# Revit family: Triple_CAVP_with_Mixing_Box
name_source: partatom
category: Mechanical Equipment
units: mm (PartAtom-declared; Revit-internal decimal feet)

## family parameters
Always vertical = Yes
Cut with Voids When Loaded = No
Part Type = Normal
Room Calculation Point = No
Round Connector Dimension = Use Diameter
Shared = No
Work Plane-Based = No

## types (227) — shared parameters
0 = 0"
1" = 1"
1.5 = 1 1/2"
10.1875 = 10 3/16"
135 = 135.00°
2" = 2"
2' = 24"
3" = 3"
4" = 4"
60 = 60.00°
8.1875 = 8 3/16"
85 = 85.00°
F-H = 2"
Manufacturer = Loren Cook Company
Model = Triple_CAVP_with_Mixing_Box
ONE EIGTH = 1/8"
Q = 1"
Q/2 = 1/2"
URL = www.lorencook.com

## per-type parameters (varying)
- Triple_120_CAVP-9L_CLASS_1_With_Mixing_Box: ((M - (2 * (D - L - K - J))) / 2) + (TRANSITION / 2)=9 7/32"; (B/2)+1.5"=9 9/16"; (B/2)-.125"=7 15/16"; (D-J-K-L)*2=2 1/16"; (E/2)-((B/2)+1.5")=3 25/32"; (E/2)-((MB_P/2)+.125")=-9/32"; (E/2)-(E/52*15)=5 21/32"; (F-((F-H)/2))/2=8 3/4"; (M - (2 * (D - L - K - J)))/2=4 11/16"; (MB_P/2)+.125"=13 5/8"; (MB_P/2-.125")+((F / 2) - 2")=-22 1/8"; (MB_P/2-.125")-((F / 2) - 2")=-4 5/8"; (MB_Q/2)+.125"=13 5/8"; (NOZZLE_HEIGHT - (NOZZLE_HEIGHT / 8 * 2)) / 2=10 1/2"; (NOZZLE_WB_OD - NOZZLE_TOP_OD) / 4=2 3/8"; -((MB_Q / 2) + 1/8")=-13 5/8"; -(F-((F-H)/2))/2=-8 3/4"; -MB_HEIGHT=-32"; -MB_P=-27"; -MB_P-.25=-27 1/4"; A=71"; A/2=35 1/2"; B=16 1/8"; B/2=8 1/16"; B/4=4 1/32"; C=43"; C/2=21 1/2"; CLASS=1"; D=32 13/16"; D-L-K-J=1 1/32"; D-M=21 3/8"; DUAL_Q=81 3/8"; DUAL_Q+.25"=81 5/8"; E=26 11/16"; E-(NOZZLE_RAD/3*2)=9 1/16"; E-N-N-H=-56 13/32"; E/2=13 11/32"; E/2-H/2=3 19/32"; E/52*15=7 11/16"; E/52*30=15 13/32"; F=21 1/2"; F/2=10 3/4"; H=19 1/2"; H/2=9 3/4"; HEIGHT=33 21/32"; J=6 1/2"; J+K+L=31 25/32"; K=11 7/8"; L=13 13/32"; M=11 7/16"; M-(2*(D-L-K-J))=9 3/8"; MB_A=89 11/16"; MB_F=9 1/8"; MB_F-3"=6 1/8"; MB_HEIGHT=32"; MB_HEIGHT/2=16"; MB_N=14 3/16"; MB_N-(D-J-K-L)=13 5/32"; MB_P=27"; MB_P+.25"=27 1/4"; MB_P+MB_P+.5=54 1/2"; MB_P-4.5"=22 1/2"; MB_Q=27"; N=60"; N+(H/2)=69 3/4"; NOZZLE_BOTTOM_ID=12 13/16"; NOZZLE_BOTTOM_RAD=6 13/32"; NOZZLE_BOTTOM_RAD-3*2=13/32"; NOZZLE_HEIGHT=28"; NOZZLE_HEIGHT/7*2=7"; NOZZLE_SIZE=9"; NOZZLE_TOP_OD=13 1/2"; NOZZLE_TOP_RAD=6 3/4"; NOZZLE_WB/4=4 19/32"; NOZZLE_WB_OD=23"; NOZZLE_WB_RAD=11 1/2"; NOZZLE_WB_RAD-2"=9 1/2"; P=60"; R=22"; R*1.1=24 3/16"; R+((B/2)+1.5")=31 9/16"; R-((B/2)+1.5")=12 7/16"; RO/2=11 1/4"; RO2/2=65 5/8"; TRANSITION=9 1/16"; TRANSITION/2=4 17/32"; TRIP_Q=135 3/4"; TRIP_Q-4.5"=131 1/4"; Type Comments=Triple Vari-Plume Laboratory Exhaust Centrifugal Airfoil Class 1 Arr 10 With Mixing Box
- Triple_120_CAVP-9H_CLASS_1_With_Mixing_Box: ((M - (2 * (D - L - K - J))) / 2) + (TRANSITION / 2)=9 7/32"; (B/2)+1.5"=9 9/16"; (B/2)-.125"=7 15/16"; (D-J-K-L)*2=2 1/16"; (E/2)-((B/2)+1.5")=3 25/32"; (E/2)-((MB_P/2)+.125")=-9/32"; (E/2)-(E/52*15)=5 21/32"; (F-((F-H)/2))/2=8 3/4"; (M - (2 * (D - L - K - J)))/2=4 11/16"; (MB_P/2)+.125"=13 5/8"; (MB_P/2-.125")+((F / 2) - 2")=-22 1/8"; (MB_P/2-.125")-((F / 2) - 2")=-4 5/8"; (MB_Q/2)+.125"=13 5/8"; (NOZZLE_HEIGHT - (NOZZLE_HEIGHT / 8 * 2)) / 2=10 1/2"; (NOZZLE_WB_OD - NOZZLE_TOP_OD) / 4=2 3/8"; -((MB_Q / 2) + 1/8")=-13 5/8"; -(F-((F-H)/2))/2=-8 3/4"; -MB_HEIGHT=-32"; -MB_P=-27"; -MB_P-.25=-27 1/4"; A=71"; A/2=35 1/2"; B=16 1/8"; B/2=8 1/16"; B/4=4 1/32"; C=43"; C/2=21 1/2"; CLASS=1"; D=32 13/16"; D-L-K-J=1 1/32"; D-M=21 3/8"; DUAL_Q=81 3/8"; DUAL_Q+.25"=81 5/8"; E=26 11/16"; E-(NOZZLE_RAD/3*2)=9 1/16"; E-N-N-H=-56 13/32"; E/2=13 11/32"; E/2-H/2=3 19/32"; E/52*15=7 11/16"; E/52*30=15 13/32"; F=21 1/2"; F/2=10 3/4"; H=19 1/2"; H/2=9 3/4"; HEIGHT=33 21/32"; J=6 1/2"; J+K+L=31 25/32"; K=11 7/8"; L=13 13/32"; M=11 7/16"; M-(2*(D-L-K-J))=9 3/8"; MB_A=89 11/16"; MB_F=9 1/8"; MB_F-3"=6 1/8"; MB_HEIGHT=32"; MB_HEIGHT/2=16"; MB_N=14 3/16"; MB_N-(D-J-K-L)=13 5/32"; MB_P=27"; MB_P+.25"=27 1/4"; MB_P+MB_P+.5=54 1/2"; MB_P-4.5"=22 1/2"; MB_Q=27"; N=60"; N+(H/2)=69 3/4"; NOZZLE_BOTTOM_ID=12 13/16"; NOZZLE_BOTTOM_RAD=6 13/32"; NOZZLE_BOTTOM_RAD-3*2=13/32"; NOZZLE_HEIGHT=28"; NOZZLE_HEIGHT/7*2=7"; NOZZLE_SIZE=9"; NOZZLE_TOP_OD=13 1/2"; NOZZLE_TOP_RAD=6 3/4"; NOZZLE_WB/4=4 19/32"; NOZZLE_WB_OD=23"; NOZZLE_WB_RAD=11 1/2"; NOZZLE_WB_RAD-2"=9 1/2"; P=60"; R=22"; R*1.1=24 3/16"; R+((B/2)+1.5")=31 9/16"; R-((B/2)+1.5")=12 7/16"; RO/2=11 1/4"; RO2/2=65 5/8"; TRANSITION=9 1/16"; TRANSITION/2=4 17/32"; TRIP_Q=135 3/4"; TRIP_Q-4.5"=131 1/4"; Type Comments=Triple Vari-Plume Laboratory Exhaust Centrifugal Airfoil Class 1 Arr 10 With Mixing Box
- Triple_120_CAVP-9L_CLASS_2_With_Mixing_Box: ((M - (2 * (D - L - K - J))) / 2) + (TRANSITION / 2)=8 15/32"; (B/2)+1.5"=9 9/16"; (B/2)-.125"=7 15/16"; (D-J-K-L)*2=3 9/16"; (E/2)-((B/2)+1.5")=3 25/32"; (E/2)-((MB_P/2)+.125")=-9/32"; (E/2)-(E/52*15)=5 21/32"; (F-((F-H)/2))/2=8 3/4"; (M - (2 * (D - L - K - J)))/2=3 15/16"; (MB_P/2)+.125"=13 5/8"; (MB_P/2-.125")+((F / 2) - 2")=-22 1/8"; (MB_P/2-.125")-((F / 2) - 2")=-4 5/8"; (MB_Q/2)+.125"=13 5/8"; (NOZZLE_HEIGHT - (NOZZLE_HEIGHT / 8 * 2)) / 2=10 1/2"; (NOZZLE_WB_OD - NOZZLE_TOP_OD) / 4=2 3/8"; -((MB_Q / 2) + 1/8")=-13 5/8"; -(F-((F-H)/2))/2=-8 3/4"; -MB_HEIGHT=-32"; -MB_P=-27"; -MB_P-.25=-27 1/4"; A=71"; A/2=35 1/2"; B=16 1/8"; B/2=8 1/16"; B/4=4 1/32"; C=43"; C/2=21 1/2"; CLASS=2"; D=36 13/16"; D-L-K-J=1 25/32"; D-M=25 3/8"; DUAL_Q=81 3/8"; DUAL_Q+.25"=81 5/8"; E=26 11/16"; E-(NOZZLE_RAD/3*2)=9 1/16"; E-N-N-H=-56 13/32"; E/2=13 11/32"; E/2-H/2=3 19/32"; E/52*15=7 11/16"; E/52*30=15 13/32"; F=21 1/2"; F/2=10 3/4"; H=19 1/2"; H/2=9 3/4"; HEIGHT=33 21/32"; J=6 1/4"; J+K+L=35 1/32"; K=15 3/8"; L=13 13/32"; M=11 7/16"; M-(2*(D-L-K-J))=7 7/8"; MB_A=86 7/16"; MB_F=9 1/8"; MB_F-3"=6 1/8"; MB_HEIGHT=32"; MB_HEIGHT/2=16"; MB_N=14 3/16"; MB_N-(D-J-K-L)=12 13/32"; MB_P=27"; MB_P+.25"=27 1/4"; MB_P+MB_P+.5=54 1/2"; MB_P-4.5"=22 1/2"; MB_Q=27"; N=60"; N+(H/2)=69 3/4"; NOZZLE_BOTTOM_ID=12 13/16"; NOZZLE_BOTTOM_RAD=6 13/32"; NOZZLE_BOTTOM_RAD-3*2=13/32"; NOZZLE_HEIGHT=28"; NOZZLE_HEIGHT/7*2=7"; NOZZLE_SIZE=9"; NOZZLE_TOP_OD=13 1/2"; NOZZLE_TOP_RAD=6 3/4"; NOZZLE_WB/4=4 19/32"; NOZZLE_WB_OD=23"; NOZZLE_WB_RAD=11 1/2"; NOZZLE_WB_RAD-2"=9 1/2"; P=60"; R=22"; R*1.1=24 3/16"; R+((B/2)+1.5")=31 9/16"; R-((B/2)+1.5")=12 7/16"; RO/2=11 1/4"; RO2/2=65 5/8"; TRANSITION=9 1/16"; TRANSITION/2=4 17/32"; TRIP_Q=135 3/4"; TRIP_Q-4.5"=131 1/4"; Type Comments=Triple Vari-Plume Laboratory Exhaust Centrifugal Airfoil Class 2 Arr 10 With Mixing Box
- Triple_120_CAVP-9H_CLASS_2_With_Mixing_Box: ((M - (2 * (D - L - K - J))) / 2) + (TRANSITION / 2)=8 15/32"; (B/2)+1.5"=9 9/16"; (B/2)-.125"=7 15/16"; (D-J-K-L)*2=3 9/16"; (E/2)-((B/2)+1.5")=3 25/32"; (E/2)-((MB_P/2)+.125")=-9/32"; (E/2)-(E/52*15)=5 21/32"; (F-((F-H)/2))/2=8 3/4"; (M - (2 * (D - L - K - J)))/2=3 15/16"; (MB_P/2)+.125"=13 5/8"; (MB_P/2-.125")+((F / 2) - 2")=-22 1/8"; (MB_P/2-.125")-((F / 2) - 2")=-4 5/8"; (MB_Q/2)+.125"=13 5/8"; (NOZZLE_HEIGHT - (NOZZLE_HEIGHT / 8 * 2)) / 2=10 1/2"; (NOZZLE_WB_OD - NOZZLE_TOP_OD) / 4=2 3/8"; -((MB_Q / 2) + 1/8")=-13 5/8"; -(F-((F-H)/2))/2=-8 3/4"; -MB_HEIGHT=-32"; -MB_P=-27"; -MB_P-.25=-27 1/4"; A=71"; A/2=35 1/2"; B=16 1/8"; B/2=8 1/16"; B/4=4 1/32"; C=43"; C/2=21 1/2"; CLASS=2"; D=36 13/16"; D-L-K-J=1 25/32"; D-M=25 3/8"; DUAL_Q=81 3/8"; DUAL_Q+.25"=81 5/8"; E=26 11/16"; E-(NOZZLE_RAD/3*2)=9 1/16"; E-N-N-H=-56 13/32"; E/2=13 11/32"; E/2-H/2=3 19/32"; E/52*15=7 11/16"; E/52*30=15 13/32"; F=21 1/2"; F/2=10 3/4"; H=19 1/2"; H/2=9 3/4"; HEIGHT=33 21/32"; J=6 1/4"; J+K+L=35 1/32"; K=15 3/8"; L=13 13/32"; M=11 7/16"; M-(2*(D-L-K-J))=7 7/8"; MB_A=86 7/16"; MB_F=9 1/8"; MB_F-3"=6 1/8"; MB_HEIGHT=32"; MB_HEIGHT/2=16"; MB_N=14 3/16"; MB_N-(D-J-K-L)=12 13/32"; MB_P=27"; MB_P+.25"=27 1/4"; MB_P+MB_P+.5=54 1/2"; MB_P-4.5"=22 1/2"; MB_Q=27"; N=60"; N+(H/2)=69 3/4"; NOZZLE_BOTTOM_ID=12 13/16"; NOZZLE_BOTTOM_RAD=6 13/32"; NOZZLE_BOTTOM_RAD-3*2=13/32"; NOZZLE_HEIGHT=28"; NOZZLE_HEIGHT/7*2=7"; NOZZLE_SIZE=9"; NOZZLE_TOP_OD=13 1/2"; NOZZLE_TOP_RAD=6 3/4"; NOZZLE_WB/4=4 19/32"; NOZZLE_WB_OD=23"; NOZZLE_WB_RAD=11 1/2"; NOZZLE_WB_RAD-2"=9 1/2"; P=60"; R=22"; R*1.1=24 3/16"; R+((B/2)+1.5")=31 9/16"; R-((B/2)+1.5")=12 7/16"; RO/2=11 1/4"; RO2/2=65 5/8"; TRANSITION=9 1/16"; TRANSITION/2=4 17/32"; TRIP_Q=135 3/4"; TRIP_Q-4.5"=131 1/4"; Type Comments=Triple Vari-Plume Laboratory Exhaust Centrifugal Airfoil Class 2 Arr 10 With Mixing Box
- Triple_135_CAVP-9L_CLASS_1_With_Mixing_Box: ((M - (2 * (D - L - K - J))) / 2) + (TRANSITION / 2)=9 25/32"; (B/2)+1.5"=10 5/16"; (B/2)-.125"=8 11/16"; (D-J-K-L)*2=2 1/16"; (E/2)-((B/2)+1.5")=4 19/32"; (E/2)-((MB_P/2)+.125")=9/32"; (E/2)-(E/52*15)=6 5/16"; (F-((F-H)/2))/2=8 3/4"; (M - (2 * (D - L - K - J)))/2=5 1/4"; (MB_P/2)+.125"=14 5/8"; (MB_P/2-.125")+((F / 2) - 2")=-23 1/8"; (MB_P/2-.125")-((F / 2) - 2")=-5 5/8"; (MB_Q/2)+.125"=14 5/8"; (NOZZLE_HEIGHT - (NOZZLE_HEIGHT / 8 * 2)) / 2=10 1/2"; (NOZZLE_WB_OD - NOZZLE_TOP_OD) / 4=2 3/8"; -((MB_Q / 2) + 1/8")=-14 5/8"; -(F-((F-H)/2))/2=-8 3/4"; -MB_HEIGHT=-33 1/2"; -MB_P=-29"; -MB_P-.25=-29 1/4"; A=73 11/16"; A/2=36 27/32"; B=17 5/8"; B/2=8 13/16"; B/4=4 13/32"; C=45 11/16"; C/2=22 27/32"; CLASS=1"; D=34 5/16"; D-L-K-J=1 1/32"; D-M=21 3/4"; DUAL_Q=87 3/8"; DUAL_Q+.25"=87 5/8"; E=29 13/16"; E-(NOZZLE_RAD/3*2)=10 5/8"; E-N-N-H=-54 27/32"; E/2=14 29/32"; E/2-H/2=5 5/32"; E/52*15=8 19/32"; E/52*30=17 3/16"; F=21 1/2"; F/2=10 3/4"; H=19 1/2"; H/2=9 3/4"; HEIGHT=35 1/32"; J=6 1/2"; J+K+L=33 9/32"; K=12 1/4"; L=14 17/32"; M=12 9/16"; M-(2*(D-L-K-J))=10 1/2"; MB_A=90 13/16"; MB_F=8 3/8"; MB_F-3"=5 3/8"; MB_HEIGHT=33 1/2"; MB_HEIGHT/2=16 3/4"; MB_N=14 3/16"; MB_N-(D-J-K-L)=13 5/32"; MB_P=29"; MB_P+.25"=29 1/4"; MB_P+MB_P+.5=58 1/2"; MB_P-4.5"=24 1/2"; MB_Q=29"; N=60"; N+(H/2)=69 3/4"; NOZZLE_BOTTOM_ID=12 13/16"; NOZZLE_BOTTOM_RAD=6 13/32"; NOZZLE_BOTTOM_RAD-3*2=13/32"; NOZZLE_HEIGHT=28"; NOZZLE_HEIGHT/7*2=7"; NOZZLE_SIZE=9"; NOZZLE_TOP_OD=13 1/2"; NOZZLE_TOP_RAD=6 3/4"; NOZZLE_WB/4=4 19/32"; NOZZLE_WB_OD=23"; NOZZLE_WB_RAD=11 1/2"; NOZZLE_WB_RAD-2"=9 1/2"; P=60"; R=22"; R*1.1=24 3/16"; R+((B/2)+1.5")=32 5/16"; R-((B/2)+1.5")=11 11/16"; RO/2=12 1/4"; RO2/2=70 5/8"; TRANSITION=9 1/16"; TRANSITION/2=4 17/32"; TRIP_Q=145 3/4"; TRIP_Q-4.5"=141 1/4"; Type Comments=Triple Vari-Plume Laboratory Exhaust Centrifugal Airfoil Class 1 Arr 10 With Mixing Box
- Triple_135_CAVP-9H_CLASS_1_With_Mixing_Box: ((M - (2 * (D - L - K - J))) / 2) + (TRANSITION / 2)=9 25/32"; (B/2)+1.5"=10 5/16"; (B/2)-.125"=8 11/16"; (D-J-K-L)*2=2 1/16"; (E/2)-((B/2)+1.5")=4 19/32"; (E/2)-((MB_P/2)+.125")=9/32"; (E/2)-(E/52*15)=6 5/16"; (F-((F-H)/2))/2=8 3/4"; (M - (2 * (D - L - K - J)))/2=5 1/4"; (MB_P/2)+.125"=14 5/8"; (MB_P/2-.125")+((F / 2) - 2")=-23 1/8"; (MB_P/2-.125")-((F / 2) - 2")=-5 5/8"; (MB_Q/2)+.125"=14 5/8"; (NOZZLE_HEIGHT - (NOZZLE_HEIGHT / 8 * 2)) / 2=10 1/2"; (NOZZLE_WB_OD - NOZZLE_TOP_OD) / 4=2 3/8"; -((MB_Q / 2) + 1/8")=-14 5/8"; -(F-((F-H)/2))/2=-8 3/4"; -MB_HEIGHT=-33 1/2"; -MB_P=-29"; -MB_P-.25=-29 1/4"; A=73 11/16"; A/2=36 27/32"; B=17 5/8"; B/2=8 13/16"; B/4=4 13/32"; C=45 11/16"; C/2=22 27/32"; CLASS=1"; D=34 5/16"; D-L-K-J=1 1/32"; D-M=21 3/4"; DUAL_Q=87 3/8"; DUAL_Q+.25"=87 5/8"; E=29 13/16"; E-(NOZZLE_RAD/3*2)=10 5/8"; E-N-N-H=-54 27/32"; E/2=14 29/32"; E/2-H/2=5 5/32"; E/52*15=8 19/32"; E/52*30=17 3/16"; F=21 1/2"; F/2=10 3/4"; H=19 1/2"; H/2=9 3/4"; HEIGHT=35 1/32"; J=6 1/2"; J+K+L=33 9/32"; K=12 1/4"; L=14 17/32"; M=12 9/16"; M-(2*(D-L-K-J))=10 1/2"; MB_A=90 13/16"; MB_F=8 3/8"; MB_F-3"=5 3/8"; MB_HEIGHT=33 1/2"; MB_HEIGHT/2=16 3/4"; MB_N=14 3/16"; MB_N-(D-J-K-L)=13 5/32"; MB_P=29"; MB_P+.25"=29 1/4"; MB_P+MB_P+.5=58 1/2"; MB_P-4.5"=24 1/2"; MB_Q=29"; N=60"; N+(H/2)=69 3/4"; NOZZLE_BOTTOM_ID=12 13/16"; NOZZLE_BOTTOM_RAD=6 13/32"; NOZZLE_BOTTOM_RAD-3*2=13/32"; NOZZLE_HEIGHT=28"; NOZZLE_HEIGHT/7*2=7"; NOZZLE_SIZE=9"; NOZZLE_TOP_OD=13 1/2"; NOZZLE_TOP_RAD=6 3/4"; NOZZLE_WB/4=4 19/32"; NOZZLE_WB_OD=23"; NOZZLE_WB_RAD=11 1/2"; NOZZLE_WB_RAD-2"=9 1/2"; P=60"; R=22"; R*1.1=24 3/16"; R+((B/2)+1.5")=32 5/16"; R-((B/2)+1.5")=11 11/16"; RO/2=12 1/4"; RO2/2=70 5/8"; TRANSITION=9 1/16"; TRANSITION/2=4 17/32"; TRIP_Q=145 3/4"; TRIP_Q-4.5"=141 1/4"; Type Comments=Triple Vari-Plume Laboratory Exhaust Centrifugal Airfoil Class 1 Arr 10 With Mixing Box
- Triple_135_CAVP-9L_CLASS_2_With_Mixing_Box: ((M - (2 * (D - L - K - J))) / 2) + (TRANSITION / 2)=9 25/32"; (B/2)+1.5"=10 5/16"; (B/2)-.125"=8 11/16"; (D-J-K-L)*2=2 1/16"; (E/2)-((B/2)+1.5")=4 19/32"; (E/2)-((MB_P/2)+.125")=9/32"; (E/2)-(E/52*15)=6 5/16"; (F-((F-H)/2))/2=8 3/4"; (M - (2 * (D - L - K - J)))/2=5 1/4"; (MB_P/2)+.125"=14 5/8"; (MB_P/2-.125")+((F / 2) - 2")=-23 1/8"; (MB_P/2-.125")-((F / 2) - 2")=-5 5/8"; (MB_Q/2)+.125"=14 5/8"; (NOZZLE_HEIGHT - (NOZZLE_HEIGHT / 8 * 2)) / 2=10 1/2"; (NOZZLE_WB_OD - NOZZLE_TOP_OD) / 4=2 3/8"; -((MB_Q / 2) + 1/8")=-14 5/8"; -(F-((F-H)/2))/2=-8 3/4"; -MB_HEIGHT=-33 1/2"; -MB_P=-29"; -MB_P-.25=-29 1/4"; A=73 11/16"; A/2=36 27/32"; B=17 5/8"; B/2=8 13/16"; B/4=4 13/32"; C=45 11/16"; C/2=22 27/32"; CLASS=2"; D=37 3/16"; D-L-K-J=1 1/32"; D-M=24 5/8"; DUAL_Q=87 3/8"; DUAL_Q+.25"=87 5/8"; E=29 13/16"; E-(NOZZLE_RAD/3*2)=10 5/8"; E-N-N-H=-54 27/32"; E/2=14 29/32"; E/2-H/2=5 5/32"; E/52*15=8 19/32"; E/52*30=17 3/16"; F=21 1/2"; F/2=10 3/4"; H=19 1/2"; H/2=9 3/4"; HEIGHT=35 1/32"; J=6 1/4"; J+K+L=36 5/32"; K=15 3/8"; L=14 17/32"; M=12 9/16"; M-(2*(D-L-K-J))=10 1/2"; MB_A=93 11/16"; MB_F=8 3/8"; MB_F-3"=5 3/8"; MB_HEIGHT=33 1/2"; MB_HEIGHT/2=16 3/4"; MB_N=14 3/16"; MB_N-(D-J-K-L)=13 5/32"; MB_P=29"; MB_P+.25"=29 1/4"; MB_P+MB_P+.5=58 1/2"; MB_P-4.5"=24 1/2"; MB_Q=29"; N=60"; N+(H/2)=69 3/4"; NOZZLE_BOTTOM_ID=12 13/16"; NOZZLE_BOTTOM_RAD=6 13/32"; NOZZLE_BOTTOM_RAD-3*2=13/32"; NOZZLE_HEIGHT=28"; NOZZLE_HEIGHT/7*2=7"; NOZZLE_SIZE=9"; NOZZLE_TOP_OD=13 1/2"; NOZZLE_TOP_RAD=6 3/4"; NOZZLE_WB/4=4 19/32"; NOZZLE_WB_OD=23"; NOZZLE_WB_RAD=11 1/2"; NOZZLE_WB_RAD-2"=9 1/2"; P=60"; R=22"; R*1.1=24 3/16"; R+((B/2)+1.5")=32 5/16"; R-((B/2)+1.5")=11 11/16"; RO/2=12 1/4"; RO2/2=70 5/8"; TRANSITION=9 1/16"; TRANSITION/2=4 17/32"; TRIP_Q=145 3/4"; TRIP_Q-4.5"=141 1/4"; Type Comments=Triple Vari-Plume Laboratory Exhaust Centrifugal Airfoil Class 2 Arr 10 With Mixing Box
- Triple_135_CAVP-9H_CLASS_2_With_Mixing_Box: ((M - (2 * (D - L - K - J))) / 2) + (TRANSITION / 2)=9 25/32"; (B/2)+1.5"=10 5/16"; (B/2)-.125"=8 11/16"; (D-J-K-L)*2=2 1/16"; (E/2)-((B/2)+1.5")=4 19/32"; (E/2)-((MB_P/2)+.125")=9/32"; (E/2)-(E/52*15)=6 5/16"; (F-((F-H)/2))/2=8 3/4"; (M - (2 * (D - L - K - J)))/2=5 1/4"; (MB_P/2)+.125"=14 5/8"; (MB_P/2-.125")+((F / 2) - 2")=-23 1/8"; (MB_P/2-.125")-((F / 2) - 2")=-5 5/8"; (MB_Q/2)+.125"=14 5/8"; (NOZZLE_HEIGHT - (NOZZLE_HEIGHT / 8 * 2)) / 2=10 1/2"; (NOZZLE_WB_OD - NOZZLE_TOP_OD) / 4=2 3/8"; -((MB_Q / 2) + 1/8")=-14 5/8"; -(F-((F-H)/2))/2=-8 3/4"; -MB_HEIGHT=-33 1/2"; -MB_P=-29"; -MB_P-.25=-29 1/4"; A=73 11/16"; A/2=36 27/32"; B=17 5/8"; B/2=8 13/16"; B/4=4 13/32"; C=45 11/16"; C/2=22 27/32"; CLASS=2"; D=37 3/16"; D-L-K-J=1 1/32"; D-M=24 5/8"; DUAL_Q=87 3/8"; DUAL_Q+.25"=87 5/8"; E=29 13/16"; E-(NOZZLE_RAD/3*2)=10 5/8"; E-N-N-H=-54 27/32"; E/2=14 29/32"; E/2-H/2=5 5/32"; E/52*15=8 19/32"; E/52*30=17 3/16"; F=21 1/2"; F/2=10 3/4"; H=19 1/2"; H/2=9 3/4"; HEIGHT=35 1/32"; J=6 1/4"; J+K+L=36 5/32"; K=15 3/8"; L=14 17/32"; M=12 9/16"; M-(2*(D-L-K-J))=10 1/2"; MB_A=93 11/16"; MB_F=8 3/8"; MB_F-3"=5 3/8"; MB_HEIGHT=33 1/2"; MB_HEIGHT/2=16 3/4"; MB_N=14 3/16"; MB_N-(D-J-K-L)=13 5/32"; MB_P=29"; MB_P+.25"=29 1/4"; MB_P+MB_P+.5=58 1/2"; MB_P-4.5"=24 1/2"; MB_Q=29"; N=60"; N+(H/2)=69 3/4"; NOZZLE_BOTTOM_ID=12 13/16"; NOZZLE_BOTTOM_RAD=6 13/32"; NOZZLE_BOTTOM_RAD-3*2=13/32"; NOZZLE_HEIGHT=28"; NOZZLE_HEIGHT/7*2=7"; NOZZLE_SIZE=9"; NOZZLE_TOP_OD=13 1/2"; NOZZLE_TOP_RAD=6 3/4"; NOZZLE_WB/4=4 19/32"; NOZZLE_WB_OD=23"; NOZZLE_WB_RAD=11 1/2"; NOZZLE_WB_RAD-2"=9 1/2"; P=60"; R=22"; R*1.1=24 3/16"; R+((B/2)+1.5")=32 5/16"; R-((B/2)+1.5")=11 11/16"; RO/2=12 1/4"; RO2/2=70 5/8"; TRANSITION=9 1/16"; TRANSITION/2=4 17/32"; TRIP_Q=145 3/4"; TRIP_Q-4.5"=141 1/4"; Type Comments=Triple Vari-Plume Laboratory Exhaust Centrifugal Airfoil Class 2 Arr 10 With Mixing Box
- Triple_150_CAVP-9L_CLASS_1_With_Mixing_Box: ((M - (2 * (D - L - K - J))) / 2) + (TRANSITION / 2)=10 11/32"; (B/2)+1.5"=11 1/16"; (B/2)-.125"=9 7/16"; (D-J-K-L)*2=2 1/16"; (E/2)-((B/2)+1.5")=5 3/8"; (E/2)-((MB_P/2)+.125")=1 5/16"; (E/2)-(E/52*15)=6 31/32"; (F-((F-H)/2))/2=8 3/4"; (M - (2 * (D - L - K - J)))/2=5 13/16"; (MB_P/2)+.125"=15 1/8"; (MB_P/2-.125")+((F / 2) - 2")=-23 5/8"; (MB_P/2-.125")-((F / 2) - 2")=-6 1/8"; (MB_Q/2)+.125"=15 1/8"; (NOZZLE_HEIGHT - (NOZZLE_HEIGHT / 8 * 2)) / 2=10 1/2"; (NOZZLE_WB_OD - NOZZLE_TOP_OD) / 4=2 3/8"; -((MB_Q / 2) + 1/8")=-15 1/8"; -(F-((F-H)/2))/2=-8 3/4"; -MB_HEIGHT=-35"; -MB_P=-30"; -MB_P-.25=-30 1/4"; A=78"; A/2=39"; B=19 1/8"; B/2=9 9/16"; B/4=4 25/32"; C=46 3/4"; C/2=23 3/8"; CLASS=1"; D=35 7/16"; D-L-K-J=1 1/32"; D-M=21 3/4"; DUAL_Q=90 3/8"; DUAL_Q+.25"=90 5/8"; E=32 7/8"; E-(NOZZLE_RAD/3*2)=12 5/32"; E-N-N-H=-53 5/16"; E/2=16 7/16"; E/2-H/2=6 11/16"; E/52*15=9 15/32"; E/52*30=18 31/32"; F=21 1/2"; F/2=10 3/4"; H=19 1/2"; H/2=9 3/4"; HEIGHT=36 11/32"; J=6 1/2"; J+K+L=34 13/32"; K=12 1/4"; L=15 21/32"; M=13 11/16"; M-(2*(D-L-K-J))=11 5/8"; MB_A=94 3/16"; MB_F=7 5/8"; MB_F-3"=4 5/8"; MB_HEIGHT=35"; MB_HEIGHT/2=17 1/2"; MB_N=14 3/16"; MB_N-(D-J-K-L)=13 5/32"; MB_P=30"; MB_P+.25"=30 1/4"; MB_P+MB_P+.5=60 1/2"; MB_P-4.5"=25 1/2"; MB_Q=30"; N=60"; N+(H/2)=69 3/4"; NOZZLE_BOTTOM_ID=12 13/16"; NOZZLE_BOTTOM_RAD=6 13/32"; NOZZLE_BOTTOM_RAD-3*2=13/32"; NOZZLE_HEIGHT=28"; NOZZLE_HEIGHT/7*2=7"; NOZZLE_SIZE=9"; NOZZLE_TOP_OD=13 1/2"; NOZZLE_TOP_RAD=6 3/4"; NOZZLE_WB/4=4 19/32"; NOZZLE_WB_OD=23"; NOZZLE_WB_RAD=11 1/2"; NOZZLE_WB_RAD-2"=9 1/2"; P=60"; R=22"; R*1.1=24 3/16"; R+((B/2)+1.5")=33 1/16"; R-((B/2)+1.5")=10 15/16"; RO/2=12 3/4"; RO2/2=73 1/8"; TRANSITION=9 1/16"; TRANSITION/2=4 17/32"; TRIP_Q=150 3/4"; TRIP_Q-4.5"=146 1/4"; Type Comments=Triple Vari-Plume Laboratory Exhaust Centrifugal Airfoil Class 1 Arr 10 With Mixing Box
- Triple_150_CAVP-9H_CLASS_1_With_Mixing_Box: ((M - (2 * (D - L - K - J))) / 2) + (TRANSITION / 2)=10 11/32"; (B/2)+1.5"=11 1/16"; (B/2)-.125"=9 7/16"; (D-J-K-L)*2=2 1/16"; (E/2)-((B/2)+1.5")=5 3/8"; (E/2)-((MB_P/2)+.125")=1 5/16"; (E/2)-(E/52*15)=6 31/32"; (F-((F-H)/2))/2=8 3/4"; (M - (2 * (D - L - K - J)))/2=5 13/16"; (MB_P/2)+.125"=15 1/8"; (MB_P/2-.125")+((F / 2) - 2")=-23 5/8"; (MB_P/2-.125")-((F / 2) - 2")=-6 1/8"; (MB_Q/2)+.125"=15 1/8"; (NOZZLE_HEIGHT - (NOZZLE_HEIGHT / 8 * 2)) / 2=10 1/2"; (NOZZLE_WB_OD - NOZZLE_TOP_OD) / 4=2 3/8"; -((MB_Q / 2) + 1/8")=-15 1/8"; -(F-((F-H)/2))/2=-8 3/4"; -MB_HEIGHT=-35"; -MB_P=-30"; -MB_P-.25=-30 1/4"; A=78"; A/2=39"; B=19 1/8"; B/2=9 9/16"; B/4=4 25/32"; C=46 3/4"; C/2=23 3/8"; CLASS=1"; D=35 7/16"; D-L-K-J=1 1/32"; D-M=21 3/4"; DUAL_Q=90 3/8"; DUAL_Q+.25"=90 5/8"; E=32 7/8"; E-(NOZZLE_RAD/3*2)=12 5/32"; E-N-N-H=-53 5/16"; E/2=16 7/16"; E/2-H/2=6 11/16"; E/52*15=9 15/32"; E/52*30=18 31/32"; F=21 1/2"; F/2=10 3/4"; H=19 1/2"; H/2=9 3/4"; HEIGHT=36 11/32"; J=6 1/2"; J+K+L=34 13/32"; K=12 1/4"; L=15 21/32"; M=13 11/16"; M-(2*(D-L-K-J))=11 5/8"; MB_A=94 3/16"; MB_F=7 5/8"; MB_F-3"=4 5/8"; MB_HEIGHT=35"; MB_HEIGHT/2=17 1/2"; MB_N=14 3/16"; MB_N-(D-J-K-L)=13 5/32"; MB_P=30"; MB_P+.25"=30 1/4"; MB_P+MB_P+.5=60 1/2"; MB_P-4.5"=25 1/2"; MB_Q=30"; N=60"; N+(H/2)=69 3/4"; NOZZLE_BOTTOM_ID=12 13/16"; NOZZLE_BOTTOM_RAD=6 13/32"; NOZZLE_BOTTOM_RAD-3*2=13/32"; NOZZLE_HEIGHT=28"; NOZZLE_HEIGHT/7*2=7"; NOZZLE_SIZE=9"; NOZZLE_TOP_OD=13 1/2"; NOZZLE_TOP_RAD=6 3/4"; NOZZLE_WB/4=4 19/32"; NOZZLE_WB_OD=23"; NOZZLE_WB_RAD=11 1/2"; NOZZLE_WB_RAD-2"=9 1/2"; P=60"; R=22"; R*1.1=24 3/16"; R+((B/2)+1.5")=33 1/16"; R-((B/2)+1.5")=10 15/16"; RO/2=12 3/4"; RO2/2=73 1/8"; TRANSITION=9 1/16"; TRANSITION/2=4 17/32"; TRIP_Q=150 3/4"; TRIP_Q-4.5"=146 1/4"; Type Comments=Triple Vari-Plume Laboratory Exhaust Centrifugal Airfoil Class 1 Arr 10 With Mixing Box
- Triple_150_CAVP-9L_CLASS_2_With_Mixing_Box: ((M - (2 * (D - L - K - J))) / 2) + (TRANSITION / 2)=10 11/32"; (B/2)+1.5"=11 1/16"; (B/2)-.125"=9 7/16"; (D-J-K-L)*2=2 1/16"; (E/2)-((B/2)+1.5")=5 3/8"; (E/2)-((MB_P/2)+.125")=1 5/16"; (E/2)-(E/52*15)=6 31/32"; (F-((F-H)/2))/2=8 3/4"; (M - (2 * (D - L - K - J)))/2=5 13/16"; (MB_P/2)+.125"=15 1/8"; (MB_P/2-.125")+((F / 2) - 2")=-23 5/8"; (MB_P/2-.125")-((F / 2) - 2")=-6 1/8"; (MB_Q/2)+.125"=15 1/8"; (NOZZLE_HEIGHT - (NOZZLE_HEIGHT / 8 * 2)) / 2=10 1/2"; (NOZZLE_WB_OD - NOZZLE_TOP_OD) / 4=2 3/8"; -((MB_Q / 2) + 1/8")=-15 1/8"; -(F-((F-H)/2))/2=-8 3/4"; -MB_HEIGHT=-35"; -MB_P=-30"; -MB_P-.25=-30 1/4"; A=78"; A/2=39"; B=19 1/8"; B/2=9 9/16"; B/4=4 25/32"; C=46 3/4"; C/2=23 3/8"; CLASS=2"; D=38 5/16"; D-L-K-J=1 1/32"; D-M=24 5/8"; DUAL_Q=90 3/8"; DUAL_Q+.25"=90 5/8"; E=32 7/8"; E-(NOZZLE_RAD/3*2)=12 5/32"; E-N-N-H=-53 5/16"; E/2=16 7/16"; E/2-H/2=6 11/16"; E/52*15=9 15/32"; E/52*30=18 31/32"; F=21 1/2"; F/2=10 3/4"; H=19 1/2"; H/2=9 3/4"; HEIGHT=36 11/32"; J=6 1/4"; J+K+L=37 9/32"; K=15 3/8"; L=15 21/32"; M=13 11/16"; M-(2*(D-L-K-J))=11 5/8"; MB_A=97 1/16"; MB_F=7 5/8"; MB_F-3"=4 5/8"; MB_HEIGHT=35"; MB_HEIGHT/2=17 1/2"; MB_N=14 3/16"; MB_N-(D-J-K-L)=13 5/32"; MB_P=30"; MB_P+.25"=30 1/4"; MB_P+MB_P+.5=60 1/2"; MB_P-4.5"=25 1/2"; MB_Q=30"; N=60"; N+(H/2)=69 3/4"; NOZZLE_BOTTOM_ID=12 13/16"; NOZZLE_BOTTOM_RAD=6 13/32"; NOZZLE_BOTTOM_RAD-3*2=13/32"; NOZZLE_HEIGHT=28"; NOZZLE_HEIGHT/7*2=7"; NOZZLE_SIZE=9"; NOZZLE_TOP_OD=13 1/2"; NOZZLE_TOP_RAD=6 3/4"; NOZZLE_WB/4=4 19/32"; NOZZLE_WB_OD=23"; NOZZLE_WB_RAD=11 1/2"; NOZZLE_WB_RAD-2"=9 1/2"; P=60"; R=22"; R*1.1=24 3/16"; R+((B/2)+1.5")=33 1/16"; R-((B/2)+1.5")=10 15/16"; RO/2=12 3/4"; RO2/2=73 1/8"; TRANSITION=9 1/16"; TRANSITION/2=4 17/32"; TRIP_Q=150 3/4"; TRIP_Q-4.5"=146 1/4"; Type Comments=Triple Vari-Plume Laboratory Exhaust Centrifugal Airfoil Class 2 Arr 10 With Mixing Box
- Triple_150_CAVP-9H_CLASS_2_With_Mixing_Box: ((M - (2 * (D - L - K - J))) / 2) + (TRANSITION / 2)=10 11/32"; (B/2)+1.5"=11 1/16"; (B/2)-.125"=9 7/16"; (D-J-K-L)*2=2 1/16"; (E/2)-((B/2)+1.5")=5 3/8"; (E/2)-((MB_P/2)+.125")=1 5/16"; (E/2)-(E/52*15)=6 31/32"; (F-((F-H)/2))/2=8 3/4"; (M - (2 * (D - L - K - J)))/2=5 13/16"; (MB_P/2)+.125"=15 1/8"; (MB_P/2-.125")+((F / 2) - 2")=-23 5/8"; (MB_P/2-.125")-((F / 2) - 2")=-6 1/8"; (MB_Q/2)+.125"=15 1/8"; (NOZZLE_HEIGHT - (NOZZLE_HEIGHT / 8 * 2)) / 2=10 1/2"; (NOZZLE_WB_OD - NOZZLE_TOP_OD) / 4=2 3/8"; -((MB_Q / 2) + 1/8")=-15 1/8"; -(F-((F-H)/2))/2=-8 3/4"; -MB_HEIGHT=-35"; -MB_P=-30"; -MB_P-.25=-30 1/4"; A=78"; A/2=39"; B=19 1/8"; B/2=9 9/16"; B/4=4 25/32"; C=46 3/4"; C/2=23 3/8"; CLASS=2"; D=38 5/16"; D-L-K-J=1 1/32"; D-M=24 5/8"; DUAL_Q=90 3/8"; DUAL_Q+.25"=90 5/8"; E=32 7/8"; E-(NOZZLE_RAD/3*2)=12 5/32"; E-N-N-H=-53 5/16"; E/2=16 7/16"; E/2-H/2=6 11/16"; E/52*15=9 15/32"; E/52*30=18 31/32"; F=21 1/2"; F/2=10 3/4"; H=19 1/2"; H/2=9 3/4"; HEIGHT=36 11/32"; J=6 1/4"; J+K+L=37 9/32"; K=15 3/8"; L=15 21/32"; M=13 11/16"; M-(2*(D-L-K-J))=11 5/8"; MB_A=97 1/16"; MB_F=7 5/8"; MB_F-3"=4 5/8"; MB_HEIGHT=35"; MB_HEIGHT/2=17 1/2"; MB_N=14 3/16"; MB_N-(D-J-K-L)=13 5/32"; MB_P=30"; MB_P+.25"=30 1/4"; MB_P+MB_P+.5=60 1/2"; MB_P-4.5"=25 1/2"; MB_Q=30"; N=60"; N+(H/2)=69 3/4"; NOZZLE_BOTTOM_ID=12 13/16"; NOZZLE_BOTTOM_RAD=6 13/32"; NOZZLE_BOTTOM_RAD-3*2=13/32"; NOZZLE_HEIGHT=28"; NOZZLE_HEIGHT/7*2=7"; NOZZLE_SIZE=9"; NOZZLE_TOP_OD=13 1/2"; NOZZLE_TOP_RAD=6 3/4"; NOZZLE_WB/4=4 19/32"; NOZZLE_WB_OD=23"; NOZZLE_WB_RAD=11 1/2"; NOZZLE_WB_RAD-2"=9 1/2"; P=60"; R=22"; R*1.1=24 3/16"; R+((B/2)+1.5")=33 1/16"; R-((B/2)+1.5")=10 15/16"; RO/2=12 3/4"; RO2/2=73 1/8"; TRANSITION=9 1/16"; TRANSITION/2=4 17/32"; TRIP_Q=150 3/4"; TRIP_Q-4.5"=146 1/4"; Type Comments=Triple Vari-Plume Laboratory Exhaust Centrifugal Airfoil Class 2 Arr 10 With Mixing Box
- Triple_150_CAVP-12H_CLASS_2_With_Mixing_Box: ((M - (2 * (D - L - K - J))) / 2) + (TRANSITION / 2)=11 27/32"; (B/2)+1.5"=11 1/16"; (B/2)-.125"=9 7/16"; (D-J-K-L)*2=2 1/16"; (E/2)-((B/2)+1.5")=5 3/8"; (E/2)-((MB_P/2)+.125")=1 5/16"; (E/2)-(E/52*15)=6 31/32"; (F-((F-H)/2))/2=8 3/4"; (M - (2 * (D - L - K - J)))/2=5 13/16"; (MB_P/2)+.125"=15 1/8"; (MB_P/2-.125")+((F / 2) - 2")=-23 5/8"; (MB_P/2-.125")-((F / 2) - 2")=-6 1/8"; (MB_Q/2)+.125"=15 1/8"; (NOZZLE_HEIGHT - (NOZZLE_HEIGHT / 8 * 2)) / 2=12"; (NOZZLE_WB_OD - NOZZLE_TOP_OD) / 4=2 1/8"; -((MB_Q / 2) + 1/8")=-15 1/8"; -(F-((F-H)/2))/2=-8 3/4"; -MB_HEIGHT=-35"; -MB_P=-30"; -MB_P-.25=-30 1/4"; A=78"; A/2=39"; B=19 1/8"; B/2=9 9/16"; B/4=4 25/32"; C=46 3/4"; C/2=23 3/8"; CLASS=2"; D=38 5/16"; D-L-K-J=1 1/32"; D-M=24 5/8"; DUAL_Q=90 3/8"; DUAL_Q+.25"=90 5/8"; E=32 7/8"; E-(NOZZLE_RAD/3*2)=10 3/4"; E-N-N-H=-53 5/16"; E/2=16 7/16"; E/2-H/2=6 11/16"; E/52*15=9 15/32"; E/52*30=18 31/32"; F=21 1/2"; F/2=10 3/4"; H=19 1/2"; H/2=9 3/4"; HEIGHT=36 11/32"; J=6 1/4"; J+K+L=37 9/32"; K=15 3/8"; L=15 21/32"; M=13 11/16"; M-(2*(D-L-K-J))=11 5/8"; MB_A=97 1/16"; MB_F=7 5/8"; MB_F-3"=4 5/8"; MB_HEIGHT=35"; MB_HEIGHT/2=17 1/2"; MB_N=14 3/16"; MB_N-(D-J-K-L)=13 5/32"; MB_P=30"; MB_P+.25"=30 1/4"; MB_P+MB_P+.5=60 1/2"; MB_P-4.5"=25 1/2"; MB_Q=30"; N=60"; N+(H/2)=69 3/4"; NOZZLE_BOTTOM_ID=17 1/16"; NOZZLE_BOTTOM_RAD=8 17/32"; NOZZLE_BOTTOM_RAD-3*2=2 17/32"; NOZZLE_HEIGHT=32"; NOZZLE_HEIGHT/7*2=8"; NOZZLE_SIZE=12"; NOZZLE_TOP_OD=19 1/2"; NOZZLE_TOP_RAD=9 3/4"; NOZZLE_WB/4=5 19/32"; NOZZLE_WB_OD=28"; NOZZLE_WB_RAD=14"; NOZZLE_WB_RAD-2"=12"; P=60"; R=22"; R*1.1=24 3/16"; R+((B/2)+1.5")=33 1/16"; R-((B/2)+1.5")=10 15/16"; RO/2=12 3/4"; RO2/2=73 1/8"; TRANSITION=12 1/16"; TRANSITION/2=6 1/32"; TRIP_Q=150 3/4"; TRIP_Q-4.5"=146 1/4"; Type Comments=Triple Vari-Plume Laboratory Exhaust Centrifugal Airfoil Class 2 Arr 10 With Mixing Box
- Triple_150_CAVP-12L_CLASS_2_With_Mixing_Box: ((M - (2 * (D - L - K - J))) / 2) + (TRANSITION / 2)=11 27/32"; (B/2)+1.5"=11 1/16"; (B/2)-.125"=9 7/16"; (D-J-K-L)*2=2 1/16"; (E/2)-((B/2)+1.5")=5 3/8"; (E/2)-((MB_P/2)+.125")=1 5/16"; (E/2)-(E/52*15)=6 31/32"; (F-((F-H)/2))/2=8 3/4"; (M - (2 * (D - L - K - J)))/2=5 13/16"; (MB_P/2)+.125"=15 1/8"; (MB_P/2-.125")+((F / 2) - 2")=-23 5/8"; (MB_P/2-.125")-((F / 2) - 2")=-6 1/8"; (MB_Q/2)+.125"=15 1/8"; (NOZZLE_HEIGHT - (NOZZLE_HEIGHT / 8 * 2)) / 2=12"; (NOZZLE_WB_OD - NOZZLE_TOP_OD) / 4=2 1/8"; -((MB_Q / 2) + 1/8")=-15 1/8"; -(F-((F-H)/2))/2=-8 3/4"; -MB_HEIGHT=-35"; -MB_P=-30"; -MB_P-.25=-30 1/4"; A=78"; A/2=39"; B=19 1/8"; B/2=9 9/16"; B/4=4 25/32"; C=46 3/4"; C/2=23 3/8"; CLASS=2"; D=38 5/16"; D-L-K-J=1 1/32"; D-M=24 5/8"; DUAL_Q=90 3/8"; DUAL_Q+.25"=90 5/8"; E=32 7/8"; E-(NOZZLE_RAD/3*2)=10 3/4"; E-N-N-H=-53 5/16"; E/2=16 7/16"; E/2-H/2=6 11/16"; E/52*15=9 15/32"; E/52*30=18 31/32"; F=21 1/2"; F/2=10 3/4"; H=19 1/2"; H/2=9 3/4"; HEIGHT=36 11/32"; J=6 1/4"; J+K+L=37 9/32"; K=15 3/8"; L=15 21/32"; M=13 11/16"; M-(2*(D-L-K-J))=11 5/8"; MB_A=97 1/16"; MB_F=7 5/8"; MB_F-3"=4 5/8"; MB_HEIGHT=35"; MB_HEIGHT/2=17 1/2"; MB_N=14 3/16"; MB_N-(D-J-K-L)=13 5/32"; MB_P=30"; MB_P+.25"=30 1/4"; MB_P+MB_P+.5=60 1/2"; MB_P-4.5"=25 1/2"; MB_Q=30"; N=60"; N+(H/2)=69 3/4"; NOZZLE_BOTTOM_ID=17 1/16"; NOZZLE_BOTTOM_RAD=8 17/32"; NOZZLE_BOTTOM_RAD-3*2=2 17/32"; NOZZLE_HEIGHT=32"; NOZZLE_HEIGHT/7*2=8"; NOZZLE_SIZE=12"; NOZZLE_TOP_OD=19 1/2"; NOZZLE_TOP_RAD=9 3/4"; NOZZLE_WB/4=5 19/32"; NOZZLE_WB_OD=28"; NOZZLE_WB_RAD=14"; NOZZLE_WB_RAD-2"=12"; P=60"; R=22"; R*1.1=24 3/16"; R+((B/2)+1.5")=33 1/16"; R-((B/2)+1.5")=10 15/16"; RO/2=12 3/4"; RO2/2=73 1/8"; TRANSITION=12 1/16"; TRANSITION/2=6 1/32"; TRIP_Q=150 3/4"; TRIP_Q-4.5"=146 1/4"; Type Comments=Triple Vari-Plume Laboratory Exhaust Centrifugal Airfoil Class 2 Arr 10 With Mixing Box
- Triple_150_CAVP-12H_CLASS_1_With_Mixing_Box: ((M - (2 * (D - L - K - J))) / 2) + (TRANSITION / 2)=11 27/32"; (B/2)+1.5"=11 1/16"; (B/2)-.125"=9 7/16"; (D-J-K-L)*2=2 1/16"; (E/2)-((B/2)+1.5")=5 3/8"; (E/2)-((MB_P/2)+.125")=1 5/16"; (E/2)-(E/52*15)=6 31/32"; (F-((F-H)/2))/2=8 3/4"; (M - (2 * (D - L - K - J)))/2=5 13/16"; (MB_P/2)+.125"=15 1/8"; (MB_P/2-.125")+((F / 2) - 2")=-23 5/8"; (MB_P/2-.125")-((F / 2) - 2")=-6 1/8"; (MB_Q/2)+.125"=15 1/8"; (NOZZLE_HEIGHT - (NOZZLE_HEIGHT / 8 * 2)) / 2=12"; (NOZZLE_WB_OD - NOZZLE_TOP_OD) / 4=2 1/8"; -((MB_Q / 2) + 1/8")=-15 1/8"; -(F-((F-H)/2))/2=-8 3/4"; -MB_HEIGHT=-35"; -MB_P=-30"; -MB_P-.25=-30 1/4"; A=78"; A/2=39"; B=19 1/8"; B/2=9 9/16"; B/4=4 25/32"; C=46 3/4"; C/2=23 3/8"; CLASS=1"; D=35 7/16"; D-L-K-J=1 1/32"; D-M=21 3/4"; DUAL_Q=90 3/8"; DUAL_Q+.25"=90 5/8"; E=32 7/8"; E-(NOZZLE_RAD/3*2)=10 3/4"; E-N-N-H=-53 5/16"; E/2=16 7/16"; E/2-H/2=6 11/16"; E/52*15=9 15/32"; E/52*30=18 31/32"; F=21 1/2"; F/2=10 3/4"; H=19 1/2"; H/2=9 3/4"; HEIGHT=36 11/32"; J=6 1/2"; J+K+L=34 13/32"; K=12 1/4"; L=15 21/32"; M=13 11/16"; M-(2*(D-L-K-J))=11 5/8"; MB_A=94 3/16"; MB_F=7 5/8"; MB_F-3"=4 5/8"; MB_HEIGHT=35"; MB_HEIGHT/2=17 1/2"; MB_N=14 3/16"; MB_N-(D-J-K-L)=13 5/32"; MB_P=30"; MB_P+.25"=30 1/4"; MB_P+MB_P+.5=60 1/2"; MB_P-4.5"=25 1/2"; MB_Q=30"; N=60"; N+(H/2)=69 3/4"; NOZZLE_BOTTOM_ID=17 1/16"; NOZZLE_BOTTOM_RAD=8 17/32"; NOZZLE_BOTTOM_RAD-3*2=2 17/32"; NOZZLE_HEIGHT=32"; NOZZLE_HEIGHT/7*2=8"; NOZZLE_SIZE=12"; NOZZLE_TOP_OD=19 1/2"; NOZZLE_TOP_RAD=9 3/4"; NOZZLE_WB/4=5 19/32"; NOZZLE_WB_OD=28"; NOZZLE_WB_RAD=14"; NOZZLE_WB_RAD-2"=12"; P=60"; R=22"; R*1.1=24 3/16"; R+((B/2)+1.5")=33 1/16"; R-((B/2)+1.5")=10 15/16"; RO/2=12 3/4"; RO2/2=73 1/8"; TRANSITION=12 1/16"; TRANSITION/2=6 1/32"; TRIP_Q=150 3/4"; TRIP_Q-4.5"=146 1/4"; Type Comments=Triple Vari-Plume Laboratory Exhaust Centrifugal Airfoil Class 1 Arr 10 With Mixing Box
- Triple_150_CAVP-12L_CLASS_1_With_Mixing_Box: ((M - (2 * (D - L - K - J))) / 2) + (TRANSITION / 2)=11 27/32"; (B/2)+1.5"=11 1/16"; (B/2)-.125"=9 7/16"; (D-J-K-L)*2=2 1/16"; (E/2)-((B/2)+1.5")=5 3/8"; (E/2)-((MB_P/2)+.125")=1 5/16"; (E/2)-(E/52*15)=6 31/32"; (F-((F-H)/2))/2=8 3/4"; (M - (2 * (D - L - K - J)))/2=5 13/16"; (MB_P/2)+.125"=15 1/8"; (MB_P/2-.125")+((F / 2) - 2")=-23 5/8"; (MB_P/2-.125")-((F / 2) - 2")=-6 1/8"; (MB_Q/2)+.125"=15 1/8"; (NOZZLE_HEIGHT - (NOZZLE_HEIGHT / 8 * 2)) / 2=12"; (NOZZLE_WB_OD - NOZZLE_TOP_OD) / 4=2 1/8"; -((MB_Q / 2) + 1/8")=-15 1/8"; -(F-((F-H)/2))/2=-8 3/4"; -MB_HEIGHT=-35"; -MB_P=-30"; -MB_P-.25=-30 1/4"; A=78"; A/2=39"; B=19 1/8"; B/2=9 9/16"; B/4=4 25/32"; C=46 3/4"; C/2=23 3/8"; CLASS=1"; D=35 7/16"; D-L-K-J=1 1/32"; D-M=21 3/4"; DUAL_Q=90 3/8"; DUAL_Q+.25"=90 5/8"; E=32 7/8"; E-(NOZZLE_RAD/3*2)=10 3/4"; E-N-N-H=-53 5/16"; E/2=16 7/16"; E/2-H/2=6 11/16"; E/52*15=9 15/32"; E/52*30=18 31/32"; F=21 1/2"; F/2=10 3/4"; H=19 1/2"; H/2=9 3/4"; HEIGHT=36 11/32"; J=6 1/2"; J+K+L=34 13/32"; K=12 1/4"; L=15 21/32"; M=13 11/16"; M-(2*(D-L-K-J))=11 5/8"; MB_A=94 3/16"; MB_F=7 5/8"; MB_F-3"=4 5/8"; MB_HEIGHT=35"; MB_HEIGHT/2=17 1/2"; MB_N=14 3/16"; MB_N-(D-J-K-L)=13 5/32"; MB_P=30"; MB_P+.25"=30 1/4"; MB_P+MB_P+.5=60 1/2"; MB_P-4.5"=25 1/2"; MB_Q=30"; N=60"; N+(H/2)=69 3/4"; NOZZLE_BOTTOM_ID=17 1/16"; NOZZLE_BOTTOM_RAD=8 17/32"; NOZZLE_BOTTOM_RAD-3*2=2 17/32"; NOZZLE_HEIGHT=32"; NOZZLE_HEIGHT/7*2=8"; NOZZLE_SIZE=12"; NOZZLE_TOP_OD=19 1/2"; NOZZLE_TOP_RAD=9 3/4"; NOZZLE_WB/4=5 19/32"; NOZZLE_WB_OD=28"; NOZZLE_WB_RAD=14"; NOZZLE_WB_RAD-2"=12"; P=60"; R=22"; R*1.1=24 3/16"; R+((B/2)+1.5")=33 1/16"; R-((B/2)+1.5")=10 15/16"; RO/2=12 3/4"; RO2/2=73 1/8"; TRANSITION=12 1/16"; TRANSITION/2=6 1/32"; TRIP_Q=150 3/4"; TRIP_Q-4.5"=146 1/4"; Type Comments=Triple Vari-Plume Laboratory Exhaust Centrifugal Airfoil Class 1 Arr 10 With Mixing Box
- Triple_165_CAVP-9L_CLASS_1_With_Mixing_Box: ((M - (2 * (D - L - K - J))) / 2) + (TRANSITION / 2)=10 15/16"; (B/2)+1.5"=12 3/32"; (B/2)-.125"=10 15/32"; (D-J-K-L)*2=2 1/16"; (E/2)-((B/2)+1.5")=5 29/32"; (E/2)-((MB_P/2)+.125")=1 7/8"; (E/2)-(E/52*15)=7 5/8"; (F-((F-H)/2))/2=11 1/16"; (M - (2 * (D - L - K - J)))/2=6 13/32"; (MB_P/2)+.125"=16 1/8"; (MB_P/2-.125")+((F / 2) - 2")=-26 15/16"; (MB_P/2-.125")-((F / 2) - 2")=-4 13/16"; (MB_Q/2)+.125"=16 1/8"; (NOZZLE_HEIGHT - (NOZZLE_HEIGHT / 8 * 2)) / 2=10 1/2"; (NOZZLE_WB_OD - NOZZLE_TOP_OD) / 4=2 3/8"; -((MB_Q / 2) + 1/8")=-16 1/8"; -(F-((F-H)/2))/2=-11 1/16"; -MB_HEIGHT=-37"; -MB_P=-32"; -MB_P-.25=-32 1/4"; A=82 1/16"; A/2=41 1/32"; B=21 3/16"; B/2=10 19/32"; B/4=5 5/16"; C=50 13/16"; C/2=25 13/32"; CLASS=1"; D=37 5/8"; D-L-K-J=1 1/32"; D-M=22 3/4"; DUAL_Q=96 3/8"; DUAL_Q+.25"=96 5/8"; E=36"; E-(NOZZLE_RAD/3*2)=13 23/32"; E-N-N-H=-54 1/16"; E/2=18"; E/2-H/2=5 15/16"; E/52*15=10 3/8"; E/52*30=20 25/32"; F=26 1/8"; F/2=13 1/16"; H=24 1/8"; H/2=12 1/16"; HEIGHT=39 31/32"; J=7 1/2"; J+K+L=36 19/32"; K=12 1/4"; L=16 27/32"; M=14 7/8"; M-(2*(D-L-K-J))=12 13/16"; MB_A=99"; MB_F=8 7/8"; MB_F-3"=5 7/8"; MB_HEIGHT=37"; MB_HEIGHT/2=18 1/2"; MB_N=14 3/16"; MB_N-(D-J-K-L)=13 5/32"; MB_P=32"; MB_P+.25"=32 1/4"; MB_P+MB_P+.5=64 1/2"; MB_P-4.5"=27 1/2"; MB_Q=32"; N=60"; N+(H/2)=72 1/16"; NOZZLE_BOTTOM_ID=12 13/16"; NOZZLE_BOTTOM_RAD=6 13/32"; NOZZLE_BOTTOM_RAD-3*2=13/32"; NOZZLE_HEIGHT=28"; NOZZLE_HEIGHT/7*2=7"; NOZZLE_SIZE=9"; NOZZLE_TOP_OD=13 1/2"; NOZZLE_TOP_RAD=6 3/4"; NOZZLE_WB/4=4 19/32"; NOZZLE_WB_OD=23"; NOZZLE_WB_RAD=11 1/2"; NOZZLE_WB_RAD-2"=9 1/2"; P=60"; R=24 1/4"; R*1.1=26 11/16"; R+((B/2)+1.5")=36 11/32"; R-((B/2)+1.5")=12 5/32"; RO/2=13 3/4"; RO2/2=78 1/8"; TRANSITION=9 1/16"; TRANSITION/2=4 17/32"; TRIP_Q=160 3/4"; TRIP_Q-4.5"=156 1/4"; Type Comments=Triple Vari-Plume Laboratory Exhaust Centrifugal Airfoil Class 1 Arr 10 With Mixing Box
- Triple_165_CAVP-9H_CLASS_1_With_Mixing_Box: ((M - (2 * (D - L - K - J))) / 2) + (TRANSITION / 2)=10 15/16"; (B/2)+1.5"=12 3/32"; (B/2)-.125"=10 15/32"; (D-J-K-L)*2=2 1/16"; (E/2)-((B/2)+1.5")=5 29/32"; (E/2)-((MB_P/2)+.125")=1 7/8"; (E/2)-(E/52*15)=7 5/8"; (F-((F-H)/2))/2=11 1/16"; (M - (2 * (D - L - K - J)))/2=6 13/32"; (MB_P/2)+.125"=16 1/8"; (MB_P/2-.125")+((F / 2) - 2")=-26 15/16"; (MB_P/2-.125")-((F / 2) - 2")=-4 13/16"; (MB_Q/2)+.125"=16 1/8"; (NOZZLE_HEIGHT - (NOZZLE_HEIGHT / 8 * 2)) / 2=10 1/2"; (NOZZLE_WB_OD - NOZZLE_TOP_OD) / 4=2 3/8"; -((MB_Q / 2) + 1/8")=-16 1/8"; -(F-((F-H)/2))/2=-11 1/16"; -MB_HEIGHT=-37"; -MB_P=-32"; -MB_P-.25=-32 1/4"; A=82 1/16"; A/2=41 1/32"; B=21 3/16"; B/2=10 19/32"; B/4=5 5/16"; C=50 13/16"; C/2=25 13/32"; CLASS=1"; D=37 5/8"; D-L-K-J=1 1/32"; D-M=22 3/4"; DUAL_Q=96 3/8"; DUAL_Q+.25"=96 5/8"; E=36"; E-(NOZZLE_RAD/3*2)=13 23/32"; E-N-N-H=-54 1/16"; E/2=18"; E/2-H/2=5 15/16"; E/52*15=10 3/8"; E/52*30=20 25/32"; F=26 1/8"; F/2=13 1/16"; H=24 1/8"; H/2=12 1/16"; HEIGHT=39 31/32"; J=7 1/2"; J+K+L=36 19/32"; K=12 1/4"; L=16 27/32"; M=14 7/8"; M-(2*(D-L-K-J))=12 13/16"; MB_A=99"; MB_F=8 7/8"; MB_F-3"=5 7/8"; MB_HEIGHT=37"; MB_HEIGHT/2=18 1/2"; MB_N=14 3/16"; MB_N-(D-J-K-L)=13 5/32"; MB_P=32"; MB_P+.25"=32 1/4"; MB_P+MB_P+.5=64 1/2"; MB_P-4.5"=27 1/2"; MB_Q=32"; N=60"; N+(H/2)=72 1/16"; NOZZLE_BOTTOM_ID=12 13/16"; NOZZLE_BOTTOM_RAD=6 13/32"; NOZZLE_BOTTOM_RAD-3*2=13/32"; NOZZLE_HEIGHT=28"; NOZZLE_HEIGHT/7*2=7"; NOZZLE_SIZE=9"; NOZZLE_TOP_OD=13 1/2"; NOZZLE_TOP_RAD=6 3/4"; NOZZLE_WB/4=4 19/32"; NOZZLE_WB_OD=23"; NOZZLE_WB_RAD=11 1/2"; NOZZLE_WB_RAD-2"=9 1/2"; P=60"; R=24 1/4"; R*1.1=26 11/16"; R+((B/2)+1.5")=36 11/32"; R-((B/2)+1.5")=12 5/32"; RO/2=13 3/4"; RO2/2=78 1/8"; TRANSITION=9 1/16"; TRANSITION/2=4 17/32"; TRIP_Q=160 3/4"; TRIP_Q-4.5"=156 1/4"; Type Comments=Triple Vari-Plume Laboratory Exhaust Centrifugal Airfoil Class 1 Arr 10 With Mixing Box
- Triple_165_CAVP-12L_CLASS_1_With_Mixing_Box: ((M - (2 * (D - L - K - J))) / 2) + (TRANSITION / 2)=12 7/16"; (B/2)+1.5"=12 3/32"; (B/2)-.125"=10 15/32"; (D-J-K-L)*2=2 1/16"; (E/2)-((B/2)+1.5")=5 29/32"; (E/2)-((MB_P/2)+.125")=1 7/8"; (E/2)-(E/52*15)=7 5/8"; (F-((F-H)/2))/2=11 1/16"; (M - (2 * (D - L - K - J)))/2=6 13/32"; (MB_P/2)+.125"=16 1/8"; (MB_P/2-.125")+((F / 2) - 2")=-26 15/16"; (MB_P/2-.125")-((F / 2) - 2")=-4 13/16"; (MB_Q/2)+.125"=16 1/8"; (NOZZLE_HEIGHT - (NOZZLE_HEIGHT / 8 * 2)) / 2=12"; (NOZZLE_WB_OD - NOZZLE_TOP_OD) / 4=2 1/8"; -((MB_Q / 2) + 1/8")=-16 1/8"; -(F-((F-H)/2))/2=-11 1/16"; -MB_HEIGHT=-37"; -MB_P=-32"; -MB_P-.25=-32 1/4"; A=82 1/16"; A/2=41 1/32"; B=21 3/16"; B/2=10 19/32"; B/4=5 5/16"; C=50 13/16"; C/2=25 13/32"; CLASS=1"; D=37 5/8"; D-L-K-J=1 1/32"; D-M=22 3/4"; DUAL_Q=96 3/8"; DUAL_Q+.25"=96 5/8"; E=36"; E-(NOZZLE_RAD/3*2)=12 5/16"; E-N-N-H=-54 1/16"; E/2=18"; E/2-H/2=5 15/16"; E/52*15=10 3/8"; E/52*30=20 25/32"; F=26 1/8"; F/2=13 1/16"; H=24 1/8"; H/2=12 1/16"; HEIGHT=39 31/32"; J=7 1/2"; J+K+L=36 19/32"; K=12 1/4"; L=16 27/32"; M=14 7/8"; M-(2*(D-L-K-J))=12 13/16"; MB_A=99"; MB_F=8 7/8"; MB_F-3"=5 7/8"; MB_HEIGHT=37"; MB_HEIGHT/2=18 1/2"; MB_N=14 3/16"; MB_N-(D-J-K-L)=13 5/32"; MB_P=32"; MB_P+.25"=32 1/4"; MB_P+MB_P+.5=64 1/2"; MB_P-4.5"=27 1/2"; MB_Q=32"; N=60"; N+(H/2)=72 1/16"; NOZZLE_BOTTOM_ID=17 1/16"; NOZZLE_BOTTOM_RAD=8 17/32"; NOZZLE_BOTTOM_RAD-3*2=2 17/32"; NOZZLE_HEIGHT=32"; NOZZLE_HEIGHT/7*2=8"; NOZZLE_SIZE=12"; NOZZLE_TOP_OD=19 1/2"; NOZZLE_TOP_RAD=9 3/4"; NOZZLE_WB/4=5 19/32"; NOZZLE_WB_OD=28"; NOZZLE_WB_RAD=14"; NOZZLE_WB_RAD-2"=12"; P=60"; R=24 1/4"; R*1.1=26 11/16"; R+((B/2)+1.5")=36 11/32"; R-((B/2)+1.5")=12 5/32"; RO/2=13 3/4"; RO2/2=78 1/8"; TRANSITION=12 1/16"; TRANSITION/2=6 1/32"; TRIP_Q=160 3/4"; TRIP_Q-4.5"=156 1/4"; Type Comments=Triple Vari-Plume Laboratory Exhaust Centrifugal Airfoil Class 1 Arr 10 With Mixing Box
- Triple_165_CAVP-12H_CLASS_1_With_Mixing_Box: ((M - (2 * (D - L - K - J))) / 2) + (TRANSITION / 2)=12 7/16"; (B/2)+1.5"=12 3/32"; (B/2)-.125"=10 15/32"; (D-J-K-L)*2=2 1/16"; (E/2)-((B/2)+1.5")=5 29/32"; (E/2)-((MB_P/2)+.125")=1 7/8"; (E/2)-(E/52*15)=7 5/8"; (F-((F-H)/2))/2=11 1/16"; (M - (2 * (D - L - K - J)))/2=6 13/32"; (MB_P/2)+.125"=16 1/8"; (MB_P/2-.125")+((F / 2) - 2")=-26 15/16"; (MB_P/2-.125")-((F / 2) - 2")=-4 13/16"; (MB_Q/2)+.125"=16 1/8"; (NOZZLE_HEIGHT - (NOZZLE_HEIGHT / 8 * 2)) / 2=12"; (NOZZLE_WB_OD - NOZZLE_TOP_OD) / 4=2 1/8"; -((MB_Q / 2) + 1/8")=-16 1/8"; -(F-((F-H)/2))/2=-11 1/16"; -MB_HEIGHT=-37"; -MB_P=-32"; -MB_P-.25=-32 1/4"; A=82 1/16"; A/2=41 1/32"; B=21 3/16"; B/2=10 19/32"; B/4=5 5/16"; C=50 13/16"; C/2=25 13/32"; CLASS=1"; D=37 5/8"; D-L-K-J=1 1/32"; D-M=22 3/4"; DUAL_Q=96 3/8"; DUAL_Q+.25"=96 5/8"; E=36"; E-(NOZZLE_RAD/3*2)=12 5/16"; E-N-N-H=-54 1/16"; E/2=18"; E/2-H/2=5 15/16"; E/52*15=10 3/8"; E/52*30=20 25/32"; F=26 1/8"; F/2=13 1/16"; H=24 1/8"; H/2=12 1/16"; HEIGHT=39 31/32"; J=7 1/2"; J+K+L=36 19/32"; K=12 1/4"; L=16 27/32"; M=14 7/8"; M-(2*(D-L-K-J))=12 13/16"; MB_A=99"; MB_F=8 7/8"; MB_F-3"=5 7/8"; MB_HEIGHT=37"; MB_HEIGHT/2=18 1/2"; MB_N=14 3/16"; MB_N-(D-J-K-L)=13 5/32"; MB_P=32"; MB_P+.25"=32 1/4"; MB_P+MB_P+.5=64 1/2"; MB_P-4.5"=27 1/2"; MB_Q=32"; N=60"; N+(H/2)=72 1/16"; NOZZLE_BOTTOM_ID=17 1/16"; NOZZLE_BOTTOM_RAD=8 17/32"; NOZZLE_BOTTOM_RAD-3*2=2 17/32"; NOZZLE_HEIGHT=32"; NOZZLE_HEIGHT/7*2=8"; NOZZLE_SIZE=12"; NOZZLE_TOP_OD=19 1/2"; NOZZLE_TOP_RAD=9 3/4"; NOZZLE_WB/4=5 19/32"; NOZZLE_WB_OD=28"; NOZZLE_WB_RAD=14"; NOZZLE_WB_RAD-2"=12"; P=60"; R=24 1/4"; R*1.1=26 11/16"; R+((B/2)+1.5")=36 11/32"; R-((B/2)+1.5")=12 5/32"; RO/2=13 3/4"; RO2/2=78 1/8"; TRANSITION=12 1/16"; TRANSITION/2=6 1/32"; TRIP_Q=160 3/4"; TRIP_Q-4.5"=156 1/4"; Type Comments=Triple Vari-Plume Laboratory Exhaust Centrifugal Airfoil Class 1 Arr 10 With Mixing Box
- Triple_165_CAVP-9L_CLASS_2_With_Mixing_Box: ((M - (2 * (D - L - K - J))) / 2) + (TRANSITION / 2)=10 15/16"; (B/2)+1.5"=12 3/32"; (B/2)-.125"=10 15/32"; (D-J-K-L)*2=2 1/16"; (E/2)-((B/2)+1.5")=5 29/32"; (E/2)-((MB_P/2)+.125")=1 7/8"; (E/2)-(E/52*15)=7 5/8"; (F-((F-H)/2))/2=11 1/16"; (M - (2 * (D - L - K - J)))/2=6 13/32"; (MB_P/2)+.125"=16 1/8"; (MB_P/2-.125")+((F / 2) - 2")=-26 15/16"; (MB_P/2-.125")-((F / 2) - 2")=-4 13/16"; (MB_Q/2)+.125"=16 1/8"; (NOZZLE_HEIGHT - (NOZZLE_HEIGHT / 8 * 2)) / 2=10 1/2"; (NOZZLE_WB_OD - NOZZLE_TOP_OD) / 4=2 3/8"; -((MB_Q / 2) + 1/8")=-16 1/8"; -(F-((F-H)/2))/2=-11 1/16"; -MB_HEIGHT=-37"; -MB_P=-32"; -MB_P-.25=-32 1/4"; A=82 1/16"; A/2=41 1/32"; B=21 3/16"; B/2=10 19/32"; B/4=5 5/16"; C=50 13/16"; C/2=25 13/32"; CLASS=2"; D=44 1/2"; D-L-K-J=1 1/32"; D-M=29 5/8"; DUAL_Q=96 3/8"; DUAL_Q+.25"=96 5/8"; E=36"; E-(NOZZLE_RAD/3*2)=13 23/32"; E-N-N-H=-54 1/16"; E/2=18"; E/2-H/2=5 15/16"; E/52*15=10 3/8"; E/52*30=20 25/32"; F=26 1/8"; F/2=13 1/16"; H=24 1/8"; H/2=12 1/16"; HEIGHT=39 31/32"; J=7 1/4"; J+K+L=43 15/32"; K=19 3/8"; L=16 27/32"; M=14 7/8"; M-(2*(D-L-K-J))=12 13/16"; MB_A=105 7/8"; MB_F=8 7/8"; MB_F-3"=5 7/8"; MB_HEIGHT=37"; MB_HEIGHT/2=18 1/2"; MB_N=14 3/16"; MB_N-(D-J-K-L)=13 5/32"; MB_P=32"; MB_P+.25"=32 1/4"; MB_P+MB_P+.5=64 1/2"; MB_P-4.5"=27 1/2"; MB_Q=32"; N=60"; N+(H/2)=72 1/16"; NOZZLE_BOTTOM_ID=12 13/16"; NOZZLE_BOTTOM_RAD=6 13/32"; NOZZLE_BOTTOM_RAD-3*2=13/32"; NOZZLE_HEIGHT=28"; NOZZLE_HEIGHT/7*2=7"; NOZZLE_SIZE=9"; NOZZLE_TOP_OD=13 1/2"; NOZZLE_TOP_RAD=6 3/4"; NOZZLE_WB/4=4 19/32"; NOZZLE_WB_OD=23"; NOZZLE_WB_RAD=11 1/2"; NOZZLE_WB_RAD-2"=9 1/2"; P=60"; R=24 1/4"; R*1.1=26 11/16"; R+((B/2)+1.5")=36 11/32"; R-((B/2)+1.5")=12 5/32"; RO/2=13 3/4"; RO2/2=78 1/8"; TRANSITION=9 1/16"; TRANSITION/2=4 17/32"; TRIP_Q=160 3/4"; TRIP_Q-4.5"=156 1/4"; Type Comments=Triple Vari-Plume Laboratory Exhaust Centrifugal Airfoil Class 2 Arr 10 With Mixing Box
- Triple_165_CAVP-9H_CLASS_2_With_Mixing_Box: ((M - (2 * (D - L - K - J))) / 2) + (TRANSITION / 2)=10 15/16"; (B/2)+1.5"=12 3/32"; (B/2)-.125"=10 15/32"; (D-J-K-L)*2=2 1/16"; (E/2)-((B/2)+1.5")=5 29/32"; (E/2)-((MB_P/2)+.125")=1 7/8"; (E/2)-(E/52*15)=7 5/8"; (F-((F-H)/2))/2=11 1/16"; (M - (2 * (D - L - K - J)))/2=6 13/32"; (MB_P/2)+.125"=16 1/8"; (MB_P/2-.125")+((F / 2) - 2")=-26 15/16"; (MB_P/2-.125")-((F / 2) - 2")=-4 13/16"; (MB_Q/2)+.125"=16 1/8"; (NOZZLE_HEIGHT - (NOZZLE_HEIGHT / 8 * 2)) / 2=10 1/2"; (NOZZLE_WB_OD - NOZZLE_TOP_OD) / 4=2 3/8"; -((MB_Q / 2) + 1/8")=-16 1/8"; -(F-((F-H)/2))/2=-11 1/16"; -MB_HEIGHT=-37"; -MB_P=-32"; -MB_P-.25=-32 1/4"; A=82 1/16"; A/2=41 1/32"; B=21 3/16"; B/2=10 19/32"; B/4=5 5/16"; C=50 13/16"; C/2=25 13/32"; CLASS=2"; D=44 1/2"; D-L-K-J=1 1/32"; D-M=29 5/8"; DUAL_Q=96 3/8"; DUAL_Q+.25"=96 5/8"; E=36"; E-(NOZZLE_RAD/3*2)=13 23/32"; E-N-N-H=-54 1/16"; E/2=18"; E/2-H/2=5 15/16"; E/52*15=10 3/8"; E/52*30=20 25/32"; F=26 1/8"; F/2=13 1/16"; H=24 1/8"; H/2=12 1/16"; HEIGHT=39 31/32"; J=7 1/4"; J+K+L=43 15/32"; K=19 3/8"; L=16 27/32"; M=14 7/8"; M-(2*(D-L-K-J))=12 13/16"; MB_A=105 7/8"; MB_F=8 7/8"; MB_F-3"=5 7/8"; MB_HEIGHT=37"; MB_HEIGHT/2=18 1/2"; MB_N=14 3/16"; MB_N-(D-J-K-L)=13 5/32"; MB_P=32"; MB_P+.25"=32 1/4"; MB_P+MB_P+.5=64 1/2"; MB_P-4.5"=27 1/2"; MB_Q=32"; N=60"; N+(H/2)=72 1/16"; NOZZLE_BOTTOM_ID=12 13/16"; NOZZLE_BOTTOM_RAD=6 13/32"; NOZZLE_BOTTOM_RAD-3*2=13/32"; NOZZLE_HEIGHT=28"; NOZZLE_HEIGHT/7*2=7"; NOZZLE_SIZE=9"; NOZZLE_TOP_OD=13 1/2"; NOZZLE_TOP_RAD=6 3/4"; NOZZLE_WB/4=4 19/32"; NOZZLE_WB_OD=23"; NOZZLE_WB_RAD=11 1/2"; NOZZLE_WB_RAD-2"=9 1/2"; P=60"; R=24 1/4"; R*1.1=26 11/16"; R+((B/2)+1.5")=36 11/32"; R-((B/2)+1.5")=12 5/32"; RO/2=13 3/4"; RO2/2=78 1/8"; TRANSITION=9 1/16"; TRANSITION/2=4 17/32"; TRIP_Q=160 3/4"; TRIP_Q-4.5"=156 1/4"; Type Comments=Triple Vari-Plume Laboratory Exhaust Centrifugal Airfoil Class 2 Arr 10 With Mixing Box
- Triple_165_CAVP-12L_CLASS_2_With_Mixing_Box: ((M - (2 * (D - L - K - J))) / 2) + (TRANSITION / 2)=12 7/16"; (B/2)+1.5"=12 3/32"; (B/2)-.125"=10 15/32"; (D-J-K-L)*2=2 1/16"; (E/2)-((B/2)+1.5")=5 29/32"; (E/2)-((MB_P/2)+.125")=1 7/8"; (E/2)-(E/52*15)=7 5/8"; (F-((F-H)/2))/2=11 1/16"; (M - (2 * (D - L - K - J)))/2=6 13/32"; (MB_P/2)+.125"=16 1/8"; (MB_P/2-.125")+((F / 2) - 2")=-26 15/16"; (MB_P/2-.125")-((F / 2) - 2")=-4 13/16"; (MB_Q/2)+.125"=16 1/8"; (NOZZLE_HEIGHT - (NOZZLE_HEIGHT / 8 * 2)) / 2=12"; (NOZZLE_WB_OD - NOZZLE_TOP_OD) / 4=2 1/8"; -((MB_Q / 2) + 1/8")=-16 1/8"; -(F-((F-H)/2))/2=-11 1/16"; -MB_HEIGHT=-37"; -MB_P=-32"; -MB_P-.25=-32 1/4"; A=82 1/16"; A/2=41 1/32"; B=21 3/16"; B/2=10 19/32"; B/4=5 5/16"; C=50 13/16"; C/2=25 13/32"; CLASS=2"; D=44 1/2"; D-L-K-J=1 1/32"; D-M=29 5/8"; DUAL_Q=96 3/8"; DUAL_Q+.25"=96 5/8"; E=36"; E-(NOZZLE_RAD/3*2)=12 5/16"; E-N-N-H=-54 1/16"; E/2=18"; E/2-H/2=5 15/16"; E/52*15=10 3/8"; E/52*30=20 25/32"; F=26 1/8"; F/2=13 1/16"; H=24 1/8"; H/2=12 1/16"; HEIGHT=39 31/32"; J=7 1/4"; J+K+L=43 15/32"; K=19 3/8"; L=16 27/32"; M=14 7/8"; M-(2*(D-L-K-J))=12 13/16"; MB_A=105 7/8"; MB_F=8 7/8"; MB_F-3"=5 7/8"; MB_HEIGHT=37"; MB_HEIGHT/2=18 1/2"; MB_N=14 3/16"; MB_N-(D-J-K-L)=13 5/32"; MB_P=32"; MB_P+.25"=32 1/4"; MB_P+MB_P+.5=64 1/2"; MB_P-4.5"=27 1/2"; MB_Q=32"; N=60"; N+(H/2)=72 1/16"; NOZZLE_BOTTOM_ID=17 1/16"; NOZZLE_BOTTOM_RAD=8 17/32"; NOZZLE_BOTTOM_RAD-3*2=2 17/32"; NOZZLE_HEIGHT=32"; NOZZLE_HEIGHT/7*2=8"; NOZZLE_SIZE=12"; NOZZLE_TOP_OD=19 1/2"; NOZZLE_TOP_RAD=9 3/4"; NOZZLE_WB/4=5 19/32"; NOZZLE_WB_OD=28"; NOZZLE_WB_RAD=14"; NOZZLE_WB_RAD-2"=12"; P=60"; R=24 1/4"; R*1.1=26 11/16"; R+((B/2)+1.5")=36 11/32"; R-((B/2)+1.5")=12 5/32"; RO/2=13 3/4"; RO2/2=78 1/8"; TRANSITION=12 1/16"; TRANSITION/2=6 1/32"; TRIP_Q=160 3/4"; TRIP_Q-4.5"=156 1/4"; Type Comments=Triple Vari-Plume Laboratory Exhaust Centrifugal Airfoil Class 2 Arr 10 With Mixing Box
- Triple_165_CAVP-12H_CLASS_2_With_Mixing_Box: ((M - (2 * (D - L - K - J))) / 2) + (TRANSITION / 2)=12 7/16"; (B/2)+1.5"=12 3/32"; (B/2)-.125"=10 15/32"; (D-J-K-L)*2=2 1/16"; (E/2)-((B/2)+1.5")=5 29/32"; (E/2)-((MB_P/2)+.125")=1 7/8"; (E/2)-(E/52*15)=7 5/8"; (F-((F-H)/2))/2=11 1/16"; (M - (2 * (D - L - K - J)))/2=6 13/32"; (MB_P/2)+.125"=16 1/8"; (MB_P/2-.125")+((F / 2) - 2")=-26 15/16"; (MB_P/2-.125")-((F / 2) - 2")=-4 13/16"; (MB_Q/2)+.125"=16 1/8"; (NOZZLE_HEIGHT - (NOZZLE_HEIGHT / 8 * 2)) / 2=12"; (NOZZLE_WB_OD - NOZZLE_TOP_OD) / 4=2 1/8"; -((MB_Q / 2) + 1/8")=-16 1/8"; -(F-((F-H)/2))/2=-11 1/16"; -MB_HEIGHT=-37"; -MB_P=-32"; -MB_P-.25=-32 1/4"; A=82 1/16"; A/2=41 1/32"; B=21 3/16"; B/2=10 19/32"; B/4=5 5/16"; C=50 13/16"; C/2=25 13/32"; CLASS=2"; D=44 1/2"; D-L-K-J=1 1/32"; D-M=29 5/8"; DUAL_Q=96 3/8"; DUAL_Q+.25"=96 5/8"; E=36"; E-(NOZZLE_RAD/3*2)=12 5/16"; E-N-N-H=-54 1/16"; E/2=18"; E/2-H/2=5 15/16"; E/52*15=10 3/8"; E/52*30=20 25/32"; F=26 1/8"; F/2=13 1/16"; H=24 1/8"; H/2=12 1/16"; HEIGHT=39 31/32"; J=7 1/4"; J+K+L=43 15/32"; K=19 3/8"; L=16 27/32"; M=14 7/8"; M-(2*(D-L-K-J))=12 13/16"; MB_A=105 7/8"; MB_F=8 7/8"; MB_F-3"=5 7/8"; MB_HEIGHT=37"; MB_HEIGHT/2=18 1/2"; MB_N=14 3/16"; MB_N-(D-J-K-L)=13 5/32"; MB_P=32"; MB_P+.25"=32 1/4"; MB_P+MB_P+.5=64 1/2"; MB_P-4.5"=27 1/2"; MB_Q=32"; N=60"; N+(H/2)=72 1/16"; NOZZLE_BOTTOM_ID=17 1/16"; NOZZLE_BOTTOM_RAD=8 17/32"; NOZZLE_BOTTOM_RAD-3*2=2 17/32"; NOZZLE_HEIGHT=32"; NOZZLE_HEIGHT/7*2=8"; NOZZLE_SIZE=12"; NOZZLE_TOP_OD=19 1/2"; NOZZLE_TOP_RAD=9 3/4"; NOZZLE_WB/4=5 19/32"; NOZZLE_WB_OD=28"; NOZZLE_WB_RAD=14"; NOZZLE_WB_RAD-2"=12"; P=60"; R=24 1/4"; R*1.1=26 11/16"; R+((B/2)+1.5")=36 11/32"; R-((B/2)+1.5")=12 5/32"; RO/2=13 3/4"; RO2/2=78 1/8"; TRANSITION=12 1/16"; TRANSITION/2=6 1/32"; TRIP_Q=160 3/4"; TRIP_Q-4.5"=156 1/4"; Type Comments=Triple Vari-Plume Laboratory Exhaust Centrifugal Airfoil Class 2 Arr 10 With Mixing Box
- Triple_180_CAVP-9H_CLASS_1_With_Mixing_Box: ((M - (2 * (D - L - K - J))) / 2) + (TRANSITION / 2)=11 1/2"; (B/2)+1.5"=12 27/32"; (B/2)-.125"=11 7/32"; (D-J-K-L)*2=2 1/16"; (E/2)-((B/2)+1.5")=6 11/16"; (E/2)-((MB_P/2)+.125")=2 13/32"; (E/2)-(E/52*15)=8 1/4"; (F-((F-H)/2))/2=11 1/16"; (M - (2 * (D - L - K - J)))/2=6 31/32"; (MB_P/2)+.125"=17 1/8"; (MB_P/2-.125")+((F / 2) - 2")=-27 15/16"; (MB_P/2-.125")-((F / 2) - 2")=-5 13/16"; (MB_Q/2)+.125"=17 1/8"; (NOZZLE_HEIGHT - (NOZZLE_HEIGHT / 8 * 2)) / 2=10 1/2"; (NOZZLE_WB_OD - NOZZLE_TOP_OD) / 4=2 3/8"; -((MB_Q / 2) + 1/8")=-17 1/8"; -(F-((F-H)/2))/2=-11 1/16"; -MB_HEIGHT=-38 1/2"; -MB_P=-34"; -MB_P-.25=-34 1/4"; A=84 1/16"; A/2=42 1/32"; B=22 11/16"; B/2=11 11/32"; B/4=5 11/16"; C=52 13/16"; C/2=26 13/32"; CLASS=1"; D=42 1/8"; D-L-K-J=1 1/32"; D-M=26 1/8"; DUAL_Q=102 3/8"; DUAL_Q+.25"=102 5/8"; E=39 1/16"; E-(NOZZLE_RAD/3*2)=15 1/4"; E-N-N-H=-52 17/32"; E/2=19 17/32"; E/2-H/2=7 15/32"; E/52*15=11 9/32"; E/52*30=22 17/32"; F=26 1/8"; F/2=13 1/16"; H=24 1/8"; H/2=12 1/16"; HEIGHT=41 5/16"; J=8"; J+K+L=41 3/32"; K=15 1/8"; L=17 31/32"; M=16"; M-(2*(D-L-K-J))=13 15/16"; MB_A=106 5/8"; MB_F=8 1/8"; MB_F-3"=5 1/8"; MB_HEIGHT=38 1/2"; MB_HEIGHT/2=19 1/4"; MB_N=14 3/16"; MB_N-(D-J-K-L)=13 5/32"; MB_P=34"; MB_P+.25"=34 1/4"; MB_P+MB_P+.5=68 1/2"; MB_P-4.5"=29 1/2"; MB_Q=34"; N=60"; N+(H/2)=72 1/16"; NOZZLE_BOTTOM_ID=12 13/16"; NOZZLE_BOTTOM_RAD=6 13/32"; NOZZLE_BOTTOM_RAD-3*2=13/32"; NOZZLE_HEIGHT=28"; NOZZLE_HEIGHT/7*2=7"; NOZZLE_SIZE=9"; NOZZLE_TOP_OD=13 1/2"; NOZZLE_TOP_RAD=6 3/4"; NOZZLE_WB/4=4 19/32"; NOZZLE_WB_OD=23"; NOZZLE_WB_RAD=11 1/2"; NOZZLE_WB_RAD-2"=9 1/2"; P=60"; R=24 1/4"; R*1.1=26 11/16"; R+((B/2)+1.5")=37 3/32"; R-((B/2)+1.5")=11 13/32"; RO/2=14 3/4"; RO2/2=83 1/8"; TRANSITION=9 1/16"; TRANSITION/2=4 17/32"; TRIP_Q=170 3/4"; TRIP_Q-4.5"=166 1/4"; Type Comments=Triple Vari-Plume Laboratory Exhaust Centrifugal Airfoil Class 1 Arr 10 With Mixing Box
- Triple_180_CAVP-9L_CLASS_1_With_Mixing_Box: ((M - (2 * (D - L - K - J))) / 2) + (TRANSITION / 2)=11 1/2"; (B/2)+1.5"=12 27/32"; (B/2)-.125"=11 7/32"; (D-J-K-L)*2=2 1/16"; (E/2)-((B/2)+1.5")=6 11/16"; (E/2)-((MB_P/2)+.125")=2 13/32"; (E/2)-(E/52*15)=8 1/4"; (F-((F-H)/2))/2=11 1/16"; (M - (2 * (D - L - K - J)))/2=6 31/32"; (MB_P/2)+.125"=17 1/8"; (MB_P/2-.125")+((F / 2) - 2")=-27 15/16"; (MB_P/2-.125")-((F / 2) - 2")=-5 13/16"; (MB_Q/2)+.125"=17 1/8"; (NOZZLE_HEIGHT - (NOZZLE_HEIGHT / 8 * 2)) / 2=10 1/2"; (NOZZLE_WB_OD - NOZZLE_TOP_OD) / 4=2 3/8"; -((MB_Q / 2) + 1/8")=-17 1/8"; -(F-((F-H)/2))/2=-11 1/16"; -MB_HEIGHT=-38 1/2"; -MB_P=-34"; -MB_P-.25=-34 1/4"; A=84 1/16"; A/2=42 1/32"; B=22 11/16"; B/2=11 11/32"; B/4=5 11/16"; C=52 13/16"; C/2=26 13/32"; CLASS=1"; D=42 1/8"; D-L-K-J=1 1/32"; D-M=26 1/8"; DUAL_Q=102 3/8"; DUAL_Q+.25"=102 5/8"; E=39 1/16"; E-(NOZZLE_RAD/3*2)=15 1/4"; E-N-N-H=-52 17/32"; E/2=19 17/32"; E/2-H/2=7 15/32"; E/52*15=11 9/32"; E/52*30=22 17/32"; F=26 1/8"; F/2=13 1/16"; H=24 1/8"; H/2=12 1/16"; HEIGHT=41 5/16"; J=8"; J+K+L=41 3/32"; K=15 1/8"; L=17 31/32"; M=16"; M-(2*(D-L-K-J))=13 15/16"; MB_A=106 5/8"; MB_F=8 1/8"; MB_F-3"=5 1/8"; MB_HEIGHT=38 1/2"; MB_HEIGHT/2=19 1/4"; MB_N=14 3/16"; MB_N-(D-J-K-L)=13 5/32"; MB_P=34"; MB_P+.25"=34 1/4"; MB_P+MB_P+.5=68 1/2"; MB_P-4.5"=29 1/2"; MB_Q=34"; N=60"; N+(H/2)=72 1/16"; NOZZLE_BOTTOM_ID=12 13/16"; NOZZLE_BOTTOM_RAD=6 13/32"; NOZZLE_BOTTOM_RAD-3*2=13/32"; NOZZLE_HEIGHT=28"; NOZZLE_HEIGHT/7*2=7"; NOZZLE_SIZE=9"; NOZZLE_TOP_OD=13 1/2"; NOZZLE_TOP_RAD=6 3/4"; NOZZLE_WB/4=4 19/32"; NOZZLE_WB_OD=23"; NOZZLE_WB_RAD=11 1/2"; NOZZLE_WB_RAD-2"=9 1/2"; P=60"; R=24 1/4"; R*1.1=26 11/16"; R+((B/2)+1.5")=37 3/32"; R-((B/2)+1.5")=11 13/32"; RO/2=14 3/4"; RO2/2=83 1/8"; TRANSITION=9 1/16"; TRANSITION/2=4 17/32"; TRIP_Q=170 3/4"; TRIP_Q-4.5"=166 1/4"; Type Comments=Triple Vari-Plume Laboratory Exhaust Centrifugal Airfoil Class 1 Arr 10 With Mixing Box
- Triple_180_CAVP-12H_CLASS_1_With_Mixing_Box: ((M - (2 * (D - L - K - J))) / 2) + (TRANSITION / 2)=13"; (B/2)+1.5"=12 27/32"; (B/2)-.125"=11 7/32"; (D-J-K-L)*2=2 1/16"; (E/2)-((B/2)+1.5")=6 11/16"; (E/2)-((MB_P/2)+.125")=2 13/32"; (E/2)-(E/52*15)=8 1/4"; (F-((F-H)/2))/2=11 1/16"; (M - (2 * (D - L - K - J)))/2=6 31/32"; (MB_P/2)+.125"=17 1/8"; (MB_P/2-.125")+((F / 2) - 2")=-27 15/16"; (MB_P/2-.125")-((F / 2) - 2")=-5 13/16"; (MB_Q/2)+.125"=17 1/8"; (NOZZLE_HEIGHT - (NOZZLE_HEIGHT / 8 * 2)) / 2=12"; (NOZZLE_WB_OD - NOZZLE_TOP_OD) / 4=2 1/8"; -((MB_Q / 2) + 1/8")=-17 1/8"; -(F-((F-H)/2))/2=-11 1/16"; -MB_HEIGHT=-38 1/2"; -MB_P=-34"; -MB_P-.25=-34 1/4"; A=84 1/16"; A/2=42 1/32"; B=22 11/16"; B/2=11 11/32"; B/4=5 11/16"; C=52 13/16"; C/2=26 13/32"; CLASS=1"; D=42 1/8"; D-L-K-J=1 1/32"; D-M=26 1/8"; DUAL_Q=102 3/8"; DUAL_Q+.25"=102 5/8"; E=39 1/16"; E-(NOZZLE_RAD/3*2)=13 27/32"; E-N-N-H=-52 17/32"; E/2=19 17/32"; E/2-H/2=7 15/32"; E/52*15=11 9/32"; E/52*30=22 17/32"; F=26 1/8"; F/2=13 1/16"; H=24 1/8"; H/2=12 1/16"; HEIGHT=41 5/16"; J=8"; J+K+L=41 3/32"; K=15 1/8"; L=17 31/32"; M=16"; M-(2*(D-L-K-J))=13 15/16"; MB_A=106 5/8"; MB_F=8 1/8"; MB_F-3"=5 1/8"; MB_HEIGHT=38 1/2"; MB_HEIGHT/2=19 1/4"; MB_N=14 3/16"; MB_N-(D-J-K-L)=13 5/32"; MB_P=34"; MB_P+.25"=34 1/4"; MB_P+MB_P+.5=68 1/2"; MB_P-4.5"=29 1/2"; MB_Q=34"; N=60"; N+(H/2)=72 1/16"; NOZZLE_BOTTOM_ID=17 1/16"; NOZZLE_BOTTOM_RAD=8 17/32"; NOZZLE_BOTTOM_RAD-3*2=2 17/32"; NOZZLE_HEIGHT=32"; NOZZLE_HEIGHT/7*2=8"; NOZZLE_SIZE=12"; NOZZLE_TOP_OD=19 1/2"; NOZZLE_TOP_RAD=9 3/4"; NOZZLE_WB/4=5 19/32"; NOZZLE_WB_OD=28"; NOZZLE_WB_RAD=14"; NOZZLE_WB_RAD-2"=12"; P=60"; R=24 1/4"; R*1.1=26 11/16"; R+((B/2)+1.5")=37 3/32"; R-((B/2)+1.5")=11 13/32"; RO/2=14 3/4"; RO2/2=83 1/8"; TRANSITION=12 1/16"; TRANSITION/2=6 1/32"; TRIP_Q=170 3/4"; TRIP_Q-4.5"=166 1/4"; Type Comments=Triple Vari-Plume Laboratory Exhaust Centrifugal Airfoil Class 1 Arr 10 With Mixing Box
- Triple_180_CAVP-12L_CLASS_1_With_Mixing_Box: ((M - (2 * (D - L - K - J))) / 2) + (TRANSITION / 2)=13"; (B/2)+1.5"=12 27/32"; (B/2)-.125"=11 7/32"; (D-J-K-L)*2=2 1/16"; (E/2)-((B/2)+1.5")=6 11/16"; (E/2)-((MB_P/2)+.125")=2 13/32"; (E/2)-(E/52*15)=8 1/4"; (F-((F-H)/2))/2=11 1/16"; (M - (2 * (D - L - K - J)))/2=6 31/32"; (MB_P/2)+.125"=17 1/8"; (MB_P/2-.125")+((F / 2) - 2")=-27 15/16"; (MB_P/2-.125")-((F / 2) - 2")=-5 13/16"; (MB_Q/2)+.125"=17 1/8"; (NOZZLE_HEIGHT - (NOZZLE_HEIGHT / 8 * 2)) / 2=12"; (NOZZLE_WB_OD - NOZZLE_TOP_OD) / 4=2 1/8"; -((MB_Q / 2) + 1/8")=-17 1/8"; -(F-((F-H)/2))/2=-11 1/16"; -MB_HEIGHT=-38 1/2"; -MB_P=-34"; -MB_P-.25=-34 1/4"; A=84 1/16"; A/2=42 1/32"; B=22 11/16"; B/2=11 11/32"; B/4=5 11/16"; C=52 13/16"; C/2=26 13/32"; CLASS=1"; D=42 1/8"; D-L-K-J=1 1/32"; D-M=26 1/8"; DUAL_Q=102 3/8"; DUAL_Q+.25"=102 5/8"; E=39 1/16"; E-(NOZZLE_RAD/3*2)=13 27/32"; E-N-N-H=-52 17/32"; E/2=19 17/32"; E/2-H/2=7 15/32"; E/52*15=11 9/32"; E/52*30=22 17/32"; F=26 1/8"; F/2=13 1/16"; H=24 1/8"; H/2=12 1/16"; HEIGHT=41 5/16"; J=8"; J+K+L=41 3/32"; K=15 1/8"; L=17 31/32"; M=16"; M-(2*(D-L-K-J))=13 15/16"; MB_A=106 5/8"; MB_F=8 1/8"; MB_F-3"=5 1/8"; MB_HEIGHT=38 1/2"; MB_HEIGHT/2=19 1/4"; MB_N=14 3/16"; MB_N-(D-J-K-L)=13 5/32"; MB_P=34"; MB_P+.25"=34 1/4"; MB_P+MB_P+.5=68 1/2"; MB_P-4.5"=29 1/2"; MB_Q=34"; N=60"; N+(H/2)=72 1/16"; NOZZLE_BOTTOM_ID=17 1/16"; NOZZLE_BOTTOM_RAD=8 17/32"; NOZZLE_BOTTOM_RAD-3*2=2 17/32"; NOZZLE_HEIGHT=32"; NOZZLE_HEIGHT/7*2=8"; NOZZLE_SIZE=12"; NOZZLE_TOP_OD=19 1/2"; NOZZLE_TOP_RAD=9 3/4"; NOZZLE_WB/4=5 19/32"; NOZZLE_WB_OD=28"; NOZZLE_WB_RAD=14"; NOZZLE_WB_RAD-2"=12"; P=60"; R=24 1/4"; R*1.1=26 11/16"; R+((B/2)+1.5")=37 3/32"; R-((B/2)+1.5")=11 13/32"; RO/2=14 3/4"; RO2/2=83 1/8"; TRANSITION=12 1/16"; TRANSITION/2=6 1/32"; TRIP_Q=170 3/4"; TRIP_Q-4.5"=166 1/4"; Type Comments=Triple Vari-Plume Laboratory Exhaust Centrifugal Airfoil Class 1 Arr 10 With Mixing Box
- Triple_180_CAVP-9H_CLASS_2_With_Mixing_Box: ((M - (2 * (D - L - K - J))) / 2) + (TRANSITION / 2)=11 1/2"; (B/2)+1.5"=12 27/32"; (B/2)-.125"=11 7/32"; (D-J-K-L)*2=2 1/16"; (E/2)-((B/2)+1.5")=6 11/16"; (E/2)-((MB_P/2)+.125")=2 13/32"; (E/2)-(E/52*15)=8 1/4"; (F-((F-H)/2))/2=11 1/16"; (M - (2 * (D - L - K - J)))/2=6 31/32"; (MB_P/2)+.125"=17 1/8"; (MB_P/2-.125")+((F / 2) - 2")=-27 15/16"; (MB_P/2-.125")-((F / 2) - 2")=-5 13/16"; (MB_Q/2)+.125"=17 1/8"; (NOZZLE_HEIGHT - (NOZZLE_HEIGHT / 8 * 2)) / 2=10 1/2"; (NOZZLE_WB_OD - NOZZLE_TOP_OD) / 4=2 3/8"; -((MB_Q / 2) + 1/8")=-17 1/8"; -(F-((F-H)/2))/2=-11 1/16"; -MB_HEIGHT=-38 1/2"; -MB_P=-34"; -MB_P-.25=-34 1/4"; A=84 1/16"; A/2=42 1/32"; B=22 11/16"; B/2=11 11/32"; B/4=5 11/16"; C=52 13/16"; C/2=26 13/32"; CLASS=2"; D=46 1/8"; D-L-K-J=1 1/32"; D-M=30 1/8"; DUAL_Q=102 3/8"; DUAL_Q+.25"=102 5/8"; E=39 1/16"; E-(NOZZLE_RAD/3*2)=15 1/4"; E-N-N-H=-52 17/32"; E/2=19 17/32"; E/2-H/2=7 15/32"; E/52*15=11 9/32"; E/52*30=22 17/32"; F=26 1/8"; F/2=13 1/16"; H=24 1/8"; H/2=12 1/16"; HEIGHT=41 5/16"; J=7 3/4"; J+K+L=45 3/32"; K=19 3/8"; L=17 31/32"; M=16"; M-(2*(D-L-K-J))=13 15/16"; MB_A=110 5/8"; MB_F=8 1/8"; MB_F-3"=5 1/8"; MB_HEIGHT=38 1/2"; MB_HEIGHT/2=19 1/4"; MB_N=14 3/16"; MB_N-(D-J-K-L)=13 5/32"; MB_P=34"; MB_P+.25"=34 1/4"; MB_P+MB_P+.5=68 1/2"; MB_P-4.5"=29 1/2"; MB_Q=34"; N=60"; N+(H/2)=72 1/16"; NOZZLE_BOTTOM_ID=12 13/16"; NOZZLE_BOTTOM_RAD=6 13/32"; NOZZLE_BOTTOM_RAD-3*2=13/32"; NOZZLE_HEIGHT=28"; NOZZLE_HEIGHT/7*2=7"; NOZZLE_SIZE=9"; NOZZLE_TOP_OD=13 1/2"; NOZZLE_TOP_RAD=6 3/4"; NOZZLE_WB/4=4 19/32"; NOZZLE_WB_OD=23"; NOZZLE_WB_RAD=11 1/2"; NOZZLE_WB_RAD-2"=9 1/2"; P=60"; R=24 1/4"; R*1.1=26 11/16"; R+((B/2)+1.5")=37 3/32"; R-((B/2)+1.5")=11 13/32"; RO/2=14 3/4"; RO2/2=83 1/8"; TRANSITION=9 1/16"; TRANSITION/2=4 17/32"; TRIP_Q=170 3/4"; TRIP_Q-4.5"=166 1/4"; Type Comments=Triple Vari-Plume Laboratory Exhaust Centrifugal Airfoil Class 2 Arr 10 With Mixing Box
- Triple_180_CAVP-9L_CLASS_2_With_Mixing_Box: ((M - (2 * (D - L - K - J))) / 2) + (TRANSITION / 2)=11 1/2"; (B/2)+1.5"=12 27/32"; (B/2)-.125"=11 7/32"; (D-J-K-L)*2=2 1/16"; (E/2)-((B/2)+1.5")=6 11/16"; (E/2)-((MB_P/2)+.125")=2 13/32"; (E/2)-(E/52*15)=8 1/4"; (F-((F-H)/2))/2=11 1/16"; (M - (2 * (D - L - K - J)))/2=6 31/32"; (MB_P/2)+.125"=17 1/8"; (MB_P/2-.125")+((F / 2) - 2")=-27 15/16"; (MB_P/2-.125")-((F / 2) - 2")=-5 13/16"; (MB_Q/2)+.125"=17 1/8"; (NOZZLE_HEIGHT - (NOZZLE_HEIGHT / 8 * 2)) / 2=10 1/2"; (NOZZLE_WB_OD - NOZZLE_TOP_OD) / 4=2 3/8"; -((MB_Q / 2) + 1/8")=-17 1/8"; -(F-((F-H)/2))/2=-11 1/16"; -MB_HEIGHT=-38 1/2"; -MB_P=-34"; -MB_P-.25=-34 1/4"; A=84 1/16"; A/2=42 1/32"; B=22 11/16"; B/2=11 11/32"; B/4=5 11/16"; C=52 13/16"; C/2=26 13/32"; CLASS=2"; D=46 1/8"; D-L-K-J=1 1/32"; D-M=30 1/8"; DUAL_Q=102 3/8"; DUAL_Q+.25"=102 5/8"; E=39 1/16"; E-(NOZZLE_RAD/3*2)=15 1/4"; E-N-N-H=-52 17/32"; E/2=19 17/32"; E/2-H/2=7 15/32"; E/52*15=11 9/32"; E/52*30=22 17/32"; F=26 1/8"; F/2=13 1/16"; H=24 1/8"; H/2=12 1/16"; HEIGHT=41 5/16"; J=7 3/4"; J+K+L=45 3/32"; K=19 3/8"; L=17 31/32"; M=16"; M-(2*(D-L-K-J))=13 15/16"; MB_A=110 5/8"; MB_F=8 1/8"; MB_F-3"=5 1/8"; MB_HEIGHT=38 1/2"; MB_HEIGHT/2=19 1/4"; MB_N=14 3/16"; MB_N-(D-J-K-L)=13 5/32"; MB_P=34"; MB_P+.25"=34 1/4"; MB_P+MB_P+.5=68 1/2"; MB_P-4.5"=29 1/2"; MB_Q=34"; N=60"; N+(H/2)=72 1/16"; NOZZLE_BOTTOM_ID=12 13/16"; NOZZLE_BOTTOM_RAD=6 13/32"; NOZZLE_BOTTOM_RAD-3*2=13/32"; NOZZLE_HEIGHT=28"; NOZZLE_HEIGHT/7*2=7"; NOZZLE_SIZE=9"; NOZZLE_TOP_OD=13 1/2"; NOZZLE_TOP_RAD=6 3/4"; NOZZLE_WB/4=4 19/32"; NOZZLE_WB_OD=23"; NOZZLE_WB_RAD=11 1/2"; NOZZLE_WB_RAD-2"=9 1/2"; P=60"; R=24 1/4"; R*1.1=26 11/16"; R+((B/2)+1.5")=37 3/32"; R-((B/2)+1.5")=11 13/32"; RO/2=14 3/4"; RO2/2=83 1/8"; TRANSITION=9 1/16"; TRANSITION/2=4 17/32"; TRIP_Q=170 3/4"; TRIP_Q-4.5"=166 1/4"; Type Comments=Triple Vari-Plume Laboratory Exhaust Centrifugal Airfoil Class 2 Arr 10 With Mixing Box
- Triple_180_CAVP-12H_CLASS_2_With_Mixing_Box: ((M - (2 * (D - L - K - J))) / 2) + (TRANSITION / 2)=13"; (B/2)+1.5"=12 27/32"; (B/2)-.125"=11 7/32"; (D-J-K-L)*2=2 1/16"; (E/2)-((B/2)+1.5")=6 11/16"; (E/2)-((MB_P/2)+.125")=2 13/32"; (E/2)-(E/52*15)=8 1/4"; (F-((F-H)/2))/2=11 1/16"; (M - (2 * (D - L - K - J)))/2=6 31/32"; (MB_P/2)+.125"=17 1/8"; (MB_P/2-.125")+((F / 2) - 2")=-27 15/16"; (MB_P/2-.125")-((F / 2) - 2")=-5 13/16"; (MB_Q/2)+.125"=17 1/8"; (NOZZLE_HEIGHT - (NOZZLE_HEIGHT / 8 * 2)) / 2=12"; (NOZZLE_WB_OD - NOZZLE_TOP_OD) / 4=2 1/8"; -((MB_Q / 2) + 1/8")=-17 1/8"; -(F-((F-H)/2))/2=-11 1/16"; -MB_HEIGHT=-38 1/2"; -MB_P=-34"; -MB_P-.25=-34 1/4"; A=84 1/16"; A/2=42 1/32"; B=22 11/16"; B/2=11 11/32"; B/4=5 11/16"; C=52 13/16"; C/2=26 13/32"; CLASS=2"; D=46 1/8"; D-L-K-J=1 1/32"; D-M=30 1/8"; DUAL_Q=102 3/8"; DUAL_Q+.25"=102 5/8"; E=39 1/16"; E-(NOZZLE_RAD/3*2)=13 27/32"; E-N-N-H=-52 17/32"; E/2=19 17/32"; E/2-H/2=7 15/32"; E/52*15=11 9/32"; E/52*30=22 17/32"; F=26 1/8"; F/2=13 1/16"; H=24 1/8"; H/2=12 1/16"; HEIGHT=41 5/16"; J=7 3/4"; J+K+L=45 3/32"; K=19 3/8"; L=17 31/32"; M=16"; M-(2*(D-L-K-J))=13 15/16"; MB_A=110 5/8"; MB_F=8 1/8"; MB_F-3"=5 1/8"; MB_HEIGHT=38 1/2"; MB_HEIGHT/2=19 1/4"; MB_N=14 3/16"; MB_N-(D-J-K-L)=13 5/32"; MB_P=34"; MB_P+.25"=34 1/4"; MB_P+MB_P+.5=68 1/2"; MB_P-4.5"=29 1/2"; MB_Q=34"; N=60"; N+(H/2)=72 1/16"; NOZZLE_BOTTOM_ID=17 1/16"; NOZZLE_BOTTOM_RAD=8 17/32"; NOZZLE_BOTTOM_RAD-3*2=2 17/32"; NOZZLE_HEIGHT=32"; NOZZLE_HEIGHT/7*2=8"; NOZZLE_SIZE=12"; NOZZLE_TOP_OD=19 1/2"; NOZZLE_TOP_RAD=9 3/4"; NOZZLE_WB/4=5 19/32"; NOZZLE_WB_OD=28"; NOZZLE_WB_RAD=14"; NOZZLE_WB_RAD-2"=12"; P=60"; R=24 1/4"; R*1.1=26 11/16"; R+((B/2)+1.5")=37 3/32"; R-((B/2)+1.5")=11 13/32"; RO/2=14 3/4"; RO2/2=83 1/8"; TRANSITION=12 1/16"; TRANSITION/2=6 1/32"; TRIP_Q=170 3/4"; TRIP_Q-4.5"=166 1/4"; Type Comments=Triple Vari-Plume Laboratory Exhaust Centrifugal Airfoil Class 2 Arr 10 With Mixing Box
- Triple_180_CAVP-12L_CLASS_2_With_Mixing_Box: ((M - (2 * (D - L - K - J))) / 2) + (TRANSITION / 2)=13"; (B/2)+1.5"=12 27/32"; (B/2)-.125"=11 7/32"; (D-J-K-L)*2=2 1/16"; (E/2)-((B/2)+1.5")=6 11/16"; (E/2)-((MB_P/2)+.125")=2 13/32"; (E/2)-(E/52*15)=8 1/4"; (F-((F-H)/2))/2=11 1/16"; (M - (2 * (D - L - K - J)))/2=6 31/32"; (MB_P/2)+.125"=17 1/8"; (MB_P/2-.125")+((F / 2) - 2")=-27 15/16"; (MB_P/2-.125")-((F / 2) - 2")=-5 13/16"; (MB_Q/2)+.125"=17 1/8"; (NOZZLE_HEIGHT - (NOZZLE_HEIGHT / 8 * 2)) / 2=12"; (NOZZLE_WB_OD - NOZZLE_TOP_OD) / 4=2 1/8"; -((MB_Q / 2) + 1/8")=-17 1/8"; -(F-((F-H)/2))/2=-11 1/16"; -MB_HEIGHT=-38 1/2"; -MB_P=-34"; -MB_P-.25=-34 1/4"; A=84 1/16"; A/2=42 1/32"; B=22 11/16"; B/2=11 11/32"; B/4=5 11/16"; C=52 13/16"; C/2=26 13/32"; CLASS=2"; D=46 1/8"; D-L-K-J=1 1/32"; D-M=30 1/8"; DUAL_Q=102 3/8"; DUAL_Q+.25"=102 5/8"; E=39 1/16"; E-(NOZZLE_RAD/3*2)=13 27/32"; E-N-N-H=-52 17/32"; E/2=19 17/32"; E/2-H/2=7 15/32"; E/52*15=11 9/32"; E/52*30=22 17/32"; F=26 1/8"; F/2=13 1/16"; H=24 1/8"; H/2=12 1/16"; HEIGHT=41 5/16"; J=7 3/4"; J+K+L=45 3/32"; K=19 3/8"; L=17 31/32"; M=16"; M-(2*(D-L-K-J))=13 15/16"; MB_A=110 5/8"; MB_F=8 1/8"; MB_F-3"=5 1/8"; MB_HEIGHT=38 1/2"; MB_HEIGHT/2=19 1/4"; MB_N=14 3/16"; MB_N-(D-J-K-L)=13 5/32"; MB_P=34"; MB_P+.25"=34 1/4"; MB_P+MB_P+.5=68 1/2"; MB_P-4.5"=29 1/2"; MB_Q=34"; N=60"; N+(H/2)=72 1/16"; NOZZLE_BOTTOM_ID=17 1/16"; NOZZLE_BOTTOM_RAD=8 17/32"; NOZZLE_BOTTOM_RAD-3*2=2 17/32"; NOZZLE_HEIGHT=32"; NOZZLE_HEIGHT/7*2=8"; NOZZLE_SIZE=12"; NOZZLE_TOP_OD=19 1/2"; NOZZLE_TOP_RAD=9 3/4"; NOZZLE_WB/4=5 19/32"; NOZZLE_WB_OD=28"; NOZZLE_WB_RAD=14"; NOZZLE_WB_RAD-2"=12"; P=60"; R=24 1/4"; R*1.1=26 11/16"; R+((B/2)+1.5")=37 3/32"; R-((B/2)+1.5")=11 13/32"; RO/2=14 3/4"; RO2/2=83 1/8"; TRANSITION=12 1/16"; TRANSITION/2=6 1/32"; TRIP_Q=170 3/4"; TRIP_Q-4.5"=166 1/4"; Type Comments=Triple Vari-Plume Laboratory Exhaust Centrifugal Airfoil Class 2 Arr 10 With Mixing Box
- Triple_195_CAVP-9L_CLASS_1_With_Mixing_Box: ((M - (2 * (D - L - K - J))) / 2) + (TRANSITION / 2)=12 1/8"; (B/2)+1.5"=13 19/32"; (B/2)-.125"=11 31/32"; (D-J-K-L)*2=2"; (E/2)-((B/2)+1.5")=7 1/2"; (E/2)-((MB_P/2)+.125")=3 15/32"; (E/2)-(E/52*15)=8 15/16"; (F-((F-H)/2))/2=11 3/4"; (M - (2 * (D - L - K - J)))/2=7 19/32"; (MB_P/2)+.125"=17 5/8"; (MB_P/2-.125")+((F / 2) - 2")=-29 1/8"; (MB_P/2-.125")-((F / 2) - 2")=-5 5/8"; (MB_Q/2)+.125"=17 5/8"; (NOZZLE_HEIGHT - (NOZZLE_HEIGHT / 8 * 2)) / 2=10 1/2"; (NOZZLE_WB_OD - NOZZLE_TOP_OD) / 4=2 3/8"; -((MB_Q / 2) + 1/8")=-17 5/8"; -(F-((F-H)/2))/2=-11 3/4"; -MB_HEIGHT=-40"; -MB_P=-35"; -MB_P-.25=-35 1/4"; A=96 3/4"; A/2=48 3/8"; B=24 3/16"; B/2=12 3/32"; B/4=6 1/16"; C=54 1/4"; C/2=27 1/8"; CLASS=1"; D=43 5/16"; D-L-K-J=1"; D-M=26 1/8"; DUAL_Q=105 3/8"; DUAL_Q+.25"=105 5/8"; E=42 3/16"; E-(NOZZLE_RAD/3*2)=16 13/16"; E-N-N-H=2"; E/2=21 3/32"; E/2-H/2=8 11/32"; E/52*15=12 5/32"; E/52*30=24 11/32"; F=27 1/2"; F/2=13 3/4"; H=25 1/2"; H/2=12 3/4"; HEIGHT=42 11/16"; J=8"; J+K+L=42 5/16"; K=15 1/8"; L=19 3/16"; M=17 3/16"; M-(2*(D-L-K-J))=15 3/16"; MB_A=110"; MB_F=7 3/8"; MB_F-3"=4 3/8"; MB_HEIGHT=40"; MB_HEIGHT/2=20"; MB_N=14 3/16"; MB_N-(D-J-K-L)=13 3/16"; MB_P=35"; MB_P+.25"=35 1/4"; MB_P+MB_P+.5=70 1/2"; MB_P-4.5"=30 1/2"; MB_Q=35"; N=6 11/32"; N+(H/2)=19 3/32"; NOZZLE_BOTTOM_ID=12 13/16"; NOZZLE_BOTTOM_RAD=6 13/32"; NOZZLE_BOTTOM_RAD-3*2=13/32"; NOZZLE_HEIGHT=28"; NOZZLE_HEIGHT/7*2=7"; NOZZLE_SIZE=9"; NOZZLE_TOP_OD=13 1/2"; NOZZLE_TOP_RAD=6 3/4"; NOZZLE_WB/4=4 19/32"; NOZZLE_WB_OD=23"; NOZZLE_WB_RAD=11 1/2"; NOZZLE_WB_RAD-2"=9 1/2"; P=60"; R=24 1/4"; R*1.1=26 11/16"; R+((B/2)+1.5")=37 27/32"; R-((B/2)+1.5")=10 21/32"; RO/2=15 1/4"; RO2/2=85 5/8"; TRANSITION=9 1/16"; TRANSITION/2=4 17/32"; TRIP_Q=175 3/4"; TRIP_Q-4.5"=171 1/4"; Type Comments=Triple Vari-Plume Laboratory Exhaust Centrifugal Airfoil Class 1 Arr 10 With Mixing Box
- Triple_195_CAVP-9H_CLASS_1_With_Mixing_Box: ((M - (2 * (D - L - K - J))) / 2) + (TRANSITION / 2)=12 1/8"; (B/2)+1.5"=13 19/32"; (B/2)-.125"=11 31/32"; (D-J-K-L)*2=2"; (E/2)-((B/2)+1.5")=7 1/2"; (E/2)-((MB_P/2)+.125")=3 15/32"; (E/2)-(E/52*15)=8 15/16"; (F-((F-H)/2))/2=11 3/4"; (M - (2 * (D - L - K - J)))/2=7 19/32"; (MB_P/2)+.125"=17 5/8"; (MB_P/2-.125")+((F / 2) - 2")=-29 1/8"; (MB_P/2-.125")-((F / 2) - 2")=-5 5/8"; (MB_Q/2)+.125"=17 5/8"; (NOZZLE_HEIGHT - (NOZZLE_HEIGHT / 8 * 2)) / 2=10 1/2"; (NOZZLE_WB_OD - NOZZLE_TOP_OD) / 4=2 3/8"; -((MB_Q / 2) + 1/8")=-17 5/8"; -(F-((F-H)/2))/2=-11 3/4"; -MB_HEIGHT=-40"; -MB_P=-35"; -MB_P-.25=-35 1/4"; A=96 3/4"; A/2=48 3/8"; B=24 3/16"; B/2=12 3/32"; B/4=6 1/16"; C=54 1/4"; C/2=27 1/8"; CLASS=1"; D=43 5/16"; D-L-K-J=1"; D-M=26 1/8"; DUAL_Q=105 3/8"; DUAL_Q+.25"=105 5/8"; E=42 3/16"; E-(NOZZLE_RAD/3*2)=16 13/16"; E-N-N-H=2"; E/2=21 3/32"; E/2-H/2=8 11/32"; E/52*15=12 5/32"; E/52*30=24 11/32"; F=27 1/2"; F/2=13 3/4"; H=25 1/2"; H/2=12 3/4"; HEIGHT=42 11/16"; J=8"; J+K+L=42 5/16"; K=15 1/8"; L=19 3/16"; M=17 3/16"; M-(2*(D-L-K-J))=15 3/16"; MB_A=110"; MB_F=7 3/8"; MB_F-3"=4 3/8"; MB_HEIGHT=40"; MB_HEIGHT/2=20"; MB_N=14 3/16"; MB_N-(D-J-K-L)=13 3/16"; MB_P=35"; MB_P+.25"=35 1/4"; MB_P+MB_P+.5=70 1/2"; MB_P-4.5"=30 1/2"; MB_Q=35"; N=6 11/32"; N+(H/2)=19 3/32"; NOZZLE_BOTTOM_ID=12 13/16"; NOZZLE_BOTTOM_RAD=6 13/32"; NOZZLE_BOTTOM_RAD-3*2=13/32"; NOZZLE_HEIGHT=28"; NOZZLE_HEIGHT/7*2=7"; NOZZLE_SIZE=9"; NOZZLE_TOP_OD=13 1/2"; NOZZLE_TOP_RAD=6 3/4"; NOZZLE_WB/4=4 19/32"; NOZZLE_WB_OD=23"; NOZZLE_WB_RAD=11 1/2"; NOZZLE_WB_RAD-2"=9 1/2"; P=60"; R=24 1/4"; R*1.1=26 11/16"; R+((B/2)+1.5")=37 27/32"; R-((B/2)+1.5")=10 21/32"; RO/2=15 1/4"; RO2/2=85 5/8"; TRANSITION=9 1/16"; TRANSITION/2=4 17/32"; TRIP_Q=175 3/4"; TRIP_Q-4.5"=171 1/4"; Type Comments=Triple Vari-Plume Laboratory Exhaust Centrifugal Airfoil Class 1 Arr 10 With Mixing Box
- Triple_195_CAVP-12L_CLASS_1_With_Mixing_Box: ((M - (2 * (D - L - K - J))) / 2) + (TRANSITION / 2)=13 5/8"; (B/2)+1.5"=13 19/32"; (B/2)-.125"=11 31/32"; (D-J-K-L)*2=2"; (E/2)-((B/2)+1.5")=7 1/2"; (E/2)-((MB_P/2)+.125")=3 15/32"; (E/2)-(E/52*15)=8 15/16"; (F-((F-H)/2))/2=11 3/4"; (M - (2 * (D - L - K - J)))/2=7 19/32"; (MB_P/2)+.125"=17 5/8"; (MB_P/2-.125")+((F / 2) - 2")=-29 1/8"; (MB_P/2-.125")-((F / 2) - 2")=-5 5/8"; (MB_Q/2)+.125"=17 5/8"; (NOZZLE_HEIGHT - (NOZZLE_HEIGHT / 8 * 2)) / 2=12"; (NOZZLE_WB_OD - NOZZLE_TOP_OD) / 4=2 1/8"; -((MB_Q / 2) + 1/8")=-17 5/8"; -(F-((F-H)/2))/2=-11 3/4"; -MB_HEIGHT=-40"; -MB_P=-35"; -MB_P-.25=-35 1/4"; A=96 3/4"; A/2=48 3/8"; B=24 3/16"; B/2=12 3/32"; B/4=6 1/16"; C=54 1/4"; C/2=27 1/8"; CLASS=1"; D=43 5/16"; D-L-K-J=1"; D-M=26 1/8"; DUAL_Q=105 3/8"; DUAL_Q+.25"=105 5/8"; E=42 3/16"; E-(NOZZLE_RAD/3*2)=15 13/32"; E-N-N-H=2"; E/2=21 3/32"; E/2-H/2=8 11/32"; E/52*15=12 5/32"; E/52*30=24 11/32"; F=27 1/2"; F/2=13 3/4"; H=25 1/2"; H/2=12 3/4"; HEIGHT=42 11/16"; J=8"; J+K+L=42 5/16"; K=15 1/8"; L=19 3/16"; M=17 3/16"; M-(2*(D-L-K-J))=15 3/16"; MB_A=110"; MB_F=7 3/8"; MB_F-3"=4 3/8"; MB_HEIGHT=40"; MB_HEIGHT/2=20"; MB_N=14 3/16"; MB_N-(D-J-K-L)=13 3/16"; MB_P=35"; MB_P+.25"=35 1/4"; MB_P+MB_P+.5=70 1/2"; MB_P-4.5"=30 1/2"; MB_Q=35"; N=6 11/32"; N+(H/2)=19 3/32"; NOZZLE_BOTTOM_ID=17 1/16"; NOZZLE_BOTTOM_RAD=8 17/32"; NOZZLE_BOTTOM_RAD-3*2=2 17/32"; NOZZLE_HEIGHT=32"; NOZZLE_HEIGHT/7*2=8"; NOZZLE_SIZE=12"; NOZZLE_TOP_OD=19 1/2"; NOZZLE_TOP_RAD=9 3/4"; NOZZLE_WB/4=5 19/32"; NOZZLE_WB_OD=28"; NOZZLE_WB_RAD=14"; NOZZLE_WB_RAD-2"=12"; P=60"; R=24 1/4"; R*1.1=26 11/16"; R+((B/2)+1.5")=37 27/32"; R-((B/2)+1.5")=10 21/32"; RO/2=15 1/4"; RO2/2=85 5/8"; TRANSITION=12 1/16"; TRANSITION/2=6 1/32"; TRIP_Q=175 3/4"; TRIP_Q-4.5"=171 1/4"; Type Comments=Triple Vari-Plume Laboratory Exhaust Centrifugal Airfoil Class 1 Arr 10 With Mixing Box
- Triple_195_CAVP-12H_CLASS_1_With_Mixing_Box: ((M - (2 * (D - L - K - J))) / 2) + (TRANSITION / 2)=13 5/8"; (B/2)+1.5"=13 19/32"; (B/2)-.125"=11 31/32"; (D-J-K-L)*2=2"; (E/2)-((B/2)+1.5")=7 1/2"; (E/2)-((MB_P/2)+.125")=3 15/32"; (E/2)-(E/52*15)=8 15/16"; (F-((F-H)/2))/2=11 3/4"; (M - (2 * (D - L - K - J)))/2=7 19/32"; (MB_P/2)+.125"=17 5/8"; (MB_P/2-.125")+((F / 2) - 2")=-29 1/8"; (MB_P/2-.125")-((F / 2) - 2")=-5 5/8"; (MB_Q/2)+.125"=17 5/8"; (NOZZLE_HEIGHT - (NOZZLE_HEIGHT / 8 * 2)) / 2=12"; (NOZZLE_WB_OD - NOZZLE_TOP_OD) / 4=2 1/8"; -((MB_Q / 2) + 1/8")=-17 5/8"; -(F-((F-H)/2))/2=-11 3/4"; -MB_HEIGHT=-40"; -MB_P=-35"; -MB_P-.25=-35 1/4"; A=96 3/4"; A/2=48 3/8"; B=24 3/16"; B/2=12 3/32"; B/4=6 1/16"; C=54 1/4"; C/2=27 1/8"; CLASS=1"; D=43 5/16"; D-L-K-J=1"; D-M=26 1/8"; DUAL_Q=105 3/8"; DUAL_Q+.25"=105 5/8"; E=42 3/16"; E-(NOZZLE_RAD/3*2)=15 13/32"; E-N-N-H=2"; E/2=21 3/32"; E/2-H/2=8 11/32"; E/52*15=12 5/32"; E/52*30=24 11/32"; F=27 1/2"; F/2=13 3/4"; H=25 1/2"; H/2=12 3/4"; HEIGHT=42 11/16"; J=8"; J+K+L=42 5/16"; K=15 1/8"; L=19 3/16"; M=17 3/16"; M-(2*(D-L-K-J))=15 3/16"; MB_A=110"; MB_F=7 3/8"; MB_F-3"=4 3/8"; MB_HEIGHT=40"; MB_HEIGHT/2=20"; MB_N=14 3/16"; MB_N-(D-J-K-L)=13 3/16"; MB_P=35"; MB_P+.25"=35 1/4"; MB_P+MB_P+.5=70 1/2"; MB_P-4.5"=30 1/2"; MB_Q=35"; N=6 11/32"; N+(H/2)=19 3/32"; NOZZLE_BOTTOM_ID=17 1/16"; NOZZLE_BOTTOM_RAD=8 17/32"; NOZZLE_BOTTOM_RAD-3*2=2 17/32"; NOZZLE_HEIGHT=32"; NOZZLE_HEIGHT/7*2=8"; NOZZLE_SIZE=12"; NOZZLE_TOP_OD=19 1/2"; NOZZLE_TOP_RAD=9 3/4"; NOZZLE_WB/4=5 19/32"; NOZZLE_WB_OD=28"; NOZZLE_WB_RAD=14"; NOZZLE_WB_RAD-2"=12"; P=60"; R=24 1/4"; R*1.1=26 11/16"; R+((B/2)+1.5")=37 27/32"; R-((B/2)+1.5")=10 21/32"; RO/2=15 1/4"; RO2/2=85 5/8"; TRANSITION=12 1/16"; TRANSITION/2=6 1/32"; TRIP_Q=175 3/4"; TRIP_Q-4.5"=171 1/4"; Type Comments=Triple Vari-Plume Laboratory Exhaust Centrifugal Airfoil Class 1 Arr 10 With Mixing Box
- Triple_195_CAVP-15L_CLASS_1_With_Mixing_Box: ((M - (2 * (D - L - K - J))) / 2) + (TRANSITION / 2)=15 5/32"; (B/2)+1.5"=13 19/32"; (B/2)-.125"=11 31/32"; (D-J-K-L)*2=2"; (E/2)-((B/2)+1.5")=7 1/2"; (E/2)-((MB_P/2)+.125")=3 15/32"; (E/2)-(E/52*15)=8 15/16"; (F-((F-H)/2))/2=11 3/4"; (M - (2 * (D - L - K - J)))/2=7 19/32"; (MB_P/2)+.125"=17 5/8"; (MB_P/2-.125")+((F / 2) - 2")=-29 1/8"; (MB_P/2-.125")-((F / 2) - 2")=-5 5/8"; (MB_Q/2)+.125"=17 5/8"; (NOZZLE_HEIGHT - (NOZZLE_HEIGHT / 8 * 2)) / 2=16 1/8"; (NOZZLE_WB_OD - NOZZLE_TOP_OD) / 4=3 1/4"; -((MB_Q / 2) + 1/8")=-17 5/8"; -(F-((F-H)/2))/2=-11 3/4"; -MB_HEIGHT=-40"; -MB_P=-35"; -MB_P-.25=-35 1/4"; A=96 3/4"; A/2=48 3/8"; B=24 3/16"; B/2=12 3/32"; B/4=6 1/16"; C=54 1/4"; C/2=27 1/8"; CLASS=1"; D=43 5/16"; D-L-K-J=1"; D-M=26 1/8"; DUAL_Q=105 3/8"; DUAL_Q+.25"=105 5/8"; E=42 3/16"; E-(NOZZLE_RAD/3*2)=13 31/32"; E-N-N-H=2"; E/2=21 3/32"; E/2-H/2=8 11/32"; E/52*15=12 5/32"; E/52*30=24 11/32"; F=27 1/2"; F/2=13 3/4"; H=25 1/2"; H/2=12 3/4"; HEIGHT=42 11/16"; J=8"; J+K+L=42 5/16"; K=15 1/8"; L=19 3/16"; M=17 3/16"; M-(2*(D-L-K-J))=15 3/16"; MB_A=110"; MB_F=7 3/8"; MB_F-3"=4 3/8"; MB_HEIGHT=40"; MB_HEIGHT/2=20"; MB_N=14 3/16"; MB_N-(D-J-K-L)=13 3/16"; MB_P=35"; MB_P+.25"=35 1/4"; MB_P+MB_P+.5=70 1/2"; MB_P-4.5"=30 1/2"; MB_Q=35"; N=6 11/32"; N+(H/2)=19 3/32"; NOZZLE_BOTTOM_ID=21 3/8"; NOZZLE_BOTTOM_RAD=10 11/16"; NOZZLE_BOTTOM_RAD-3*2=4 11/16"; NOZZLE_HEIGHT=43"; NOZZLE_HEIGHT/7*2=10 3/4"; NOZZLE_SIZE=15"; NOZZLE_TOP_OD=23"; NOZZLE_TOP_RAD=11 1/2"; NOZZLE_WB/4=7 3/16"; NOZZLE_WB_OD=36"; NOZZLE_WB_RAD=18"; NOZZLE_WB_RAD-2"=16"; P=60"; R=24 1/4"; R*1.1=26 11/16"; R+((B/2)+1.5")=37 27/32"; R-((B/2)+1.5")=10 21/32"; RO/2=15 1/4"; RO2/2=85 5/8"; TRANSITION=15 1/8"; TRANSITION/2=7 9/16"; TRIP_Q=175 3/4"; TRIP_Q-4.5"=171 1/4"; Type Comments=Triple Vari-Plume Laboratory Exhaust Centrifugal Airfoil Class 1 Arr 10 With Mixing Box
- Triple_195_CAVP-15H_CLASS_1_With_Mixing_Box: ((M - (2 * (D - L - K - J))) / 2) + (TRANSITION / 2)=15 5/32"; (B/2)+1.5"=13 19/32"; (B/2)-.125"=11 31/32"; (D-J-K-L)*2=2"; (E/2)-((B/2)+1.5")=7 1/2"; (E/2)-((MB_P/2)+.125")=3 15/32"; (E/2)-(E/52*15)=8 15/16"; (F-((F-H)/2))/2=11 3/4"; (M - (2 * (D - L - K - J)))/2=7 19/32"; (MB_P/2)+.125"=17 5/8"; (MB_P/2-.125")+((F / 2) - 2")=-29 1/8"; (MB_P/2-.125")-((F / 2) - 2")=-5 5/8"; (MB_Q/2)+.125"=17 5/8"; (NOZZLE_HEIGHT - (NOZZLE_HEIGHT / 8 * 2)) / 2=16 1/8"; (NOZZLE_WB_OD - NOZZLE_TOP_OD) / 4=3 1/4"; -((MB_Q / 2) + 1/8")=-17 5/8"; -(F-((F-H)/2))/2=-11 3/4"; -MB_HEIGHT=-40"; -MB_P=-35"; -MB_P-.25=-35 1/4"; A=96 3/4"; A/2=48 3/8"; B=24 3/16"; B/2=12 3/32"; B/4=6 1/16"; C=54 1/4"; C/2=27 1/8"; CLASS=1"; D=43 5/16"; D-L-K-J=1"; D-M=26 1/8"; DUAL_Q=105 3/8"; DUAL_Q+.25"=105 5/8"; E=42 3/16"; E-(NOZZLE_RAD/3*2)=13 31/32"; E-N-N-H=2"; E/2=21 3/32"; E/2-H/2=8 11/32"; E/52*15=12 5/32"; E/52*30=24 11/32"; F=27 1/2"; F/2=13 3/4"; H=25 1/2"; H/2=12 3/4"; HEIGHT=42 11/16"; J=8"; J+K+L=42 5/16"; K=15 1/8"; L=19 3/16"; M=17 3/16"; M-(2*(D-L-K-J))=15 3/16"; MB_A=110"; MB_F=7 3/8"; MB_F-3"=4 3/8"; MB_HEIGHT=40"; MB_HEIGHT/2=20"; MB_N=14 3/16"; MB_N-(D-J-K-L)=13 3/16"; MB_P=35"; MB_P+.25"=35 1/4"; MB_P+MB_P+.5=70 1/2"; MB_P-4.5"=30 1/2"; MB_Q=35"; N=6 11/32"; N+(H/2)=19 3/32"; NOZZLE_BOTTOM_ID=21 3/8"; NOZZLE_BOTTOM_RAD=10 11/16"; NOZZLE_BOTTOM_RAD-3*2=4 11/16"; NOZZLE_HEIGHT=43"; NOZZLE_HEIGHT/7*2=10 3/4"; NOZZLE_SIZE=15"; NOZZLE_TOP_OD=23"; NOZZLE_TOP_RAD=11 1/2"; NOZZLE_WB/4=7 3/16"; NOZZLE_WB_OD=36"; NOZZLE_WB_RAD=18"; NOZZLE_WB_RAD-2"=16"; P=60"; R=24 1/4"; R*1.1=26 11/16"; R+((B/2)+1.5")=37 27/32"; R-((B/2)+1.5")=10 21/32"; RO/2=15 1/4"; RO2/2=85 5/8"; TRANSITION=15 1/8"; TRANSITION/2=7 9/16"; TRIP_Q=175 3/4"; TRIP_Q-4.5"=171 1/4"; Type Comments=Triple Vari-Plume Laboratory Exhaust Centrifugal Airfoil Class 1 Arr 10 With Mixing Box
- Triple_195_CAVP-9L_CLASS_2_With_Mixing_Box: ((M - (2 * (D - L - K - J))) / 2) + (TRANSITION / 2)=12 1/8"; (B/2)+1.5"=13 19/32"; (B/2)-.125"=11 31/32"; (D-J-K-L)*2=2"; (E/2)-((B/2)+1.5")=7 1/2"; (E/2)-((MB_P/2)+.125")=3 15/32"; (E/2)-(E/52*15)=8 15/16"; (F-((F-H)/2))/2=11 3/4"; (M - (2 * (D - L - K - J)))/2=7 19/32"; (MB_P/2)+.125"=17 5/8"; (MB_P/2-.125")+((F / 2) - 2")=-29 1/8"; (MB_P/2-.125")-((F / 2) - 2")=-5 5/8"; (MB_Q/2)+.125"=17 5/8"; (NOZZLE_HEIGHT - (NOZZLE_HEIGHT / 8 * 2)) / 2=10 1/2"; (NOZZLE_WB_OD - NOZZLE_TOP_OD) / 4=2 3/8"; -((MB_Q / 2) + 1/8")=-17 5/8"; -(F-((F-H)/2))/2=-11 3/4"; -MB_HEIGHT=-40"; -MB_P=-35"; -MB_P-.25=-35 1/4"; A=96 3/4"; A/2=48 3/8"; B=24 3/16"; B/2=12 3/32"; B/4=6 1/16"; C=54 1/4"; C/2=27 1/8"; CLASS=2"; D=47 5/16"; D-L-K-J=1"; D-M=30 1/8"; DUAL_Q=105 3/8"; DUAL_Q+.25"=105 5/8"; E=42 3/16"; E-(NOZZLE_RAD/3*2)=16 13/16"; E-N-N-H=1 27/32"; E/2=21 3/32"; E/2-H/2=8 11/32"; E/52*15=12 5/32"; E/52*30=24 11/32"; F=27 1/2"; F/2=13 3/4"; H=25 1/2"; H/2=12 3/4"; HEIGHT=42 11/16"; J=7 3/4"; J+K+L=46 5/16"; K=19 3/8"; L=19 3/16"; M=17 3/16"; M-(2*(D-L-K-J))=15 3/16"; MB_A=114"; MB_F=7 3/8"; MB_F-3"=4 3/8"; MB_HEIGHT=40"; MB_HEIGHT/2=20"; MB_N=14 3/16"; MB_N-(D-J-K-L)=13 3/16"; MB_P=35"; MB_P+.25"=35 1/4"; MB_P+MB_P+.5=70 1/2"; MB_P-4.5"=30 1/2"; MB_Q=35"; N=6 1/2"; N+(H/2)=19 1/4"; NOZZLE_BOTTOM_ID=12 13/16"; NOZZLE_BOTTOM_RAD=6 13/32"; NOZZLE_BOTTOM_RAD-3*2=13/32"; NOZZLE_HEIGHT=28"; NOZZLE_HEIGHT/7*2=7"; NOZZLE_SIZE=9"; NOZZLE_TOP_OD=13 1/2"; NOZZLE_TOP_RAD=6 3/4"; NOZZLE_WB/4=4 19/32"; NOZZLE_WB_OD=23"; NOZZLE_WB_RAD=11 1/2"; NOZZLE_WB_RAD-2"=9 1/2"; P=60"; R=24 1/4"; R*1.1=26 11/16"; R+((B/2)+1.5")=37 27/32"; R-((B/2)+1.5")=10 21/32"; RO/2=15 1/4"; RO2/2=85 5/8"; TRANSITION=9 1/16"; TRANSITION/2=4 17/32"; TRIP_Q=175 3/4"; TRIP_Q-4.5"=171 1/4"; Type Comments=Triple Vari-Plume Laboratory Exhaust Centrifugal Airfoil Class 2 Arr 10 With Mixing Box
- Triple_195_CAVP-9H_CLASS_2_With_Mixing_Box: ((M - (2 * (D - L - K - J))) / 2) + (TRANSITION / 2)=12 1/8"; (B/2)+1.5"=13 19/32"; (B/2)-.125"=11 31/32"; (D-J-K-L)*2=2"; (E/2)-((B/2)+1.5")=7 1/2"; (E/2)-((MB_P/2)+.125")=3 15/32"; (E/2)-(E/52*15)=8 15/16"; (F-((F-H)/2))/2=11 3/4"; (M - (2 * (D - L - K - J)))/2=7 19/32"; (MB_P/2)+.125"=17 5/8"; (MB_P/2-.125")+((F / 2) - 2")=-29 1/8"; (MB_P/2-.125")-((F / 2) - 2")=-5 5/8"; (MB_Q/2)+.125"=17 5/8"; (NOZZLE_HEIGHT - (NOZZLE_HEIGHT / 8 * 2)) / 2=10 1/2"; (NOZZLE_WB_OD - NOZZLE_TOP_OD) / 4=2 3/8"; -((MB_Q / 2) + 1/8")=-17 5/8"; -(F-((F-H)/2))/2=-11 3/4"; -MB_HEIGHT=-40"; -MB_P=-35"; -MB_P-.25=-35 1/4"; A=96 3/4"; A/2=48 3/8"; B=24 3/16"; B/2=12 3/32"; B/4=6 1/16"; C=54 1/4"; C/2=27 1/8"; CLASS=2"; D=47 5/16"; D-L-K-J=1"; D-M=30 1/8"; DUAL_Q=105 3/8"; DUAL_Q+.25"=105 5/8"; E=42 3/16"; E-(NOZZLE_RAD/3*2)=16 13/16"; E-N-N-H=1 27/32"; E/2=21 3/32"; E/2-H/2=8 11/32"; E/52*15=12 5/32"; E/52*30=24 11/32"; F=27 1/2"; F/2=13 3/4"; H=25 1/2"; H/2=12 3/4"; HEIGHT=42 11/16"; J=7 3/4"; J+K+L=46 5/16"; K=19 3/8"; L=19 3/16"; M=17 3/16"; M-(2*(D-L-K-J))=15 3/16"; MB_A=114"; MB_F=7 3/8"; MB_F-3"=4 3/8"; MB_HEIGHT=40"; MB_HEIGHT/2=20"; MB_N=14 3/16"; MB_N-(D-J-K-L)=13 3/16"; MB_P=35"; MB_P+.25"=35 1/4"; MB_P+MB_P+.5=70 1/2"; MB_P-4.5"=30 1/2"; MB_Q=35"; N=6 1/2"; N+(H/2)=19 1/4"; NOZZLE_BOTTOM_ID=12 13/16"; NOZZLE_BOTTOM_RAD=6 13/32"; NOZZLE_BOTTOM_RAD-3*2=13/32"; NOZZLE_HEIGHT=28"; NOZZLE_HEIGHT/7*2=7"; NOZZLE_SIZE=9"; NOZZLE_TOP_OD=13 1/2"; NOZZLE_TOP_RAD=6 3/4"; NOZZLE_WB/4=4 19/32"; NOZZLE_WB_OD=23"; NOZZLE_WB_RAD=11 1/2"; NOZZLE_WB_RAD-2"=9 1/2"; P=60"; R=24 1/4"; R*1.1=26 11/16"; R+((B/2)+1.5")=37 27/32"; R-((B/2)+1.5")=10 21/32"; RO/2=15 1/4"; RO2/2=85 5/8"; TRANSITION=9 1/16"; TRANSITION/2=4 17/32"; TRIP_Q=175 3/4"; TRIP_Q-4.5"=171 1/4"; Type Comments=Triple Vari-Plume Laboratory Exhaust Centrifugal Airfoil Class 2 Arr 10 With Mixing Box
- Triple_195_CAVP-12L_CLASS_2_With_Mixing_Box: ((M - (2 * (D - L - K - J))) / 2) + (TRANSITION / 2)=13 5/8"; (B/2)+1.5"=13 19/32"; (B/2)-.125"=11 31/32"; (D-J-K-L)*2=2"; (E/2)-((B/2)+1.5")=7 1/2"; (E/2)-((MB_P/2)+.125")=3 15/32"; (E/2)-(E/52*15)=8 15/16"; (F-((F-H)/2))/2=11 3/4"; (M - (2 * (D - L - K - J)))/2=7 19/32"; (MB_P/2)+.125"=17 5/8"; (MB_P/2-.125")+((F / 2) - 2")=-29 1/8"; (MB_P/2-.125")-((F / 2) - 2")=-5 5/8"; (MB_Q/2)+.125"=17 5/8"; (NOZZLE_HEIGHT - (NOZZLE_HEIGHT / 8 * 2)) / 2=12"; (NOZZLE_WB_OD - NOZZLE_TOP_OD) / 4=2 1/8"; -((MB_Q / 2) + 1/8")=-17 5/8"; -(F-((F-H)/2))/2=-11 3/4"; -MB_HEIGHT=-40"; -MB_P=-35"; -MB_P-.25=-35 1/4"; A=96 3/4"; A/2=48 3/8"; B=24 3/16"; B/2=12 3/32"; B/4=6 1/16"; C=54 1/4"; C/2=27 1/8"; CLASS=2"; D=47 5/16"; D-L-K-J=1"; D-M=30 1/8"; DUAL_Q=105 3/8"; DUAL_Q+.25"=105 5/8"; E=42 3/16"; E-(NOZZLE_RAD/3*2)=15 13/32"; E-N-N-H=1 27/32"; E/2=21 3/32"; E/2-H/2=8 11/32"; E/52*15=12 5/32"; E/52*30=24 11/32"; F=27 1/2"; F/2=13 3/4"; H=25 1/2"; H/2=12 3/4"; HEIGHT=42 11/16"; J=7 3/4"; J+K+L=46 5/16"; K=19 3/8"; L=19 3/16"; M=17 3/16"; M-(2*(D-L-K-J))=15 3/16"; MB_A=114"; MB_F=7 3/8"; MB_F-3"=4 3/8"; MB_HEIGHT=40"; MB_HEIGHT/2=20"; MB_N=14 3/16"; MB_N-(D-J-K-L)=13 3/16"; MB_P=35"; MB_P+.25"=35 1/4"; MB_P+MB_P+.5=70 1/2"; MB_P-4.5"=30 1/2"; MB_Q=35"; N=6 1/2"; N+(H/2)=19 1/4"; NOZZLE_BOTTOM_ID=17 1/16"; NOZZLE_BOTTOM_RAD=8 17/32"; NOZZLE_BOTTOM_RAD-3*2=2 17/32"; NOZZLE_HEIGHT=32"; NOZZLE_HEIGHT/7*2=8"; NOZZLE_SIZE=12"; NOZZLE_TOP_OD=19 1/2"; NOZZLE_TOP_RAD=9 3/4"; NOZZLE_WB/4=5 19/32"; NOZZLE_WB_OD=28"; NOZZLE_WB_RAD=14"; NOZZLE_WB_RAD-2"=12"; P=60"; R=24 1/4"; R*1.1=26 11/16"; R+((B/2)+1.5")=37 27/32"; R-((B/2)+1.5")=10 21/32"; RO/2=15 1/4"; RO2/2=85 5/8"; TRANSITION=12 1/16"; TRANSITION/2=6 1/32"; TRIP_Q=175 3/4"; TRIP_Q-4.5"=171 1/4"; Type Comments=Triple Vari-Plume Laboratory Exhaust Centrifugal Airfoil Class 2 Arr 10 With Mixing Box
- Triple_195_CAVP-12H_CLASS_2_With_Mixing_Box: ((M - (2 * (D - L - K - J))) / 2) + (TRANSITION / 2)=13 5/8"; (B/2)+1.5"=13 19/32"; (B/2)-.125"=11 31/32"; (D-J-K-L)*2=2"; (E/2)-((B/2)+1.5")=7 1/2"; (E/2)-((MB_P/2)+.125")=3 15/32"; (E/2)-(E/52*15)=8 15/16"; (F-((F-H)/2))/2=11 3/4"; (M - (2 * (D - L - K - J)))/2=7 19/32"; (MB_P/2)+.125"=17 5/8"; (MB_P/2-.125")+((F / 2) - 2")=-29 1/8"; (MB_P/2-.125")-((F / 2) - 2")=-5 5/8"; (MB_Q/2)+.125"=17 5/8"; (NOZZLE_HEIGHT - (NOZZLE_HEIGHT / 8 * 2)) / 2=12"; (NOZZLE_WB_OD - NOZZLE_TOP_OD) / 4=2 1/8"; -((MB_Q / 2) + 1/8")=-17 5/8"; -(F-((F-H)/2))/2=-11 3/4"; -MB_HEIGHT=-40"; -MB_P=-35"; -MB_P-.25=-35 1/4"; A=96 3/4"; A/2=48 3/8"; B=24 3/16"; B/2=12 3/32"; B/4=6 1/16"; C=54 1/4"; C/2=27 1/8"; CLASS=2"; D=47 5/16"; D-L-K-J=1"; D-M=30 1/8"; DUAL_Q=105 3/8"; DUAL_Q+.25"=105 5/8"; E=42 3/16"; E-(NOZZLE_RAD/3*2)=15 13/32"; E-N-N-H=1 27/32"; E/2=21 3/32"; E/2-H/2=8 11/32"; E/52*15=12 5/32"; E/52*30=24 11/32"; F=27 1/2"; F/2=13 3/4"; H=25 1/2"; H/2=12 3/4"; HEIGHT=42 11/16"; J=7 3/4"; J+K+L=46 5/16"; K=19 3/8"; L=19 3/16"; M=17 3/16"; M-(2*(D-L-K-J))=15 3/16"; MB_A=114"; MB_F=7 3/8"; MB_F-3"=4 3/8"; MB_HEIGHT=40"; MB_HEIGHT/2=20"; MB_N=14 3/16"; MB_N-(D-J-K-L)=13 3/16"; MB_P=35"; MB_P+.25"=35 1/4"; MB_P+MB_P+.5=70 1/2"; MB_P-4.5"=30 1/2"; MB_Q=35"; N=6 1/2"; N+(H/2)=19 1/4"; NOZZLE_BOTTOM_ID=17 1/16"; NOZZLE_BOTTOM_RAD=8 17/32"; NOZZLE_BOTTOM_RAD-3*2=2 17/32"; NOZZLE_HEIGHT=32"; NOZZLE_HEIGHT/7*2=8"; NOZZLE_SIZE=12"; NOZZLE_TOP_OD=19 1/2"; NOZZLE_TOP_RAD=9 3/4"; NOZZLE_WB/4=5 19/32"; NOZZLE_WB_OD=28"; NOZZLE_WB_RAD=14"; NOZZLE_WB_RAD-2"=12"; P=60"; R=24 1/4"; R*1.1=26 11/16"; R+((B/2)+1.5")=37 27/32"; R-((B/2)+1.5")=10 21/32"; RO/2=15 1/4"; RO2/2=85 5/8"; TRANSITION=12 1/16"; TRANSITION/2=6 1/32"; TRIP_Q=175 3/4"; TRIP_Q-4.5"=171 1/4"; Type Comments=Triple Vari-Plume Laboratory Exhaust Centrifugal Airfoil Class 2 Arr 10 With Mixing Box
- Triple_195_CAVP-15L_CLASS_2_With_Mixing_Box: ((M - (2 * (D - L - K - J))) / 2) + (TRANSITION / 2)=15 5/32"; (B/2)+1.5"=13 19/32"; (B/2)-.125"=11 31/32"; (D-J-K-L)*2=2"; (E/2)-((B/2)+1.5")=7 1/2"; (E/2)-((MB_P/2)+.125")=3 15/32"; (E/2)-(E/52*15)=8 15/16"; (F-((F-H)/2))/2=11 3/4"; (M - (2 * (D - L - K - J)))/2=7 19/32"; (MB_P/2)+.125"=17 5/8"; (MB_P/2-.125")+((F / 2) - 2")=-29 1/8"; (MB_P/2-.125")-((F / 2) - 2")=-5 5/8"; (MB_Q/2)+.125"=17 5/8"; (NOZZLE_HEIGHT - (NOZZLE_HEIGHT / 8 * 2)) / 2=16 1/8"; (NOZZLE_WB_OD - NOZZLE_TOP_OD) / 4=3 1/4"; -((MB_Q / 2) + 1/8")=-17 5/8"; -(F-((F-H)/2))/2=-11 3/4"; -MB_HEIGHT=-40"; -MB_P=-35"; -MB_P-.25=-35 1/4"; A=96 3/4"; A/2=48 3/8"; B=24 3/16"; B/2=12 3/32"; B/4=6 1/16"; C=54 1/4"; C/2=27 1/8"; CLASS=2"; D=47 5/16"; D-L-K-J=1"; D-M=30 1/8"; DUAL_Q=105 3/8"; DUAL_Q+.25"=105 5/8"; E=42 3/16"; E-(NOZZLE_RAD/3*2)=13 31/32"; E-N-N-H=1 27/32"; E/2=21 3/32"; E/2-H/2=8 11/32"; E/52*15=12 5/32"; E/52*30=24 11/32"; F=27 1/2"; F/2=13 3/4"; H=25 1/2"; H/2=12 3/4"; HEIGHT=42 11/16"; J=7 3/4"; J+K+L=46 5/16"; K=19 3/8"; L=19 3/16"; M=17 3/16"; M-(2*(D-L-K-J))=15 3/16"; MB_A=114"; MB_F=7 3/8"; MB_F-3"=4 3/8"; MB_HEIGHT=40"; MB_HEIGHT/2=20"; MB_N=14 3/16"; MB_N-(D-J-K-L)=13 3/16"; MB_P=35"; MB_P+.25"=35 1/4"; MB_P+MB_P+.5=70 1/2"; MB_P-4.5"=30 1/2"; MB_Q=35"; N=6 1/2"; N+(H/2)=19 1/4"; NOZZLE_BOTTOM_ID=21 3/8"; NOZZLE_BOTTOM_RAD=10 11/16"; NOZZLE_BOTTOM_RAD-3*2=4 11/16"; NOZZLE_HEIGHT=43"; NOZZLE_HEIGHT/7*2=10 3/4"; NOZZLE_SIZE=15"; NOZZLE_TOP_OD=23"; NOZZLE_TOP_RAD=11 1/2"; NOZZLE_WB/4=7 3/16"; NOZZLE_WB_OD=36"; NOZZLE_WB_RAD=18"; NOZZLE_WB_RAD-2"=16"; P=60"; R=24 1/4"; R*1.1=26 11/16"; R+((B/2)+1.5")=37 27/32"; R-((B/2)+1.5")=10 21/32"; RO/2=15 1/4"; RO2/2=85 5/8"; TRANSITION=15 1/8"; TRANSITION/2=7 9/16"; TRIP_Q=175 3/4"; TRIP_Q-4.5"=171 1/4"; Type Comments=Triple Vari-Plume Laboratory Exhaust Centrifugal Airfoil Class 2 Arr 10 With Mixing Box
- Triple_195_CAVP-15H_CLASS_2_With_Mixing_Box: ((M - (2 * (D - L - K - J))) / 2) + (TRANSITION / 2)=15 5/32"; (B/2)+1.5"=13 19/32"; (B/2)-.125"=11 31/32"; (D-J-K-L)*2=2"; (E/2)-((B/2)+1.5")=7 1/2"; (E/2)-((MB_P/2)+.125")=3 15/32"; (E/2)-(E/52*15)=8 15/16"; (F-((F-H)/2))/2=11 3/4"; (M - (2 * (D - L - K - J)))/2=7 19/32"; (MB_P/2)+.125"=17 5/8"; (MB_P/2-.125")+((F / 2) - 2")=-29 1/8"; (MB_P/2-.125")-((F / 2) - 2")=-5 5/8"; (MB_Q/2)+.125"=17 5/8"; (NOZZLE_HEIGHT - (NOZZLE_HEIGHT / 8 * 2)) / 2=16 1/8"; (NOZZLE_WB_OD - NOZZLE_TOP_OD) / 4=3 1/4"; -((MB_Q / 2) + 1/8")=-17 5/8"; -(F-((F-H)/2))/2=-11 3/4"; -MB_HEIGHT=-40"; -MB_P=-35"; -MB_P-.25=-35 1/4"; A=96 3/4"; A/2=48 3/8"; B=24 3/16"; B/2=12 3/32"; B/4=6 1/16"; C=54 1/4"; C/2=27 1/8"; CLASS=2"; D=47 5/16"; D-L-K-J=1"; D-M=30 1/8"; DUAL_Q=105 3/8"; DUAL_Q+.25"=105 5/8"; E=42 3/16"; E-(NOZZLE_RAD/3*2)=13 31/32"; E-N-N-H=1 27/32"; E/2=21 3/32"; E/2-H/2=8 11/32"; E/52*15=12 5/32"; E/52*30=24 11/32"; F=27 1/2"; F/2=13 3/4"; H=25 1/2"; H/2=12 3/4"; HEIGHT=42 11/16"; J=7 3/4"; J+K+L=46 5/16"; K=19 3/8"; L=19 3/16"; M=17 3/16"; M-(2*(D-L-K-J))=15 3/16"; MB_A=114"; MB_F=7 3/8"; MB_F-3"=4 3/8"; MB_HEIGHT=40"; MB_HEIGHT/2=20"; MB_N=14 3/16"; MB_N-(D-J-K-L)=13 3/16"; MB_P=35"; MB_P+.25"=35 1/4"; MB_P+MB_P+.5=70 1/2"; MB_P-4.5"=30 1/2"; MB_Q=35"; N=6 1/2"; N+(H/2)=19 1/4"; NOZZLE_BOTTOM_ID=21 3/8"; NOZZLE_BOTTOM_RAD=10 11/16"; NOZZLE_BOTTOM_RAD-3*2=4 11/16"; NOZZLE_HEIGHT=43"; NOZZLE_HEIGHT/7*2=10 3/4"; NOZZLE_SIZE=15"; NOZZLE_TOP_OD=23"; NOZZLE_TOP_RAD=11 1/2"; NOZZLE_WB/4=7 3/16"; NOZZLE_WB_OD=36"; NOZZLE_WB_RAD=18"; NOZZLE_WB_RAD-2"=16"; P=60"; R=24 1/4"; R*1.1=26 11/16"; R+((B/2)+1.5")=37 27/32"; R-((B/2)+1.5")=10 21/32"; RO/2=15 1/4"; RO2/2=85 5/8"; TRANSITION=15 1/8"; TRANSITION/2=7 9/16"; TRIP_Q=175 3/4"; TRIP_Q-4.5"=171 1/4"; Type Comments=Triple Vari-Plume Laboratory Exhaust Centrifugal Airfoil Class 2 Arr 10 With Mixing Box
- Triple_210_CAVP-12H_CLASS_1_With_Mixing_Box: ((M - (2 * (D - L - K - J))) / 2) + (TRANSITION / 2)=14 3/16"; (B/2)+1.5"=14 15/32"; (B/2)-.125"=12 27/32"; (D-J-K-L)*2=2"; (E/2)-((B/2)+1.5")=8 5/32"; (E/2)-((MB_P/2)+.125")=4"; (E/2)-(E/52*15)=9 9/16"; (F-((F-H)/2))/2=12 1/16"; (M - (2 * (D - L - K - J)))/2=8 5/32"; (MB_P/2)+.125"=18 5/8"; (MB_P/2-.125")+((F / 2) - 2")=-30 7/16"; (MB_P/2-.125")-((F / 2) - 2")=-6 5/16"; (MB_Q/2)+.125"=18 5/8"; (NOZZLE_HEIGHT - (NOZZLE_HEIGHT / 8 * 2)) / 2=12"; (NOZZLE_WB_OD - NOZZLE_TOP_OD) / 4=2 1/8"; -((MB_Q / 2) + 1/8")=-18 5/8"; -(F-((F-H)/2))/2=-12 1/16"; -MB_HEIGHT=-41 3/4"; -MB_P=-37"; -MB_P-.25=-37 1/4"; A=99 1/4"; A/2=49 5/8"; B=25 15/16"; B/2=12 31/32"; B/4=6 1/2"; C=56 3/4"; C/2=28 3/8"; CLASS=1"; D=44 15/16"; D-L-K-J=1"; D-M=26 5/8"; DUAL_Q=111 3/8"; DUAL_Q+.25"=111 5/8"; E=45 1/4"; E-(NOZZLE_RAD/3*2)=16 15/16"; E-N-N-H=2"; E/2=22 5/8"; E/2-H/2=9 9/16"; E/52*15=13 1/16"; E/52*30=26 3/32"; F=28 1/8"; F/2=14 1/16"; H=26 1/8"; H/2=13 1/16"; HEIGHT=44"; J=8 1/2"; J+K+L=43 15/16"; K=15 1/8"; L=20 5/16"; M=18 5/16"; M-(2*(D-L-K-J))=16 5/16"; MB_A=114 1/2"; MB_F=6 1/2"; MB_F-3"=3 1/2"; MB_HEIGHT=41 3/4"; MB_HEIGHT/2=20 7/8"; MB_N=14 3/16"; MB_N-(D-J-K-L)=13 3/16"; MB_P=37"; MB_P+.25"=37 1/4"; MB_P+MB_P+.5=74 1/2"; MB_P-4.5"=32 1/2"; MB_Q=37"; N=7 9/16"; N+(H/2)=20 5/8"; NOZZLE_BOTTOM_ID=17 1/16"; NOZZLE_BOTTOM_RAD=8 17/32"; NOZZLE_BOTTOM_RAD-3*2=2 17/32"; NOZZLE_HEIGHT=32"; NOZZLE_HEIGHT/7*2=8"; NOZZLE_SIZE=12"; NOZZLE_TOP_OD=19 1/2"; NOZZLE_TOP_RAD=9 3/4"; NOZZLE_WB/4=5 19/32"; NOZZLE_WB_OD=28"; NOZZLE_WB_RAD=14"; NOZZLE_WB_RAD-2"=12"; P=60"; R=24 1/4"; R*1.1=26 11/16"; R+((B/2)+1.5")=38 23/32"; R-((B/2)+1.5")=9 25/32"; RO/2=16 1/4"; RO2/2=90 5/8"; TRANSITION=12 1/16"; TRANSITION/2=6 1/32"; TRIP_Q=185 3/4"; TRIP_Q-4.5"=181 1/4"; Type Comments=Triple Vari-Plume Laboratory Exhaust Centrifugal Airfoil Class 1 Arr 10 With Mixing Box
- Triple_210_CAVP-12L_CLASS_1_With_Mixing_Box: ((M - (2 * (D - L - K - J))) / 2) + (TRANSITION / 2)=14 3/16"; (B/2)+1.5"=14 15/32"; (B/2)-.125"=12 27/32"; (D-J-K-L)*2=2"; (E/2)-((B/2)+1.5")=8 5/32"; (E/2)-((MB_P/2)+.125")=4"; (E/2)-(E/52*15)=9 9/16"; (F-((F-H)/2))/2=12 1/16"; (M - (2 * (D - L - K - J)))/2=8 5/32"; (MB_P/2)+.125"=18 5/8"; (MB_P/2-.125")+((F / 2) - 2")=-30 7/16"; (MB_P/2-.125")-((F / 2) - 2")=-6 5/16"; (MB_Q/2)+.125"=18 5/8"; (NOZZLE_HEIGHT - (NOZZLE_HEIGHT / 8 * 2)) / 2=12"; (NOZZLE_WB_OD - NOZZLE_TOP_OD) / 4=2 1/8"; -((MB_Q / 2) + 1/8")=-18 5/8"; -(F-((F-H)/2))/2=-12 1/16"; -MB_HEIGHT=-41 3/4"; -MB_P=-37"; -MB_P-.25=-37 1/4"; A=99 1/4"; A/2=49 5/8"; B=25 15/16"; B/2=12 31/32"; B/4=6 1/2"; C=56 3/4"; C/2=28 3/8"; CLASS=1"; D=44 15/16"; D-L-K-J=1"; D-M=26 5/8"; DUAL_Q=111 3/8"; DUAL_Q+.25"=111 5/8"; E=45 1/4"; E-(NOZZLE_RAD/3*2)=16 15/16"; E-N-N-H=2"; E/2=22 5/8"; E/2-H/2=9 9/16"; E/52*15=13 1/16"; E/52*30=26 3/32"; F=28 1/8"; F/2=14 1/16"; H=26 1/8"; H/2=13 1/16"; HEIGHT=44"; J=8 1/2"; J+K+L=43 15/16"; K=15 1/8"; L=20 5/16"; M=18 5/16"; M-(2*(D-L-K-J))=16 5/16"; MB_A=114 1/2"; MB_F=6 1/2"; MB_F-3"=3 1/2"; MB_HEIGHT=41 3/4"; MB_HEIGHT/2=20 7/8"; MB_N=14 3/16"; MB_N-(D-J-K-L)=13 3/16"; MB_P=37"; MB_P+.25"=37 1/4"; MB_P+MB_P+.5=74 1/2"; MB_P-4.5"=32 1/2"; MB_Q=37"; N=7 9/16"; N+(H/2)=20 5/8"; NOZZLE_BOTTOM_ID=17 1/16"; NOZZLE_BOTTOM_RAD=8 17/32"; NOZZLE_BOTTOM_RAD-3*2=2 17/32"; NOZZLE_HEIGHT=32"; NOZZLE_HEIGHT/7*2=8"; NOZZLE_SIZE=12"; NOZZLE_TOP_OD=19 1/2"; NOZZLE_TOP_RAD=9 3/4"; NOZZLE_WB/4=5 19/32"; NOZZLE_WB_OD=28"; NOZZLE_WB_RAD=14"; NOZZLE_WB_RAD-2"=12"; P=60"; R=24 1/4"; R*1.1=26 11/16"; R+((B/2)+1.5")=38 23/32"; R-((B/2)+1.5")=9 25/32"; RO/2=16 1/4"; RO2/2=90 5/8"; TRANSITION=12 1/16"; TRANSITION/2=6 1/32"; TRIP_Q=185 3/4"; TRIP_Q-4.5"=181 1/4"; Type Comments=Triple Vari-Plume Laboratory Exhaust Centrifugal Airfoil Class 1 Arr 10 With Mixing Box
- Triple_210_CAVP-15H_CLASS_1_With_Mixing_Box: ((M - (2 * (D - L - K - J))) / 2) + (TRANSITION / 2)=15 23/32"; (B/2)+1.5"=14 15/32"; (B/2)-.125"=12 27/32"; (D-J-K-L)*2=2"; (E/2)-((B/2)+1.5")=8 5/32"; (E/2)-((MB_P/2)+.125")=4"; (E/2)-(E/52*15)=9 9/16"; (F-((F-H)/2))/2=12 1/16"; (M - (2 * (D - L - K - J)))/2=8 5/32"; (MB_P/2)+.125"=18 5/8"; (MB_P/2-.125")+((F / 2) - 2")=-30 7/16"; (MB_P/2-.125")-((F / 2) - 2")=-6 5/16"; (MB_Q/2)+.125"=18 5/8"; (NOZZLE_HEIGHT - (NOZZLE_HEIGHT / 8 * 2)) / 2=16 1/8"; (NOZZLE_WB_OD - NOZZLE_TOP_OD) / 4=3 1/4"; -((MB_Q / 2) + 1/8")=-18 5/8"; -(F-((F-H)/2))/2=-12 1/16"; -MB_HEIGHT=-41 3/4"; -MB_P=-37"; -MB_P-.25=-37 1/4"; A=99 1/4"; A/2=49 5/8"; B=25 15/16"; B/2=12 31/32"; B/4=6 1/2"; C=56 3/4"; C/2=28 3/8"; CLASS=1"; D=44 15/16"; D-L-K-J=1"; D-M=26 5/8"; DUAL_Q=111 3/8"; DUAL_Q+.25"=111 5/8"; E=45 1/4"; E-(NOZZLE_RAD/3*2)=15 1/2"; E-N-N-H=2"; E/2=22 5/8"; E/2-H/2=9 9/16"; E/52*15=13 1/16"; E/52*30=26 3/32"; F=28 1/8"; F/2=14 1/16"; H=26 1/8"; H/2=13 1/16"; HEIGHT=44"; J=8 1/2"; J+K+L=43 15/16"; K=15 1/8"; L=20 5/16"; M=18 5/16"; M-(2*(D-L-K-J))=16 5/16"; MB_A=114 1/2"; MB_F=6 1/2"; MB_F-3"=3 1/2"; MB_HEIGHT=41 3/4"; MB_HEIGHT/2=20 7/8"; MB_N=14 3/16"; MB_N-(D-J-K-L)=13 3/16"; MB_P=37"; MB_P+.25"=37 1/4"; MB_P+MB_P+.5=74 1/2"; MB_P-4.5"=32 1/2"; MB_Q=37"; N=7 9/16"; N+(H/2)=20 5/8"; NOZZLE_BOTTOM_ID=21 3/8"; NOZZLE_BOTTOM_RAD=10 11/16"; NOZZLE_BOTTOM_RAD-3*2=4 11/16"; NOZZLE_HEIGHT=43"; NOZZLE_HEIGHT/7*2=10 3/4"; NOZZLE_SIZE=15"; NOZZLE_TOP_OD=23"; NOZZLE_TOP_RAD=11 1/2"; NOZZLE_WB/4=7 3/16"; NOZZLE_WB_OD=36"; NOZZLE_WB_RAD=18"; NOZZLE_WB_RAD-2"=16"; P=60"; R=24 1/4"; R*1.1=26 11/16"; R+((B/2)+1.5")=38 23/32"; R-((B/2)+1.5")=9 25/32"; RO/2=16 1/4"; RO2/2=90 5/8"; TRANSITION=15 1/8"; TRANSITION/2=7 9/16"; TRIP_Q=185 3/4"; TRIP_Q-4.5"=181 1/4"; Type Comments=Triple Vari-Plume Laboratory Exhaust Centrifugal Airfoil Class 1 Arr 10 With Mixing Box
- Triple_210_CAVP-15L_CLASS_1_With_Mixing_Box: ((M - (2 * (D - L - K - J))) / 2) + (TRANSITION / 2)=15 23/32"; (B/2)+1.5"=14 15/32"; (B/2)-.125"=12 27/32"; (D-J-K-L)*2=2"; (E/2)-((B/2)+1.5")=8 5/32"; (E/2)-((MB_P/2)+.125")=4"; (E/2)-(E/52*15)=9 9/16"; (F-((F-H)/2))/2=12 1/16"; (M - (2 * (D - L - K - J)))/2=8 5/32"; (MB_P/2)+.125"=18 5/8"; (MB_P/2-.125")+((F / 2) - 2")=-30 7/16"; (MB_P/2-.125")-((F / 2) - 2")=-6 5/16"; (MB_Q/2)+.125"=18 5/8"; (NOZZLE_HEIGHT - (NOZZLE_HEIGHT / 8 * 2)) / 2=16 1/8"; (NOZZLE_WB_OD - NOZZLE_TOP_OD) / 4=3 1/4"; -((MB_Q / 2) + 1/8")=-18 5/8"; -(F-((F-H)/2))/2=-12 1/16"; -MB_HEIGHT=-41 3/4"; -MB_P=-37"; -MB_P-.25=-37 1/4"; A=99 1/4"; A/2=49 5/8"; B=25 15/16"; B/2=12 31/32"; B/4=6 1/2"; C=56 3/4"; C/2=28 3/8"; CLASS=1"; D=44 15/16"; D-L-K-J=1"; D-M=26 5/8"; DUAL_Q=111 3/8"; DUAL_Q+.25"=111 5/8"; E=45 1/4"; E-(NOZZLE_RAD/3*2)=15 1/2"; E-N-N-H=2"; E/2=22 5/8"; E/2-H/2=9 9/16"; E/52*15=13 1/16"; E/52*30=26 3/32"; F=28 1/8"; F/2=14 1/16"; H=26 1/8"; H/2=13 1/16"; HEIGHT=44"; J=8 1/2"; J+K+L=43 15/16"; K=15 1/8"; L=20 5/16"; M=18 5/16"; M-(2*(D-L-K-J))=16 5/16"; MB_A=114 1/2"; MB_F=6 1/2"; MB_F-3"=3 1/2"; MB_HEIGHT=41 3/4"; MB_HEIGHT/2=20 7/8"; MB_N=14 3/16"; MB_N-(D-J-K-L)=13 3/16"; MB_P=37"; MB_P+.25"=37 1/4"; MB_P+MB_P+.5=74 1/2"; MB_P-4.5"=32 1/2"; MB_Q=37"; N=7 9/16"; N+(H/2)=20 5/8"; NOZZLE_BOTTOM_ID=21 3/8"; NOZZLE_BOTTOM_RAD=10 11/16"; NOZZLE_BOTTOM_RAD-3*2=4 11/16"; NOZZLE_HEIGHT=43"; NOZZLE_HEIGHT/7*2=10 3/4"; NOZZLE_SIZE=15"; NOZZLE_TOP_OD=23"; NOZZLE_TOP_RAD=11 1/2"; NOZZLE_WB/4=7 3/16"; NOZZLE_WB_OD=36"; NOZZLE_WB_RAD=18"; NOZZLE_WB_RAD-2"=16"; P=60"; R=24 1/4"; R*1.1=26 11/16"; R+((B/2)+1.5")=38 23/32"; R-((B/2)+1.5")=9 25/32"; RO/2=16 1/4"; RO2/2=90 5/8"; TRANSITION=15 1/8"; TRANSITION/2=7 9/16"; TRIP_Q=185 3/4"; TRIP_Q-4.5"=181 1/4"; Type Comments=Triple Vari-Plume Laboratory Exhaust Centrifugal Airfoil Class 1 Arr 10 With Mixing Box
- Triple_210_CAVP-15L_CLASS_2_With_Mixing_Box: ((M - (2 * (D - L - K - J))) / 2) + (TRANSITION / 2)=15 23/32"; (B/2)+1.5"=14 15/32"; (B/2)-.125"=12 27/32"; (D-J-K-L)*2=2"; (E/2)-((B/2)+1.5")=8 5/32"; (E/2)-((MB_P/2)+.125")=4"; (E/2)-(E/52*15)=9 9/16"; (F-((F-H)/2))/2=12 1/16"; (M - (2 * (D - L - K - J)))/2=8 5/32"; (MB_P/2)+.125"=18 5/8"; (MB_P/2-.125")+((F / 2) - 2")=-30 7/16"; (MB_P/2-.125")-((F / 2) - 2")=-6 5/16"; (MB_Q/2)+.125"=18 5/8"; (NOZZLE_HEIGHT - (NOZZLE_HEIGHT / 8 * 2)) / 2=16 1/8"; (NOZZLE_WB_OD - NOZZLE_TOP_OD) / 4=3 1/4"; -((MB_Q / 2) + 1/8")=-18 5/8"; -(F-((F-H)/2))/2=-12 1/16"; -MB_HEIGHT=-41 3/4"; -MB_P=-37"; -MB_P-.25=-37 1/4"; A=99 1/4"; A/2=49 5/8"; B=25 15/16"; B/2=12 31/32"; B/4=6 1/2"; C=56 3/4"; C/2=28 3/8"; CLASS=2"; D=44 15/16"; D-L-K-J=1"; D-M=26 5/8"; DUAL_Q=111 3/8"; DUAL_Q+.25"=111 5/8"; E=45 1/4"; E-(NOZZLE_RAD/3*2)=15 1/2"; E-N-N-H=2"; E/2=22 5/8"; E/2-H/2=9 9/16"; E/52*15=13 1/16"; E/52*30=26 3/32"; F=28 1/8"; F/2=14 1/16"; H=26 1/8"; H/2=13 1/16"; HEIGHT=44"; J=8 1/2"; J+K+L=43 15/16"; K=15 1/8"; L=20 5/16"; M=18 5/16"; M-(2*(D-L-K-J))=16 5/16"; MB_A=118 1/2"; MB_F=6 1/2"; MB_F-3"=3 1/2"; MB_HEIGHT=41 3/4"; MB_HEIGHT/2=20 7/8"; MB_N=14 3/16"; MB_N-(D-J-K-L)=13 3/16"; MB_P=37"; MB_P+.25"=37 1/4"; MB_P+MB_P+.5=74 1/2"; MB_P-4.5"=32 1/2"; MB_Q=37"; N=7 9/16"; N+(H/2)=20 5/8"; NOZZLE_BOTTOM_ID=21 3/8"; NOZZLE_BOTTOM_RAD=10 11/16"; NOZZLE_BOTTOM_RAD-3*2=4 11/16"; NOZZLE_HEIGHT=43"; NOZZLE_HEIGHT/7*2=10 3/4"; NOZZLE_SIZE=15"; NOZZLE_TOP_OD=23"; NOZZLE_TOP_RAD=11 1/2"; NOZZLE_WB/4=7 3/16"; NOZZLE_WB_OD=36"; NOZZLE_WB_RAD=18"; NOZZLE_WB_RAD-2"=16"; P=60"; R=24 1/4"; R*1.1=26 11/16"; R+((B/2)+1.5")=38 23/32"; R-((B/2)+1.5")=9 25/32"; RO/2=16 1/4"; RO2/2=90 5/8"; TRANSITION=15 1/8"; TRANSITION/2=7 9/16"; TRIP_Q=185 3/4"; TRIP_Q-4.5"=181 1/4"; Type Comments=Triple Vari-Plume Laboratory Exhaust Centrifugal Airfoil Class 2 Arr 10 With Mixing Box
- Triple_210_CAVP-15H_CLASS_2_With_Mixing_Box: ((M - (2 * (D - L - K - J))) / 2) + (TRANSITION / 2)=15 23/32"; (B/2)+1.5"=14 15/32"; (B/2)-.125"=12 27/32"; (D-J-K-L)*2=2"; (E/2)-((B/2)+1.5")=8 5/32"; (E/2)-((MB_P/2)+.125")=4"; (E/2)-(E/52*15)=9 9/16"; (F-((F-H)/2))/2=12 1/16"; (M - (2 * (D - L - K - J)))/2=8 5/32"; (MB_P/2)+.125"=18 5/8"; (MB_P/2-.125")+((F / 2) - 2")=-30 7/16"; (MB_P/2-.125")-((F / 2) - 2")=-6 5/16"; (MB_Q/2)+.125"=18 5/8"; (NOZZLE_HEIGHT - (NOZZLE_HEIGHT / 8 * 2)) / 2=16 1/8"; (NOZZLE_WB_OD - NOZZLE_TOP_OD) / 4=3 1/4"; -((MB_Q / 2) + 1/8")=-18 5/8"; -(F-((F-H)/2))/2=-12 1/16"; -MB_HEIGHT=-41 3/4"; -MB_P=-37"; -MB_P-.25=-37 1/4"; A=99 1/4"; A/2=49 5/8"; B=25 15/16"; B/2=12 31/32"; B/4=6 1/2"; C=56 3/4"; C/2=28 3/8"; CLASS=2"; D=44 15/16"; D-L-K-J=1"; D-M=26 5/8"; DUAL_Q=111 3/8"; DUAL_Q+.25"=111 5/8"; E=45 1/4"; E-(NOZZLE_RAD/3*2)=15 1/2"; E-N-N-H=2"; E/2=22 5/8"; E/2-H/2=9 9/16"; E/52*15=13 1/16"; E/52*30=26 3/32"; F=28 1/8"; F/2=14 1/16"; H=26 1/8"; H/2=13 1/16"; HEIGHT=44"; J=8 1/2"; J+K+L=43 15/16"; K=15 1/8"; L=20 5/16"; M=18 5/16"; M-(2*(D-L-K-J))=16 5/16"; MB_A=118 1/2"; MB_F=6 1/2"; MB_F-3"=3 1/2"; MB_HEIGHT=41 3/4"; MB_HEIGHT/2=20 7/8"; MB_N=14 3/16"; MB_N-(D-J-K-L)=13 3/16"; MB_P=37"; MB_P+.25"=37 1/4"; MB_P+MB_P+.5=74 1/2"; MB_P-4.5"=32 1/2"; MB_Q=37"; N=7 9/16"; N+(H/2)=20 5/8"; NOZZLE_BOTTOM_ID=21 3/8"; NOZZLE_BOTTOM_RAD=10 11/16"; NOZZLE_BOTTOM_RAD-3*2=4 11/16"; NOZZLE_HEIGHT=43"; NOZZLE_HEIGHT/7*2=10 3/4"; NOZZLE_SIZE=15"; NOZZLE_TOP_OD=23"; NOZZLE_TOP_RAD=11 1/2"; NOZZLE_WB/4=7 3/16"; NOZZLE_WB_OD=36"; NOZZLE_WB_RAD=18"; NOZZLE_WB_RAD-2"=16"; P=60"; R=24 1/4"; R*1.1=26 11/16"; R+((B/2)+1.5")=38 23/32"; R-((B/2)+1.5")=9 25/32"; RO/2=16 1/4"; RO2/2=90 5/8"; TRANSITION=15 1/8"; TRANSITION/2=7 9/16"; TRIP_Q=185 3/4"; TRIP_Q-4.5"=181 1/4"; Type Comments=Triple Vari-Plume Laboratory Exhaust Centrifugal Airfoil Class 2 Arr 10 With Mixing Box
- Triple_210_CAVP-12L_CLASS_2_With_Mixing_Box: ((M - (2 * (D - L - K - J))) / 2) + (TRANSITION / 2)=14 3/16"; (B/2)+1.5"=14 15/32"; (B/2)-.125"=12 27/32"; (D-J-K-L)*2=2"; (E/2)-((B/2)+1.5")=8 5/32"; (E/2)-((MB_P/2)+.125")=4"; (E/2)-(E/52*15)=9 9/16"; (F-((F-H)/2))/2=12 1/16"; (M - (2 * (D - L - K - J)))/2=8 5/32"; (MB_P/2)+.125"=18 5/8"; (MB_P/2-.125")+((F / 2) - 2")=-30 7/16"; (MB_P/2-.125")-((F / 2) - 2")=-6 5/16"; (MB_Q/2)+.125"=18 5/8"; (NOZZLE_HEIGHT - (NOZZLE_HEIGHT / 8 * 2)) / 2=12"; (NOZZLE_WB_OD - NOZZLE_TOP_OD) / 4=2 1/8"; -((MB_Q / 2) + 1/8")=-18 5/8"; -(F-((F-H)/2))/2=-12 1/16"; -MB_HEIGHT=-41 3/4"; -MB_P=-37"; -MB_P-.25=-37 1/4"; A=99 1/4"; A/2=49 5/8"; B=25 15/16"; B/2=12 31/32"; B/4=6 1/2"; C=56 3/4"; C/2=28 3/8"; CLASS=2"; D=44 15/16"; D-L-K-J=1"; D-M=26 5/8"; DUAL_Q=111 3/8"; DUAL_Q+.25"=111 5/8"; E=45 1/4"; E-(NOZZLE_RAD/3*2)=16 15/16"; E-N-N-H=2"; E/2=22 5/8"; E/2-H/2=9 9/16"; E/52*15=13 1/16"; E/52*30=26 3/32"; F=28 1/8"; F/2=14 1/16"; H=26 1/8"; H/2=13 1/16"; HEIGHT=44"; J=8 1/2"; J+K+L=43 15/16"; K=15 1/8"; L=20 5/16"; M=18 5/16"; M-(2*(D-L-K-J))=16 5/16"; MB_A=118 1/2"; MB_F=6 1/2"; MB_F-3"=3 1/2"; MB_HEIGHT=41 3/4"; MB_HEIGHT/2=20 7/8"; MB_N=14 3/16"; MB_N-(D-J-K-L)=13 3/16"; MB_P=37"; MB_P+.25"=37 1/4"; MB_P+MB_P+.5=74 1/2"; MB_P-4.5"=32 1/2"; MB_Q=37"; N=7 9/16"; N+(H/2)=20 5/8"; NOZZLE_BOTTOM_ID=17 1/16"; NOZZLE_BOTTOM_RAD=8 17/32"; NOZZLE_BOTTOM_RAD-3*2=2 17/32"; NOZZLE_HEIGHT=32"; NOZZLE_HEIGHT/7*2=8"; NOZZLE_SIZE=12"; NOZZLE_TOP_OD=19 1/2"; NOZZLE_TOP_RAD=9 3/4"; NOZZLE_WB/4=5 19/32"; NOZZLE_WB_OD=28"; NOZZLE_WB_RAD=14"; NOZZLE_WB_RAD-2"=12"; P=60"; R=24 1/4"; R*1.1=26 11/16"; R+((B/2)+1.5")=38 23/32"; R-((B/2)+1.5")=9 25/32"; RO/2=16 1/4"; RO2/2=90 5/8"; TRANSITION=12 1/16"; TRANSITION/2=6 1/32"; TRIP_Q=185 3/4"; TRIP_Q-4.5"=181 1/4"; Type Comments=Triple Vari-Plume Laboratory Exhaust Centrifugal Airfoil Class 2 Arr 10 With Mixing Box
- Triple_210_CAVP-12H_CLASS_2_With_Mixing_Box: ((M - (2 * (D - L - K - J))) / 2) + (TRANSITION / 2)=14 3/16"; (B/2)+1.5"=14 15/32"; (B/2)-.125"=12 27/32"; (D-J-K-L)*2=2"; (E/2)-((B/2)+1.5")=8 5/32"; (E/2)-((MB_P/2)+.125")=4"; (E/2)-(E/52*15)=9 9/16"; (F-((F-H)/2))/2=12 1/16"; (M - (2 * (D - L - K - J)))/2=8 5/32"; (MB_P/2)+.125"=18 5/8"; (MB_P/2-.125")+((F / 2) - 2")=-30 7/16"; (MB_P/2-.125")-((F / 2) - 2")=-6 5/16"; (MB_Q/2)+.125"=18 5/8"; (NOZZLE_HEIGHT - (NOZZLE_HEIGHT / 8 * 2)) / 2=12"; (NOZZLE_WB_OD - NOZZLE_TOP_OD) / 4=2 1/8"; -((MB_Q / 2) + 1/8")=-18 5/8"; -(F-((F-H)/2))/2=-12 1/16"; -MB_HEIGHT=-41 3/4"; -MB_P=-37"; -MB_P-.25=-37 1/4"; A=99 1/4"; A/2=49 5/8"; B=25 15/16"; B/2=12 31/32"; B/4=6 1/2"; C=56 3/4"; C/2=28 3/8"; CLASS=2"; D=44 15/16"; D-L-K-J=1"; D-M=26 5/8"; DUAL_Q=111 3/8"; DUAL_Q+.25"=111 5/8"; E=45 1/4"; E-(NOZZLE_RAD/3*2)=16 15/16"; E-N-N-H=2"; E/2=22 5/8"; E/2-H/2=9 9/16"; E/52*15=13 1/16"; E/52*30=26 3/32"; F=28 1/8"; F/2=14 1/16"; H=26 1/8"; H/2=13 1/16"; HEIGHT=44"; J=8 1/2"; J+K+L=43 15/16"; K=15 1/8"; L=20 5/16"; M=18 5/16"; M-(2*(D-L-K-J))=16 5/16"; MB_A=118 1/2"; MB_F=6 1/2"; MB_F-3"=3 1/2"; MB_HEIGHT=41 3/4"; MB_HEIGHT/2=20 7/8"; MB_N=14 3/16"; MB_N-(D-J-K-L)=13 3/16"; MB_P=37"; MB_P+.25"=37 1/4"; MB_P+MB_P+.5=74 1/2"; MB_P-4.5"=32 1/2"; MB_Q=37"; N=7 9/16"; N+(H/2)=20 5/8"; NOZZLE_BOTTOM_ID=17 1/16"; NOZZLE_BOTTOM_RAD=8 17/32"; NOZZLE_BOTTOM_RAD-3*2=2 17/32"; NOZZLE_HEIGHT=32"; NOZZLE_HEIGHT/7*2=8"; NOZZLE_SIZE=12"; NOZZLE_TOP_OD=19 1/2"; NOZZLE_TOP_RAD=9 3/4"; NOZZLE_WB/4=5 19/32"; NOZZLE_WB_OD=28"; NOZZLE_WB_RAD=14"; NOZZLE_WB_RAD-2"=12"; P=60"; R=24 1/4"; R*1.1=26 11/16"; R+((B/2)+1.5")=38 23/32"; R-((B/2)+1.5")=9 25/32"; RO/2=16 1/4"; RO2/2=90 5/8"; TRANSITION=12 1/16"; TRANSITION/2=6 1/32"; TRIP_Q=185 3/4"; TRIP_Q-4.5"=181 1/4"; Type Comments=Triple Vari-Plume Laboratory Exhaust Centrifugal Airfoil Class 2 Arr 10 With Mixing Box
- Triple_225_CAVP-12H_CLASS_1_With_Mixing_Box: ((M - (2 * (D - L - K - J))) / 2) + (TRANSITION / 2)=14 3/4"; (B/2)+1.5"=15 7/32"; (B/2)-.125"=13 19/32"; (D-J-K-L)*2=2"; (E/2)-((B/2)+1.5")=8 15/16"; (E/2)-((MB_P/2)+.125")=5 1/32"; (E/2)-(E/52*15)=10 7/32"; (F-((F-H)/2))/2=12 13/16"; (M - (2 * (D - L - K - J)))/2=8 23/32"; (MB_P/2)+.125"=19 1/8"; (MB_P/2-.125")+((F / 2) - 2")=-31 11/16"; (MB_P/2-.125")-((F / 2) - 2")=-6 1/16"; (MB_Q/2)+.125"=19 1/8"; (NOZZLE_HEIGHT - (NOZZLE_HEIGHT / 8 * 2)) / 2=12"; (NOZZLE_WB_OD - NOZZLE_TOP_OD) / 4=2 1/8"; -((MB_Q / 2) + 1/8")=-19 1/8"; -(F-((F-H)/2))/2=-12 13/16"; -MB_HEIGHT=-43 1/4"; -MB_P=-38"; -MB_P-.25=-38 1/4"; A=106 11/16"; A/2=53 11/32"; B=27 7/16"; B/2=13 23/32"; B/4=6 7/8"; C=59 3/16"; C/2=29 19/32"; CLASS=1"; D=46 1/16"; D-L-K-J=1"; D-M=26 5/8"; DUAL_Q=114 3/8"; DUAL_Q+.25"=114 5/8"; E=48 5/16"; E-(NOZZLE_RAD/3*2)=18 15/32"; E-N-N-H=2"; E/2=24 5/32"; E/2-H/2=10 11/32"; E/52*15=13 15/16"; E/52*30=27 7/8"; F=29 5/8"; F/2=14 13/16"; H=27 5/8"; H/2=13 13/16"; HEIGHT=45 11/32"; J=8 1/2"; J+K+L=45 1/16"; K=15 1/8"; L=21 7/16"; M=19 7/16"; M-(2*(D-L-K-J))=17 7/16"; MB_A=117 5/8"; MB_F=5 3/4"; MB_F-3"=2 3/4"; MB_HEIGHT=43 1/4"; MB_HEIGHT/2=21 5/8"; MB_N=14 3/16"; MB_N-(D-J-K-L)=13 3/16"; MB_P=38"; MB_P+.25"=38 1/4"; MB_P+MB_P+.5=76 1/2"; MB_P-4.5"=33 1/2"; MB_Q=38"; N=8 11/32"; N+(H/2)=22 5/32"; NOZZLE_BOTTOM_ID=17 1/16"; NOZZLE_BOTTOM_RAD=8 17/32"; NOZZLE_BOTTOM_RAD-3*2=2 17/32"; NOZZLE_HEIGHT=32"; NOZZLE_HEIGHT/7*2=8"; NOZZLE_SIZE=12"; NOZZLE_TOP_OD=19 1/2"; NOZZLE_TOP_RAD=9 3/4"; NOZZLE_WB/4=5 19/32"; NOZZLE_WB_OD=28"; NOZZLE_WB_RAD=14"; NOZZLE_WB_RAD-2"=12"; P=60"; R=24 1/4"; R*1.1=26 11/16"; R+((B/2)+1.5")=39 15/32"; R-((B/2)+1.5")=9 1/32"; RO/2=16 3/4"; RO2/2=93 1/8"; TRANSITION=12 1/16"; TRANSITION/2=6 1/32"; TRIP_Q=190 3/4"; TRIP_Q-4.5"=186 1/4"; Type Comments=Triple Vari-Plume Laboratory Exhaust Centrifugal Airfoil Class 1 Arr 10 With Mixing Box
- Triple_225_CAVP-12L_CLASS_1_With_Mixing_Box: ((M - (2 * (D - L - K - J))) / 2) + (TRANSITION / 2)=14 3/4"; (B/2)+1.5"=15 7/32"; (B/2)-.125"=13 19/32"; (D-J-K-L)*2=2"; (E/2)-((B/2)+1.5")=8 15/16"; (E/2)-((MB_P/2)+.125")=5 1/32"; (E/2)-(E/52*15)=10 7/32"; (F-((F-H)/2))/2=12 13/16"; (M - (2 * (D - L - K - J)))/2=8 23/32"; (MB_P/2)+.125"=19 1/8"; (MB_P/2-.125")+((F / 2) - 2")=-31 11/16"; (MB_P/2-.125")-((F / 2) - 2")=-6 1/16"; (MB_Q/2)+.125"=19 1/8"; (NOZZLE_HEIGHT - (NOZZLE_HEIGHT / 8 * 2)) / 2=12"; (NOZZLE_WB_OD - NOZZLE_TOP_OD) / 4=2 1/8"; -((MB_Q / 2) + 1/8")=-19 1/8"; -(F-((F-H)/2))/2=-12 13/16"; -MB_HEIGHT=-43 1/4"; -MB_P=-38"; -MB_P-.25=-38 1/4"; A=106 11/16"; A/2=53 11/32"; B=27 7/16"; B/2=13 23/32"; B/4=6 7/8"; C=59 3/16"; C/2=29 19/32"; CLASS=1"; D=46 1/16"; D-L-K-J=1"; D-M=26 5/8"; DUAL_Q=114 3/8"; DUAL_Q+.25"=114 5/8"; E=48 5/16"; E-(NOZZLE_RAD/3*2)=18 15/32"; E-N-N-H=2"; E/2=24 5/32"; E/2-H/2=10 11/32"; E/52*15=13 15/16"; E/52*30=27 7/8"; F=29 5/8"; F/2=14 13/16"; H=27 5/8"; H/2=13 13/16"; HEIGHT=45 11/32"; J=8 1/2"; J+K+L=45 1/16"; K=15 1/8"; L=21 7/16"; M=19 7/16"; M-(2*(D-L-K-J))=17 7/16"; MB_A=117 5/8"; MB_F=5 3/4"; MB_F-3"=2 3/4"; MB_HEIGHT=43 1/4"; MB_HEIGHT/2=21 5/8"; MB_N=14 3/16"; MB_N-(D-J-K-L)=13 3/16"; MB_P=38"; MB_P+.25"=38 1/4"; MB_P+MB_P+.5=76 1/2"; MB_P-4.5"=33 1/2"; MB_Q=38"; N=8 11/32"; N+(H/2)=22 5/32"; NOZZLE_BOTTOM_ID=17 1/16"; NOZZLE_BOTTOM_RAD=8 17/32"; NOZZLE_BOTTOM_RAD-3*2=2 17/32"; NOZZLE_HEIGHT=32"; NOZZLE_HEIGHT/7*2=8"; NOZZLE_SIZE=12"; NOZZLE_TOP_OD=19 1/2"; NOZZLE_TOP_RAD=9 3/4"; NOZZLE_WB/4=5 19/32"; NOZZLE_WB_OD=28"; NOZZLE_WB_RAD=14"; NOZZLE_WB_RAD-2"=12"; P=60"; R=24 1/4"; R*1.1=26 11/16"; R+((B/2)+1.5")=39 15/32"; R-((B/2)+1.5")=9 1/32"; RO/2=16 3/4"; RO2/2=93 1/8"; TRANSITION=12 1/16"; TRANSITION/2=6 1/32"; TRIP_Q=190 3/4"; TRIP_Q-4.5"=186 1/4"; Type Comments=Triple Vari-Plume Laboratory Exhaust Centrifugal Airfoil Class 1 Arr 10 With Mixing Box
- Triple_225_CAVP-15L_CLASS_1_With_Mixing_Box: ((M - (2 * (D - L - K - J))) / 2) + (TRANSITION / 2)=16 9/32"; (B/2)+1.5"=15 7/32"; (B/2)-.125"=13 19/32"; (D-J-K-L)*2=2"; (E/2)-((B/2)+1.5")=8 15/16"; (E/2)-((MB_P/2)+.125")=5 1/32"; (E/2)-(E/52*15)=10 7/32"; (F-((F-H)/2))/2=12 13/16"; (M - (2 * (D - L - K - J)))/2=8 23/32"; (MB_P/2)+.125"=19 1/8"; (MB_P/2-.125")+((F / 2) - 2")=-31 11/16"; (MB_P/2-.125")-((F / 2) - 2")=-6 1/16"; (MB_Q/2)+.125"=19 1/8"; (NOZZLE_HEIGHT - (NOZZLE_HEIGHT / 8 * 2)) / 2=16 1/8"; (NOZZLE_WB_OD - NOZZLE_TOP_OD) / 4=3 1/4"; -((MB_Q / 2) + 1/8")=-19 1/8"; -(F-((F-H)/2))/2=-12 13/16"; -MB_HEIGHT=-43 1/4"; -MB_P=-38"; -MB_P-.25=-38 1/4"; A=106 11/16"; A/2=53 11/32"; B=27 7/16"; B/2=13 23/32"; B/4=6 7/8"; C=59 3/16"; C/2=29 19/32"; CLASS=1"; D=46 1/16"; D-L-K-J=1"; D-M=26 5/8"; DUAL_Q=114 3/8"; DUAL_Q+.25"=114 5/8"; E=48 5/16"; E-(NOZZLE_RAD/3*2)=17 1/32"; E-N-N-H=2"; E/2=24 5/32"; E/2-H/2=10 11/32"; E/52*15=13 15/16"; E/52*30=27 7/8"; F=29 5/8"; F/2=14 13/16"; H=27 5/8"; H/2=13 13/16"; HEIGHT=45 11/32"; J=8 1/2"; J+K+L=45 1/16"; K=15 1/8"; L=21 7/16"; M=19 7/16"; M-(2*(D-L-K-J))=17 7/16"; MB_A=117 5/8"; MB_F=5 3/4"; MB_F-3"=2 3/4"; MB_HEIGHT=43 1/4"; MB_HEIGHT/2=21 5/8"; MB_N=14 3/16"; MB_N-(D-J-K-L)=13 3/16"; MB_P=38"; MB_P+.25"=38 1/4"; MB_P+MB_P+.5=76 1/2"; MB_P-4.5"=33 1/2"; MB_Q=38"; N=8 11/32"; N+(H/2)=22 5/32"; NOZZLE_BOTTOM_ID=21 3/8"; NOZZLE_BOTTOM_RAD=10 11/16"; NOZZLE_BOTTOM_RAD-3*2=4 11/16"; NOZZLE_HEIGHT=43"; NOZZLE_HEIGHT/7*2=10 3/4"; NOZZLE_SIZE=15"; NOZZLE_TOP_OD=23"; NOZZLE_TOP_RAD=11 1/2"; NOZZLE_WB/4=7 3/16"; NOZZLE_WB_OD=36"; NOZZLE_WB_RAD=18"; NOZZLE_WB_RAD-2"=16"; P=60"; R=24 1/4"; R*1.1=26 11/16"; R+((B/2)+1.5")=39 15/32"; R-((B/2)+1.5")=9 1/32"; RO/2=16 3/4"; RO2/2=93 1/8"; TRANSITION=15 1/8"; TRANSITION/2=7 9/16"; TRIP_Q=190 3/4"; TRIP_Q-4.5"=186 1/4"; Type Comments=Triple Vari-Plume Laboratory Exhaust Centrifugal Airfoil Class 1 Arr 10 With Mixing Box
- Triple_225_CAVP-18H_CLASS_1_With_Mixing_Box: ((M - (2 * (D - L - K - J))) / 2) + (TRANSITION / 2)=17 25/32"; (B/2)+1.5"=15 7/32"; (B/2)-.125"=13 19/32"; (D-J-K-L)*2=2"; (E/2)-((B/2)+1.5")=8 15/16"; (E/2)-((MB_P/2)+.125")=5 1/32"; (E/2)-(E/52*15)=10 7/32"; (F-((F-H)/2))/2=12 13/16"; (M - (2 * (D - L - K - J)))/2=8 23/32"; (MB_P/2)+.125"=19 1/8"; (MB_P/2-.125")+((F / 2) - 2")=-31 11/16"; (MB_P/2-.125")-((F / 2) - 2")=-6 1/16"; (MB_Q/2)+.125"=19 1/8"; (NOZZLE_HEIGHT - (NOZZLE_HEIGHT / 8 * 2)) / 2=18"; (NOZZLE_WB_OD - NOZZLE_TOP_OD) / 4=3 7/8"; -((MB_Q / 2) + 1/8")=-19 1/8"; -(F-((F-H)/2))/2=-12 13/16"; -MB_HEIGHT=-43 1/4"; -MB_P=-38"; -MB_P-.25=-38 1/4"; A=106 11/16"; A/2=53 11/32"; B=27 7/16"; B/2=13 23/32"; B/4=6 7/8"; C=59 3/16"; C/2=29 19/32"; CLASS=1"; D=46 1/16"; D-L-K-J=1"; D-M=26 5/8"; DUAL_Q=114 3/8"; DUAL_Q+.25"=114 5/8"; E=48 5/16"; E-(NOZZLE_RAD/3*2)=15 5/8"; E-N-N-H=2"; E/2=24 5/32"; E/2-H/2=10 11/32"; E/52*15=13 15/16"; E/52*30=27 7/8"; F=29 5/8"; F/2=14 13/16"; H=27 5/8"; H/2=13 13/16"; HEIGHT=45 11/32"; J=8 1/2"; J+K+L=45 1/16"; K=15 1/8"; L=21 7/16"; M=19 7/16"; M-(2*(D-L-K-J))=17 7/16"; MB_A=117 5/8"; MB_F=5 3/4"; MB_F-3"=2 3/4"; MB_HEIGHT=43 1/4"; MB_HEIGHT/2=21 5/8"; MB_N=14 3/16"; MB_N-(D-J-K-L)=13 3/16"; MB_P=38"; MB_P+.25"=38 1/4"; MB_P+MB_P+.5=76 1/2"; MB_P-4.5"=33 1/2"; MB_Q=38"; N=8 11/32"; N+(H/2)=22 5/32"; NOZZLE_BOTTOM_ID=25 5/8"; NOZZLE_BOTTOM_RAD=12 13/16"; NOZZLE_BOTTOM_RAD-3*2=6 13/16"; NOZZLE_HEIGHT=48"; NOZZLE_HEIGHT/7*2=12"; NOZZLE_SIZE=18"; NOZZLE_TOP_OD=27 1/2"; NOZZLE_TOP_RAD=13 3/4"; NOZZLE_WB/4=8 19/32"; NOZZLE_WB_OD=43"; NOZZLE_WB_RAD=21 1/2"; NOZZLE_WB_RAD-2"=19 1/2"; P=60"; R=24 1/4"; R*1.1=26 11/16"; R+((B/2)+1.5")=39 15/32"; R-((B/2)+1.5")=9 1/32"; RO/2=16 3/4"; RO2/2=93 1/8"; TRANSITION=18 1/8"; TRANSITION/2=9 1/16"; TRIP_Q=190 3/4"; TRIP_Q-4.5"=186 1/4"; Type Comments=Triple Vari-Plume Laboratory Exhaust Centrifugal Airfoil Class 1 Arr 10 With Mixing Box
- Triple_225_CAVP-18L_CLASS_1_With_Mixing_Box: ((M - (2 * (D - L - K - J))) / 2) + (TRANSITION / 2)=17 25/32"; (B/2)+1.5"=15 7/32"; (B/2)-.125"=13 19/32"; (D-J-K-L)*2=2"; (E/2)-((B/2)+1.5")=8 15/16"; (E/2)-((MB_P/2)+.125")=5 1/32"; (E/2)-(E/52*15)=10 7/32"; (F-((F-H)/2))/2=12 13/16"; (M - (2 * (D - L - K - J)))/2=8 23/32"; (MB_P/2)+.125"=19 1/8"; (MB_P/2-.125")+((F / 2) - 2")=-31 11/16"; (MB_P/2-.125")-((F / 2) - 2")=-6 1/16"; (MB_Q/2)+.125"=19 1/8"; (NOZZLE_HEIGHT - (NOZZLE_HEIGHT / 8 * 2)) / 2=18"; (NOZZLE_WB_OD - NOZZLE_TOP_OD) / 4=3 7/8"; -((MB_Q / 2) + 1/8")=-19 1/8"; -(F-((F-H)/2))/2=-12 13/16"; -MB_HEIGHT=-43 1/4"; -MB_P=-38"; -MB_P-.25=-38 1/4"; A=106 11/16"; A/2=53 11/32"; B=27 7/16"; B/2=13 23/32"; B/4=6 7/8"; C=59 3/16"; C/2=29 19/32"; CLASS=1"; D=46 1/16"; D-L-K-J=1"; D-M=26 5/8"; DUAL_Q=114 3/8"; DUAL_Q+.25"=114 5/8"; E=48 5/16"; E-(NOZZLE_RAD/3*2)=15 5/8"; E-N-N-H=2"; E/2=24 5/32"; E/2-H/2=10 11/32"; E/52*15=13 15/16"; E/52*30=27 7/8"; F=29 5/8"; F/2=14 13/16"; H=27 5/8"; H/2=13 13/16"; HEIGHT=45 11/32"; J=8 1/2"; J+K+L=45 1/16"; K=15 1/8"; L=21 7/16"; M=19 7/16"; M-(2*(D-L-K-J))=17 7/16"; MB_A=117 5/8"; MB_F=5 3/4"; MB_F-3"=2 3/4"; MB_HEIGHT=43 1/4"; MB_HEIGHT/2=21 5/8"; MB_N=14 3/16"; MB_N-(D-J-K-L)=13 3/16"; MB_P=38"; MB_P+.25"=38 1/4"; MB_P+MB_P+.5=76 1/2"; MB_P-4.5"=33 1/2"; MB_Q=38"; N=8 11/32"; N+(H/2)=22 5/32"; NOZZLE_BOTTOM_ID=25 5/8"; NOZZLE_BOTTOM_RAD=12 13/16"; NOZZLE_BOTTOM_RAD-3*2=6 13/16"; NOZZLE_HEIGHT=48"; NOZZLE_HEIGHT/7*2=12"; NOZZLE_SIZE=18"; NOZZLE_TOP_OD=27 1/2"; NOZZLE_TOP_RAD=13 3/4"; NOZZLE_WB/4=8 19/32"; NOZZLE_WB_OD=43"; NOZZLE_WB_RAD=21 1/2"; NOZZLE_WB_RAD-2"=19 1/2"; P=60"; R=24 1/4"; R*1.1=26 11/16"; R+((B/2)+1.5")=39 15/32"; R-((B/2)+1.5")=9 1/32"; RO/2=16 3/4"; RO2/2=93 1/8"; TRANSITION=18 1/8"; TRANSITION/2=9 1/16"; TRIP_Q=190 3/4"; TRIP_Q-4.5"=186 1/4"; Type Comments=Triple Vari-Plume Laboratory Exhaust Centrifugal Airfoil Class 1 Arr 10 With Mixing Box
- Triple_225_CAVP-18H_CLASS_2_With_Mixing_Box: ((M - (2 * (D - L - K - J))) / 2) + (TRANSITION / 2)=17 25/32"; (B/2)+1.5"=15 7/32"; (B/2)-.125"=13 19/32"; (D-J-K-L)*2=2"; (E/2)-((B/2)+1.5")=8 15/16"; (E/2)-((MB_P/2)+.125")=5 1/32"; (E/2)-(E/52*15)=10 7/32"; (F-((F-H)/2))/2=12 13/16"; (M - (2 * (D - L - K - J)))/2=8 23/32"; (MB_P/2)+.125"=19 1/8"; (MB_P/2-.125")+((F / 2) - 2")=-31 11/16"; (MB_P/2-.125")-((F / 2) - 2")=-6 1/16"; (MB_Q/2)+.125"=19 1/8"; (NOZZLE_HEIGHT - (NOZZLE_HEIGHT / 8 * 2)) / 2=18"; (NOZZLE_WB_OD - NOZZLE_TOP_OD) / 4=3 7/8"; -((MB_Q / 2) + 1/8")=-19 1/8"; -(F-((F-H)/2))/2=-12 13/16"; -MB_HEIGHT=-43 1/4"; -MB_P=-38"; -MB_P-.25=-38 1/4"; A=106 11/16"; A/2=53 11/32"; B=27 7/16"; B/2=13 23/32"; B/4=6 7/8"; C=59 3/16"; C/2=29 19/32"; CLASS=2"; D=50 1/16"; D-L-K-J=1"; D-M=30 5/8"; DUAL_Q=114 3/8"; DUAL_Q+.25"=114 5/8"; E=48 5/16"; E-(NOZZLE_RAD/3*2)=15 5/8"; E-N-N-H=1 27/32"; E/2=24 5/32"; E/2-H/2=10 11/32"; E/52*15=13 15/16"; E/52*30=27 7/8"; F=29 5/8"; F/2=14 13/16"; H=27 5/8"; H/2=13 13/16"; HEIGHT=45 11/32"; J=8 1/4"; J+K+L=49 1/16"; K=19 3/8"; L=21 7/16"; M=19 7/16"; M-(2*(D-L-K-J))=17 7/16"; MB_A=121 5/8"; MB_F=5 3/4"; MB_F-3"=2 3/4"; MB_HEIGHT=43 1/4"; MB_HEIGHT/2=21 5/8"; MB_N=14 3/16"; MB_N-(D-J-K-L)=13 3/16"; MB_P=38"; MB_P+.25"=38 1/4"; MB_P+MB_P+.5=76 1/2"; MB_P-4.5"=33 1/2"; MB_Q=38"; N=8 1/2"; N+(H/2)=22 5/16"; NOZZLE_BOTTOM_ID=25 5/8"; NOZZLE_BOTTOM_RAD=12 13/16"; NOZZLE_BOTTOM_RAD-3*2=6 13/16"; NOZZLE_HEIGHT=48"; NOZZLE_HEIGHT/7*2=12"; NOZZLE_SIZE=18"; NOZZLE_TOP_OD=27 1/2"; NOZZLE_TOP_RAD=13 3/4"; NOZZLE_WB/4=8 19/32"; NOZZLE_WB_OD=43"; NOZZLE_WB_RAD=21 1/2"; NOZZLE_WB_RAD-2"=19 1/2"; P=60"; R=24 1/4"; R*1.1=26 11/16"; R+((B/2)+1.5")=39 15/32"; R-((B/2)+1.5")=9 1/32"; RO/2=16 3/4"; RO2/2=93 1/8"; TRANSITION=18 1/8"; TRANSITION/2=9 1/16"; TRIP_Q=190 3/4"; TRIP_Q-4.5"=186 1/4"; Type Comments=Triple Vari-Plume Laboratory Exhaust Centrifugal Airfoil Class 2 Arr 10 With Mixing Box
- Triple_225_CAVP-18L_CLASS_2_With_Mixing_Box: ((M - (2 * (D - L - K - J))) / 2) + (TRANSITION / 2)=17 25/32"; (B/2)+1.5"=15 7/32"; (B/2)-.125"=13 19/32"; (D-J-K-L)*2=2"; (E/2)-((B/2)+1.5")=8 15/16"; (E/2)-((MB_P/2)+.125")=5 1/32"; (E/2)-(E/52*15)=10 7/32"; (F-((F-H)/2))/2=12 13/16"; (M - (2 * (D - L - K - J)))/2=8 23/32"; (MB_P/2)+.125"=19 1/8"; (MB_P/2-.125")+((F / 2) - 2")=-31 11/16"; (MB_P/2-.125")-((F / 2) - 2")=-6 1/16"; (MB_Q/2)+.125"=19 1/8"; (NOZZLE_HEIGHT - (NOZZLE_HEIGHT / 8 * 2)) / 2=18"; (NOZZLE_WB_OD - NOZZLE_TOP_OD) / 4=3 7/8"; -((MB_Q / 2) + 1/8")=-19 1/8"; -(F-((F-H)/2))/2=-12 13/16"; -MB_HEIGHT=-43 1/4"; -MB_P=-38"; -MB_P-.25=-38 1/4"; A=106 11/16"; A/2=53 11/32"; B=27 7/16"; B/2=13 23/32"; B/4=6 7/8"; C=59 3/16"; C/2=29 19/32"; CLASS=2"; D=50 1/16"; D-L-K-J=1"; D-M=30 5/8"; DUAL_Q=114 3/8"; DUAL_Q+.25"=114 5/8"; E=48 5/16"; E-(NOZZLE_RAD/3*2)=15 5/8"; E-N-N-H=1 27/32"; E/2=24 5/32"; E/2-H/2=10 11/32"; E/52*15=13 15/16"; E/52*30=27 7/8"; F=29 5/8"; F/2=14 13/16"; H=27 5/8"; H/2=13 13/16"; HEIGHT=45 11/32"; J=8 1/4"; J+K+L=49 1/16"; K=19 3/8"; L=21 7/16"; M=19 7/16"; M-(2*(D-L-K-J))=17 7/16"; MB_A=121 5/8"; MB_F=5 3/4"; MB_F-3"=2 3/4"; MB_HEIGHT=43 1/4"; MB_HEIGHT/2=21 5/8"; MB_N=14 3/16"; MB_N-(D-J-K-L)=13 3/16"; MB_P=38"; MB_P+.25"=38 1/4"; MB_P+MB_P+.5=76 1/2"; MB_P-4.5"=33 1/2"; MB_Q=38"; N=8 1/2"; N+(H/2)=22 5/16"; NOZZLE_BOTTOM_ID=25 5/8"; NOZZLE_BOTTOM_RAD=12 13/16"; NOZZLE_BOTTOM_RAD-3*2=6 13/16"; NOZZLE_HEIGHT=48"; NOZZLE_HEIGHT/7*2=12"; NOZZLE_SIZE=18"; NOZZLE_TOP_OD=27 1/2"; NOZZLE_TOP_RAD=13 3/4"; NOZZLE_WB/4=8 19/32"; NOZZLE_WB_OD=43"; NOZZLE_WB_RAD=21 1/2"; NOZZLE_WB_RAD-2"=19 1/2"; P=60"; R=24 1/4"; R*1.1=26 11/16"; R+((B/2)+1.5")=39 15/32"; R-((B/2)+1.5")=9 1/32"; RO/2=16 3/4"; RO2/2=93 1/8"; TRANSITION=18 1/8"; TRANSITION/2=9 1/16"; TRIP_Q=190 3/4"; TRIP_Q-4.5"=186 1/4"; Type Comments=Triple Vari-Plume Laboratory Exhaust Centrifugal Airfoil Class 2 Arr 10 With Mixing Box
- Triple_225_CAVP-15H_CLASS_2_With_Mixing_Box: ((M - (2 * (D - L - K - J))) / 2) + (TRANSITION / 2)=16 9/32"; (B/2)+1.5"=15 7/32"; (B/2)-.125"=13 19/32"; (D-J-K-L)*2=2"; (E/2)-((B/2)+1.5")=8 15/16"; (E/2)-((MB_P/2)+.125")=5 1/32"; (E/2)-(E/52*15)=10 7/32"; (F-((F-H)/2))/2=12 13/16"; (M - (2 * (D - L - K - J)))/2=8 23/32"; (MB_P/2)+.125"=19 1/8"; (MB_P/2-.125")+((F / 2) - 2")=-31 11/16"; (MB_P/2-.125")-((F / 2) - 2")=-6 1/16"; (MB_Q/2)+.125"=19 1/8"; (NOZZLE_HEIGHT - (NOZZLE_HEIGHT / 8 * 2)) / 2=16 1/8"; (NOZZLE_WB_OD - NOZZLE_TOP_OD) / 4=3 1/4"; -((MB_Q / 2) + 1/8")=-19 1/8"; -(F-((F-H)/2))/2=-12 13/16"; -MB_HEIGHT=-43 1/4"; -MB_P=-38"; -MB_P-.25=-38 1/4"; A=106 11/16"; A/2=53 11/32"; B=27 7/16"; B/2=13 23/32"; B/4=6 7/8"; C=59 3/16"; C/2=29 19/32"; CLASS=2"; D=50 1/16"; D-L-K-J=1"; D-M=30 5/8"; DUAL_Q=114 3/8"; DUAL_Q+.25"=114 5/8"; E=48 5/16"; E-(NOZZLE_RAD/3*2)=17 1/32"; E-N-N-H=1 27/32"; E/2=24 5/32"; E/2-H/2=10 11/32"; E/52*15=13 15/16"; E/52*30=27 7/8"; F=29 5/8"; F/2=14 13/16"; H=27 5/8"; H/2=13 13/16"; HEIGHT=45 11/32"; J=8 1/4"; J+K+L=49 1/16"; K=19 3/8"; L=21 7/16"; M=19 7/16"; M-(2*(D-L-K-J))=17 7/16"; MB_A=121 5/8"; MB_F=5 3/4"; MB_F-3"=2 3/4"; MB_HEIGHT=43 1/4"; MB_HEIGHT/2=21 5/8"; MB_N=14 3/16"; MB_N-(D-J-K-L)=13 3/16"; MB_P=38"; MB_P+.25"=38 1/4"; MB_P+MB_P+.5=76 1/2"; MB_P-4.5"=33 1/2"; MB_Q=38"; N=8 1/2"; N+(H/2)=22 5/16"; NOZZLE_BOTTOM_ID=21 3/8"; NOZZLE_BOTTOM_RAD=10 11/16"; NOZZLE_BOTTOM_RAD-3*2=4 11/16"; NOZZLE_HEIGHT=43"; NOZZLE_HEIGHT/7*2=10 3/4"; NOZZLE_SIZE=15"; NOZZLE_TOP_OD=23"; NOZZLE_TOP_RAD=11 1/2"; NOZZLE_WB/4=7 3/16"; NOZZLE_WB_OD=36"; NOZZLE_WB_RAD=18"; NOZZLE_WB_RAD-2"=16"; P=60"; R=24 1/4"; R*1.1=26 11/16"; R+((B/2)+1.5")=39 15/32"; R-((B/2)+1.5")=9 1/32"; RO/2=16 3/4"; RO2/2=93 1/8"; TRANSITION=15 1/8"; TRANSITION/2=7 9/16"; TRIP_Q=190 3/4"; TRIP_Q-4.5"=186 1/4"; Type Comments=Triple Vari-Plume Laboratory Exhaust Centrifugal Airfoil Class 2 Arr 10 With Mixing Box
- Triple_225_CAVP-15L_CLASS_2_With_Mixing_Box: ((M - (2 * (D - L - K - J))) / 2) + (TRANSITION / 2)=16 9/32"; (B/2)+1.5"=15 7/32"; (B/2)-.125"=13 19/32"; (D-J-K-L)*2=2"; (E/2)-((B/2)+1.5")=8 15/16"; (E/2)-((MB_P/2)+.125")=5 1/32"; (E/2)-(E/52*15)=10 7/32"; (F-((F-H)/2))/2=12 13/16"; (M - (2 * (D - L - K - J)))/2=8 23/32"; (MB_P/2)+.125"=19 1/8"; (MB_P/2-.125")+((F / 2) - 2")=-31 11/16"; (MB_P/2-.125")-((F / 2) - 2")=-6 1/16"; (MB_Q/2)+.125"=19 1/8"; (NOZZLE_HEIGHT - (NOZZLE_HEIGHT / 8 * 2)) / 2=16 1/8"; (NOZZLE_WB_OD - NOZZLE_TOP_OD) / 4=3 1/4"; -((MB_Q / 2) + 1/8")=-19 1/8"; -(F-((F-H)/2))/2=-12 13/16"; -MB_HEIGHT=-43 1/4"; -MB_P=-38"; -MB_P-.25=-38 1/4"; A=106 11/16"; A/2=53 11/32"; B=27 7/16"; B/2=13 23/32"; B/4=6 7/8"; C=59 3/16"; C/2=29 19/32"; CLASS=2"; D=50 1/16"; D-L-K-J=1"; D-M=30 5/8"; DUAL_Q=114 3/8"; DUAL_Q+.25"=114 5/8"; E=48 5/16"; E-(NOZZLE_RAD/3*2)=17 1/32"; E-N-N-H=1 27/32"; E/2=24 5/32"; E/2-H/2=10 11/32"; E/52*15=13 15/16"; E/52*30=27 7/8"; F=29 5/8"; F/2=14 13/16"; H=27 5/8"; H/2=13 13/16"; HEIGHT=45 11/32"; J=8 1/4"; J+K+L=49 1/16"; K=19 3/8"; L=21 7/16"; M=19 7/16"; M-(2*(D-L-K-J))=17 7/16"; MB_A=121 5/8"; MB_F=5 3/4"; MB_F-3"=2 3/4"; MB_HEIGHT=43 1/4"; MB_HEIGHT/2=21 5/8"; MB_N=14 3/16"; MB_N-(D-J-K-L)=13 3/16"; MB_P=38"; MB_P+.25"=38 1/4"; MB_P+MB_P+.5=76 1/2"; MB_P-4.5"=33 1/2"; MB_Q=38"; N=8 1/2"; N+(H/2)=22 5/16"; NOZZLE_BOTTOM_ID=21 3/8"; NOZZLE_BOTTOM_RAD=10 11/16"; NOZZLE_BOTTOM_RAD-3*2=4 11/16"; NOZZLE_HEIGHT=43"; NOZZLE_HEIGHT/7*2=10 3/4"; NOZZLE_SIZE=15"; NOZZLE_TOP_OD=23"; NOZZLE_TOP_RAD=11 1/2"; NOZZLE_WB/4=7 3/16"; NOZZLE_WB_OD=36"; NOZZLE_WB_RAD=18"; NOZZLE_WB_RAD-2"=16"; P=60"; R=24 1/4"; R*1.1=26 11/16"; R+((B/2)+1.5")=39 15/32"; R-((B/2)+1.5")=9 1/32"; RO/2=16 3/4"; RO2/2=93 1/8"; TRANSITION=15 1/8"; TRANSITION/2=7 9/16"; TRIP_Q=190 3/4"; TRIP_Q-4.5"=186 1/4"; Type Comments=Triple Vari-Plume Laboratory Exhaust Centrifugal Airfoil Class 2 Arr 10 With Mixing Box
- Triple_225_CAVP-12H_CLASS_2_With_Mixing_Box: ((M - (2 * (D - L - K - J))) / 2) + (TRANSITION / 2)=14 3/4"; (B/2)+1.5"=15 7/32"; (B/2)-.125"=13 19/32"; (D-J-K-L)*2=2"; (E/2)-((B/2)+1.5")=8 15/16"; (E/2)-((MB_P/2)+.125")=5 1/32"; (E/2)-(E/52*15)=10 7/32"; (F-((F-H)/2))/2=12 13/16"; (M - (2 * (D - L - K - J)))/2=8 23/32"; (MB_P/2)+.125"=19 1/8"; (MB_P/2-.125")+((F / 2) - 2")=-31 11/16"; (MB_P/2-.125")-((F / 2) - 2")=-6 1/16"; (MB_Q/2)+.125"=19 1/8"; (NOZZLE_HEIGHT - (NOZZLE_HEIGHT / 8 * 2)) / 2=12"; (NOZZLE_WB_OD - NOZZLE_TOP_OD) / 4=2 1/8"; -((MB_Q / 2) + 1/8")=-19 1/8"; -(F-((F-H)/2))/2=-12 13/16"; -MB_HEIGHT=-43 1/4"; -MB_P=-38"; -MB_P-.25=-38 1/4"; A=106 11/16"; A/2=53 11/32"; B=27 7/16"; B/2=13 23/32"; B/4=6 7/8"; C=59 3/16"; C/2=29 19/32"; CLASS=2"; D=50 1/16"; D-L-K-J=1"; D-M=30 5/8"; DUAL_Q=114 3/8"; DUAL_Q+.25"=114 5/8"; E=48 5/16"; E-(NOZZLE_RAD/3*2)=18 15/32"; E-N-N-H=1 27/32"; E/2=24 5/32"; E/2-H/2=10 11/32"; E/52*15=13 15/16"; E/52*30=27 7/8"; F=29 5/8"; F/2=14 13/16"; H=27 5/8"; H/2=13 13/16"; HEIGHT=45 11/32"; J=8 1/4"; J+K+L=49 1/16"; K=19 3/8"; L=21 7/16"; M=19 7/16"; M-(2*(D-L-K-J))=17 7/16"; MB_A=121 5/8"; MB_F=5 3/4"; MB_F-3"=2 3/4"; MB_HEIGHT=43 1/4"; MB_HEIGHT/2=21 5/8"; MB_N=14 3/16"; MB_N-(D-J-K-L)=13 3/16"; MB_P=38"; MB_P+.25"=38 1/4"; MB_P+MB_P+.5=76 1/2"; MB_P-4.5"=33 1/2"; MB_Q=38"; N=8 1/2"; N+(H/2)=22 5/16"; NOZZLE_BOTTOM_ID=17 1/16"; NOZZLE_BOTTOM_RAD=8 17/32"; NOZZLE_BOTTOM_RAD-3*2=2 17/32"; NOZZLE_HEIGHT=32"; NOZZLE_HEIGHT/7*2=8"; NOZZLE_SIZE=12"; NOZZLE_TOP_OD=19 1/2"; NOZZLE_TOP_RAD=9 3/4"; NOZZLE_WB/4=5 19/32"; NOZZLE_WB_OD=28"; NOZZLE_WB_RAD=14"; NOZZLE_WB_RAD-2"=12"; P=60"; R=24 1/4"; R*1.1=26 11/16"; R+((B/2)+1.5")=39 15/32"; R-((B/2)+1.5")=9 1/32"; RO/2=16 3/4"; RO2/2=93 1/8"; TRANSITION=12 1/16"; TRANSITION/2=6 1/32"; TRIP_Q=190 3/4"; TRIP_Q-4.5"=186 1/4"; Type Comments=Triple Vari-Plume Laboratory Exhaust Centrifugal Airfoil Class 2 Arr 10 With Mixing Box
- Triple_225_CAVP-12L_CLASS_2_With_Mixing_Box: ((M - (2 * (D - L - K - J))) / 2) + (TRANSITION / 2)=14 3/4"; (B/2)+1.5"=15 7/32"; (B/2)-.125"=13 19/32"; (D-J-K-L)*2=2"; (E/2)-((B/2)+1.5")=8 15/16"; (E/2)-((MB_P/2)+.125")=5 1/32"; (E/2)-(E/52*15)=10 7/32"; (F-((F-H)/2))/2=12 13/16"; (M - (2 * (D - L - K - J)))/2=8 23/32"; (MB_P/2)+.125"=19 1/8"; (MB_P/2-.125")+((F / 2) - 2")=-31 11/16"; (MB_P/2-.125")-((F / 2) - 2")=-6 1/16"; (MB_Q/2)+.125"=19 1/8"; (NOZZLE_HEIGHT - (NOZZLE_HEIGHT / 8 * 2)) / 2=12"; (NOZZLE_WB_OD - NOZZLE_TOP_OD) / 4=2 1/8"; -((MB_Q / 2) + 1/8")=-19 1/8"; -(F-((F-H)/2))/2=-12 13/16"; -MB_HEIGHT=-43 1/4"; -MB_P=-38"; -MB_P-.25=-38 1/4"; A=106 11/16"; A/2=53 11/32"; B=27 7/16"; B/2=13 23/32"; B/4=6 7/8"; C=59 3/16"; C/2=29 19/32"; CLASS=2"; D=50 1/16"; D-L-K-J=1"; D-M=30 5/8"; DUAL_Q=114 3/8"; DUAL_Q+.25"=114 5/8"; E=48 5/16"; E-(NOZZLE_RAD/3*2)=18 15/32"; E-N-N-H=1 27/32"; E/2=24 5/32"; E/2-H/2=10 11/32"; E/52*15=13 15/16"; E/52*30=27 7/8"; F=29 5/8"; F/2=14 13/16"; H=27 5/8"; H/2=13 13/16"; HEIGHT=45 11/32"; J=8 1/4"; J+K+L=49 1/16"; K=19 3/8"; L=21 7/16"; M=19 7/16"; M-(2*(D-L-K-J))=17 7/16"; MB_A=121 5/8"; MB_F=5 3/4"; MB_F-3"=2 3/4"; MB_HEIGHT=43 1/4"; MB_HEIGHT/2=21 5/8"; MB_N=14 3/16"; MB_N-(D-J-K-L)=13 3/16"; MB_P=38"; MB_P+.25"=38 1/4"; MB_P+MB_P+.5=76 1/2"; MB_P-4.5"=33 1/2"; MB_Q=38"; N=8 1/2"; N+(H/2)=22 5/16"; NOZZLE_BOTTOM_ID=17 1/16"; NOZZLE_BOTTOM_RAD=8 17/32"; NOZZLE_BOTTOM_RAD-3*2=2 17/32"; NOZZLE_HEIGHT=32"; NOZZLE_HEIGHT/7*2=8"; NOZZLE_SIZE=12"; NOZZLE_TOP_OD=19 1/2"; NOZZLE_TOP_RAD=9 3/4"; NOZZLE_WB/4=5 19/32"; NOZZLE_WB_OD=28"; NOZZLE_WB_RAD=14"; NOZZLE_WB_RAD-2"=12"; P=60"; R=24 1/4"; R*1.1=26 11/16"; R+((B/2)+1.5")=39 15/32"; R-((B/2)+1.5")=9 1/32"; RO/2=16 3/4"; RO2/2=93 1/8"; TRANSITION=12 1/16"; TRANSITION/2=6 1/32"; TRIP_Q=190 3/4"; TRIP_Q-4.5"=186 1/4"; Type Comments=Triple Vari-Plume Laboratory Exhaust Centrifugal Airfoil Class 2 Arr 10 With Mixing Box
- Triple_245_CAVP-12L_CLASS_1_With_Mixing_Box: ((M - (2 * (D - L - K - J))) / 2) + (TRANSITION / 2)=15 17/32"; (B/2)+1.5"=16 7/32"; (B/2)-.125"=14 19/32"; (D-J-K-L)*2=2"; (E/2)-((B/2)+1.5")=10"; (E/2)-((MB_P/2)+.125")=6 3/32"; (E/2)-(E/52*15)=11 3/32"; (F-((F-H)/2))/2=13 13/16"; (M - (2 * (D - L - K - J)))/2=9 1/2"; (MB_P/2)+.125"=20 1/8"; (MB_P/2-.125")+((F / 2) - 2")=-33 11/16"; (MB_P/2-.125")-((F / 2) - 2")=-6 1/16"; (MB_Q/2)+.125"=20 1/8"; (NOZZLE_HEIGHT - (NOZZLE_HEIGHT / 8 * 2)) / 2=12"; (NOZZLE_WB_OD - NOZZLE_TOP_OD) / 4=2 1/8"; -((MB_Q / 2) + 1/8")=-20 1/8"; -(F-((F-H)/2))/2=-13 13/16"; -MB_HEIGHT=-45 1/4"; -MB_P=-40"; -MB_P-.25=-40 1/4"; A=112 1/4"; A/2=56 1/8"; B=29 7/16"; B/2=14 23/32"; B/4=7 3/8"; C=64 3/4"; C/2=32 3/8"; CLASS=1"; D=49 7/8"; D-L-K-J=1"; D-M=28 7/8"; DUAL_Q=120 3/8"; DUAL_Q+.25"=120 5/8"; E=52 7/16"; E-(NOZZLE_RAD/3*2)=20 17/32"; E-N-N-H=2"; E/2=26 7/32"; E/2-H/2=11 13/32"; E/52*15=15 1/8"; E/52*30=30 1/4"; F=31 5/8"; F/2=15 13/16"; H=29 5/8"; H/2=14 13/16"; HEIGHT=49 29/32"; J=9"; J+K+L=48 7/8"; K=16 7/8"; L=23"; M=21"; M-(2*(D-L-K-J))=19"; MB_A=124 15/16"; MB_F=7 1/2"; MB_F-3"=4 1/2"; MB_HEIGHT=45 1/4"; MB_HEIGHT/2=22 5/8"; MB_N=14 3/16"; MB_N-(D-J-K-L)=13 3/16"; MB_P=40"; MB_P+.25"=40 1/4"; MB_P+MB_P+.5=80 1/2"; MB_P-4.5"=35 1/2"; MB_Q=40"; N=9 13/32"; N+(H/2)=24 7/32"; NOZZLE_BOTTOM_ID=17 1/16"; NOZZLE_BOTTOM_RAD=8 17/32"; NOZZLE_BOTTOM_RAD-3*2=2 17/32"; NOZZLE_HEIGHT=32"; NOZZLE_HEIGHT/7*2=8"; NOZZLE_SIZE=12"; NOZZLE_TOP_OD=19 1/2"; NOZZLE_TOP_RAD=9 3/4"; NOZZLE_WB/4=5 19/32"; NOZZLE_WB_OD=28"; NOZZLE_WB_RAD=14"; NOZZLE_WB_RAD-2"=12"; P=60"; R=27"; R*1.1=29 11/16"; R+((B/2)+1.5")=43 7/32"; R-((B/2)+1.5")=10 25/32"; RO/2=17 3/4"; RO2/2=98 1/8"; TRANSITION=12 1/16"; TRANSITION/2=6 1/32"; TRIP_Q=200 3/4"; TRIP_Q-4.5"=196 1/4"; Type Comments=Triple Vari-Plume Laboratory Exhaust Centrifugal Airfoil Class 1 Arr 10 With Mixing Box
- Triple_245_CAVP-12H_CLASS_1_With_Mixing_Box: ((M - (2 * (D - L - K - J))) / 2) + (TRANSITION / 2)=15 17/32"; (B/2)+1.5"=16 7/32"; (B/2)-.125"=14 19/32"; (D-J-K-L)*2=2"; (E/2)-((B/2)+1.5")=10"; (E/2)-((MB_P/2)+.125")=6 3/32"; (E/2)-(E/52*15)=11 3/32"; (F-((F-H)/2))/2=13 13/16"; (M - (2 * (D - L - K - J)))/2=9 1/2"; (MB_P/2)+.125"=20 1/8"; (MB_P/2-.125")+((F / 2) - 2")=-33 11/16"; (MB_P/2-.125")-((F / 2) - 2")=-6 1/16"; (MB_Q/2)+.125"=20 1/8"; (NOZZLE_HEIGHT - (NOZZLE_HEIGHT / 8 * 2)) / 2=12"; (NOZZLE_WB_OD - NOZZLE_TOP_OD) / 4=2 1/8"; -((MB_Q / 2) + 1/8")=-20 1/8"; -(F-((F-H)/2))/2=-13 13/16"; -MB_HEIGHT=-45 1/4"; -MB_P=-40"; -MB_P-.25=-40 1/4"; A=112 1/4"; A/2=56 1/8"; B=29 7/16"; B/2=14 23/32"; B/4=7 3/8"; C=64 3/4"; C/2=32 3/8"; CLASS=1"; D=49 7/8"; D-L-K-J=1"; D-M=28 7/8"; DUAL_Q=120 3/8"; DUAL_Q+.25"=120 5/8"; E=52 7/16"; E-(NOZZLE_RAD/3*2)=20 17/32"; E-N-N-H=2"; E/2=26 7/32"; E/2-H/2=11 13/32"; E/52*15=15 1/8"; E/52*30=30 1/4"; F=31 5/8"; F/2=15 13/16"; H=29 5/8"; H/2=14 13/16"; HEIGHT=49 29/32"; J=9"; J+K+L=48 7/8"; K=16 7/8"; L=23"; M=21"; M-(2*(D-L-K-J))=19"; MB_A=124 15/16"; MB_F=7 1/2"; MB_F-3"=4 1/2"; MB_HEIGHT=45 1/4"; MB_HEIGHT/2=22 5/8"; MB_N=14 3/16"; MB_N-(D-J-K-L)=13 3/16"; MB_P=40"; MB_P+.25"=40 1/4"; MB_P+MB_P+.5=80 1/2"; MB_P-4.5"=35 1/2"; MB_Q=40"; N=9 13/32"; N+(H/2)=24 7/32"; NOZZLE_BOTTOM_ID=17 1/16"; NOZZLE_BOTTOM_RAD=8 17/32"; NOZZLE_BOTTOM_RAD-3*2=2 17/32"; NOZZLE_HEIGHT=32"; NOZZLE_HEIGHT/7*2=8"; NOZZLE_SIZE=12"; NOZZLE_TOP_OD=19 1/2"; NOZZLE_TOP_RAD=9 3/4"; NOZZLE_WB/4=5 19/32"; NOZZLE_WB_OD=28"; NOZZLE_WB_RAD=14"; NOZZLE_WB_RAD-2"=12"; P=60"; R=27"; R*1.1=29 11/16"; R+((B/2)+1.5")=43 7/32"; R-((B/2)+1.5")=10 25/32"; RO/2=17 3/4"; RO2/2=98 1/8"; TRANSITION=12 1/16"; TRANSITION/2=6 1/32"; TRIP_Q=200 3/4"; TRIP_Q-4.5"=196 1/4"; Type Comments=Triple Vari-Plume Laboratory Exhaust Centrifugal Airfoil Class 1 Arr 10 With Mixing Box
- Triple_245_CAVP-15L_CLASS_1_With_Mixing_Box: ((M - (2 * (D - L - K - J))) / 2) + (TRANSITION / 2)=17 1/16"; (B/2)+1.5"=16 7/32"; (B/2)-.125"=14 19/32"; (D-J-K-L)*2=2"; (E/2)-((B/2)+1.5")=10"; (E/2)-((MB_P/2)+.125")=6 3/32"; (E/2)-(E/52*15)=11 3/32"; (F-((F-H)/2))/2=13 13/16"; (M - (2 * (D - L - K - J)))/2=9 1/2"; (MB_P/2)+.125"=20 1/8"; (MB_P/2-.125")+((F / 2) - 2")=-33 11/16"; (MB_P/2-.125")-((F / 2) - 2")=-6 1/16"; (MB_Q/2)+.125"=20 1/8"; (NOZZLE_HEIGHT - (NOZZLE_HEIGHT / 8 * 2)) / 2=16 1/8"; (NOZZLE_WB_OD - NOZZLE_TOP_OD) / 4=3 1/4"; -((MB_Q / 2) + 1/8")=-20 1/8"; -(F-((F-H)/2))/2=-13 13/16"; -MB_HEIGHT=-45 1/4"; -MB_P=-40"; -MB_P-.25=-40 1/4"; A=112 1/4"; A/2=56 1/8"; B=29 7/16"; B/2=14 23/32"; B/4=7 3/8"; C=64 3/4"; C/2=32 3/8"; CLASS=1"; D=49 7/8"; D-L-K-J=1"; D-M=28 7/8"; DUAL_Q=120 3/8"; DUAL_Q+.25"=120 5/8"; E=52 7/16"; E-(NOZZLE_RAD/3*2)=19 3/32"; E-N-N-H=2"; E/2=26 7/32"; E/2-H/2=11 13/32"; E/52*15=15 1/8"; E/52*30=30 1/4"; F=31 5/8"; F/2=15 13/16"; H=29 5/8"; H/2=14 13/16"; HEIGHT=49 29/32"; J=9"; J+K+L=48 7/8"; K=16 7/8"; L=23"; M=21"; M-(2*(D-L-K-J))=19"; MB_A=124 15/16"; MB_F=7 1/2"; MB_F-3"=4 1/2"; MB_HEIGHT=45 1/4"; MB_HEIGHT/2=22 5/8"; MB_N=14 3/16"; MB_N-(D-J-K-L)=13 3/16"; MB_P=40"; MB_P+.25"=40 1/4"; MB_P+MB_P+.5=80 1/2"; MB_P-4.5"=35 1/2"; MB_Q=40"; N=9 13/32"; N+(H/2)=24 7/32"; NOZZLE_BOTTOM_ID=21 3/8"; NOZZLE_BOTTOM_RAD=10 11/16"; NOZZLE_BOTTOM_RAD-3*2=4 11/16"; NOZZLE_HEIGHT=43"; NOZZLE_HEIGHT/7*2=10 3/4"; NOZZLE_SIZE=15"; NOZZLE_TOP_OD=23"; NOZZLE_TOP_RAD=11 1/2"; NOZZLE_WB/4=7 3/16"; NOZZLE_WB_OD=36"; NOZZLE_WB_RAD=18"; NOZZLE_WB_RAD-2"=16"; P=60"; R=27"; R*1.1=29 11/16"; R+((B/2)+1.5")=43 7/32"; R-((B/2)+1.5")=10 25/32"; RO/2=17 3/4"; RO2/2=98 1/8"; TRANSITION=15 1/8"; TRANSITION/2=7 9/16"; TRIP_Q=200 3/4"; TRIP_Q-4.5"=196 1/4"; Type Comments=Triple Vari-Plume Laboratory Exhaust Centrifugal Airfoil Class 1 Arr 10 With Mixing Box
- Triple_245_CAVP-15H_CLASS_1_With_Mixing_Box: ((M - (2 * (D - L - K - J))) / 2) + (TRANSITION / 2)=17 1/16"; (B/2)+1.5"=16 7/32"; (B/2)-.125"=14 19/32"; (D-J-K-L)*2=2"; (E/2)-((B/2)+1.5")=10"; (E/2)-((MB_P/2)+.125")=6 3/32"; (E/2)-(E/52*15)=11 3/32"; (F-((F-H)/2))/2=13 13/16"; (M - (2 * (D - L - K - J)))/2=9 1/2"; (MB_P/2)+.125"=20 1/8"; (MB_P/2-.125")+((F / 2) - 2")=-33 11/16"; (MB_P/2-.125")-((F / 2) - 2")=-6 1/16"; (MB_Q/2)+.125"=20 1/8"; (NOZZLE_HEIGHT - (NOZZLE_HEIGHT / 8 * 2)) / 2=16 1/8"; (NOZZLE_WB_OD - NOZZLE_TOP_OD) / 4=3 1/4"; -((MB_Q / 2) + 1/8")=-20 1/8"; -(F-((F-H)/2))/2=-13 13/16"; -MB_HEIGHT=-45 1/4"; -MB_P=-40"; -MB_P-.25=-40 1/4"; A=112 1/4"; A/2=56 1/8"; B=29 7/16"; B/2=14 23/32"; B/4=7 3/8"; C=64 3/4"; C/2=32 3/8"; CLASS=1"; D=49 7/8"; D-L-K-J=1"; D-M=28 7/8"; DUAL_Q=120 3/8"; DUAL_Q+.25"=120 5/8"; E=52 7/16"; E-(NOZZLE_RAD/3*2)=19 3/32"; E-N-N-H=2"; E/2=26 7/32"; E/2-H/2=11 13/32"; E/52*15=15 1/8"; E/52*30=30 1/4"; F=31 5/8"; F/2=15 13/16"; H=29 5/8"; H/2=14 13/16"; HEIGHT=49 29/32"; J=9"; J+K+L=48 7/8"; K=16 7/8"; L=23"; M=21"; M-(2*(D-L-K-J))=19"; MB_A=124 15/16"; MB_F=7 1/2"; MB_F-3"=4 1/2"; MB_HEIGHT=45 1/4"; MB_HEIGHT/2=22 5/8"; MB_N=14 3/16"; MB_N-(D-J-K-L)=13 3/16"; MB_P=40"; MB_P+.25"=40 1/4"; MB_P+MB_P+.5=80 1/2"; MB_P-4.5"=35 1/2"; MB_Q=40"; N=9 13/32"; N+(H/2)=24 7/32"; NOZZLE_BOTTOM_ID=21 3/8"; NOZZLE_BOTTOM_RAD=10 11/16"; NOZZLE_BOTTOM_RAD-3*2=4 11/16"; NOZZLE_HEIGHT=43"; NOZZLE_HEIGHT/7*2=10 3/4"; NOZZLE_SIZE=15"; NOZZLE_TOP_OD=23"; NOZZLE_TOP_RAD=11 1/2"; NOZZLE_WB/4=7 3/16"; NOZZLE_WB_OD=36"; NOZZLE_WB_RAD=18"; NOZZLE_WB_RAD-2"=16"; P=60"; R=27"; R*1.1=29 11/16"; R+((B/2)+1.5")=43 7/32"; R-((B/2)+1.5")=10 25/32"; RO/2=17 3/4"; RO2/2=98 1/8"; TRANSITION=15 1/8"; TRANSITION/2=7 9/16"; TRIP_Q=200 3/4"; TRIP_Q-4.5"=196 1/4"; Type Comments=Triple Vari-Plume Laboratory Exhaust Centrifugal Airfoil Class 1 Arr 10 With Mixing Box
- Triple_245_CAVP-18L_CLASS_1_With_Mixing_Box: ((M - (2 * (D - L - K - J))) / 2) + (TRANSITION / 2)=18 9/16"; (B/2)+1.5"=16 7/32"; (B/2)-.125"=14 19/32"; (D-J-K-L)*2=2"; (E/2)-((B/2)+1.5")=10"; (E/2)-((MB_P/2)+.125")=6 3/32"; (E/2)-(E/52*15)=11 3/32"; (F-((F-H)/2))/2=13 13/16"; (M - (2 * (D - L - K - J)))/2=9 1/2"; (MB_P/2)+.125"=20 1/8"; (MB_P/2-.125")+((F / 2) - 2")=-33 11/16"; (MB_P/2-.125")-((F / 2) - 2")=-6 1/16"; (MB_Q/2)+.125"=20 1/8"; (NOZZLE_HEIGHT - (NOZZLE_HEIGHT / 8 * 2)) / 2=18"; (NOZZLE_WB_OD - NOZZLE_TOP_OD) / 4=3 7/8"; -((MB_Q / 2) + 1/8")=-20 1/8"; -(F-((F-H)/2))/2=-13 13/16"; -MB_HEIGHT=-45 1/4"; -MB_P=-40"; -MB_P-.25=-40 1/4"; A=112 1/4"; A/2=56 1/8"; B=29 7/16"; B/2=14 23/32"; B/4=7 3/8"; C=64 3/4"; C/2=32 3/8"; CLASS=1"; D=49 7/8"; D-L-K-J=1"; D-M=28 7/8"; DUAL_Q=120 3/8"; DUAL_Q+.25"=120 5/8"; E=52 7/16"; E-(NOZZLE_RAD/3*2)=17 11/16"; E-N-N-H=2"; E/2=26 7/32"; E/2-H/2=11 13/32"; E/52*15=15 1/8"; E/52*30=30 1/4"; F=31 5/8"; F/2=15 13/16"; H=29 5/8"; H/2=14 13/16"; HEIGHT=49 29/32"; J=9"; J+K+L=48 7/8"; K=16 7/8"; L=23"; M=21"; M-(2*(D-L-K-J))=19"; MB_A=124 15/16"; MB_F=7 1/2"; MB_F-3"=4 1/2"; MB_HEIGHT=45 1/4"; MB_HEIGHT/2=22 5/8"; MB_N=14 3/16"; MB_N-(D-J-K-L)=13 3/16"; MB_P=40"; MB_P+.25"=40 1/4"; MB_P+MB_P+.5=80 1/2"; MB_P-4.5"=35 1/2"; MB_Q=40"; N=9 13/32"; N+(H/2)=24 7/32"; NOZZLE_BOTTOM_ID=25 5/8"; NOZZLE_BOTTOM_RAD=12 13/16"; NOZZLE_BOTTOM_RAD-3*2=6 13/16"; NOZZLE_HEIGHT=48"; NOZZLE_HEIGHT/7*2=12"; NOZZLE_SIZE=18"; NOZZLE_TOP_OD=27 1/2"; NOZZLE_TOP_RAD=13 3/4"; NOZZLE_WB/4=8 19/32"; NOZZLE_WB_OD=43"; NOZZLE_WB_RAD=21 1/2"; NOZZLE_WB_RAD-2"=19 1/2"; P=60"; R=27"; R*1.1=29 11/16"; R+((B/2)+1.5")=43 7/32"; R-((B/2)+1.5")=10 25/32"; RO/2=17 3/4"; RO2/2=98 1/8"; TRANSITION=18 1/8"; TRANSITION/2=9 1/16"; TRIP_Q=200 3/4"; TRIP_Q-4.5"=196 1/4"; Type Comments=Triple Vari-Plume Laboratory Exhaust Centrifugal Airfoil Class 1 Arr 10 With Mixing Box
- Triple_245_CAVP-18H_CLASS_1_With_Mixing_Box: ((M - (2 * (D - L - K - J))) / 2) + (TRANSITION / 2)=18 9/16"; (B/2)+1.5"=16 7/32"; (B/2)-.125"=14 19/32"; (D-J-K-L)*2=2"; (E/2)-((B/2)+1.5")=10"; (E/2)-((MB_P/2)+.125")=6 3/32"; (E/2)-(E/52*15)=11 3/32"; (F-((F-H)/2))/2=13 13/16"; (M - (2 * (D - L - K - J)))/2=9 1/2"; (MB_P/2)+.125"=20 1/8"; (MB_P/2-.125")+((F / 2) - 2")=-33 11/16"; (MB_P/2-.125")-((F / 2) - 2")=-6 1/16"; (MB_Q/2)+.125"=20 1/8"; (NOZZLE_HEIGHT - (NOZZLE_HEIGHT / 8 * 2)) / 2=18"; (NOZZLE_WB_OD - NOZZLE_TOP_OD) / 4=3 7/8"; -((MB_Q / 2) + 1/8")=-20 1/8"; -(F-((F-H)/2))/2=-13 13/16"; -MB_HEIGHT=-45 1/4"; -MB_P=-40"; -MB_P-.25=-40 1/4"; A=112 1/4"; A/2=56 1/8"; B=29 7/16"; B/2=14 23/32"; B/4=7 3/8"; C=64 3/4"; C/2=32 3/8"; CLASS=1"; D=49 7/8"; D-L-K-J=1"; D-M=28 7/8"; DUAL_Q=120 3/8"; DUAL_Q+.25"=120 5/8"; E=52 7/16"; E-(NOZZLE_RAD/3*2)=17 11/16"; E-N-N-H=2"; E/2=26 7/32"; E/2-H/2=11 13/32"; E/52*15=15 1/8"; E/52*30=30 1/4"; F=31 5/8"; F/2=15 13/16"; H=29 5/8"; H/2=14 13/16"; HEIGHT=49 29/32"; J=9"; J+K+L=48 7/8"; K=16 7/8"; L=23"; M=21"; M-(2*(D-L-K-J))=19"; MB_A=124 15/16"; MB_F=7 1/2"; MB_F-3"=4 1/2"; MB_HEIGHT=45 1/4"; MB_HEIGHT/2=22 5/8"; MB_N=14 3/16"; MB_N-(D-J-K-L)=13 3/16"; MB_P=40"; MB_P+.25"=40 1/4"; MB_P+MB_P+.5=80 1/2"; MB_P-4.5"=35 1/2"; MB_Q=40"; N=9 13/32"; N+(H/2)=24 7/32"; NOZZLE_BOTTOM_ID=25 5/8"; NOZZLE_BOTTOM_RAD=12 13/16"; NOZZLE_BOTTOM_RAD-3*2=6 13/16"; NOZZLE_HEIGHT=48"; NOZZLE_HEIGHT/7*2=12"; NOZZLE_SIZE=18"; NOZZLE_TOP_OD=27 1/2"; NOZZLE_TOP_RAD=13 3/4"; NOZZLE_WB/4=8 19/32"; NOZZLE_WB_OD=43"; NOZZLE_WB_RAD=21 1/2"; NOZZLE_WB_RAD-2"=19 1/2"; P=60"; R=27"; R*1.1=29 11/16"; R+((B/2)+1.5")=43 7/32"; R-((B/2)+1.5")=10 25/32"; RO/2=17 3/4"; RO2/2=98 1/8"; TRANSITION=18 1/8"; TRANSITION/2=9 1/16"; TRIP_Q=200 3/4"; TRIP_Q-4.5"=196 1/4"; Type Comments=Triple Vari-Plume Laboratory Exhaust Centrifugal Airfoil Class 1 Arr 10 With Mixing Box
- Triple_245_CAVP-12L_CLASS_2_With_Mixing_Box: ((M - (2 * (D - L - K - J))) / 2) + (TRANSITION / 2)=15 17/32"; (B/2)+1.5"=16 7/32"; (B/2)-.125"=14 19/32"; (D-J-K-L)*2=2"; (E/2)-((B/2)+1.5")=10"; (E/2)-((MB_P/2)+.125")=6 3/32"; (E/2)-(E/52*15)=11 3/32"; (F-((F-H)/2))/2=13 13/16"; (M - (2 * (D - L - K - J)))/2=9 1/2"; (MB_P/2)+.125"=20 1/8"; (MB_P/2-.125")+((F / 2) - 2")=-33 11/16"; (MB_P/2-.125")-((F / 2) - 2")=-6 1/16"; (MB_Q/2)+.125"=20 1/8"; (NOZZLE_HEIGHT - (NOZZLE_HEIGHT / 8 * 2)) / 2=12"; (NOZZLE_WB_OD - NOZZLE_TOP_OD) / 4=2 1/8"; -((MB_Q / 2) + 1/8")=-20 1/8"; -(F-((F-H)/2))/2=-13 13/16"; -MB_HEIGHT=-45 1/4"; -MB_P=-40"; -MB_P-.25=-40 1/4"; A=112 1/4"; A/2=56 1/8"; B=29 7/16"; B/2=14 23/32"; B/4=7 3/8"; C=64 3/4"; C/2=32 3/8"; CLASS=2"; D=54 1/8"; D-L-K-J=1"; D-M=33 1/8"; DUAL_Q=120 3/8"; DUAL_Q+.25"=120 5/8"; E=52 7/16"; E-(NOZZLE_RAD/3*2)=20 17/32"; E-N-N-H=2"; E/2=26 7/32"; E/2-H/2=11 13/32"; E/52*15=15 1/8"; E/52*30=30 1/4"; F=31 5/8"; F/2=15 13/16"; H=29 5/8"; H/2=14 13/16"; HEIGHT=49 29/32"; J=9"; J+K+L=53 1/8"; K=21 1/8"; L=23"; M=21"; M-(2*(D-L-K-J))=19"; MB_A=129 3/16"; MB_F=7 1/2"; MB_F-3"=4 1/2"; MB_HEIGHT=45 1/4"; MB_HEIGHT/2=22 5/8"; MB_N=14 3/16"; MB_N-(D-J-K-L)=13 3/16"; MB_P=40"; MB_P+.25"=40 1/4"; MB_P+MB_P+.5=80 1/2"; MB_P-4.5"=35 1/2"; MB_Q=40"; N=9 13/32"; N+(H/2)=24 7/32"; NOZZLE_BOTTOM_ID=17 1/16"; NOZZLE_BOTTOM_RAD=8 17/32"; NOZZLE_BOTTOM_RAD-3*2=2 17/32"; NOZZLE_HEIGHT=32"; NOZZLE_HEIGHT/7*2=8"; NOZZLE_SIZE=12"; NOZZLE_TOP_OD=19 1/2"; NOZZLE_TOP_RAD=9 3/4"; NOZZLE_WB/4=5 19/32"; NOZZLE_WB_OD=28"; NOZZLE_WB_RAD=14"; NOZZLE_WB_RAD-2"=12"; P=60"; R=27"; R*1.1=29 11/16"; R+((B/2)+1.5")=43 7/32"; R-((B/2)+1.5")=10 25/32"; RO/2=17 3/4"; RO2/2=98 1/8"; TRANSITION=12 1/16"; TRANSITION/2=6 1/32"; TRIP_Q=200 3/4"; TRIP_Q-4.5"=196 1/4"; Type Comments=Triple Vari-Plume Laboratory Exhaust Centrifugal Airfoil Class 2 Arr 10 With Mixing Box
- Triple_245_CAVP-12H_CLASS_2_With_Mixing_Box: ((M - (2 * (D - L - K - J))) / 2) + (TRANSITION / 2)=15 17/32"; (B/2)+1.5"=16 7/32"; (B/2)-.125"=14 19/32"; (D-J-K-L)*2=2"; (E/2)-((B/2)+1.5")=10"; (E/2)-((MB_P/2)+.125")=6 3/32"; (E/2)-(E/52*15)=11 3/32"; (F-((F-H)/2))/2=13 13/16"; (M - (2 * (D - L - K - J)))/2=9 1/2"; (MB_P/2)+.125"=20 1/8"; (MB_P/2-.125")+((F / 2) - 2")=-33 11/16"; (MB_P/2-.125")-((F / 2) - 2")=-6 1/16"; (MB_Q/2)+.125"=20 1/8"; (NOZZLE_HEIGHT - (NOZZLE_HEIGHT / 8 * 2)) / 2=12"; (NOZZLE_WB_OD - NOZZLE_TOP_OD) / 4=2 1/8"; -((MB_Q / 2) + 1/8")=-20 1/8"; -(F-((F-H)/2))/2=-13 13/16"; -MB_HEIGHT=-45 1/4"; -MB_P=-40"; -MB_P-.25=-40 1/4"; A=112 1/4"; A/2=56 1/8"; B=29 7/16"; B/2=14 23/32"; B/4=7 3/8"; C=64 3/4"; C/2=32 3/8"; CLASS=2"; D=54 1/8"; D-L-K-J=1"; D-M=33 1/8"; DUAL_Q=120 3/8"; DUAL_Q+.25"=120 5/8"; E=52 7/16"; E-(NOZZLE_RAD/3*2)=20 17/32"; E-N-N-H=2"; E/2=26 7/32"; E/2-H/2=11 13/32"; E/52*15=15 1/8"; E/52*30=30 1/4"; F=31 5/8"; F/2=15 13/16"; H=29 5/8"; H/2=14 13/16"; HEIGHT=49 29/32"; J=9"; J+K+L=53 1/8"; K=21 1/8"; L=23"; M=21"; M-(2*(D-L-K-J))=19"; MB_A=129 3/16"; MB_F=7 1/2"; MB_F-3"=4 1/2"; MB_HEIGHT=45 1/4"; MB_HEIGHT/2=22 5/8"; MB_N=14 3/16"; MB_N-(D-J-K-L)=13 3/16"; MB_P=40"; MB_P+.25"=40 1/4"; MB_P+MB_P+.5=80 1/2"; MB_P-4.5"=35 1/2"; MB_Q=40"; N=9 13/32"; N+(H/2)=24 7/32"; NOZZLE_BOTTOM_ID=17 1/16"; NOZZLE_BOTTOM_RAD=8 17/32"; NOZZLE_BOTTOM_RAD-3*2=2 17/32"; NOZZLE_HEIGHT=32"; NOZZLE_HEIGHT/7*2=8"; NOZZLE_SIZE=12"; NOZZLE_TOP_OD=19 1/2"; NOZZLE_TOP_RAD=9 3/4"; NOZZLE_WB/4=5 19/32"; NOZZLE_WB_OD=28"; NOZZLE_WB_RAD=14"; NOZZLE_WB_RAD-2"=12"; P=60"; R=27"; R*1.1=29 11/16"; R+((B/2)+1.5")=43 7/32"; R-((B/2)+1.5")=10 25/32"; RO/2=17 3/4"; RO2/2=98 1/8"; TRANSITION=12 1/16"; TRANSITION/2=6 1/32"; TRIP_Q=200 3/4"; TRIP_Q-4.5"=196 1/4"; Type Comments=Triple Vari-Plume Laboratory Exhaust Centrifugal Airfoil Class 2 Arr 10 With Mixing Box
- Triple_245_CAVP-15L_CLASS_2_With_Mixing_Box: ((M - (2 * (D - L - K - J))) / 2) + (TRANSITION / 2)=17 1/16"; (B/2)+1.5"=16 7/32"; (B/2)-.125"=14 19/32"; (D-J-K-L)*2=2"; (E/2)-((B/2)+1.5")=10"; (E/2)-((MB_P/2)+.125")=6 3/32"; (E/2)-(E/52*15)=11 3/32"; (F-((F-H)/2))/2=13 13/16"; (M - (2 * (D - L - K - J)))/2=9 1/2"; (MB_P/2)+.125"=20 1/8"; (MB_P/2-.125")+((F / 2) - 2")=-33 11/16"; (MB_P/2-.125")-((F / 2) - 2")=-6 1/16"; (MB_Q/2)+.125"=20 1/8"; (NOZZLE_HEIGHT - (NOZZLE_HEIGHT / 8 * 2)) / 2=16 1/8"; (NOZZLE_WB_OD - NOZZLE_TOP_OD) / 4=3 1/4"; -((MB_Q / 2) + 1/8")=-20 1/8"; -(F-((F-H)/2))/2=-13 13/16"; -MB_HEIGHT=-45 1/4"; -MB_P=-40"; -MB_P-.25=-40 1/4"; A=112 1/4"; A/2=56 1/8"; B=29 7/16"; B/2=14 23/32"; B/4=7 3/8"; C=64 3/4"; C/2=32 3/8"; CLASS=2"; D=54 1/8"; D-L-K-J=1"; D-M=33 1/8"; DUAL_Q=120 3/8"; DUAL_Q+.25"=120 5/8"; E=52 7/16"; E-(NOZZLE_RAD/3*2)=19 3/32"; E-N-N-H=2"; E/2=26 7/32"; E/2-H/2=11 13/32"; E/52*15=15 1/8"; E/52*30=30 1/4"; F=31 5/8"; F/2=15 13/16"; H=29 5/8"; H/2=14 13/16"; HEIGHT=49 29/32"; J=9"; J+K+L=53 1/8"; K=21 1/8"; L=23"; M=21"; M-(2*(D-L-K-J))=19"; MB_A=129 3/16"; MB_F=7 1/2"; MB_F-3"=4 1/2"; MB_HEIGHT=45 1/4"; MB_HEIGHT/2=22 5/8"; MB_N=14 3/16"; MB_N-(D-J-K-L)=13 3/16"; MB_P=40"; MB_P+.25"=40 1/4"; MB_P+MB_P+.5=80 1/2"; MB_P-4.5"=35 1/2"; MB_Q=40"; N=9 13/32"; N+(H/2)=24 7/32"; NOZZLE_BOTTOM_ID=21 3/8"; NOZZLE_BOTTOM_RAD=10 11/16"; NOZZLE_BOTTOM_RAD-3*2=4 11/16"; NOZZLE_HEIGHT=43"; NOZZLE_HEIGHT/7*2=10 3/4"; NOZZLE_SIZE=15"; NOZZLE_TOP_OD=23"; NOZZLE_TOP_RAD=11 1/2"; NOZZLE_WB/4=7 3/16"; NOZZLE_WB_OD=36"; NOZZLE_WB_RAD=18"; NOZZLE_WB_RAD-2"=16"; P=60"; R=27"; R*1.1=29 11/16"; R+((B/2)+1.5")=43 7/32"; R-((B/2)+1.5")=10 25/32"; RO/2=17 3/4"; RO2/2=98 1/8"; TRANSITION=15 1/8"; TRANSITION/2=7 9/16"; TRIP_Q=200 3/4"; TRIP_Q-4.5"=196 1/4"; Type Comments=Triple Vari-Plume Laboratory Exhaust Centrifugal Airfoil Class 2 Arr 10 With Mixing Box
- Triple_245_CAVP-15H_CLASS_2_With_Mixing_Box: ((M - (2 * (D - L - K - J))) / 2) + (TRANSITION / 2)=17 1/16"; (B/2)+1.5"=16 7/32"; (B/2)-.125"=14 19/32"; (D-J-K-L)*2=2"; (E/2)-((B/2)+1.5")=10"; (E/2)-((MB_P/2)+.125")=6 3/32"; (E/2)-(E/52*15)=11 3/32"; (F-((F-H)/2))/2=13 13/16"; (M - (2 * (D - L - K - J)))/2=9 1/2"; (MB_P/2)+.125"=20 1/8"; (MB_P/2-.125")+((F / 2) - 2")=-33 11/16"; (MB_P/2-.125")-((F / 2) - 2")=-6 1/16"; (MB_Q/2)+.125"=20 1/8"; (NOZZLE_HEIGHT - (NOZZLE_HEIGHT / 8 * 2)) / 2=16 1/8"; (NOZZLE_WB_OD - NOZZLE_TOP_OD) / 4=3 1/4"; -((MB_Q / 2) + 1/8")=-20 1/8"; -(F-((F-H)/2))/2=-13 13/16"; -MB_HEIGHT=-45 1/4"; -MB_P=-40"; -MB_P-.25=-40 1/4"; A=112 1/4"; A/2=56 1/8"; B=29 7/16"; B/2=14 23/32"; B/4=7 3/8"; C=64 3/4"; C/2=32 3/8"; CLASS=2"; D=54 1/8"; D-L-K-J=1"; D-M=33 1/8"; DUAL_Q=120 3/8"; DUAL_Q+.25"=120 5/8"; E=52 7/16"; E-(NOZZLE_RAD/3*2)=19 3/32"; E-N-N-H=2"; E/2=26 7/32"; E/2-H/2=11 13/32"; E/52*15=15 1/8"; E/52*30=30 1/4"; F=31 5/8"; F/2=15 13/16"; H=29 5/8"; H/2=14 13/16"; HEIGHT=49 29/32"; J=9"; J+K+L=53 1/8"; K=21 1/8"; L=23"; M=21"; M-(2*(D-L-K-J))=19"; MB_A=129 3/16"; MB_F=7 1/2"; MB_F-3"=4 1/2"; MB_HEIGHT=45 1/4"; MB_HEIGHT/2=22 5/8"; MB_N=14 3/16"; MB_N-(D-J-K-L)=13 3/16"; MB_P=40"; MB_P+.25"=40 1/4"; MB_P+MB_P+.5=80 1/2"; MB_P-4.5"=35 1/2"; MB_Q=40"; N=9 13/32"; N+(H/2)=24 7/32"; NOZZLE_BOTTOM_ID=21 3/8"; NOZZLE_BOTTOM_RAD=10 11/16"; NOZZLE_BOTTOM_RAD-3*2=4 11/16"; NOZZLE_HEIGHT=43"; NOZZLE_HEIGHT/7*2=10 3/4"; NOZZLE_SIZE=15"; NOZZLE_TOP_OD=23"; NOZZLE_TOP_RAD=11 1/2"; NOZZLE_WB/4=7 3/16"; NOZZLE_WB_OD=36"; NOZZLE_WB_RAD=18"; NOZZLE_WB_RAD-2"=16"; P=60"; R=27"; R*1.1=29 11/16"; R+((B/2)+1.5")=43 7/32"; R-((B/2)+1.5")=10 25/32"; RO/2=17 3/4"; RO2/2=98 1/8"; TRANSITION=15 1/8"; TRANSITION/2=7 9/16"; TRIP_Q=200 3/4"; TRIP_Q-4.5"=196 1/4"; Type Comments=Triple Vari-Plume Laboratory Exhaust Centrifugal Airfoil Class 2 Arr 10 With Mixing Box
- Triple_245_CAVP-18L_CLASS_2_With_Mixing_Box: ((M - (2 * (D - L - K - J))) / 2) + (TRANSITION / 2)=18 9/16"; (B/2)+1.5"=16 7/32"; (B/2)-.125"=14 19/32"; (D-J-K-L)*2=2"; (E/2)-((B/2)+1.5")=10"; (E/2)-((MB_P/2)+.125")=6 3/32"; (E/2)-(E/52*15)=11 3/32"; (F-((F-H)/2))/2=13 13/16"; (M - (2 * (D - L - K - J)))/2=9 1/2"; (MB_P/2)+.125"=20 1/8"; (MB_P/2-.125")+((F / 2) - 2")=-33 11/16"; (MB_P/2-.125")-((F / 2) - 2")=-6 1/16"; (MB_Q/2)+.125"=20 1/8"; (NOZZLE_HEIGHT - (NOZZLE_HEIGHT / 8 * 2)) / 2=18"; (NOZZLE_WB_OD - NOZZLE_TOP_OD) / 4=3 7/8"; -((MB_Q / 2) + 1/8")=-20 1/8"; -(F-((F-H)/2))/2=-13 13/16"; -MB_HEIGHT=-45 1/4"; -MB_P=-40"; -MB_P-.25=-40 1/4"; A=112 1/4"; A/2=56 1/8"; B=29 7/16"; B/2=14 23/32"; B/4=7 3/8"; C=64 3/4"; C/2=32 3/8"; CLASS=2"; D=54 1/8"; D-L-K-J=1"; D-M=33 1/8"; DUAL_Q=120 3/8"; DUAL_Q+.25"=120 5/8"; E=52 7/16"; E-(NOZZLE_RAD/3*2)=17 11/16"; E-N-N-H=2"; E/2=26 7/32"; E/2-H/2=11 13/32"; E/52*15=15 1/8"; E/52*30=30 1/4"; F=31 5/8"; F/2=15 13/16"; H=29 5/8"; H/2=14 13/16"; HEIGHT=49 29/32"; J=9"; J+K+L=53 1/8"; K=21 1/8"; L=23"; M=21"; M-(2*(D-L-K-J))=19"; MB_A=129 3/16"; MB_F=7 1/2"; MB_F-3"=4 1/2"; MB_HEIGHT=45 1/4"; MB_HEIGHT/2=22 5/8"; MB_N=14 3/16"; MB_N-(D-J-K-L)=13 3/16"; MB_P=40"; MB_P+.25"=40 1/4"; MB_P+MB_P+.5=80 1/2"; MB_P-4.5"=35 1/2"; MB_Q=40"; N=9 13/32"; N+(H/2)=24 7/32"; NOZZLE_BOTTOM_ID=25 5/8"; NOZZLE_BOTTOM_RAD=12 13/16"; NOZZLE_BOTTOM_RAD-3*2=6 13/16"; NOZZLE_HEIGHT=48"; NOZZLE_HEIGHT/7*2=12"; NOZZLE_SIZE=18"; NOZZLE_TOP_OD=27 1/2"; NOZZLE_TOP_RAD=13 3/4"; NOZZLE_WB/4=8 19/32"; NOZZLE_WB_OD=43"; NOZZLE_WB_RAD=21 1/2"; NOZZLE_WB_RAD-2"=19 1/2"; P=60"; R=27"; R*1.1=29 11/16"; R+((B/2)+1.5")=43 7/32"; R-((B/2)+1.5")=10 25/32"; RO/2=17 3/4"; RO2/2=98 1/8"; TRANSITION=18 1/8"; TRANSITION/2=9 1/16"; TRIP_Q=200 3/4"; TRIP_Q-4.5"=196 1/4"; Type Comments=Triple Vari-Plume Laboratory Exhaust Centrifugal Airfoil Class 2 Arr 10 With Mixing Box
- Triple_245_CAVP-18H_CLASS_2_With_Mixing_Box: ((M - (2 * (D - L - K - J))) / 2) + (TRANSITION / 2)=18 9/16"; (B/2)+1.5"=16 7/32"; (B/2)-.125"=14 19/32"; (D-J-K-L)*2=2"; (E/2)-((B/2)+1.5")=10"; (E/2)-((MB_P/2)+.125")=6 3/32"; (E/2)-(E/52*15)=11 3/32"; (F-((F-H)/2))/2=13 13/16"; (M - (2 * (D - L - K - J)))/2=9 1/2"; (MB_P/2)+.125"=20 1/8"; (MB_P/2-.125")+((F / 2) - 2")=-33 11/16"; (MB_P/2-.125")-((F / 2) - 2")=-6 1/16"; (MB_Q/2)+.125"=20 1/8"; (NOZZLE_HEIGHT - (NOZZLE_HEIGHT / 8 * 2)) / 2=18"; (NOZZLE_WB_OD - NOZZLE_TOP_OD) / 4=3 7/8"; -((MB_Q / 2) + 1/8")=-20 1/8"; -(F-((F-H)/2))/2=-13 13/16"; -MB_HEIGHT=-45 1/4"; -MB_P=-40"; -MB_P-.25=-40 1/4"; A=112 1/4"; A/2=56 1/8"; B=29 7/16"; B/2=14 23/32"; B/4=7 3/8"; C=64 3/4"; C/2=32 3/8"; CLASS=2"; D=54 1/8"; D-L-K-J=1"; D-M=33 1/8"; DUAL_Q=120 3/8"; DUAL_Q+.25"=120 5/8"; E=52 7/16"; E-(NOZZLE_RAD/3*2)=17 11/16"; E-N-N-H=2"; E/2=26 7/32"; E/2-H/2=11 13/32"; E/52*15=15 1/8"; E/52*30=30 1/4"; F=31 5/8"; F/2=15 13/16"; H=29 5/8"; H/2=14 13/16"; HEIGHT=49 29/32"; J=9"; J+K+L=53 1/8"; K=21 1/8"; L=23"; M=21"; M-(2*(D-L-K-J))=19"; MB_A=129 3/16"; MB_F=7 1/2"; MB_F-3"=4 1/2"; MB_HEIGHT=45 1/4"; MB_HEIGHT/2=22 5/8"; MB_N=14 3/16"; MB_N-(D-J-K-L)=13 3/16"; MB_P=40"; MB_P+.25"=40 1/4"; MB_P+MB_P+.5=80 1/2"; MB_P-4.5"=35 1/2"; MB_Q=40"; N=9 13/32"; N+(H/2)=24 7/32"; NOZZLE_BOTTOM_ID=25 5/8"; NOZZLE_BOTTOM_RAD=12 13/16"; NOZZLE_BOTTOM_RAD-3*2=6 13/16"; NOZZLE_HEIGHT=48"; NOZZLE_HEIGHT/7*2=12"; NOZZLE_SIZE=18"; NOZZLE_TOP_OD=27 1/2"; NOZZLE_TOP_RAD=13 3/4"; NOZZLE_WB/4=8 19/32"; NOZZLE_WB_OD=43"; NOZZLE_WB_RAD=21 1/2"; NOZZLE_WB_RAD-2"=19 1/2"; P=60"; R=27"; R*1.1=29 11/16"; R+((B/2)+1.5")=43 7/32"; R-((B/2)+1.5")=10 25/32"; RO/2=17 3/4"; RO2/2=98 1/8"; TRANSITION=18 1/8"; TRANSITION/2=9 1/16"; TRIP_Q=200 3/4"; TRIP_Q-4.5"=196 1/4"; Type Comments=Triple Vari-Plume Laboratory Exhaust Centrifugal Airfoil Class 2 Arr 10 With Mixing Box
- Triple_270_CAVP-12L_CLASS_1_With_Mixing_Box: ((M - (2 * (D - L - K - J))) / 2) + (TRANSITION / 2)=16 15/32"; (B/2)+1.5"=17 15/32"; (B/2)-.125"=15 27/32"; (D-J-K-L)*2=2"; (E/2)-((B/2)+1.5")=11 5/16"; (E/2)-((MB_P/2)+.125")=7 5/32"; (E/2)-(E/52*15)=12 3/16"; (F-((F-H)/2))/2=15 3/16"; (M - (2 * (D - L - K - J)))/2=10 7/16"; (MB_P/2)+.125"=21 5/8"; (MB_P/2-.125")+((F / 2) - 2")=-36 9/16"; (MB_P/2-.125")-((F / 2) - 2")=-6 3/16"; (MB_Q/2)+.125"=21 5/8"; (NOZZLE_HEIGHT - (NOZZLE_HEIGHT / 8 * 2)) / 2=12"; (NOZZLE_WB_OD - NOZZLE_TOP_OD) / 4=2 1/8"; -((MB_Q / 2) + 1/8")=-21 5/8"; -(F-((F-H)/2))/2=-15 3/16"; -MB_HEIGHT=-47 3/4"; -MB_P=-43"; -MB_P-.25=-43 1/4"; A=116 7/16"; A/2=58 7/32"; B=31 15/16"; B/2=15 31/32"; B/4=8"; C=68 15/16"; C/2=34 15/32"; CLASS=1"; D=54 1/2"; D-L-K-J=1"; D-M=31 5/8"; DUAL_Q=129 3/8"; DUAL_Q+.25"=129 5/8"; E=57 9/16"; E-(NOZZLE_RAD/3*2)=23 3/32"; E-N-N-H=2"; E/2=28 25/32"; E/2-H/2=12 19/32"; E/52*15=16 19/32"; E/52*30=33 7/32"; F=34 3/8"; F/2=17 3/16"; H=32 3/8"; H/2=16 3/16"; HEIGHT=52 1/8"; J=9 1/2"; J+K+L=53 1/2"; K=19 1/8"; L=24 7/8"; M=22 7/8"; M-(2*(D-L-K-J))=20 7/8"; MB_A=132 7/16"; MB_F=6 1/4"; MB_F-3"=3 1/4"; MB_HEIGHT=47 3/4"; MB_HEIGHT/2=23 7/8"; MB_N=14 3/16"; MB_N-(D-J-K-L)=13 3/16"; MB_P=43"; MB_P+.25"=43 1/4"; MB_P+MB_P+.5=86 1/2"; MB_P-4.5"=38 1/2"; MB_Q=43"; N=10 19/32"; N+(H/2)=26 25/32"; NOZZLE_BOTTOM_ID=17 1/16"; NOZZLE_BOTTOM_RAD=8 17/32"; NOZZLE_BOTTOM_RAD-3*2=2 17/32"; NOZZLE_HEIGHT=32"; NOZZLE_HEIGHT/7*2=8"; NOZZLE_SIZE=12"; NOZZLE_TOP_OD=19 1/2"; NOZZLE_TOP_RAD=9 3/4"; NOZZLE_WB/4=5 19/32"; NOZZLE_WB_OD=28"; NOZZLE_WB_RAD=14"; NOZZLE_WB_RAD-2"=12"; P=60"; R=27"; R*1.1=29 11/16"; R+((B/2)+1.5")=44 15/32"; R-((B/2)+1.5")=9 17/32"; RO/2=19 1/4"; RO2/2=105 5/8"; TRANSITION=12 1/16"; TRANSITION/2=6 1/32"; TRIP_Q=215 3/4"; TRIP_Q-4.5"=211 1/4"; Type Comments=Triple Vari-Plume Laboratory Exhaust Centrifugal Airfoil Class 1 Arr 10 With Mixing Box
- Triple_270_CAVP-12H_CLASS_1_With_Mixing_Box: ((M - (2 * (D - L - K - J))) / 2) + (TRANSITION / 2)=16 15/32"; (B/2)+1.5"=17 15/32"; (B/2)-.125"=15 27/32"; (D-J-K-L)*2=2"; (E/2)-((B/2)+1.5")=11 5/16"; (E/2)-((MB_P/2)+.125")=7 5/32"; (E/2)-(E/52*15)=12 3/16"; (F-((F-H)/2))/2=15 3/16"; (M - (2 * (D - L - K - J)))/2=10 7/16"; (MB_P/2)+.125"=21 5/8"; (MB_P/2-.125")+((F / 2) - 2")=-36 9/16"; (MB_P/2-.125")-((F / 2) - 2")=-6 3/16"; (MB_Q/2)+.125"=21 5/8"; (NOZZLE_HEIGHT - (NOZZLE_HEIGHT / 8 * 2)) / 2=12"; (NOZZLE_WB_OD - NOZZLE_TOP_OD) / 4=2 1/8"; -((MB_Q / 2) + 1/8")=-21 5/8"; -(F-((F-H)/2))/2=-15 3/16"; -MB_HEIGHT=-47 3/4"; -MB_P=-43"; -MB_P-.25=-43 1/4"; A=116 7/16"; A/2=58 7/32"; B=31 15/16"; B/2=15 31/32"; B/4=8"; C=68 15/16"; C/2=34 15/32"; CLASS=1"; D=54 1/2"; D-L-K-J=1"; D-M=31 5/8"; DUAL_Q=129 3/8"; DUAL_Q+.25"=129 5/8"; E=57 9/16"; E-(NOZZLE_RAD/3*2)=23 3/32"; E-N-N-H=2"; E/2=28 25/32"; E/2-H/2=12 19/32"; E/52*15=16 19/32"; E/52*30=33 7/32"; F=34 3/8"; F/2=17 3/16"; H=32 3/8"; H/2=16 3/16"; HEIGHT=52 1/8"; J=9 1/2"; J+K+L=53 1/2"; K=19 1/8"; L=24 7/8"; M=22 7/8"; M-(2*(D-L-K-J))=20 7/8"; MB_A=132 7/16"; MB_F=6 1/4"; MB_F-3"=3 1/4"; MB_HEIGHT=47 3/4"; MB_HEIGHT/2=23 7/8"; MB_N=14 3/16"; MB_N-(D-J-K-L)=13 3/16"; MB_P=43"; MB_P+.25"=43 1/4"; MB_P+MB_P+.5=86 1/2"; MB_P-4.5"=38 1/2"; MB_Q=43"; N=10 19/32"; N+(H/2)=26 25/32"; NOZZLE_BOTTOM_ID=17 1/16"; NOZZLE_BOTTOM_RAD=8 17/32"; NOZZLE_BOTTOM_RAD-3*2=2 17/32"; NOZZLE_HEIGHT=32"; NOZZLE_HEIGHT/7*2=8"; NOZZLE_SIZE=12"; NOZZLE_TOP_OD=19 1/2"; NOZZLE_TOP_RAD=9 3/4"; NOZZLE_WB/4=5 19/32"; NOZZLE_WB_OD=28"; NOZZLE_WB_RAD=14"; NOZZLE_WB_RAD-2"=12"; P=60"; R=27"; R*1.1=29 11/16"; R+((B/2)+1.5")=44 15/32"; R-((B/2)+1.5")=9 17/32"; RO/2=19 1/4"; RO2/2=105 5/8"; TRANSITION=12 1/16"; TRANSITION/2=6 1/32"; TRIP_Q=215 3/4"; TRIP_Q-4.5"=211 1/4"; Type Comments=Triple Vari-Plume Laboratory Exhaust Centrifugal Airfoil Class 1 Arr 10 With Mixing Box
- Triple_270_CAVP-15L_CLASS_1_With_Mixing_Box: ((M - (2 * (D - L - K - J))) / 2) + (TRANSITION / 2)=18"; (B/2)+1.5"=17 15/32"; (B/2)-.125"=15 27/32"; (D-J-K-L)*2=2"; (E/2)-((B/2)+1.5")=11 5/16"; (E/2)-((MB_P/2)+.125")=7 5/32"; (E/2)-(E/52*15)=12 3/16"; (F-((F-H)/2))/2=15 3/16"; (M - (2 * (D - L - K - J)))/2=10 7/16"; (MB_P/2)+.125"=21 5/8"; (MB_P/2-.125")+((F / 2) - 2")=-36 9/16"; (MB_P/2-.125")-((F / 2) - 2")=-6 3/16"; (MB_Q/2)+.125"=21 5/8"; (NOZZLE_HEIGHT - (NOZZLE_HEIGHT / 8 * 2)) / 2=16 1/8"; (NOZZLE_WB_OD - NOZZLE_TOP_OD) / 4=3 1/4"; -((MB_Q / 2) + 1/8")=-21 5/8"; -(F-((F-H)/2))/2=-15 3/16"; -MB_HEIGHT=-47 3/4"; -MB_P=-43"; -MB_P-.25=-43 1/4"; A=116 7/16"; A/2=58 7/32"; B=31 15/16"; B/2=15 31/32"; B/4=8"; C=68 15/16"; C/2=34 15/32"; CLASS=1"; D=54 1/2"; D-L-K-J=1"; D-M=31 5/8"; DUAL_Q=129 3/8"; DUAL_Q+.25"=129 5/8"; E=57 9/16"; E-(NOZZLE_RAD/3*2)=21 21/32"; E-N-N-H=2"; E/2=28 25/32"; E/2-H/2=12 19/32"; E/52*15=16 19/32"; E/52*30=33 7/32"; F=34 3/8"; F/2=17 3/16"; H=32 3/8"; H/2=16 3/16"; HEIGHT=52 1/8"; J=9 1/2"; J+K+L=53 1/2"; K=19 1/8"; L=24 7/8"; M=22 7/8"; M-(2*(D-L-K-J))=20 7/8"; MB_A=132 7/16"; MB_F=6 1/4"; MB_F-3"=3 1/4"; MB_HEIGHT=47 3/4"; MB_HEIGHT/2=23 7/8"; MB_N=14 3/16"; MB_N-(D-J-K-L)=13 3/16"; MB_P=43"; MB_P+.25"=43 1/4"; MB_P+MB_P+.5=86 1/2"; MB_P-4.5"=38 1/2"; MB_Q=43"; N=10 19/32"; N+(H/2)=26 25/32"; NOZZLE_BOTTOM_ID=21 3/8"; NOZZLE_BOTTOM_RAD=10 11/16"; NOZZLE_BOTTOM_RAD-3*2=4 11/16"; NOZZLE_HEIGHT=43"; NOZZLE_HEIGHT/7*2=10 3/4"; NOZZLE_SIZE=15"; NOZZLE_TOP_OD=23"; NOZZLE_TOP_RAD=11 1/2"; NOZZLE_WB/4=7 3/16"; NOZZLE_WB_OD=36"; NOZZLE_WB_RAD=18"; NOZZLE_WB_RAD-2"=16"; P=60"; R=27"; R*1.1=29 11/16"; R+((B/2)+1.5")=44 15/32"; R-((B/2)+1.5")=9 17/32"; RO/2=19 1/4"; RO2/2=105 5/8"; TRANSITION=15 1/8"; TRANSITION/2=7 9/16"; TRIP_Q=215 3/4"; TRIP_Q-4.5"=211 1/4"; Type Comments=Triple Vari-Plume Laboratory Exhaust Centrifugal Airfoil Class 1 Arr 10 With Mixing Box
- Triple_270_CAVP-15H_CLASS_1_With_Mixing_Box: ((M - (2 * (D - L - K - J))) / 2) + (TRANSITION / 2)=18"; (B/2)+1.5"=17 15/32"; (B/2)-.125"=15 27/32"; (D-J-K-L)*2=2"; (E/2)-((B/2)+1.5")=11 5/16"; (E/2)-((MB_P/2)+.125")=7 5/32"; (E/2)-(E/52*15)=12 3/16"; (F-((F-H)/2))/2=15 3/16"; (M - (2 * (D - L - K - J)))/2=10 7/16"; (MB_P/2)+.125"=21 5/8"; (MB_P/2-.125")+((F / 2) - 2")=-36 9/16"; (MB_P/2-.125")-((F / 2) - 2")=-6 3/16"; (MB_Q/2)+.125"=21 5/8"; (NOZZLE_HEIGHT - (NOZZLE_HEIGHT / 8 * 2)) / 2=16 1/8"; (NOZZLE_WB_OD - NOZZLE_TOP_OD) / 4=3 1/4"; -((MB_Q / 2) + 1/8")=-21 5/8"; -(F-((F-H)/2))/2=-15 3/16"; -MB_HEIGHT=-47 3/4"; -MB_P=-43"; -MB_P-.25=-43 1/4"; A=116 7/16"; A/2=58 7/32"; B=31 15/16"; B/2=15 31/32"; B/4=8"; C=68 15/16"; C/2=34 15/32"; CLASS=1"; D=54 1/2"; D-L-K-J=1"; D-M=31 5/8"; DUAL_Q=129 3/8"; DUAL_Q+.25"=129 5/8"; E=57 9/16"; E-(NOZZLE_RAD/3*2)=21 21/32"; E-N-N-H=2"; E/2=28 25/32"; E/2-H/2=12 19/32"; E/52*15=16 19/32"; E/52*30=33 7/32"; F=34 3/8"; F/2=17 3/16"; H=32 3/8"; H/2=16 3/16"; HEIGHT=52 1/8"; J=9 1/2"; J+K+L=53 1/2"; K=19 1/8"; L=24 7/8"; M=22 7/8"; M-(2*(D-L-K-J))=20 7/8"; MB_A=132 7/16"; MB_F=6 1/4"; MB_F-3"=3 1/4"; MB_HEIGHT=47 3/4"; MB_HEIGHT/2=23 7/8"; MB_N=14 3/16"; MB_N-(D-J-K-L)=13 3/16"; MB_P=43"; MB_P+.25"=43 1/4"; MB_P+MB_P+.5=86 1/2"; MB_P-4.5"=38 1/2"; MB_Q=43"; N=10 19/32"; N+(H/2)=26 25/32"; NOZZLE_BOTTOM_ID=21 3/8"; NOZZLE_BOTTOM_RAD=10 11/16"; NOZZLE_BOTTOM_RAD-3*2=4 11/16"; NOZZLE_HEIGHT=43"; NOZZLE_HEIGHT/7*2=10 3/4"; NOZZLE_SIZE=15"; NOZZLE_TOP_OD=23"; NOZZLE_TOP_RAD=11 1/2"; NOZZLE_WB/4=7 3/16"; NOZZLE_WB_OD=36"; NOZZLE_WB_RAD=18"; NOZZLE_WB_RAD-2"=16"; P=60"; R=27"; R*1.1=29 11/16"; R+((B/2)+1.5")=44 15/32"; R-((B/2)+1.5")=9 17/32"; RO/2=19 1/4"; RO2/2=105 5/8"; TRANSITION=15 1/8"; TRANSITION/2=7 9/16"; TRIP_Q=215 3/4"; TRIP_Q-4.5"=211 1/4"; Type Comments=Triple Vari-Plume Laboratory Exhaust Centrifugal Airfoil Class 1 Arr 10 With Mixing Box
- Triple_270_CAVP-18L_CLASS_1_With_Mixing_Box: ((M - (2 * (D - L - K - J))) / 2) + (TRANSITION / 2)=19 1/2"; (B/2)+1.5"=17 15/32"; (B/2)-.125"=15 27/32"; (D-J-K-L)*2=2"; (E/2)-((B/2)+1.5")=11 5/16"; (E/2)-((MB_P/2)+.125")=7 5/32"; (E/2)-(E/52*15)=12 3/16"; (F-((F-H)/2))/2=15 3/16"; (M - (2 * (D - L - K - J)))/2=10 7/16"; (MB_P/2)+.125"=21 5/8"; (MB_P/2-.125")+((F / 2) - 2")=-36 9/16"; (MB_P/2-.125")-((F / 2) - 2")=-6 3/16"; (MB_Q/2)+.125"=21 5/8"; (NOZZLE_HEIGHT - (NOZZLE_HEIGHT / 8 * 2)) / 2=18"; (NOZZLE_WB_OD - NOZZLE_TOP_OD) / 4=3 7/8"; -((MB_Q / 2) + 1/8")=-21 5/8"; -(F-((F-H)/2))/2=-15 3/16"; -MB_HEIGHT=-47 3/4"; -MB_P=-43"; -MB_P-.25=-43 1/4"; A=116 7/16"; A/2=58 7/32"; B=31 15/16"; B/2=15 31/32"; B/4=8"; C=68 15/16"; C/2=34 15/32"; CLASS=1"; D=54 1/2"; D-L-K-J=1"; D-M=31 5/8"; DUAL_Q=129 3/8"; DUAL_Q+.25"=129 5/8"; E=57 9/16"; E-(NOZZLE_RAD/3*2)=20 1/4"; E-N-N-H=2"; E/2=28 25/32"; E/2-H/2=12 19/32"; E/52*15=16 19/32"; E/52*30=33 7/32"; F=34 3/8"; F/2=17 3/16"; H=32 3/8"; H/2=16 3/16"; HEIGHT=52 1/8"; J=9 1/2"; J+K+L=53 1/2"; K=19 1/8"; L=24 7/8"; M=22 7/8"; M-(2*(D-L-K-J))=20 7/8"; MB_A=132 7/16"; MB_F=6 1/4"; MB_F-3"=3 1/4"; MB_HEIGHT=47 3/4"; MB_HEIGHT/2=23 7/8"; MB_N=14 3/16"; MB_N-(D-J-K-L)=13 3/16"; MB_P=43"; MB_P+.25"=43 1/4"; MB_P+MB_P+.5=86 1/2"; MB_P-4.5"=38 1/2"; MB_Q=43"; N=10 19/32"; N+(H/2)=26 25/32"; NOZZLE_BOTTOM_ID=25 5/8"; NOZZLE_BOTTOM_RAD=12 13/16"; NOZZLE_BOTTOM_RAD-3*2=6 13/16"; NOZZLE_HEIGHT=48"; NOZZLE_HEIGHT/7*2=12"; NOZZLE_SIZE=18"; NOZZLE_TOP_OD=27 1/2"; NOZZLE_TOP_RAD=13 3/4"; NOZZLE_WB/4=8 19/32"; NOZZLE_WB_OD=43"; NOZZLE_WB_RAD=21 1/2"; NOZZLE_WB_RAD-2"=19 1/2"; P=60"; R=27"; R*1.1=29 11/16"; R+((B/2)+1.5")=44 15/32"; R-((B/2)+1.5")=9 17/32"; RO/2=19 1/4"; RO2/2=105 5/8"; TRANSITION=18 1/8"; TRANSITION/2=9 1/16"; TRIP_Q=215 3/4"; TRIP_Q-4.5"=211 1/4"; Type Comments=Triple Vari-Plume Laboratory Exhaust Centrifugal Airfoil Class 1 Arr 10 With Mixing Box
- Triple_270_CAVP-18H_CLASS_1_With_Mixing_Box: ((M - (2 * (D - L - K - J))) / 2) + (TRANSITION / 2)=19 1/2"; (B/2)+1.5"=17 15/32"; (B/2)-.125"=15 27/32"; (D-J-K-L)*2=2"; (E/2)-((B/2)+1.5")=11 5/16"; (E/2)-((MB_P/2)+.125")=7 5/32"; (E/2)-(E/52*15)=12 3/16"; (F-((F-H)/2))/2=15 3/16"; (M - (2 * (D - L - K - J)))/2=10 7/16"; (MB_P/2)+.125"=21 5/8"; (MB_P/2-.125")+((F / 2) - 2")=-36 9/16"; (MB_P/2-.125")-((F / 2) - 2")=-6 3/16"; (MB_Q/2)+.125"=21 5/8"; (NOZZLE_HEIGHT - (NOZZLE_HEIGHT / 8 * 2)) / 2=18"; (NOZZLE_WB_OD - NOZZLE_TOP_OD) / 4=3 7/8"; -((MB_Q / 2) + 1/8")=-21 5/8"; -(F-((F-H)/2))/2=-15 3/16"; -MB_HEIGHT=-47 3/4"; -MB_P=-43"; -MB_P-.25=-43 1/4"; A=116 7/16"; A/2=58 7/32"; B=31 15/16"; B/2=15 31/32"; B/4=8"; C=68 15/16"; C/2=34 15/32"; CLASS=1"; D=54 1/2"; D-L-K-J=1"; D-M=31 5/8"; DUAL_Q=129 3/8"; DUAL_Q+.25"=129 5/8"; E=57 9/16"; E-(NOZZLE_RAD/3*2)=20 1/4"; E-N-N-H=2"; E/2=28 25/32"; E/2-H/2=12 19/32"; E/52*15=16 19/32"; E/52*30=33 7/32"; F=34 3/8"; F/2=17 3/16"; H=32 3/8"; H/2=16 3/16"; HEIGHT=52 1/8"; J=9 1/2"; J+K+L=53 1/2"; K=19 1/8"; L=24 7/8"; M=22 7/8"; M-(2*(D-L-K-J))=20 7/8"; MB_A=132 7/16"; MB_F=6 1/4"; MB_F-3"=3 1/4"; MB_HEIGHT=47 3/4"; MB_HEIGHT/2=23 7/8"; MB_N=14 3/16"; MB_N-(D-J-K-L)=13 3/16"; MB_P=43"; MB_P+.25"=43 1/4"; MB_P+MB_P+.5=86 1/2"; MB_P-4.5"=38 1/2"; MB_Q=43"; N=10 19/32"; N+(H/2)=26 25/32"; NOZZLE_BOTTOM_ID=25 5/8"; NOZZLE_BOTTOM_RAD=12 13/16"; NOZZLE_BOTTOM_RAD-3*2=6 13/16"; NOZZLE_HEIGHT=48"; NOZZLE_HEIGHT/7*2=12"; NOZZLE_SIZE=18"; NOZZLE_TOP_OD=27 1/2"; NOZZLE_TOP_RAD=13 3/4"; NOZZLE_WB/4=8 19/32"; NOZZLE_WB_OD=43"; NOZZLE_WB_RAD=21 1/2"; NOZZLE_WB_RAD-2"=19 1/2"; P=60"; R=27"; R*1.1=29 11/16"; R+((B/2)+1.5")=44 15/32"; R-((B/2)+1.5")=9 17/32"; RO/2=19 1/4"; RO2/2=105 5/8"; TRANSITION=18 1/8"; TRANSITION/2=9 1/16"; TRIP_Q=215 3/4"; TRIP_Q-4.5"=211 1/4"; Type Comments=Triple Vari-Plume Laboratory Exhaust Centrifugal Airfoil Class 1 Arr 10 With Mixing Box
- Triple_270_CAVP-12L_CLASS_2_With_Mixing_Box: ((M - (2 * (D - L - K - J))) / 2) + (TRANSITION / 2)=16 15/32"; (B/2)+1.5"=17 15/32"; (B/2)-.125"=15 27/32"; (D-J-K-L)*2=2"; (E/2)-((B/2)+1.5")=11 5/16"; (E/2)-((MB_P/2)+.125")=7 5/32"; (E/2)-(E/52*15)=12 3/16"; (F-((F-H)/2))/2=15 3/16"; (M - (2 * (D - L - K - J)))/2=10 7/16"; (MB_P/2)+.125"=21 5/8"; (MB_P/2-.125")+((F / 2) - 2")=-36 9/16"; (MB_P/2-.125")-((F / 2) - 2")=-6 3/16"; (MB_Q/2)+.125"=21 5/8"; (NOZZLE_HEIGHT - (NOZZLE_HEIGHT / 8 * 2)) / 2=12"; (NOZZLE_WB_OD - NOZZLE_TOP_OD) / 4=2 1/8"; -((MB_Q / 2) + 1/8")=-21 5/8"; -(F-((F-H)/2))/2=-15 3/16"; -MB_HEIGHT=-47 3/4"; -MB_P=-43"; -MB_P-.25=-43 1/4"; A=116 7/16"; A/2=58 7/32"; B=31 15/16"; B/2=15 31/32"; B/4=8"; C=68 15/16"; C/2=34 15/32"; CLASS=2"; D=56 1/2"; D-L-K-J=1"; D-M=33 5/8"; DUAL_Q=129 3/8"; DUAL_Q+.25"=129 5/8"; E=57 9/16"; E-(NOZZLE_RAD/3*2)=23 3/32"; E-N-N-H=2 19/32"; E/2=28 25/32"; E/2-H/2=12 19/32"; E/52*15=16 19/32"; E/52*30=33 7/32"; F=34 3/8"; F/2=17 3/16"; H=32 3/8"; H/2=16 3/16"; HEIGHT=52 1/8"; J=9 1/4"; J+K+L=55 1/2"; K=21 3/8"; L=24 7/8"; M=22 7/8"; M-(2*(D-L-K-J))=20 7/8"; MB_A=134 7/16"; MB_F=6 1/4"; MB_F-3"=3 1/4"; MB_HEIGHT=47 3/4"; MB_HEIGHT/2=23 7/8"; MB_N=14 3/16"; MB_N-(D-J-K-L)=13 3/16"; MB_P=43"; MB_P+.25"=43 1/4"; MB_P+MB_P+.5=86 1/2"; MB_P-4.5"=38 1/2"; MB_Q=43"; N=10"; N+(H/2)=26 3/16"; NOZZLE_BOTTOM_ID=17 1/16"; NOZZLE_BOTTOM_RAD=8 17/32"; NOZZLE_BOTTOM_RAD-3*2=2 17/32"; NOZZLE_HEIGHT=32"; NOZZLE_HEIGHT/7*2=8"; NOZZLE_SIZE=12"; NOZZLE_TOP_OD=19 1/2"; NOZZLE_TOP_RAD=9 3/4"; NOZZLE_WB/4=5 19/32"; NOZZLE_WB_OD=28"; NOZZLE_WB_RAD=14"; NOZZLE_WB_RAD-2"=12"; P=60"; R=27"; R*1.1=29 11/16"; R+((B/2)+1.5")=44 15/32"; R-((B/2)+1.5")=9 17/32"; RO/2=19 1/4"; RO2/2=105 5/8"; TRANSITION=12 1/16"; TRANSITION/2=6 1/32"; TRIP_Q=215 3/4"; TRIP_Q-4.5"=211 1/4"; Type Comments=Triple Vari-Plume Laboratory Exhaust Centrifugal Airfoil Class 2 Arr 10 With Mixing Box
- Triple_270_CAVP-12H_CLASS_2_With_Mixing_Box: ((M - (2 * (D - L - K - J))) / 2) + (TRANSITION / 2)=16 15/32"; (B/2)+1.5"=17 15/32"; (B/2)-.125"=15 27/32"; (D-J-K-L)*2=2"; (E/2)-((B/2)+1.5")=11 5/16"; (E/2)-((MB_P/2)+.125")=7 5/32"; (E/2)-(E/52*15)=12 3/16"; (F-((F-H)/2))/2=15 3/16"; (M - (2 * (D - L - K - J)))/2=10 7/16"; (MB_P/2)+.125"=21 5/8"; (MB_P/2-.125")+((F / 2) - 2")=-36 9/16"; (MB_P/2-.125")-((F / 2) - 2")=-6 3/16"; (MB_Q/2)+.125"=21 5/8"; (NOZZLE_HEIGHT - (NOZZLE_HEIGHT / 8 * 2)) / 2=12"; (NOZZLE_WB_OD - NOZZLE_TOP_OD) / 4=2 1/8"; -((MB_Q / 2) + 1/8")=-21 5/8"; -(F-((F-H)/2))/2=-15 3/16"; -MB_HEIGHT=-47 3/4"; -MB_P=-43"; -MB_P-.25=-43 1/4"; A=116 7/16"; A/2=58 7/32"; B=31 15/16"; B/2=15 31/32"; B/4=8"; C=68 15/16"; C/2=34 15/32"; CLASS=2"; D=56 1/2"; D-L-K-J=1"; D-M=33 5/8"; DUAL_Q=129 3/8"; DUAL_Q+.25"=129 5/8"; E=57 9/16"; E-(NOZZLE_RAD/3*2)=23 3/32"; E-N-N-H=2 19/32"; E/2=28 25/32"; E/2-H/2=12 19/32"; E/52*15=16 19/32"; E/52*30=33 7/32"; F=34 3/8"; F/2=17 3/16"; H=32 3/8"; H/2=16 3/16"; HEIGHT=52 1/8"; J=9 1/4"; J+K+L=55 1/2"; K=21 3/8"; L=24 7/8"; M=22 7/8"; M-(2*(D-L-K-J))=20 7/8"; MB_A=134 7/16"; MB_F=6 1/4"; MB_F-3"=3 1/4"; MB_HEIGHT=47 3/4"; MB_HEIGHT/2=23 7/8"; MB_N=14 3/16"; MB_N-(D-J-K-L)=13 3/16"; MB_P=43"; MB_P+.25"=43 1/4"; MB_P+MB_P+.5=86 1/2"; MB_P-4.5"=38 1/2"; MB_Q=43"; N=10"; N+(H/2)=26 3/16"; NOZZLE_BOTTOM_ID=17 1/16"; NOZZLE_BOTTOM_RAD=8 17/32"; NOZZLE_BOTTOM_RAD-3*2=2 17/32"; NOZZLE_HEIGHT=32"; NOZZLE_HEIGHT/7*2=8"; NOZZLE_SIZE=12"; NOZZLE_TOP_OD=19 1/2"; NOZZLE_TOP_RAD=9 3/4"; NOZZLE_WB/4=5 19/32"; NOZZLE_WB_OD=28"; NOZZLE_WB_RAD=14"; NOZZLE_WB_RAD-2"=12"; P=60"; R=27"; R*1.1=29 11/16"; R+((B/2)+1.5")=44 15/32"; R-((B/2)+1.5")=9 17/32"; RO/2=19 1/4"; RO2/2=105 5/8"; TRANSITION=12 1/16"; TRANSITION/2=6 1/32"; TRIP_Q=215 3/4"; TRIP_Q-4.5"=211 1/4"; Type Comments=Triple Vari-Plume Laboratory Exhaust Centrifugal Airfoil Class 2 Arr 10 With Mixing Box
- Triple_270_CAVP-15L_CLASS_2_With_Mixing_Box: ((M - (2 * (D - L - K - J))) / 2) + (TRANSITION / 2)=18"; (B/2)+1.5"=17 15/32"; (B/2)-.125"=15 27/32"; (D-J-K-L)*2=2"; (E/2)-((B/2)+1.5")=11 5/16"; (E/2)-((MB_P/2)+.125")=7 5/32"; (E/2)-(E/52*15)=12 3/16"; (F-((F-H)/2))/2=15 3/16"; (M - (2 * (D - L - K - J)))/2=10 7/16"; (MB_P/2)+.125"=21 5/8"; (MB_P/2-.125")+((F / 2) - 2")=-36 9/16"; (MB_P/2-.125")-((F / 2) - 2")=-6 3/16"; (MB_Q/2)+.125"=21 5/8"; (NOZZLE_HEIGHT - (NOZZLE_HEIGHT / 8 * 2)) / 2=16 1/8"; (NOZZLE_WB_OD - NOZZLE_TOP_OD) / 4=3 1/4"; -((MB_Q / 2) + 1/8")=-21 5/8"; -(F-((F-H)/2))/2=-15 3/16"; -MB_HEIGHT=-47 3/4"; -MB_P=-43"; -MB_P-.25=-43 1/4"; A=116 7/16"; A/2=58 7/32"; B=31 15/16"; B/2=15 31/32"; B/4=8"; C=68 15/16"; C/2=34 15/32"; CLASS=2"; D=56 1/2"; D-L-K-J=1"; D-M=33 5/8"; DUAL_Q=129 3/8"; DUAL_Q+.25"=129 5/8"; E=57 9/16"; E-(NOZZLE_RAD/3*2)=21 21/32"; E-N-N-H=2 19/32"; E/2=28 25/32"; E/2-H/2=12 19/32"; E/52*15=16 19/32"; E/52*30=33 7/32"; F=34 3/8"; F/2=17 3/16"; H=32 3/8"; H/2=16 3/16"; HEIGHT=52 1/8"; J=9 1/4"; J+K+L=55 1/2"; K=21 3/8"; L=24 7/8"; M=22 7/8"; M-(2*(D-L-K-J))=20 7/8"; MB_A=134 7/16"; MB_F=6 1/4"; MB_F-3"=3 1/4"; MB_HEIGHT=47 3/4"; MB_HEIGHT/2=23 7/8"; MB_N=14 3/16"; MB_N-(D-J-K-L)=13 3/16"; MB_P=43"; MB_P+.25"=43 1/4"; MB_P+MB_P+.5=86 1/2"; MB_P-4.5"=38 1/2"; MB_Q=43"; N=10"; N+(H/2)=26 3/16"; NOZZLE_BOTTOM_ID=21 3/8"; NOZZLE_BOTTOM_RAD=10 11/16"; NOZZLE_BOTTOM_RAD-3*2=4 11/16"; NOZZLE_HEIGHT=43"; NOZZLE_HEIGHT/7*2=10 3/4"; NOZZLE_SIZE=15"; NOZZLE_TOP_OD=23"; NOZZLE_TOP_RAD=11 1/2"; NOZZLE_WB/4=7 3/16"; NOZZLE_WB_OD=36"; NOZZLE_WB_RAD=18"; NOZZLE_WB_RAD-2"=16"; P=60"; R=27"; R*1.1=29 11/16"; R+((B/2)+1.5")=44 15/32"; R-((B/2)+1.5")=9 17/32"; RO/2=19 1/4"; RO2/2=105 5/8"; TRANSITION=15 1/8"; TRANSITION/2=7 9/16"; TRIP_Q=215 3/4"; TRIP_Q-4.5"=211 1/4"; Type Comments=Triple Vari-Plume Laboratory Exhaust Centrifugal Airfoil Class 2 Arr 10 With Mixing Box
- Triple_270_CAVP-15H_CLASS_2_With_Mixing_Box: ((M - (2 * (D - L - K - J))) / 2) + (TRANSITION / 2)=18"; (B/2)+1.5"=17 15/32"; (B/2)-.125"=15 27/32"; (D-J-K-L)*2=2"; (E/2)-((B/2)+1.5")=11 5/16"; (E/2)-((MB_P/2)+.125")=7 5/32"; (E/2)-(E/52*15)=12 3/16"; (F-((F-H)/2))/2=15 3/16"; (M - (2 * (D - L - K - J)))/2=10 7/16"; (MB_P/2)+.125"=21 5/8"; (MB_P/2-.125")+((F / 2) - 2")=-36 9/16"; (MB_P/2-.125")-((F / 2) - 2")=-6 3/16"; (MB_Q/2)+.125"=21 5/8"; (NOZZLE_HEIGHT - (NOZZLE_HEIGHT / 8 * 2)) / 2=16 1/8"; (NOZZLE_WB_OD - NOZZLE_TOP_OD) / 4=3 1/4"; -((MB_Q / 2) + 1/8")=-21 5/8"; -(F-((F-H)/2))/2=-15 3/16"; -MB_HEIGHT=-47 3/4"; -MB_P=-43"; -MB_P-.25=-43 1/4"; A=116 7/16"; A/2=58 7/32"; B=31 15/16"; B/2=15 31/32"; B/4=8"; C=68 15/16"; C/2=34 15/32"; CLASS=2"; D=56 1/2"; D-L-K-J=1"; D-M=33 5/8"; DUAL_Q=129 3/8"; DUAL_Q+.25"=129 5/8"; E=57 9/16"; E-(NOZZLE_RAD/3*2)=21 21/32"; E-N-N-H=2 19/32"; E/2=28 25/32"; E/2-H/2=12 19/32"; E/52*15=16 19/32"; E/52*30=33 7/32"; F=34 3/8"; F/2=17 3/16"; H=32 3/8"; H/2=16 3/16"; HEIGHT=52 1/8"; J=9 1/4"; J+K+L=55 1/2"; K=21 3/8"; L=24 7/8"; M=22 7/8"; M-(2*(D-L-K-J))=20 7/8"; MB_A=134 7/16"; MB_F=6 1/4"; MB_F-3"=3 1/4"; MB_HEIGHT=47 3/4"; MB_HEIGHT/2=23 7/8"; MB_N=14 3/16"; MB_N-(D-J-K-L)=13 3/16"; MB_P=43"; MB_P+.25"=43 1/4"; MB_P+MB_P+.5=86 1/2"; MB_P-4.5"=38 1/2"; MB_Q=43"; N=10"; N+(H/2)=26 3/16"; NOZZLE_BOTTOM_ID=21 3/8"; NOZZLE_BOTTOM_RAD=10 11/16"; NOZZLE_BOTTOM_RAD-3*2=4 11/16"; NOZZLE_HEIGHT=43"; NOZZLE_HEIGHT/7*2=10 3/4"; NOZZLE_SIZE=15"; NOZZLE_TOP_OD=23"; NOZZLE_TOP_RAD=11 1/2"; NOZZLE_WB/4=7 3/16"; NOZZLE_WB_OD=36"; NOZZLE_WB_RAD=18"; NOZZLE_WB_RAD-2"=16"; P=60"; R=27"; R*1.1=29 11/16"; R+((B/2)+1.5")=44 15/32"; R-((B/2)+1.5")=9 17/32"; RO/2=19 1/4"; RO2/2=105 5/8"; TRANSITION=15 1/8"; TRANSITION/2=7 9/16"; TRIP_Q=215 3/4"; TRIP_Q-4.5"=211 1/4"; Type Comments=Triple Vari-Plume Laboratory Exhaust Centrifugal Airfoil Class 2 Arr 10 With Mixing Box
- Triple_270_CAVP-18L_CLASS_2_With_Mixing_Box: ((M - (2 * (D - L - K - J))) / 2) + (TRANSITION / 2)=19 1/2"; (B/2)+1.5"=17 15/32"; (B/2)-.125"=15 27/32"; (D-J-K-L)*2=2"; (E/2)-((B/2)+1.5")=11 5/16"; (E/2)-((MB_P/2)+.125")=7 5/32"; (E/2)-(E/52*15)=12 3/16"; (F-((F-H)/2))/2=15 3/16"; (M - (2 * (D - L - K - J)))/2=10 7/16"; (MB_P/2)+.125"=21 5/8"; (MB_P/2-.125")+((F / 2) - 2")=-36 9/16"; (MB_P/2-.125")-((F / 2) - 2")=-6 3/16"; (MB_Q/2)+.125"=21 5/8"; (NOZZLE_HEIGHT - (NOZZLE_HEIGHT / 8 * 2)) / 2=18"; (NOZZLE_WB_OD - NOZZLE_TOP_OD) / 4=3 7/8"; -((MB_Q / 2) + 1/8")=-21 5/8"; -(F-((F-H)/2))/2=-15 3/16"; -MB_HEIGHT=-47 3/4"; -MB_P=-43"; -MB_P-.25=-43 1/4"; A=116 7/16"; A/2=58 7/32"; B=31 15/16"; B/2=15 31/32"; B/4=8"; C=68 15/16"; C/2=34 15/32"; CLASS=2"; D=56 1/2"; D-L-K-J=1"; D-M=33 5/8"; DUAL_Q=129 3/8"; DUAL_Q+.25"=129 5/8"; E=57 9/16"; E-(NOZZLE_RAD/3*2)=20 1/4"; E-N-N-H=2 19/32"; E/2=28 25/32"; E/2-H/2=12 19/32"; E/52*15=16 19/32"; E/52*30=33 7/32"; F=34 3/8"; F/2=17 3/16"; H=32 3/8"; H/2=16 3/16"; HEIGHT=52 1/8"; J=9 1/4"; J+K+L=55 1/2"; K=21 3/8"; L=24 7/8"; M=22 7/8"; M-(2*(D-L-K-J))=20 7/8"; MB_A=134 7/16"; MB_F=6 1/4"; MB_F-3"=3 1/4"; MB_HEIGHT=47 3/4"; MB_HEIGHT/2=23 7/8"; MB_N=14 3/16"; MB_N-(D-J-K-L)=13 3/16"; MB_P=43"; MB_P+.25"=43 1/4"; MB_P+MB_P+.5=86 1/2"; MB_P-4.5"=38 1/2"; MB_Q=43"; N=10"; N+(H/2)=26 3/16"; NOZZLE_BOTTOM_ID=25 5/8"; NOZZLE_BOTTOM_RAD=12 13/16"; NOZZLE_BOTTOM_RAD-3*2=6 13/16"; NOZZLE_HEIGHT=48"; NOZZLE_HEIGHT/7*2=12"; NOZZLE_SIZE=18"; NOZZLE_TOP_OD=27 1/2"; NOZZLE_TOP_RAD=13 3/4"; NOZZLE_WB/4=8 19/32"; NOZZLE_WB_OD=43"; NOZZLE_WB_RAD=21 1/2"; NOZZLE_WB_RAD-2"=19 1/2"; P=60"; R=27"; R*1.1=29 11/16"; R+((B/2)+1.5")=44 15/32"; R-((B/2)+1.5")=9 17/32"; RO/2=19 1/4"; RO2/2=105 5/8"; TRANSITION=18 1/8"; TRANSITION/2=9 1/16"; TRIP_Q=215 3/4"; TRIP_Q-4.5"=211 1/4"; Type Comments=Triple Vari-Plume Laboratory Exhaust Centrifugal Airfoil Class 2 Arr 10 With Mixing Box
- Triple_270_CAVP-18H_CLASS_2_With_Mixing_Box: ((M - (2 * (D - L - K - J))) / 2) + (TRANSITION / 2)=19 1/2"; (B/2)+1.5"=17 15/32"; (B/2)-.125"=15 27/32"; (D-J-K-L)*2=2"; (E/2)-((B/2)+1.5")=11 5/16"; (E/2)-((MB_P/2)+.125")=7 5/32"; (E/2)-(E/52*15)=12 3/16"; (F-((F-H)/2))/2=15 3/16"; (M - (2 * (D - L - K - J)))/2=10 7/16"; (MB_P/2)+.125"=21 5/8"; (MB_P/2-.125")+((F / 2) - 2")=-36 9/16"; (MB_P/2-.125")-((F / 2) - 2")=-6 3/16"; (MB_Q/2)+.125"=21 5/8"; (NOZZLE_HEIGHT - (NOZZLE_HEIGHT / 8 * 2)) / 2=18"; (NOZZLE_WB_OD - NOZZLE_TOP_OD) / 4=3 7/8"; -((MB_Q / 2) + 1/8")=-21 5/8"; -(F-((F-H)/2))/2=-15 3/16"; -MB_HEIGHT=-47 3/4"; -MB_P=-43"; -MB_P-.25=-43 1/4"; A=116 7/16"; A/2=58 7/32"; B=31 15/16"; B/2=15 31/32"; B/4=8"; C=68 15/16"; C/2=34 15/32"; CLASS=2"; D=56 1/2"; D-L-K-J=1"; D-M=33 5/8"; DUAL_Q=129 3/8"; DUAL_Q+.25"=129 5/8"; E=57 9/16"; E-(NOZZLE_RAD/3*2)=20 1/4"; E-N-N-H=2 19/32"; E/2=28 25/32"; E/2-H/2=12 19/32"; E/52*15=16 19/32"; E/52*30=33 7/32"; F=34 3/8"; F/2=17 3/16"; H=32 3/8"; H/2=16 3/16"; HEIGHT=52 1/8"; J=9 1/4"; J+K+L=55 1/2"; K=21 3/8"; L=24 7/8"; M=22 7/8"; M-(2*(D-L-K-J))=20 7/8"; MB_A=134 7/16"; MB_F=6 1/4"; MB_F-3"=3 1/4"; MB_HEIGHT=47 3/4"; MB_HEIGHT/2=23 7/8"; MB_N=14 3/16"; MB_N-(D-J-K-L)=13 3/16"; MB_P=43"; MB_P+.25"=43 1/4"; MB_P+MB_P+.5=86 1/2"; MB_P-4.5"=38 1/2"; MB_Q=43"; N=10"; N+(H/2)=26 3/16"; NOZZLE_BOTTOM_ID=25 5/8"; NOZZLE_BOTTOM_RAD=12 13/16"; NOZZLE_BOTTOM_RAD-3*2=6 13/16"; NOZZLE_HEIGHT=48"; NOZZLE_HEIGHT/7*2=12"; NOZZLE_SIZE=18"; NOZZLE_TOP_OD=27 1/2"; NOZZLE_TOP_RAD=13 3/4"; NOZZLE_WB/4=8 19/32"; NOZZLE_WB_OD=43"; NOZZLE_WB_RAD=21 1/2"; NOZZLE_WB_RAD-2"=19 1/2"; P=60"; R=27"; R*1.1=29 11/16"; R+((B/2)+1.5")=44 15/32"; R-((B/2)+1.5")=9 17/32"; RO/2=19 1/4"; RO2/2=105 5/8"; TRANSITION=18 1/8"; TRANSITION/2=9 1/16"; TRIP_Q=215 3/4"; TRIP_Q-4.5"=211 1/4"; Type Comments=Triple Vari-Plume Laboratory Exhaust Centrifugal Airfoil Class 2 Arr 10 With Mixing Box
- Triple_300_CAVP-12L_CLASS_1_With_Mixing_Box: ((M - (2 * (D - L - K - J))) / 2) + (TRANSITION / 2)=17 5/8"; (B/2)+1.5"=18 31/32"; (B/2)-.125"=17 11/32"; (D-J-K-L)*2=2"; (E/2)-((B/2)+1.5")=12 29/32"; (E/2)-((MB_P/2)+.125")=8 3/4"; (E/2)-(E/52*15)=13 1/2"; (F-((F-H)/2))/2=16 11/16"; (M - (2 * (D - L - K - J)))/2=11 19/32"; (MB_P/2)+.125"=23 1/8"; (MB_P/2-.125")+((F / 2) - 2")=-39 9/16"; (MB_P/2-.125")-((F / 2) - 2")=-6 3/16"; (MB_Q/2)+.125"=23 1/8"; (NOZZLE_HEIGHT - (NOZZLE_HEIGHT / 8 * 2)) / 2=12"; (NOZZLE_WB_OD - NOZZLE_TOP_OD) / 4=2 1/8"; -((MB_Q / 2) + 1/8")=-23 1/8"; -(F-((F-H)/2))/2=-16 11/16"; -MB_HEIGHT=-50 3/4"; -MB_P=-46"; -MB_P-.25=-46 1/4"; A=122 7/16"; A/2=61 7/32"; B=34 15/16"; B/2=17 15/32"; B/4=8 3/4"; C=74 15/16"; C/2=37 15/32"; CLASS=1"; D=57 5/16"; D-L-K-J=1"; D-M=32 1/8"; DUAL_Q=138 3/8"; DUAL_Q+.25"=138 5/8"; E=63 3/4"; E-(NOZZLE_RAD/3*2)=26 3/16"; E-N-N-H=2"; E/2=31 7/8"; E/2-H/2=14 3/16"; E/52*15=18 3/8"; E/52*30=36 25/32"; F=37 3/8"; F/2=18 11/16"; H=35 3/8"; H/2=17 11/16"; HEIGHT=57 27/32"; J=10"; J+K+L=56 5/16"; K=19 1/8"; L=27 3/16"; M=25 3/16"; M-(2*(D-L-K-J))=23 3/16"; MB_A=140 1/8"; MB_F=7 3/4"; MB_F-3"=4 3/4"; MB_HEIGHT=50 3/4"; MB_HEIGHT/2=25 3/8"; MB_N=14 3/16"; MB_N-(D-J-K-L)=13 3/16"; MB_P=46"; MB_P+.25"=46 1/4"; MB_P+MB_P+.5=92 1/2"; MB_P-4.5"=41 1/2"; MB_Q=46"; N=12 3/16"; N+(H/2)=29 7/8"; NOZZLE_BOTTOM_ID=17 1/16"; NOZZLE_BOTTOM_RAD=8 17/32"; NOZZLE_BOTTOM_RAD-3*2=2 17/32"; NOZZLE_HEIGHT=32"; NOZZLE_HEIGHT/7*2=8"; NOZZLE_SIZE=12"; NOZZLE_TOP_OD=19 1/2"; NOZZLE_TOP_RAD=9 3/4"; NOZZLE_WB/4=5 19/32"; NOZZLE_WB_OD=28"; NOZZLE_WB_RAD=14"; NOZZLE_WB_RAD-2"=12"; P=60"; R=30"; R*1.1=33"; R+((B/2)+1.5")=48 31/32"; R-((B/2)+1.5")=11 1/32"; RO/2=20 3/4"; RO2/2=113 1/8"; TRANSITION=12 1/16"; TRANSITION/2=6 1/32"; TRIP_Q=230 3/4"; TRIP_Q-4.5"=226 1/4"; Type Comments=Triple Vari-Plume Laboratory Exhaust Centrifugal Airfoil Class 1 Arr 10 With Mixing Box
- Triple_300_CAVP-12H_CLASS_1_With_Mixing_Box: ((M - (2 * (D - L - K - J))) / 2) + (TRANSITION / 2)=17 5/8"; (B/2)+1.5"=18 31/32"; (B/2)-.125"=17 11/32"; (D-J-K-L)*2=2"; (E/2)-((B/2)+1.5")=12 29/32"; (E/2)-((MB_P/2)+.125")=8 3/4"; (E/2)-(E/52*15)=13 1/2"; (F-((F-H)/2))/2=16 11/16"; (M - (2 * (D - L - K - J)))/2=11 19/32"; (MB_P/2)+.125"=23 1/8"; (MB_P/2-.125")+((F / 2) - 2")=-39 9/16"; (MB_P/2-.125")-((F / 2) - 2")=-6 3/16"; (MB_Q/2)+.125"=23 1/8"; (NOZZLE_HEIGHT - (NOZZLE_HEIGHT / 8 * 2)) / 2=12"; (NOZZLE_WB_OD - NOZZLE_TOP_OD) / 4=2 1/8"; -((MB_Q / 2) + 1/8")=-23 1/8"; -(F-((F-H)/2))/2=-16 11/16"; -MB_HEIGHT=-50 3/4"; -MB_P=-46"; -MB_P-.25=-46 1/4"; A=122 7/16"; A/2=61 7/32"; B=34 15/16"; B/2=17 15/32"; B/4=8 3/4"; C=74 15/16"; C/2=37 15/32"; CLASS=1"; D=57 5/16"; D-L-K-J=1"; D-M=32 1/8"; DUAL_Q=138 3/8"; DUAL_Q+.25"=138 5/8"; E=63 3/4"; E-(NOZZLE_RAD/3*2)=26 3/16"; E-N-N-H=2"; E/2=31 7/8"; E/2-H/2=14 3/16"; E/52*15=18 3/8"; E/52*30=36 25/32"; F=37 3/8"; F/2=18 11/16"; H=35 3/8"; H/2=17 11/16"; HEIGHT=57 27/32"; J=10"; J+K+L=56 5/16"; K=19 1/8"; L=27 3/16"; M=25 3/16"; M-(2*(D-L-K-J))=23 3/16"; MB_A=140 1/8"; MB_F=7 3/4"; MB_F-3"=4 3/4"; MB_HEIGHT=50 3/4"; MB_HEIGHT/2=25 3/8"; MB_N=14 3/16"; MB_N-(D-J-K-L)=13 3/16"; MB_P=46"; MB_P+.25"=46 1/4"; MB_P+MB_P+.5=92 1/2"; MB_P-4.5"=41 1/2"; MB_Q=46"; N=12 3/16"; N+(H/2)=29 7/8"; NOZZLE_BOTTOM_ID=17 1/16"; NOZZLE_BOTTOM_RAD=8 17/32"; NOZZLE_BOTTOM_RAD-3*2=2 17/32"; NOZZLE_HEIGHT=32"; NOZZLE_HEIGHT/7*2=8"; NOZZLE_SIZE=12"; NOZZLE_TOP_OD=19 1/2"; NOZZLE_TOP_RAD=9 3/4"; NOZZLE_WB/4=5 19/32"; NOZZLE_WB_OD=28"; NOZZLE_WB_RAD=14"; NOZZLE_WB_RAD-2"=12"; P=60"; R=30"; R*1.1=33"; R+((B/2)+1.5")=48 31/32"; R-((B/2)+1.5")=11 1/32"; RO/2=20 3/4"; RO2/2=113 1/8"; TRANSITION=12 1/16"; TRANSITION/2=6 1/32"; TRIP_Q=230 3/4"; TRIP_Q-4.5"=226 1/4"; Type Comments=Triple Vari-Plume Laboratory Exhaust Centrifugal Airfoil Class 1 Arr 10 With Mixing Box
- Triple_300_CAVP-15L_CLASS_1_With_Mixing_Box: ((M - (2 * (D - L - K - J))) / 2) + (TRANSITION / 2)=19 5/32"; (B/2)+1.5"=18 31/32"; (B/2)-.125"=17 11/32"; (D-J-K-L)*2=2"; (E/2)-((B/2)+1.5")=12 29/32"; (E/2)-((MB_P/2)+.125")=8 3/4"; (E/2)-(E/52*15)=13 1/2"; (F-((F-H)/2))/2=16 11/16"; (M - (2 * (D - L - K - J)))/2=11 19/32"; (MB_P/2)+.125"=23 1/8"; (MB_P/2-.125")+((F / 2) - 2")=-39 9/16"; (MB_P/2-.125")-((F / 2) - 2")=-6 3/16"; (MB_Q/2)+.125"=23 1/8"; (NOZZLE_HEIGHT - (NOZZLE_HEIGHT / 8 * 2)) / 2=16 1/8"; (NOZZLE_WB_OD - NOZZLE_TOP_OD) / 4=3 1/4"; -((MB_Q / 2) + 1/8")=-23 1/8"; -(F-((F-H)/2))/2=-16 11/16"; -MB_HEIGHT=-50 3/4"; -MB_P=-46"; -MB_P-.25=-46 1/4"; A=122 7/16"; A/2=61 7/32"; B=34 15/16"; B/2=17 15/32"; B/4=8 3/4"; C=74 15/16"; C/2=37 15/32"; CLASS=1"; D=57 5/16"; D-L-K-J=1"; D-M=32 1/8"; DUAL_Q=138 3/8"; DUAL_Q+.25"=138 5/8"; E=63 3/4"; E-(NOZZLE_RAD/3*2)=24 3/4"; E-N-N-H=2"; E/2=31 7/8"; E/2-H/2=14 3/16"; E/52*15=18 3/8"; E/52*30=36 25/32"; F=37 3/8"; F/2=18 11/16"; H=35 3/8"; H/2=17 11/16"; HEIGHT=57 27/32"; J=10"; J+K+L=56 5/16"; K=19 1/8"; L=27 3/16"; M=25 3/16"; M-(2*(D-L-K-J))=23 3/16"; MB_A=140 1/8"; MB_F=7 3/4"; MB_F-3"=4 3/4"; MB_HEIGHT=50 3/4"; MB_HEIGHT/2=25 3/8"; MB_N=14 3/16"; MB_N-(D-J-K-L)=13 3/16"; MB_P=46"; MB_P+.25"=46 1/4"; MB_P+MB_P+.5=92 1/2"; MB_P-4.5"=41 1/2"; MB_Q=46"; N=12 3/16"; N+(H/2)=29 7/8"; NOZZLE_BOTTOM_ID=21 3/8"; NOZZLE_BOTTOM_RAD=10 11/16"; NOZZLE_BOTTOM_RAD-3*2=4 11/16"; NOZZLE_HEIGHT=43"; NOZZLE_HEIGHT/7*2=10 3/4"; NOZZLE_SIZE=15"; NOZZLE_TOP_OD=23"; NOZZLE_TOP_RAD=11 1/2"; NOZZLE_WB/4=7 3/16"; NOZZLE_WB_OD=36"; NOZZLE_WB_RAD=18"; NOZZLE_WB_RAD-2"=16"; P=60"; R=30"; R*1.1=33"; R+((B/2)+1.5")=48 31/32"; R-((B/2)+1.5")=11 1/32"; RO/2=20 3/4"; RO2/2=113 1/8"; TRANSITION=15 1/8"; TRANSITION/2=7 9/16"; TRIP_Q=230 3/4"; TRIP_Q-4.5"=226 1/4"; Type Comments=Triple Vari-Plume Laboratory Exhaust Centrifugal Airfoil Class 1 Arr 10 With Mixing Box
- Triple_300_CAVP-15H_CLASS_1_With_Mixing_Box: ((M - (2 * (D - L - K - J))) / 2) + (TRANSITION / 2)=19 5/32"; (B/2)+1.5"=18 31/32"; (B/2)-.125"=17 11/32"; (D-J-K-L)*2=2"; (E/2)-((B/2)+1.5")=12 29/32"; (E/2)-((MB_P/2)+.125")=8 3/4"; (E/2)-(E/52*15)=13 1/2"; (F-((F-H)/2))/2=16 11/16"; (M - (2 * (D - L - K - J)))/2=11 19/32"; (MB_P/2)+.125"=23 1/8"; (MB_P/2-.125")+((F / 2) - 2")=-39 9/16"; (MB_P/2-.125")-((F / 2) - 2")=-6 3/16"; (MB_Q/2)+.125"=23 1/8"; (NOZZLE_HEIGHT - (NOZZLE_HEIGHT / 8 * 2)) / 2=16 1/8"; (NOZZLE_WB_OD - NOZZLE_TOP_OD) / 4=3 1/4"; -((MB_Q / 2) + 1/8")=-23 1/8"; -(F-((F-H)/2))/2=-16 11/16"; -MB_HEIGHT=-50 3/4"; -MB_P=-46"; -MB_P-.25=-46 1/4"; A=122 7/16"; A/2=61 7/32"; B=34 15/16"; B/2=17 15/32"; B/4=8 3/4"; C=74 15/16"; C/2=37 15/32"; CLASS=1"; D=57 5/16"; D-L-K-J=1"; D-M=32 1/8"; DUAL_Q=138 3/8"; DUAL_Q+.25"=138 5/8"; E=63 3/4"; E-(NOZZLE_RAD/3*2)=24 3/4"; E-N-N-H=2"; E/2=31 7/8"; E/2-H/2=14 3/16"; E/52*15=18 3/8"; E/52*30=36 25/32"; F=37 3/8"; F/2=18 11/16"; H=35 3/8"; H/2=17 11/16"; HEIGHT=57 27/32"; J=10"; J+K+L=56 5/16"; K=19 1/8"; L=27 3/16"; M=25 3/16"; M-(2*(D-L-K-J))=23 3/16"; MB_A=140 1/8"; MB_F=7 3/4"; MB_F-3"=4 3/4"; MB_HEIGHT=50 3/4"; MB_HEIGHT/2=25 3/8"; MB_N=14 3/16"; MB_N-(D-J-K-L)=13 3/16"; MB_P=46"; MB_P+.25"=46 1/4"; MB_P+MB_P+.5=92 1/2"; MB_P-4.5"=41 1/2"; MB_Q=46"; N=12 3/16"; N+(H/2)=29 7/8"; NOZZLE_BOTTOM_ID=21 3/8"; NOZZLE_BOTTOM_RAD=10 11/16"; NOZZLE_BOTTOM_RAD-3*2=4 11/16"; NOZZLE_HEIGHT=43"; NOZZLE_HEIGHT/7*2=10 3/4"; NOZZLE_SIZE=15"; NOZZLE_TOP_OD=23"; NOZZLE_TOP_RAD=11 1/2"; NOZZLE_WB/4=7 3/16"; NOZZLE_WB_OD=36"; NOZZLE_WB_RAD=18"; NOZZLE_WB_RAD-2"=16"; P=60"; R=30"; R*1.1=33"; R+((B/2)+1.5")=48 31/32"; R-((B/2)+1.5")=11 1/32"; RO/2=20 3/4"; RO2/2=113 1/8"; TRANSITION=15 1/8"; TRANSITION/2=7 9/16"; TRIP_Q=230 3/4"; TRIP_Q-4.5"=226 1/4"; Type Comments=Triple Vari-Plume Laboratory Exhaust Centrifugal Airfoil Class 1 Arr 10 With Mixing Box
- Triple_300_CAVP-18L_CLASS_1_With_Mixing_Box: ((M - (2 * (D - L - K - J))) / 2) + (TRANSITION / 2)=20 21/32"; (B/2)+1.5"=18 31/32"; (B/2)-.125"=17 11/32"; (D-J-K-L)*2=2"; (E/2)-((B/2)+1.5")=12 29/32"; (E/2)-((MB_P/2)+.125")=8 3/4"; (E/2)-(E/52*15)=13 1/2"; (F-((F-H)/2))/2=16 11/16"; (M - (2 * (D - L - K - J)))/2=11 19/32"; (MB_P/2)+.125"=23 1/8"; (MB_P/2-.125")+((F / 2) - 2")=-39 9/16"; (MB_P/2-.125")-((F / 2) - 2")=-6 3/16"; (MB_Q/2)+.125"=23 1/8"; (NOZZLE_HEIGHT - (NOZZLE_HEIGHT / 8 * 2)) / 2=18"; (NOZZLE_WB_OD - NOZZLE_TOP_OD) / 4=3 7/8"; -((MB_Q / 2) + 1/8")=-23 1/8"; -(F-((F-H)/2))/2=-16 11/16"; -MB_HEIGHT=-50 3/4"; -MB_P=-46"; -MB_P-.25=-46 1/4"; A=122 7/16"; A/2=61 7/32"; B=34 15/16"; B/2=17 15/32"; B/4=8 3/4"; C=74 15/16"; C/2=37 15/32"; CLASS=1"; D=57 5/16"; D-L-K-J=1"; D-M=32 1/8"; DUAL_Q=138 3/8"; DUAL_Q+.25"=138 5/8"; E=63 3/4"; E-(NOZZLE_RAD/3*2)=23 11/32"; E-N-N-H=2"; E/2=31 7/8"; E/2-H/2=14 3/16"; E/52*15=18 3/8"; E/52*30=36 25/32"; F=37 3/8"; F/2=18 11/16"; H=35 3/8"; H/2=17 11/16"; HEIGHT=57 27/32"; J=10"; J+K+L=56 5/16"; K=19 1/8"; L=27 3/16"; M=25 3/16"; M-(2*(D-L-K-J))=23 3/16"; MB_A=248"; MB_F=140 1/8"; MB_F-3"=137 1/8"; MB_HEIGHT=50 3/4"; MB_HEIGHT/2=25 3/8"; MB_N=14 3/16"; MB_N-(D-J-K-L)=13 3/16"; MB_P=46"; MB_P+.25"=46 1/4"; MB_P+MB_P+.5=92 1/2"; MB_P-4.5"=41 1/2"; MB_Q=46"; N=12 3/16"; N+(H/2)=29 7/8"; NOZZLE_BOTTOM_ID=25 5/8"; NOZZLE_BOTTOM_RAD=12 13/16"; NOZZLE_BOTTOM_RAD-3*2=6 13/16"; NOZZLE_HEIGHT=48"; NOZZLE_HEIGHT/7*2=12"; NOZZLE_SIZE=18"; NOZZLE_TOP_OD=27 1/2"; NOZZLE_TOP_RAD=13 3/4"; NOZZLE_WB/4=8 19/32"; NOZZLE_WB_OD=43"; NOZZLE_WB_RAD=21 1/2"; NOZZLE_WB_RAD-2"=19 1/2"; P=60"; R=30"; R*1.1=33"; R+((B/2)+1.5")=48 31/32"; R-((B/2)+1.5")=11 1/32"; RO/2=20 3/4"; RO2/2=113 1/8"; TRANSITION=18 1/8"; TRANSITION/2=9 1/16"; TRIP_Q=230 3/4"; TRIP_Q-4.5"=226 1/4"; Type Comments=Triple Vari-Plume Laboratory Exhaust Centrifugal Airfoil Class 1 Arr 10 With Mixing Box
- Triple_300_CAVP-18H_CLASS_1_With_Mixing_Box: ((M - (2 * (D - L - K - J))) / 2) + (TRANSITION / 2)=20 21/32"; (B/2)+1.5"=18 31/32"; (B/2)-.125"=17 11/32"; (D-J-K-L)*2=2"; (E/2)-((B/2)+1.5")=12 29/32"; (E/2)-((MB_P/2)+.125")=8 3/4"; (E/2)-(E/52*15)=13 1/2"; (F-((F-H)/2))/2=16 11/16"; (M - (2 * (D - L - K - J)))/2=11 19/32"; (MB_P/2)+.125"=23 1/8"; (MB_P/2-.125")+((F / 2) - 2")=-39 9/16"; (MB_P/2-.125")-((F / 2) - 2")=-6 3/16"; (MB_Q/2)+.125"=23 1/8"; (NOZZLE_HEIGHT - (NOZZLE_HEIGHT / 8 * 2)) / 2=18"; (NOZZLE_WB_OD - NOZZLE_TOP_OD) / 4=3 7/8"; -((MB_Q / 2) + 1/8")=-23 1/8"; -(F-((F-H)/2))/2=-16 11/16"; -MB_HEIGHT=-50 3/4"; -MB_P=-46"; -MB_P-.25=-46 1/4"; A=122 7/16"; A/2=61 7/32"; B=34 15/16"; B/2=17 15/32"; B/4=8 3/4"; C=74 15/16"; C/2=37 15/32"; CLASS=1"; D=57 5/16"; D-L-K-J=1"; D-M=32 1/8"; DUAL_Q=138 3/8"; DUAL_Q+.25"=138 5/8"; E=63 3/4"; E-(NOZZLE_RAD/3*2)=23 11/32"; E-N-N-H=2"; E/2=31 7/8"; E/2-H/2=14 3/16"; E/52*15=18 3/8"; E/52*30=36 25/32"; F=37 3/8"; F/2=18 11/16"; H=35 3/8"; H/2=17 11/16"; HEIGHT=57 27/32"; J=10"; J+K+L=56 5/16"; K=19 1/8"; L=27 3/16"; M=25 3/16"; M-(2*(D-L-K-J))=23 3/16"; MB_A=140 1/8"; MB_F=7 3/4"; MB_F-3"=4 3/4"; MB_HEIGHT=50 3/4"; MB_HEIGHT/2=25 3/8"; MB_N=14 3/16"; MB_N-(D-J-K-L)=13 3/16"; MB_P=46"; MB_P+.25"=46 1/4"; MB_P+MB_P+.5=92 1/2"; MB_P-4.5"=41 1/2"; MB_Q=46"; N=12 3/16"; N+(H/2)=29 7/8"; NOZZLE_BOTTOM_ID=25 5/8"; NOZZLE_BOTTOM_RAD=12 13/16"; NOZZLE_BOTTOM_RAD-3*2=6 13/16"; NOZZLE_HEIGHT=48"; NOZZLE_HEIGHT/7*2=12"; NOZZLE_SIZE=18"; NOZZLE_TOP_OD=27 1/2"; NOZZLE_TOP_RAD=13 3/4"; NOZZLE_WB/4=8 19/32"; NOZZLE_WB_OD=43"; NOZZLE_WB_RAD=21 1/2"; NOZZLE_WB_RAD-2"=19 1/2"; P=60"; R=30"; R*1.1=33"; R+((B/2)+1.5")=48 31/32"; R-((B/2)+1.5")=11 1/32"; RO/2=20 3/4"; RO2/2=113 1/8"; TRANSITION=18 1/8"; TRANSITION/2=9 1/16"; TRIP_Q=230 3/4"; TRIP_Q-4.5"=226 1/4"; Type Comments=Triple Vari-Plume Laboratory Exhaust Centrifugal Airfoil Class 1 Arr 10 With Mixing Box
- Triple_300_CAVP-12L_CLASS_2_With_Mixing_Box: ((M - (2 * (D - L - K - J))) / 2) + (TRANSITION / 2)=17 5/8"; (B/2)+1.5"=18 31/32"; (B/2)-.125"=17 11/32"; (D-J-K-L)*2=2"; (E/2)-((B/2)+1.5")=12 29/32"; (E/2)-((MB_P/2)+.125")=8 3/4"; (E/2)-(E/52*15)=13 1/2"; (F-((F-H)/2))/2=16 11/16"; (M - (2 * (D - L - K - J)))/2=11 19/32"; (MB_P/2)+.125"=23 1/8"; (MB_P/2-.125")+((F / 2) - 2")=-39 9/16"; (MB_P/2-.125")-((F / 2) - 2")=-6 3/16"; (MB_Q/2)+.125"=23 1/8"; (NOZZLE_HEIGHT - (NOZZLE_HEIGHT / 8 * 2)) / 2=12"; (NOZZLE_WB_OD - NOZZLE_TOP_OD) / 4=2 1/8"; -((MB_Q / 2) + 1/8")=-23 1/8"; -(F-((F-H)/2))/2=-16 11/16"; -MB_HEIGHT=-50 3/4"; -MB_P=-46"; -MB_P-.25=-46 1/4"; A=122 7/16"; A/2=61 7/32"; B=34 15/16"; B/2=17 15/32"; B/4=8 3/4"; C=74 15/16"; C/2=37 15/32"; CLASS=2"; D=61 3/16"; D-L-K-J=1"; D-M=36"; DUAL_Q=138 3/8"; DUAL_Q+.25"=138 5/8"; E=63 3/4"; E-(NOZZLE_RAD/3*2)=26 3/16"; E-N-N-H=2"; E/2=31 7/8"; E/2-H/2=14 3/16"; E/52*15=18 3/8"; E/52*30=36 25/32"; F=37 3/8"; F/2=18 11/16"; H=35 3/8"; H/2=17 11/16"; HEIGHT=57 27/32"; J=10"; J+K+L=60 3/16"; K=23"; L=27 3/16"; M=25 3/16"; M-(2*(D-L-K-J))=23 3/16"; MB_A=144"; MB_F=7 3/4"; MB_F-3"=4 3/4"; MB_HEIGHT=50 3/4"; MB_HEIGHT/2=25 3/8"; MB_N=14 3/16"; MB_N-(D-J-K-L)=13 3/16"; MB_P=46"; MB_P+.25"=46 1/4"; MB_P+MB_P+.5=92 1/2"; MB_P-4.5"=41 1/2"; MB_Q=46"; N=12 3/16"; N+(H/2)=29 7/8"; NOZZLE_BOTTOM_ID=17 1/16"; NOZZLE_BOTTOM_RAD=8 17/32"; NOZZLE_BOTTOM_RAD-3*2=2 17/32"; NOZZLE_HEIGHT=32"; NOZZLE_HEIGHT/7*2=8"; NOZZLE_SIZE=12"; NOZZLE_TOP_OD=19 1/2"; NOZZLE_TOP_RAD=9 3/4"; NOZZLE_WB/4=5 19/32"; NOZZLE_WB_OD=28"; NOZZLE_WB_RAD=14"; NOZZLE_WB_RAD-2"=12"; P=18 1/4"; R=30"; R*1.1=33"; R+((B/2)+1.5")=48 31/32"; R-((B/2)+1.5")=11 1/32"; RO/2=20 3/4"; RO2/2=113 1/8"; TRANSITION=12 1/16"; TRANSITION/2=6 1/32"; TRIP_Q=230 3/4"; TRIP_Q-4.5"=226 1/4"; Type Comments=Triple Vari-Plume Laboratory Exhaust Centrifugal Airfoil Class 2 Arr 10 With Mixing Box
- Triple_300_CAVP-12H_CLASS_2_With_Mixing_Box: ((M - (2 * (D - L - K - J))) / 2) + (TRANSITION / 2)=17 5/8"; (B/2)+1.5"=18 31/32"; (B/2)-.125"=17 11/32"; (D-J-K-L)*2=2"; (E/2)-((B/2)+1.5")=12 29/32"; (E/2)-((MB_P/2)+.125")=8 3/4"; (E/2)-(E/52*15)=13 1/2"; (F-((F-H)/2))/2=16 11/16"; (M - (2 * (D - L - K - J)))/2=11 19/32"; (MB_P/2)+.125"=23 1/8"; (MB_P/2-.125")+((F / 2) - 2")=-39 9/16"; (MB_P/2-.125")-((F / 2) - 2")=-6 3/16"; (MB_Q/2)+.125"=23 1/8"; (NOZZLE_HEIGHT - (NOZZLE_HEIGHT / 8 * 2)) / 2=12"; (NOZZLE_WB_OD - NOZZLE_TOP_OD) / 4=2 1/8"; -((MB_Q / 2) + 1/8")=-23 1/8"; -(F-((F-H)/2))/2=-16 11/16"; -MB_HEIGHT=-50 3/4"; -MB_P=-46"; -MB_P-.25=-46 1/4"; A=122 7/16"; A/2=61 7/32"; B=34 15/16"; B/2=17 15/32"; B/4=8 3/4"; C=74 15/16"; C/2=37 15/32"; CLASS=2"; D=61 3/16"; D-L-K-J=1"; D-M=36"; DUAL_Q=138 3/8"; DUAL_Q+.25"=138 5/8"; E=63 3/4"; E-(NOZZLE_RAD/3*2)=26 3/16"; E-N-N-H=2"; E/2=31 7/8"; E/2-H/2=14 3/16"; E/52*15=18 3/8"; E/52*30=36 25/32"; F=37 3/8"; F/2=18 11/16"; H=35 3/8"; H/2=17 11/16"; HEIGHT=57 27/32"; J=10"; J+K+L=60 3/16"; K=23"; L=27 3/16"; M=25 3/16"; M-(2*(D-L-K-J))=23 3/16"; MB_A=144"; MB_F=7 3/4"; MB_F-3"=4 3/4"; MB_HEIGHT=50 3/4"; MB_HEIGHT/2=25 3/8"; MB_N=14 3/16"; MB_N-(D-J-K-L)=13 3/16"; MB_P=46"; MB_P+.25"=46 1/4"; MB_P+MB_P+.5=92 1/2"; MB_P-4.5"=41 1/2"; MB_Q=46"; N=12 3/16"; N+(H/2)=29 7/8"; NOZZLE_BOTTOM_ID=17 1/16"; NOZZLE_BOTTOM_RAD=8 17/32"; NOZZLE_BOTTOM_RAD-3*2=2 17/32"; NOZZLE_HEIGHT=32"; NOZZLE_HEIGHT/7*2=8"; NOZZLE_SIZE=12"; NOZZLE_TOP_OD=19 1/2"; NOZZLE_TOP_RAD=9 3/4"; NOZZLE_WB/4=5 19/32"; NOZZLE_WB_OD=28"; NOZZLE_WB_RAD=14"; NOZZLE_WB_RAD-2"=12"; P=18 1/4"; R=30"; R*1.1=33"; R+((B/2)+1.5")=48 31/32"; R-((B/2)+1.5")=11 1/32"; RO/2=20 3/4"; RO2/2=113 1/8"; TRANSITION=12 1/16"; TRANSITION/2=6 1/32"; TRIP_Q=230 3/4"; TRIP_Q-4.5"=226 1/4"; Type Comments=Triple Vari-Plume Laboratory Exhaust Centrifugal Airfoil Class 2 Arr 10 With Mixing Box
- Triple_300_CAVP-15L_CLASS_2_With_Mixing_Box: ((M - (2 * (D - L - K - J))) / 2) + (TRANSITION / 2)=19 5/32"; (B/2)+1.5"=18 31/32"; (B/2)-.125"=17 11/32"; (D-J-K-L)*2=2"; (E/2)-((B/2)+1.5")=12 29/32"; (E/2)-((MB_P/2)+.125")=8 3/4"; (E/2)-(E/52*15)=13 1/2"; (F-((F-H)/2))/2=16 11/16"; (M - (2 * (D - L - K - J)))/2=11 19/32"; (MB_P/2)+.125"=23 1/8"; (MB_P/2-.125")+((F / 2) - 2")=-39 9/16"; (MB_P/2-.125")-((F / 2) - 2")=-6 3/16"; (MB_Q/2)+.125"=23 1/8"; (NOZZLE_HEIGHT - (NOZZLE_HEIGHT / 8 * 2)) / 2=16 1/8"; (NOZZLE_WB_OD - NOZZLE_TOP_OD) / 4=3 1/4"; -((MB_Q / 2) + 1/8")=-23 1/8"; -(F-((F-H)/2))/2=-16 11/16"; -MB_HEIGHT=-50 3/4"; -MB_P=-46"; -MB_P-.25=-46 1/4"; A=122 7/16"; A/2=61 7/32"; B=34 15/16"; B/2=17 15/32"; B/4=8 3/4"; C=74 15/16"; C/2=37 15/32"; CLASS=2"; D=61 3/16"; D-L-K-J=1"; D-M=36"; DUAL_Q=138 3/8"; DUAL_Q+.25"=138 5/8"; E=63 3/4"; E-(NOZZLE_RAD/3*2)=24 3/4"; E-N-N-H=2"; E/2=31 7/8"; E/2-H/2=14 3/16"; E/52*15=18 3/8"; E/52*30=36 25/32"; F=37 3/8"; F/2=18 11/16"; H=35 3/8"; H/2=17 11/16"; HEIGHT=57 27/32"; J=10"; J+K+L=60 3/16"; K=23"; L=27 3/16"; M=25 3/16"; M-(2*(D-L-K-J))=23 3/16"; MB_A=144"; MB_F=7 3/4"; MB_F-3"=4 3/4"; MB_HEIGHT=50 3/4"; MB_HEIGHT/2=25 3/8"; MB_N=14 3/16"; MB_N-(D-J-K-L)=13 3/16"; MB_P=46"; MB_P+.25"=46 1/4"; MB_P+MB_P+.5=92 1/2"; MB_P-4.5"=41 1/2"; MB_Q=46"; N=12 3/16"; N+(H/2)=29 7/8"; NOZZLE_BOTTOM_ID=21 3/8"; NOZZLE_BOTTOM_RAD=10 11/16"; NOZZLE_BOTTOM_RAD-3*2=4 11/16"; NOZZLE_HEIGHT=43"; NOZZLE_HEIGHT/7*2=10 3/4"; NOZZLE_SIZE=15"; NOZZLE_TOP_OD=23"; NOZZLE_TOP_RAD=11 1/2"; NOZZLE_WB/4=7 3/16"; NOZZLE_WB_OD=36"; NOZZLE_WB_RAD=18"; NOZZLE_WB_RAD-2"=16"; P=18 1/4"; R=30"; R*1.1=33"; R+((B/2)+1.5")=48 31/32"; R-((B/2)+1.5")=11 1/32"; RO/2=20 3/4"; RO2/2=113 1/8"; TRANSITION=15 1/8"; TRANSITION/2=7 9/16"; TRIP_Q=230 3/4"; TRIP_Q-4.5"=226 1/4"; Type Comments=Triple Vari-Plume Laboratory Exhaust Centrifugal Airfoil Class 2 Arr 10 With Mixing Box
- Triple_300_CAVP-15H_CLASS_2_With_Mixing_Box: ((M - (2 * (D - L - K - J))) / 2) + (TRANSITION / 2)=19 5/32"; (B/2)+1.5"=18 31/32"; (B/2)-.125"=17 11/32"; (D-J-K-L)*2=2"; (E/2)-((B/2)+1.5")=12 29/32"; (E/2)-((MB_P/2)+.125")=8 3/4"; (E/2)-(E/52*15)=13 1/2"; (F-((F-H)/2))/2=16 11/16"; (M - (2 * (D - L - K - J)))/2=11 19/32"; (MB_P/2)+.125"=23 1/8"; (MB_P/2-.125")+((F / 2) - 2")=-39 9/16"; (MB_P/2-.125")-((F / 2) - 2")=-6 3/16"; (MB_Q/2)+.125"=23 1/8"; (NOZZLE_HEIGHT - (NOZZLE_HEIGHT / 8 * 2)) / 2=16 1/8"; (NOZZLE_WB_OD - NOZZLE_TOP_OD) / 4=3 1/4"; -((MB_Q / 2) + 1/8")=-23 1/8"; -(F-((F-H)/2))/2=-16 11/16"; -MB_HEIGHT=-50 3/4"; -MB_P=-46"; -MB_P-.25=-46 1/4"; A=122 7/16"; A/2=61 7/32"; B=34 15/16"; B/2=17 15/32"; B/4=8 3/4"; C=74 15/16"; C/2=37 15/32"; CLASS=2"; D=61 3/16"; D-L-K-J=1"; D-M=36"; DUAL_Q=138 3/8"; DUAL_Q+.25"=138 5/8"; E=63 3/4"; E-(NOZZLE_RAD/3*2)=24 3/4"; E-N-N-H=2"; E/2=31 7/8"; E/2-H/2=14 3/16"; E/52*15=18 3/8"; E/52*30=36 25/32"; F=37 3/8"; F/2=18 11/16"; H=35 3/8"; H/2=17 11/16"; HEIGHT=57 27/32"; J=10"; J+K+L=60 3/16"; K=23"; L=27 3/16"; M=25 3/16"; M-(2*(D-L-K-J))=23 3/16"; MB_A=144"; MB_F=7 3/4"; MB_F-3"=4 3/4"; MB_HEIGHT=50 3/4"; MB_HEIGHT/2=25 3/8"; MB_N=14 3/16"; MB_N-(D-J-K-L)=13 3/16"; MB_P=46"; MB_P+.25"=46 1/4"; MB_P+MB_P+.5=92 1/2"; MB_P-4.5"=41 1/2"; MB_Q=46"; N=12 3/16"; N+(H/2)=29 7/8"; NOZZLE_BOTTOM_ID=21 3/8"; NOZZLE_BOTTOM_RAD=10 11/16"; NOZZLE_BOTTOM_RAD-3*2=4 11/16"; NOZZLE_HEIGHT=43"; NOZZLE_HEIGHT/7*2=10 3/4"; NOZZLE_SIZE=15"; NOZZLE_TOP_OD=23"; NOZZLE_TOP_RAD=11 1/2"; NOZZLE_WB/4=7 3/16"; NOZZLE_WB_OD=36"; NOZZLE_WB_RAD=18"; NOZZLE_WB_RAD-2"=16"; P=18 1/4"; R=30"; R*1.1=33"; R+((B/2)+1.5")=48 31/32"; R-((B/2)+1.5")=11 1/32"; RO/2=20 3/4"; RO2/2=113 1/8"; TRANSITION=15 1/8"; TRANSITION/2=7 9/16"; TRIP_Q=230 3/4"; TRIP_Q-4.5"=226 1/4"; Type Comments=Triple Vari-Plume Laboratory Exhaust Centrifugal Airfoil Class 2 Arr 10 With Mixing Box
- Triple_300_CAVP-18L_CLASS_2_With_Mixing_Box: ((M - (2 * (D - L - K - J))) / 2) + (TRANSITION / 2)=20 21/32"; (B/2)+1.5"=18 31/32"; (B/2)-.125"=17 11/32"; (D-J-K-L)*2=2"; (E/2)-((B/2)+1.5")=12 29/32"; (E/2)-((MB_P/2)+.125")=8 3/4"; (E/2)-(E/52*15)=13 1/2"; (F-((F-H)/2))/2=16 11/16"; (M - (2 * (D - L - K - J)))/2=11 19/32"; (MB_P/2)+.125"=23 1/8"; (MB_P/2-.125")+((F / 2) - 2")=-39 9/16"; (MB_P/2-.125")-((F / 2) - 2")=-6 3/16"; (MB_Q/2)+.125"=23 1/8"; (NOZZLE_HEIGHT - (NOZZLE_HEIGHT / 8 * 2)) / 2=18"; (NOZZLE_WB_OD - NOZZLE_TOP_OD) / 4=3 7/8"; -((MB_Q / 2) + 1/8")=-23 1/8"; -(F-((F-H)/2))/2=-16 11/16"; -MB_HEIGHT=-50 3/4"; -MB_P=-46"; -MB_P-.25=-46 1/4"; A=122 7/16"; A/2=61 7/32"; B=34 15/16"; B/2=17 15/32"; B/4=8 3/4"; C=74 15/16"; C/2=37 15/32"; CLASS=2"; D=61 3/16"; D-L-K-J=1"; D-M=36"; DUAL_Q=138 3/8"; DUAL_Q+.25"=138 5/8"; E=63 3/4"; E-(NOZZLE_RAD/3*2)=23 11/32"; E-N-N-H=2"; E/2=31 7/8"; E/2-H/2=14 3/16"; E/52*15=18 3/8"; E/52*30=36 25/32"; F=37 3/8"; F/2=18 11/16"; H=35 3/8"; H/2=17 11/16"; HEIGHT=57 27/32"; J=10"; J+K+L=60 3/16"; K=23"; L=27 3/16"; M=25 3/16"; M-(2*(D-L-K-J))=23 3/16"; MB_A=144"; MB_F=7 3/4"; MB_F-3"=4 3/4"; MB_HEIGHT=50 3/4"; MB_HEIGHT/2=25 3/8"; MB_N=14 3/16"; MB_N-(D-J-K-L)=13 3/16"; MB_P=46"; MB_P+.25"=46 1/4"; MB_P+MB_P+.5=92 1/2"; MB_P-4.5"=41 1/2"; MB_Q=46"; N=12 3/16"; N+(H/2)=29 7/8"; NOZZLE_BOTTOM_ID=25 5/8"; NOZZLE_BOTTOM_RAD=12 13/16"; NOZZLE_BOTTOM_RAD-3*2=6 13/16"; NOZZLE_HEIGHT=48"; NOZZLE_HEIGHT/7*2=12"; NOZZLE_SIZE=18"; NOZZLE_TOP_OD=27 1/2"; NOZZLE_TOP_RAD=13 3/4"; NOZZLE_WB/4=8 19/32"; NOZZLE_WB_OD=43"; NOZZLE_WB_RAD=21 1/2"; NOZZLE_WB_RAD-2"=19 1/2"; P=18 1/4"; R=30"; R*1.1=33"; R+((B/2)+1.5")=48 31/32"; R-((B/2)+1.5")=11 1/32"; RO/2=20 3/4"; RO2/2=113 1/8"; TRANSITION=18 1/8"; TRANSITION/2=9 1/16"; TRIP_Q=230 3/4"; TRIP_Q-4.5"=226 1/4"; Type Comments=Triple Vari-Plume Laboratory Exhaust Centrifugal Airfoil Class 2 Arr 10 With Mixing Box
- Triple_300_CAVP-18H_CLASS_2_With_Mixing_Box: ((M - (2 * (D - L - K - J))) / 2) + (TRANSITION / 2)=20 21/32"; (B/2)+1.5"=18 31/32"; (B/2)-.125"=17 11/32"; (D-J-K-L)*2=2"; (E/2)-((B/2)+1.5")=12 29/32"; (E/2)-((MB_P/2)+.125")=8 3/4"; (E/2)-(E/52*15)=13 1/2"; (F-((F-H)/2))/2=16 11/16"; (M - (2 * (D - L - K - J)))/2=11 19/32"; (MB_P/2)+.125"=23 1/8"; (MB_P/2-.125")+((F / 2) - 2")=-39 9/16"; (MB_P/2-.125")-((F / 2) - 2")=-6 3/16"; (MB_Q/2)+.125"=23 1/8"; (NOZZLE_HEIGHT - (NOZZLE_HEIGHT / 8 * 2)) / 2=18"; (NOZZLE_WB_OD - NOZZLE_TOP_OD) / 4=3 7/8"; -((MB_Q / 2) + 1/8")=-23 1/8"; -(F-((F-H)/2))/2=-16 11/16"; -MB_HEIGHT=-50 3/4"; -MB_P=-46"; -MB_P-.25=-46 1/4"; A=122 7/16"; A/2=61 7/32"; B=34 15/16"; B/2=17 15/32"; B/4=8 3/4"; C=74 15/16"; C/2=37 15/32"; CLASS=2"; D=61 3/16"; D-L-K-J=1"; D-M=36"; DUAL_Q=138 3/8"; DUAL_Q+.25"=138 5/8"; E=63 3/4"; E-(NOZZLE_RAD/3*2)=23 11/32"; E-N-N-H=2"; E/2=31 7/8"; E/2-H/2=14 3/16"; E/52*15=18 3/8"; E/52*30=36 25/32"; F=37 3/8"; F/2=18 11/16"; H=35 3/8"; H/2=17 11/16"; HEIGHT=57 27/32"; J=10"; J+K+L=60 3/16"; K=23"; L=27 3/16"; M=25 3/16"; M-(2*(D-L-K-J))=23 3/16"; MB_A=144"; MB_F=7 3/4"; MB_F-3"=4 3/4"; MB_HEIGHT=50 3/4"; MB_HEIGHT/2=25 3/8"; MB_N=14 3/16"; MB_N-(D-J-K-L)=13 3/16"; MB_P=46"; MB_P+.25"=46 1/4"; MB_P+MB_P+.5=92 1/2"; MB_P-4.5"=41 1/2"; MB_Q=46"; N=12 3/16"; N+(H/2)=29 7/8"; NOZZLE_BOTTOM_ID=25 5/8"; NOZZLE_BOTTOM_RAD=12 13/16"; NOZZLE_BOTTOM_RAD-3*2=6 13/16"; NOZZLE_HEIGHT=48"; NOZZLE_HEIGHT/7*2=12"; NOZZLE_SIZE=18"; NOZZLE_TOP_OD=27 1/2"; NOZZLE_TOP_RAD=13 3/4"; NOZZLE_WB/4=8 19/32"; NOZZLE_WB_OD=43"; NOZZLE_WB_RAD=21 1/2"; NOZZLE_WB_RAD-2"=19 1/2"; P=18 1/4"; R=30"; R*1.1=33"; R+((B/2)+1.5")=48 31/32"; R-((B/2)+1.5")=11 1/32"; RO/2=20 3/4"; RO2/2=113 1/8"; TRANSITION=18 1/8"; TRANSITION/2=9 1/16"; TRIP_Q=230 3/4"; TRIP_Q-4.5"=226 1/4"; Type Comments=Triple Vari-Plume Laboratory Exhaust Centrifugal Airfoil Class 2 Arr 10 With Mixing Box
- Triple_330_CAVP-15L_CLASS_1_With_Mixing_Box: ((M - (2 * (D - L - K - J))) / 2) + (TRANSITION / 2)=20 5/16"; (B/2)+1.5"=20 15/32"; (B/2)-.125"=18 27/32"; (D-J-K-L)*2=2"; (E/2)-((B/2)+1.5")=14 1/2"; (E/2)-((MB_P/2)+.125")=10 11/32"; (E/2)-(E/52*15)=14 25/32"; (F-((F-H)/2))/2=18 3/16"; (M - (2 * (D - L - K - J)))/2=12 3/4"; (MB_P/2)+.125"=24 5/8"; (MB_P/2-.125")+((F / 2) - 2")=-42 9/16"; (MB_P/2-.125")-((F / 2) - 2")=-6 3/16"; (MB_Q/2)+.125"=24 5/8"; (NOZZLE_HEIGHT - (NOZZLE_HEIGHT / 8 * 2)) / 2=16 1/8"; (NOZZLE_WB_OD - NOZZLE_TOP_OD) / 4=3 1/4"; -((MB_Q / 2) + 1/8")=-24 5/8"; -(F-((F-H)/2))/2=-18 3/16"; -MB_HEIGHT=-53 3/4"; -MB_P=-49"; -MB_P-.25=-49 1/4"; A=144 7/16"; A/2=72 7/32"; B=37 15/16"; B/2=18 31/32"; B/4=9 1/2"; C=82 13/16"; C/2=41 13/32"; CLASS=1"; D=60 1/4"; D-L-K-J=1"; D-M=32 3/4"; DUAL_Q=147 3/8"; DUAL_Q+.25"=147 5/8"; E=69 15/16"; E-(NOZZLE_RAD/3*2)=27 27/32"; E-N-N-H=2"; E/2=34 31/32"; E/2-H/2=15 25/32"; E/52*15=20 3/16"; E/52*30=40 11/32"; F=40 3/8"; F/2=20 3/16"; H=38 3/8"; H/2=19 3/16"; HEIGHT=63 17/32"; J=10 1/2"; J+K+L=59 1/4"; K=19 1/4"; L=29 1/2"; M=27 1/2"; M-(2*(D-L-K-J))=25 1/2"; MB_A=148 1/16"; MB_F=9 1/4"; MB_F-3"=6 1/4"; MB_HEIGHT=53 3/4"; MB_HEIGHT/2=26 7/8"; MB_N=14 3/16"; MB_N-(D-J-K-L)=13 3/16"; MB_P=49"; MB_P+.25"=49 1/4"; MB_P+MB_P+.5=98 1/2"; MB_P-4.5"=44 1/2"; MB_Q=49"; N=13 25/32"; N+(H/2)=32 31/32"; NOZZLE_BOTTOM_ID=21 3/8"; NOZZLE_BOTTOM_RAD=10 11/16"; NOZZLE_BOTTOM_RAD-3*2=4 11/16"; NOZZLE_HEIGHT=43"; NOZZLE_HEIGHT/7*2=10 3/4"; NOZZLE_SIZE=15"; NOZZLE_TOP_OD=23"; NOZZLE_TOP_RAD=11 1/2"; NOZZLE_WB/4=7 3/16"; NOZZLE_WB_OD=36"; NOZZLE_WB_RAD=18"; NOZZLE_WB_RAD-2"=16"; P=60"; R=33"; R*1.1=36 5/16"; R+((B/2)+1.5")=53 15/32"; R-((B/2)+1.5")=12 17/32"; RO/2=22 1/4"; RO2/2=120 5/8"; TRANSITION=15 1/8"; TRANSITION/2=7 9/16"; TRIP_Q=245 3/4"; TRIP_Q-4.5"=241 1/4"; Type Comments=Triple Vari-Plume Laboratory Exhaust Centrifugal Airfoil Class 1 Arr 10 With Mixing Box
- Triple_330_CAVP-15H_CLASS_1_With_Mixing_Box: ((M - (2 * (D - L - K - J))) / 2) + (TRANSITION / 2)=20 5/16"; (B/2)+1.5"=20 15/32"; (B/2)-.125"=18 27/32"; (D-J-K-L)*2=2"; (E/2)-((B/2)+1.5")=14 1/2"; (E/2)-((MB_P/2)+.125")=10 11/32"; (E/2)-(E/52*15)=14 25/32"; (F-((F-H)/2))/2=18 3/16"; (M - (2 * (D - L - K - J)))/2=12 3/4"; (MB_P/2)+.125"=24 5/8"; (MB_P/2-.125")+((F / 2) - 2")=-42 9/16"; (MB_P/2-.125")-((F / 2) - 2")=-6 3/16"; (MB_Q/2)+.125"=24 5/8"; (NOZZLE_HEIGHT - (NOZZLE_HEIGHT / 8 * 2)) / 2=16 1/8"; (NOZZLE_WB_OD - NOZZLE_TOP_OD) / 4=3 1/4"; -((MB_Q / 2) + 1/8")=-24 5/8"; -(F-((F-H)/2))/2=-18 3/16"; -MB_HEIGHT=-53 3/4"; -MB_P=-49"; -MB_P-.25=-49 1/4"; A=144 7/16"; A/2=72 7/32"; B=37 15/16"; B/2=18 31/32"; B/4=9 1/2"; C=82 13/16"; C/2=41 13/32"; CLASS=1"; D=60 1/4"; D-L-K-J=1"; D-M=32 3/4"; DUAL_Q=147 3/8"; DUAL_Q+.25"=147 5/8"; E=69 15/16"; E-(NOZZLE_RAD/3*2)=27 27/32"; E-N-N-H=2"; E/2=34 31/32"; E/2-H/2=15 25/32"; E/52*15=20 3/16"; E/52*30=40 11/32"; F=40 3/8"; F/2=20 3/16"; H=38 3/8"; H/2=19 3/16"; HEIGHT=63 17/32"; J=10 1/2"; J+K+L=59 1/4"; K=19 1/4"; L=29 1/2"; M=27 1/2"; M-(2*(D-L-K-J))=25 1/2"; MB_A=148 1/16"; MB_F=9 1/4"; MB_F-3"=6 1/4"; MB_HEIGHT=53 3/4"; MB_HEIGHT/2=26 7/8"; MB_N=14 3/16"; MB_N-(D-J-K-L)=13 3/16"; MB_P=49"; MB_P+.25"=49 1/4"; MB_P+MB_P+.5=98 1/2"; MB_P-4.5"=44 1/2"; MB_Q=49"; N=13 25/32"; N+(H/2)=32 31/32"; NOZZLE_BOTTOM_ID=21 3/8"; NOZZLE_BOTTOM_RAD=10 11/16"; NOZZLE_BOTTOM_RAD-3*2=4 11/16"; NOZZLE_HEIGHT=43"; NOZZLE_HEIGHT/7*2=10 3/4"; NOZZLE_SIZE=15"; NOZZLE_TOP_OD=23"; NOZZLE_TOP_RAD=11 1/2"; NOZZLE_WB/4=7 3/16"; NOZZLE_WB_OD=36"; NOZZLE_WB_RAD=18"; NOZZLE_WB_RAD-2"=16"; P=60"; R=33"; R*1.1=36 5/16"; R+((B/2)+1.5")=53 15/32"; R-((B/2)+1.5")=12 17/32"; RO/2=22 1/4"; RO2/2=120 5/8"; TRANSITION=15 1/8"; TRANSITION/2=7 9/16"; TRIP_Q=245 3/4"; TRIP_Q-4.5"=241 1/4"; Type Comments=Triple Vari-Plume Laboratory Exhaust Centrifugal Airfoil Class 1 Arr 10 With Mixing Box
- Triple_330_CAVP-18L_CLASS_1_With_Mixing_Box: ((M - (2 * (D - L - K - J))) / 2) + (TRANSITION / 2)=21 13/16"; (B/2)+1.5"=20 15/32"; (B/2)-.125"=18 27/32"; (D-J-K-L)*2=2"; (E/2)-((B/2)+1.5")=14 1/2"; (E/2)-((MB_P/2)+.125")=10 11/32"; (E/2)-(E/52*15)=14 25/32"; (F-((F-H)/2))/2=18 3/16"; (M - (2 * (D - L - K - J)))/2=12 3/4"; (MB_P/2)+.125"=24 5/8"; (MB_P/2-.125")+((F / 2) - 2")=-42 9/16"; (MB_P/2-.125")-((F / 2) - 2")=-6 3/16"; (MB_Q/2)+.125"=24 5/8"; (NOZZLE_HEIGHT - (NOZZLE_HEIGHT / 8 * 2)) / 2=18"; (NOZZLE_WB_OD - NOZZLE_TOP_OD) / 4=3 7/8"; -((MB_Q / 2) + 1/8")=-24 5/8"; -(F-((F-H)/2))/2=-18 3/16"; -MB_HEIGHT=-53 3/4"; -MB_P=-49"; -MB_P-.25=-49 1/4"; A=144 7/16"; A/2=72 7/32"; B=37 15/16"; B/2=18 31/32"; B/4=9 1/2"; C=82 13/16"; C/2=41 13/32"; CLASS=1"; D=60 1/4"; D-L-K-J=1"; D-M=32 3/4"; DUAL_Q=147 3/8"; DUAL_Q+.25"=147 5/8"; E=69 15/16"; E-(NOZZLE_RAD/3*2)=26 7/16"; E-N-N-H=2"; E/2=34 31/32"; E/2-H/2=15 25/32"; E/52*15=20 3/16"; E/52*30=40 11/32"; F=40 3/8"; F/2=20 3/16"; H=38 3/8"; H/2=19 3/16"; HEIGHT=63 17/32"; J=10 1/2"; J+K+L=59 1/4"; K=19 1/4"; L=29 1/2"; M=27 1/2"; M-(2*(D-L-K-J))=25 1/2"; MB_A=148 1/16"; MB_F=9 1/4"; MB_F-3"=6 1/4"; MB_HEIGHT=53 3/4"; MB_HEIGHT/2=26 7/8"; MB_N=14 3/16"; MB_N-(D-J-K-L)=13 3/16"; MB_P=49"; MB_P+.25"=49 1/4"; MB_P+MB_P+.5=98 1/2"; MB_P-4.5"=44 1/2"; MB_Q=49"; N=13 25/32"; N+(H/2)=32 31/32"; NOZZLE_BOTTOM_ID=25 5/8"; NOZZLE_BOTTOM_RAD=12 13/16"; NOZZLE_BOTTOM_RAD-3*2=6 13/16"; NOZZLE_HEIGHT=48"; NOZZLE_HEIGHT/7*2=12"; NOZZLE_SIZE=18"; NOZZLE_TOP_OD=27 1/2"; NOZZLE_TOP_RAD=13 3/4"; NOZZLE_WB/4=8 19/32"; NOZZLE_WB_OD=43"; NOZZLE_WB_RAD=21 1/2"; NOZZLE_WB_RAD-2"=19 1/2"; P=60"; R=33"; R*1.1=36 5/16"; R+((B/2)+1.5")=53 15/32"; R-((B/2)+1.5")=12 17/32"; RO/2=22 1/4"; RO2/2=120 5/8"; TRANSITION=18 1/8"; TRANSITION/2=9 1/16"; TRIP_Q=245 3/4"; TRIP_Q-4.5"=241 1/4"; Type Comments=Triple Vari-Plume Laboratory Exhaust Centrifugal Airfoil Class 1 Arr 10 With Mixing Box
- Triple_330_CAVP-18H_CLASS_1_With_Mixing_Box: ((M - (2 * (D - L - K - J))) / 2) + (TRANSITION / 2)=21 13/16"; (B/2)+1.5"=20 15/32"; (B/2)-.125"=18 27/32"; (D-J-K-L)*2=2"; (E/2)-((B/2)+1.5")=14 1/2"; (E/2)-((MB_P/2)+.125")=10 11/32"; (E/2)-(E/52*15)=14 25/32"; (F-((F-H)/2))/2=18 3/16"; (M - (2 * (D - L - K - J)))/2=12 3/4"; (MB_P/2)+.125"=24 5/8"; (MB_P/2-.125")+((F / 2) - 2")=-42 9/16"; (MB_P/2-.125")-((F / 2) - 2")=-6 3/16"; (MB_Q/2)+.125"=24 5/8"; (NOZZLE_HEIGHT - (NOZZLE_HEIGHT / 8 * 2)) / 2=18"; (NOZZLE_WB_OD - NOZZLE_TOP_OD) / 4=3 7/8"; -((MB_Q / 2) + 1/8")=-24 5/8"; -(F-((F-H)/2))/2=-18 3/16"; -MB_HEIGHT=-53 3/4"; -MB_P=-49"; -MB_P-.25=-49 1/4"; A=144 7/16"; A/2=72 7/32"; B=37 15/16"; B/2=18 31/32"; B/4=9 1/2"; C=82 13/16"; C/2=41 13/32"; CLASS=1"; D=60 1/4"; D-L-K-J=1"; D-M=32 3/4"; DUAL_Q=147 3/8"; DUAL_Q+.25"=147 5/8"; E=69 15/16"; E-(NOZZLE_RAD/3*2)=26 7/16"; E-N-N-H=2"; E/2=34 31/32"; E/2-H/2=15 25/32"; E/52*15=20 3/16"; E/52*30=40 11/32"; F=40 3/8"; F/2=20 3/16"; H=38 3/8"; H/2=19 3/16"; HEIGHT=63 17/32"; J=10 1/2"; J+K+L=59 1/4"; K=19 1/4"; L=29 1/2"; M=27 1/2"; M-(2*(D-L-K-J))=25 1/2"; MB_A=148 1/16"; MB_F=9 1/4"; MB_F-3"=6 1/4"; MB_HEIGHT=53 3/4"; MB_HEIGHT/2=26 7/8"; MB_N=14 3/16"; MB_N-(D-J-K-L)=13 3/16"; MB_P=49"; MB_P+.25"=49 1/4"; MB_P+MB_P+.5=98 1/2"; MB_P-4.5"=44 1/2"; MB_Q=49"; N=13 25/32"; N+(H/2)=32 31/32"; NOZZLE_BOTTOM_ID=25 5/8"; NOZZLE_BOTTOM_RAD=12 13/16"; NOZZLE_BOTTOM_RAD-3*2=6 13/16"; NOZZLE_HEIGHT=48"; NOZZLE_HEIGHT/7*2=12"; NOZZLE_SIZE=18"; NOZZLE_TOP_OD=27 1/2"; NOZZLE_TOP_RAD=13 3/4"; NOZZLE_WB/4=8 19/32"; NOZZLE_WB_OD=43"; NOZZLE_WB_RAD=21 1/2"; NOZZLE_WB_RAD-2"=19 1/2"; P=60"; R=33"; R*1.1=36 5/16"; R+((B/2)+1.5")=53 15/32"; R-((B/2)+1.5")=12 17/32"; RO/2=22 1/4"; RO2/2=120 5/8"; TRANSITION=18 1/8"; TRANSITION/2=9 1/16"; TRIP_Q=245 3/4"; TRIP_Q-4.5"=241 1/4"; Type Comments=Triple Vari-Plume Laboratory Exhaust Centrifugal Airfoil Class 1 Arr 10 With Mixing Box
- Triple_330_CAVP-24L_CLASS_1_With_Mixing_Box: ((M - (2 * (D - L - K - J))) / 2) + (TRANSITION / 2)=25 1/32"; (B/2)+1.5"=20 15/32"; (B/2)-.125"=18 27/32"; (D-J-K-L)*2=2"; (E/2)-((B/2)+1.5")=14 1/2"; (E/2)-((MB_P/2)+.125")=10 11/32"; (E/2)-(E/52*15)=14 25/32"; (F-((F-H)/2))/2=18 3/16"; (M - (2 * (D - L - K - J)))/2=12 3/4"; (MB_P/2)+.125"=24 5/8"; (MB_P/2-.125")+((F / 2) - 2")=-42 9/16"; (MB_P/2-.125")-((F / 2) - 2")=-6 3/16"; (MB_Q/2)+.125"=24 5/8"; (NOZZLE_HEIGHT - (NOZZLE_HEIGHT / 8 * 2)) / 2=23 1/4"; (NOZZLE_WB_OD - NOZZLE_TOP_OD) / 4=6 1/8"; -((MB_Q / 2) + 1/8")=-24 5/8"; -(F-((F-H)/2))/2=-18 3/16"; -MB_HEIGHT=-53 3/4"; -MB_P=-49"; -MB_P-.25=-49 1/4"; A=144 7/16"; A/2=72 7/32"; B=37 15/16"; B/2=18 31/32"; B/4=9 1/2"; C=82 13/16"; C/2=41 13/32"; CLASS=1"; D=60 1/4"; D-L-K-J=1"; D-M=32 3/4"; DUAL_Q=147 3/8"; DUAL_Q+.25"=147 5/8"; E=69 15/16"; E-(NOZZLE_RAD/3*2)=23 3/8"; E-N-N-H=2"; E/2=34 31/32"; E/2-H/2=15 25/32"; E/52*15=20 3/16"; E/52*30=40 11/32"; F=40 3/8"; F/2=20 3/16"; H=38 3/8"; H/2=19 3/16"; HEIGHT=63 17/32"; J=10 1/2"; J+K+L=59 1/4"; K=19 1/4"; L=29 1/2"; M=27 1/2"; M-(2*(D-L-K-J))=25 1/2"; MB_A=148 1/16"; MB_F=9 1/4"; MB_F-3"=6 1/4"; MB_HEIGHT=53 3/4"; MB_HEIGHT/2=26 7/8"; MB_N=14 3/16"; MB_N-(D-J-K-L)=13 3/16"; MB_P=49"; MB_P+.25"=49 1/4"; MB_P+MB_P+.5=98 1/2"; MB_P-4.5"=44 1/2"; MB_Q=49"; N=13 25/32"; N+(H/2)=32 31/32"; NOZZLE_BOTTOM_ID=34 3/4"; NOZZLE_BOTTOM_RAD=17 3/8"; NOZZLE_BOTTOM_RAD-3*2=11 3/8"; NOZZLE_HEIGHT=62"; NOZZLE_HEIGHT/7*2=15 1/2"; NOZZLE_SIZE=24"; NOZZLE_TOP_OD=36 1/2"; NOZZLE_TOP_RAD=18 1/4"; NOZZLE_WB/4=12 3/16"; NOZZLE_WB_OD=61"; NOZZLE_WB_RAD=30 1/2"; NOZZLE_WB_RAD-2"=28 1/2"; P=60"; R=33"; R*1.1=36 5/16"; R+((B/2)+1.5")=53 15/32"; R-((B/2)+1.5")=12 17/32"; RO/2=22 1/4"; RO2/2=120 5/8"; TRANSITION=24 9/16"; TRANSITION/2=12 9/32"; TRIP_Q=245 3/4"; TRIP_Q-4.5"=241 1/4"; Type Comments=Triple Vari-Plume Laboratory Exhaust Centrifugal Airfoil Class 1 Arr 10 With Mixing Box
- Triple_330_CAVP-24H_CLASS_1_With_Mixing_Box: ((M - (2 * (D - L - K - J))) / 2) + (TRANSITION / 2)=25 1/32"; (B/2)+1.5"=20 15/32"; (B/2)-.125"=18 27/32"; (D-J-K-L)*2=2"; (E/2)-((B/2)+1.5")=14 1/2"; (E/2)-((MB_P/2)+.125")=10 11/32"; (E/2)-(E/52*15)=14 25/32"; (F-((F-H)/2))/2=18 3/16"; (M - (2 * (D - L - K - J)))/2=12 3/4"; (MB_P/2)+.125"=24 5/8"; (MB_P/2-.125")+((F / 2) - 2")=-42 9/16"; (MB_P/2-.125")-((F / 2) - 2")=-6 3/16"; (MB_Q/2)+.125"=24 5/8"; (NOZZLE_HEIGHT - (NOZZLE_HEIGHT / 8 * 2)) / 2=23 1/4"; (NOZZLE_WB_OD - NOZZLE_TOP_OD) / 4=6 1/8"; -((MB_Q / 2) + 1/8")=-24 5/8"; -(F-((F-H)/2))/2=-18 3/16"; -MB_HEIGHT=-53 3/4"; -MB_P=-49"; -MB_P-.25=-49 1/4"; A=144 7/16"; A/2=72 7/32"; B=37 15/16"; B/2=18 31/32"; B/4=9 1/2"; C=82 13/16"; C/2=41 13/32"; CLASS=1"; D=60 1/4"; D-L-K-J=1"; D-M=32 3/4"; DUAL_Q=147 3/8"; DUAL_Q+.25"=147 5/8"; E=69 15/16"; E-(NOZZLE_RAD/3*2)=23 3/8"; E-N-N-H=2"; E/2=34 31/32"; E/2-H/2=15 25/32"; E/52*15=20 3/16"; E/52*30=40 11/32"; F=40 3/8"; F/2=20 3/16"; H=38 3/8"; H/2=19 3/16"; HEIGHT=63 17/32"; J=10 1/2"; J+K+L=59 1/4"; K=19 1/4"; L=29 1/2"; M=27 1/2"; M-(2*(D-L-K-J))=25 1/2"; MB_A=148 1/16"; MB_F=9 1/4"; MB_F-3"=6 1/4"; MB_HEIGHT=53 3/4"; MB_HEIGHT/2=26 7/8"; MB_N=14 3/16"; MB_N-(D-J-K-L)=13 3/16"; MB_P=49"; MB_P+.25"=49 1/4"; MB_P+MB_P+.5=98 1/2"; MB_P-4.5"=44 1/2"; MB_Q=49"; N=13 25/32"; N+(H/2)=32 31/32"; NOZZLE_BOTTOM_ID=34 3/4"; NOZZLE_BOTTOM_RAD=17 3/8"; NOZZLE_BOTTOM_RAD-3*2=11 3/8"; NOZZLE_HEIGHT=62"; NOZZLE_HEIGHT/7*2=15 1/2"; NOZZLE_SIZE=24"; NOZZLE_TOP_OD=36 1/2"; NOZZLE_TOP_RAD=18 1/4"; NOZZLE_WB/4=12 3/16"; NOZZLE_WB_OD=61"; NOZZLE_WB_RAD=30 1/2"; NOZZLE_WB_RAD-2"=28 1/2"; P=60"; R=33"; R*1.1=36 5/16"; R+((B/2)+1.5")=53 15/32"; R-((B/2)+1.5")=12 17/32"; RO/2=22 1/4"; RO2/2=120 5/8"; TRANSITION=24 9/16"; TRANSITION/2=12 9/32"; TRIP_Q=245 3/4"; TRIP_Q-4.5"=241 1/4"; Type Comments=Triple Vari-Plume Laboratory Exhaust Centrifugal Airfoil Class 1 Arr 10 With Mixing Box
- Triple_330_CAVP-15L_CLASS_2_With_Mixing_Box: ((M - (2 * (D - L - K - J))) / 2) + (TRANSITION / 2)=20 5/16"; (B/2)+1.5"=20 15/32"; (B/2)-.125"=18 27/32"; (D-J-K-L)*2=2"; (E/2)-((B/2)+1.5")=14 1/2"; (E/2)-((MB_P/2)+.125")=10 11/32"; (E/2)-(E/52*15)=14 25/32"; (F-((F-H)/2))/2=18 3/16"; (M - (2 * (D - L - K - J)))/2=12 3/4"; (MB_P/2)+.125"=24 5/8"; (MB_P/2-.125")+((F / 2) - 2")=-42 9/16"; (MB_P/2-.125")-((F / 2) - 2")=-6 3/16"; (MB_Q/2)+.125"=24 5/8"; (NOZZLE_HEIGHT - (NOZZLE_HEIGHT / 8 * 2)) / 2=16 1/8"; (NOZZLE_WB_OD - NOZZLE_TOP_OD) / 4=3 1/4"; -((MB_Q / 2) + 1/8")=-24 5/8"; -(F-((F-H)/2))/2=-18 3/16"; -MB_HEIGHT=-53 3/4"; -MB_P=-49"; -MB_P-.25=-49 1/4"; A=144 7/16"; A/2=72 7/32"; B=37 15/16"; B/2=18 31/32"; B/4=9 1/2"; C=82 13/16"; C/2=41 13/32"; CLASS=2"; D=64"; D-L-K-J=1"; D-M=36 1/2"; DUAL_Q=147 3/8"; DUAL_Q+.25"=147 5/8"; E=69 15/16"; E-(NOZZLE_RAD/3*2)=27 27/32"; E-N-N-H=2"; E/2=34 31/32"; E/2-H/2=15 25/32"; E/52*15=20 3/16"; E/52*30=40 11/32"; F=40 3/8"; F/2=20 3/16"; H=38 3/8"; H/2=19 3/16"; HEIGHT=63 17/32"; J=10 1/2"; J+K+L=63"; K=23"; L=29 1/2"; M=27 1/2"; M-(2*(D-L-K-J))=25 1/2"; MB_A=151 13/16"; MB_F=9 1/4"; MB_F-3"=6 1/4"; MB_HEIGHT=53 3/4"; MB_HEIGHT/2=26 7/8"; MB_N=14 3/16"; MB_N-(D-J-K-L)=13 3/16"; MB_P=49"; MB_P+.25"=49 1/4"; MB_P+MB_P+.5=98 1/2"; MB_P-4.5"=44 1/2"; MB_Q=49"; N=13 25/32"; N+(H/2)=32 31/32"; NOZZLE_BOTTOM_ID=21 3/8"; NOZZLE_BOTTOM_RAD=10 11/16"; NOZZLE_BOTTOM_RAD-3*2=4 11/16"; NOZZLE_HEIGHT=43"; NOZZLE_HEIGHT/7*2=10 3/4"; NOZZLE_SIZE=15"; NOZZLE_TOP_OD=23"; NOZZLE_TOP_RAD=11 1/2"; NOZZLE_WB/4=7 3/16"; NOZZLE_WB_OD=36"; NOZZLE_WB_RAD=18"; NOZZLE_WB_RAD-2"=16"; P=60"; R=33"; R*1.1=36 5/16"; R+((B/2)+1.5")=53 15/32"; R-((B/2)+1.5")=12 17/32"; RO/2=22 1/4"; RO2/2=120 5/8"; TRANSITION=15 1/8"; TRANSITION/2=7 9/16"; TRIP_Q=245 3/4"; TRIP_Q-4.5"=241 1/4"; Type Comments=Triple Vari-Plume Laboratory Exhaust Centrifugal Airfoil Class 2 Arr 10 With Mixing Box
- Triple_330_CAVP-15H_CLASS_2_With_Mixing_Box: ((M - (2 * (D - L - K - J))) / 2) + (TRANSITION / 2)=20 5/16"; (B/2)+1.5"=20 15/32"; (B/2)-.125"=18 27/32"; (D-J-K-L)*2=2"; (E/2)-((B/2)+1.5")=14 1/2"; (E/2)-((MB_P/2)+.125")=10 11/32"; (E/2)-(E/52*15)=14 25/32"; (F-((F-H)/2))/2=18 3/16"; (M - (2 * (D - L - K - J)))/2=12 3/4"; (MB_P/2)+.125"=24 5/8"; (MB_P/2-.125")+((F / 2) - 2")=-42 9/16"; (MB_P/2-.125")-((F / 2) - 2")=-6 3/16"; (MB_Q/2)+.125"=24 5/8"; (NOZZLE_HEIGHT - (NOZZLE_HEIGHT / 8 * 2)) / 2=16 1/8"; (NOZZLE_WB_OD - NOZZLE_TOP_OD) / 4=3 1/4"; -((MB_Q / 2) + 1/8")=-24 5/8"; -(F-((F-H)/2))/2=-18 3/16"; -MB_HEIGHT=-53 3/4"; -MB_P=-49"; -MB_P-.25=-49 1/4"; A=144 7/16"; A/2=72 7/32"; B=37 15/16"; B/2=18 31/32"; B/4=9 1/2"; C=82 13/16"; C/2=41 13/32"; CLASS=2"; D=64"; D-L-K-J=1"; D-M=36 1/2"; DUAL_Q=147 3/8"; DUAL_Q+.25"=147 5/8"; E=69 15/16"; E-(NOZZLE_RAD/3*2)=27 27/32"; E-N-N-H=2"; E/2=34 31/32"; E/2-H/2=15 25/32"; E/52*15=20 3/16"; E/52*30=40 11/32"; F=40 3/8"; F/2=20 3/16"; H=38 3/8"; H/2=19 3/16"; HEIGHT=63 17/32"; J=10 1/2"; J+K+L=63"; K=23"; L=29 1/2"; M=27 1/2"; M-(2*(D-L-K-J))=25 1/2"; MB_A=151 13/16"; MB_F=9 1/4"; MB_F-3"=6 1/4"; MB_HEIGHT=53 3/4"; MB_HEIGHT/2=26 7/8"; MB_N=14 3/16"; MB_N-(D-J-K-L)=13 3/16"; MB_P=49"; MB_P+.25"=49 1/4"; MB_P+MB_P+.5=98 1/2"; MB_P-4.5"=44 1/2"; MB_Q=49"; N=13 25/32"; N+(H/2)=32 31/32"; NOZZLE_BOTTOM_ID=21 3/8"; NOZZLE_BOTTOM_RAD=10 11/16"; NOZZLE_BOTTOM_RAD-3*2=4 11/16"; NOZZLE_HEIGHT=43"; NOZZLE_HEIGHT/7*2=10 3/4"; NOZZLE_SIZE=15"; NOZZLE_TOP_OD=23"; NOZZLE_TOP_RAD=11 1/2"; NOZZLE_WB/4=7 3/16"; NOZZLE_WB_OD=36"; NOZZLE_WB_RAD=18"; NOZZLE_WB_RAD-2"=16"; P=60"; R=33"; R*1.1=36 5/16"; R+((B/2)+1.5")=53 15/32"; R-((B/2)+1.5")=12 17/32"; RO/2=22 1/4"; RO2/2=120 5/8"; TRANSITION=15 1/8"; TRANSITION/2=7 9/16"; TRIP_Q=245 3/4"; TRIP_Q-4.5"=241 1/4"; Type Comments=Triple Vari-Plume Laboratory Exhaust Centrifugal Airfoil Class 2 Arr 10 With Mixing Box
- Triple_330_CAVP-18L_CLASS_2_With_Mixing_Box: ((M - (2 * (D - L - K - J))) / 2) + (TRANSITION / 2)=21 13/16"; (B/2)+1.5"=20 15/32"; (B/2)-.125"=18 27/32"; (D-J-K-L)*2=2"; (E/2)-((B/2)+1.5")=14 1/2"; (E/2)-((MB_P/2)+.125")=10 11/32"; (E/2)-(E/52*15)=14 25/32"; (F-((F-H)/2))/2=18 3/16"; (M - (2 * (D - L - K - J)))/2=12 3/4"; (MB_P/2)+.125"=24 5/8"; (MB_P/2-.125")+((F / 2) - 2")=-42 9/16"; (MB_P/2-.125")-((F / 2) - 2")=-6 3/16"; (MB_Q/2)+.125"=24 5/8"; (NOZZLE_HEIGHT - (NOZZLE_HEIGHT / 8 * 2)) / 2=18"; (NOZZLE_WB_OD - NOZZLE_TOP_OD) / 4=3 7/8"; -((MB_Q / 2) + 1/8")=-24 5/8"; -(F-((F-H)/2))/2=-18 3/16"; -MB_HEIGHT=-53 3/4"; -MB_P=-49"; -MB_P-.25=-49 1/4"; A=144 7/16"; A/2=72 7/32"; B=37 15/16"; B/2=18 31/32"; B/4=9 1/2"; C=82 13/16"; C/2=41 13/32"; CLASS=2"; D=64"; D-L-K-J=1"; D-M=36 1/2"; DUAL_Q=147 3/8"; DUAL_Q+.25"=147 5/8"; E=69 15/16"; E-(NOZZLE_RAD/3*2)=26 7/16"; E-N-N-H=2"; E/2=34 31/32"; E/2-H/2=15 25/32"; E/52*15=20 3/16"; E/52*30=40 11/32"; F=40 3/8"; F/2=20 3/16"; H=38 3/8"; H/2=19 3/16"; HEIGHT=63 17/32"; J=10 1/2"; J+K+L=63"; K=23"; L=29 1/2"; M=27 1/2"; M-(2*(D-L-K-J))=25 1/2"; MB_A=151 13/16"; MB_F=9 1/4"; MB_F-3"=6 1/4"; MB_HEIGHT=53 3/4"; MB_HEIGHT/2=26 7/8"; MB_N=14 3/16"; MB_N-(D-J-K-L)=13 3/16"; MB_P=49"; MB_P+.25"=49 1/4"; MB_P+MB_P+.5=98 1/2"; MB_P-4.5"=44 1/2"; MB_Q=49"; N=13 25/32"; N+(H/2)=32 31/32"; NOZZLE_BOTTOM_ID=25 5/8"; NOZZLE_BOTTOM_RAD=12 13/16"; NOZZLE_BOTTOM_RAD-3*2=6 13/16"; NOZZLE_HEIGHT=48"; NOZZLE_HEIGHT/7*2=12"; NOZZLE_SIZE=18"; NOZZLE_TOP_OD=27 1/2"; NOZZLE_TOP_RAD=13 3/4"; NOZZLE_WB/4=8 19/32"; NOZZLE_WB_OD=43"; NOZZLE_WB_RAD=21 1/2"; NOZZLE_WB_RAD-2"=19 1/2"; P=60"; R=33"; R*1.1=36 5/16"; R+((B/2)+1.5")=53 15/32"; R-((B/2)+1.5")=12 17/32"; RO/2=22 1/4"; RO2/2=120 5/8"; TRANSITION=18 1/8"; TRANSITION/2=9 1/16"; TRIP_Q=245 3/4"; TRIP_Q-4.5"=241 1/4"; Type Comments=Triple Vari-Plume Laboratory Exhaust Centrifugal Airfoil Class 2 Arr 10 With Mixing Box
- Triple_330_CAVP-18H_CLASS_2_With_Mixing_Box: ((M - (2 * (D - L - K - J))) / 2) + (TRANSITION / 2)=21 13/16"; (B/2)+1.5"=20 15/32"; (B/2)-.125"=18 27/32"; (D-J-K-L)*2=2"; (E/2)-((B/2)+1.5")=14 1/2"; (E/2)-((MB_P/2)+.125")=10 11/32"; (E/2)-(E/52*15)=14 25/32"; (F-((F-H)/2))/2=18 3/16"; (M - (2 * (D - L - K - J)))/2=12 3/4"; (MB_P/2)+.125"=24 5/8"; (MB_P/2-.125")+((F / 2) - 2")=-42 9/16"; (MB_P/2-.125")-((F / 2) - 2")=-6 3/16"; (MB_Q/2)+.125"=24 5/8"; (NOZZLE_HEIGHT - (NOZZLE_HEIGHT / 8 * 2)) / 2=18"; (NOZZLE_WB_OD - NOZZLE_TOP_OD) / 4=3 7/8"; -((MB_Q / 2) + 1/8")=-24 5/8"; -(F-((F-H)/2))/2=-18 3/16"; -MB_HEIGHT=-53 3/4"; -MB_P=-49"; -MB_P-.25=-49 1/4"; A=144 7/16"; A/2=72 7/32"; B=37 15/16"; B/2=18 31/32"; B/4=9 1/2"; C=82 13/16"; C/2=41 13/32"; CLASS=2"; D=64"; D-L-K-J=1"; D-M=36 1/2"; DUAL_Q=147 3/8"; DUAL_Q+.25"=147 5/8"; E=69 15/16"; E-(NOZZLE_RAD/3*2)=26 7/16"; E-N-N-H=2"; E/2=34 31/32"; E/2-H/2=15 25/32"; E/52*15=20 3/16"; E/52*30=40 11/32"; F=40 3/8"; F/2=20 3/16"; H=38 3/8"; H/2=19 3/16"; HEIGHT=63 17/32"; J=10 1/2"; J+K+L=63"; K=23"; L=29 1/2"; M=27 1/2"; M-(2*(D-L-K-J))=25 1/2"; MB_A=151 13/16"; MB_F=9 1/4"; MB_F-3"=6 1/4"; MB_HEIGHT=53 3/4"; MB_HEIGHT/2=26 7/8"; MB_N=14 3/16"; MB_N-(D-J-K-L)=13 3/16"; MB_P=49"; MB_P+.25"=49 1/4"; MB_P+MB_P+.5=98 1/2"; MB_P-4.5"=44 1/2"; MB_Q=49"; N=13 25/32"; N+(H/2)=32 31/32"; NOZZLE_BOTTOM_ID=25 5/8"; NOZZLE_BOTTOM_RAD=12 13/16"; NOZZLE_BOTTOM_RAD-3*2=6 13/16"; NOZZLE_HEIGHT=48"; NOZZLE_HEIGHT/7*2=12"; NOZZLE_SIZE=18"; NOZZLE_TOP_OD=27 1/2"; NOZZLE_TOP_RAD=13 3/4"; NOZZLE_WB/4=8 19/32"; NOZZLE_WB_OD=43"; NOZZLE_WB_RAD=21 1/2"; NOZZLE_WB_RAD-2"=19 1/2"; P=60"; R=33"; R*1.1=36 5/16"; R+((B/2)+1.5")=53 15/32"; R-((B/2)+1.5")=12 17/32"; RO/2=22 1/4"; RO2/2=120 5/8"; TRANSITION=18 1/8"; TRANSITION/2=9 1/16"; TRIP_Q=245 3/4"; TRIP_Q-4.5"=241 1/4"; Type Comments=Triple Vari-Plume Laboratory Exhaust Centrifugal Airfoil Class 2 Arr 10 With Mixing Box
- Triple_330_CAVP-24L_CLASS_2_With_Mixing_Box: ((M - (2 * (D - L - K - J))) / 2) + (TRANSITION / 2)=25 1/32"; (B/2)+1.5"=20 15/32"; (B/2)-.125"=18 27/32"; (D-J-K-L)*2=2"; (E/2)-((B/2)+1.5")=14 1/2"; (E/2)-((MB_P/2)+.125")=10 11/32"; (E/2)-(E/52*15)=14 25/32"; (F-((F-H)/2))/2=18 3/16"; (M - (2 * (D - L - K - J)))/2=12 3/4"; (MB_P/2)+.125"=24 5/8"; (MB_P/2-.125")+((F / 2) - 2")=-42 9/16"; (MB_P/2-.125")-((F / 2) - 2")=-6 3/16"; (MB_Q/2)+.125"=24 5/8"; (NOZZLE_HEIGHT - (NOZZLE_HEIGHT / 8 * 2)) / 2=23 1/4"; (NOZZLE_WB_OD - NOZZLE_TOP_OD) / 4=6 1/8"; -((MB_Q / 2) + 1/8")=-24 5/8"; -(F-((F-H)/2))/2=-18 3/16"; -MB_HEIGHT=-53 3/4"; -MB_P=-49"; -MB_P-.25=-49 1/4"; A=144 7/16"; A/2=72 7/32"; B=37 15/16"; B/2=18 31/32"; B/4=9 1/2"; C=82 13/16"; C/2=41 13/32"; CLASS=2"; D=64"; D-L-K-J=1"; D-M=36 1/2"; DUAL_Q=147 3/8"; DUAL_Q+.25"=147 5/8"; E=69 15/16"; E-(NOZZLE_RAD/3*2)=23 3/8"; E-N-N-H=2"; E/2=34 31/32"; E/2-H/2=15 25/32"; E/52*15=20 3/16"; E/52*30=40 11/32"; F=40 3/8"; F/2=20 3/16"; H=38 3/8"; H/2=19 3/16"; HEIGHT=63 17/32"; J=10 1/2"; J+K+L=63"; K=23"; L=29 1/2"; M=27 1/2"; M-(2*(D-L-K-J))=25 1/2"; MB_A=151 13/16"; MB_F=9 1/4"; MB_F-3"=6 1/4"; MB_HEIGHT=53 3/4"; MB_HEIGHT/2=26 7/8"; MB_N=14 3/16"; MB_N-(D-J-K-L)=13 3/16"; MB_P=49"; MB_P+.25"=49 1/4"; MB_P+MB_P+.5=98 1/2"; MB_P-4.5"=44 1/2"; MB_Q=49"; N=13 25/32"; N+(H/2)=32 31/32"; NOZZLE_BOTTOM_ID=34 3/4"; NOZZLE_BOTTOM_RAD=17 3/8"; NOZZLE_BOTTOM_RAD-3*2=11 3/8"; NOZZLE_HEIGHT=62"; NOZZLE_HEIGHT/7*2=15 1/2"; NOZZLE_SIZE=24"; NOZZLE_TOP_OD=36 1/2"; NOZZLE_TOP_RAD=18 1/4"; NOZZLE_WB/4=12 3/16"; NOZZLE_WB_OD=61"; NOZZLE_WB_RAD=30 1/2"; NOZZLE_WB_RAD-2"=28 1/2"; P=60"; R=33"; R*1.1=36 5/16"; R+((B/2)+1.5")=53 15/32"; R-((B/2)+1.5")=12 17/32"; RO/2=22 1/4"; RO2/2=120 5/8"; TRANSITION=24 9/16"; TRANSITION/2=12 9/32"; TRIP_Q=245 3/4"; TRIP_Q-4.5"=241 1/4"; Type Comments=Triple Vari-Plume Laboratory Exhaust Centrifugal Airfoil Class 2 Arr 10 With Mixing Box
- Triple_330_CAVP-24H_CLASS_2_With_Mixing_Box: ((M - (2 * (D - L - K - J))) / 2) + (TRANSITION / 2)=25 1/32"; (B/2)+1.5"=20 15/32"; (B/2)-.125"=18 27/32"; (D-J-K-L)*2=2"; (E/2)-((B/2)+1.5")=14 1/2"; (E/2)-((MB_P/2)+.125")=10 11/32"; (E/2)-(E/52*15)=14 25/32"; (F-((F-H)/2))/2=18 3/16"; (M - (2 * (D - L - K - J)))/2=12 3/4"; (MB_P/2)+.125"=24 5/8"; (MB_P/2-.125")+((F / 2) - 2")=-42 9/16"; (MB_P/2-.125")-((F / 2) - 2")=-6 3/16"; (MB_Q/2)+.125"=24 5/8"; (NOZZLE_HEIGHT - (NOZZLE_HEIGHT / 8 * 2)) / 2=23 1/4"; (NOZZLE_WB_OD - NOZZLE_TOP_OD) / 4=6 1/8"; -((MB_Q / 2) + 1/8")=-24 5/8"; -(F-((F-H)/2))/2=-18 3/16"; -MB_HEIGHT=-53 3/4"; -MB_P=-49"; -MB_P-.25=-49 1/4"; A=144 7/16"; A/2=72 7/32"; B=37 15/16"; B/2=18 31/32"; B/4=9 1/2"; C=82 13/16"; C/2=41 13/32"; CLASS=2"; D=64"; D-L-K-J=1"; D-M=36 1/2"; DUAL_Q=147 3/8"; DUAL_Q+.25"=147 5/8"; E=69 15/16"; E-(NOZZLE_RAD/3*2)=23 3/8"; E-N-N-H=2"; E/2=34 31/32"; E/2-H/2=15 25/32"; E/52*15=20 3/16"; E/52*30=40 11/32"; F=40 3/8"; F/2=20 3/16"; H=38 3/8"; H/2=19 3/16"; HEIGHT=63 17/32"; J=10 1/2"; J+K+L=63"; K=23"; L=29 1/2"; M=27 1/2"; M-(2*(D-L-K-J))=25 1/2"; MB_A=151 13/16"; MB_F=9 1/4"; MB_F-3"=6 1/4"; MB_HEIGHT=53 3/4"; MB_HEIGHT/2=26 7/8"; MB_N=14 3/16"; MB_N-(D-J-K-L)=13 3/16"; MB_P=49"; MB_P+.25"=49 1/4"; MB_P+MB_P+.5=98 1/2"; MB_P-4.5"=44 1/2"; MB_Q=49"; N=13 25/32"; N+(H/2)=32 31/32"; NOZZLE_BOTTOM_ID=34 3/4"; NOZZLE_BOTTOM_RAD=17 3/8"; NOZZLE_BOTTOM_RAD-3*2=11 3/8"; NOZZLE_HEIGHT=62"; NOZZLE_HEIGHT/7*2=15 1/2"; NOZZLE_SIZE=24"; NOZZLE_TOP_OD=36 1/2"; NOZZLE_TOP_RAD=18 1/4"; NOZZLE_WB/4=12 3/16"; NOZZLE_WB_OD=61"; NOZZLE_WB_RAD=30 1/2"; NOZZLE_WB_RAD-2"=28 1/2"; P=60"; R=33"; R*1.1=36 5/16"; R+((B/2)+1.5")=53 15/32"; R-((B/2)+1.5")=12 17/32"; RO/2=22 1/4"; RO2/2=120 5/8"; TRANSITION=24 9/16"; TRANSITION/2=12 9/32"; TRIP_Q=245 3/4"; TRIP_Q-4.5"=241 1/4"; Type Comments=Triple Vari-Plume Laboratory Exhaust Centrifugal Airfoil Class 2 Arr 10 With Mixing Box
- Triple_365_CAVP-15L_CLASS_1_With_Mixing_Box: ((M - (2 * (D - L - K - J))) / 2) + (TRANSITION / 2)=21 5/8"; (B/2)+1.5"=22 23/32"; (B/2)-.125"=21 3/32"; (D-J-K-L)*2=2"; (E/2)-((B/2)+1.5")=15 15/16"; (E/2)-((MB_P/2)+.125")=12 17/32"; (E/2)-(E/52*15)=16 11/32"; (F-((F-H)/2))/2=20 7/16"; (M - (2 * (D - L - K - J)))/2=14 1/16"; (MB_P/2)+.125"=26 1/8"; (MB_P/2-.125")+((F / 2) - 2")=-46 5/16"; (MB_P/2-.125")-((F / 2) - 2")=-5 7/16"; (MB_Q/2)+.125"=26 1/8"; (NOZZLE_HEIGHT - (NOZZLE_HEIGHT / 8 * 2)) / 2=16 1/8"; (NOZZLE_WB_OD - NOZZLE_TOP_OD) / 4=3 1/4"; -((MB_Q / 2) + 1/8")=-26 1/8"; -(F-((F-H)/2))/2=-20 7/16"; -MB_HEIGHT=-58 1/4"; -MB_P=-52"; -MB_P-.25=-52 1/4"; A=153 13/16"; A/2=76 29/32"; B=42 7/16"; B/2=21 7/32"; B/4=10 5/8"; C=92 3/16"; C/2=46 3/32"; CLASS=1"; D=66 7/8"; D-L-K-J=1"; D-M=36 3/4"; DUAL_Q=156 3/8"; DUAL_Q+.25"=156 5/8"; E=77 5/16"; E-(NOZZLE_RAD/3*2)=31 17/32"; E-N-N-H=2"; E/2=38 21/32"; E/2-H/2=17 7/32"; E/52*15=22 5/16"; E/52*30=44 19/32"; F=44 7/8"; F/2=22 7/16"; H=42 7/8"; H/2=21 7/16"; HEIGHT=69 3/4"; J=11"; J+K+L=65 7/8"; K=22 3/4"; L=32 1/8"; M=30 1/8"; M-(2*(D-L-K-J))=28 1/8"; MB_A=160 5/16"; MB_F=10 1/2"; MB_F-3"=7 1/2"; MB_HEIGHT=58 1/4"; MB_HEIGHT/2=29 1/8"; MB_N=14 3/16"; MB_N-(D-J-K-L)=13 3/16"; MB_P=52"; MB_P+.25"=52 1/4"; MB_P+MB_P+.5=104 1/2"; MB_P-4.5"=47 1/2"; MB_Q=52"; N=15 7/32"; N+(H/2)=36 21/32"; NOZZLE_BOTTOM_ID=21 3/8"; NOZZLE_BOTTOM_RAD=10 11/16"; NOZZLE_BOTTOM_RAD-3*2=4 11/16"; NOZZLE_HEIGHT=43"; NOZZLE_HEIGHT/7*2=10 3/4"; NOZZLE_SIZE=15"; NOZZLE_TOP_OD=23"; NOZZLE_TOP_RAD=11 1/2"; NOZZLE_WB/4=7 3/16"; NOZZLE_WB_OD=36"; NOZZLE_WB_RAD=18"; NOZZLE_WB_RAD-2"=16"; P=18 1/4"; R=36"; R*1.1=39 19/32"; R+((B/2)+1.5")=58 23/32"; R-((B/2)+1.5")=13 9/32"; RO/2=23 3/4"; RO2/2=128 1/8"; TRANSITION=15 1/8"; TRANSITION/2=7 9/16"; TRIP_Q=260 3/4"; TRIP_Q-4.5"=256 1/4"; Type Comments=Triple Vari-Plume Laboratory Exhaust Centrifugal Airfoil Class 1 Arr 10 With Mixing Box
- Triple_365_CAVP-15H_CLASS_1_With_Mixing_Box: ((M - (2 * (D - L - K - J))) / 2) + (TRANSITION / 2)=21 5/8"; (B/2)+1.5"=22 23/32"; (B/2)-.125"=21 3/32"; (D-J-K-L)*2=2"; (E/2)-((B/2)+1.5")=15 15/16"; (E/2)-((MB_P/2)+.125")=12 17/32"; (E/2)-(E/52*15)=16 11/32"; (F-((F-H)/2))/2=20 7/16"; (M - (2 * (D - L - K - J)))/2=14 1/16"; (MB_P/2)+.125"=26 1/8"; (MB_P/2-.125")+((F / 2) - 2")=-46 5/16"; (MB_P/2-.125")-((F / 2) - 2")=-5 7/16"; (MB_Q/2)+.125"=26 1/8"; (NOZZLE_HEIGHT - (NOZZLE_HEIGHT / 8 * 2)) / 2=16 1/8"; (NOZZLE_WB_OD - NOZZLE_TOP_OD) / 4=3 1/4"; -((MB_Q / 2) + 1/8")=-26 1/8"; -(F-((F-H)/2))/2=-20 7/16"; -MB_HEIGHT=-58 1/4"; -MB_P=-52"; -MB_P-.25=-52 1/4"; A=153 13/16"; A/2=76 29/32"; B=42 7/16"; B/2=21 7/32"; B/4=10 5/8"; C=92 3/16"; C/2=46 3/32"; CLASS=1"; D=66 7/8"; D-L-K-J=1"; D-M=36 3/4"; DUAL_Q=156 3/8"; DUAL_Q+.25"=156 5/8"; E=77 5/16"; E-(NOZZLE_RAD/3*2)=31 17/32"; E-N-N-H=2"; E/2=38 21/32"; E/2-H/2=17 7/32"; E/52*15=22 5/16"; E/52*30=44 19/32"; F=44 7/8"; F/2=22 7/16"; H=42 7/8"; H/2=21 7/16"; HEIGHT=69 3/4"; J=11"; J+K+L=65 7/8"; K=22 3/4"; L=32 1/8"; M=30 1/8"; M-(2*(D-L-K-J))=28 1/8"; MB_A=160 5/16"; MB_F=10 1/2"; MB_F-3"=7 1/2"; MB_HEIGHT=58 1/4"; MB_HEIGHT/2=29 1/8"; MB_N=14 3/16"; MB_N-(D-J-K-L)=13 3/16"; MB_P=52"; MB_P+.25"=52 1/4"; MB_P+MB_P+.5=104 1/2"; MB_P-4.5"=47 1/2"; MB_Q=52"; N=15 7/32"; N+(H/2)=36 21/32"; NOZZLE_BOTTOM_ID=21 3/8"; NOZZLE_BOTTOM_RAD=10 11/16"; NOZZLE_BOTTOM_RAD-3*2=4 11/16"; NOZZLE_HEIGHT=43"; NOZZLE_HEIGHT/7*2=10 3/4"; NOZZLE_SIZE=15"; NOZZLE_TOP_OD=23"; NOZZLE_TOP_RAD=11 1/2"; NOZZLE_WB/4=7 3/16"; NOZZLE_WB_OD=36"; NOZZLE_WB_RAD=18"; NOZZLE_WB_RAD-2"=16"; P=18 1/4"; R=36"; R*1.1=39 19/32"; R+((B/2)+1.5")=58 23/32"; R-((B/2)+1.5")=13 9/32"; RO/2=23 3/4"; RO2/2=128 1/8"; TRANSITION=15 1/8"; TRANSITION/2=7 9/16"; TRIP_Q=260 3/4"; TRIP_Q-4.5"=256 1/4"; Type Comments=Triple Vari-Plume Laboratory Exhaust Centrifugal Airfoil Class 1 Arr 10 With Mixing Box
- Triple_365_CAVP-18L_CLASS_1_With_Mixing_Box: ((M - (2 * (D - L - K - J))) / 2) + (TRANSITION / 2)=23 1/8"; (B/2)+1.5"=22 23/32"; (B/2)-.125"=21 3/32"; (D-J-K-L)*2=2"; (E/2)-((B/2)+1.5")=15 15/16"; (E/2)-((MB_P/2)+.125")=12 17/32"; (E/2)-(E/52*15)=16 11/32"; (F-((F-H)/2))/2=20 7/16"; (M - (2 * (D - L - K - J)))/2=14 1/16"; (MB_P/2)+.125"=26 1/8"; (MB_P/2-.125")+((F / 2) - 2")=-46 5/16"; (MB_P/2-.125")-((F / 2) - 2")=-5 7/16"; (MB_Q/2)+.125"=26 1/8"; (NOZZLE_HEIGHT - (NOZZLE_HEIGHT / 8 * 2)) / 2=18"; (NOZZLE_WB_OD - NOZZLE_TOP_OD) / 4=3 7/8"; -((MB_Q / 2) + 1/8")=-26 1/8"; -(F-((F-H)/2))/2=-20 7/16"; -MB_HEIGHT=-58 1/4"; -MB_P=-52"; -MB_P-.25=-52 1/4"; A=153 13/16"; A/2=76 29/32"; B=42 7/16"; B/2=21 7/32"; B/4=10 5/8"; C=92 3/16"; C/2=46 3/32"; CLASS=1"; D=66 7/8"; D-L-K-J=1"; D-M=36 3/4"; DUAL_Q=156 3/8"; DUAL_Q+.25"=156 5/8"; E=77 5/16"; E-(NOZZLE_RAD/3*2)=30 1/8"; E-N-N-H=2"; E/2=38 21/32"; E/2-H/2=17 7/32"; E/52*15=22 5/16"; E/52*30=44 19/32"; F=44 7/8"; F/2=22 7/16"; H=42 7/8"; H/2=21 7/16"; HEIGHT=69 3/4"; J=11"; J+K+L=65 7/8"; K=22 3/4"; L=32 1/8"; M=30 1/8"; M-(2*(D-L-K-J))=28 1/8"; MB_A=160 5/16"; MB_F=10 1/2"; MB_F-3"=7 1/2"; MB_HEIGHT=58 1/4"; MB_HEIGHT/2=29 1/8"; MB_N=14 3/16"; MB_N-(D-J-K-L)=13 3/16"; MB_P=52"; MB_P+.25"=52 1/4"; MB_P+MB_P+.5=104 1/2"; MB_P-4.5"=47 1/2"; MB_Q=52"; N=15 7/32"; N+(H/2)=36 21/32"; NOZZLE_BOTTOM_ID=25 5/8"; NOZZLE_BOTTOM_RAD=12 13/16"; NOZZLE_BOTTOM_RAD-3*2=6 13/16"; NOZZLE_HEIGHT=48"; NOZZLE_HEIGHT/7*2=12"; NOZZLE_SIZE=18"; NOZZLE_TOP_OD=27 1/2"; NOZZLE_TOP_RAD=13 3/4"; NOZZLE_WB/4=8 19/32"; NOZZLE_WB_OD=43"; NOZZLE_WB_RAD=21 1/2"; NOZZLE_WB_RAD-2"=19 1/2"; P=18 1/4"; R=36"; R*1.1=39 19/32"; R+((B/2)+1.5")=58 23/32"; R-((B/2)+1.5")=13 9/32"; RO/2=23 3/4"; RO2/2=128 1/8"; TRANSITION=18 1/8"; TRANSITION/2=9 1/16"; TRIP_Q=260 3/4"; TRIP_Q-4.5"=256 1/4"; Type Comments=Triple Vari-Plume Laboratory Exhaust Centrifugal Airfoil Class 1 Arr 10 With Mixing Box
- Triple_365_CAVP-18H_CLASS_1_With_Mixing_Box: ((M - (2 * (D - L - K - J))) / 2) + (TRANSITION / 2)=23 1/8"; (B/2)+1.5"=22 23/32"; (B/2)-.125"=21 3/32"; (D-J-K-L)*2=2"; (E/2)-((B/2)+1.5")=15 15/16"; (E/2)-((MB_P/2)+.125")=12 17/32"; (E/2)-(E/52*15)=16 11/32"; (F-((F-H)/2))/2=20 7/16"; (M - (2 * (D - L - K - J)))/2=14 1/16"; (MB_P/2)+.125"=26 1/8"; (MB_P/2-.125")+((F / 2) - 2")=-46 5/16"; (MB_P/2-.125")-((F / 2) - 2")=-5 7/16"; (MB_Q/2)+.125"=26 1/8"; (NOZZLE_HEIGHT - (NOZZLE_HEIGHT / 8 * 2)) / 2=18"; (NOZZLE_WB_OD - NOZZLE_TOP_OD) / 4=3 7/8"; -((MB_Q / 2) + 1/8")=-26 1/8"; -(F-((F-H)/2))/2=-20 7/16"; -MB_HEIGHT=-58 1/4"; -MB_P=-52"; -MB_P-.25=-52 1/4"; A=153 13/16"; A/2=76 29/32"; B=42 7/16"; B/2=21 7/32"; B/4=10 5/8"; C=92 3/16"; C/2=46 3/32"; CLASS=1"; D=66 7/8"; D-L-K-J=1"; D-M=36 3/4"; DUAL_Q=156 3/8"; DUAL_Q+.25"=156 5/8"; E=77 5/16"; E-(NOZZLE_RAD/3*2)=30 1/8"; E-N-N-H=2"; E/2=38 21/32"; E/2-H/2=17 7/32"; E/52*15=22 5/16"; E/52*30=44 19/32"; F=44 7/8"; F/2=22 7/16"; H=42 7/8"; H/2=21 7/16"; HEIGHT=69 3/4"; J=11"; J+K+L=65 7/8"; K=22 3/4"; L=32 1/8"; M=30 1/8"; M-(2*(D-L-K-J))=28 1/8"; MB_A=160 5/16"; MB_F=10 1/2"; MB_F-3"=7 1/2"; MB_HEIGHT=58 1/4"; MB_HEIGHT/2=29 1/8"; MB_N=14 3/16"; MB_N-(D-J-K-L)=13 3/16"; MB_P=52"; MB_P+.25"=52 1/4"; MB_P+MB_P+.5=104 1/2"; MB_P-4.5"=47 1/2"; MB_Q=52"; N=15 7/32"; N+(H/2)=36 21/32"; NOZZLE_BOTTOM_ID=25 5/8"; NOZZLE_BOTTOM_RAD=12 13/16"; NOZZLE_BOTTOM_RAD-3*2=6 13/16"; NOZZLE_HEIGHT=48"; NOZZLE_HEIGHT/7*2=12"; NOZZLE_SIZE=18"; NOZZLE_TOP_OD=27 1/2"; NOZZLE_TOP_RAD=13 3/4"; NOZZLE_WB/4=8 19/32"; NOZZLE_WB_OD=43"; NOZZLE_WB_RAD=21 1/2"; NOZZLE_WB_RAD-2"=19 1/2"; P=18 1/4"; R=36"; R*1.1=39 19/32"; R+((B/2)+1.5")=58 23/32"; R-((B/2)+1.5")=13 9/32"; RO/2=23 3/4"; RO2/2=128 1/8"; TRANSITION=18 1/8"; TRANSITION/2=9 1/16"; TRIP_Q=260 3/4"; TRIP_Q-4.5"=256 1/4"; Type Comments=Triple Vari-Plume Laboratory Exhaust Centrifugal Airfoil Class 1 Arr 10 With Mixing Box
- Triple_365_CAVP-24L_CLASS_1_With_Mixing_Box: ((M - (2 * (D - L - K - J))) / 2) + (TRANSITION / 2)=26 11/32"; (B/2)+1.5"=22 23/32"; (B/2)-.125"=21 3/32"; (D-J-K-L)*2=2"; (E/2)-((B/2)+1.5")=15 15/16"; (E/2)-((MB_P/2)+.125")=12 17/32"; (E/2)-(E/52*15)=16 11/32"; (F-((F-H)/2))/2=20 7/16"; (M - (2 * (D - L - K - J)))/2=14 1/16"; (MB_P/2)+.125"=26 1/8"; (MB_P/2-.125")+((F / 2) - 2")=-46 5/16"; (MB_P/2-.125")-((F / 2) - 2")=-5 7/16"; (MB_Q/2)+.125"=26 1/8"; (NOZZLE_HEIGHT - (NOZZLE_HEIGHT / 8 * 2)) / 2=23 1/4"; (NOZZLE_WB_OD - NOZZLE_TOP_OD) / 4=6 1/8"; -((MB_Q / 2) + 1/8")=-26 1/8"; -(F-((F-H)/2))/2=-20 7/16"; -MB_HEIGHT=-58 1/4"; -MB_P=-52"; -MB_P-.25=-52 1/4"; A=153 13/16"; A/2=76 29/32"; B=42 7/16"; B/2=21 7/32"; B/4=10 5/8"; C=92 3/16"; C/2=46 3/32"; CLASS=1"; D=66 7/8"; D-L-K-J=1"; D-M=36 3/4"; DUAL_Q=156 3/8"; DUAL_Q+.25"=156 5/8"; E=77 5/16"; E-(NOZZLE_RAD/3*2)=27 1/16"; E-N-N-H=2"; E/2=38 21/32"; E/2-H/2=17 7/32"; E/52*15=22 5/16"; E/52*30=44 19/32"; F=44 7/8"; F/2=22 7/16"; H=42 7/8"; H/2=21 7/16"; HEIGHT=69 3/4"; J=11"; J+K+L=65 7/8"; K=22 3/4"; L=32 1/8"; M=30 1/8"; M-(2*(D-L-K-J))=28 1/8"; MB_A=160 5/16"; MB_F=10 1/2"; MB_F-3"=7 1/2"; MB_HEIGHT=58 1/4"; MB_HEIGHT/2=29 1/8"; MB_N=14 3/16"; MB_N-(D-J-K-L)=13 3/16"; MB_P=52"; MB_P+.25"=52 1/4"; MB_P+MB_P+.5=104 1/2"; MB_P-4.5"=47 1/2"; MB_Q=52"; N=15 7/32"; N+(H/2)=36 21/32"; NOZZLE_BOTTOM_ID=34 3/4"; NOZZLE_BOTTOM_RAD=17 3/8"; NOZZLE_BOTTOM_RAD-3*2=11 3/8"; NOZZLE_HEIGHT=62"; NOZZLE_HEIGHT/7*2=15 1/2"; NOZZLE_SIZE=24"; NOZZLE_TOP_OD=36 1/2"; NOZZLE_TOP_RAD=18 1/4"; NOZZLE_WB/4=12 3/16"; NOZZLE_WB_OD=61"; NOZZLE_WB_RAD=30 1/2"; NOZZLE_WB_RAD-2"=28 1/2"; P=18 1/4"; R=36"; R*1.1=39 19/32"; R+((B/2)+1.5")=58 23/32"; R-((B/2)+1.5")=13 9/32"; RO/2=23 3/4"; RO2/2=128 1/8"; TRANSITION=24 9/16"; TRANSITION/2=12 9/32"; TRIP_Q=260 3/4"; TRIP_Q-4.5"=256 1/4"; Type Comments=Triple Vari-Plume Laboratory Exhaust Centrifugal Airfoil Class 1 Arr 10 With Mixing Box
- Triple_365_CAVP-24H_CLASS_1_With_Mixing_Box: ((M - (2 * (D - L - K - J))) / 2) + (TRANSITION / 2)=26 11/32"; (B/2)+1.5"=22 23/32"; (B/2)-.125"=21 3/32"; (D-J-K-L)*2=2"; (E/2)-((B/2)+1.5")=15 15/16"; (E/2)-((MB_P/2)+.125")=12 17/32"; (E/2)-(E/52*15)=16 11/32"; (F-((F-H)/2))/2=20 7/16"; (M - (2 * (D - L - K - J)))/2=14 1/16"; (MB_P/2)+.125"=26 1/8"; (MB_P/2-.125")+((F / 2) - 2")=-46 5/16"; (MB_P/2-.125")-((F / 2) - 2")=-5 7/16"; (MB_Q/2)+.125"=26 1/8"; (NOZZLE_HEIGHT - (NOZZLE_HEIGHT / 8 * 2)) / 2=23 1/4"; (NOZZLE_WB_OD - NOZZLE_TOP_OD) / 4=6 1/8"; -((MB_Q / 2) + 1/8")=-26 1/8"; -(F-((F-H)/2))/2=-20 7/16"; -MB_HEIGHT=-58 1/4"; -MB_P=-52"; -MB_P-.25=-52 1/4"; A=153 13/16"; A/2=76 29/32"; B=42 7/16"; B/2=21 7/32"; B/4=10 5/8"; C=92 3/16"; C/2=46 3/32"; CLASS=1"; D=66 7/8"; D-L-K-J=1"; D-M=36 3/4"; DUAL_Q=156 3/8"; DUAL_Q+.25"=156 5/8"; E=77 5/16"; E-(NOZZLE_RAD/3*2)=27 1/16"; E-N-N-H=2"; E/2=38 21/32"; E/2-H/2=17 7/32"; E/52*15=22 5/16"; E/52*30=44 19/32"; F=44 7/8"; F/2=22 7/16"; H=42 7/8"; H/2=21 7/16"; HEIGHT=69 3/4"; J=11"; J+K+L=65 7/8"; K=22 3/4"; L=32 1/8"; M=30 1/8"; M-(2*(D-L-K-J))=28 1/8"; MB_A=160 5/16"; MB_F=10 1/2"; MB_F-3"=7 1/2"; MB_HEIGHT=58 1/4"; MB_HEIGHT/2=29 1/8"; MB_N=14 3/16"; MB_N-(D-J-K-L)=13 3/16"; MB_P=52"; MB_P+.25"=52 1/4"; MB_P+MB_P+.5=104 1/2"; MB_P-4.5"=47 1/2"; MB_Q=52"; N=15 7/32"; N+(H/2)=36 21/32"; NOZZLE_BOTTOM_ID=34 3/4"; NOZZLE_BOTTOM_RAD=17 3/8"; NOZZLE_BOTTOM_RAD-3*2=11 3/8"; NOZZLE_HEIGHT=62"; NOZZLE_HEIGHT/7*2=15 1/2"; NOZZLE_SIZE=24"; NOZZLE_TOP_OD=36 1/2"; NOZZLE_TOP_RAD=18 1/4"; NOZZLE_WB/4=12 3/16"; NOZZLE_WB_OD=61"; NOZZLE_WB_RAD=30 1/2"; NOZZLE_WB_RAD-2"=28 1/2"; P=18 1/4"; R=36"; R*1.1=39 19/32"; R+((B/2)+1.5")=58 23/32"; R-((B/2)+1.5")=13 9/32"; RO/2=23 3/4"; RO2/2=128 1/8"; TRANSITION=24 9/16"; TRANSITION/2=12 9/32"; TRIP_Q=260 3/4"; TRIP_Q-4.5"=256 1/4"; Type Comments=Triple Vari-Plume Laboratory Exhaust Centrifugal Airfoil Class 1 Arr 10 With Mixing Box
- Triple_365_CAVP-15L_CLASS_2_With_Mixing_Box: ((M - (2 * (D - L - K - J))) / 2) + (TRANSITION / 2)=21 5/8"; (B/2)+1.5"=22 23/32"; (B/2)-.125"=21 3/32"; (D-J-K-L)*2=2"; (E/2)-((B/2)+1.5")=15 15/16"; (E/2)-((MB_P/2)+.125")=12 17/32"; (E/2)-(E/52*15)=16 11/32"; (F-((F-H)/2))/2=20 7/16"; (M - (2 * (D - L - K - J)))/2=14 1/16"; (MB_P/2)+.125"=26 1/8"; (MB_P/2-.125")+((F / 2) - 2")=-46 5/16"; (MB_P/2-.125")-((F / 2) - 2")=-5 7/16"; (MB_Q/2)+.125"=26 1/8"; (NOZZLE_HEIGHT - (NOZZLE_HEIGHT / 8 * 2)) / 2=16 1/8"; (NOZZLE_WB_OD - NOZZLE_TOP_OD) / 4=3 1/4"; -((MB_Q / 2) + 1/8")=-26 1/8"; -(F-((F-H)/2))/2=-20 7/16"; -MB_HEIGHT=-58 1/4"; -MB_P=-52"; -MB_P-.25=-52 1/4"; A=153 13/16"; A/2=76 29/32"; B=42 7/16"; B/2=21 7/32"; B/4=10 5/8"; C=92 3/16"; C/2=46 3/32"; CLASS=2"; D=67 1/8"; D-L-K-J=1"; D-M=37"; DUAL_Q=156 3/8"; DUAL_Q+.25"=156 5/8"; E=77 5/16"; E-(NOZZLE_RAD/3*2)=31 17/32"; E-N-N-H=2"; E/2=38 21/32"; E/2-H/2=17 7/32"; E/52*15=22 5/16"; E/52*30=44 19/32"; F=44 7/8"; F/2=22 7/16"; H=42 7/8"; H/2=21 7/16"; HEIGHT=69 3/4"; J=11"; J+K+L=66 1/8"; K=23"; L=32 1/8"; M=30 1/8"; M-(2*(D-L-K-J))=28 1/8"; MB_A=160 9/16"; MB_F=10 1/2"; MB_F-3"=7 1/2"; MB_HEIGHT=58 1/4"; MB_HEIGHT/2=29 1/8"; MB_N=14 3/16"; MB_N-(D-J-K-L)=13 3/16"; MB_P=52"; MB_P+.25"=52 1/4"; MB_P+MB_P+.5=104 1/2"; MB_P-4.5"=47 1/2"; MB_Q=52"; N=15 7/32"; N+(H/2)=36 21/32"; NOZZLE_BOTTOM_ID=21 3/8"; NOZZLE_BOTTOM_RAD=10 11/16"; NOZZLE_BOTTOM_RAD-3*2=4 11/16"; NOZZLE_HEIGHT=43"; NOZZLE_HEIGHT/7*2=10 3/4"; NOZZLE_SIZE=15"; NOZZLE_TOP_OD=23"; NOZZLE_TOP_RAD=11 1/2"; NOZZLE_WB/4=7 3/16"; NOZZLE_WB_OD=36"; NOZZLE_WB_RAD=18"; NOZZLE_WB_RAD-2"=16"; P=18 1/2"; R=36"; R*1.1=39 19/32"; R+((B/2)+1.5")=58 23/32"; R-((B/2)+1.5")=13 9/32"; RO/2=23 3/4"; RO2/2=128 1/8"; TRANSITION=15 1/8"; TRANSITION/2=7 9/16"; TRIP_Q=260 3/4"; TRIP_Q-4.5"=256 1/4"; Type Comments=Triple Vari-Plume Laboratory Exhaust Centrifugal Airfoil Class 2 Arr 10 With Mixing Box
- Triple_365_CAVP-15H_CLASS_2_With_Mixing_Box: ((M - (2 * (D - L - K - J))) / 2) + (TRANSITION / 2)=21 5/8"; (B/2)+1.5"=22 23/32"; (B/2)-.125"=21 3/32"; (D-J-K-L)*2=2"; (E/2)-((B/2)+1.5")=15 15/16"; (E/2)-((MB_P/2)+.125")=12 17/32"; (E/2)-(E/52*15)=16 11/32"; (F-((F-H)/2))/2=20 7/16"; (M - (2 * (D - L - K - J)))/2=14 1/16"; (MB_P/2)+.125"=26 1/8"; (MB_P/2-.125")+((F / 2) - 2")=-46 5/16"; (MB_P/2-.125")-((F / 2) - 2")=-5 7/16"; (MB_Q/2)+.125"=26 1/8"; (NOZZLE_HEIGHT - (NOZZLE_HEIGHT / 8 * 2)) / 2=16 1/8"; (NOZZLE_WB_OD - NOZZLE_TOP_OD) / 4=3 1/4"; -((MB_Q / 2) + 1/8")=-26 1/8"; -(F-((F-H)/2))/2=-20 7/16"; -MB_HEIGHT=-58 1/4"; -MB_P=-52"; -MB_P-.25=-52 1/4"; A=153 13/16"; A/2=76 29/32"; B=42 7/16"; B/2=21 7/32"; B/4=10 5/8"; C=92 3/16"; C/2=46 3/32"; CLASS=2"; D=67 1/8"; D-L-K-J=1"; D-M=37"; DUAL_Q=156 3/8"; DUAL_Q+.25"=156 5/8"; E=77 5/16"; E-(NOZZLE_RAD/3*2)=31 17/32"; E-N-N-H=2"; E/2=38 21/32"; E/2-H/2=17 7/32"; E/52*15=22 5/16"; E/52*30=44 19/32"; F=44 7/8"; F/2=22 7/16"; H=42 7/8"; H/2=21 7/16"; HEIGHT=69 3/4"; J=11"; J+K+L=66 1/8"; K=23"; L=32 1/8"; M=30 1/8"; M-(2*(D-L-K-J))=28 1/8"; MB_A=160 9/16"; MB_F=10 1/2"; MB_F-3"=7 1/2"; MB_HEIGHT=58 1/4"; MB_HEIGHT/2=29 1/8"; MB_N=14 3/16"; MB_N-(D-J-K-L)=13 3/16"; MB_P=52"; MB_P+.25"=52 1/4"; MB_P+MB_P+.5=104 1/2"; MB_P-4.5"=47 1/2"; MB_Q=52"; N=15 7/32"; N+(H/2)=36 21/32"; NOZZLE_BOTTOM_ID=21 3/8"; NOZZLE_BOTTOM_RAD=10 11/16"; NOZZLE_BOTTOM_RAD-3*2=4 11/16"; NOZZLE_HEIGHT=43"; NOZZLE_HEIGHT/7*2=10 3/4"; NOZZLE_SIZE=15"; NOZZLE_TOP_OD=23"; NOZZLE_TOP_RAD=11 1/2"; NOZZLE_WB/4=7 3/16"; NOZZLE_WB_OD=36"; NOZZLE_WB_RAD=18"; NOZZLE_WB_RAD-2"=16"; P=18 1/2"; R=36"; R*1.1=39 19/32"; R+((B/2)+1.5")=58 23/32"; R-((B/2)+1.5")=13 9/32"; RO/2=23 3/4"; RO2/2=128 1/8"; TRANSITION=15 1/8"; TRANSITION/2=7 9/16"; TRIP_Q=260 3/4"; TRIP_Q-4.5"=256 1/4"; Type Comments=Triple Vari-Plume Laboratory Exhaust Centrifugal Airfoil Class 2 Arr 10 With Mixing Box
- Triple_365_CAVP-18L_CLASS_2_With_Mixing_Box: ((M - (2 * (D - L - K - J))) / 2) + (TRANSITION / 2)=23 1/8"; (B/2)+1.5"=22 23/32"; (B/2)-.125"=21 3/32"; (D-J-K-L)*2=2"; (E/2)-((B/2)+1.5")=15 15/16"; (E/2)-((MB_P/2)+.125")=12 17/32"; (E/2)-(E/52*15)=16 11/32"; (F-((F-H)/2))/2=20 7/16"; (M - (2 * (D - L - K - J)))/2=14 1/16"; (MB_P/2)+.125"=26 1/8"; (MB_P/2-.125")+((F / 2) - 2")=-46 5/16"; (MB_P/2-.125")-((F / 2) - 2")=-5 7/16"; (MB_Q/2)+.125"=26 1/8"; (NOZZLE_HEIGHT - (NOZZLE_HEIGHT / 8 * 2)) / 2=18"; (NOZZLE_WB_OD - NOZZLE_TOP_OD) / 4=3 7/8"; -((MB_Q / 2) + 1/8")=-26 1/8"; -(F-((F-H)/2))/2=-20 7/16"; -MB_HEIGHT=-58 1/4"; -MB_P=-52"; -MB_P-.25=-52 1/4"; A=153 13/16"; A/2=76 29/32"; B=42 7/16"; B/2=21 7/32"; B/4=10 5/8"; C=92 3/16"; C/2=46 3/32"; CLASS=2"; D=67 1/8"; D-L-K-J=1"; D-M=37"; DUAL_Q=156 3/8"; DUAL_Q+.25"=156 5/8"; E=77 5/16"; E-(NOZZLE_RAD/3*2)=30 1/8"; E-N-N-H=2"; E/2=38 21/32"; E/2-H/2=17 7/32"; E/52*15=22 5/16"; E/52*30=44 19/32"; F=44 7/8"; F/2=22 7/16"; H=42 7/8"; H/2=21 7/16"; HEIGHT=69 3/4"; J=11"; J+K+L=66 1/8"; K=23"; L=32 1/8"; M=30 1/8"; M-(2*(D-L-K-J))=28 1/8"; MB_A=160 9/16"; MB_F=10 1/2"; MB_F-3"=7 1/2"; MB_HEIGHT=58 1/4"; MB_HEIGHT/2=29 1/8"; MB_N=14 3/16"; MB_N-(D-J-K-L)=13 3/16"; MB_P=52"; MB_P+.25"=52 1/4"; MB_P+MB_P+.5=104 1/2"; MB_P-4.5"=47 1/2"; MB_Q=52"; N=15 7/32"; N+(H/2)=36 21/32"; NOZZLE_BOTTOM_ID=25 5/8"; NOZZLE_BOTTOM_RAD=12 13/16"; NOZZLE_BOTTOM_RAD-3*2=6 13/16"; NOZZLE_HEIGHT=48"; NOZZLE_HEIGHT/7*2=12"; NOZZLE_SIZE=18"; NOZZLE_TOP_OD=27 1/2"; NOZZLE_TOP_RAD=13 3/4"; NOZZLE_WB/4=8 19/32"; NOZZLE_WB_OD=43"; NOZZLE_WB_RAD=21 1/2"; NOZZLE_WB_RAD-2"=19 1/2"; P=18 1/2"; R=36"; R*1.1=39 19/32"; R+((B/2)+1.5")=58 23/32"; R-((B/2)+1.5")=13 9/32"; RO/2=23 3/4"; RO2/2=128 1/8"; TRANSITION=18 1/8"; TRANSITION/2=9 1/16"; TRIP_Q=260 3/4"; TRIP_Q-4.5"=256 1/4"; Type Comments=Triple Vari-Plume Laboratory Exhaust Centrifugal Airfoil Class 2 Arr 10 With Mixing Box
- Triple_365_CAVP-18H_CLASS_2_With_Mixing_Box: ((M - (2 * (D - L - K - J))) / 2) + (TRANSITION / 2)=23 1/8"; (B/2)+1.5"=22 23/32"; (B/2)-.125"=21 3/32"; (D-J-K-L)*2=2"; (E/2)-((B/2)+1.5")=15 15/16"; (E/2)-((MB_P/2)+.125")=12 17/32"; (E/2)-(E/52*15)=16 11/32"; (F-((F-H)/2))/2=20 7/16"; (M - (2 * (D - L - K - J)))/2=14 1/16"; (MB_P/2)+.125"=26 1/8"; (MB_P/2-.125")+((F / 2) - 2")=-46 5/16"; (MB_P/2-.125")-((F / 2) - 2")=-5 7/16"; (MB_Q/2)+.125"=26 1/8"; (NOZZLE_HEIGHT - (NOZZLE_HEIGHT / 8 * 2)) / 2=18"; (NOZZLE_WB_OD - NOZZLE_TOP_OD) / 4=3 7/8"; -((MB_Q / 2) + 1/8")=-26 1/8"; -(F-((F-H)/2))/2=-20 7/16"; -MB_HEIGHT=-58 1/4"; -MB_P=-52"; -MB_P-.25=-52 1/4"; A=153 13/16"; A/2=76 29/32"; B=42 7/16"; B/2=21 7/32"; B/4=10 5/8"; C=92 3/16"; C/2=46 3/32"; CLASS=2"; D=67 1/8"; D-L-K-J=1"; D-M=37"; DUAL_Q=156 3/8"; DUAL_Q+.25"=156 5/8"; E=77 5/16"; E-(NOZZLE_RAD/3*2)=30 1/8"; E-N-N-H=2"; E/2=38 21/32"; E/2-H/2=17 7/32"; E/52*15=22 5/16"; E/52*30=44 19/32"; F=44 7/8"; F/2=22 7/16"; H=42 7/8"; H/2=21 7/16"; HEIGHT=69 3/4"; J=11"; J+K+L=66 1/8"; K=23"; L=32 1/8"; M=30 1/8"; M-(2*(D-L-K-J))=28 1/8"; MB_A=160 9/16"; MB_F=10 1/2"; MB_F-3"=7 1/2"; MB_HEIGHT=58 1/4"; MB_HEIGHT/2=29 1/8"; MB_N=14 3/16"; MB_N-(D-J-K-L)=13 3/16"; MB_P=52"; MB_P+.25"=52 1/4"; MB_P+MB_P+.5=104 1/2"; MB_P-4.5"=47 1/2"; MB_Q=52"; N=15 7/32"; N+(H/2)=36 21/32"; NOZZLE_BOTTOM_ID=25 5/8"; NOZZLE_BOTTOM_RAD=12 13/16"; NOZZLE_BOTTOM_RAD-3*2=6 13/16"; NOZZLE_HEIGHT=48"; NOZZLE_HEIGHT/7*2=12"; NOZZLE_SIZE=18"; NOZZLE_TOP_OD=27 1/2"; NOZZLE_TOP_RAD=13 3/4"; NOZZLE_WB/4=8 19/32"; NOZZLE_WB_OD=43"; NOZZLE_WB_RAD=21 1/2"; NOZZLE_WB_RAD-2"=19 1/2"; P=18 1/2"; R=36"; R*1.1=39 19/32"; R+((B/2)+1.5")=58 23/32"; R-((B/2)+1.5")=13 9/32"; RO/2=23 3/4"; RO2/2=128 1/8"; TRANSITION=18 1/8"; TRANSITION/2=9 1/16"; TRIP_Q=260 3/4"; TRIP_Q-4.5"=256 1/4"; Type Comments=Triple Vari-Plume Laboratory Exhaust Centrifugal Airfoil Class 2 Arr 10 With Mixing Box
- Triple_365_CAVP-24L_CLASS_2_With_Mixing_Box: ((M - (2 * (D - L - K - J))) / 2) + (TRANSITION / 2)=26 11/32"; (B/2)+1.5"=22 23/32"; (B/2)-.125"=21 3/32"; (D-J-K-L)*2=2"; (E/2)-((B/2)+1.5")=15 15/16"; (E/2)-((MB_P/2)+.125")=12 17/32"; (E/2)-(E/52*15)=16 11/32"; (F-((F-H)/2))/2=20 7/16"; (M - (2 * (D - L - K - J)))/2=14 1/16"; (MB_P/2)+.125"=26 1/8"; (MB_P/2-.125")+((F / 2) - 2")=-46 5/16"; (MB_P/2-.125")-((F / 2) - 2")=-5 7/16"; (MB_Q/2)+.125"=26 1/8"; (NOZZLE_HEIGHT - (NOZZLE_HEIGHT / 8 * 2)) / 2=23 1/4"; (NOZZLE_WB_OD - NOZZLE_TOP_OD) / 4=6 1/8"; -((MB_Q / 2) + 1/8")=-26 1/8"; -(F-((F-H)/2))/2=-20 7/16"; -MB_HEIGHT=-58 1/4"; -MB_P=-52"; -MB_P-.25=-52 1/4"; A=153 13/16"; A/2=76 29/32"; B=42 7/16"; B/2=21 7/32"; B/4=10 5/8"; C=92 3/16"; C/2=46 3/32"; CLASS=2"; D=67 1/8"; D-L-K-J=1"; D-M=37"; DUAL_Q=156 3/8"; DUAL_Q+.25"=156 5/8"; E=77 5/16"; E-(NOZZLE_RAD/3*2)=27 1/16"; E-N-N-H=2"; E/2=38 21/32"; E/2-H/2=17 7/32"; E/52*15=22 5/16"; E/52*30=44 19/32"; F=44 7/8"; F/2=22 7/16"; H=42 7/8"; H/2=21 7/16"; HEIGHT=69 3/4"; J=11"; J+K+L=66 1/8"; K=23"; L=32 1/8"; M=30 1/8"; M-(2*(D-L-K-J))=28 1/8"; MB_A=160 9/16"; MB_F=10 1/2"; MB_F-3"=7 1/2"; MB_HEIGHT=58 1/4"; MB_HEIGHT/2=29 1/8"; MB_N=14 3/16"; MB_N-(D-J-K-L)=13 3/16"; MB_P=52"; MB_P+.25"=52 1/4"; MB_P+MB_P+.5=104 1/2"; MB_P-4.5"=47 1/2"; MB_Q=52"; N=15 7/32"; N+(H/2)=36 21/32"; NOZZLE_BOTTOM_ID=34 3/4"; NOZZLE_BOTTOM_RAD=17 3/8"; NOZZLE_BOTTOM_RAD-3*2=11 3/8"; NOZZLE_HEIGHT=62"; NOZZLE_HEIGHT/7*2=15 1/2"; NOZZLE_SIZE=24"; NOZZLE_TOP_OD=36 1/2"; NOZZLE_TOP_RAD=18 1/4"; NOZZLE_WB/4=12 3/16"; NOZZLE_WB_OD=61"; NOZZLE_WB_RAD=30 1/2"; NOZZLE_WB_RAD-2"=28 1/2"; P=18 1/2"; R=36"; R*1.1=39 19/32"; R+((B/2)+1.5")=58 23/32"; R-((B/2)+1.5")=13 9/32"; RO/2=23 3/4"; RO2/2=128 1/8"; TRANSITION=24 9/16"; TRANSITION/2=12 9/32"; TRIP_Q=260 3/4"; TRIP_Q-4.5"=256 1/4"; Type Comments=Triple Vari-Plume Laboratory Exhaust Centrifugal Airfoil Class 2 Arr 10 With Mixing Box
- Triple_365_CAVP-24H_CLASS_2_With_Mixing_Box: ((M - (2 * (D - L - K - J))) / 2) + (TRANSITION / 2)=26 11/32"; (B/2)+1.5"=22 23/32"; (B/2)-.125"=21 3/32"; (D-J-K-L)*2=2"; (E/2)-((B/2)+1.5")=15 15/16"; (E/2)-((MB_P/2)+.125")=12 17/32"; (E/2)-(E/52*15)=16 11/32"; (F-((F-H)/2))/2=20 7/16"; (M - (2 * (D - L - K - J)))/2=14 1/16"; (MB_P/2)+.125"=26 1/8"; (MB_P/2-.125")+((F / 2) - 2")=-46 5/16"; (MB_P/2-.125")-((F / 2) - 2")=-5 7/16"; (MB_Q/2)+.125"=26 1/8"; (NOZZLE_HEIGHT - (NOZZLE_HEIGHT / 8 * 2)) / 2=23 1/4"; (NOZZLE_WB_OD - NOZZLE_TOP_OD) / 4=6 1/8"; -((MB_Q / 2) + 1/8")=-26 1/8"; -(F-((F-H)/2))/2=-20 7/16"; -MB_HEIGHT=-58 1/4"; -MB_P=-52"; -MB_P-.25=-52 1/4"; A=153 13/16"; A/2=76 29/32"; B=42 7/16"; B/2=21 7/32"; B/4=10 5/8"; C=92 3/16"; C/2=46 3/32"; CLASS=2"; D=67 1/8"; D-L-K-J=1"; D-M=37"; DUAL_Q=156 3/8"; DUAL_Q+.25"=156 5/8"; E=77 5/16"; E-(NOZZLE_RAD/3*2)=27 1/16"; E-N-N-H=2"; E/2=38 21/32"; E/2-H/2=17 7/32"; E/52*15=22 5/16"; E/52*30=44 19/32"; F=44 7/8"; F/2=22 7/16"; H=42 7/8"; H/2=21 7/16"; HEIGHT=69 3/4"; J=11"; J+K+L=66 1/8"; K=23"; L=32 1/8"; M=30 1/8"; M-(2*(D-L-K-J))=28 1/8"; MB_A=160 9/16"; MB_F=10 1/2"; MB_F-3"=7 1/2"; MB_HEIGHT=58 1/4"; MB_HEIGHT/2=29 1/8"; MB_N=14 3/16"; MB_N-(D-J-K-L)=13 3/16"; MB_P=52"; MB_P+.25"=52 1/4"; MB_P+MB_P+.5=104 1/2"; MB_P-4.5"=47 1/2"; MB_Q=52"; N=15 7/32"; N+(H/2)=36 21/32"; NOZZLE_BOTTOM_ID=34 3/4"; NOZZLE_BOTTOM_RAD=17 3/8"; NOZZLE_BOTTOM_RAD-3*2=11 3/8"; NOZZLE_HEIGHT=62"; NOZZLE_HEIGHT/7*2=15 1/2"; NOZZLE_SIZE=24"; NOZZLE_TOP_OD=36 1/2"; NOZZLE_TOP_RAD=18 1/4"; NOZZLE_WB/4=12 3/16"; NOZZLE_WB_OD=61"; NOZZLE_WB_RAD=30 1/2"; NOZZLE_WB_RAD-2"=28 1/2"; P=18 1/2"; R=36"; R*1.1=39 19/32"; R+((B/2)+1.5")=58 23/32"; R-((B/2)+1.5")=13 9/32"; RO/2=23 3/4"; RO2/2=128 1/8"; TRANSITION=24 9/16"; TRANSITION/2=12 9/32"; TRIP_Q=260 3/4"; TRIP_Q-4.5"=256 1/4"; Type Comments=Triple Vari-Plume Laboratory Exhaust Centrifugal Airfoil Class 2 Arr 10 With Mixing Box
- Triple_402_CAVP-18L_CLASS_1_With_Mixing_Box: ((M - (2 * (D - L - K - J))) / 2) + (TRANSITION / 2)=24 13/16"; (B/2)+1.5"=24 3/32"; (B/2)-.125"=22 15/32"; (D-J-K-L)*2=2 3/4"; (E/2)-((B/2)+1.5")=18 3/8"; (E/2)-((MB_P/2)+.125")=14 11/32"; (E/2)-(E/52*15)=17 31/32"; (F-((F-H)/2))/2=22 3/8"; (M - (2 * (D - L - K - J)))/2=15 3/4"; (MB_P/2)+.125"=28 1/8"; (MB_P/2-.125")+((F / 2) - 2")=-50 1/4"; (MB_P/2-.125")-((F / 2) - 2")=-5 1/2"; (MB_Q/2)+.125"=28 1/8"; (NOZZLE_HEIGHT - (NOZZLE_HEIGHT / 8 * 2)) / 2=18"; (NOZZLE_WB_OD - NOZZLE_TOP_OD) / 4=3 7/8"; -((MB_Q / 2) + 1/8")=-28 1/8"; -(F-((F-H)/2))/2=-22 3/8"; -MB_HEIGHT=-64 1/2"; -MB_P=-56"; -MB_P-.25=-56 1/4"; A=178 3/4"; A/2=89 3/8"; B=45 3/16"; B/2=22 19/32"; B/4=11 5/16"; C=100 3/4"; C/2=50 3/8"; CLASS=1"; D=72 1/4"; D-L-K-J=1 3/8"; D-M=38"; DUAL_Q=168 3/8"; DUAL_Q+.25"=168 5/8"; E=84 15/16"; E-(NOZZLE_RAD/3*2)=33 15/16"; E-N-N-H=2"; E/2=42 15/32"; E/2-H/2=19 3/32"; E/52*15=24 1/2"; E/52*30=49"; F=48 3/4"; F/2=24 3/8"; H=46 3/4"; H/2=23 3/8"; HEIGHT=77 3/32"; J=12 1/2"; J+K+L=70 7/8"; K=21 7/8"; L=36 1/2"; M=34 1/4"; M-(2*(D-L-K-J))=31 1/2"; MB_A=171 1/16"; MB_F=12 5/8"; MB_F-3"=9 5/8"; MB_HEIGHT=64 1/2"; MB_HEIGHT/2=32 1/4"; MB_N=13 9/16"; MB_N-(D-J-K-L)=12 3/16"; MB_P=56"; MB_P+.25"=56 1/4"; MB_P+MB_P+.5=112 1/2"; MB_P-4.5"=51 1/2"; MB_Q=56"; N=17 3/32"; N+(H/2)=40 15/32"; NOZZLE_BOTTOM_ID=25 5/8"; NOZZLE_BOTTOM_RAD=12 13/16"; NOZZLE_BOTTOM_RAD-3*2=6 13/16"; NOZZLE_HEIGHT=48"; NOZZLE_HEIGHT/7*2=12"; NOZZLE_SIZE=18"; NOZZLE_TOP_OD=27 1/2"; NOZZLE_TOP_RAD=13 3/4"; NOZZLE_WB/4=8 19/32"; NOZZLE_WB_OD=43"; NOZZLE_WB_RAD=21 1/2"; NOZZLE_WB_RAD-2"=19 1/2"; P=18 1/4"; R=40"; R*1.1=44"; R+((B/2)+1.5")=64 3/32"; R-((B/2)+1.5")=15 29/32"; RO/2=25 3/4"; RO2/2=138 1/8"; TRANSITION=18 1/8"; TRANSITION/2=9 1/16"; TRIP_Q=280 3/4"; TRIP_Q-4.5"=276 1/4"; Type Comments=Triple Vari-Plume Laboratory Exhaust Centrifugal Airfoil Class 1 Arr 10 With Mixing Box
- Triple_402_CAVP-18H_CLASS_1_With_Mixing_Box: ((M - (2 * (D - L - K - J))) / 2) + (TRANSITION / 2)=24 13/16"; (B/2)+1.5"=24 3/32"; (B/2)-.125"=22 15/32"; (D-J-K-L)*2=2 3/4"; (E/2)-((B/2)+1.5")=18 3/8"; (E/2)-((MB_P/2)+.125")=14 11/32"; (E/2)-(E/52*15)=17 31/32"; (F-((F-H)/2))/2=22 3/8"; (M - (2 * (D - L - K - J)))/2=15 3/4"; (MB_P/2)+.125"=28 1/8"; (MB_P/2-.125")+((F / 2) - 2")=-50 1/4"; (MB_P/2-.125")-((F / 2) - 2")=-5 1/2"; (MB_Q/2)+.125"=28 1/8"; (NOZZLE_HEIGHT - (NOZZLE_HEIGHT / 8 * 2)) / 2=18"; (NOZZLE_WB_OD - NOZZLE_TOP_OD) / 4=3 7/8"; -((MB_Q / 2) + 1/8")=-28 1/8"; -(F-((F-H)/2))/2=-22 3/8"; -MB_HEIGHT=-64 1/2"; -MB_P=-56"; -MB_P-.25=-56 1/4"; A=178 3/4"; A/2=89 3/8"; B=45 3/16"; B/2=22 19/32"; B/4=11 5/16"; C=100 3/4"; C/2=50 3/8"; CLASS=1"; D=72 1/4"; D-L-K-J=1 3/8"; D-M=38"; DUAL_Q=168 3/8"; DUAL_Q+.25"=168 5/8"; E=84 15/16"; E-(NOZZLE_RAD/3*2)=33 15/16"; E-N-N-H=2"; E/2=42 15/32"; E/2-H/2=19 3/32"; E/52*15=24 1/2"; E/52*30=49"; F=48 3/4"; F/2=24 3/8"; H=46 3/4"; H/2=23 3/8"; HEIGHT=77 3/32"; J=12 1/2"; J+K+L=70 7/8"; K=21 7/8"; L=36 1/2"; M=34 1/4"; M-(2*(D-L-K-J))=31 1/2"; MB_A=171 1/16"; MB_F=12 5/8"; MB_F-3"=9 5/8"; MB_HEIGHT=64 1/2"; MB_HEIGHT/2=32 1/4"; MB_N=13 9/16"; MB_N-(D-J-K-L)=12 3/16"; MB_P=56"; MB_P+.25"=56 1/4"; MB_P+MB_P+.5=112 1/2"; MB_P-4.5"=51 1/2"; MB_Q=56"; N=17 3/32"; N+(H/2)=40 15/32"; NOZZLE_BOTTOM_ID=25 5/8"; NOZZLE_BOTTOM_RAD=12 13/16"; NOZZLE_BOTTOM_RAD-3*2=6 13/16"; NOZZLE_HEIGHT=48"; NOZZLE_HEIGHT/7*2=12"; NOZZLE_SIZE=18"; NOZZLE_TOP_OD=27 1/2"; NOZZLE_TOP_RAD=13 3/4"; NOZZLE_WB/4=8 19/32"; NOZZLE_WB_OD=43"; NOZZLE_WB_RAD=21 1/2"; NOZZLE_WB_RAD-2"=19 1/2"; P=18 1/4"; R=40"; R*1.1=44"; R+((B/2)+1.5")=64 3/32"; R-((B/2)+1.5")=15 29/32"; RO/2=25 3/4"; RO2/2=138 1/8"; TRANSITION=18 1/8"; TRANSITION/2=9 1/16"; TRIP_Q=280 3/4"; TRIP_Q-4.5"=276 1/4"; Type Comments=Triple Vari-Plume Laboratory Exhaust Centrifugal Airfoil Class 1 Arr 10 With Mixing Box
- Triple_402_CAVP-24L_CLASS_1_With_Mixing_Box: ((M - (2 * (D - L - K - J))) / 2) + (TRANSITION / 2)=28 1/32"; (B/2)+1.5"=24 3/32"; (B/2)-.125"=22 15/32"; (D-J-K-L)*2=2 3/4"; (E/2)-((B/2)+1.5")=18 3/8"; (E/2)-((MB_P/2)+.125")=14 11/32"; (E/2)-(E/52*15)=17 31/32"; (F-((F-H)/2))/2=22 3/8"; (M - (2 * (D - L - K - J)))/2=15 3/4"; (MB_P/2)+.125"=28 1/8"; (MB_P/2-.125")+((F / 2) - 2")=-50 1/4"; (MB_P/2-.125")-((F / 2) - 2")=-5 1/2"; (MB_Q/2)+.125"=28 1/8"; (NOZZLE_HEIGHT - (NOZZLE_HEIGHT / 8 * 2)) / 2=23 1/4"; (NOZZLE_WB_OD - NOZZLE_TOP_OD) / 4=6 1/8"; -((MB_Q / 2) + 1/8")=-28 1/8"; -(F-((F-H)/2))/2=-22 3/8"; -MB_HEIGHT=-64 1/2"; -MB_P=-56"; -MB_P-.25=-56 1/4"; A=178 3/4"; A/2=89 3/8"; B=45 3/16"; B/2=22 19/32"; B/4=11 5/16"; C=100 3/4"; C/2=50 3/8"; CLASS=1"; D=72 1/4"; D-L-K-J=1 3/8"; D-M=38"; DUAL_Q=168 3/8"; DUAL_Q+.25"=168 5/8"; E=84 15/16"; E-(NOZZLE_RAD/3*2)=30 7/8"; E-N-N-H=2"; E/2=42 15/32"; E/2-H/2=19 3/32"; E/52*15=24 1/2"; E/52*30=49"; F=48 3/4"; F/2=24 3/8"; H=46 3/4"; H/2=23 3/8"; HEIGHT=77 3/32"; J=12 1/2"; J+K+L=70 7/8"; K=21 7/8"; L=36 1/2"; M=34 1/4"; M-(2*(D-L-K-J))=31 1/2"; MB_A=171 1/16"; MB_F=12 5/8"; MB_F-3"=9 5/8"; MB_HEIGHT=64 1/2"; MB_HEIGHT/2=32 1/4"; MB_N=13 9/16"; MB_N-(D-J-K-L)=12 3/16"; MB_P=56"; MB_P+.25"=56 1/4"; MB_P+MB_P+.5=112 1/2"; MB_P-4.5"=51 1/2"; MB_Q=56"; N=17 3/32"; N+(H/2)=40 15/32"; NOZZLE_BOTTOM_ID=34 3/4"; NOZZLE_BOTTOM_RAD=17 3/8"; NOZZLE_BOTTOM_RAD-3*2=11 3/8"; NOZZLE_HEIGHT=62"; NOZZLE_HEIGHT/7*2=15 1/2"; NOZZLE_SIZE=24"; NOZZLE_TOP_OD=36 1/2"; NOZZLE_TOP_RAD=18 1/4"; NOZZLE_WB/4=12 3/16"; NOZZLE_WB_OD=61"; NOZZLE_WB_RAD=30 1/2"; NOZZLE_WB_RAD-2"=28 1/2"; P=18 1/4"; R=40"; R*1.1=44"; R+((B/2)+1.5")=64 3/32"; R-((B/2)+1.5")=15 29/32"; RO/2=25 3/4"; RO2/2=138 1/8"; TRANSITION=24 9/16"; TRANSITION/2=12 9/32"; TRIP_Q=280 3/4"; TRIP_Q-4.5"=276 1/4"; Type Comments=Triple Vari-Plume Laboratory Exhaust Centrifugal Airfoil Class 1 Arr 10 With Mixing Box
- Triple_402_CAVP-24H_CLASS_1_With_Mixing_Box: ((M - (2 * (D - L - K - J))) / 2) + (TRANSITION / 2)=28 1/32"; (B/2)+1.5"=24 3/32"; (B/2)-.125"=22 15/32"; (D-J-K-L)*2=2 3/4"; (E/2)-((B/2)+1.5")=18 3/8"; (E/2)-((MB_P/2)+.125")=14 11/32"; (E/2)-(E/52*15)=17 31/32"; (F-((F-H)/2))/2=22 3/8"; (M - (2 * (D - L - K - J)))/2=15 3/4"; (MB_P/2)+.125"=28 1/8"; (MB_P/2-.125")+((F / 2) - 2")=-50 1/4"; (MB_P/2-.125")-((F / 2) - 2")=-5 1/2"; (MB_Q/2)+.125"=28 1/8"; (NOZZLE_HEIGHT - (NOZZLE_HEIGHT / 8 * 2)) / 2=23 1/4"; (NOZZLE_WB_OD - NOZZLE_TOP_OD) / 4=6 1/8"; -((MB_Q / 2) + 1/8")=-28 1/8"; -(F-((F-H)/2))/2=-22 3/8"; -MB_HEIGHT=-64 1/2"; -MB_P=-56"; -MB_P-.25=-56 1/4"; A=178 3/4"; A/2=89 3/8"; B=45 3/16"; B/2=22 19/32"; B/4=11 5/16"; C=100 3/4"; C/2=50 3/8"; CLASS=1"; D=72 1/4"; D-L-K-J=1 3/8"; D-M=38"; DUAL_Q=168 3/8"; DUAL_Q+.25"=168 5/8"; E=84 15/16"; E-(NOZZLE_RAD/3*2)=30 7/8"; E-N-N-H=2"; E/2=42 15/32"; E/2-H/2=19 3/32"; E/52*15=24 1/2"; E/52*30=49"; F=48 3/4"; F/2=24 3/8"; H=46 3/4"; H/2=23 3/8"; HEIGHT=77 3/32"; J=12 1/2"; J+K+L=70 7/8"; K=21 7/8"; L=36 1/2"; M=34 1/4"; M-(2*(D-L-K-J))=31 1/2"; MB_A=171 1/16"; MB_F=12 5/8"; MB_F-3"=9 5/8"; MB_HEIGHT=64 1/2"; MB_HEIGHT/2=32 1/4"; MB_N=13 9/16"; MB_N-(D-J-K-L)=12 3/16"; MB_P=56"; MB_P+.25"=56 1/4"; MB_P+MB_P+.5=112 1/2"; MB_P-4.5"=51 1/2"; MB_Q=56"; N=17 3/32"; N+(H/2)=40 15/32"; NOZZLE_BOTTOM_ID=34 3/4"; NOZZLE_BOTTOM_RAD=17 3/8"; NOZZLE_BOTTOM_RAD-3*2=11 3/8"; NOZZLE_HEIGHT=62"; NOZZLE_HEIGHT/7*2=15 1/2"; NOZZLE_SIZE=24"; NOZZLE_TOP_OD=36 1/2"; NOZZLE_TOP_RAD=18 1/4"; NOZZLE_WB/4=12 3/16"; NOZZLE_WB_OD=61"; NOZZLE_WB_RAD=30 1/2"; NOZZLE_WB_RAD-2"=28 1/2"; P=18 1/4"; R=40"; R*1.1=44"; R+((B/2)+1.5")=64 3/32"; R-((B/2)+1.5")=15 29/32"; RO/2=25 3/4"; RO2/2=138 1/8"; TRANSITION=24 9/16"; TRANSITION/2=12 9/32"; TRIP_Q=280 3/4"; TRIP_Q-4.5"=276 1/4"; Type Comments=Triple Vari-Plume Laboratory Exhaust Centrifugal Airfoil Class 1 Arr 10 With Mixing Box
- Triple_402_CAVP-30L_CLASS_1_With_Mixing_Box: ((M - (2 * (D - L - K - J))) / 2) + (TRANSITION / 2)=30 25/32"; (B/2)+1.5"=24 3/32"; (B/2)-.125"=22 15/32"; (D-J-K-L)*2=2 3/4"; (E/2)-((B/2)+1.5")=18 3/8"; (E/2)-((MB_P/2)+.125")=14 11/32"; (E/2)-(E/52*15)=17 31/32"; (F-((F-H)/2))/2=22 3/8"; (M - (2 * (D - L - K - J)))/2=15 3/4"; (MB_P/2)+.125"=28 1/8"; (MB_P/2-.125")+((F / 2) - 2")=-50 1/4"; (MB_P/2-.125")-((F / 2) - 2")=-5 1/2"; (MB_Q/2)+.125"=28 1/8"; (NOZZLE_HEIGHT - (NOZZLE_HEIGHT / 8 * 2)) / 2=29 1/4"; (NOZZLE_WB_OD - NOZZLE_TOP_OD) / 4=7 1/8"; -((MB_Q / 2) + 1/8")=-28 1/8"; -(F-((F-H)/2))/2=-22 3/8"; -MB_HEIGHT=-64 1/2"; -MB_P=-56"; -MB_P-.25=-56 1/4"; A=178 3/4"; A/2=89 3/8"; B=45 3/16"; B/2=22 19/32"; B/4=11 5/16"; C=100 3/4"; C/2=50 3/8"; CLASS=1"; D=72 1/4"; D-L-K-J=1 3/8"; D-M=38"; DUAL_Q=168 3/8"; DUAL_Q+.25"=168 5/8"; E=84 15/16"; E-(NOZZLE_RAD/3*2)=28 5/16"; E-N-N-H=2"; E/2=42 15/32"; E/2-H/2=19 3/32"; E/52*15=24 1/2"; E/52*30=49"; F=48 3/4"; F/2=24 3/8"; H=46 3/4"; H/2=23 3/8"; HEIGHT=77 3/32"; J=12 1/2"; J+K+L=70 7/8"; K=21 7/8"; L=36 1/2"; M=34 1/4"; M-(2*(D-L-K-J))=31 1/2"; MB_A=171 1/16"; MB_F=12 5/8"; MB_F-3"=9 5/8"; MB_HEIGHT=64 1/2"; MB_HEIGHT/2=32 1/4"; MB_N=13 9/16"; MB_N-(D-J-K-L)=12 3/16"; MB_P=56"; MB_P+.25"=56 1/4"; MB_P+MB_P+.5=112 1/2"; MB_P-4.5"=51 1/2"; MB_Q=56"; N=17 3/32"; N+(H/2)=40 15/32"; NOZZLE_BOTTOM_ID=42 1/2"; NOZZLE_BOTTOM_RAD=21 1/4"; NOZZLE_BOTTOM_RAD-3*2=15 1/4"; NOZZLE_HEIGHT=78"; NOZZLE_HEIGHT/7*2=19 1/2"; NOZZLE_SIZE=30"; NOZZLE_TOP_OD=45 1/2"; NOZZLE_TOP_RAD=22 3/4"; NOZZLE_WB/4=14 13/16"; NOZZLE_WB_OD=74"; NOZZLE_WB_RAD=37"; NOZZLE_WB_RAD-2"=35"; P=18 1/4"; R=40"; R*1.1=44"; R+((B/2)+1.5")=64 3/32"; R-((B/2)+1.5")=15 29/32"; RO/2=25 3/4"; RO2/2=138 1/8"; TRANSITION=30 1/16"; TRANSITION/2=15 1/32"; TRIP_Q=280 3/4"; TRIP_Q-4.5"=276 1/4"; Type Comments=Triple Vari-Plume Laboratory Exhaust Centrifugal Airfoil Class 1 Arr 10 With Mixing Box
- Triple_402_CAVP-30H_CLASS_1_With_Mixing_Box: ((M - (2 * (D - L - K - J))) / 2) + (TRANSITION / 2)=30 25/32"; (B/2)+1.5"=24 3/32"; (B/2)-.125"=22 15/32"; (D-J-K-L)*2=2 3/4"; (E/2)-((B/2)+1.5")=18 3/8"; (E/2)-((MB_P/2)+.125")=14 11/32"; (E/2)-(E/52*15)=17 31/32"; (F-((F-H)/2))/2=22 3/8"; (M - (2 * (D - L - K - J)))/2=15 3/4"; (MB_P/2)+.125"=28 1/8"; (MB_P/2-.125")+((F / 2) - 2")=-50 1/4"; (MB_P/2-.125")-((F / 2) - 2")=-5 1/2"; (MB_Q/2)+.125"=28 1/8"; (NOZZLE_HEIGHT - (NOZZLE_HEIGHT / 8 * 2)) / 2=29 1/4"; (NOZZLE_WB_OD - NOZZLE_TOP_OD) / 4=7 1/8"; -((MB_Q / 2) + 1/8")=-28 1/8"; -(F-((F-H)/2))/2=-22 3/8"; -MB_HEIGHT=-64 1/2"; -MB_P=-56"; -MB_P-.25=-56 1/4"; A=178 3/4"; A/2=89 3/8"; B=45 3/16"; B/2=22 19/32"; B/4=11 5/16"; C=100 3/4"; C/2=50 3/8"; CLASS=1"; D=72 1/4"; D-L-K-J=1 3/8"; D-M=38"; DUAL_Q=168 3/8"; DUAL_Q+.25"=168 5/8"; E=84 15/16"; E-(NOZZLE_RAD/3*2)=28 5/16"; E-N-N-H=2"; E/2=42 15/32"; E/2-H/2=19 3/32"; E/52*15=24 1/2"; E/52*30=49"; F=48 3/4"; F/2=24 3/8"; H=46 3/4"; H/2=23 3/8"; HEIGHT=77 3/32"; J=12 1/2"; J+K+L=70 7/8"; K=21 7/8"; L=36 1/2"; M=34 1/4"; M-(2*(D-L-K-J))=31 1/2"; MB_A=171 1/16"; MB_F=12 5/8"; MB_F-3"=9 5/8"; MB_HEIGHT=64 1/2"; MB_HEIGHT/2=32 1/4"; MB_N=13 9/16"; MB_N-(D-J-K-L)=12 3/16"; MB_P=56"; MB_P+.25"=56 1/4"; MB_P+MB_P+.5=112 1/2"; MB_P-4.5"=51 1/2"; MB_Q=56"; N=17 3/32"; N+(H/2)=40 15/32"; NOZZLE_BOTTOM_ID=42 1/2"; NOZZLE_BOTTOM_RAD=21 1/4"; NOZZLE_BOTTOM_RAD-3*2=15 1/4"; NOZZLE_HEIGHT=78"; NOZZLE_HEIGHT/7*2=19 1/2"; NOZZLE_SIZE=30"; NOZZLE_TOP_OD=45 1/2"; NOZZLE_TOP_RAD=22 3/4"; NOZZLE_WB/4=14 13/16"; NOZZLE_WB_OD=74"; NOZZLE_WB_RAD=37"; NOZZLE_WB_RAD-2"=35"; P=18 1/4"; R=40"; R*1.1=44"; R+((B/2)+1.5")=64 3/32"; R-((B/2)+1.5")=15 29/32"; RO/2=25 3/4"; RO2/2=138 1/8"; TRANSITION=30 1/16"; TRANSITION/2=15 1/32"; TRIP_Q=280 3/4"; TRIP_Q-4.5"=276 1/4"; Type Comments=Triple Vari-Plume Laboratory Exhaust Centrifugal Airfoil Class 1 Arr 10 With Mixing Box
- Triple_402_CAVP-18L_CLASS_2_With_Mixing_Box: ((M - (2 * (D - L - K - J))) / 2) + (TRANSITION / 2)=24 13/16"; (B/2)+1.5"=24 3/32"; (B/2)-.125"=22 15/32"; (D-J-K-L)*2=2 3/4"; (E/2)-((B/2)+1.5")=18 3/8"; (E/2)-((MB_P/2)+.125")=14 11/32"; (E/2)-(E/52*15)=17 31/32"; (F-((F-H)/2))/2=22 3/8"; (M - (2 * (D - L - K - J)))/2=15 3/4"; (MB_P/2)+.125"=28 1/8"; (MB_P/2-.125")+((F / 2) - 2")=-50 1/4"; (MB_P/2-.125")-((F / 2) - 2")=-5 1/2"; (MB_Q/2)+.125"=28 1/8"; (NOZZLE_HEIGHT - (NOZZLE_HEIGHT / 8 * 2)) / 2=18"; (NOZZLE_WB_OD - NOZZLE_TOP_OD) / 4=3 7/8"; -((MB_Q / 2) + 1/8")=-28 1/8"; -(F-((F-H)/2))/2=-22 3/8"; -MB_HEIGHT=-64 1/2"; -MB_P=-56"; -MB_P-.25=-56 1/4"; A=178 3/4"; A/2=89 3/8"; B=45 3/16"; B/2=22 19/32"; B/4=11 5/16"; C=100 3/4"; C/2=50 3/8"; CLASS=2"; D=72 1/4"; D-L-K-J=1 3/8"; D-M=38"; DUAL_Q=168 3/8"; DUAL_Q+.25"=168 5/8"; E=84 15/16"; E-(NOZZLE_RAD/3*2)=33 15/16"; E-N-N-H=2"; E/2=42 15/32"; E/2-H/2=19 3/32"; E/52*15=24 1/2"; E/52*30=49"; F=48 3/4"; F/2=24 3/8"; H=46 3/4"; H/2=23 3/8"; HEIGHT=77 3/32"; J=12 1/2"; J+K+L=70 7/8"; K=21 7/8"; L=36 1/2"; M=34 1/4"; M-(2*(D-L-K-J))=31 1/2"; MB_A=171 1/16"; MB_F=12 5/8"; MB_F-3"=9 5/8"; MB_HEIGHT=64 1/2"; MB_HEIGHT/2=32 1/4"; MB_N=13 9/16"; MB_N-(D-J-K-L)=12 3/16"; MB_P=56"; MB_P+.25"=56 1/4"; MB_P+MB_P+.5=112 1/2"; MB_P-4.5"=51 1/2"; MB_Q=56"; N=17 3/32"; N+(H/2)=40 15/32"; NOZZLE_BOTTOM_ID=25 5/8"; NOZZLE_BOTTOM_RAD=12 13/16"; NOZZLE_BOTTOM_RAD-3*2=6 13/16"; NOZZLE_HEIGHT=48"; NOZZLE_HEIGHT/7*2=12"; NOZZLE_SIZE=18"; NOZZLE_TOP_OD=27 1/2"; NOZZLE_TOP_RAD=13 3/4"; NOZZLE_WB/4=8 19/32"; NOZZLE_WB_OD=43"; NOZZLE_WB_RAD=21 1/2"; NOZZLE_WB_RAD-2"=19 1/2"; P=19 1/2"; R=40"; R*1.1=44"; R+((B/2)+1.5")=64 3/32"; R-((B/2)+1.5")=15 29/32"; RO/2=25 3/4"; RO2/2=138 1/8"; TRANSITION=18 1/8"; TRANSITION/2=9 1/16"; TRIP_Q=280 3/4"; TRIP_Q-4.5"=276 1/4"; Type Comments=Triple Vari-Plume Laboratory Exhaust Centrifugal Airfoil Class 2 Arr 10 With Mixing Box
- Triple_402_CAVP-18H_CLASS_2_With_Mixing_Box: ((M - (2 * (D - L - K - J))) / 2) + (TRANSITION / 2)=24 13/16"; (B/2)+1.5"=24 3/32"; (B/2)-.125"=22 15/32"; (D-J-K-L)*2=2 3/4"; (E/2)-((B/2)+1.5")=18 3/8"; (E/2)-((MB_P/2)+.125")=14 11/32"; (E/2)-(E/52*15)=17 31/32"; (F-((F-H)/2))/2=22 3/8"; (M - (2 * (D - L - K - J)))/2=15 3/4"; (MB_P/2)+.125"=28 1/8"; (MB_P/2-.125")+((F / 2) - 2")=-50 1/4"; (MB_P/2-.125")-((F / 2) - 2")=-5 1/2"; (MB_Q/2)+.125"=28 1/8"; (NOZZLE_HEIGHT - (NOZZLE_HEIGHT / 8 * 2)) / 2=18"; (NOZZLE_WB_OD - NOZZLE_TOP_OD) / 4=3 7/8"; -((MB_Q / 2) + 1/8")=-28 1/8"; -(F-((F-H)/2))/2=-22 3/8"; -MB_HEIGHT=-64 1/2"; -MB_P=-56"; -MB_P-.25=-56 1/4"; A=178 3/4"; A/2=89 3/8"; B=45 3/16"; B/2=22 19/32"; B/4=11 5/16"; C=100 3/4"; C/2=50 3/8"; CLASS=2"; D=72 1/4"; D-L-K-J=1 3/8"; D-M=38"; DUAL_Q=168 3/8"; DUAL_Q+.25"=168 5/8"; E=84 15/16"; E-(NOZZLE_RAD/3*2)=33 15/16"; E-N-N-H=2"; E/2=42 15/32"; E/2-H/2=19 3/32"; E/52*15=24 1/2"; E/52*30=49"; F=48 3/4"; F/2=24 3/8"; H=46 3/4"; H/2=23 3/8"; HEIGHT=77 3/32"; J=12 1/2"; J+K+L=70 7/8"; K=21 7/8"; L=36 1/2"; M=34 1/4"; M-(2*(D-L-K-J))=31 1/2"; MB_A=171 1/16"; MB_F=12 5/8"; MB_F-3"=9 5/8"; MB_HEIGHT=64 1/2"; MB_HEIGHT/2=32 1/4"; MB_N=13 9/16"; MB_N-(D-J-K-L)=12 3/16"; MB_P=56"; MB_P+.25"=56 1/4"; MB_P+MB_P+.5=112 1/2"; MB_P-4.5"=51 1/2"; MB_Q=56"; N=17 3/32"; N+(H/2)=40 15/32"; NOZZLE_BOTTOM_ID=25 5/8"; NOZZLE_BOTTOM_RAD=12 13/16"; NOZZLE_BOTTOM_RAD-3*2=6 13/16"; NOZZLE_HEIGHT=48"; NOZZLE_HEIGHT/7*2=12"; NOZZLE_SIZE=18"; NOZZLE_TOP_OD=27 1/2"; NOZZLE_TOP_RAD=13 3/4"; NOZZLE_WB/4=8 19/32"; NOZZLE_WB_OD=43"; NOZZLE_WB_RAD=21 1/2"; NOZZLE_WB_RAD-2"=19 1/2"; P=19 1/2"; R=40"; R*1.1=44"; R+((B/2)+1.5")=64 3/32"; R-((B/2)+1.5")=15 29/32"; RO/2=25 3/4"; RO2/2=138 1/8"; TRANSITION=18 1/8"; TRANSITION/2=9 1/16"; TRIP_Q=280 3/4"; TRIP_Q-4.5"=276 1/4"; Type Comments=Triple Vari-Plume Laboratory Exhaust Centrifugal Airfoil Class 2 Arr 10 With Mixing Box
- Triple_402_CAVP-24L_CLASS_2_With_Mixing_Box: ((M - (2 * (D - L - K - J))) / 2) + (TRANSITION / 2)=28 1/32"; (B/2)+1.5"=24 3/32"; (B/2)-.125"=22 15/32"; (D-J-K-L)*2=2 3/4"; (E/2)-((B/2)+1.5")=18 3/8"; (E/2)-((MB_P/2)+.125")=14 11/32"; (E/2)-(E/52*15)=17 31/32"; (F-((F-H)/2))/2=22 3/8"; (M - (2 * (D - L - K - J)))/2=15 3/4"; (MB_P/2)+.125"=28 1/8"; (MB_P/2-.125")+((F / 2) - 2")=-50 1/4"; (MB_P/2-.125")-((F / 2) - 2")=-5 1/2"; (MB_Q/2)+.125"=28 1/8"; (NOZZLE_HEIGHT - (NOZZLE_HEIGHT / 8 * 2)) / 2=23 1/4"; (NOZZLE_WB_OD - NOZZLE_TOP_OD) / 4=6 1/8"; -((MB_Q / 2) + 1/8")=-28 1/8"; -(F-((F-H)/2))/2=-22 3/8"; -MB_HEIGHT=-64 1/2"; -MB_P=-56"; -MB_P-.25=-56 1/4"; A=178 3/4"; A/2=89 3/8"; B=45 3/16"; B/2=22 19/32"; B/4=11 5/16"; C=100 3/4"; C/2=50 3/8"; CLASS=2"; D=72 1/4"; D-L-K-J=1 3/8"; D-M=38"; DUAL_Q=168 3/8"; DUAL_Q+.25"=168 5/8"; E=84 15/16"; E-(NOZZLE_RAD/3*2)=30 7/8"; E-N-N-H=2"; E/2=42 15/32"; E/2-H/2=19 3/32"; E/52*15=24 1/2"; E/52*30=49"; F=48 3/4"; F/2=24 3/8"; H=46 3/4"; H/2=23 3/8"; HEIGHT=77 3/32"; J=12 1/2"; J+K+L=70 7/8"; K=21 7/8"; L=36 1/2"; M=34 1/4"; M-(2*(D-L-K-J))=31 1/2"; MB_A=171 1/16"; MB_F=12 5/8"; MB_F-3"=9 5/8"; MB_HEIGHT=64 1/2"; MB_HEIGHT/2=32 1/4"; MB_N=12 5/8"; MB_N-(D-J-K-L)=11 1/4"; MB_P=56"; MB_P+.25"=56 1/4"; MB_P+MB_P+.5=112 1/2"; MB_P-4.5"=51 1/2"; MB_Q=56"; N=17 3/32"; N+(H/2)=40 15/32"; NOZZLE_BOTTOM_ID=34 3/4"; NOZZLE_BOTTOM_RAD=17 3/8"; NOZZLE_BOTTOM_RAD-3*2=11 3/8"; NOZZLE_HEIGHT=62"; NOZZLE_HEIGHT/7*2=15 1/2"; NOZZLE_SIZE=24"; NOZZLE_TOP_OD=36 1/2"; NOZZLE_TOP_RAD=18 1/4"; NOZZLE_WB/4=12 3/16"; NOZZLE_WB_OD=61"; NOZZLE_WB_RAD=30 1/2"; NOZZLE_WB_RAD-2"=28 1/2"; P=19 1/2"; R=40"; R*1.1=44"; R+((B/2)+1.5")=64 3/32"; R-((B/2)+1.5")=15 29/32"; RO/2=25 3/4"; RO2/2=138 1/8"; TRANSITION=24 9/16"; TRANSITION/2=12 9/32"; TRIP_Q=280 3/4"; TRIP_Q-4.5"=276 1/4"; Type Comments=Triple Vari-Plume Laboratory Exhaust Centrifugal Airfoil Class 2 Arr 10 With Mixing Box
- Triple_402_CAVP-24H_CLASS_2_With_Mixing_Box: ((M - (2 * (D - L - K - J))) / 2) + (TRANSITION / 2)=28 1/32"; (B/2)+1.5"=24 3/32"; (B/2)-.125"=22 15/32"; (D-J-K-L)*2=2 3/4"; (E/2)-((B/2)+1.5")=18 3/8"; (E/2)-((MB_P/2)+.125")=14 11/32"; (E/2)-(E/52*15)=17 31/32"; (F-((F-H)/2))/2=22 3/8"; (M - (2 * (D - L - K - J)))/2=15 3/4"; (MB_P/2)+.125"=28 1/8"; (MB_P/2-.125")+((F / 2) - 2")=-50 1/4"; (MB_P/2-.125")-((F / 2) - 2")=-5 1/2"; (MB_Q/2)+.125"=28 1/8"; (NOZZLE_HEIGHT - (NOZZLE_HEIGHT / 8 * 2)) / 2=23 1/4"; (NOZZLE_WB_OD - NOZZLE_TOP_OD) / 4=6 1/8"; -((MB_Q / 2) + 1/8")=-28 1/8"; -(F-((F-H)/2))/2=-22 3/8"; -MB_HEIGHT=-64 1/2"; -MB_P=-56"; -MB_P-.25=-56 1/4"; A=178 3/4"; A/2=89 3/8"; B=45 3/16"; B/2=22 19/32"; B/4=11 5/16"; C=100 3/4"; C/2=50 3/8"; CLASS=2"; D=72 1/4"; D-L-K-J=1 3/8"; D-M=38"; DUAL_Q=168 3/8"; DUAL_Q+.25"=168 5/8"; E=84 15/16"; E-(NOZZLE_RAD/3*2)=30 7/8"; E-N-N-H=2"; E/2=42 15/32"; E/2-H/2=19 3/32"; E/52*15=24 1/2"; E/52*30=49"; F=48 3/4"; F/2=24 3/8"; H=46 3/4"; H/2=23 3/8"; HEIGHT=77 3/32"; J=12 1/2"; J+K+L=70 7/8"; K=21 7/8"; L=36 1/2"; M=34 1/4"; M-(2*(D-L-K-J))=31 1/2"; MB_A=171 1/16"; MB_F=12 5/8"; MB_F-3"=9 5/8"; MB_HEIGHT=64 1/2"; MB_HEIGHT/2=32 1/4"; MB_N=13 9/16"; MB_N-(D-J-K-L)=12 3/16"; MB_P=56"; MB_P+.25"=56 1/4"; MB_P+MB_P+.5=112 1/2"; MB_P-4.5"=51 1/2"; MB_Q=56"; N=17 3/32"; N+(H/2)=40 15/32"; NOZZLE_BOTTOM_ID=34 3/4"; NOZZLE_BOTTOM_RAD=17 3/8"; NOZZLE_BOTTOM_RAD-3*2=11 3/8"; NOZZLE_HEIGHT=62"; NOZZLE_HEIGHT/7*2=15 1/2"; NOZZLE_SIZE=24"; NOZZLE_TOP_OD=36 1/2"; NOZZLE_TOP_RAD=18 1/4"; NOZZLE_WB/4=12 3/16"; NOZZLE_WB_OD=61"; NOZZLE_WB_RAD=30 1/2"; NOZZLE_WB_RAD-2"=28 1/2"; P=19 1/2"; R=40"; R*1.1=44"; R+((B/2)+1.5")=64 3/32"; R-((B/2)+1.5")=15 29/32"; RO/2=25 3/4"; RO2/2=138 1/8"; TRANSITION=24 9/16"; TRANSITION/2=12 9/32"; TRIP_Q=280 3/4"; TRIP_Q-4.5"=276 1/4"; Type Comments=Triple Vari-Plume Laboratory Exhaust Centrifugal Airfoil Class 2 Arr 10 With Mixing Box
- Triple_402_CAVP-30L_CLASS_2_With_Mixing_Box: ((M - (2 * (D - L - K - J))) / 2) + (TRANSITION / 2)=30 25/32"; (B/2)+1.5"=24 3/32"; (B/2)-.125"=22 15/32"; (D-J-K-L)*2=2 3/4"; (E/2)-((B/2)+1.5")=18 3/8"; (E/2)-((MB_P/2)+.125")=14 11/32"; (E/2)-(E/52*15)=17 31/32"; (F-((F-H)/2))/2=22 3/8"; (M - (2 * (D - L - K - J)))/2=15 3/4"; (MB_P/2)+.125"=28 1/8"; (MB_P/2-.125")+((F / 2) - 2")=-50 1/4"; (MB_P/2-.125")-((F / 2) - 2")=-5 1/2"; (MB_Q/2)+.125"=28 1/8"; (NOZZLE_HEIGHT - (NOZZLE_HEIGHT / 8 * 2)) / 2=29 1/4"; (NOZZLE_WB_OD - NOZZLE_TOP_OD) / 4=7 1/8"; -((MB_Q / 2) + 1/8")=-28 1/8"; -(F-((F-H)/2))/2=-22 3/8"; -MB_HEIGHT=-64 1/2"; -MB_P=-56"; -MB_P-.25=-56 1/4"; A=178 3/4"; A/2=89 3/8"; B=45 3/16"; B/2=22 19/32"; B/4=11 5/16"; C=100 3/4"; C/2=50 3/8"; CLASS=2"; D=72 1/4"; D-L-K-J=1 3/8"; D-M=38"; DUAL_Q=168 3/8"; DUAL_Q+.25"=168 5/8"; E=84 15/16"; E-(NOZZLE_RAD/3*2)=28 5/16"; E-N-N-H=2"; E/2=42 15/32"; E/2-H/2=19 3/32"; E/52*15=24 1/2"; E/52*30=49"; F=48 3/4"; F/2=24 3/8"; H=46 3/4"; H/2=23 3/8"; HEIGHT=77 3/32"; J=12 1/2"; J+K+L=70 7/8"; K=21 7/8"; L=36 1/2"; M=34 1/4"; M-(2*(D-L-K-J))=31 1/2"; MB_A=171 1/16"; MB_F=12 5/8"; MB_F-3"=9 5/8"; MB_HEIGHT=64 1/2"; MB_HEIGHT/2=32 1/4"; MB_N=13 9/16"; MB_N-(D-J-K-L)=12 3/16"; MB_P=56"; MB_P+.25"=56 1/4"; MB_P+MB_P+.5=112 1/2"; MB_P-4.5"=51 1/2"; MB_Q=56"; N=17 3/32"; N+(H/2)=40 15/32"; NOZZLE_BOTTOM_ID=42 1/2"; NOZZLE_BOTTOM_RAD=21 1/4"; NOZZLE_BOTTOM_RAD-3*2=15 1/4"; NOZZLE_HEIGHT=78"; NOZZLE_HEIGHT/7*2=19 1/2"; NOZZLE_SIZE=30"; NOZZLE_TOP_OD=45 1/2"; NOZZLE_TOP_RAD=22 3/4"; NOZZLE_WB/4=14 13/16"; NOZZLE_WB_OD=74"; NOZZLE_WB_RAD=37"; NOZZLE_WB_RAD-2"=35"; P=19 1/2"; R=40"; R*1.1=44"; R+((B/2)+1.5")=64 3/32"; R-((B/2)+1.5")=15 29/32"; RO/2=25 3/4"; RO2/2=138 1/8"; TRANSITION=30 1/16"; TRANSITION/2=15 1/32"; TRIP_Q=280 3/4"; TRIP_Q-4.5"=276 1/4"; Type Comments=Triple Vari-Plume Laboratory Exhaust Centrifugal Airfoil Class 2 Arr 10 With Mixing Box
- Triple_402_CAVP-30H_CLASS_2_With_Mixing_Box: ((M - (2 * (D - L - K - J))) / 2) + (TRANSITION / 2)=30 25/32"; (B/2)+1.5"=24 3/32"; (B/2)-.125"=22 15/32"; (D-J-K-L)*2=2 3/4"; (E/2)-((B/2)+1.5")=18 3/8"; (E/2)-((MB_P/2)+.125")=14 11/32"; (E/2)-(E/52*15)=17 31/32"; (F-((F-H)/2))/2=22 3/8"; (M - (2 * (D - L - K - J)))/2=15 3/4"; (MB_P/2)+.125"=28 1/8"; (MB_P/2-.125")+((F / 2) - 2")=-50 1/4"; (MB_P/2-.125")-((F / 2) - 2")=-5 1/2"; (MB_Q/2)+.125"=28 1/8"; (NOZZLE_HEIGHT - (NOZZLE_HEIGHT / 8 * 2)) / 2=29 1/4"; (NOZZLE_WB_OD - NOZZLE_TOP_OD) / 4=7 1/8"; -((MB_Q / 2) + 1/8")=-28 1/8"; -(F-((F-H)/2))/2=-22 3/8"; -MB_HEIGHT=-64 1/2"; -MB_P=-56"; -MB_P-.25=-56 1/4"; A=178 3/4"; A/2=89 3/8"; B=45 3/16"; B/2=22 19/32"; B/4=11 5/16"; C=100 3/4"; C/2=50 3/8"; CLASS=2"; D=72 1/4"; D-L-K-J=1 3/8"; D-M=38"; DUAL_Q=168 3/8"; DUAL_Q+.25"=168 5/8"; E=84 15/16"; E-(NOZZLE_RAD/3*2)=28 5/16"; E-N-N-H=2"; E/2=42 15/32"; E/2-H/2=19 3/32"; E/52*15=24 1/2"; E/52*30=49"; F=48 3/4"; F/2=24 3/8"; H=46 3/4"; H/2=23 3/8"; HEIGHT=77 3/32"; J=12 1/2"; J+K+L=70 7/8"; K=21 7/8"; L=36 1/2"; M=34 1/4"; M-(2*(D-L-K-J))=31 1/2"; MB_A=171 1/16"; MB_F=12 5/8"; MB_F-3"=9 5/8"; MB_HEIGHT=64 1/2"; MB_HEIGHT/2=32 1/4"; MB_N=13 9/16"; MB_N-(D-J-K-L)=12 3/16"; MB_P=56"; MB_P+.25"=56 1/4"; MB_P+MB_P+.5=112 1/2"; MB_P-4.5"=51 1/2"; MB_Q=56"; N=17 3/32"; N+(H/2)=40 15/32"; NOZZLE_BOTTOM_ID=42 1/2"; NOZZLE_BOTTOM_RAD=21 1/4"; NOZZLE_BOTTOM_RAD-3*2=15 1/4"; NOZZLE_HEIGHT=78"; NOZZLE_HEIGHT/7*2=19 1/2"; NOZZLE_SIZE=30"; NOZZLE_TOP_OD=45 1/2"; NOZZLE_TOP_RAD=22 3/4"; NOZZLE_WB/4=14 13/16"; NOZZLE_WB_OD=74"; NOZZLE_WB_RAD=37"; NOZZLE_WB_RAD-2"=35"; P=19 1/2"; R=40"; R*1.1=44"; R+((B/2)+1.5")=64 3/32"; R-((B/2)+1.5")=15 29/32"; RO/2=25 3/4"; RO2/2=138 1/8"; TRANSITION=30 1/16"; TRANSITION/2=15 1/32"; TRIP_Q=280 3/4"; TRIP_Q-4.5"=276 1/4"; Type Comments=Triple Vari-Plume Laboratory Exhaust Centrifugal Airfoil Class 2 Arr 10 With Mixing Box
- Triple_445_CAVP-24H_CLASS_1_With_Mixing_Box: ((M - (2 * (D - L - K - J))) / 2) + (TRANSITION / 2)=29 21/32"; (B/2)+1.5"=26 7/32"; (B/2)-.125"=24 19/32"; (D-J-K-L)*2=2 3/4"; (E/2)-((B/2)+1.5")=20 5/8"; (E/2)-((MB_P/2)+.125")=16 23/32"; (E/2)-(E/52*15)=19 13/16"; (F-((F-H)/2))/2=24 3/8"; (M - (2 * (D - L - K - J)))/2=17 3/8"; (MB_P/2)+.125"=30 1/8"; (MB_P/2-.125")+((F / 2) - 2")=-54 1/4"; (MB_P/2-.125")-((F / 2) - 2")=-5 1/2"; (MB_Q/2)+.125"=30 1/8"; (NOZZLE_HEIGHT - (NOZZLE_HEIGHT / 8 * 2)) / 2=23 1/4"; (NOZZLE_WB_OD - NOZZLE_TOP_OD) / 4=6 1/8"; -((MB_Q / 2) + 1/8")=-30 1/8"; -(F-((F-H)/2))/2=-24 3/8"; -MB_HEIGHT=-69 3/4"; -MB_P=-60"; -MB_P-.25=-60 1/4"; A=190 7/8"; A/2=95 7/16"; B=49 7/16"; B/2=24 23/32"; B/4=12 3/8"; C=112 7/8"; C/2=56 7/16"; CLASS=1"; D=80"; D-L-K-J=1 3/8"; D-M=42 1/2"; DUAL_Q=180 3/8"; DUAL_Q+.25"=180 5/8"; E=93 11/16"; E-(NOZZLE_RAD/3*2)=35 1/4"; E-N-N-H=2"; E/2=46 27/32"; E/2-H/2=21 15/32"; E/52*15=27 1/32"; E/52*30=54 1/16"; F=52 3/4"; F/2=26 3/8"; H=50 3/4"; H/2=25 3/8"; HEIGHT=84 29/32"; J=13"; J+K+L=78 5/8"; K=25 7/8"; L=39 3/4"; M=37 1/2"; M-(2*(D-L-K-J))=34 3/4"; MB_A=186 3/16"; MB_F=14 1/2"; MB_F-3"=11 1/2"; MB_HEIGHT=69 3/4"; MB_HEIGHT/2=34 7/8"; MB_N=13 9/16"; MB_N-(D-J-K-L)=12 3/16"; MB_P=60"; MB_P+.25"=60 1/4"; MB_P+MB_P+.5=120 1/2"; MB_P-4.5"=55 1/2"; MB_Q=60"; N=19 15/32"; N+(H/2)=44 27/32"; NOZZLE_BOTTOM_ID=34 3/4"; NOZZLE_BOTTOM_RAD=17 3/8"; NOZZLE_BOTTOM_RAD-3*2=11 3/8"; NOZZLE_HEIGHT=62"; NOZZLE_HEIGHT/7*2=15 1/2"; NOZZLE_SIZE=24"; NOZZLE_TOP_OD=36 1/2"; NOZZLE_TOP_RAD=18 1/4"; NOZZLE_WB/4=12 3/16"; NOZZLE_WB_OD=61"; NOZZLE_WB_RAD=30 1/2"; NOZZLE_WB_RAD-2"=28 1/2"; P=18 1/4"; R=44"; R*1.1=48 13/32"; R+((B/2)+1.5")=70 7/32"; R-((B/2)+1.5")=17 25/32"; RO/2=27 3/4"; RO2/2=148 1/8"; TRANSITION=24 9/16"; TRANSITION/2=12 9/32"; TRIP_Q=300 3/4"; TRIP_Q-4.5"=296 1/4"; Type Comments=Triple Vari-Plume Laboratory Exhaust Centrifugal Airfoil Class 1 Arr 10 With Mixing Box
- Triple_445_CAVP-24L_CLASS_1_With_Mixing_Box: ((M - (2 * (D - L - K - J))) / 2) + (TRANSITION / 2)=29 21/32"; (B/2)+1.5"=26 7/32"; (B/2)-.125"=24 19/32"; (D-J-K-L)*2=2 3/4"; (E/2)-((B/2)+1.5")=20 5/8"; (E/2)-((MB_P/2)+.125")=16 23/32"; (E/2)-(E/52*15)=19 13/16"; (F-((F-H)/2))/2=24 3/8"; (M - (2 * (D - L - K - J)))/2=17 3/8"; (MB_P/2)+.125"=30 1/8"; (MB_P/2-.125")+((F / 2) - 2")=-54 1/4"; (MB_P/2-.125")-((F / 2) - 2")=-5 1/2"; (MB_Q/2)+.125"=30 1/8"; (NOZZLE_HEIGHT - (NOZZLE_HEIGHT / 8 * 2)) / 2=23 1/4"; (NOZZLE_WB_OD - NOZZLE_TOP_OD) / 4=6 1/8"; -((MB_Q / 2) + 1/8")=-30 1/8"; -(F-((F-H)/2))/2=-24 3/8"; -MB_HEIGHT=-69 3/4"; -MB_P=-60"; -MB_P-.25=-60 1/4"; A=190 7/8"; A/2=95 7/16"; B=49 7/16"; B/2=24 23/32"; B/4=12 3/8"; C=112 7/8"; C/2=56 7/16"; CLASS=1"; D=80"; D-L-K-J=1 3/8"; D-M=42 1/2"; DUAL_Q=180 3/8"; DUAL_Q+.25"=180 5/8"; E=93 11/16"; E-(NOZZLE_RAD/3*2)=35 1/4"; E-N-N-H=2"; E/2=46 27/32"; E/2-H/2=21 15/32"; E/52*15=27 1/32"; E/52*30=54 1/16"; F=52 3/4"; F/2=26 3/8"; H=50 3/4"; H/2=25 3/8"; HEIGHT=84 29/32"; J=13"; J+K+L=78 5/8"; K=25 7/8"; L=39 3/4"; M=37 1/2"; M-(2*(D-L-K-J))=34 3/4"; MB_A=186 3/16"; MB_F=14 1/2"; MB_F-3"=11 1/2"; MB_HEIGHT=69 3/4"; MB_HEIGHT/2=34 7/8"; MB_N=13 9/16"; MB_N-(D-J-K-L)=12 3/16"; MB_P=60"; MB_P+.25"=60 1/4"; MB_P+MB_P+.5=120 1/2"; MB_P-4.5"=55 1/2"; MB_Q=60"; N=19 15/32"; N+(H/2)=44 27/32"; NOZZLE_BOTTOM_ID=34 3/4"; NOZZLE_BOTTOM_RAD=17 3/8"; NOZZLE_BOTTOM_RAD-3*2=11 3/8"; NOZZLE_HEIGHT=62"; NOZZLE_HEIGHT/7*2=15 1/2"; NOZZLE_SIZE=24"; NOZZLE_TOP_OD=36 1/2"; NOZZLE_TOP_RAD=18 1/4"; NOZZLE_WB/4=12 3/16"; NOZZLE_WB_OD=61"; NOZZLE_WB_RAD=30 1/2"; NOZZLE_WB_RAD-2"=28 1/2"; P=18 1/4"; R=44"; R*1.1=48 13/32"; R+((B/2)+1.5")=70 7/32"; R-((B/2)+1.5")=17 25/32"; RO/2=27 3/4"; RO2/2=148 1/8"; TRANSITION=24 9/16"; TRANSITION/2=12 9/32"; TRIP_Q=300 3/4"; TRIP_Q-4.5"=296 1/4"; Type Comments=Triple Vari-Plume Laboratory Exhaust Centrifugal Airfoil Class 1 Arr 10 With Mixing Box
- Triple_445_CAVP-30H_CLASS_1_With_Mixing_Box: ((M - (2 * (D - L - K - J))) / 2) + (TRANSITION / 2)=32 13/32"; (B/2)+1.5"=26 7/32"; (B/2)-.125"=24 19/32"; (D-J-K-L)*2=2 3/4"; (E/2)-((B/2)+1.5")=20 5/8"; (E/2)-((MB_P/2)+.125")=16 23/32"; (E/2)-(E/52*15)=19 13/16"; (F-((F-H)/2))/2=24 3/8"; (M - (2 * (D - L - K - J)))/2=17 3/8"; (MB_P/2)+.125"=30 1/8"; (MB_P/2-.125")+((F / 2) - 2")=-54 1/4"; (MB_P/2-.125")-((F / 2) - 2")=-5 1/2"; (MB_Q/2)+.125"=30 1/8"; (NOZZLE_HEIGHT - (NOZZLE_HEIGHT / 8 * 2)) / 2=29 1/4"; (NOZZLE_WB_OD - NOZZLE_TOP_OD) / 4=7 1/8"; -((MB_Q / 2) + 1/8")=-30 1/8"; -(F-((F-H)/2))/2=-24 3/8"; -MB_HEIGHT=-69 3/4"; -MB_P=-60"; -MB_P-.25=-60 1/4"; A=190 7/8"; A/2=95 7/16"; B=49 7/16"; B/2=24 23/32"; B/4=12 3/8"; C=112 7/8"; C/2=56 7/16"; CLASS=1"; D=80"; D-L-K-J=1 3/8"; D-M=42 1/2"; DUAL_Q=180 3/8"; DUAL_Q+.25"=180 5/8"; E=93 11/16"; E-(NOZZLE_RAD/3*2)=32 11/16"; E-N-N-H=2"; E/2=46 27/32"; E/2-H/2=21 15/32"; E/52*15=27 1/32"; E/52*30=54 1/16"; F=52 3/4"; F/2=26 3/8"; H=50 3/4"; H/2=25 3/8"; HEIGHT=84 29/32"; J=13"; J+K+L=78 5/8"; K=25 7/8"; L=39 3/4"; M=37 1/2"; M-(2*(D-L-K-J))=34 3/4"; MB_A=186 3/16"; MB_F=14 1/2"; MB_F-3"=11 1/2"; MB_HEIGHT=69 3/4"; MB_HEIGHT/2=34 7/8"; MB_N=13 9/16"; MB_N-(D-J-K-L)=12 3/16"; MB_P=60"; MB_P+.25"=60 1/4"; MB_P+MB_P+.5=120 1/2"; MB_P-4.5"=55 1/2"; MB_Q=60"; N=19 15/32"; N+(H/2)=44 27/32"; NOZZLE_BOTTOM_ID=42 1/2"; NOZZLE_BOTTOM_RAD=21 1/4"; NOZZLE_BOTTOM_RAD-3*2=15 1/4"; NOZZLE_HEIGHT=78"; NOZZLE_HEIGHT/7*2=19 1/2"; NOZZLE_SIZE=30"; NOZZLE_TOP_OD=45 1/2"; NOZZLE_TOP_RAD=22 3/4"; NOZZLE_WB/4=14 13/16"; NOZZLE_WB_OD=74"; NOZZLE_WB_RAD=37"; NOZZLE_WB_RAD-2"=35"; P=18 1/4"; R=44"; R*1.1=48 13/32"; R+((B/2)+1.5")=70 7/32"; R-((B/2)+1.5")=17 25/32"; RO/2=27 3/4"; RO2/2=148 1/8"; TRANSITION=30 1/16"; TRANSITION/2=15 1/32"; TRIP_Q=300 3/4"; TRIP_Q-4.5"=296 1/4"; Type Comments=Triple Vari-Plume Laboratory Exhaust Centrifugal Airfoil Class 1 Arr 10 With Mixing Box
- Triple_445_CAVP-30L_CLASS_1_With_Mixing_Box: ((M - (2 * (D - L - K - J))) / 2) + (TRANSITION / 2)=32 13/32"; (B/2)+1.5"=26 7/32"; (B/2)-.125"=24 19/32"; (D-J-K-L)*2=2 3/4"; (E/2)-((B/2)+1.5")=20 5/8"; (E/2)-((MB_P/2)+.125")=16 23/32"; (E/2)-(E/52*15)=19 13/16"; (F-((F-H)/2))/2=24 3/8"; (M - (2 * (D - L - K - J)))/2=17 3/8"; (MB_P/2)+.125"=30 1/8"; (MB_P/2-.125")+((F / 2) - 2")=-54 1/4"; (MB_P/2-.125")-((F / 2) - 2")=-5 1/2"; (MB_Q/2)+.125"=30 1/8"; (NOZZLE_HEIGHT - (NOZZLE_HEIGHT / 8 * 2)) / 2=29 1/4"; (NOZZLE_WB_OD - NOZZLE_TOP_OD) / 4=7 1/8"; -((MB_Q / 2) + 1/8")=-30 1/8"; -(F-((F-H)/2))/2=-24 3/8"; -MB_HEIGHT=-69 3/4"; -MB_P=-60"; -MB_P-.25=-60 1/4"; A=190 7/8"; A/2=95 7/16"; B=49 7/16"; B/2=24 23/32"; B/4=12 3/8"; C=112 7/8"; C/2=56 7/16"; CLASS=1"; D=80"; D-L-K-J=1 3/8"; D-M=42 1/2"; DUAL_Q=180 3/8"; DUAL_Q+.25"=180 5/8"; E=93 11/16"; E-(NOZZLE_RAD/3*2)=32 11/16"; E-N-N-H=2"; E/2=46 27/32"; E/2-H/2=21 15/32"; E/52*15=27 1/32"; E/52*30=54 1/16"; F=52 3/4"; F/2=26 3/8"; H=50 3/4"; H/2=25 3/8"; HEIGHT=84 29/32"; J=13"; J+K+L=78 5/8"; K=25 7/8"; L=39 3/4"; M=37 1/2"; M-(2*(D-L-K-J))=34 3/4"; MB_A=186 3/16"; MB_F=14 1/2"; MB_F-3"=11 1/2"; MB_HEIGHT=69 3/4"; MB_HEIGHT/2=34 7/8"; MB_N=13 9/16"; MB_N-(D-J-K-L)=12 3/16"; MB_P=60"; MB_P+.25"=60 1/4"; MB_P+MB_P+.5=120 1/2"; MB_P-4.5"=55 1/2"; MB_Q=60"; N=19 15/32"; N+(H/2)=44 27/32"; NOZZLE_BOTTOM_ID=42 1/2"; NOZZLE_BOTTOM_RAD=21 1/4"; NOZZLE_BOTTOM_RAD-3*2=15 1/4"; NOZZLE_HEIGHT=78"; NOZZLE_HEIGHT/7*2=19 1/2"; NOZZLE_SIZE=30"; NOZZLE_TOP_OD=45 1/2"; NOZZLE_TOP_RAD=22 3/4"; NOZZLE_WB/4=14 13/16"; NOZZLE_WB_OD=74"; NOZZLE_WB_RAD=37"; NOZZLE_WB_RAD-2"=35"; P=18 1/4"; R=44"; R*1.1=48 13/32"; R+((B/2)+1.5")=70 7/32"; R-((B/2)+1.5")=17 25/32"; RO/2=27 3/4"; RO2/2=148 1/8"; TRANSITION=30 1/16"; TRANSITION/2=15 1/32"; TRIP_Q=300 3/4"; TRIP_Q-4.5"=296 1/4"; Type Comments=Triple Vari-Plume Laboratory Exhaust Centrifugal Airfoil Class 1 Arr 10 With Mixing Box
- Triple_445_CAVP-24H_CLASS_2_With_Mixing_Box: ((M - (2 * (D - L - K - J))) / 2) + (TRANSITION / 2)=29 21/32"; (B/2)+1.5"=26 7/32"; (B/2)-.125"=24 19/32"; (D-J-K-L)*2=2 3/4"; (E/2)-((B/2)+1.5")=20 5/8"; (E/2)-((MB_P/2)+.125")=16 23/32"; (E/2)-(E/52*15)=19 13/16"; (F-((F-H)/2))/2=24 3/8"; (M - (2 * (D - L - K - J)))/2=17 3/8"; (MB_P/2)+.125"=30 1/8"; (MB_P/2-.125")+((F / 2) - 2")=-54 1/4"; (MB_P/2-.125")-((F / 2) - 2")=-5 1/2"; (MB_Q/2)+.125"=30 1/8"; (NOZZLE_HEIGHT - (NOZZLE_HEIGHT / 8 * 2)) / 2=23 1/4"; (NOZZLE_WB_OD - NOZZLE_TOP_OD) / 4=6 1/8"; -((MB_Q / 2) + 1/8")=-30 1/8"; -(F-((F-H)/2))/2=-24 3/8"; -MB_HEIGHT=-69 3/4"; -MB_P=-60"; -MB_P-.25=-60 1/4"; A=190 7/8"; A/2=95 7/16"; B=49 7/16"; B/2=24 23/32"; B/4=12 3/8"; C=112 7/8"; C/2=56 7/16"; CLASS=2"; D=80"; D-L-K-J=1 3/8"; D-M=42 1/2"; DUAL_Q=180 3/8"; DUAL_Q+.25"=180 5/8"; E=93 11/16"; E-(NOZZLE_RAD/3*2)=35 1/4"; E-N-N-H=2"; E/2=46 27/32"; E/2-H/2=21 15/32"; E/52*15=27 1/32"; E/52*30=54 1/16"; F=52 3/4"; F/2=26 3/8"; H=50 3/4"; H/2=25 3/8"; HEIGHT=84 29/32"; J=13"; J+K+L=78 5/8"; K=25 7/8"; L=39 3/4"; M=37 1/2"; M-(2*(D-L-K-J))=34 3/4"; MB_A=186 3/16"; MB_F=14 1/2"; MB_F-3"=11 1/2"; MB_HEIGHT=69 3/4"; MB_HEIGHT/2=34 7/8"; MB_N=13 9/16"; MB_N-(D-J-K-L)=12 3/16"; MB_P=60"; MB_P+.25"=60 1/4"; MB_P+MB_P+.5=120 1/2"; MB_P-4.5"=55 1/2"; MB_Q=60"; N=19 15/32"; N+(H/2)=44 27/32"; NOZZLE_BOTTOM_ID=34 3/4"; NOZZLE_BOTTOM_RAD=17 3/8"; NOZZLE_BOTTOM_RAD-3*2=11 3/8"; NOZZLE_HEIGHT=62"; NOZZLE_HEIGHT/7*2=15 1/2"; NOZZLE_SIZE=24"; NOZZLE_TOP_OD=36 1/2"; NOZZLE_TOP_RAD=18 1/4"; NOZZLE_WB/4=12 3/16"; NOZZLE_WB_OD=61"; NOZZLE_WB_RAD=30 1/2"; NOZZLE_WB_RAD-2"=28 1/2"; P=19 1/2"; R=44"; R*1.1=48 13/32"; R+((B/2)+1.5")=70 7/32"; R-((B/2)+1.5")=17 25/32"; RO/2=27 3/4"; RO2/2=148 1/8"; TRANSITION=24 9/16"; TRANSITION/2=12 9/32"; TRIP_Q=300 3/4"; TRIP_Q-4.5"=296 1/4"; Type Comments=Triple Vari-Plume Laboratory Exhaust Centrifugal Airfoil Class 2 Arr 10 With Mixing Box
- Triple_445_CAVP-24L_CLASS_2_With_Mixing_Box: ((M - (2 * (D - L - K - J))) / 2) + (TRANSITION / 2)=29 21/32"; (B/2)+1.5"=26 7/32"; (B/2)-.125"=24 19/32"; (D-J-K-L)*2=2 3/4"; (E/2)-((B/2)+1.5")=20 5/8"; (E/2)-((MB_P/2)+.125")=16 23/32"; (E/2)-(E/52*15)=19 13/16"; (F-((F-H)/2))/2=24 3/8"; (M - (2 * (D - L - K - J)))/2=17 3/8"; (MB_P/2)+.125"=30 1/8"; (MB_P/2-.125")+((F / 2) - 2")=-54 1/4"; (MB_P/2-.125")-((F / 2) - 2")=-5 1/2"; (MB_Q/2)+.125"=30 1/8"; (NOZZLE_HEIGHT - (NOZZLE_HEIGHT / 8 * 2)) / 2=23 1/4"; (NOZZLE_WB_OD - NOZZLE_TOP_OD) / 4=6 1/8"; -((MB_Q / 2) + 1/8")=-30 1/8"; -(F-((F-H)/2))/2=-24 3/8"; -MB_HEIGHT=-69 3/4"; -MB_P=-60"; -MB_P-.25=-60 1/4"; A=190 7/8"; A/2=95 7/16"; B=49 7/16"; B/2=24 23/32"; B/4=12 3/8"; C=112 7/8"; C/2=56 7/16"; CLASS=2"; D=80"; D-L-K-J=1 3/8"; D-M=42 1/2"; DUAL_Q=180 3/8"; DUAL_Q+.25"=180 5/8"; E=93 11/16"; E-(NOZZLE_RAD/3*2)=35 1/4"; E-N-N-H=2"; E/2=46 27/32"; E/2-H/2=21 15/32"; E/52*15=27 1/32"; E/52*30=54 1/16"; F=52 3/4"; F/2=26 3/8"; H=50 3/4"; H/2=25 3/8"; HEIGHT=84 29/32"; J=13"; J+K+L=78 5/8"; K=25 7/8"; L=39 3/4"; M=37 1/2"; M-(2*(D-L-K-J))=34 3/4"; MB_A=186 3/16"; MB_F=14 1/2"; MB_F-3"=11 1/2"; MB_HEIGHT=69 3/4"; MB_HEIGHT/2=34 7/8"; MB_N=12 9/16"; MB_N-(D-J-K-L)=11 3/16"; MB_P=60"; MB_P+.25"=60 1/4"; MB_P+MB_P+.5=120 1/2"; MB_P-4.5"=55 1/2"; MB_Q=60"; N=19 15/32"; N+(H/2)=44 27/32"; NOZZLE_BOTTOM_ID=34 3/4"; NOZZLE_BOTTOM_RAD=17 3/8"; NOZZLE_BOTTOM_RAD-3*2=11 3/8"; NOZZLE_HEIGHT=62"; NOZZLE_HEIGHT/7*2=15 1/2"; NOZZLE_SIZE=24"; NOZZLE_TOP_OD=36 1/2"; NOZZLE_TOP_RAD=18 1/4"; NOZZLE_WB/4=12 3/16"; NOZZLE_WB_OD=61"; NOZZLE_WB_RAD=30 1/2"; NOZZLE_WB_RAD-2"=28 1/2"; P=19 1/2"; R=44"; R*1.1=48 13/32"; R+((B/2)+1.5")=70 7/32"; R-((B/2)+1.5")=17 25/32"; RO/2=27 3/4"; RO2/2=148 1/8"; TRANSITION=24 9/16"; TRANSITION/2=12 9/32"; TRIP_Q=300 3/4"; TRIP_Q-4.5"=296 1/4"; Type Comments=Triple Vari-Plume Laboratory Exhaust Centrifugal Airfoil Class 2 Arr 10 With Mixing Box
- Triple_445_CAVP-30H_CLASS_2_With_Mixing_Box: ((M - (2 * (D - L - K - J))) / 2) + (TRANSITION / 2)=32 13/32"; (B/2)+1.5"=26 7/32"; (B/2)-.125"=24 19/32"; (D-J-K-L)*2=2 3/4"; (E/2)-((B/2)+1.5")=20 5/8"; (E/2)-((MB_P/2)+.125")=16 23/32"; (E/2)-(E/52*15)=19 13/16"; (F-((F-H)/2))/2=24 3/8"; (M - (2 * (D - L - K - J)))/2=17 3/8"; (MB_P/2)+.125"=30 1/8"; (MB_P/2-.125")+((F / 2) - 2")=-54 1/4"; (MB_P/2-.125")-((F / 2) - 2")=-5 1/2"; (MB_Q/2)+.125"=30 1/8"; (NOZZLE_HEIGHT - (NOZZLE_HEIGHT / 8 * 2)) / 2=29 1/4"; (NOZZLE_WB_OD - NOZZLE_TOP_OD) / 4=7 1/8"; -((MB_Q / 2) + 1/8")=-30 1/8"; -(F-((F-H)/2))/2=-24 3/8"; -MB_HEIGHT=-69 3/4"; -MB_P=-60"; -MB_P-.25=-60 1/4"; A=190 7/8"; A/2=95 7/16"; B=49 7/16"; B/2=24 23/32"; B/4=12 3/8"; C=112 7/8"; C/2=56 7/16"; CLASS=2"; D=80"; D-L-K-J=1 3/8"; D-M=42 1/2"; DUAL_Q=180 3/8"; DUAL_Q+.25"=180 5/8"; E=93 11/16"; E-(NOZZLE_RAD/3*2)=32 11/16"; E-N-N-H=2"; E/2=46 27/32"; E/2-H/2=21 15/32"; E/52*15=27 1/32"; E/52*30=54 1/16"; F=52 3/4"; F/2=26 3/8"; H=50 3/4"; H/2=25 3/8"; HEIGHT=84 29/32"; J=13"; J+K+L=78 5/8"; K=25 7/8"; L=39 3/4"; M=37 1/2"; M-(2*(D-L-K-J))=34 3/4"; MB_A=186 3/16"; MB_F=14 1/2"; MB_F-3"=11 1/2"; MB_HEIGHT=69 3/4"; MB_HEIGHT/2=34 7/8"; MB_N=13 9/16"; MB_N-(D-J-K-L)=12 3/16"; MB_P=60"; MB_P+.25"=60 1/4"; MB_P+MB_P+.5=120 1/2"; MB_P-4.5"=55 1/2"; MB_Q=60"; N=19 15/32"; N+(H/2)=44 27/32"; NOZZLE_BOTTOM_ID=42 1/2"; NOZZLE_BOTTOM_RAD=21 1/4"; NOZZLE_BOTTOM_RAD-3*2=15 1/4"; NOZZLE_HEIGHT=78"; NOZZLE_HEIGHT/7*2=19 1/2"; NOZZLE_SIZE=30"; NOZZLE_TOP_OD=45 1/2"; NOZZLE_TOP_RAD=22 3/4"; NOZZLE_WB/4=14 13/16"; NOZZLE_WB_OD=74"; NOZZLE_WB_RAD=37"; NOZZLE_WB_RAD-2"=35"; P=19 1/2"; R=44"; R*1.1=48 13/32"; R+((B/2)+1.5")=70 7/32"; R-((B/2)+1.5")=17 25/32"; RO/2=27 3/4"; RO2/2=148 1/8"; TRANSITION=30 1/16"; TRANSITION/2=15 1/32"; TRIP_Q=300 3/4"; TRIP_Q-4.5"=296 1/4"; Type Comments=Triple Vari-Plume Laboratory Exhaust Centrifugal Airfoil Class 2 Arr 10 With Mixing Box
- Triple_445_CAVP-30L_CLASS_2_With_Mixing_Box: ((M - (2 * (D - L - K - J))) / 2) + (TRANSITION / 2)=32 13/32"; (B/2)+1.5"=26 7/32"; (B/2)-.125"=24 19/32"; (D-J-K-L)*2=2 3/4"; (E/2)-((B/2)+1.5")=20 5/8"; (E/2)-((MB_P/2)+.125")=16 23/32"; (E/2)-(E/52*15)=19 13/16"; (F-((F-H)/2))/2=24 3/8"; (M - (2 * (D - L - K - J)))/2=17 3/8"; (MB_P/2)+.125"=30 1/8"; (MB_P/2-.125")+((F / 2) - 2")=-54 1/4"; (MB_P/2-.125")-((F / 2) - 2")=-5 1/2"; (MB_Q/2)+.125"=30 1/8"; (NOZZLE_HEIGHT - (NOZZLE_HEIGHT / 8 * 2)) / 2=29 1/4"; (NOZZLE_WB_OD - NOZZLE_TOP_OD) / 4=7 1/8"; -((MB_Q / 2) + 1/8")=-30 1/8"; -(F-((F-H)/2))/2=-24 3/8"; -MB_HEIGHT=-69 3/4"; -MB_P=-60"; -MB_P-.25=-60 1/4"; A=190 7/8"; A/2=95 7/16"; B=49 7/16"; B/2=24 23/32"; B/4=12 3/8"; C=112 7/8"; C/2=56 7/16"; CLASS=2"; D=80"; D-L-K-J=1 3/8"; D-M=42 1/2"; DUAL_Q=180 3/8"; DUAL_Q+.25"=180 5/8"; E=93 11/16"; E-(NOZZLE_RAD/3*2)=32 11/16"; E-N-N-H=2"; E/2=46 27/32"; E/2-H/2=21 15/32"; E/52*15=27 1/32"; E/52*30=54 1/16"; F=52 3/4"; F/2=26 3/8"; H=50 3/4"; H/2=25 3/8"; HEIGHT=84 29/32"; J=13"; J+K+L=78 5/8"; K=25 7/8"; L=39 3/4"; M=37 1/2"; M-(2*(D-L-K-J))=34 3/4"; MB_A=186 3/16"; MB_F=14 1/2"; MB_F-3"=11 1/2"; MB_HEIGHT=69 3/4"; MB_HEIGHT/2=34 7/8"; MB_N=13 9/16"; MB_N-(D-J-K-L)=12 3/16"; MB_P=60"; MB_P+.25"=60 1/4"; MB_P+MB_P+.5=120 1/2"; MB_P-4.5"=55 1/2"; MB_Q=60"; N=19 15/32"; N+(H/2)=44 27/32"; NOZZLE_BOTTOM_ID=42 1/2"; NOZZLE_BOTTOM_RAD=21 1/4"; NOZZLE_BOTTOM_RAD-3*2=15 1/4"; NOZZLE_HEIGHT=78"; NOZZLE_HEIGHT/7*2=19 1/2"; NOZZLE_SIZE=30"; NOZZLE_TOP_OD=45 1/2"; NOZZLE_TOP_RAD=22 3/4"; NOZZLE_WB/4=14 13/16"; NOZZLE_WB_OD=74"; NOZZLE_WB_RAD=37"; NOZZLE_WB_RAD-2"=35"; P=19 1/2"; R=44"; R*1.1=48 13/32"; R+((B/2)+1.5")=70 7/32"; R-((B/2)+1.5")=17 25/32"; RO/2=27 3/4"; RO2/2=148 1/8"; TRANSITION=30 1/16"; TRANSITION/2=15 1/32"; TRIP_Q=300 3/4"; TRIP_Q-4.5"=296 1/4"; Type Comments=Triple Vari-Plume Laboratory Exhaust Centrifugal Airfoil Class 2 Arr 10 With Mixing Box
- Triple_490_CAVP-24H_CLASS_1_With_Mixing_Box: ((M - (2 * (D - L - K - J))) / 2) + (TRANSITION / 2)=31 3/8"; (B/2)+1.5"=29"; (B/2)-.125"=27 3/8"; (D-J-K-L)*2=2 3/4"; (E/2)-((B/2)+1.5")=22 15/32"; (E/2)-((MB_P/2)+.125")=18 11/32"; (E/2)-(E/52*15)=21 25/32"; (F-((F-H)/2))/2=27 27/32"; (M - (2 * (D - L - K - J)))/2=19 3/32"; (MB_P/2)+.125"=33 1/8"; (MB_P/2-.125")+((F / 2) - 2")=-60 23/32"; (MB_P/2-.125")-((F / 2) - 2")=-5 1/32"; (MB_Q/2)+.125"=33 1/8"; (NOZZLE_HEIGHT - (NOZZLE_HEIGHT / 8 * 2)) / 2=23 1/4"; (NOZZLE_WB_OD - NOZZLE_TOP_OD) / 4=6 1/8"; -((MB_Q / 2) + 1/8")=-33 1/8"; -(F-((F-H)/2))/2=-27 27/32"; -MB_HEIGHT=-70 3/4"; -MB_P=-66"; -MB_P-.25=-66 1/4"; A=217 13/16"; A/2=108 29/32"; B=55"; B/2=27 1/2"; B/4=13 3/4"; C=123 1/16"; C/2=61 17/32"; CLASS=1"; D=79 15/16"; D-L-K-J=1 3/8"; D-M=39"; DUAL_Q=198 3/8"; DUAL_Q+.25"=198 5/8"; E=102 15/16"; E-(NOZZLE_RAD/3*2)=39 7/8"; E-N-N-H=2"; E/2=51 15/32"; E/2-H/2=22 5/8"; E/52*15=29 11/16"; E/52*30=59 3/8"; F=59 11/16"; F/2=29 27/32"; H=57 11/16"; H/2=28 27/32"; HEIGHT=92 15/16"; J=13 1/2"; J+K+L=78 9/16"; K=21 7/8"; L=43 3/16"; M=40 15/16"; M-(2*(D-L-K-J))=38 3/16"; MB_A=191 7/8"; MB_F=15 3/4"; MB_F-3"=12 3/4"; MB_HEIGHT=70 3/4"; MB_HEIGHT/2=35 3/8"; MB_N=13 9/16"; MB_N-(D-J-K-L)=12 3/16"; MB_P=66"; MB_P+.25"=66 1/4"; MB_P+MB_P+.5=132 1/2"; MB_P-4.5"=61 1/2"; MB_Q=66"; N=20 5/8"; N+(H/2)=49 15/32"; NOZZLE_BOTTOM_ID=34 3/4"; NOZZLE_BOTTOM_RAD=17 3/8"; NOZZLE_BOTTOM_RAD-3*2=11 3/8"; NOZZLE_HEIGHT=62"; NOZZLE_HEIGHT/7*2=15 1/2"; NOZZLE_SIZE=24"; NOZZLE_TOP_OD=36 1/2"; NOZZLE_TOP_RAD=18 1/4"; NOZZLE_WB/4=12 3/16"; NOZZLE_WB_OD=61"; NOZZLE_WB_RAD=30 1/2"; NOZZLE_WB_RAD-2"=28 1/2"; P=18 1/2"; R=48"; R*1.1=52 13/16"; R+((B/2)+1.5")=77"; R-((B/2)+1.5")=19"; RO/2=30 3/4"; RO2/2=163 1/8"; TRANSITION=24 9/16"; TRANSITION/2=12 9/32"; TRIP_Q=330 3/4"; TRIP_Q-4.5"=326 1/4"; Type Comments=Triple Vari-Plume Laboratory Exhaust Centrifugal Airfoil Class 1 Arr 10 With Mixing Box
- Triple_490_CAVP-24L_CLASS_1_With_Mixing_Box: ((M - (2 * (D - L - K - J))) / 2) + (TRANSITION / 2)=31 3/8"; (B/2)+1.5"=29"; (B/2)-.125"=27 3/8"; (D-J-K-L)*2=2 3/4"; (E/2)-((B/2)+1.5")=22 15/32"; (E/2)-((MB_P/2)+.125")=18 11/32"; (E/2)-(E/52*15)=21 25/32"; (F-((F-H)/2))/2=27 27/32"; (M - (2 * (D - L - K - J)))/2=19 3/32"; (MB_P/2)+.125"=33 1/8"; (MB_P/2-.125")+((F / 2) - 2")=-60 23/32"; (MB_P/2-.125")-((F / 2) - 2")=-5 1/32"; (MB_Q/2)+.125"=33 1/8"; (NOZZLE_HEIGHT - (NOZZLE_HEIGHT / 8 * 2)) / 2=23 1/4"; (NOZZLE_WB_OD - NOZZLE_TOP_OD) / 4=6 1/8"; -((MB_Q / 2) + 1/8")=-33 1/8"; -(F-((F-H)/2))/2=-27 27/32"; -MB_HEIGHT=-70 3/4"; -MB_P=-66"; -MB_P-.25=-66 1/4"; A=217 13/16"; A/2=108 29/32"; B=55"; B/2=27 1/2"; B/4=13 3/4"; C=123 1/16"; C/2=61 17/32"; CLASS=1"; D=79 15/16"; D-L-K-J=1 3/8"; D-M=39"; DUAL_Q=198 3/8"; DUAL_Q+.25"=198 5/8"; E=102 15/16"; E-(NOZZLE_RAD/3*2)=39 7/8"; E-N-N-H=2"; E/2=51 15/32"; E/2-H/2=22 5/8"; E/52*15=29 11/16"; E/52*30=59 3/8"; F=59 11/16"; F/2=29 27/32"; H=57 11/16"; H/2=28 27/32"; HEIGHT=92 15/16"; J=13 1/2"; J+K+L=78 9/16"; K=21 7/8"; L=43 3/16"; M=40 15/16"; M-(2*(D-L-K-J))=38 3/16"; MB_A=191 7/8"; MB_F=15 3/4"; MB_F-3"=12 3/4"; MB_HEIGHT=70 3/4"; MB_HEIGHT/2=35 3/8"; MB_N=13 9/16"; MB_N-(D-J-K-L)=12 3/16"; MB_P=66"; MB_P+.25"=66 1/4"; MB_P+MB_P+.5=132 1/2"; MB_P-4.5"=61 1/2"; MB_Q=66"; N=20 5/8"; N+(H/2)=49 15/32"; NOZZLE_BOTTOM_ID=34 3/4"; NOZZLE_BOTTOM_RAD=17 3/8"; NOZZLE_BOTTOM_RAD-3*2=11 3/8"; NOZZLE_HEIGHT=62"; NOZZLE_HEIGHT/7*2=15 1/2"; NOZZLE_SIZE=24"; NOZZLE_TOP_OD=36 1/2"; NOZZLE_TOP_RAD=18 1/4"; NOZZLE_WB/4=12 3/16"; NOZZLE_WB_OD=61"; NOZZLE_WB_RAD=30 1/2"; NOZZLE_WB_RAD-2"=28 1/2"; P=18 1/2"; R=48"; R*1.1=52 13/16"; R+((B/2)+1.5")=77"; R-((B/2)+1.5")=19"; RO/2=30 3/4"; RO2/2=163 1/8"; TRANSITION=24 9/16"; TRANSITION/2=12 9/32"; TRIP_Q=330 3/4"; TRIP_Q-4.5"=326 1/4"; Type Comments=Triple Vari-Plume Laboratory Exhaust Centrifugal Airfoil Class 1 Arr 10 With Mixing Box
- Triple_490_CAVP-30H_CLASS_1_With_Mixing_Box: ((M - (2 * (D - L - K - J))) / 2) + (TRANSITION / 2)=34 1/8"; (B/2)+1.5"=29"; (B/2)-.125"=27 3/8"; (D-J-K-L)*2=2 3/4"; (E/2)-((B/2)+1.5")=22 15/32"; (E/2)-((MB_P/2)+.125")=18 11/32"; (E/2)-(E/52*15)=21 25/32"; (F-((F-H)/2))/2=27 27/32"; (M - (2 * (D - L - K - J)))/2=19 3/32"; (MB_P/2)+.125"=33 1/8"; (MB_P/2-.125")+((F / 2) - 2")=-60 23/32"; (MB_P/2-.125")-((F / 2) - 2")=-5 1/32"; (MB_Q/2)+.125"=33 1/8"; (NOZZLE_HEIGHT - (NOZZLE_HEIGHT / 8 * 2)) / 2=29 1/4"; (NOZZLE_WB_OD - NOZZLE_TOP_OD) / 4=7 1/8"; -((MB_Q / 2) + 1/8")=-33 1/8"; -(F-((F-H)/2))/2=-27 27/32"; -MB_HEIGHT=-70 3/4"; -MB_P=-66"; -MB_P-.25=-66 1/4"; A=217 13/16"; A/2=108 29/32"; B=55"; B/2=27 1/2"; B/4=13 3/4"; C=123 1/16"; C/2=61 17/32"; CLASS=1"; D=79 15/16"; D-L-K-J=1 3/8"; D-M=39"; DUAL_Q=198 3/8"; DUAL_Q+.25"=198 5/8"; E=102 15/16"; E-(NOZZLE_RAD/3*2)=37 5/16"; E-N-N-H=2"; E/2=51 15/32"; E/2-H/2=22 5/8"; E/52*15=29 11/16"; E/52*30=59 3/8"; F=59 11/16"; F/2=29 27/32"; H=57 11/16"; H/2=28 27/32"; HEIGHT=92 15/16"; J=13 1/2"; J+K+L=78 9/16"; K=21 7/8"; L=43 3/16"; M=40 15/16"; M-(2*(D-L-K-J))=38 3/16"; MB_A=191 7/8"; MB_F=15 3/4"; MB_F-3"=12 3/4"; MB_HEIGHT=70 3/4"; MB_HEIGHT/2=35 3/8"; MB_N=13 9/16"; MB_N-(D-J-K-L)=12 3/16"; MB_P=66"; MB_P+.25"=66 1/4"; MB_P+MB_P+.5=132 1/2"; MB_P-4.5"=61 1/2"; MB_Q=66"; N=20 5/8"; N+(H/2)=49 15/32"; NOZZLE_BOTTOM_ID=42 1/2"; NOZZLE_BOTTOM_RAD=21 1/4"; NOZZLE_BOTTOM_RAD-3*2=15 1/4"; NOZZLE_HEIGHT=78"; NOZZLE_HEIGHT/7*2=19 1/2"; NOZZLE_SIZE=30"; NOZZLE_TOP_OD=45 1/2"; NOZZLE_TOP_RAD=22 3/4"; NOZZLE_WB/4=14 13/16"; NOZZLE_WB_OD=74"; NOZZLE_WB_RAD=37"; NOZZLE_WB_RAD-2"=35"; P=18 1/2"; R=48"; R*1.1=52 13/16"; R+((B/2)+1.5")=77"; R-((B/2)+1.5")=19"; RO/2=30 3/4"; RO2/2=163 1/8"; TRANSITION=30 1/16"; TRANSITION/2=15 1/32"; TRIP_Q=330 3/4"; TRIP_Q-4.5"=326 1/4"; Type Comments=Triple Vari-Plume Laboratory Exhaust Centrifugal Airfoil Class 1 Arr 10 With Mixing Box
- Triple_490_CAVP-30L_CLASS_1_With_Mixing_Box: ((M - (2 * (D - L - K - J))) / 2) + (TRANSITION / 2)=34 1/8"; (B/2)+1.5"=29"; (B/2)-.125"=27 3/8"; (D-J-K-L)*2=2 3/4"; (E/2)-((B/2)+1.5")=22 15/32"; (E/2)-((MB_P/2)+.125")=18 11/32"; (E/2)-(E/52*15)=21 25/32"; (F-((F-H)/2))/2=27 27/32"; (M - (2 * (D - L - K - J)))/2=19 3/32"; (MB_P/2)+.125"=33 1/8"; (MB_P/2-.125")+((F / 2) - 2")=-60 23/32"; (MB_P/2-.125")-((F / 2) - 2")=-5 1/32"; (MB_Q/2)+.125"=33 1/8"; (NOZZLE_HEIGHT - (NOZZLE_HEIGHT / 8 * 2)) / 2=29 1/4"; (NOZZLE_WB_OD - NOZZLE_TOP_OD) / 4=7 1/8"; -((MB_Q / 2) + 1/8")=-33 1/8"; -(F-((F-H)/2))/2=-27 27/32"; -MB_HEIGHT=-70 3/4"; -MB_P=-66"; -MB_P-.25=-66 1/4"; A=217 13/16"; A/2=108 29/32"; B=55"; B/2=27 1/2"; B/4=13 3/4"; C=123 1/16"; C/2=61 17/32"; CLASS=1"; D=79 15/16"; D-L-K-J=1 3/8"; D-M=39"; DUAL_Q=198 3/8"; DUAL_Q+.25"=198 5/8"; E=102 15/16"; E-(NOZZLE_RAD/3*2)=37 5/16"; E-N-N-H=2"; E/2=51 15/32"; E/2-H/2=22 5/8"; E/52*15=29 11/16"; E/52*30=59 3/8"; F=59 11/16"; F/2=29 27/32"; H=57 11/16"; H/2=28 27/32"; HEIGHT=92 15/16"; J=13 1/2"; J+K+L=78 9/16"; K=21 7/8"; L=43 3/16"; M=40 15/16"; M-(2*(D-L-K-J))=38 3/16"; MB_A=191 7/8"; MB_F=15 3/4"; MB_F-3"=12 3/4"; MB_HEIGHT=70 3/4"; MB_HEIGHT/2=35 3/8"; MB_N=13 9/16"; MB_N-(D-J-K-L)=12 3/16"; MB_P=66"; MB_P+.25"=66 1/4"; MB_P+MB_P+.5=132 1/2"; MB_P-4.5"=61 1/2"; MB_Q=66"; N=20 5/8"; N+(H/2)=49 15/32"; NOZZLE_BOTTOM_ID=42 1/2"; NOZZLE_BOTTOM_RAD=21 1/4"; NOZZLE_BOTTOM_RAD-3*2=15 1/4"; NOZZLE_HEIGHT=78"; NOZZLE_HEIGHT/7*2=19 1/2"; NOZZLE_SIZE=30"; NOZZLE_TOP_OD=45 1/2"; NOZZLE_TOP_RAD=22 3/4"; NOZZLE_WB/4=14 13/16"; NOZZLE_WB_OD=74"; NOZZLE_WB_RAD=37"; NOZZLE_WB_RAD-2"=35"; P=18 1/2"; R=48"; R*1.1=52 13/16"; R+((B/2)+1.5")=77"; R-((B/2)+1.5")=19"; RO/2=30 3/4"; RO2/2=163 1/8"; TRANSITION=30 1/16"; TRANSITION/2=15 1/32"; TRIP_Q=330 3/4"; TRIP_Q-4.5"=326 1/4"; Type Comments=Triple Vari-Plume Laboratory Exhaust Centrifugal Airfoil Class 1 Arr 10 With Mixing Box
- Triple_490_CAVP-36H_CLASS_1_With_Mixing_Box: ((M - (2 * (D - L - K - J))) / 2) + (TRANSITION / 2)=37 3/8"; (B/2)+1.5"=29"; (B/2)-.125"=27 3/8"; (D-J-K-L)*2=2 3/4"; (E/2)-((B/2)+1.5")=22 15/32"; (E/2)-((MB_P/2)+.125")=18 11/32"; (E/2)-(E/52*15)=21 25/32"; (F-((F-H)/2))/2=27 27/32"; (M - (2 * (D - L - K - J)))/2=19 3/32"; (MB_P/2)+.125"=33 1/8"; (MB_P/2-.125")+((F / 2) - 2")=-60 23/32"; (MB_P/2-.125")-((F / 2) - 2")=-5 1/32"; (MB_Q/2)+.125"=33 1/8"; (NOZZLE_HEIGHT - (NOZZLE_HEIGHT / 8 * 2)) / 2=35 5/8"; (NOZZLE_WB_OD - NOZZLE_TOP_OD) / 4=8"; -((MB_Q / 2) + 1/8")=-33 1/8"; -(F-((F-H)/2))/2=-27 27/32"; -MB_HEIGHT=-70 3/4"; -MB_P=-66"; -MB_P-.25=-66 1/4"; A=217 13/16"; A/2=108 29/32"; B=55"; B/2=27 1/2"; B/4=13 3/4"; C=123 1/16"; C/2=61 17/32"; CLASS=1"; D=79 15/16"; D-L-K-J=1 3/8"; D-M=39"; DUAL_Q=198 3/8"; DUAL_Q+.25"=198 5/8"; E=102 15/16"; E-(NOZZLE_RAD/3*2)=34 7/32"; E-N-N-H=2"; E/2=51 15/32"; E/2-H/2=22 5/8"; E/52*15=29 11/16"; E/52*30=59 3/8"; F=59 11/16"; F/2=29 27/32"; H=57 11/16"; H/2=28 27/32"; HEIGHT=92 15/16"; J=13 1/2"; J+K+L=78 9/16"; K=21 7/8"; L=43 3/16"; M=40 15/16"; M-(2*(D-L-K-J))=38 3/16"; MB_A=191 7/8"; MB_F=15 3/4"; MB_F-3"=12 3/4"; MB_HEIGHT=70 3/4"; MB_HEIGHT/2=35 3/8"; MB_N=13 9/16"; MB_N-(D-J-K-L)=12 3/16"; MB_P=66"; MB_P+.25"=66 1/4"; MB_P+MB_P+.5=132 1/2"; MB_P-4.5"=61 1/2"; MB_Q=66"; N=20 5/8"; N+(H/2)=49 15/32"; NOZZLE_BOTTOM_ID=51 3/4"; NOZZLE_BOTTOM_RAD=25 7/8"; NOZZLE_BOTTOM_RAD-3*2=19 7/8"; NOZZLE_HEIGHT=95"; NOZZLE_HEIGHT/7*2=23 3/4"; NOZZLE_SIZE=36"; NOZZLE_TOP_OD=58"; NOZZLE_TOP_RAD=29"; NOZZLE_WB/4=18"; NOZZLE_WB_OD=90"; NOZZLE_WB_RAD=45"; NOZZLE_WB_RAD-2"=43"; P=18 1/2"; R=48"; R*1.1=52 13/16"; R+((B/2)+1.5")=77"; R-((B/2)+1.5")=19"; RO/2=30 3/4"; RO2/2=163 1/8"; TRANSITION=36 19/32"; TRANSITION/2=18 9/32"; TRIP_Q=330 3/4"; TRIP_Q-4.5"=326 1/4"; Type Comments=Triple Vari-Plume Laboratory Exhaust Centrifugal Airfoil Class 1 Arr 10 With Mixing Box
- Triple_490_CAVP-36L_CLASS_1_With_Mixing_Box: ((M - (2 * (D - L - K - J))) / 2) + (TRANSITION / 2)=37 3/8"; (B/2)+1.5"=29"; (B/2)-.125"=27 3/8"; (D-J-K-L)*2=2 3/4"; (E/2)-((B/2)+1.5")=22 15/32"; (E/2)-((MB_P/2)+.125")=18 11/32"; (E/2)-(E/52*15)=21 25/32"; (F-((F-H)/2))/2=27 27/32"; (M - (2 * (D - L - K - J)))/2=19 3/32"; (MB_P/2)+.125"=33 1/8"; (MB_P/2-.125")+((F / 2) - 2")=-60 23/32"; (MB_P/2-.125")-((F / 2) - 2")=-5 1/32"; (MB_Q/2)+.125"=33 1/8"; (NOZZLE_HEIGHT - (NOZZLE_HEIGHT / 8 * 2)) / 2=35 5/8"; (NOZZLE_WB_OD - NOZZLE_TOP_OD) / 4=8"; -((MB_Q / 2) + 1/8")=-33 1/8"; -(F-((F-H)/2))/2=-27 27/32"; -MB_HEIGHT=-70 3/4"; -MB_P=-66"; -MB_P-.25=-66 1/4"; A=217 13/16"; A/2=108 29/32"; B=55"; B/2=27 1/2"; B/4=13 3/4"; C=123 1/16"; C/2=61 17/32"; CLASS=1"; D=79 15/16"; D-L-K-J=1 3/8"; D-M=39"; DUAL_Q=198 3/8"; DUAL_Q+.25"=198 5/8"; E=102 15/16"; E-(NOZZLE_RAD/3*2)=34 7/32"; E-N-N-H=2"; E/2=51 15/32"; E/2-H/2=22 5/8"; E/52*15=29 11/16"; E/52*30=59 3/8"; F=59 11/16"; F/2=29 27/32"; H=57 11/16"; H/2=28 27/32"; HEIGHT=92 15/16"; J=13 1/2"; J+K+L=78 9/16"; K=21 7/8"; L=43 3/16"; M=40 15/16"; M-(2*(D-L-K-J))=38 3/16"; MB_A=191 7/8"; MB_F=15 3/4"; MB_F-3"=12 3/4"; MB_HEIGHT=70 3/4"; MB_HEIGHT/2=35 3/8"; MB_N=13 9/16"; MB_N-(D-J-K-L)=12 3/16"; MB_P=66"; MB_P+.25"=66 1/4"; MB_P+MB_P+.5=132 1/2"; MB_P-4.5"=61 1/2"; MB_Q=66"; N=20 5/8"; N+(H/2)=49 15/32"; NOZZLE_BOTTOM_ID=51 3/4"; NOZZLE_BOTTOM_RAD=25 7/8"; NOZZLE_BOTTOM_RAD-3*2=19 7/8"; NOZZLE_HEIGHT=95"; NOZZLE_HEIGHT/7*2=23 3/4"; NOZZLE_SIZE=36"; NOZZLE_TOP_OD=58"; NOZZLE_TOP_RAD=29"; NOZZLE_WB/4=18"; NOZZLE_WB_OD=90"; NOZZLE_WB_RAD=45"; NOZZLE_WB_RAD-2"=43"; P=18 1/2"; R=48"; R*1.1=52 13/16"; R+((B/2)+1.5")=77"; R-((B/2)+1.5")=19"; RO/2=30 3/4"; RO2/2=163 1/8"; TRANSITION=36 19/32"; TRANSITION/2=18 9/32"; TRIP_Q=330 3/4"; TRIP_Q-4.5"=326 1/4"; Type Comments=Triple Vari-Plume Laboratory Exhaust Centrifugal Airfoil Class 1 Arr 10 With Mixing Box
- Triple_490_CAVP-24H_CLASS_2_With_Mixing_Box: ((M - (2 * (D - L - K - J))) / 2) + (TRANSITION / 2)=31 3/8"; (B/2)+1.5"=29"; (B/2)-.125"=27 3/8"; (D-J-K-L)*2=2 3/4"; (E/2)-((B/2)+1.5")=22 15/32"; (E/2)-((MB_P/2)+.125")=18 11/32"; (E/2)-(E/52*15)=21 25/32"; (F-((F-H)/2))/2=27 27/32"; (M - (2 * (D - L - K - J)))/2=19 3/32"; (MB_P/2)+.125"=33 1/8"; (MB_P/2-.125")+((F / 2) - 2")=-60 23/32"; (MB_P/2-.125")-((F / 2) - 2")=-5 1/32"; (MB_Q/2)+.125"=33 1/8"; (NOZZLE_HEIGHT - (NOZZLE_HEIGHT / 8 * 2)) / 2=23 1/4"; (NOZZLE_WB_OD - NOZZLE_TOP_OD) / 4=6 1/8"; -((MB_Q / 2) + 1/8")=-33 1/8"; -(F-((F-H)/2))/2=-27 27/32"; -MB_HEIGHT=-70 3/4"; -MB_P=-66"; -MB_P-.25=-66 1/4"; A=217 13/16"; A/2=108 29/32"; B=55"; B/2=27 1/2"; B/4=13 3/4"; C=123 1/16"; C/2=61 17/32"; CLASS=2"; D=83 15/16"; D-L-K-J=1 3/8"; D-M=43"; DUAL_Q=198 3/8"; DUAL_Q+.25"=198 5/8"; E=102 15/16"; E-(NOZZLE_RAD/3*2)=39 7/8"; E-N-N-H=2"; E/2=51 15/32"; E/2-H/2=22 5/8"; E/52*15=29 11/16"; E/52*30=59 3/8"; F=59 11/16"; F/2=29 27/32"; H=57 11/16"; H/2=28 27/32"; HEIGHT=92 15/16"; J=13 1/2"; J+K+L=82 9/16"; K=25 7/8"; L=43 3/16"; M=40 15/16"; M-(2*(D-L-K-J))=38 3/16"; MB_A=195 7/8"; MB_F=15 3/4"; MB_F-3"=12 3/4"; MB_HEIGHT=70 3/4"; MB_HEIGHT/2=35 3/8"; MB_N=13 9/16"; MB_N-(D-J-K-L)=12 3/16"; MB_P=66"; MB_P+.25"=66 1/4"; MB_P+MB_P+.5=132 1/2"; MB_P-4.5"=61 1/2"; MB_Q=66"; N=20 5/8"; N+(H/2)=49 15/32"; NOZZLE_BOTTOM_ID=34 3/4"; NOZZLE_BOTTOM_RAD=17 3/8"; NOZZLE_BOTTOM_RAD-3*2=11 3/8"; NOZZLE_HEIGHT=62"; NOZZLE_HEIGHT/7*2=15 1/2"; NOZZLE_SIZE=24"; NOZZLE_TOP_OD=36 1/2"; NOZZLE_TOP_RAD=18 1/4"; NOZZLE_WB/4=12 3/16"; NOZZLE_WB_OD=61"; NOZZLE_WB_RAD=30 1/2"; NOZZLE_WB_RAD-2"=28 1/2"; P=21 7/8"; R=48"; R*1.1=52 13/16"; R+((B/2)+1.5")=77"; R-((B/2)+1.5")=19"; RO/2=30 3/4"; RO2/2=163 1/8"; TRANSITION=24 9/16"; TRANSITION/2=12 9/32"; TRIP_Q=330 3/4"; TRIP_Q-4.5"=326 1/4"; Type Comments=Triple Vari-Plume Laboratory Exhaust Centrifugal Airfoil Class 2 Arr 10 With Mixing Box
- Triple_490_CAVP-24L_CLASS_2_With_Mixing_Box: ((M - (2 * (D - L - K - J))) / 2) + (TRANSITION / 2)=31 3/8"; (B/2)+1.5"=29"; (B/2)-.125"=27 3/8"; (D-J-K-L)*2=2 3/4"; (E/2)-((B/2)+1.5")=22 15/32"; (E/2)-((MB_P/2)+.125")=18 11/32"; (E/2)-(E/52*15)=21 25/32"; (F-((F-H)/2))/2=27 27/32"; (M - (2 * (D - L - K - J)))/2=19 3/32"; (MB_P/2)+.125"=33 1/8"; (MB_P/2-.125")+((F / 2) - 2")=-60 23/32"; (MB_P/2-.125")-((F / 2) - 2")=-5 1/32"; (MB_Q/2)+.125"=33 1/8"; (NOZZLE_HEIGHT - (NOZZLE_HEIGHT / 8 * 2)) / 2=23 1/4"; (NOZZLE_WB_OD - NOZZLE_TOP_OD) / 4=6 1/8"; -((MB_Q / 2) + 1/8")=-33 1/8"; -(F-((F-H)/2))/2=-27 27/32"; -MB_HEIGHT=-70 3/4"; -MB_P=-66"; -MB_P-.25=-66 1/4"; A=217 13/16"; A/2=108 29/32"; B=55"; B/2=27 1/2"; B/4=13 3/4"; C=123 1/16"; C/2=61 17/32"; CLASS=2"; D=83 15/16"; D-L-K-J=1 3/8"; D-M=43"; DUAL_Q=198 3/8"; DUAL_Q+.25"=198 5/8"; E=102 15/16"; E-(NOZZLE_RAD/3*2)=39 7/8"; E-N-N-H=2"; E/2=51 15/32"; E/2-H/2=22 5/8"; E/52*15=29 11/16"; E/52*30=59 3/8"; F=59 11/16"; F/2=29 27/32"; H=57 11/16"; H/2=28 27/32"; HEIGHT=92 15/16"; J=13 1/2"; J+K+L=82 9/16"; K=25 7/8"; L=43 3/16"; M=40 15/16"; M-(2*(D-L-K-J))=38 3/16"; MB_A=195 7/8"; MB_F=15 3/4"; MB_F-3"=12 3/4"; MB_HEIGHT=70 3/4"; MB_HEIGHT/2=35 3/8"; MB_N=13 9/16"; MB_N-(D-J-K-L)=12 3/16"; MB_P=66"; MB_P+.25"=66 1/4"; MB_P+MB_P+.5=132 1/2"; MB_P-4.5"=61 1/2"; MB_Q=66"; N=20 5/8"; N+(H/2)=49 15/32"; NOZZLE_BOTTOM_ID=34 3/4"; NOZZLE_BOTTOM_RAD=17 3/8"; NOZZLE_BOTTOM_RAD-3*2=11 3/8"; NOZZLE_HEIGHT=62"; NOZZLE_HEIGHT/7*2=15 1/2"; NOZZLE_SIZE=24"; NOZZLE_TOP_OD=36 1/2"; NOZZLE_TOP_RAD=18 1/4"; NOZZLE_WB/4=12 3/16"; NOZZLE_WB_OD=61"; NOZZLE_WB_RAD=30 1/2"; NOZZLE_WB_RAD-2"=28 1/2"; P=21 7/8"; R=48"; R*1.1=52 13/16"; R+((B/2)+1.5")=77"; R-((B/2)+1.5")=19"; RO/2=30 3/4"; RO2/2=163 1/8"; TRANSITION=24 9/16"; TRANSITION/2=12 9/32"; TRIP_Q=330 3/4"; TRIP_Q-4.5"=326 1/4"; Type Comments=Triple Vari-Plume Laboratory Exhaust Centrifugal Airfoil Class 2 Arr 10 With Mixing Box
- Triple_490_CAVP-30H_CLASS_2_With_Mixing_Box: ((M - (2 * (D - L - K - J))) / 2) + (TRANSITION / 2)=34 1/8"; (B/2)+1.5"=29"; (B/2)-.125"=27 3/8"; (D-J-K-L)*2=2 3/4"; (E/2)-((B/2)+1.5")=22 15/32"; (E/2)-((MB_P/2)+.125")=18 11/32"; (E/2)-(E/52*15)=21 25/32"; (F-((F-H)/2))/2=27 27/32"; (M - (2 * (D - L - K - J)))/2=19 3/32"; (MB_P/2)+.125"=33 1/8"; (MB_P/2-.125")+((F / 2) - 2")=-60 23/32"; (MB_P/2-.125")-((F / 2) - 2")=-5 1/32"; (MB_Q/2)+.125"=33 1/8"; (NOZZLE_HEIGHT - (NOZZLE_HEIGHT / 8 * 2)) / 2=29 1/4"; (NOZZLE_WB_OD - NOZZLE_TOP_OD) / 4=7 1/8"; -((MB_Q / 2) + 1/8")=-33 1/8"; -(F-((F-H)/2))/2=-27 27/32"; -MB_HEIGHT=-70 3/4"; -MB_P=-66"; -MB_P-.25=-66 1/4"; A=217 13/16"; A/2=108 29/32"; B=55"; B/2=27 1/2"; B/4=13 3/4"; C=123 1/16"; C/2=61 17/32"; CLASS=2"; D=83 15/16"; D-L-K-J=1 3/8"; D-M=43"; DUAL_Q=198 3/8"; DUAL_Q+.25"=198 5/8"; E=102 15/16"; E-(NOZZLE_RAD/3*2)=37 5/16"; E-N-N-H=2"; E/2=51 15/32"; E/2-H/2=22 5/8"; E/52*15=29 11/16"; E/52*30=59 3/8"; F=59 11/16"; F/2=29 27/32"; H=57 11/16"; H/2=28 27/32"; HEIGHT=92 15/16"; J=13 1/2"; J+K+L=82 9/16"; K=25 7/8"; L=43 3/16"; M=40 15/16"; M-(2*(D-L-K-J))=38 3/16"; MB_A=195 7/8"; MB_F=15 3/4"; MB_F-3"=12 3/4"; MB_HEIGHT=70 3/4"; MB_HEIGHT/2=35 3/8"; MB_N=13 9/16"; MB_N-(D-J-K-L)=12 3/16"; MB_P=66"; MB_P+.25"=66 1/4"; MB_P+MB_P+.5=132 1/2"; MB_P-4.5"=61 1/2"; MB_Q=66"; N=20 5/8"; N+(H/2)=49 15/32"; NOZZLE_BOTTOM_ID=42 1/2"; NOZZLE_BOTTOM_RAD=21 1/4"; NOZZLE_BOTTOM_RAD-3*2=15 1/4"; NOZZLE_HEIGHT=78"; NOZZLE_HEIGHT/7*2=19 1/2"; NOZZLE_SIZE=30"; NOZZLE_TOP_OD=45 1/2"; NOZZLE_TOP_RAD=22 3/4"; NOZZLE_WB/4=14 13/16"; NOZZLE_WB_OD=74"; NOZZLE_WB_RAD=37"; NOZZLE_WB_RAD-2"=35"; P=21 7/8"; R=48"; R*1.1=52 13/16"; R+((B/2)+1.5")=77"; R-((B/2)+1.5")=19"; RO/2=30 3/4"; RO2/2=163 1/8"; TRANSITION=30 1/16"; TRANSITION/2=15 1/32"; TRIP_Q=330 3/4"; TRIP_Q-4.5"=326 1/4"; Type Comments=Triple Vari-Plume Laboratory Exhaust Centrifugal Airfoil Class 2 Arr 10 With Mixing Box
- Triple_490_CAVP-30L_CLASS_2_With_Mixing_Box: ((M - (2 * (D - L - K - J))) / 2) + (TRANSITION / 2)=34 1/8"; (B/2)+1.5"=29"; (B/2)-.125"=27 3/8"; (D-J-K-L)*2=2 3/4"; (E/2)-((B/2)+1.5")=22 15/32"; (E/2)-((MB_P/2)+.125")=18 11/32"; (E/2)-(E/52*15)=21 25/32"; (F-((F-H)/2))/2=27 27/32"; (M - (2 * (D - L - K - J)))/2=19 3/32"; (MB_P/2)+.125"=33 1/8"; (MB_P/2-.125")+((F / 2) - 2")=-60 23/32"; (MB_P/2-.125")-((F / 2) - 2")=-5 1/32"; (MB_Q/2)+.125"=33 1/8"; (NOZZLE_HEIGHT - (NOZZLE_HEIGHT / 8 * 2)) / 2=29 1/4"; (NOZZLE_WB_OD - NOZZLE_TOP_OD) / 4=7 1/8"; -((MB_Q / 2) + 1/8")=-33 1/8"; -(F-((F-H)/2))/2=-27 27/32"; -MB_HEIGHT=-70 3/4"; -MB_P=-66"; -MB_P-.25=-66 1/4"; A=217 13/16"; A/2=108 29/32"; B=55"; B/2=27 1/2"; B/4=13 3/4"; C=123 1/16"; C/2=61 17/32"; CLASS=2"; D=83 15/16"; D-L-K-J=1 3/8"; D-M=43"; DUAL_Q=198 3/8"; DUAL_Q+.25"=198 5/8"; E=102 15/16"; E-(NOZZLE_RAD/3*2)=37 5/16"; E-N-N-H=2"; E/2=51 15/32"; E/2-H/2=22 5/8"; E/52*15=29 11/16"; E/52*30=59 3/8"; F=59 11/16"; F/2=29 27/32"; H=57 11/16"; H/2=28 27/32"; HEIGHT=92 15/16"; J=13 1/2"; J+K+L=82 9/16"; K=25 7/8"; L=43 3/16"; M=40 15/16"; M-(2*(D-L-K-J))=38 3/16"; MB_A=195 7/8"; MB_F=15 3/4"; MB_F-3"=12 3/4"; MB_HEIGHT=70 3/4"; MB_HEIGHT/2=35 3/8"; MB_N=13 9/16"; MB_N-(D-J-K-L)=12 3/16"; MB_P=66"; MB_P+.25"=66 1/4"; MB_P+MB_P+.5=132 1/2"; MB_P-4.5"=61 1/2"; MB_Q=66"; N=20 5/8"; N+(H/2)=49 15/32"; NOZZLE_BOTTOM_ID=42 1/2"; NOZZLE_BOTTOM_RAD=21 1/4"; NOZZLE_BOTTOM_RAD-3*2=15 1/4"; NOZZLE_HEIGHT=78"; NOZZLE_HEIGHT/7*2=19 1/2"; NOZZLE_SIZE=30"; NOZZLE_TOP_OD=45 1/2"; NOZZLE_TOP_RAD=22 3/4"; NOZZLE_WB/4=14 13/16"; NOZZLE_WB_OD=74"; NOZZLE_WB_RAD=37"; NOZZLE_WB_RAD-2"=35"; P=21 7/8"; R=48"; R*1.1=52 13/16"; R+((B/2)+1.5")=77"; R-((B/2)+1.5")=19"; RO/2=30 3/4"; RO2/2=163 1/8"; TRANSITION=30 1/16"; TRANSITION/2=15 1/32"; TRIP_Q=330 3/4"; TRIP_Q-4.5"=326 1/4"; Type Comments=Triple Vari-Plume Laboratory Exhaust Centrifugal Airfoil Class 2 Arr 10 With Mixing Box
- Triple_490_CAVP-36H_CLASS_2_With_Mixing_Box: ((M - (2 * (D - L - K - J))) / 2) + (TRANSITION / 2)=37 3/8"; (B/2)+1.5"=29"; (B/2)-.125"=27 3/8"; (D-J-K-L)*2=2 3/4"; (E/2)-((B/2)+1.5")=22 15/32"; (E/2)-((MB_P/2)+.125")=18 11/32"; (E/2)-(E/52*15)=21 25/32"; (F-((F-H)/2))/2=27 27/32"; (M - (2 * (D - L - K - J)))/2=19 3/32"; (MB_P/2)+.125"=33 1/8"; (MB_P/2-.125")+((F / 2) - 2")=-60 23/32"; (MB_P/2-.125")-((F / 2) - 2")=-5 1/32"; (MB_Q/2)+.125"=33 1/8"; (NOZZLE_HEIGHT - (NOZZLE_HEIGHT / 8 * 2)) / 2=35 5/8"; (NOZZLE_WB_OD - NOZZLE_TOP_OD) / 4=8"; -((MB_Q / 2) + 1/8")=-33 1/8"; -(F-((F-H)/2))/2=-27 27/32"; -MB_HEIGHT=-70 3/4"; -MB_P=-66"; -MB_P-.25=-66 1/4"; A=217 13/16"; A/2=108 29/32"; B=55"; B/2=27 1/2"; B/4=13 3/4"; C=123 1/16"; C/2=61 17/32"; CLASS=2"; D=83 15/16"; D-L-K-J=1 3/8"; D-M=43"; DUAL_Q=198 3/8"; DUAL_Q+.25"=198 5/8"; E=102 15/16"; E-(NOZZLE_RAD/3*2)=34 7/32"; E-N-N-H=2"; E/2=51 15/32"; E/2-H/2=22 5/8"; E/52*15=29 11/16"; E/52*30=59 3/8"; F=59 11/16"; F/2=29 27/32"; H=57 11/16"; H/2=28 27/32"; HEIGHT=92 15/16"; J=13 1/2"; J+K+L=82 9/16"; K=25 7/8"; L=43 3/16"; M=40 15/16"; M-(2*(D-L-K-J))=38 3/16"; MB_A=195 7/8"; MB_F=15 3/4"; MB_F-3"=12 3/4"; MB_HEIGHT=70 3/4"; MB_HEIGHT/2=35 3/8"; MB_N=13 9/16"; MB_N-(D-J-K-L)=12 3/16"; MB_P=66"; MB_P+.25"=66 1/4"; MB_P+MB_P+.5=132 1/2"; MB_P-4.5"=61 1/2"; MB_Q=66"; N=20 5/8"; N+(H/2)=49 15/32"; NOZZLE_BOTTOM_ID=51 3/4"; NOZZLE_BOTTOM_RAD=25 7/8"; NOZZLE_BOTTOM_RAD-3*2=19 7/8"; NOZZLE_HEIGHT=95"; NOZZLE_HEIGHT/7*2=23 3/4"; NOZZLE_SIZE=36"; NOZZLE_TOP_OD=58"; NOZZLE_TOP_RAD=29"; NOZZLE_WB/4=18"; NOZZLE_WB_OD=90"; NOZZLE_WB_RAD=45"; NOZZLE_WB_RAD-2"=43"; P=21 7/8"; R=48"; R*1.1=52 13/16"; R+((B/2)+1.5")=77"; R-((B/2)+1.5")=19"; RO/2=30 3/4"; RO2/2=163 1/8"; TRANSITION=36 19/32"; TRANSITION/2=18 9/32"; TRIP_Q=330 3/4"; TRIP_Q-4.5"=326 1/4"; Type Comments=Triple Vari-Plume Laboratory Exhaust Centrifugal Airfoil Class 2 Arr 10 With Mixing Box
- Triple_490_CAVP-36L_CLASS_2_With_Mixing_Box: ((M - (2 * (D - L - K - J))) / 2) + (TRANSITION / 2)=37 3/8"; (B/2)+1.5"=29"; (B/2)-.125"=27 3/8"; (D-J-K-L)*2=2 3/4"; (E/2)-((B/2)+1.5")=22 15/32"; (E/2)-((MB_P/2)+.125")=18 11/32"; (E/2)-(E/52*15)=21 25/32"; (F-((F-H)/2))/2=27 27/32"; (M - (2 * (D - L - K - J)))/2=19 3/32"; (MB_P/2)+.125"=33 1/8"; (MB_P/2-.125")+((F / 2) - 2")=-60 23/32"; (MB_P/2-.125")-((F / 2) - 2")=-5 1/32"; (MB_Q/2)+.125"=33 1/8"; (NOZZLE_HEIGHT - (NOZZLE_HEIGHT / 8 * 2)) / 2=35 5/8"; (NOZZLE_WB_OD - NOZZLE_TOP_OD) / 4=8"; -((MB_Q / 2) + 1/8")=-33 1/8"; -(F-((F-H)/2))/2=-27 27/32"; -MB_HEIGHT=-70 3/4"; -MB_P=-66"; -MB_P-.25=-66 1/4"; A=217 13/16"; A/2=108 29/32"; B=55"; B/2=27 1/2"; B/4=13 3/4"; C=123 1/16"; C/2=61 17/32"; CLASS=2"; D=83 15/16"; D-L-K-J=1 3/8"; D-M=43"; DUAL_Q=198 3/8"; DUAL_Q+.25"=198 5/8"; E=102 15/16"; E-(NOZZLE_RAD/3*2)=34 7/32"; E-N-N-H=2"; E/2=51 15/32"; E/2-H/2=22 5/8"; E/52*15=29 11/16"; E/52*30=59 3/8"; F=59 11/16"; F/2=29 27/32"; H=57 11/16"; H/2=28 27/32"; HEIGHT=92 15/16"; J=13 1/2"; J+K+L=82 9/16"; K=25 7/8"; L=43 3/16"; M=40 15/16"; M-(2*(D-L-K-J))=38 3/16"; MB_A=195 7/8"; MB_F=15 3/4"; MB_F-3"=12 3/4"; MB_HEIGHT=70 3/4"; MB_HEIGHT/2=35 3/8"; MB_N=13 9/16"; MB_N-(D-J-K-L)=12 3/16"; MB_P=66"; MB_P+.25"=66 1/4"; MB_P+MB_P+.5=132 1/2"; MB_P-4.5"=61 1/2"; MB_Q=66"; N=20 5/8"; N+(H/2)=49 15/32"; NOZZLE_BOTTOM_ID=51 3/4"; NOZZLE_BOTTOM_RAD=25 7/8"; NOZZLE_BOTTOM_RAD-3*2=19 7/8"; NOZZLE_HEIGHT=95"; NOZZLE_HEIGHT/7*2=23 3/4"; NOZZLE_SIZE=36"; NOZZLE_TOP_OD=58"; NOZZLE_TOP_RAD=29"; NOZZLE_WB/4=18"; NOZZLE_WB_OD=90"; NOZZLE_WB_RAD=45"; NOZZLE_WB_RAD-2"=43"; P=21 7/8"; R=48"; R*1.1=52 13/16"; R+((B/2)+1.5")=77"; R-((B/2)+1.5")=19"; RO/2=30 3/4"; RO2/2=163 1/8"; TRANSITION=36 19/32"; TRANSITION/2=18 9/32"; TRIP_Q=330 3/4"; TRIP_Q-4.5"=326 1/4"; Type Comments=Triple Vari-Plume Laboratory Exhaust Centrifugal Airfoil Class 2 Arr 10 With Mixing Box
- Triple_540_CAVP-30H_CLASS_1_With_Mixing_Box: ((M - (2 * (D - L - K - J))) / 2) + (TRANSITION / 2)=36 1/32"; (B/2)+1.5"=31 1/2"; (B/2)-.125"=29 7/8"; (D-J-K-L)*2=2 3/4"; (E/2)-((B/2)+1.5")=25 3/32"; (E/2)-((MB_P/2)+.125")=20 31/32"; (E/2)-(E/52*15)=23 15/16"; (F-((F-H)/2))/2=30 11/32"; (M - (2 * (D - L - K - J)))/2=21"; (MB_P/2)+.125"=35 5/8"; (MB_P/2-.125")+((F / 2) - 2")=-65 23/32"; (MB_P/2-.125")-((F / 2) - 2")=-5 1/32"; (MB_Q/2)+.125"=35 5/8"; (NOZZLE_HEIGHT - (NOZZLE_HEIGHT / 8 * 2)) / 2=29 1/4"; (NOZZLE_WB_OD - NOZZLE_TOP_OD) / 4=7 1/8"; -((MB_Q / 2) + 1/8")=-35 5/8"; -(F-((F-H)/2))/2=-30 11/32"; -MB_HEIGHT=-76"; -MB_P=-71"; -MB_P-.25=-71 1/4"; A=231 5/16"; A/2=115 21/32"; B=60"; B/2=30"; B/4=15"; C=136 9/16"; C/2=68 9/32"; CLASS=1"; D=88 1/4"; D-L-K-J=1 3/8"; D-M=43 1/2"; DUAL_Q=213 3/8"; DUAL_Q+.25"=213 5/8"; E=113 3/16"; E-(NOZZLE_RAD/3*2)=42 7/16"; E-N-N-H=2"; E/2=56 19/32"; E/2-H/2=25 1/4"; E/52*15=32 21/32"; E/52*30=65 5/16"; F=64 11/16"; F/2=32 11/32"; H=62 11/16"; H/2=31 11/32"; HEIGHT=102 7/16"; J=14"; J+K+L=86 7/8"; K=25 7/8"; L=47"; M=44 3/4"; M-(2*(D-L-K-J))=42"; MB_A=208 5/8"; MB_F=18 1/4"; MB_F-3"=15 1/4"; MB_HEIGHT=76"; MB_HEIGHT/2=38"; MB_N=13 5/8"; MB_N-(D-J-K-L)=12 1/4"; MB_P=71"; MB_P+.25"=71 1/4"; MB_P+MB_P+.5=142 1/2"; MB_P-4.5"=66 1/2"; MB_Q=71"; N=23 1/4"; N+(H/2)=54 19/32"; NOZZLE_BOTTOM_ID=42 1/2"; NOZZLE_BOTTOM_RAD=21 1/4"; NOZZLE_BOTTOM_RAD-3*2=15 1/4"; NOZZLE_HEIGHT=78"; NOZZLE_HEIGHT/7*2=19 1/2"; NOZZLE_SIZE=30"; NOZZLE_TOP_OD=45 1/2"; NOZZLE_TOP_RAD=22 3/4"; NOZZLE_WB/4=14 13/16"; NOZZLE_WB_OD=74"; NOZZLE_WB_RAD=37"; NOZZLE_WB_RAD-2"=35"; P=18 1/2"; R=53"; R*1.1=58 5/16"; R+((B/2)+1.5")=84 1/2"; R-((B/2)+1.5")=21 1/2"; RO/2=33 1/4"; RO2/2=175 5/8"; TRANSITION=30 1/16"; TRANSITION/2=15 1/32"; TRIP_Q=355 3/4"; TRIP_Q-4.5"=351 1/4"; Type Comments=Triple Vari-Plume Laboratory Exhaust Centrifugal Airfoil Class 1 Arr 10 With Mixing Box
- Triple_540_CAVP-30L_CLASS_1_With_Mixing_Box: ((M - (2 * (D - L - K - J))) / 2) + (TRANSITION / 2)=36 1/32"; (B/2)+1.5"=31 1/2"; (B/2)-.125"=29 7/8"; (D-J-K-L)*2=2 3/4"; (E/2)-((B/2)+1.5")=25 3/32"; (E/2)-((MB_P/2)+.125")=20 31/32"; (E/2)-(E/52*15)=23 15/16"; (F-((F-H)/2))/2=30 11/32"; (M - (2 * (D - L - K - J)))/2=21"; (MB_P/2)+.125"=35 5/8"; (MB_P/2-.125")+((F / 2) - 2")=-65 23/32"; (MB_P/2-.125")-((F / 2) - 2")=-5 1/32"; (MB_Q/2)+.125"=35 5/8"; (NOZZLE_HEIGHT - (NOZZLE_HEIGHT / 8 * 2)) / 2=29 1/4"; (NOZZLE_WB_OD - NOZZLE_TOP_OD) / 4=7 1/8"; -((MB_Q / 2) + 1/8")=-35 5/8"; -(F-((F-H)/2))/2=-30 11/32"; -MB_HEIGHT=-76"; -MB_P=-71"; -MB_P-.25=-71 1/4"; A=231 5/16"; A/2=115 21/32"; B=60"; B/2=30"; B/4=15"; C=136 9/16"; C/2=68 9/32"; CLASS=1"; D=88 1/4"; D-L-K-J=1 3/8"; D-M=43 1/2"; DUAL_Q=213 3/8"; DUAL_Q+.25"=213 5/8"; E=113 3/16"; E-(NOZZLE_RAD/3*2)=42 7/16"; E-N-N-H=2"; E/2=56 19/32"; E/2-H/2=25 1/4"; E/52*15=32 21/32"; E/52*30=65 5/16"; F=64 11/16"; F/2=32 11/32"; H=62 11/16"; H/2=31 11/32"; HEIGHT=102 7/16"; J=14"; J+K+L=86 7/8"; K=25 7/8"; L=47"; M=44 3/4"; M-(2*(D-L-K-J))=42"; MB_A=208 5/8"; MB_F=18 1/4"; MB_F-3"=15 1/4"; MB_HEIGHT=76"; MB_HEIGHT/2=38"; MB_N=13 5/8"; MB_N-(D-J-K-L)=12 1/4"; MB_P=71"; MB_P+.25"=71 1/4"; MB_P+MB_P+.5=142 1/2"; MB_P-4.5"=66 1/2"; MB_Q=71"; N=23 1/4"; N+(H/2)=54 19/32"; NOZZLE_BOTTOM_ID=42 1/2"; NOZZLE_BOTTOM_RAD=21 1/4"; NOZZLE_BOTTOM_RAD-3*2=15 1/4"; NOZZLE_HEIGHT=78"; NOZZLE_HEIGHT/7*2=19 1/2"; NOZZLE_SIZE=30"; NOZZLE_TOP_OD=45 1/2"; NOZZLE_TOP_RAD=22 3/4"; NOZZLE_WB/4=14 13/16"; NOZZLE_WB_OD=74"; NOZZLE_WB_RAD=37"; NOZZLE_WB_RAD-2"=35"; P=18 1/2"; R=53"; R*1.1=58 5/16"; R+((B/2)+1.5")=84 1/2"; R-((B/2)+1.5")=21 1/2"; RO/2=33 1/4"; RO2/2=175 5/8"; TRANSITION=30 1/16"; TRANSITION/2=15 1/32"; TRIP_Q=355 3/4"; TRIP_Q-4.5"=351 1/4"; Type Comments=Triple Vari-Plume Laboratory Exhaust Centrifugal Airfoil Class 1 Arr 10 With Mixing Box
- Triple_540_CAVP-36H_CLASS_1_With_Mixing_Box: ((M - (2 * (D - L - K - J))) / 2) + (TRANSITION / 2)=39 9/32"; (B/2)+1.5"=31 1/2"; (B/2)-.125"=29 7/8"; (D-J-K-L)*2=2 3/4"; (E/2)-((B/2)+1.5")=25 3/32"; (E/2)-((MB_P/2)+.125")=20 31/32"; (E/2)-(E/52*15)=23 15/16"; (F-((F-H)/2))/2=30 11/32"; (M - (2 * (D - L - K - J)))/2=21"; (MB_P/2)+.125"=35 5/8"; (MB_P/2-.125")+((F / 2) - 2")=-65 23/32"; (MB_P/2-.125")-((F / 2) - 2")=-5 1/32"; (MB_Q/2)+.125"=35 5/8"; (NOZZLE_HEIGHT - (NOZZLE_HEIGHT / 8 * 2)) / 2=35 5/8"; (NOZZLE_WB_OD - NOZZLE_TOP_OD) / 4=8"; -((MB_Q / 2) + 1/8")=-35 5/8"; -(F-((F-H)/2))/2=-30 11/32"; -MB_HEIGHT=-76"; -MB_P=-71"; -MB_P-.25=-71 1/4"; A=231 5/16"; A/2=115 21/32"; B=60"; B/2=30"; B/4=15"; C=136 9/16"; C/2=68 9/32"; CLASS=1"; D=88 1/4"; D-L-K-J=1 3/8"; D-M=43 1/2"; DUAL_Q=213 3/8"; DUAL_Q+.25"=213 5/8"; E=113 3/16"; E-(NOZZLE_RAD/3*2)=39 11/32"; E-N-N-H=2"; E/2=56 19/32"; E/2-H/2=25 1/4"; E/52*15=32 21/32"; E/52*30=65 5/16"; F=64 11/16"; F/2=32 11/32"; H=62 11/16"; H/2=31 11/32"; HEIGHT=102 7/16"; J=14"; J+K+L=86 7/8"; K=25 7/8"; L=47"; M=44 3/4"; M-(2*(D-L-K-J))=42"; MB_A=208 5/8"; MB_F=18 1/4"; MB_F-3"=15 1/4"; MB_HEIGHT=76"; MB_HEIGHT/2=38"; MB_N=13 5/8"; MB_N-(D-J-K-L)=12 1/4"; MB_P=71"; MB_P+.25"=71 1/4"; MB_P+MB_P+.5=142 1/2"; MB_P-4.5"=66 1/2"; MB_Q=71"; N=23 1/4"; N+(H/2)=54 19/32"; NOZZLE_BOTTOM_ID=51 3/4"; NOZZLE_BOTTOM_RAD=25 7/8"; NOZZLE_BOTTOM_RAD-3*2=19 7/8"; NOZZLE_HEIGHT=95"; NOZZLE_HEIGHT/7*2=23 3/4"; NOZZLE_SIZE=36"; NOZZLE_TOP_OD=58"; NOZZLE_TOP_RAD=29"; NOZZLE_WB/4=18"; NOZZLE_WB_OD=90"; NOZZLE_WB_RAD=45"; NOZZLE_WB_RAD-2"=43"; P=18 1/2"; R=53"; R*1.1=58 5/16"; R+((B/2)+1.5")=84 1/2"; R-((B/2)+1.5")=21 1/2"; RO/2=33 1/4"; RO2/2=175 5/8"; TRANSITION=36 19/32"; TRANSITION/2=18 9/32"; TRIP_Q=355 3/4"; TRIP_Q-4.5"=351 1/4"; Type Comments=Triple Vari-Plume Laboratory Exhaust Centrifugal Airfoil Class 1 Arr 10 With Mixing Box
- Triple_540_CAVP-36L_CLASS_1_With_Mixing_Box: ((M - (2 * (D - L - K - J))) / 2) + (TRANSITION / 2)=39 9/32"; (B/2)+1.5"=31 1/2"; (B/2)-.125"=29 7/8"; (D-J-K-L)*2=2 3/4"; (E/2)-((B/2)+1.5")=25 3/32"; (E/2)-((MB_P/2)+.125")=20 31/32"; (E/2)-(E/52*15)=23 15/16"; (F-((F-H)/2))/2=30 11/32"; (M - (2 * (D - L - K - J)))/2=21"; (MB_P/2)+.125"=35 5/8"; (MB_P/2-.125")+((F / 2) - 2")=-65 23/32"; (MB_P/2-.125")-((F / 2) - 2")=-5 1/32"; (MB_Q/2)+.125"=35 5/8"; (NOZZLE_HEIGHT - (NOZZLE_HEIGHT / 8 * 2)) / 2=35 5/8"; (NOZZLE_WB_OD - NOZZLE_TOP_OD) / 4=8"; -((MB_Q / 2) + 1/8")=-35 5/8"; -(F-((F-H)/2))/2=-30 11/32"; -MB_HEIGHT=-76"; -MB_P=-71"; -MB_P-.25=-71 1/4"; A=231 5/16"; A/2=115 21/32"; B=60"; B/2=30"; B/4=15"; C=136 9/16"; C/2=68 9/32"; CLASS=1"; D=88 1/4"; D-L-K-J=1 3/8"; D-M=43 1/2"; DUAL_Q=213 3/8"; DUAL_Q+.25"=213 5/8"; E=113 3/16"; E-(NOZZLE_RAD/3*2)=39 11/32"; E-N-N-H=2"; E/2=56 19/32"; E/2-H/2=25 1/4"; E/52*15=32 21/32"; E/52*30=65 5/16"; F=64 11/16"; F/2=32 11/32"; H=62 11/16"; H/2=31 11/32"; HEIGHT=102 7/16"; J=14"; J+K+L=86 7/8"; K=25 7/8"; L=47"; M=44 3/4"; M-(2*(D-L-K-J))=42"; MB_A=208 5/8"; MB_F=18 1/4"; MB_F-3"=15 1/4"; MB_HEIGHT=76"; MB_HEIGHT/2=38"; MB_N=13 5/8"; MB_N-(D-J-K-L)=12 1/4"; MB_P=71"; MB_P+.25"=71 1/4"; MB_P+MB_P+.5=142 1/2"; MB_P-4.5"=66 1/2"; MB_Q=71"; N=23 1/4"; N+(H/2)=54 19/32"; NOZZLE_BOTTOM_ID=51 3/4"; NOZZLE_BOTTOM_RAD=25 7/8"; NOZZLE_BOTTOM_RAD-3*2=19 7/8"; NOZZLE_HEIGHT=95"; NOZZLE_HEIGHT/7*2=23 3/4"; NOZZLE_SIZE=36"; NOZZLE_TOP_OD=58"; NOZZLE_TOP_RAD=29"; NOZZLE_WB/4=18"; NOZZLE_WB_OD=90"; NOZZLE_WB_RAD=45"; NOZZLE_WB_RAD-2"=43"; P=18 1/2"; R=53"; R*1.1=58 5/16"; R+((B/2)+1.5")=84 1/2"; R-((B/2)+1.5")=21 1/2"; RO/2=33 1/4"; RO2/2=175 5/8"; TRANSITION=36 19/32"; TRANSITION/2=18 9/32"; TRIP_Q=355 3/4"; TRIP_Q-4.5"=351 1/4"; Type Comments=Triple Vari-Plume Laboratory Exhaust Centrifugal Airfoil Class 1 Arr 10 With Mixing Box
- Triple_540_CAVP-30H_CLASS_2_With_Mixing_Box: ((M - (2 * (D - L - K - J))) / 2) + (TRANSITION / 2)=36 1/32"; (B/2)+1.5"=31 1/2"; (B/2)-.125"=29 7/8"; (D-J-K-L)*2=2 3/4"; (E/2)-((B/2)+1.5")=25 3/32"; (E/2)-((MB_P/2)+.125")=20 31/32"; (E/2)-(E/52*15)=23 15/16"; (F-((F-H)/2))/2=30 11/32"; (M - (2 * (D - L - K - J)))/2=21"; (MB_P/2)+.125"=35 5/8"; (MB_P/2-.125")+((F / 2) - 2")=-65 23/32"; (MB_P/2-.125")-((F / 2) - 2")=-5 1/32"; (MB_Q/2)+.125"=35 5/8"; (NOZZLE_HEIGHT - (NOZZLE_HEIGHT / 8 * 2)) / 2=29 1/4"; (NOZZLE_WB_OD - NOZZLE_TOP_OD) / 4=7 1/8"; -((MB_Q / 2) + 1/8")=-35 5/8"; -(F-((F-H)/2))/2=-30 11/32"; -MB_HEIGHT=-76"; -MB_P=-71"; -MB_P-.25=-71 1/4"; A=231 5/16"; A/2=115 21/32"; B=60"; B/2=30"; B/4=15"; C=136 9/16"; C/2=68 9/32"; CLASS=2"; D=92 1/2"; D-L-K-J=1 3/8"; D-M=47 3/4"; DUAL_Q=213 3/8"; DUAL_Q+.25"=213 5/8"; E=113 3/16"; E-(NOZZLE_RAD/3*2)=42 7/16"; E-N-N-H=2"; E/2=56 19/32"; E/2-H/2=25 1/4"; E/52*15=32 21/32"; E/52*30=65 5/16"; F=64 11/16"; F/2=32 11/32"; H=62 11/16"; H/2=31 11/32"; HEIGHT=102 7/16"; J=14"; J+K+L=91 1/8"; K=30 1/8"; L=47"; M=44 3/4"; M-(2*(D-L-K-J))=42"; MB_A=212 7/8"; MB_F=18 1/4"; MB_F-3"=15 1/4"; MB_HEIGHT=76"; MB_HEIGHT/2=38"; MB_N=13 5/8"; MB_N-(D-J-K-L)=12 1/4"; MB_P=71"; MB_P+.25"=71 1/4"; MB_P+MB_P+.5=142 1/2"; MB_P-4.5"=66 1/2"; MB_Q=71"; N=23 1/4"; N+(H/2)=54 19/32"; NOZZLE_BOTTOM_ID=42 1/2"; NOZZLE_BOTTOM_RAD=21 1/4"; NOZZLE_BOTTOM_RAD-3*2=15 1/4"; NOZZLE_HEIGHT=78"; NOZZLE_HEIGHT/7*2=19 1/2"; NOZZLE_SIZE=30"; NOZZLE_TOP_OD=45 1/2"; NOZZLE_TOP_RAD=22 3/4"; NOZZLE_WB/4=14 13/16"; NOZZLE_WB_OD=74"; NOZZLE_WB_RAD=37"; NOZZLE_WB_RAD-2"=35"; P=25 3/4"; R=53"; R*1.1=58 5/16"; R+((B/2)+1.5")=84 1/2"; R-((B/2)+1.5")=21 1/2"; RO/2=33 1/4"; RO2/2=175 5/8"; TRANSITION=30 1/16"; TRANSITION/2=15 1/32"; TRIP_Q=355 3/4"; TRIP_Q-4.5"=351 1/4"; Type Comments=Triple Vari-Plume Laboratory Exhaust Centrifugal Airfoil Class 2 Arr 10 With Mixing Box
- Triple_540_CAVP-30L_CLASS_2_With_Mixing_Box: ((M - (2 * (D - L - K - J))) / 2) + (TRANSITION / 2)=36 1/32"; (B/2)+1.5"=31 1/2"; (B/2)-.125"=29 7/8"; (D-J-K-L)*2=2 3/4"; (E/2)-((B/2)+1.5")=25 3/32"; (E/2)-((MB_P/2)+.125")=20 31/32"; (E/2)-(E/52*15)=23 15/16"; (F-((F-H)/2))/2=30 11/32"; (M - (2 * (D - L - K - J)))/2=21"; (MB_P/2)+.125"=35 5/8"; (MB_P/2-.125")+((F / 2) - 2")=-65 23/32"; (MB_P/2-.125")-((F / 2) - 2")=-5 1/32"; (MB_Q/2)+.125"=35 5/8"; (NOZZLE_HEIGHT - (NOZZLE_HEIGHT / 8 * 2)) / 2=29 1/4"; (NOZZLE_WB_OD - NOZZLE_TOP_OD) / 4=7 1/8"; -((MB_Q / 2) + 1/8")=-35 5/8"; -(F-((F-H)/2))/2=-30 11/32"; -MB_HEIGHT=-76"; -MB_P=-71"; -MB_P-.25=-71 1/4"; A=231 5/16"; A/2=115 21/32"; B=60"; B/2=30"; B/4=15"; C=136 9/16"; C/2=68 9/32"; CLASS=2"; D=92 1/2"; D-L-K-J=1 3/8"; D-M=47 3/4"; DUAL_Q=213 3/8"; DUAL_Q+.25"=213 5/8"; E=113 3/16"; E-(NOZZLE_RAD/3*2)=42 7/16"; E-N-N-H=2"; E/2=56 19/32"; E/2-H/2=25 1/4"; E/52*15=32 21/32"; E/52*30=65 5/16"; F=64 11/16"; F/2=32 11/32"; H=62 11/16"; H/2=31 11/32"; HEIGHT=102 7/16"; J=14"; J+K+L=91 1/8"; K=30 1/8"; L=47"; M=44 3/4"; M-(2*(D-L-K-J))=42"; MB_A=212 7/8"; MB_F=18 1/4"; MB_F-3"=15 1/4"; MB_HEIGHT=76"; MB_HEIGHT/2=38"; MB_N=13 5/8"; MB_N-(D-J-K-L)=12 1/4"; MB_P=71"; MB_P+.25"=71 1/4"; MB_P+MB_P+.5=142 1/2"; MB_P-4.5"=66 1/2"; MB_Q=71"; N=23 1/4"; N+(H/2)=54 19/32"; NOZZLE_BOTTOM_ID=42 1/2"; NOZZLE_BOTTOM_RAD=21 1/4"; NOZZLE_BOTTOM_RAD-3*2=15 1/4"; NOZZLE_HEIGHT=78"; NOZZLE_HEIGHT/7*2=19 1/2"; NOZZLE_SIZE=30"; NOZZLE_TOP_OD=45 1/2"; NOZZLE_TOP_RAD=22 3/4"; NOZZLE_WB/4=14 13/16"; NOZZLE_WB_OD=74"; NOZZLE_WB_RAD=37"; NOZZLE_WB_RAD-2"=35"; P=25 3/4"; R=53"; R*1.1=58 5/16"; R+((B/2)+1.5")=84 1/2"; R-((B/2)+1.5")=21 1/2"; RO/2=33 1/4"; RO2/2=175 5/8"; TRANSITION=30 1/16"; TRANSITION/2=15 1/32"; TRIP_Q=355 3/4"; TRIP_Q-4.5"=351 1/4"; Type Comments=Triple Vari-Plume Laboratory Exhaust Centrifugal Airfoil Class 2 Arr 10 With Mixing Box
- Triple_540_CAVP-36H_CLASS_2_With_Mixing_Box: ((M - (2 * (D - L - K - J))) / 2) + (TRANSITION / 2)=39 9/32"; (B/2)+1.5"=31 1/2"; (B/2)-.125"=29 7/8"; (D-J-K-L)*2=2 3/4"; (E/2)-((B/2)+1.5")=25 3/32"; (E/2)-((MB_P/2)+.125")=20 31/32"; (E/2)-(E/52*15)=23 15/16"; (F-((F-H)/2))/2=30 11/32"; (M - (2 * (D - L - K - J)))/2=21"; (MB_P/2)+.125"=35 5/8"; (MB_P/2-.125")+((F / 2) - 2")=-65 23/32"; (MB_P/2-.125")-((F / 2) - 2")=-5 1/32"; (MB_Q/2)+.125"=35 5/8"; (NOZZLE_HEIGHT - (NOZZLE_HEIGHT / 8 * 2)) / 2=35 5/8"; (NOZZLE_WB_OD - NOZZLE_TOP_OD) / 4=8"; -((MB_Q / 2) + 1/8")=-35 5/8"; -(F-((F-H)/2))/2=-30 11/32"; -MB_HEIGHT=-76"; -MB_P=-71"; -MB_P-.25=-71 1/4"; A=231 5/16"; A/2=115 21/32"; B=60"; B/2=30"; B/4=15"; C=136 9/16"; C/2=68 9/32"; CLASS=2"; D=92 1/2"; D-L-K-J=1 3/8"; D-M=47 3/4"; DUAL_Q=213 3/8"; DUAL_Q+.25"=213 5/8"; E=113 3/16"; E-(NOZZLE_RAD/3*2)=39 11/32"; E-N-N-H=2"; E/2=56 19/32"; E/2-H/2=25 1/4"; E/52*15=32 21/32"; E/52*30=65 5/16"; F=64 11/16"; F/2=32 11/32"; H=62 11/16"; H/2=31 11/32"; HEIGHT=102 7/16"; J=14"; J+K+L=91 1/8"; K=30 1/8"; L=47"; M=44 3/4"; M-(2*(D-L-K-J))=42"; MB_A=212 7/8"; MB_F=18 1/4"; MB_F-3"=15 1/4"; MB_HEIGHT=76"; MB_HEIGHT/2=38"; MB_N=13 5/8"; MB_N-(D-J-K-L)=12 1/4"; MB_P=71"; MB_P+.25"=71 1/4"; MB_P+MB_P+.5=142 1/2"; MB_P-4.5"=66 1/2"; MB_Q=71"; N=23 1/4"; N+(H/2)=54 19/32"; NOZZLE_BOTTOM_ID=51 3/4"; NOZZLE_BOTTOM_RAD=25 7/8"; NOZZLE_BOTTOM_RAD-3*2=19 7/8"; NOZZLE_HEIGHT=95"; NOZZLE_HEIGHT/7*2=23 3/4"; NOZZLE_SIZE=36"; NOZZLE_TOP_OD=58"; NOZZLE_TOP_RAD=29"; NOZZLE_WB/4=18"; NOZZLE_WB_OD=90"; NOZZLE_WB_RAD=45"; NOZZLE_WB_RAD-2"=43"; P=25 3/4"; R=53"; R*1.1=58 5/16"; R+((B/2)+1.5")=84 1/2"; R-((B/2)+1.5")=21 1/2"; RO/2=33 1/4"; RO2/2=175 5/8"; TRANSITION=36 19/32"; TRANSITION/2=18 9/32"; TRIP_Q=355 3/4"; TRIP_Q-4.5"=351 1/4"; Type Comments=Triple Vari-Plume Laboratory Exhaust Centrifugal Airfoil Class 2 Arr 10 With Mixing Box
- Triple_540_CAVP-36L_CLASS_2_With_Mixing_Box: ((M - (2 * (D - L - K - J))) / 2) + (TRANSITION / 2)=39 9/32"; (B/2)+1.5"=31 1/2"; (B/2)-.125"=29 7/8"; (D-J-K-L)*2=2 3/4"; (E/2)-((B/2)+1.5")=25 3/32"; (E/2)-((MB_P/2)+.125")=20 31/32"; (E/2)-(E/52*15)=23 15/16"; (F-((F-H)/2))/2=30 11/32"; (M - (2 * (D - L - K - J)))/2=21"; (MB_P/2)+.125"=35 5/8"; (MB_P/2-.125")+((F / 2) - 2")=-65 23/32"; (MB_P/2-.125")-((F / 2) - 2")=-5 1/32"; (MB_Q/2)+.125"=35 5/8"; (NOZZLE_HEIGHT - (NOZZLE_HEIGHT / 8 * 2)) / 2=35 5/8"; (NOZZLE_WB_OD - NOZZLE_TOP_OD) / 4=8"; -((MB_Q / 2) + 1/8")=-35 5/8"; -(F-((F-H)/2))/2=-30 11/32"; -MB_HEIGHT=-76"; -MB_P=-71"; -MB_P-.25=-71 1/4"; A=231 5/16"; A/2=115 21/32"; B=60"; B/2=30"; B/4=15"; C=136 9/16"; C/2=68 9/32"; CLASS=2"; D=92 1/2"; D-L-K-J=1 3/8"; D-M=47 3/4"; DUAL_Q=213 3/8"; DUAL_Q+.25"=213 5/8"; E=113 3/16"; E-(NOZZLE_RAD/3*2)=39 11/32"; E-N-N-H=2"; E/2=56 19/32"; E/2-H/2=25 1/4"; E/52*15=32 21/32"; E/52*30=65 5/16"; F=64 11/16"; F/2=32 11/32"; H=62 11/16"; H/2=31 11/32"; HEIGHT=102 7/16"; J=14"; J+K+L=91 1/8"; K=30 1/8"; L=47"; M=44 3/4"; M-(2*(D-L-K-J))=42"; MB_A=212 7/8"; MB_F=18 1/4"; MB_F-3"=15 1/4"; MB_HEIGHT=76"; MB_HEIGHT/2=38"; MB_N=13 5/8"; MB_N-(D-J-K-L)=12 1/4"; MB_P=71"; MB_P+.25"=71 1/4"; MB_P+MB_P+.5=142 1/2"; MB_P-4.5"=66 1/2"; MB_Q=71"; N=23 1/4"; N+(H/2)=54 19/32"; NOZZLE_BOTTOM_ID=51 3/4"; NOZZLE_BOTTOM_RAD=25 7/8"; NOZZLE_BOTTOM_RAD-3*2=19 7/8"; NOZZLE_HEIGHT=95"; NOZZLE_HEIGHT/7*2=23 3/4"; NOZZLE_SIZE=36"; NOZZLE_TOP_OD=58"; NOZZLE_TOP_RAD=29"; NOZZLE_WB/4=18"; NOZZLE_WB_OD=90"; NOZZLE_WB_RAD=45"; NOZZLE_WB_RAD-2"=43"; P=25 3/4"; R=53"; R*1.1=58 5/16"; R+((B/2)+1.5")=84 1/2"; R-((B/2)+1.5")=21 1/2"; RO/2=33 1/4"; RO2/2=175 5/8"; TRANSITION=36 19/32"; TRANSITION/2=18 9/32"; TRIP_Q=355 3/4"; TRIP_Q-4.5"=351 1/4"; Type Comments=Triple Vari-Plume Laboratory Exhaust Centrifugal Airfoil Class 2 Arr 10 With Mixing Box
- Triple_600_CAVP-30L_CLASS_1_With_Mixing_Box: ((M - (2 * (D - L - K - J))) / 2) + (TRANSITION / 2)=38 5/16"; (B/2)+1.5"=34 1/2"; (B/2)-.125"=32 7/8"; (D-J-K-L)*2=2 3/4"; (E/2)-((B/2)+1.5")=28 9/32"; (E/2)-((MB_P/2)+.125")=24 5/32"; (E/2)-(E/52*15)=26 9/16"; (F-((F-H)/2))/2=33 11/32"; (M - (2 * (D - L - K - J)))/2=23 9/32"; (MB_P/2)+.125"=38 5/8"; (MB_P/2-.125")+((F / 2) - 2")=-71 23/32"; (MB_P/2-.125")-((F / 2) - 2")=-5 1/32"; (MB_Q/2)+.125"=38 5/8"; (NOZZLE_HEIGHT - (NOZZLE_HEIGHT / 8 * 2)) / 2=29 1/4"; (NOZZLE_WB_OD - NOZZLE_TOP_OD) / 4=7 1/8"; -((MB_Q / 2) + 1/8")=-38 5/8"; -(F-((F-H)/2))/2=-33 11/32"; -MB_HEIGHT=-84 1/2"; -MB_P=-77"; -MB_P-.25=-77 1/4"; A=239 7/16"; A/2=119 23/32"; B=66"; B/2=33"; B/4=16 1/2"; C=144 11/16"; C/2=72 11/32"; CLASS=1"; D=93 3/8"; D-L-K-J=1 3/8"; D-M=44 1/16"; DUAL_Q=231 3/8"; DUAL_Q+.25"=231 5/8"; E=125 9/16"; E-(NOZZLE_RAD/3*2)=48 5/8"; E-N-N-H=2"; E/2=62 25/32"; E/2-H/2=28 7/16"; E/52*15=36 7/32"; E/52*30=72 7/16"; F=70 11/16"; F/2=35 11/32"; H=68 11/16"; H/2=34 11/32"; HEIGHT=113 27/32"; J=14 1/2"; J+K+L=92"; K=25 7/8"; L=51 5/8"; M=49 5/16"; M-(2*(D-L-K-J))=46 9/16"; MB_A=224"; MB_F=21 1/4"; MB_F-3"=18 1/4"; MB_HEIGHT=84 1/2"; MB_HEIGHT/2=42 1/4"; MB_N=13 5/8"; MB_N-(D-J-K-L)=12 1/4"; MB_P=77"; MB_P+.25"=77 1/4"; MB_P+MB_P+.5=154 1/2"; MB_P-4.5"=72 1/2"; MB_Q=77"; N=26 7/16"; N+(H/2)=60 25/32"; NOZZLE_BOTTOM_ID=42 1/2"; NOZZLE_BOTTOM_RAD=21 1/4"; NOZZLE_BOTTOM_RAD-3*2=15 1/4"; NOZZLE_HEIGHT=78"; NOZZLE_HEIGHT/7*2=19 1/2"; NOZZLE_SIZE=30"; NOZZLE_TOP_OD=45 1/2"; NOZZLE_TOP_RAD=22 3/4"; NOZZLE_WB/4=14 13/16"; NOZZLE_WB_OD=74"; NOZZLE_WB_RAD=37"; NOZZLE_WB_RAD-2"=35"; P=19 1/2"; R=59"; R*1.1=64 29/32"; R+((B/2)+1.5")=93 1/2"; R-((B/2)+1.5")=24 1/2"; RO/2=36 1/4"; RO2/2=190 5/8"; TRANSITION=30 1/16"; TRANSITION/2=15 1/32"; TRIP_Q=385 3/4"; TRIP_Q-4.5"=381 1/4"; Type Comments=Triple Vari-Plume Laboratory Exhaust Centrifugal Airfoil Class 1 Arr 10 With Mixing Box
- Triple_600_CAVP-30H_CLASS_1_With_Mixing_Box: ((M - (2 * (D - L - K - J))) / 2) + (TRANSITION / 2)=38 5/16"; (B/2)+1.5"=34 1/2"; (B/2)-.125"=32 7/8"; (D-J-K-L)*2=2 3/4"; (E/2)-((B/2)+1.5")=28 9/32"; (E/2)-((MB_P/2)+.125")=24 5/32"; (E/2)-(E/52*15)=26 9/16"; (F-((F-H)/2))/2=33 11/32"; (M - (2 * (D - L - K - J)))/2=23 9/32"; (MB_P/2)+.125"=38 5/8"; (MB_P/2-.125")+((F / 2) - 2")=-71 23/32"; (MB_P/2-.125")-((F / 2) - 2")=-5 1/32"; (MB_Q/2)+.125"=38 5/8"; (NOZZLE_HEIGHT - (NOZZLE_HEIGHT / 8 * 2)) / 2=29 1/4"; (NOZZLE_WB_OD - NOZZLE_TOP_OD) / 4=7 1/8"; -((MB_Q / 2) + 1/8")=-38 5/8"; -(F-((F-H)/2))/2=-33 11/32"; -MB_HEIGHT=-84 1/2"; -MB_P=-77"; -MB_P-.25=-77 1/4"; A=239 7/16"; A/2=119 23/32"; B=66"; B/2=33"; B/4=16 1/2"; C=144 11/16"; C/2=72 11/32"; CLASS=1"; D=93 3/8"; D-L-K-J=1 3/8"; D-M=44 1/16"; DUAL_Q=231 3/8"; DUAL_Q+.25"=231 5/8"; E=125 9/16"; E-(NOZZLE_RAD/3*2)=48 5/8"; E-N-N-H=2"; E/2=62 25/32"; E/2-H/2=28 7/16"; E/52*15=36 7/32"; E/52*30=72 7/16"; F=70 11/16"; F/2=35 11/32"; H=68 11/16"; H/2=34 11/32"; HEIGHT=113 27/32"; J=14 1/2"; J+K+L=92"; K=25 7/8"; L=51 5/8"; M=49 5/16"; M-(2*(D-L-K-J))=46 9/16"; MB_A=224"; MB_F=21 1/4"; MB_F-3"=18 1/4"; MB_HEIGHT=84 1/2"; MB_HEIGHT/2=42 1/4"; MB_N=13 5/8"; MB_N-(D-J-K-L)=12 1/4"; MB_P=77"; MB_P+.25"=77 1/4"; MB_P+MB_P+.5=154 1/2"; MB_P-4.5"=72 1/2"; MB_Q=77"; N=26 7/16"; N+(H/2)=60 25/32"; NOZZLE_BOTTOM_ID=42 1/2"; NOZZLE_BOTTOM_RAD=21 1/4"; NOZZLE_BOTTOM_RAD-3*2=15 1/4"; NOZZLE_HEIGHT=78"; NOZZLE_HEIGHT/7*2=19 1/2"; NOZZLE_SIZE=30"; NOZZLE_TOP_OD=45 1/2"; NOZZLE_TOP_RAD=22 3/4"; NOZZLE_WB/4=14 13/16"; NOZZLE_WB_OD=74"; NOZZLE_WB_RAD=37"; NOZZLE_WB_RAD-2"=35"; P=19 1/2"; R=59"; R*1.1=64 29/32"; R+((B/2)+1.5")=93 1/2"; R-((B/2)+1.5")=24 1/2"; RO/2=36 1/4"; RO2/2=190 5/8"; TRANSITION=30 1/16"; TRANSITION/2=15 1/32"; TRIP_Q=385 3/4"; TRIP_Q-4.5"=381 1/4"; Type Comments=Triple Vari-Plume Laboratory Exhaust Centrifugal Airfoil Class 1 Arr 10 With Mixing Box
- Triple_600_CAVP-36L_CLASS_1_With_Mixing_Box: ((M - (2 * (D - L - K - J))) / 2) + (TRANSITION / 2)=41 9/16"; (B/2)+1.5"=34 1/2"; (B/2)-.125"=32 7/8"; (D-J-K-L)*2=2 3/4"; (E/2)-((B/2)+1.5")=28 9/32"; (E/2)-((MB_P/2)+.125")=24 5/32"; (E/2)-(E/52*15)=26 9/16"; (F-((F-H)/2))/2=33 11/32"; (M - (2 * (D - L - K - J)))/2=23 9/32"; (MB_P/2)+.125"=38 5/8"; (MB_P/2-.125")+((F / 2) - 2")=-71 23/32"; (MB_P/2-.125")-((F / 2) - 2")=-5 1/32"; (MB_Q/2)+.125"=38 5/8"; (NOZZLE_HEIGHT - (NOZZLE_HEIGHT / 8 * 2)) / 2=35 5/8"; (NOZZLE_WB_OD - NOZZLE_TOP_OD) / 4=8"; -((MB_Q / 2) + 1/8")=-38 5/8"; -(F-((F-H)/2))/2=-33 11/32"; -MB_HEIGHT=-84 1/2"; -MB_P=-77"; -MB_P-.25=-77 1/4"; A=239 7/16"; A/2=119 23/32"; B=66"; B/2=33"; B/4=16 1/2"; C=144 11/16"; C/2=72 11/32"; CLASS=1"; D=93 3/8"; D-L-K-J=1 3/8"; D-M=44 1/16"; DUAL_Q=231 3/8"; DUAL_Q+.25"=231 5/8"; E=125 9/16"; E-(NOZZLE_RAD/3*2)=45 17/32"; E-N-N-H=2"; E/2=62 25/32"; E/2-H/2=28 7/16"; E/52*15=36 7/32"; E/52*30=72 7/16"; F=70 11/16"; F/2=35 11/32"; H=68 11/16"; H/2=34 11/32"; HEIGHT=113 27/32"; J=14 1/2"; J+K+L=92"; K=25 7/8"; L=51 5/8"; M=49 5/16"; M-(2*(D-L-K-J))=46 9/16"; MB_A=224"; MB_F=21 1/4"; MB_F-3"=18 1/4"; MB_HEIGHT=84 1/2"; MB_HEIGHT/2=42 1/4"; MB_N=13 5/8"; MB_N-(D-J-K-L)=12 1/4"; MB_P=77"; MB_P+.25"=77 1/4"; MB_P+MB_P+.5=154 1/2"; MB_P-4.5"=72 1/2"; MB_Q=77"; N=26 7/16"; N+(H/2)=60 25/32"; NOZZLE_BOTTOM_ID=51 3/4"; NOZZLE_BOTTOM_RAD=25 7/8"; NOZZLE_BOTTOM_RAD-3*2=19 7/8"; NOZZLE_HEIGHT=95"; NOZZLE_HEIGHT/7*2=23 3/4"; NOZZLE_SIZE=36"; NOZZLE_TOP_OD=58"; NOZZLE_TOP_RAD=29"; NOZZLE_WB/4=18"; NOZZLE_WB_OD=90"; NOZZLE_WB_RAD=45"; NOZZLE_WB_RAD-2"=43"; P=19 1/2"; R=59"; R*1.1=64 29/32"; R+((B/2)+1.5")=93 1/2"; R-((B/2)+1.5")=24 1/2"; RO/2=36 1/4"; RO2/2=190 5/8"; TRANSITION=36 19/32"; TRANSITION/2=18 9/32"; TRIP_Q=385 3/4"; TRIP_Q-4.5"=381 1/4"; Type Comments=Triple Vari-Plume Laboratory Exhaust Centrifugal Airfoil Class 1 Arr 10 With Mixing Box
- Triple_600_CAVP-36H_CLASS_1_With_Mixing_Box: ((M - (2 * (D - L - K - J))) / 2) + (TRANSITION / 2)=41 9/16"; (B/2)+1.5"=34 1/2"; (B/2)-.125"=32 7/8"; (D-J-K-L)*2=2 3/4"; (E/2)-((B/2)+1.5")=28 9/32"; (E/2)-((MB_P/2)+.125")=24 5/32"; (E/2)-(E/52*15)=26 9/16"; (F-((F-H)/2))/2=33 11/32"; (M - (2 * (D - L - K - J)))/2=23 9/32"; (MB_P/2)+.125"=38 5/8"; (MB_P/2-.125")+((F / 2) - 2")=-71 23/32"; (MB_P/2-.125")-((F / 2) - 2")=-5 1/32"; (MB_Q/2)+.125"=38 5/8"; (NOZZLE_HEIGHT - (NOZZLE_HEIGHT / 8 * 2)) / 2=35 5/8"; (NOZZLE_WB_OD - NOZZLE_TOP_OD) / 4=8"; -((MB_Q / 2) + 1/8")=-38 5/8"; -(F-((F-H)/2))/2=-33 11/32"; -MB_HEIGHT=-84 1/2"; -MB_P=-77"; -MB_P-.25=-77 1/4"; A=239 7/16"; A/2=119 23/32"; B=66"; B/2=33"; B/4=16 1/2"; C=144 11/16"; C/2=72 11/32"; CLASS=1"; D=93 3/8"; D-L-K-J=1 3/8"; D-M=44 1/16"; DUAL_Q=231 3/8"; DUAL_Q+.25"=231 5/8"; E=125 9/16"; E-(NOZZLE_RAD/3*2)=45 17/32"; E-N-N-H=2"; E/2=62 25/32"; E/2-H/2=28 7/16"; E/52*15=36 7/32"; E/52*30=72 7/16"; F=70 11/16"; F/2=35 11/32"; H=68 11/16"; H/2=34 11/32"; HEIGHT=113 27/32"; J=14 1/2"; J+K+L=92"; K=25 7/8"; L=51 5/8"; M=49 5/16"; M-(2*(D-L-K-J))=46 9/16"; MB_A=224"; MB_F=21 1/4"; MB_F-3"=18 1/4"; MB_HEIGHT=84 1/2"; MB_HEIGHT/2=42 1/4"; MB_N=13 5/8"; MB_N-(D-J-K-L)=12 1/4"; MB_P=77"; MB_P+.25"=77 1/4"; MB_P+MB_P+.5=154 1/2"; MB_P-4.5"=72 1/2"; MB_Q=77"; N=26 7/16"; N+(H/2)=60 25/32"; NOZZLE_BOTTOM_ID=51 3/4"; NOZZLE_BOTTOM_RAD=25 7/8"; NOZZLE_BOTTOM_RAD-3*2=19 7/8"; NOZZLE_HEIGHT=95"; NOZZLE_HEIGHT/7*2=23 3/4"; NOZZLE_SIZE=36"; NOZZLE_TOP_OD=58"; NOZZLE_TOP_RAD=29"; NOZZLE_WB/4=18"; NOZZLE_WB_OD=90"; NOZZLE_WB_RAD=45"; NOZZLE_WB_RAD-2"=43"; P=19 1/2"; R=59"; R*1.1=64 29/32"; R+((B/2)+1.5")=93 1/2"; R-((B/2)+1.5")=24 1/2"; RO/2=36 1/4"; RO2/2=190 5/8"; TRANSITION=36 19/32"; TRANSITION/2=18 9/32"; TRIP_Q=385 3/4"; TRIP_Q-4.5"=381 1/4"; Type Comments=Triple Vari-Plume Laboratory Exhaust Centrifugal Airfoil Class 1 Arr 10 With Mixing Box
- Triple_600_CAVP-49L_CLASS_1_With_Mixing_Box: ((M - (2 * (D - L - K - J))) / 2) + (TRANSITION / 2)=47 13/16"; (B/2)+1.5"=34 1/2"; (B/2)-.125"=32 7/8"; (D-J-K-L)*2=2 3/4"; (E/2)-((B/2)+1.5")=28 9/32"; (E/2)-((MB_P/2)+.125")=24 5/32"; (E/2)-(E/52*15)=26 9/16"; (F-((F-H)/2))/2=33 11/32"; (M - (2 * (D - L - K - J)))/2=23 9/32"; (MB_P/2)+.125"=38 5/8"; (MB_P/2-.125")+((F / 2) - 2")=-71 23/32"; (MB_P/2-.125")-((F / 2) - 2")=-5 1/32"; (MB_Q/2)+.125"=38 5/8"; (NOZZLE_HEIGHT - (NOZZLE_HEIGHT / 8 * 2)) / 2=41 1/4"; (NOZZLE_WB_OD - NOZZLE_TOP_OD) / 4=6 1/4"; -((MB_Q / 2) + 1/8")=-38 5/8"; -(F-((F-H)/2))/2=-33 11/32"; -MB_HEIGHT=-84 1/2"; -MB_P=-77"; -MB_P-.25=-77 1/4"; A=239 7/16"; A/2=119 23/32"; B=66"; B/2=33"; B/4=16 1/2"; C=144 11/16"; C/2=72 11/32"; CLASS=1"; D=93 3/8"; D-L-K-J=1 3/8"; D-M=44 1/16"; DUAL_Q=231 3/8"; DUAL_Q+.25"=231 5/8"; E=125 9/16"; E-(NOZZLE_RAD/3*2)=39 21/32"; E-N-N-H=2"; E/2=62 25/32"; E/2-H/2=28 7/16"; E/52*15=36 7/32"; E/52*30=72 7/16"; F=70 11/16"; F/2=35 11/32"; H=68 11/16"; H/2=34 11/32"; HEIGHT=113 27/32"; J=14 1/2"; J+K+L=92"; K=25 7/8"; L=51 5/8"; M=49 5/16"; M-(2*(D-L-K-J))=46 9/16"; MB_A=224"; MB_F=21 1/4"; MB_F-3"=18 1/4"; MB_HEIGHT=84 1/2"; MB_HEIGHT/2=42 1/4"; MB_N=13 5/8"; MB_N-(D-J-K-L)=12 1/4"; MB_P=77"; MB_P+.25"=77 1/4"; MB_P+MB_P+.5=154 1/2"; MB_P-4.5"=72 1/2"; MB_Q=77"; N=26 7/16"; N+(H/2)=60 25/32"; NOZZLE_BOTTOM_ID=69 3/8"; NOZZLE_BOTTOM_RAD=34 11/16"; NOZZLE_BOTTOM_RAD-3*2=28 11/16"; NOZZLE_HEIGHT=110"; NOZZLE_HEIGHT/7*2=27 1/2"; NOZZLE_SIZE=49"; NOZZLE_TOP_OD=76"; NOZZLE_TOP_RAD=38"; NOZZLE_WB/4=20 3/16"; NOZZLE_WB_OD=101"; NOZZLE_WB_RAD=50 1/2"; NOZZLE_WB_RAD-2"=48 1/2"; P=19 1/2"; R=59"; R*1.1=64 29/32"; R+((B/2)+1.5")=93 1/2"; R-((B/2)+1.5")=24 1/2"; RO/2=36 1/4"; RO2/2=190 5/8"; TRANSITION=49 1/16"; TRANSITION/2=24 17/32"; TRIP_Q=385 3/4"; TRIP_Q-4.5"=381 1/4"; Type Comments=Triple Vari-Plume Laboratory Exhaust Centrifugal Airfoil Class 1 Arr 10 With Mixing Box
- Triple_600_CAVP-49H_CLASS_1_With_Mixing_Box: ((M - (2 * (D - L - K - J))) / 2) + (TRANSITION / 2)=47 13/16"; (B/2)+1.5"=34 1/2"; (B/2)-.125"=32 7/8"; (D-J-K-L)*2=2 3/4"; (E/2)-((B/2)+1.5")=28 9/32"; (E/2)-((MB_P/2)+.125")=24 5/32"; (E/2)-(E/52*15)=26 9/16"; (F-((F-H)/2))/2=33 11/32"; (M - (2 * (D - L - K - J)))/2=23 9/32"; (MB_P/2)+.125"=38 5/8"; (MB_P/2-.125")+((F / 2) - 2")=-71 23/32"; (MB_P/2-.125")-((F / 2) - 2")=-5 1/32"; (MB_Q/2)+.125"=38 5/8"; (NOZZLE_HEIGHT - (NOZZLE_HEIGHT / 8 * 2)) / 2=41 1/4"; (NOZZLE_WB_OD - NOZZLE_TOP_OD) / 4=6 1/4"; -((MB_Q / 2) + 1/8")=-38 5/8"; -(F-((F-H)/2))/2=-33 11/32"; -MB_HEIGHT=-84 1/2"; -MB_P=-77"; -MB_P-.25=-77 1/4"; A=239 7/16"; A/2=119 23/32"; B=66"; B/2=33"; B/4=16 1/2"; C=144 11/16"; C/2=72 11/32"; CLASS=1"; D=93 3/8"; D-L-K-J=1 3/8"; D-M=44 1/16"; DUAL_Q=231 3/8"; DUAL_Q+.25"=231 5/8"; E=125 9/16"; E-(NOZZLE_RAD/3*2)=39 21/32"; E-N-N-H=2"; E/2=62 25/32"; E/2-H/2=28 7/16"; E/52*15=36 7/32"; E/52*30=72 7/16"; F=70 11/16"; F/2=35 11/32"; H=68 11/16"; H/2=34 11/32"; HEIGHT=113 27/32"; J=14 1/2"; J+K+L=92"; K=25 7/8"; L=51 5/8"; M=49 5/16"; M-(2*(D-L-K-J))=46 9/16"; MB_A=224"; MB_F=21 1/4"; MB_F-3"=18 1/4"; MB_HEIGHT=84 1/2"; MB_HEIGHT/2=42 1/4"; MB_N=13 5/8"; MB_N-(D-J-K-L)=12 1/4"; MB_P=77"; MB_P+.25"=77 1/4"; MB_P+MB_P+.5=154 1/2"; MB_P-4.5"=72 1/2"; MB_Q=77"; N=26 7/16"; N+(H/2)=60 25/32"; NOZZLE_BOTTOM_ID=69 3/8"; NOZZLE_BOTTOM_RAD=34 11/16"; NOZZLE_BOTTOM_RAD-3*2=28 11/16"; NOZZLE_HEIGHT=110"; NOZZLE_HEIGHT/7*2=27 1/2"; NOZZLE_SIZE=49"; NOZZLE_TOP_OD=76"; NOZZLE_TOP_RAD=38"; NOZZLE_WB/4=20 3/16"; NOZZLE_WB_OD=101"; NOZZLE_WB_RAD=50 1/2"; NOZZLE_WB_RAD-2"=48 1/2"; P=19 1/2"; R=59"; R*1.1=64 29/32"; R+((B/2)+1.5")=93 1/2"; R-((B/2)+1.5")=24 1/2"; RO/2=36 1/4"; RO2/2=190 5/8"; TRANSITION=49 1/16"; TRANSITION/2=24 17/32"; TRIP_Q=385 3/4"; TRIP_Q-4.5"=381 1/4"; Type Comments=Triple Vari-Plume Laboratory Exhaust Centrifugal Airfoil Class 1 Arr 10 With Mixing Box
- Triple_600_CAVP-30L_CLASS_2_With_Mixing_Box: ((M - (2 * (D - L - K - J))) / 2) + (TRANSITION / 2)=38 5/16"; (B/2)+1.5"=34 1/2"; (B/2)-.125"=32 7/8"; (D-J-K-L)*2=2 3/4"; (E/2)-((B/2)+1.5")=28 9/32"; (E/2)-((MB_P/2)+.125")=24 5/32"; (E/2)-(E/52*15)=26 9/16"; (F-((F-H)/2))/2=33 11/32"; (M - (2 * (D - L - K - J)))/2=23 9/32"; (MB_P/2)+.125"=38 5/8"; (MB_P/2-.125")+((F / 2) - 2")=-71 23/32"; (MB_P/2-.125")-((F / 2) - 2")=-5 1/32"; (MB_Q/2)+.125"=38 5/8"; (NOZZLE_HEIGHT - (NOZZLE_HEIGHT / 8 * 2)) / 2=29 1/4"; (NOZZLE_WB_OD - NOZZLE_TOP_OD) / 4=7 1/8"; -((MB_Q / 2) + 1/8")=-38 5/8"; -(F-((F-H)/2))/2=-33 11/32"; -MB_HEIGHT=-84 1/2"; -MB_P=-77"; -MB_P-.25=-77 1/4"; A=239 7/16"; A/2=119 23/32"; B=66"; B/2=33"; B/4=16 1/2"; C=144 11/16"; C/2=72 11/32"; CLASS=2"; D=97 9/16"; D-L-K-J=1 3/8"; D-M=48 1/4"; DUAL_Q=231 3/8"; DUAL_Q+.25"=231 5/8"; E=125 9/16"; E-(NOZZLE_RAD/3*2)=48 5/8"; E-N-N-H=2"; E/2=62 25/32"; E/2-H/2=28 7/16"; E/52*15=36 7/32"; E/52*30=72 7/16"; F=70 11/16"; F/2=35 11/32"; H=68 11/16"; H/2=34 11/32"; HEIGHT=113 27/32"; J=14 1/2"; J+K+L=96 3/16"; K=30 1/8"; L=51 9/16"; M=49 5/16"; M-(2*(D-L-K-J))=46 9/16"; MB_A=228 1/4"; MB_F=21 1/4"; MB_F-3"=18 1/4"; MB_HEIGHT=84 1/2"; MB_HEIGHT/2=42 1/4"; MB_N=13 5/8"; MB_N-(D-J-K-L)=12 1/4"; MB_P=77"; MB_P+.25"=77 1/4"; MB_P+MB_P+.5=154 1/2"; MB_P-4.5"=72 1/2"; MB_Q=77"; N=26 7/16"; N+(H/2)=60 25/32"; NOZZLE_BOTTOM_ID=42 1/2"; NOZZLE_BOTTOM_RAD=21 1/4"; NOZZLE_BOTTOM_RAD-3*2=15 1/4"; NOZZLE_HEIGHT=78"; NOZZLE_HEIGHT/7*2=19 1/2"; NOZZLE_SIZE=30"; NOZZLE_TOP_OD=45 1/2"; NOZZLE_TOP_RAD=22 3/4"; NOZZLE_WB/4=14 13/16"; NOZZLE_WB_OD=74"; NOZZLE_WB_RAD=37"; NOZZLE_WB_RAD-2"=35"; P=26"; R=59"; R*1.1=64 29/32"; R+((B/2)+1.5")=93 1/2"; R-((B/2)+1.5")=24 1/2"; RO/2=36 1/4"; RO2/2=190 5/8"; TRANSITION=30 1/16"; TRANSITION/2=15 1/32"; TRIP_Q=385 3/4"; TRIP_Q-4.5"=381 1/4"; Type Comments=Triple Vari-Plume Laboratory Exhaust Centrifugal Airfoil Class 2 Arr 10 With Mixing Box
- Triple_600_CAVP-30H_CLASS_2_With_Mixing_Box: ((M - (2 * (D - L - K - J))) / 2) + (TRANSITION / 2)=38 5/16"; (B/2)+1.5"=34 1/2"; (B/2)-.125"=32 7/8"; (D-J-K-L)*2=2 3/4"; (E/2)-((B/2)+1.5")=28 9/32"; (E/2)-((MB_P/2)+.125")=24 5/32"; (E/2)-(E/52*15)=26 9/16"; (F-((F-H)/2))/2=33 11/32"; (M - (2 * (D - L - K - J)))/2=23 9/32"; (MB_P/2)+.125"=38 5/8"; (MB_P/2-.125")+((F / 2) - 2")=-71 23/32"; (MB_P/2-.125")-((F / 2) - 2")=-5 1/32"; (MB_Q/2)+.125"=38 5/8"; (NOZZLE_HEIGHT - (NOZZLE_HEIGHT / 8 * 2)) / 2=29 1/4"; (NOZZLE_WB_OD - NOZZLE_TOP_OD) / 4=7 1/8"; -((MB_Q / 2) + 1/8")=-38 5/8"; -(F-((F-H)/2))/2=-33 11/32"; -MB_HEIGHT=-84 1/2"; -MB_P=-77"; -MB_P-.25=-77 1/4"; A=239 7/16"; A/2=119 23/32"; B=66"; B/2=33"; B/4=16 1/2"; C=144 11/16"; C/2=72 11/32"; CLASS=2"; D=97 9/16"; D-L-K-J=1 3/8"; D-M=48 1/4"; DUAL_Q=231 3/8"; DUAL_Q+.25"=231 5/8"; E=125 9/16"; E-(NOZZLE_RAD/3*2)=48 5/8"; E-N-N-H=2"; E/2=62 25/32"; E/2-H/2=28 7/16"; E/52*15=36 7/32"; E/52*30=72 7/16"; F=70 11/16"; F/2=35 11/32"; H=68 11/16"; H/2=34 11/32"; HEIGHT=113 27/32"; J=14 1/2"; J+K+L=96 3/16"; K=30 1/8"; L=51 9/16"; M=49 5/16"; M-(2*(D-L-K-J))=46 9/16"; MB_A=228 1/4"; MB_F=21 1/4"; MB_F-3"=18 1/4"; MB_HEIGHT=84 1/2"; MB_HEIGHT/2=42 1/4"; MB_N=13 5/8"; MB_N-(D-J-K-L)=12 1/4"; MB_P=77"; MB_P+.25"=77 1/4"; MB_P+MB_P+.5=154 1/2"; MB_P-4.5"=72 1/2"; MB_Q=77"; N=26 7/16"; N+(H/2)=60 25/32"; NOZZLE_BOTTOM_ID=42 1/2"; NOZZLE_BOTTOM_RAD=21 1/4"; NOZZLE_BOTTOM_RAD-3*2=15 1/4"; NOZZLE_HEIGHT=78"; NOZZLE_HEIGHT/7*2=19 1/2"; NOZZLE_SIZE=30"; NOZZLE_TOP_OD=45 1/2"; NOZZLE_TOP_RAD=22 3/4"; NOZZLE_WB/4=14 13/16"; NOZZLE_WB_OD=74"; NOZZLE_WB_RAD=37"; NOZZLE_WB_RAD-2"=35"; P=26"; R=59"; R*1.1=64 29/32"; R+((B/2)+1.5")=93 1/2"; R-((B/2)+1.5")=24 1/2"; RO/2=36 1/4"; RO2/2=190 5/8"; TRANSITION=30 1/16"; TRANSITION/2=15 1/32"; TRIP_Q=385 3/4"; TRIP_Q-4.5"=381 1/4"; Type Comments=Triple Vari-Plume Laboratory Exhaust Centrifugal Airfoil Class 2 Arr 10 With Mixing Box
- Triple_600_CAVP-36L_CLASS_2_With_Mixing_Box: ((M - (2 * (D - L - K - J))) / 2) + (TRANSITION / 2)=41 9/16"; (B/2)+1.5"=34 1/2"; (B/2)-.125"=32 7/8"; (D-J-K-L)*2=2 3/4"; (E/2)-((B/2)+1.5")=28 9/32"; (E/2)-((MB_P/2)+.125")=24 5/32"; (E/2)-(E/52*15)=26 9/16"; (F-((F-H)/2))/2=33 11/32"; (M - (2 * (D - L - K - J)))/2=23 9/32"; (MB_P/2)+.125"=38 5/8"; (MB_P/2-.125")+((F / 2) - 2")=-71 23/32"; (MB_P/2-.125")-((F / 2) - 2")=-5 1/32"; (MB_Q/2)+.125"=38 5/8"; (NOZZLE_HEIGHT - (NOZZLE_HEIGHT / 8 * 2)) / 2=35 5/8"; (NOZZLE_WB_OD - NOZZLE_TOP_OD) / 4=8"; -((MB_Q / 2) + 1/8")=-38 5/8"; -(F-((F-H)/2))/2=-33 11/32"; -MB_HEIGHT=-84 1/2"; -MB_P=-77"; -MB_P-.25=-77 1/4"; A=239 7/16"; A/2=119 23/32"; B=66"; B/2=33"; B/4=16 1/2"; C=144 11/16"; C/2=72 11/32"; CLASS=2"; D=97 9/16"; D-L-K-J=1 3/8"; D-M=48 1/4"; DUAL_Q=231 3/8"; DUAL_Q+.25"=231 5/8"; E=125 9/16"; E-(NOZZLE_RAD/3*2)=45 17/32"; E-N-N-H=2"; E/2=62 25/32"; E/2-H/2=28 7/16"; E/52*15=36 7/32"; E/52*30=72 7/16"; F=70 11/16"; F/2=35 11/32"; H=68 11/16"; H/2=34 11/32"; HEIGHT=113 27/32"; J=14 1/2"; J+K+L=96 3/16"; K=30 1/8"; L=51 9/16"; M=49 5/16"; M-(2*(D-L-K-J))=46 9/16"; MB_A=228 1/4"; MB_F=21 1/4"; MB_F-3"=18 1/4"; MB_HEIGHT=84 1/2"; MB_HEIGHT/2=42 1/4"; MB_N=13 5/8"; MB_N-(D-J-K-L)=12 1/4"; MB_P=77"; MB_P+.25"=77 1/4"; MB_P+MB_P+.5=154 1/2"; MB_P-4.5"=72 1/2"; MB_Q=77"; N=26 7/16"; N+(H/2)=60 25/32"; NOZZLE_BOTTOM_ID=51 3/4"; NOZZLE_BOTTOM_RAD=25 7/8"; NOZZLE_BOTTOM_RAD-3*2=19 7/8"; NOZZLE_HEIGHT=95"; NOZZLE_HEIGHT/7*2=23 3/4"; NOZZLE_SIZE=36"; NOZZLE_TOP_OD=58"; NOZZLE_TOP_RAD=29"; NOZZLE_WB/4=18"; NOZZLE_WB_OD=90"; NOZZLE_WB_RAD=45"; NOZZLE_WB_RAD-2"=43"; P=26"; R=59"; R*1.1=64 29/32"; R+((B/2)+1.5")=93 1/2"; R-((B/2)+1.5")=24 1/2"; RO/2=36 1/4"; RO2/2=190 5/8"; TRANSITION=36 19/32"; TRANSITION/2=18 9/32"; TRIP_Q=385 3/4"; TRIP_Q-4.5"=381 1/4"; Type Comments=Triple Vari-Plume Laboratory Exhaust Centrifugal Airfoil Class 2 Arr 10 With Mixing Box
- Triple_600_CAVP-36H_CLASS_2_With_Mixing_Box: ((M - (2 * (D - L - K - J))) / 2) + (TRANSITION / 2)=41 9/16"; (B/2)+1.5"=34 1/2"; (B/2)-.125"=32 7/8"; (D-J-K-L)*2=2 3/4"; (E/2)-((B/2)+1.5")=28 9/32"; (E/2)-((MB_P/2)+.125")=24 5/32"; (E/2)-(E/52*15)=26 9/16"; (F-((F-H)/2))/2=33 11/32"; (M - (2 * (D - L - K - J)))/2=23 9/32"; (MB_P/2)+.125"=38 5/8"; (MB_P/2-.125")+((F / 2) - 2")=-71 23/32"; (MB_P/2-.125")-((F / 2) - 2")=-5 1/32"; (MB_Q/2)+.125"=38 5/8"; (NOZZLE_HEIGHT - (NOZZLE_HEIGHT / 8 * 2)) / 2=35 5/8"; (NOZZLE_WB_OD - NOZZLE_TOP_OD) / 4=8"; -((MB_Q / 2) + 1/8")=-38 5/8"; -(F-((F-H)/2))/2=-33 11/32"; -MB_HEIGHT=-84 1/2"; -MB_P=-77"; -MB_P-.25=-77 1/4"; A=239 7/16"; A/2=119 23/32"; B=66"; B/2=33"; B/4=16 1/2"; C=144 11/16"; C/2=72 11/32"; CLASS=2"; D=97 9/16"; D-L-K-J=1 3/8"; D-M=48 1/4"; DUAL_Q=231 3/8"; DUAL_Q+.25"=231 5/8"; E=125 9/16"; E-(NOZZLE_RAD/3*2)=45 17/32"; E-N-N-H=2"; E/2=62 25/32"; E/2-H/2=28 7/16"; E/52*15=36 7/32"; E/52*30=72 7/16"; F=70 11/16"; F/2=35 11/32"; H=68 11/16"; H/2=34 11/32"; HEIGHT=113 27/32"; J=14 1/2"; J+K+L=96 3/16"; K=30 1/8"; L=51 9/16"; M=49 5/16"; M-(2*(D-L-K-J))=46 9/16"; MB_A=228 1/4"; MB_F=21 1/4"; MB_F-3"=18 1/4"; MB_HEIGHT=84 1/2"; MB_HEIGHT/2=42 1/4"; MB_N=13 5/8"; MB_N-(D-J-K-L)=12 1/4"; MB_P=77"; MB_P+.25"=77 1/4"; MB_P+MB_P+.5=154 1/2"; MB_P-4.5"=72 1/2"; MB_Q=77"; N=26 7/16"; N+(H/2)=60 25/32"; NOZZLE_BOTTOM_ID=51 3/4"; NOZZLE_BOTTOM_RAD=25 7/8"; NOZZLE_BOTTOM_RAD-3*2=19 7/8"; NOZZLE_HEIGHT=95"; NOZZLE_HEIGHT/7*2=23 3/4"; NOZZLE_SIZE=36"; NOZZLE_TOP_OD=58"; NOZZLE_TOP_RAD=29"; NOZZLE_WB/4=18"; NOZZLE_WB_OD=90"; NOZZLE_WB_RAD=45"; NOZZLE_WB_RAD-2"=43"; P=26"; R=59"; R*1.1=64 29/32"; R+((B/2)+1.5")=93 1/2"; R-((B/2)+1.5")=24 1/2"; RO/2=36 1/4"; RO2/2=190 5/8"; TRANSITION=36 19/32"; TRANSITION/2=18 9/32"; TRIP_Q=385 3/4"; TRIP_Q-4.5"=381 1/4"; Type Comments=Triple Vari-Plume Laboratory Exhaust Centrifugal Airfoil Class 2 Arr 10 With Mixing Box
- Triple_600_CAVP-49L_CLASS_2_With_Mixing_Box: ((M - (2 * (D - L - K - J))) / 2) + (TRANSITION / 2)=47 13/16"; (B/2)+1.5"=34 1/2"; (B/2)-.125"=32 7/8"; (D-J-K-L)*2=2 3/4"; (E/2)-((B/2)+1.5")=28 9/32"; (E/2)-((MB_P/2)+.125")=24 5/32"; (E/2)-(E/52*15)=26 9/16"; (F-((F-H)/2))/2=33 11/32"; (M - (2 * (D - L - K - J)))/2=23 9/32"; (MB_P/2)+.125"=38 5/8"; (MB_P/2-.125")+((F / 2) - 2")=-71 23/32"; (MB_P/2-.125")-((F / 2) - 2")=-5 1/32"; (MB_Q/2)+.125"=38 5/8"; (NOZZLE_HEIGHT - (NOZZLE_HEIGHT / 8 * 2)) / 2=41 1/4"; (NOZZLE_WB_OD - NOZZLE_TOP_OD) / 4=6 1/4"; -((MB_Q / 2) + 1/8")=-38 5/8"; -(F-((F-H)/2))/2=-33 11/32"; -MB_HEIGHT=-84 1/2"; -MB_P=-77"; -MB_P-.25=-77 1/4"; A=239 7/16"; A/2=119 23/32"; B=66"; B/2=33"; B/4=16 1/2"; C=144 11/16"; C/2=72 11/32"; CLASS=2"; D=97 9/16"; D-L-K-J=1 3/8"; D-M=48 1/4"; DUAL_Q=231 3/8"; DUAL_Q+.25"=231 5/8"; E=125 9/16"; E-(NOZZLE_RAD/3*2)=39 21/32"; E-N-N-H=2"; E/2=62 25/32"; E/2-H/2=28 7/16"; E/52*15=36 7/32"; E/52*30=72 7/16"; F=70 11/16"; F/2=35 11/32"; H=68 11/16"; H/2=34 11/32"; HEIGHT=113 27/32"; J=14 1/2"; J+K+L=96 3/16"; K=30 1/8"; L=51 9/16"; M=49 5/16"; M-(2*(D-L-K-J))=46 9/16"; MB_A=228 1/4"; MB_F=21 1/4"; MB_F-3"=18 1/4"; MB_HEIGHT=84 1/2"; MB_HEIGHT/2=42 1/4"; MB_N=13 5/8"; MB_N-(D-J-K-L)=12 1/4"; MB_P=77"; MB_P+.25"=77 1/4"; MB_P+MB_P+.5=154 1/2"; MB_P-4.5"=72 1/2"; MB_Q=77"; N=26 7/16"; N+(H/2)=60 25/32"; NOZZLE_BOTTOM_ID=69 3/8"; NOZZLE_BOTTOM_RAD=34 11/16"; NOZZLE_BOTTOM_RAD-3*2=28 11/16"; NOZZLE_HEIGHT=110"; NOZZLE_HEIGHT/7*2=27 1/2"; NOZZLE_SIZE=49"; NOZZLE_TOP_OD=76"; NOZZLE_TOP_RAD=38"; NOZZLE_WB/4=20 3/16"; NOZZLE_WB_OD=101"; NOZZLE_WB_RAD=50 1/2"; NOZZLE_WB_RAD-2"=48 1/2"; P=26"; R=59"; R*1.1=64 29/32"; R+((B/2)+1.5")=93 1/2"; R-((B/2)+1.5")=24 1/2"; RO/2=36 1/4"; RO2/2=190 5/8"; TRANSITION=49 1/16"; TRANSITION/2=24 17/32"; TRIP_Q=385 3/4"; TRIP_Q-4.5"=381 1/4"; Type Comments=Triple Vari-Plume Laboratory Exhaust Centrifugal Airfoil Class 2 Arr 10 With Mixing Box
- Triple_600_CAVP-49H_CLASS_2_With_Mixing_Box: ((M - (2 * (D - L - K - J))) / 2) + (TRANSITION / 2)=47 13/16"; (B/2)+1.5"=34 1/2"; (B/2)-.125"=32 7/8"; (D-J-K-L)*2=2 3/4"; (E/2)-((B/2)+1.5")=28 9/32"; (E/2)-((MB_P/2)+.125")=24 5/32"; (E/2)-(E/52*15)=26 9/16"; (F-((F-H)/2))/2=33 11/32"; (M - (2 * (D - L - K - J)))/2=23 9/32"; (MB_P/2)+.125"=38 5/8"; (MB_P/2-.125")+((F / 2) - 2")=-71 23/32"; (MB_P/2-.125")-((F / 2) - 2")=-5 1/32"; (MB_Q/2)+.125"=38 5/8"; (NOZZLE_HEIGHT - (NOZZLE_HEIGHT / 8 * 2)) / 2=41 1/4"; (NOZZLE_WB_OD - NOZZLE_TOP_OD) / 4=6 1/4"; -((MB_Q / 2) + 1/8")=-38 5/8"; -(F-((F-H)/2))/2=-33 11/32"; -MB_HEIGHT=-84 1/2"; -MB_P=-77"; -MB_P-.25=-77 1/4"; A=239 7/16"; A/2=119 23/32"; B=66"; B/2=33"; B/4=16 1/2"; C=144 11/16"; C/2=72 11/32"; CLASS=2"; D=97 9/16"; D-L-K-J=1 3/8"; D-M=48 1/4"; DUAL_Q=231 3/8"; DUAL_Q+.25"=231 5/8"; E=125 9/16"; E-(NOZZLE_RAD/3*2)=39 21/32"; E-N-N-H=2"; E/2=62 25/32"; E/2-H/2=28 7/16"; E/52*15=36 7/32"; E/52*30=72 7/16"; F=70 11/16"; F/2=35 11/32"; H=68 11/16"; H/2=34 11/32"; HEIGHT=113 27/32"; J=14 1/2"; J+K+L=96 3/16"; K=30 1/8"; L=51 9/16"; M=49 5/16"; M-(2*(D-L-K-J))=46 9/16"; MB_A=228 1/4"; MB_F=21 1/4"; MB_F-3"=18 1/4"; MB_HEIGHT=84 1/2"; MB_HEIGHT/2=42 1/4"; MB_N=13 5/8"; MB_N-(D-J-K-L)=12 1/4"; MB_P=77"; MB_P+.25"=77 1/4"; MB_P+MB_P+.5=154 1/2"; MB_P-4.5"=72 1/2"; MB_Q=77"; N=26 7/16"; N+(H/2)=60 25/32"; NOZZLE_BOTTOM_ID=69 3/8"; NOZZLE_BOTTOM_RAD=34 11/16"; NOZZLE_BOTTOM_RAD-3*2=28 11/16"; NOZZLE_HEIGHT=110"; NOZZLE_HEIGHT/7*2=27 1/2"; NOZZLE_SIZE=49"; NOZZLE_TOP_OD=76"; NOZZLE_TOP_RAD=38"; NOZZLE_WB/4=20 3/16"; NOZZLE_WB_OD=101"; NOZZLE_WB_RAD=50 1/2"; NOZZLE_WB_RAD-2"=48 1/2"; P=26"; R=59"; R*1.1=64 29/32"; R+((B/2)+1.5")=93 1/2"; R-((B/2)+1.5")=24 1/2"; RO/2=36 1/4"; RO2/2=190 5/8"; TRANSITION=49 1/16"; TRANSITION/2=24 17/32"; TRIP_Q=385 3/4"; TRIP_Q-4.5"=381 1/4"; Type Comments=Triple Vari-Plume Laboratory Exhaust Centrifugal Airfoil Class 2 Arr 10 With Mixing Box
- Triple_660_CAVP-36H_CLASS_1_With_Mixing_Box: ((M - (2 * (D - L - K - J))) / 2) + (TRANSITION / 2)=43 7/8"; (B/2)+1.5"=37 1/2"; (B/2)-.125"=35 7/8"; (D-J-K-L)*2=2 3/4"; (E/2)-((B/2)+1.5")=31 15/32"; (E/2)-((MB_P/2)+.125")=27 11/32"; (E/2)-(E/52*15)=29 3/16"; (F-((F-H)/2))/2=36 11/32"; (M - (2 * (D - L - K - J)))/2=25 19/32"; (MB_P/2)+.125"=41 5/8"; (MB_P/2-.125")+((F / 2) - 2")=-77 23/32"; (MB_P/2-.125")-((F / 2) - 2")=-5 1/32"; (MB_Q/2)+.125"=41 5/8"; (NOZZLE_HEIGHT - (NOZZLE_HEIGHT / 8 * 2)) / 2=35 5/8"; (NOZZLE_WB_OD - NOZZLE_TOP_OD) / 4=8"; -((MB_Q / 2) + 1/8")=-41 5/8"; -(F-((F-H)/2))/2=-36 11/32"; -MB_HEIGHT=-93 1/2"; -MB_P=-83"; -MB_P-.25=-83 1/4"; A=270 1/4"; A/2=135 1/8"; B=72"; B/2=36"; B/4=18"; C=160 1/4"; C/2=80 1/8"; CLASS=1"; D=102 1/2"; D-L-K-J=1 3/8"; D-M=48 9/16"; DUAL_Q=249 3/8"; DUAL_Q+.25"=249 5/8"; E=137 15/16"; E-(NOZZLE_RAD/3*2)=51 23/32"; E-N-N-H=2"; E/2=68 31/32"; E/2-H/2=31 5/8"; E/52*15=39 25/32"; E/52*30=79 19/32"; F=76 11/16"; F/2=38 11/32"; H=74 11/16"; H/2=37 11/32"; HEIGHT=125 1/4"; J=15"; J+K+L=101 1/8"; K=29 7/8"; L=56 1/4"; M=53 15/16"; M-(2*(D-L-K-J))=51 3/16"; MB_A=243 5/8"; MB_F=24 1/4"; MB_F-3"=21 1/4"; MB_HEIGHT=93 1/2"; MB_HEIGHT/2=46 3/4"; MB_N=13 5/8"; MB_N-(D-J-K-L)=12 1/4"; MB_P=83"; MB_P+.25"=83 1/4"; MB_P+MB_P+.5=166 1/2"; MB_P-4.5"=78 1/2"; MB_Q=83"; N=29 5/8"; N+(H/2)=66 31/32"; NOZZLE_BOTTOM_ID=51 3/4"; NOZZLE_BOTTOM_RAD=25 7/8"; NOZZLE_BOTTOM_RAD-3*2=19 7/8"; NOZZLE_HEIGHT=95"; NOZZLE_HEIGHT/7*2=23 3/4"; NOZZLE_SIZE=36"; NOZZLE_TOP_OD=58"; NOZZLE_TOP_RAD=29"; NOZZLE_WB/4=18"; NOZZLE_WB_OD=90"; NOZZLE_WB_RAD=45"; NOZZLE_WB_RAD-2"=43"; P=19 1/2"; R=65"; R*1.1=71 1/2"; R+((B/2)+1.5")=102 1/2"; R-((B/2)+1.5")=27 1/2"; RO/2=39 1/4"; RO2/2=205 5/8"; TRANSITION=36 19/32"; TRANSITION/2=18 9/32"; TRIP_Q=415 3/4"; TRIP_Q-4.5"=411 1/4"; Type Comments=Triple Vari-Plume Laboratory Exhaust Centrifugal Airfoil Class 1 Arr 10 With Mixing Box
- Triple_660_CAVP-36L_CLASS_1_With_Mixing_Box: ((M - (2 * (D - L - K - J))) / 2) + (TRANSITION / 2)=43 7/8"; (B/2)+1.5"=37 1/2"; (B/2)-.125"=35 7/8"; (D-J-K-L)*2=2 3/4"; (E/2)-((B/2)+1.5")=31 15/32"; (E/2)-((MB_P/2)+.125")=27 11/32"; (E/2)-(E/52*15)=29 3/16"; (F-((F-H)/2))/2=36 11/32"; (M - (2 * (D - L - K - J)))/2=25 19/32"; (MB_P/2)+.125"=41 5/8"; (MB_P/2-.125")+((F / 2) - 2")=-77 23/32"; (MB_P/2-.125")-((F / 2) - 2")=-5 1/32"; (MB_Q/2)+.125"=41 5/8"; (NOZZLE_HEIGHT - (NOZZLE_HEIGHT / 8 * 2)) / 2=35 5/8"; (NOZZLE_WB_OD - NOZZLE_TOP_OD) / 4=8"; -((MB_Q / 2) + 1/8")=-41 5/8"; -(F-((F-H)/2))/2=-36 11/32"; -MB_HEIGHT=-93 1/2"; -MB_P=-83"; -MB_P-.25=-83 1/4"; A=270 1/4"; A/2=135 1/8"; B=72"; B/2=36"; B/4=18"; C=160 1/4"; C/2=80 1/8"; CLASS=1"; D=102 1/2"; D-L-K-J=1 3/8"; D-M=48 9/16"; DUAL_Q=249 3/8"; DUAL_Q+.25"=249 5/8"; E=137 15/16"; E-(NOZZLE_RAD/3*2)=51 23/32"; E-N-N-H=2"; E/2=68 31/32"; E/2-H/2=31 5/8"; E/52*15=39 25/32"; E/52*30=79 19/32"; F=76 11/16"; F/2=38 11/32"; H=74 11/16"; H/2=37 11/32"; HEIGHT=125 1/4"; J=15"; J+K+L=101 1/8"; K=29 7/8"; L=56 1/4"; M=53 15/16"; M-(2*(D-L-K-J))=51 3/16"; MB_A=243 5/8"; MB_F=24 1/4"; MB_F-3"=21 1/4"; MB_HEIGHT=93 1/2"; MB_HEIGHT/2=46 3/4"; MB_N=13 5/8"; MB_N-(D-J-K-L)=12 1/4"; MB_P=83"; MB_P+.25"=83 1/4"; MB_P+MB_P+.5=166 1/2"; MB_P-4.5"=78 1/2"; MB_Q=83"; N=29 5/8"; N+(H/2)=66 31/32"; NOZZLE_BOTTOM_ID=51 3/4"; NOZZLE_BOTTOM_RAD=25 7/8"; NOZZLE_BOTTOM_RAD-3*2=19 7/8"; NOZZLE_HEIGHT=95"; NOZZLE_HEIGHT/7*2=23 3/4"; NOZZLE_SIZE=36"; NOZZLE_TOP_OD=58"; NOZZLE_TOP_RAD=29"; NOZZLE_WB/4=18"; NOZZLE_WB_OD=90"; NOZZLE_WB_RAD=45"; NOZZLE_WB_RAD-2"=43"; P=19 1/2"; R=65"; R*1.1=71 1/2"; R+((B/2)+1.5")=102 1/2"; R-((B/2)+1.5")=27 1/2"; RO/2=39 1/4"; RO2/2=205 5/8"; TRANSITION=36 19/32"; TRANSITION/2=18 9/32"; TRIP_Q=415 3/4"; TRIP_Q-4.5"=411 1/4"; Type Comments=Triple Vari-Plume Laboratory Exhaust Centrifugal Airfoil Class 1 Arr 10 With Mixing Box
- Triple_660_CAVP-49H_CLASS_1_With_Mixing_Box: ((M - (2 * (D - L - K - J))) / 2) + (TRANSITION / 2)=50 1/8"; (B/2)+1.5"=37 1/2"; (B/2)-.125"=35 7/8"; (D-J-K-L)*2=2 3/4"; (E/2)-((B/2)+1.5")=31 15/32"; (E/2)-((MB_P/2)+.125")=27 11/32"; (E/2)-(E/52*15)=29 3/16"; (F-((F-H)/2))/2=36 11/32"; (M - (2 * (D - L - K - J)))/2=25 19/32"; (MB_P/2)+.125"=41 5/8"; (MB_P/2-.125")+((F / 2) - 2")=-77 23/32"; (MB_P/2-.125")-((F / 2) - 2")=-5 1/32"; (MB_Q/2)+.125"=41 5/8"; (NOZZLE_HEIGHT - (NOZZLE_HEIGHT / 8 * 2)) / 2=41 1/4"; (NOZZLE_WB_OD - NOZZLE_TOP_OD) / 4=6 1/4"; -((MB_Q / 2) + 1/8")=-41 5/8"; -(F-((F-H)/2))/2=-36 11/32"; -MB_HEIGHT=-93 1/2"; -MB_P=-83"; -MB_P-.25=-83 1/4"; A=270 1/4"; A/2=135 1/8"; B=72"; B/2=36"; B/4=18"; C=160 1/4"; C/2=80 1/8"; CLASS=1"; D=102 1/2"; D-L-K-J=1 3/8"; D-M=48 9/16"; DUAL_Q=249 3/8"; DUAL_Q+.25"=249 5/8"; E=137 15/16"; E-(NOZZLE_RAD/3*2)=45 27/32"; E-N-N-H=2"; E/2=68 31/32"; E/2-H/2=31 5/8"; E/52*15=39 25/32"; E/52*30=79 19/32"; F=76 11/16"; F/2=38 11/32"; H=74 11/16"; H/2=37 11/32"; HEIGHT=125 1/4"; J=15"; J+K+L=101 1/8"; K=29 7/8"; L=56 1/4"; M=53 15/16"; M-(2*(D-L-K-J))=51 3/16"; MB_A=243 5/8"; MB_F=24 1/4"; MB_F-3"=21 1/4"; MB_HEIGHT=93 1/2"; MB_HEIGHT/2=46 3/4"; MB_N=13 5/8"; MB_N-(D-J-K-L)=12 1/4"; MB_P=83"; MB_P+.25"=83 1/4"; MB_P+MB_P+.5=166 1/2"; MB_P-4.5"=78 1/2"; MB_Q=83"; N=29 5/8"; N+(H/2)=66 31/32"; NOZZLE_BOTTOM_ID=69 3/8"; NOZZLE_BOTTOM_RAD=34 11/16"; NOZZLE_BOTTOM_RAD-3*2=28 11/16"; NOZZLE_HEIGHT=110"; NOZZLE_HEIGHT/7*2=27 1/2"; NOZZLE_SIZE=49"; NOZZLE_TOP_OD=76"; NOZZLE_TOP_RAD=38"; NOZZLE_WB/4=20 3/16"; NOZZLE_WB_OD=101"; NOZZLE_WB_RAD=50 1/2"; NOZZLE_WB_RAD-2"=48 1/2"; P=19 1/2"; R=65"; R*1.1=71 1/2"; R+((B/2)+1.5")=102 1/2"; R-((B/2)+1.5")=27 1/2"; RO/2=39 1/4"; RO2/2=205 5/8"; TRANSITION=49 1/16"; TRANSITION/2=24 17/32"; TRIP_Q=415 3/4"; TRIP_Q-4.5"=411 1/4"; Type Comments=Triple Vari-Plume Laboratory Exhaust Centrifugal Airfoil Class 1 Arr 10 With Mixing Box
- Triple_660_CAVP-49L_CLASS_1_With_Mixing_Box: ((M - (2 * (D - L - K - J))) / 2) + (TRANSITION / 2)=50 1/8"; (B/2)+1.5"=37 1/2"; (B/2)-.125"=35 7/8"; (D-J-K-L)*2=2 3/4"; (E/2)-((B/2)+1.5")=31 15/32"; (E/2)-((MB_P/2)+.125")=27 11/32"; (E/2)-(E/52*15)=29 3/16"; (F-((F-H)/2))/2=36 11/32"; (M - (2 * (D - L - K - J)))/2=25 19/32"; (MB_P/2)+.125"=41 5/8"; (MB_P/2-.125")+((F / 2) - 2")=-77 23/32"; (MB_P/2-.125")-((F / 2) - 2")=-5 1/32"; (MB_Q/2)+.125"=41 5/8"; (NOZZLE_HEIGHT - (NOZZLE_HEIGHT / 8 * 2)) / 2=41 1/4"; (NOZZLE_WB_OD - NOZZLE_TOP_OD) / 4=6 1/4"; -((MB_Q / 2) + 1/8")=-41 5/8"; -(F-((F-H)/2))/2=-36 11/32"; -MB_HEIGHT=-93 1/2"; -MB_P=-83"; -MB_P-.25=-83 1/4"; A=270 1/4"; A/2=135 1/8"; B=72"; B/2=36"; B/4=18"; C=160 1/4"; C/2=80 1/8"; CLASS=1"; D=102 1/2"; D-L-K-J=1 3/8"; D-M=48 9/16"; DUAL_Q=249 3/8"; DUAL_Q+.25"=249 5/8"; E=137 15/16"; E-(NOZZLE_RAD/3*2)=45 27/32"; E-N-N-H=2"; E/2=68 31/32"; E/2-H/2=31 5/8"; E/52*15=39 25/32"; E/52*30=79 19/32"; F=76 11/16"; F/2=38 11/32"; H=74 11/16"; H/2=37 11/32"; HEIGHT=125 1/4"; J=15"; J+K+L=101 1/8"; K=29 7/8"; L=56 1/4"; M=53 15/16"; M-(2*(D-L-K-J))=51 3/16"; MB_A=243 5/8"; MB_F=24 1/4"; MB_F-3"=21 1/4"; MB_HEIGHT=93 1/2"; MB_HEIGHT/2=46 3/4"; MB_N=13 5/8"; MB_N-(D-J-K-L)=12 1/4"; MB_P=83"; MB_P+.25"=83 1/4"; MB_P+MB_P+.5=166 1/2"; MB_P-4.5"=78 1/2"; MB_Q=83"; N=29 5/8"; N+(H/2)=66 31/32"; NOZZLE_BOTTOM_ID=69 3/8"; NOZZLE_BOTTOM_RAD=34 11/16"; NOZZLE_BOTTOM_RAD-3*2=28 11/16"; NOZZLE_HEIGHT=110"; NOZZLE_HEIGHT/7*2=27 1/2"; NOZZLE_SIZE=49"; NOZZLE_TOP_OD=76"; NOZZLE_TOP_RAD=38"; NOZZLE_WB/4=20 3/16"; NOZZLE_WB_OD=101"; NOZZLE_WB_RAD=50 1/2"; NOZZLE_WB_RAD-2"=48 1/2"; P=19 1/2"; R=65"; R*1.1=71 1/2"; R+((B/2)+1.5")=102 1/2"; R-((B/2)+1.5")=27 1/2"; RO/2=39 1/4"; RO2/2=205 5/8"; TRANSITION=49 1/16"; TRANSITION/2=24 17/32"; TRIP_Q=415 3/4"; TRIP_Q-4.5"=411 1/4"; Type Comments=Triple Vari-Plume Laboratory Exhaust Centrifugal Airfoil Class 1 Arr 10 With Mixing Box
- Triple_660_CAVP-36H_CLASS_2_With_Mixing_Box: ((M - (2 * (D - L - K - J))) / 2) + (TRANSITION / 2)=43 7/8"; (B/2)+1.5"=37 1/2"; (B/2)-.125"=35 7/8"; (D-J-K-L)*2=2 3/4"; (E/2)-((B/2)+1.5")=31 15/32"; (E/2)-((MB_P/2)+.125")=27 11/32"; (E/2)-(E/52*15)=29 3/16"; (F-((F-H)/2))/2=36 11/32"; (M - (2 * (D - L - K - J)))/2=25 19/32"; (MB_P/2)+.125"=41 5/8"; (MB_P/2-.125")+((F / 2) - 2")=-77 23/32"; (MB_P/2-.125")-((F / 2) - 2")=-5 1/32"; (MB_Q/2)+.125"=41 5/8"; (NOZZLE_HEIGHT - (NOZZLE_HEIGHT / 8 * 2)) / 2=35 5/8"; (NOZZLE_WB_OD - NOZZLE_TOP_OD) / 4=8"; -((MB_Q / 2) + 1/8")=-41 5/8"; -(F-((F-H)/2))/2=-36 11/32"; -MB_HEIGHT=-93 1/2"; -MB_P=-83"; -MB_P-.25=-83 1/4"; A=270 1/4"; A/2=135 1/8"; B=72"; B/2=36"; B/4=18"; C=160 1/4"; C/2=80 1/8"; CLASS=2"; D=111 1/4"; D-L-K-J=1 3/8"; D-M=57 5/16"; DUAL_Q=249 3/8"; DUAL_Q+.25"=249 5/8"; E=137 15/16"; E-(NOZZLE_RAD/3*2)=51 23/32"; E-N-N-H=2"; E/2=68 31/32"; E/2-H/2=31 5/8"; E/52*15=39 25/32"; E/52*30=79 19/32"; F=76 11/16"; F/2=38 11/32"; H=74 11/16"; H/2=37 11/32"; HEIGHT=125 1/4"; J=15"; J+K+L=109 7/8"; K=38 5/8"; L=56 1/4"; M=53 15/16"; M-(2*(D-L-K-J))=51 3/16"; MB_A=252 3/8"; MB_F=24 1/4"; MB_F-3"=21 1/4"; MB_HEIGHT=93 1/2"; MB_HEIGHT/2=46 3/4"; MB_N=13 5/8"; MB_N-(D-J-K-L)=12 1/4"; MB_P=83"; MB_P+.25"=83 1/4"; MB_P+MB_P+.5=166 1/2"; MB_P-4.5"=78 1/2"; MB_Q=83"; N=29 5/8"; N+(H/2)=66 31/32"; NOZZLE_BOTTOM_ID=51 3/4"; NOZZLE_BOTTOM_RAD=25 7/8"; NOZZLE_BOTTOM_RAD-3*2=19 7/8"; NOZZLE_HEIGHT=95"; NOZZLE_HEIGHT/7*2=23 3/4"; NOZZLE_SIZE=36"; NOZZLE_TOP_OD=58"; NOZZLE_TOP_RAD=29"; NOZZLE_WB/4=18"; NOZZLE_WB_OD=90"; NOZZLE_WB_RAD=45"; NOZZLE_WB_RAD-2"=43"; P=29 1/2"; R=65"; R*1.1=71 1/2"; R+((B/2)+1.5")=102 1/2"; R-((B/2)+1.5")=27 1/2"; RO/2=39 1/4"; RO2/2=205 5/8"; TRANSITION=36 19/32"; TRANSITION/2=18 9/32"; TRIP_Q=415 3/4"; TRIP_Q-4.5"=411 1/4"; Type Comments=Triple Vari-Plume Laboratory Exhaust Centrifugal Airfoil Class 2 Arr 10 With Mixing Box
- Triple_660_CAVP-36L_CLASS_2_With_Mixing_Box: ((M - (2 * (D - L - K - J))) / 2) + (TRANSITION / 2)=43 7/8"; (B/2)+1.5"=37 1/2"; (B/2)-.125"=35 7/8"; (D-J-K-L)*2=2 3/4"; (E/2)-((B/2)+1.5")=31 15/32"; (E/2)-((MB_P/2)+.125")=27 11/32"; (E/2)-(E/52*15)=29 3/16"; (F-((F-H)/2))/2=36 11/32"; (M - (2 * (D - L - K - J)))/2=25 19/32"; (MB_P/2)+.125"=41 5/8"; (MB_P/2-.125")+((F / 2) - 2")=-77 23/32"; (MB_P/2-.125")-((F / 2) - 2")=-5 1/32"; (MB_Q/2)+.125"=41 5/8"; (NOZZLE_HEIGHT - (NOZZLE_HEIGHT / 8 * 2)) / 2=35 5/8"; (NOZZLE_WB_OD - NOZZLE_TOP_OD) / 4=8"; -((MB_Q / 2) + 1/8")=-41 5/8"; -(F-((F-H)/2))/2=-36 11/32"; -MB_HEIGHT=-93 1/2"; -MB_P=-83"; -MB_P-.25=-83 1/4"; A=270 1/4"; A/2=135 1/8"; B=72"; B/2=36"; B/4=18"; C=160 1/4"; C/2=80 1/8"; CLASS=2"; D=111 1/4"; D-L-K-J=1 3/8"; D-M=57 5/16"; DUAL_Q=249 3/8"; DUAL_Q+.25"=249 5/8"; E=137 15/16"; E-(NOZZLE_RAD/3*2)=51 23/32"; E-N-N-H=2"; E/2=68 31/32"; E/2-H/2=31 5/8"; E/52*15=39 25/32"; E/52*30=79 19/32"; F=76 11/16"; F/2=38 11/32"; H=74 11/16"; H/2=37 11/32"; HEIGHT=125 1/4"; J=15"; J+K+L=109 7/8"; K=38 5/8"; L=56 1/4"; M=53 15/16"; M-(2*(D-L-K-J))=51 3/16"; MB_A=252 3/8"; MB_F=24 1/4"; MB_F-3"=21 1/4"; MB_HEIGHT=93 1/2"; MB_HEIGHT/2=46 3/4"; MB_N=13 5/8"; MB_N-(D-J-K-L)=12 1/4"; MB_P=83"; MB_P+.25"=83 1/4"; MB_P+MB_P+.5=166 1/2"; MB_P-4.5"=78 1/2"; MB_Q=83"; N=29 5/8"; N+(H/2)=66 31/32"; NOZZLE_BOTTOM_ID=51 3/4"; NOZZLE_BOTTOM_RAD=25 7/8"; NOZZLE_BOTTOM_RAD-3*2=19 7/8"; NOZZLE_HEIGHT=95"; NOZZLE_HEIGHT/7*2=23 3/4"; NOZZLE_SIZE=36"; NOZZLE_TOP_OD=58"; NOZZLE_TOP_RAD=29"; NOZZLE_WB/4=18"; NOZZLE_WB_OD=90"; NOZZLE_WB_RAD=45"; NOZZLE_WB_RAD-2"=43"; P=29 1/2"; R=65"; R*1.1=71 1/2"; R+((B/2)+1.5")=102 1/2"; R-((B/2)+1.5")=27 1/2"; RO/2=39 1/4"; RO2/2=205 5/8"; TRANSITION=36 19/32"; TRANSITION/2=18 9/32"; TRIP_Q=415 3/4"; TRIP_Q-4.5"=411 1/4"; Type Comments=Triple Vari-Plume Laboratory Exhaust Centrifugal Airfoil Class 2 Arr 10 With Mixing Box
- Triple_660_CAVP-49L_CLASS_2_With_Mixing_Box: ((M - (2 * (D - L - K - J))) / 2) + (TRANSITION / 2)=50 1/8"; (B/2)+1.5"=37 1/2"; (B/2)-.125"=35 7/8"; (D-J-K-L)*2=2 3/4"; (E/2)-((B/2)+1.5")=31 15/32"; (E/2)-((MB_P/2)+.125")=27 11/32"; (E/2)-(E/52*15)=29 3/16"; (F-((F-H)/2))/2=36 11/32"; (M - (2 * (D - L - K - J)))/2=25 19/32"; (MB_P/2)+.125"=41 5/8"; (MB_P/2-.125")+((F / 2) - 2")=-77 23/32"; (MB_P/2-.125")-((F / 2) - 2")=-5 1/32"; (MB_Q/2)+.125"=41 5/8"; (NOZZLE_HEIGHT - (NOZZLE_HEIGHT / 8 * 2)) / 2=41 1/4"; (NOZZLE_WB_OD - NOZZLE_TOP_OD) / 4=6 1/4"; -((MB_Q / 2) + 1/8")=-41 5/8"; -(F-((F-H)/2))/2=-36 11/32"; -MB_HEIGHT=-93 1/2"; -MB_P=-83"; -MB_P-.25=-83 1/4"; A=270 1/4"; A/2=135 1/8"; B=72"; B/2=36"; B/4=18"; C=160 1/4"; C/2=80 1/8"; CLASS=2"; D=111 1/4"; D-L-K-J=1 3/8"; D-M=57 5/16"; DUAL_Q=249 3/8"; DUAL_Q+.25"=249 5/8"; E=137 15/16"; E-(NOZZLE_RAD/3*2)=45 27/32"; E-N-N-H=2"; E/2=68 31/32"; E/2-H/2=31 5/8"; E/52*15=39 25/32"; E/52*30=79 19/32"; F=76 11/16"; F/2=38 11/32"; H=74 11/16"; H/2=37 11/32"; HEIGHT=125 1/4"; J=15"; J+K+L=109 7/8"; K=38 5/8"; L=56 1/4"; M=53 15/16"; M-(2*(D-L-K-J))=51 3/16"; MB_A=252 3/8"; MB_F=24 1/4"; MB_F-3"=21 1/4"; MB_HEIGHT=93 1/2"; MB_HEIGHT/2=46 3/4"; MB_N=13 5/8"; MB_N-(D-J-K-L)=12 1/4"; MB_P=83"; MB_P+.25"=83 1/4"; MB_P+MB_P+.5=166 1/2"; MB_P-4.5"=78 1/2"; MB_Q=83"; N=29 5/8"; N+(H/2)=66 31/32"; NOZZLE_BOTTOM_ID=69 3/8"; NOZZLE_BOTTOM_RAD=34 11/16"; NOZZLE_BOTTOM_RAD-3*2=28 11/16"; NOZZLE_HEIGHT=110"; NOZZLE_HEIGHT/7*2=27 1/2"; NOZZLE_SIZE=49"; NOZZLE_TOP_OD=76"; NOZZLE_TOP_RAD=38"; NOZZLE_WB/4=20 3/16"; NOZZLE_WB_OD=101"; NOZZLE_WB_RAD=50 1/2"; NOZZLE_WB_RAD-2"=48 1/2"; P=29 1/2"; R=65"; R*1.1=71 1/2"; R+((B/2)+1.5")=102 1/2"; R-((B/2)+1.5")=27 1/2"; RO/2=39 1/4"; RO2/2=205 5/8"; TRANSITION=49 1/16"; TRANSITION/2=24 17/32"; TRIP_Q=415 3/4"; TRIP_Q-4.5"=411 1/4"; Type Comments=Triple Vari-Plume Laboratory Exhaust Centrifugal Airfoil Class 2 Arr 10 With Mixing Box
- Triple_730_CAVP-36H_CLASS_1_With_Mixing_Box: ((M - (2 * (D - L - K - J))) / 2) + (TRANSITION / 2)=46 17/32"; (B/2)+1.5"=41"; (B/2)-.125"=39 3/8"; (D-J-K-L)*2=2 3/4"; (E/2)-((B/2)+1.5")=35 3/16"; (E/2)-((MB_P/2)+.125")=31 1/16"; (E/2)-(E/52*15)=32 7/32"; (F-((F-H)/2))/2=39 27/32"; (M - (2 * (D - L - K - J)))/2=28 1/4"; (MB_P/2)+.125"=45 1/8"; (MB_P/2-.125")+((F / 2) - 2")=-84 23/32"; (MB_P/2-.125")-((F / 2) - 2")=-5 1/32"; (MB_Q/2)+.125"=45 1/8"; (NOZZLE_HEIGHT - (NOZZLE_HEIGHT / 8 * 2)) / 2=35 5/8"; (NOZZLE_WB_OD - NOZZLE_TOP_OD) / 4=8"; -((MB_Q / 2) + 1/8")=-45 1/8"; -(F-((F-H)/2))/2=-39 27/32"; -MB_HEIGHT=-104"; -MB_P=-90"; -MB_P-.25=-90 1/4"; A=286 3/8"; A/2=143 3/16"; B=79"; B/2=39 1/2"; B/4=19 3/4"; C=176 3/8"; C/2=88 3/16"; CLASS=1"; D=108 5/16"; D-L-K-J=1 3/8"; D-M=49 1/16"; DUAL_Q=270 3/8"; DUAL_Q+.25"=270 5/8"; E=152 3/8"; E-(NOZZLE_RAD/3*2)=58 15/16"; E-N-N-H=2"; E/2=76 3/16"; E/2-H/2=35 11/32"; E/52*15=43 31/32"; E/52*30=87 29/32"; F=83 11/16"; F/2=41 27/32"; H=81 11/16"; H/2=40 27/32"; HEIGHT=138 17/32"; J=15 1/2"; J+K+L=106 15/16"; K=29 7/8"; L=61 9/16"; M=59 1/4"; M-(2*(D-L-K-J))=56 1/2"; MB_A=248"; MB_F=27 3/4"; MB_F-3"=24 3/4"; MB_HEIGHT=104"; MB_HEIGHT/2=52"; MB_N=13 5/8"; MB_N-(D-J-K-L)=12 1/4"; MB_P=90"; MB_P+.25"=90 1/4"; MB_P+MB_P+.5=180 1/2"; MB_P-4.5"=85 1/2"; MB_Q=90"; N=33 11/32"; N+(H/2)=74 3/16"; NOZZLE_BOTTOM_ID=51 3/4"; NOZZLE_BOTTOM_RAD=25 7/8"; NOZZLE_BOTTOM_RAD-3*2=19 7/8"; NOZZLE_HEIGHT=95"; NOZZLE_HEIGHT/7*2=23 3/4"; NOZZLE_SIZE=36"; NOZZLE_TOP_OD=58"; NOZZLE_TOP_RAD=29"; NOZZLE_WB/4=18"; NOZZLE_WB_OD=90"; NOZZLE_WB_RAD=45"; NOZZLE_WB_RAD-2"=43"; P=22 1/8"; R=72"; R*1.1=79 3/16"; R+((B/2)+1.5")=113"; R-((B/2)+1.5")=31"; RO/2=42 3/4"; RO2/2=223 1/8"; TRANSITION=36 19/32"; TRANSITION/2=18 9/32"; TRIP_Q=450 3/4"; TRIP_Q-4.5"=446 1/4"; Type Comments=Triple Vari-Plume Laboratory Exhaust Centrifugal Airfoil Class 1 Arr 10 With Mixing Box
- Triple_730_CAVP-36L_CLASS_1_With_Mixing_Box: ((M - (2 * (D - L - K - J))) / 2) + (TRANSITION / 2)=46 17/32"; (B/2)+1.5"=41"; (B/2)-.125"=39 3/8"; (D-J-K-L)*2=2 3/4"; (E/2)-((B/2)+1.5")=35 3/16"; (E/2)-((MB_P/2)+.125")=31 1/16"; (E/2)-(E/52*15)=32 7/32"; (F-((F-H)/2))/2=39 27/32"; (M - (2 * (D - L - K - J)))/2=28 1/4"; (MB_P/2)+.125"=45 1/8"; (MB_P/2-.125")+((F / 2) - 2")=-84 23/32"; (MB_P/2-.125")-((F / 2) - 2")=-5 1/32"; (MB_Q/2)+.125"=45 1/8"; (NOZZLE_HEIGHT - (NOZZLE_HEIGHT / 8 * 2)) / 2=35 5/8"; (NOZZLE_WB_OD - NOZZLE_TOP_OD) / 4=8"; -((MB_Q / 2) + 1/8")=-45 1/8"; -(F-((F-H)/2))/2=-39 27/32"; -MB_HEIGHT=-104"; -MB_P=-90"; -MB_P-.25=-90 1/4"; A=286 3/8"; A/2=143 3/16"; B=79"; B/2=39 1/2"; B/4=19 3/4"; C=176 3/8"; C/2=88 3/16"; CLASS=1"; D=108 5/16"; D-L-K-J=1 3/8"; D-M=49 1/16"; DUAL_Q=270 3/8"; DUAL_Q+.25"=270 5/8"; E=152 3/8"; E-(NOZZLE_RAD/3*2)=58 15/16"; E-N-N-H=2"; E/2=76 3/16"; E/2-H/2=35 11/32"; E/52*15=43 31/32"; E/52*30=87 29/32"; F=83 11/16"; F/2=41 27/32"; H=81 11/16"; H/2=40 27/32"; HEIGHT=138 17/32"; J=15 1/2"; J+K+L=106 15/16"; K=29 7/8"; L=61 9/16"; M=59 1/4"; M-(2*(D-L-K-J))=56 1/2"; MB_A=261 11/16"; MB_F=27 3/4"; MB_F-3"=24 3/4"; MB_HEIGHT=104"; MB_HEIGHT/2=52"; MB_N=13 5/8"; MB_N-(D-J-K-L)=12 1/4"; MB_P=90"; MB_P+.25"=90 1/4"; MB_P+MB_P+.5=180 1/2"; MB_P-4.5"=85 1/2"; MB_Q=90"; N=33 11/32"; N+(H/2)=74 3/16"; NOZZLE_BOTTOM_ID=51 3/4"; NOZZLE_BOTTOM_RAD=25 7/8"; NOZZLE_BOTTOM_RAD-3*2=19 7/8"; NOZZLE_HEIGHT=95"; NOZZLE_HEIGHT/7*2=23 3/4"; NOZZLE_SIZE=36"; NOZZLE_TOP_OD=58"; NOZZLE_TOP_RAD=29"; NOZZLE_WB/4=18"; NOZZLE_WB_OD=90"; NOZZLE_WB_RAD=45"; NOZZLE_WB_RAD-2"=43"; P=22 1/8"; R=72"; R*1.1=79 3/16"; R+((B/2)+1.5")=113"; R-((B/2)+1.5")=31"; RO/2=42 3/4"; RO2/2=223 1/8"; TRANSITION=36 19/32"; TRANSITION/2=18 9/32"; TRIP_Q=450 3/4"; TRIP_Q-4.5"=446 1/4"; Type Comments=Triple Vari-Plume Laboratory Exhaust Centrifugal Airfoil Class 1 Arr 10 With Mixing Box
- Triple_730_CAVP-49H_CLASS_1_With_Mixing_Box: ((M - (2 * (D - L - K - J))) / 2) + (TRANSITION / 2)=52 25/32"; (B/2)+1.5"=41"; (B/2)-.125"=39 3/8"; (D-J-K-L)*2=2 3/4"; (E/2)-((B/2)+1.5")=35 3/16"; (E/2)-((MB_P/2)+.125")=31 1/16"; (E/2)-(E/52*15)=32 7/32"; (F-((F-H)/2))/2=39 27/32"; (M - (2 * (D - L - K - J)))/2=28 1/4"; (MB_P/2)+.125"=45 1/8"; (MB_P/2-.125")+((F / 2) - 2")=-84 23/32"; (MB_P/2-.125")-((F / 2) - 2")=-5 1/32"; (MB_Q/2)+.125"=45 1/8"; (NOZZLE_HEIGHT - (NOZZLE_HEIGHT / 8 * 2)) / 2=41 1/4"; (NOZZLE_WB_OD - NOZZLE_TOP_OD) / 4=6 1/4"; -((MB_Q / 2) + 1/8")=-45 1/8"; -(F-((F-H)/2))/2=-39 27/32"; -MB_HEIGHT=-104"; -MB_P=-90"; -MB_P-.25=-90 1/4"; A=286 3/8"; A/2=143 3/16"; B=79"; B/2=39 1/2"; B/4=19 3/4"; C=176 3/8"; C/2=88 3/16"; CLASS=1"; D=108 5/16"; D-L-K-J=1 3/8"; D-M=49 1/16"; DUAL_Q=270 3/8"; DUAL_Q+.25"=270 5/8"; E=152 3/8"; E-(NOZZLE_RAD/3*2)=53 1/16"; E-N-N-H=2"; E/2=76 3/16"; E/2-H/2=35 11/32"; E/52*15=43 31/32"; E/52*30=87 29/32"; F=83 11/16"; F/2=41 27/32"; H=81 11/16"; H/2=40 27/32"; HEIGHT=138 17/32"; J=15 1/2"; J+K+L=106 15/16"; K=29 7/8"; L=61 9/16"; M=59 1/4"; M-(2*(D-L-K-J))=56 1/2"; MB_A=261 11/16"; MB_F=27 3/4"; MB_F-3"=24 3/4"; MB_HEIGHT=104"; MB_HEIGHT/2=52"; MB_N=13 5/8"; MB_N-(D-J-K-L)=12 1/4"; MB_P=90"; MB_P+.25"=90 1/4"; MB_P+MB_P+.5=180 1/2"; MB_P-4.5"=85 1/2"; MB_Q=90"; N=33 11/32"; N+(H/2)=74 3/16"; NOZZLE_BOTTOM_ID=69 3/8"; NOZZLE_BOTTOM_RAD=34 11/16"; NOZZLE_BOTTOM_RAD-3*2=28 11/16"; NOZZLE_HEIGHT=110"; NOZZLE_HEIGHT/7*2=27 1/2"; NOZZLE_SIZE=49"; NOZZLE_TOP_OD=76"; NOZZLE_TOP_RAD=38"; NOZZLE_WB/4=20 3/16"; NOZZLE_WB_OD=101"; NOZZLE_WB_RAD=50 1/2"; NOZZLE_WB_RAD-2"=48 1/2"; P=22 1/8"; R=72"; R*1.1=79 3/16"; R+((B/2)+1.5")=113"; R-((B/2)+1.5")=31"; RO/2=42 3/4"; RO2/2=223 1/8"; TRANSITION=49 1/16"; TRANSITION/2=24 17/32"; TRIP_Q=450 3/4"; TRIP_Q-4.5"=446 1/4"; Type Comments=Triple Vari-Plume Laboratory Exhaust Centrifugal Airfoil Class 1 Arr 10 With Mixing Box
- Triple_730_CAVP-49L_CLASS_1_With_Mixing_Box: ((M - (2 * (D - L - K - J))) / 2) + (TRANSITION / 2)=52 25/32"; (B/2)+1.5"=41"; (B/2)-.125"=39 3/8"; (D-J-K-L)*2=2 3/4"; (E/2)-((B/2)+1.5")=35 3/16"; (E/2)-((MB_P/2)+.125")=31 1/16"; (E/2)-(E/52*15)=32 7/32"; (F-((F-H)/2))/2=39 27/32"; (M - (2 * (D - L - K - J)))/2=28 1/4"; (MB_P/2)+.125"=45 1/8"; (MB_P/2-.125")+((F / 2) - 2")=-84 23/32"; (MB_P/2-.125")-((F / 2) - 2")=-5 1/32"; (MB_Q/2)+.125"=45 1/8"; (NOZZLE_HEIGHT - (NOZZLE_HEIGHT / 8 * 2)) / 2=41 1/4"; (NOZZLE_WB_OD - NOZZLE_TOP_OD) / 4=6 1/4"; -((MB_Q / 2) + 1/8")=-45 1/8"; -(F-((F-H)/2))/2=-39 27/32"; -MB_HEIGHT=-104"; -MB_P=-90"; -MB_P-.25=-90 1/4"; A=286 3/8"; A/2=143 3/16"; B=79"; B/2=39 1/2"; B/4=19 3/4"; C=176 3/8"; C/2=88 3/16"; CLASS=1"; D=108 5/16"; D-L-K-J=1 3/8"; D-M=49 1/16"; DUAL_Q=270 3/8"; DUAL_Q+.25"=270 5/8"; E=152 3/8"; E-(NOZZLE_RAD/3*2)=53 1/16"; E-N-N-H=2"; E/2=76 3/16"; E/2-H/2=35 11/32"; E/52*15=43 31/32"; E/52*30=87 29/32"; F=83 11/16"; F/2=41 27/32"; H=81 11/16"; H/2=40 27/32"; HEIGHT=138 17/32"; J=15 1/2"; J+K+L=106 15/16"; K=29 7/8"; L=61 9/16"; M=59 1/4"; M-(2*(D-L-K-J))=56 1/2"; MB_A=261 11/16"; MB_F=27 3/4"; MB_F-3"=24 3/4"; MB_HEIGHT=104"; MB_HEIGHT/2=52"; MB_N=13 5/8"; MB_N-(D-J-K-L)=12 1/4"; MB_P=90"; MB_P+.25"=90 1/4"; MB_P+MB_P+.5=180 1/2"; MB_P-4.5"=85 1/2"; MB_Q=90"; N=33 11/32"; N+(H/2)=74 3/16"; NOZZLE_BOTTOM_ID=69 3/8"; NOZZLE_BOTTOM_RAD=34 11/16"; NOZZLE_BOTTOM_RAD-3*2=28 11/16"; NOZZLE_HEIGHT=110"; NOZZLE_HEIGHT/7*2=27 1/2"; NOZZLE_SIZE=49"; NOZZLE_TOP_OD=76"; NOZZLE_TOP_RAD=38"; NOZZLE_WB/4=20 3/16"; NOZZLE_WB_OD=101"; NOZZLE_WB_RAD=50 1/2"; NOZZLE_WB_RAD-2"=48 1/2"; P=22 1/8"; R=72"; R*1.1=79 3/16"; R+((B/2)+1.5")=113"; R-((B/2)+1.5")=31"; RO/2=42 3/4"; RO2/2=223 1/8"; TRANSITION=49 1/16"; TRANSITION/2=24 17/32"; TRIP_Q=450 3/4"; TRIP_Q-4.5"=446 1/4"; Type Comments=Triple Vari-Plume Laboratory Exhaust Centrifugal Airfoil Class 1 Arr 10 With Mixing Box
- Triple_730_CAVP-36H_CLASS_2_With_Mixing_Box: ((M - (2 * (D - L - K - J))) / 2) + (TRANSITION / 2)=46 17/32"; (B/2)+1.5"=41"; (B/2)-.125"=39 3/8"; (D-J-K-L)*2=2 3/4"; (E/2)-((B/2)+1.5")=35 3/16"; (E/2)-((MB_P/2)+.125")=31 1/16"; (E/2)-(E/52*15)=32 7/32"; (F-((F-H)/2))/2=39 27/32"; (M - (2 * (D - L - K - J)))/2=28 1/4"; (MB_P/2)+.125"=45 1/8"; (MB_P/2-.125")+((F / 2) - 2")=-84 23/32"; (MB_P/2-.125")-((F / 2) - 2")=-5 1/32"; (MB_Q/2)+.125"=45 1/8"; (NOZZLE_HEIGHT - (NOZZLE_HEIGHT / 8 * 2)) / 2=35 5/8"; (NOZZLE_WB_OD - NOZZLE_TOP_OD) / 4=8"; -((MB_Q / 2) + 1/8")=-45 1/8"; -(F-((F-H)/2))/2=-39 27/32"; -MB_HEIGHT=-104"; -MB_P=-90"; -MB_P-.25=-90 1/4"; A=286 3/8"; A/2=143 3/16"; B=79"; B/2=39 1/2"; B/4=19 3/4"; C=176 3/8"; C/2=88 3/16"; CLASS=2"; D=117"; D-L-K-J=1 3/8"; D-M=57 3/4"; DUAL_Q=270 3/8"; DUAL_Q+.25"=270 5/8"; E=152 3/8"; E-(NOZZLE_RAD/3*2)=58 15/16"; E-N-N-H=2"; E/2=76 3/16"; E/2-H/2=35 11/32"; E/52*15=43 31/32"; E/52*30=87 29/32"; F=83 11/16"; F/2=41 27/32"; H=81 11/16"; H/2=40 27/32"; HEIGHT=138 17/32"; J=15 1/2"; J+K+L=115 5/8"; K=38 5/8"; L=61 1/2"; M=59 1/4"; M-(2*(D-L-K-J))=56 1/2"; MB_A=270 7/16"; MB_F=27 3/4"; MB_F-3"=24 3/4"; MB_HEIGHT=104"; MB_HEIGHT/2=52"; MB_N=13 5/8"; MB_N-(D-J-K-L)=12 1/4"; MB_P=90"; MB_P+.25"=90 1/4"; MB_P+MB_P+.5=180 1/2"; MB_P-4.5"=85 1/2"; MB_Q=90"; N=33 11/32"; N+(H/2)=74 3/16"; NOZZLE_BOTTOM_ID=51 3/4"; NOZZLE_BOTTOM_RAD=25 7/8"; NOZZLE_BOTTOM_RAD-3*2=19 7/8"; NOZZLE_HEIGHT=95"; NOZZLE_HEIGHT/7*2=23 3/4"; NOZZLE_SIZE=36"; NOZZLE_TOP_OD=58"; NOZZLE_TOP_RAD=29"; NOZZLE_WB/4=18"; NOZZLE_WB_OD=90"; NOZZLE_WB_RAD=45"; NOZZLE_WB_RAD-2"=43"; P=29 1/2"; R=72"; R*1.1=79 3/16"; R+((B/2)+1.5")=113"; R-((B/2)+1.5")=31"; RO/2=42 3/4"; RO2/2=223 1/8"; TRANSITION=36 19/32"; TRANSITION/2=18 9/32"; TRIP_Q=450 3/4"; TRIP_Q-4.5"=446 1/4"; Type Comments=Triple Vari-Plume Laboratory Exhaust Centrifugal Airfoil Class 2 Arr 10 With Mixing Box
- Triple_730_CAVP-36L_CLASS_2_With_Mixing_Box: ((M - (2 * (D - L - K - J))) / 2) + (TRANSITION / 2)=46 17/32"; (B/2)+1.5"=41"; (B/2)-.125"=39 3/8"; (D-J-K-L)*2=2 3/4"; (E/2)-((B/2)+1.5")=35 3/16"; (E/2)-((MB_P/2)+.125")=31 1/16"; (E/2)-(E/52*15)=32 7/32"; (F-((F-H)/2))/2=39 27/32"; (M - (2 * (D - L - K - J)))/2=28 1/4"; (MB_P/2)+.125"=45 1/8"; (MB_P/2-.125")+((F / 2) - 2")=-84 23/32"; (MB_P/2-.125")-((F / 2) - 2")=-5 1/32"; (MB_Q/2)+.125"=45 1/8"; (NOZZLE_HEIGHT - (NOZZLE_HEIGHT / 8 * 2)) / 2=35 5/8"; (NOZZLE_WB_OD - NOZZLE_TOP_OD) / 4=8"; -((MB_Q / 2) + 1/8")=-45 1/8"; -(F-((F-H)/2))/2=-39 27/32"; -MB_HEIGHT=-104"; -MB_P=-90"; -MB_P-.25=-90 1/4"; A=286 3/8"; A/2=143 3/16"; B=79"; B/2=39 1/2"; B/4=19 3/4"; C=176 3/8"; C/2=88 3/16"; CLASS=2"; D=117"; D-L-K-J=1 3/8"; D-M=57 3/4"; DUAL_Q=270 3/8"; DUAL_Q+.25"=270 5/8"; E=152 3/8"; E-(NOZZLE_RAD/3*2)=58 15/16"; E-N-N-H=2"; E/2=76 3/16"; E/2-H/2=35 11/32"; E/52*15=43 31/32"; E/52*30=87 29/32"; F=83 11/16"; F/2=41 27/32"; H=81 11/16"; H/2=40 27/32"; HEIGHT=138 17/32"; J=15 1/2"; J+K+L=115 5/8"; K=38 5/8"; L=61 1/2"; M=59 1/4"; M-(2*(D-L-K-J))=56 1/2"; MB_A=270 7/16"; MB_F=27 3/4"; MB_F-3"=24 3/4"; MB_HEIGHT=104"; MB_HEIGHT/2=52"; MB_N=13 5/8"; MB_N-(D-J-K-L)=12 1/4"; MB_P=90"; MB_P+.25"=90 1/4"; MB_P+MB_P+.5=180 1/2"; MB_P-4.5"=85 1/2"; MB_Q=90"; N=33 11/32"; N+(H/2)=74 3/16"; NOZZLE_BOTTOM_ID=51 3/4"; NOZZLE_BOTTOM_RAD=25 7/8"; NOZZLE_BOTTOM_RAD-3*2=19 7/8"; NOZZLE_HEIGHT=95"; NOZZLE_HEIGHT/7*2=23 3/4"; NOZZLE_SIZE=36"; NOZZLE_TOP_OD=58"; NOZZLE_TOP_RAD=29"; NOZZLE_WB/4=18"; NOZZLE_WB_OD=90"; NOZZLE_WB_RAD=45"; NOZZLE_WB_RAD-2"=43"; P=29 1/2"; R=72"; R*1.1=79 3/16"; R+((B/2)+1.5")=113"; R-((B/2)+1.5")=31"; RO/2=42 3/4"; RO2/2=223 1/8"; TRANSITION=36 19/32"; TRANSITION/2=18 9/32"; TRIP_Q=450 3/4"; TRIP_Q-4.5"=446 1/4"; Type Comments=Triple Vari-Plume Laboratory Exhaust Centrifugal Airfoil Class 2 Arr 10 With Mixing Box
- Triple_730_CAVP-49H_CLASS_2_With_Mixing_Box: ((M - (2 * (D - L - K - J))) / 2) + (TRANSITION / 2)=52 25/32"; (B/2)+1.5"=41"; (B/2)-.125"=39 3/8"; (D-J-K-L)*2=2 3/4"; (E/2)-((B/2)+1.5")=35 3/16"; (E/2)-((MB_P/2)+.125")=31 1/16"; (E/2)-(E/52*15)=32 7/32"; (F-((F-H)/2))/2=39 27/32"; (M - (2 * (D - L - K - J)))/2=28 1/4"; (MB_P/2)+.125"=45 1/8"; (MB_P/2-.125")+((F / 2) - 2")=-84 23/32"; (MB_P/2-.125")-((F / 2) - 2")=-5 1/32"; (MB_Q/2)+.125"=45 1/8"; (NOZZLE_HEIGHT - (NOZZLE_HEIGHT / 8 * 2)) / 2=41 1/4"; (NOZZLE_WB_OD - NOZZLE_TOP_OD) / 4=6 1/4"; -((MB_Q / 2) + 1/8")=-45 1/8"; -(F-((F-H)/2))/2=-39 27/32"; -MB_HEIGHT=-104"; -MB_P=-90"; -MB_P-.25=-90 1/4"; A=286 3/8"; A/2=143 3/16"; B=79"; B/2=39 1/2"; B/4=19 3/4"; C=176 3/8"; C/2=88 3/16"; CLASS=2"; D=117"; D-L-K-J=1 3/8"; D-M=57 3/4"; DUAL_Q=270 3/8"; DUAL_Q+.25"=270 5/8"; E=152 3/8"; E-(NOZZLE_RAD/3*2)=53 1/16"; E-N-N-H=2"; E/2=76 3/16"; E/2-H/2=35 11/32"; E/52*15=43 31/32"; E/52*30=87 29/32"; F=83 11/16"; F/2=41 27/32"; H=81 11/16"; H/2=40 27/32"; HEIGHT=138 17/32"; J=15 1/2"; J+K+L=115 5/8"; K=38 5/8"; L=61 1/2"; M=59 1/4"; M-(2*(D-L-K-J))=56 1/2"; MB_A=270 7/16"; MB_F=27 3/4"; MB_F-3"=24 3/4"; MB_HEIGHT=104"; MB_HEIGHT/2=52"; MB_N=13 5/8"; MB_N-(D-J-K-L)=12 1/4"; MB_P=90"; MB_P+.25"=90 1/4"; MB_P+MB_P+.5=180 1/2"; MB_P-4.5"=85 1/2"; MB_Q=90"; N=33 11/32"; N+(H/2)=74 3/16"; NOZZLE_BOTTOM_ID=69 3/8"; NOZZLE_BOTTOM_RAD=34 11/16"; NOZZLE_BOTTOM_RAD-3*2=28 11/16"; NOZZLE_HEIGHT=110"; NOZZLE_HEIGHT/7*2=27 1/2"; NOZZLE_SIZE=49"; NOZZLE_TOP_OD=76"; NOZZLE_TOP_RAD=38"; NOZZLE_WB/4=20 3/16"; NOZZLE_WB_OD=101"; NOZZLE_WB_RAD=50 1/2"; NOZZLE_WB_RAD-2"=48 1/2"; P=29 1/2"; R=72"; R*1.1=79 3/16"; R+((B/2)+1.5")=113"; R-((B/2)+1.5")=31"; RO/2=42 3/4"; RO2/2=223 1/8"; TRANSITION=49 1/16"; TRANSITION/2=24 17/32"; TRIP_Q=450 3/4"; TRIP_Q-4.5"=446 1/4"; Type Comments=Triple Vari-Plume Laboratory Exhaust Centrifugal Airfoil Class 2 Arr 10 With Mixing Box
- Triple_730_CAVP-49L_CLASS_2_With_Mixing_Box: ((M - (2 * (D - L - K - J))) / 2) + (TRANSITION / 2)=52 25/32"; (B/2)+1.5"=41"; (B/2)-.125"=39 3/8"; (D-J-K-L)*2=2 3/4"; (E/2)-((B/2)+1.5")=35 3/16"; (E/2)-((MB_P/2)+.125")=31 1/16"; (E/2)-(E/52*15)=32 7/32"; (F-((F-H)/2))/2=39 27/32"; (M - (2 * (D - L - K - J)))/2=28 1/4"; (MB_P/2)+.125"=45 1/8"; (MB_P/2-.125")+((F / 2) - 2")=-84 23/32"; (MB_P/2-.125")-((F / 2) - 2")=-5 1/32"; (MB_Q/2)+.125"=45 1/8"; (NOZZLE_HEIGHT - (NOZZLE_HEIGHT / 8 * 2)) / 2=41 1/4"; (NOZZLE_WB_OD - NOZZLE_TOP_OD) / 4=6 1/4"; -((MB_Q / 2) + 1/8")=-45 1/8"; -(F-((F-H)/2))/2=-39 27/32"; -MB_HEIGHT=-104"; -MB_P=-90"; -MB_P-.25=-90 1/4"; A=286 3/8"; A/2=143 3/16"; B=79"; B/2=39 1/2"; B/4=19 3/4"; C=176 3/8"; C/2=88 3/16"; CLASS=2"; D=117"; D-L-K-J=1 3/8"; D-M=57 3/4"; DUAL_Q=270 3/8"; DUAL_Q+.25"=270 5/8"; E=152 3/8"; E-(NOZZLE_RAD/3*2)=53 1/16"; E-N-N-H=2"; E/2=76 3/16"; E/2-H/2=35 11/32"; E/52*15=43 31/32"; E/52*30=87 29/32"; F=83 11/16"; F/2=41 27/32"; H=81 11/16"; H/2=40 27/32"; HEIGHT=138 17/32"; J=15 1/2"; J+K+L=115 5/8"; K=38 5/8"; L=61 1/2"; M=59 1/4"; M-(2*(D-L-K-J))=56 1/2"; MB_A=270 7/16"; MB_F=27 3/4"; MB_F-3"=24 3/4"; MB_HEIGHT=104"; MB_HEIGHT/2=52"; MB_N=13 5/8"; MB_N-(D-J-K-L)=12 1/4"; MB_P=90"; MB_P+.25"=90 1/4"; MB_P+MB_P+.5=180 1/2"; MB_P-4.5"=85 1/2"; MB_Q=90"; N=33 11/32"; N+(H/2)=74 3/16"; NOZZLE_BOTTOM_ID=69 3/8"; NOZZLE_BOTTOM_RAD=34 11/16"; NOZZLE_BOTTOM_RAD-3*2=28 11/16"; NOZZLE_HEIGHT=110"; NOZZLE_HEIGHT/7*2=27 1/2"; NOZZLE_SIZE=49"; NOZZLE_TOP_OD=76"; NOZZLE_TOP_RAD=38"; NOZZLE_WB/4=20 3/16"; NOZZLE_WB_OD=101"; NOZZLE_WB_RAD=50 1/2"; NOZZLE_WB_RAD-2"=48 1/2"; P=29 1/2"; R=72"; R*1.1=79 3/16"; R+((B/2)+1.5")=113"; R-((B/2)+1.5")=31"; RO/2=42 3/4"; RO2/2=223 1/8"; TRANSITION=49 1/16"; TRANSITION/2=24 17/32"; TRIP_Q=450 3/4"; TRIP_Q-4.5"=446 1/4"; Type Comments=Triple Vari-Plume Laboratory Exhaust Centrifugal Airfoil Class 2 Arr 10 With Mixing Box
- Triple_225_CAVP-15H_CLASS_1_With_Mixing_Box: ((M - (2 * (D - L - K - J))) / 2) + (TRANSITION / 2)=16 9/32"; (B/2)+1.5"=15 7/32"; (B/2)-.125"=13 19/32"; (D-J-K-L)*2=2"; (E/2)-((B/2)+1.5")=8 15/16"; (E/2)-((MB_P/2)+.125")=5 1/32"; (E/2)-(E/52*15)=10 7/32"; (F-((F-H)/2))/2=12 13/16"; (M - (2 * (D - L - K - J)))/2=8 23/32"; (MB_P/2)+.125"=19 1/8"; (MB_P/2-.125")+((F / 2) - 2")=-31 11/16"; (MB_P/2-.125")-((F / 2) - 2")=-6 1/16"; (MB_Q/2)+.125"=19 1/8"; (NOZZLE_HEIGHT - (NOZZLE_HEIGHT / 8 * 2)) / 2=16 1/8"; (NOZZLE_WB_OD - NOZZLE_TOP_OD) / 4=3 1/4"; -((MB_Q / 2) + 1/8")=-19 1/8"; -(F-((F-H)/2))/2=-12 13/16"; -MB_HEIGHT=-43 1/4"; -MB_P=-38"; -MB_P-.25=-38 1/4"; A=106 11/16"; A/2=53 11/32"; B=27 7/16"; B/2=13 23/32"; B/4=6 7/8"; C=59 3/16"; C/2=29 19/32"; CLASS=1"; D=46 1/16"; D-L-K-J=1"; D-M=26 5/8"; DUAL_Q=114 3/8"; DUAL_Q+.25"=114 5/8"; E=48 5/16"; E-(NOZZLE_RAD/3*2)=17 1/32"; E-N-N-H=2"; E/2=24 5/32"; E/2-H/2=10 11/32"; E/52*15=13 15/16"; E/52*30=27 7/8"; F=29 5/8"; F/2=14 13/16"; H=27 5/8"; H/2=13 13/16"; HEIGHT=45 11/32"; J=8 1/2"; J+K+L=45 1/16"; K=15 1/8"; L=21 7/16"; M=19 7/16"; M-(2*(D-L-K-J))=17 7/16"; MB_A=117 5/8"; MB_F=5 3/4"; MB_F-3"=2 3/4"; MB_HEIGHT=43 1/4"; MB_HEIGHT/2=21 5/8"; MB_N=14 3/16"; MB_N-(D-J-K-L)=13 3/16"; MB_P=38"; MB_P+.25"=38 1/4"; MB_P+MB_P+.5=76 1/2"; MB_P-4.5"=33 1/2"; MB_Q=38"; N=8 11/32"; N+(H/2)=22 5/32"; NOZZLE_BOTTOM_ID=21 3/8"; NOZZLE_BOTTOM_RAD=10 11/16"; NOZZLE_BOTTOM_RAD-3*2=4 11/16"; NOZZLE_HEIGHT=43"; NOZZLE_HEIGHT/7*2=10 3/4"; NOZZLE_SIZE=15"; NOZZLE_TOP_OD=23"; NOZZLE_TOP_RAD=11 1/2"; NOZZLE_WB/4=7 3/16"; NOZZLE_WB_OD=36"; NOZZLE_WB_RAD=18"; NOZZLE_WB_RAD-2"=16"; P=60"; R=24 1/4"; R*1.1=26 11/16"; R+((B/2)+1.5")=39 15/32"; R-((B/2)+1.5")=9 1/32"; RO/2=16 3/4"; RO2/2=93 1/8"; TRANSITION=15 1/8"; TRANSITION/2=7 9/16"; TRIP_Q=190 3/4"; TRIP_Q-4.5"=186 1/4"; Type Comments=Triple Vari-Plume Laboratory Exhaust Centrifugal Airfoil Class 1 Arr 10 With Mixing Box
- Triple_270_CAVP-21H_CLASS_1_With_Mixing_Box: ((M - (2 * (D - L - K - J))) / 2) + (TRANSITION / 2)=20 19/32"; (B/2)+1.5"=17 15/32"; (B/2)-.125"=15 27/32"; (D-J-K-L)*2=2"; (E/2)-((B/2)+1.5")=11 5/16"; (E/2)-((MB_P/2)+.125")=7 5/32"; (E/2)-(E/52*15)=12 3/16"; (F-((F-H)/2))/2=15 3/16"; (M - (2 * (D - L - K - J)))/2=10 7/16"; (MB_P/2)+.125"=21 5/8"; (MB_P/2-.125")+((F / 2) - 2")=-36 9/16"; (MB_P/2-.125")-((F / 2) - 2")=-6 3/16"; (MB_Q/2)+.125"=21 5/8"; (NOZZLE_HEIGHT - (NOZZLE_HEIGHT / 8 * 2)) / 2=19 25/32"; (NOZZLE_WB_OD - NOZZLE_TOP_OD) / 4=4 9/16"; -((MB_Q / 2) + 1/8")=-21 5/8"; -(F-((F-H)/2))/2=-15 3/16"; -MB_HEIGHT=-47 3/4"; -MB_P=-43"; -MB_P-.25=-43 1/4"; A=116 7/16"; A/2=58 7/32"; B=31 15/16"; B/2=15 31/32"; B/4=8"; C=68 15/16"; C/2=34 15/32"; CLASS=1"; D=54 1/2"; D-L-K-J=1"; D-M=31 5/8"; DUAL_Q=129 3/8"; DUAL_Q+.25"=129 5/8"; E=57 9/16"; E-(NOZZLE_RAD/3*2)=19 3/16"; E-N-N-H=2"; E/2=28 25/32"; E/2-H/2=12 19/32"; E/52*15=16 19/32"; E/52*30=33 7/32"; F=34 3/8"; F/2=17 3/16"; H=32 3/8"; H/2=16 3/16"; HEIGHT=52 1/8"; J=9 1/2"; J+K+L=53 1/2"; K=19 1/8"; L=24 7/8"; M=22 7/8"; M-(2*(D-L-K-J))=20 7/8"; MB_A=132 7/16"; MB_F=6 1/4"; MB_F-3"=3 1/4"; MB_HEIGHT=47 3/4"; MB_HEIGHT/2=23 7/8"; MB_N=14 3/16"; MB_N-(D-J-K-L)=13 3/16"; MB_P=43"; MB_P+.25"=43 1/4"; MB_P+MB_P+.5=86 1/2"; MB_P-4.5"=38 1/2"; MB_Q=43"; N=10 19/32"; N+(H/2)=26 25/32"; NOZZLE_BOTTOM_ID=28 3/4"; NOZZLE_BOTTOM_RAD=14 3/8"; NOZZLE_BOTTOM_RAD-3*2=8 3/8"; NOZZLE_HEIGHT=52 3/4"; NOZZLE_HEIGHT/7*2=13 3/16"; NOZZLE_SIZE=21"; NOZZLE_TOP_OD=30 3/4"; NOZZLE_TOP_RAD=15 3/8"; NOZZLE_WB/4=9 13/16"; NOZZLE_WB_OD=49"; NOZZLE_WB_RAD=24 1/2"; NOZZLE_WB_RAD-2"=22 1/2"; P=60"; R=27"; R*1.1=29 11/16"; R+((B/2)+1.5")=44 15/32"; R-((B/2)+1.5")=9 17/32"; RO/2=19 1/4"; RO2/2=105 5/8"; TRANSITION=20 11/32"; TRANSITION/2=10 5/32"; TRIP_Q=215 3/4"; TRIP_Q-4.5"=211 1/4"; Type Comments=Triple Vari-Plume Laboratory Exhaust Centrifugal Airfoil Class 1 Arr 10 With Mixing Box
- Triple_270_CAVP-21L_CLASS_1_With_Mixing_Box: ((M - (2 * (D - L - K - J))) / 2) + (TRANSITION / 2)=20 19/32"; (B/2)+1.5"=17 15/32"; (B/2)-.125"=15 27/32"; (D-J-K-L)*2=2"; (E/2)-((B/2)+1.5")=11 5/16"; (E/2)-((MB_P/2)+.125")=7 5/32"; (E/2)-(E/52*15)=12 3/16"; (F-((F-H)/2))/2=15 3/16"; (M - (2 * (D - L - K - J)))/2=10 7/16"; (MB_P/2)+.125"=21 5/8"; (MB_P/2-.125")+((F / 2) - 2")=-36 9/16"; (MB_P/2-.125")-((F / 2) - 2")=-6 3/16"; (MB_Q/2)+.125"=21 5/8"; (NOZZLE_HEIGHT - (NOZZLE_HEIGHT / 8 * 2)) / 2=19 25/32"; (NOZZLE_WB_OD - NOZZLE_TOP_OD) / 4=4 9/16"; -((MB_Q / 2) + 1/8")=-21 5/8"; -(F-((F-H)/2))/2=-15 3/16"; -MB_HEIGHT=-47 3/4"; -MB_P=-43"; -MB_P-.25=-43 1/4"; A=116 7/16"; A/2=58 7/32"; B=31 15/16"; B/2=15 31/32"; B/4=8"; C=68 15/16"; C/2=34 15/32"; CLASS=1"; D=54 1/2"; D-L-K-J=1"; D-M=31 5/8"; DUAL_Q=129 3/8"; DUAL_Q+.25"=129 5/8"; E=57 9/16"; E-(NOZZLE_RAD/3*2)=19 3/16"; E-N-N-H=2"; E/2=28 25/32"; E/2-H/2=12 19/32"; E/52*15=16 19/32"; E/52*30=33 7/32"; F=34 3/8"; F/2=17 3/16"; H=32 3/8"; H/2=16 3/16"; HEIGHT=52 1/8"; J=9 1/2"; J+K+L=53 1/2"; K=19 1/8"; L=24 7/8"; M=22 7/8"; M-(2*(D-L-K-J))=20 7/8"; MB_A=132 7/16"; MB_F=6 1/4"; MB_F-3"=3 1/4"; MB_HEIGHT=47 3/4"; MB_HEIGHT/2=23 7/8"; MB_N=14 3/16"; MB_N-(D-J-K-L)=13 3/16"; MB_P=43"; MB_P+.25"=43 1/4"; MB_P+MB_P+.5=86 1/2"; MB_P-4.5"=38 1/2"; MB_Q=43"; N=10 19/32"; N+(H/2)=26 25/32"; NOZZLE_BOTTOM_ID=28 3/4"; NOZZLE_BOTTOM_RAD=14 3/8"; NOZZLE_BOTTOM_RAD-3*2=8 3/8"; NOZZLE_HEIGHT=52 3/4"; NOZZLE_HEIGHT/7*2=13 3/16"; NOZZLE_SIZE=21"; NOZZLE_TOP_OD=30 3/4"; NOZZLE_TOP_RAD=15 3/8"; NOZZLE_WB/4=9 13/16"; NOZZLE_WB_OD=49"; NOZZLE_WB_RAD=24 1/2"; NOZZLE_WB_RAD-2"=22 1/2"; P=60"; R=27"; R*1.1=29 11/16"; R+((B/2)+1.5")=44 15/32"; R-((B/2)+1.5")=9 17/32"; RO/2=19 1/4"; RO2/2=105 5/8"; TRANSITION=20 11/32"; TRANSITION/2=10 5/32"; TRIP_Q=215 3/4"; TRIP_Q-4.5"=211 1/4"; Type Comments=Triple Vari-Plume Laboratory Exhaust Centrifugal Airfoil Class 1 Arr 10 With Mixing Box
- Triple_270_CAVP-21H_CLASS_2_With_Mixing_Box: ((M - (2 * (D - L - K - J))) / 2) + (TRANSITION / 2)=20 19/32"; (B/2)+1.5"=17 15/32"; (B/2)-.125"=15 27/32"; (D-J-K-L)*2=2"; (E/2)-((B/2)+1.5")=11 5/16"; (E/2)-((MB_P/2)+.125")=7 5/32"; (E/2)-(E/52*15)=12 3/16"; (F-((F-H)/2))/2=15 3/16"; (M - (2 * (D - L - K - J)))/2=10 7/16"; (MB_P/2)+.125"=21 5/8"; (MB_P/2-.125")+((F / 2) - 2")=-36 9/16"; (MB_P/2-.125")-((F / 2) - 2")=-6 3/16"; (MB_Q/2)+.125"=21 5/8"; (NOZZLE_HEIGHT - (NOZZLE_HEIGHT / 8 * 2)) / 2=19 25/32"; (NOZZLE_WB_OD - NOZZLE_TOP_OD) / 4=4 9/16"; -((MB_Q / 2) + 1/8")=-21 5/8"; -(F-((F-H)/2))/2=-15 3/16"; -MB_HEIGHT=-47 3/4"; -MB_P=-43"; -MB_P-.25=-43 1/4"; A=116 7/16"; A/2=58 7/32"; B=31 15/16"; B/2=15 31/32"; B/4=8"; C=68 15/16"; C/2=34 15/32"; CLASS=2"; D=56 1/2"; D-L-K-J=1"; D-M=33 5/8"; DUAL_Q=129 3/8"; DUAL_Q+.25"=129 5/8"; E=57 9/16"; E-(NOZZLE_RAD/3*2)=19 3/16"; E-N-N-H=2 19/32"; E/2=28 25/32"; E/2-H/2=12 19/32"; E/52*15=16 19/32"; E/52*30=33 7/32"; F=34 3/8"; F/2=17 3/16"; H=32 3/8"; H/2=16 3/16"; HEIGHT=52 1/8"; J=9 1/4"; J+K+L=55 1/2"; K=21 3/8"; L=24 7/8"; M=22 7/8"; M-(2*(D-L-K-J))=20 7/8"; MB_A=134 7/16"; MB_F=6 1/4"; MB_F-3"=3 1/4"; MB_HEIGHT=47 3/4"; MB_HEIGHT/2=23 7/8"; MB_N=14 3/16"; MB_N-(D-J-K-L)=13 3/16"; MB_P=43"; MB_P+.25"=43 1/4"; MB_P+MB_P+.5=86 1/2"; MB_P-4.5"=38 1/2"; MB_Q=43"; N=10"; N+(H/2)=26 3/16"; NOZZLE_BOTTOM_ID=28 3/4"; NOZZLE_BOTTOM_RAD=14 3/8"; NOZZLE_BOTTOM_RAD-3*2=8 3/8"; NOZZLE_HEIGHT=52 3/4"; NOZZLE_HEIGHT/7*2=13 3/16"; NOZZLE_SIZE=21"; NOZZLE_TOP_OD=30 3/4"; NOZZLE_TOP_RAD=15 3/8"; NOZZLE_WB/4=9 13/16"; NOZZLE_WB_OD=49"; NOZZLE_WB_RAD=24 1/2"; NOZZLE_WB_RAD-2"=22 1/2"; P=60"; R=27"; R*1.1=29 11/16"; R+((B/2)+1.5")=44 15/32"; R-((B/2)+1.5")=9 17/32"; RO/2=19 1/4"; RO2/2=105 5/8"; TRANSITION=20 11/32"; TRANSITION/2=10 5/32"; TRIP_Q=215 3/4"; TRIP_Q-4.5"=211 1/4"; Type Comments=Triple Vari-Plume Laboratory Exhaust Centrifugal Airfoil Class 2 Arr 10 With Mixing Box
- Triple_270_CAVP-21L_CLASS_2_With_Mixing_Box: ((M - (2 * (D - L - K - J))) / 2) + (TRANSITION / 2)=20 19/32"; (B/2)+1.5"=17 15/32"; (B/2)-.125"=15 27/32"; (D-J-K-L)*2=2"; (E/2)-((B/2)+1.5")=11 5/16"; (E/2)-((MB_P/2)+.125")=7 5/32"; (E/2)-(E/52*15)=12 3/16"; (F-((F-H)/2))/2=15 3/16"; (M - (2 * (D - L - K - J)))/2=10 7/16"; (MB_P/2)+.125"=21 5/8"; (MB_P/2-.125")+((F / 2) - 2")=-36 9/16"; (MB_P/2-.125")-((F / 2) - 2")=-6 3/16"; (MB_Q/2)+.125"=21 5/8"; (NOZZLE_HEIGHT - (NOZZLE_HEIGHT / 8 * 2)) / 2=19 25/32"; (NOZZLE_WB_OD - NOZZLE_TOP_OD) / 4=4 9/16"; -((MB_Q / 2) + 1/8")=-21 5/8"; -(F-((F-H)/2))/2=-15 3/16"; -MB_HEIGHT=-47 3/4"; -MB_P=-43"; -MB_P-.25=-43 1/4"; A=116 7/16"; A/2=58 7/32"; B=31 15/16"; B/2=15 31/32"; B/4=8"; C=68 15/16"; C/2=34 15/32"; CLASS=2"; D=56 1/2"; D-L-K-J=1"; D-M=33 5/8"; DUAL_Q=129 3/8"; DUAL_Q+.25"=129 5/8"; E=57 9/16"; E-(NOZZLE_RAD/3*2)=19 3/16"; E-N-N-H=2 19/32"; E/2=28 25/32"; E/2-H/2=12 19/32"; E/52*15=16 19/32"; E/52*30=33 7/32"; F=34 3/8"; F/2=17 3/16"; H=32 3/8"; H/2=16 3/16"; HEIGHT=52 1/8"; J=9 1/4"; J+K+L=55 1/2"; K=21 3/8"; L=24 7/8"; M=22 7/8"; M-(2*(D-L-K-J))=20 7/8"; MB_A=134 7/16"; MB_F=6 1/4"; MB_F-3"=3 1/4"; MB_HEIGHT=47 3/4"; MB_HEIGHT/2=23 7/8"; MB_N=14 3/16"; MB_N-(D-J-K-L)=13 3/16"; MB_P=43"; MB_P+.25"=43 1/4"; MB_P+MB_P+.5=86 1/2"; MB_P-4.5"=38 1/2"; MB_Q=43"; N=10"; N+(H/2)=26 3/16"; NOZZLE_BOTTOM_ID=28 3/4"; NOZZLE_BOTTOM_RAD=14 3/8"; NOZZLE_BOTTOM_RAD-3*2=8 3/8"; NOZZLE_HEIGHT=52 3/4"; NOZZLE_HEIGHT/7*2=13 3/16"; NOZZLE_SIZE=21"; NOZZLE_TOP_OD=30 3/4"; NOZZLE_TOP_RAD=15 3/8"; NOZZLE_WB/4=9 13/16"; NOZZLE_WB_OD=49"; NOZZLE_WB_RAD=24 1/2"; NOZZLE_WB_RAD-2"=22 1/2"; P=60"; R=27"; R*1.1=29 11/16"; R+((B/2)+1.5")=44 15/32"; R-((B/2)+1.5")=9 17/32"; RO/2=19 1/4"; RO2/2=105 5/8"; TRANSITION=20 11/32"; TRANSITION/2=10 5/32"; TRIP_Q=215 3/4"; TRIP_Q-4.5"=211 1/4"; Type Comments=Triple Vari-Plume Laboratory Exhaust Centrifugal Airfoil Class 2 Arr 10 With Mixing Box
- Triple_300_CAVP-21H_CLASS_1_With_Mixing_Box: ((M - (2 * (D - L - K - J))) / 2) + (TRANSITION / 2)=21 3/4"; (B/2)+1.5"=18 31/32"; (B/2)-.125"=17 11/32"; (D-J-K-L)*2=2"; (E/2)-((B/2)+1.5")=12 29/32"; (E/2)-((MB_P/2)+.125")=8 3/4"; (E/2)-(E/52*15)=13 1/2"; (F-((F-H)/2))/2=16 11/16"; (M - (2 * (D - L - K - J)))/2=11 19/32"; (MB_P/2)+.125"=23 1/8"; (MB_P/2-.125")+((F / 2) - 2")=-39 9/16"; (MB_P/2-.125")-((F / 2) - 2")=-6 3/16"; (MB_Q/2)+.125"=23 1/8"; (NOZZLE_HEIGHT - (NOZZLE_HEIGHT / 8 * 2)) / 2=19 25/32"; (NOZZLE_WB_OD - NOZZLE_TOP_OD) / 4=4 9/16"; -((MB_Q / 2) + 1/8")=-23 1/8"; -(F-((F-H)/2))/2=-16 11/16"; -MB_HEIGHT=-50 3/4"; -MB_P=-46"; -MB_P-.25=-46 1/4"; A=122 7/16"; A/2=61 7/32"; B=34 15/16"; B/2=17 15/32"; B/4=8 3/4"; C=74 15/16"; C/2=37 15/32"; CLASS=1"; D=57 5/16"; D-L-K-J=1"; D-M=32 1/8"; DUAL_Q=138 3/8"; DUAL_Q+.25"=138 5/8"; E=63 3/4"; E-(NOZZLE_RAD/3*2)=22 9/32"; E-N-N-H=2"; E/2=31 7/8"; E/2-H/2=14 3/16"; E/52*15=18 3/8"; E/52*30=36 25/32"; F=37 3/8"; F/2=18 11/16"; H=35 3/8"; H/2=17 11/16"; HEIGHT=57 27/32"; J=10"; J+K+L=56 5/16"; K=19 1/8"; L=27 3/16"; M=25 3/16"; M-(2*(D-L-K-J))=23 3/16"; MB_A=140 1/8"; MB_F=7 3/4"; MB_F-3"=4 3/4"; MB_HEIGHT=50 3/4"; MB_HEIGHT/2=25 3/8"; MB_N=14 3/16"; MB_N-(D-J-K-L)=13 3/16"; MB_P=46"; MB_P+.25"=46 1/4"; MB_P+MB_P+.5=92 1/2"; MB_P-4.5"=41 1/2"; MB_Q=46"; N=12 3/16"; N+(H/2)=29 7/8"; NOZZLE_BOTTOM_ID=28 3/4"; NOZZLE_BOTTOM_RAD=14 3/8"; NOZZLE_BOTTOM_RAD-3*2=8 3/8"; NOZZLE_HEIGHT=52 3/4"; NOZZLE_HEIGHT/7*2=13 3/16"; NOZZLE_SIZE=21"; NOZZLE_TOP_OD=30 3/4"; NOZZLE_TOP_RAD=15 3/8"; NOZZLE_WB/4=9 13/16"; NOZZLE_WB_OD=49"; NOZZLE_WB_RAD=24 1/2"; NOZZLE_WB_RAD-2"=22 1/2"; P=60"; R=30"; R*1.1=33"; R+((B/2)+1.5")=48 31/32"; R-((B/2)+1.5")=11 1/32"; RO/2=20 3/4"; RO2/2=113 1/8"; TRANSITION=20 11/32"; TRANSITION/2=10 5/32"; TRIP_Q=230 3/4"; TRIP_Q-4.5"=226 1/4"; Type Comments=Triple Vari-Plume Laboratory Exhaust Centrifugal Airfoil Class 1 Arr 10 With Mixing Box
- Triple_300_CAVP-21L_CLASS_1_With_Mixing_Box: ((M - (2 * (D - L - K - J))) / 2) + (TRANSITION / 2)=21 3/4"; (B/2)+1.5"=18 31/32"; (B/2)-.125"=17 11/32"; (D-J-K-L)*2=2"; (E/2)-((B/2)+1.5")=12 29/32"; (E/2)-((MB_P/2)+.125")=8 3/4"; (E/2)-(E/52*15)=13 1/2"; (F-((F-H)/2))/2=16 11/16"; (M - (2 * (D - L - K - J)))/2=11 19/32"; (MB_P/2)+.125"=23 1/8"; (MB_P/2-.125")+((F / 2) - 2")=-39 9/16"; (MB_P/2-.125")-((F / 2) - 2")=-6 3/16"; (MB_Q/2)+.125"=23 1/8"; (NOZZLE_HEIGHT - (NOZZLE_HEIGHT / 8 * 2)) / 2=19 25/32"; (NOZZLE_WB_OD - NOZZLE_TOP_OD) / 4=4 9/16"; -((MB_Q / 2) + 1/8")=-23 1/8"; -(F-((F-H)/2))/2=-16 11/16"; -MB_HEIGHT=-50 3/4"; -MB_P=-46"; -MB_P-.25=-46 1/4"; A=122 7/16"; A/2=61 7/32"; B=34 15/16"; B/2=17 15/32"; B/4=8 3/4"; C=74 15/16"; C/2=37 15/32"; CLASS=1"; D=57 5/16"; D-L-K-J=1"; D-M=32 1/8"; DUAL_Q=138 3/8"; DUAL_Q+.25"=138 5/8"; E=63 3/4"; E-(NOZZLE_RAD/3*2)=22 9/32"; E-N-N-H=2"; E/2=31 7/8"; E/2-H/2=14 3/16"; E/52*15=18 3/8"; E/52*30=36 25/32"; F=37 3/8"; F/2=18 11/16"; H=35 3/8"; H/2=17 11/16"; HEIGHT=57 27/32"; J=10"; J+K+L=56 5/16"; K=19 1/8"; L=27 3/16"; M=25 3/16"; M-(2*(D-L-K-J))=23 3/16"; MB_A=140 1/8"; MB_F=7 3/4"; MB_F-3"=4 3/4"; MB_HEIGHT=50 3/4"; MB_HEIGHT/2=25 3/8"; MB_N=14 3/16"; MB_N-(D-J-K-L)=13 3/16"; MB_P=46"; MB_P+.25"=46 1/4"; MB_P+MB_P+.5=92 1/2"; MB_P-4.5"=41 1/2"; MB_Q=46"; N=12 3/16"; N+(H/2)=29 7/8"; NOZZLE_BOTTOM_ID=28 3/4"; NOZZLE_BOTTOM_RAD=14 3/8"; NOZZLE_BOTTOM_RAD-3*2=8 3/8"; NOZZLE_HEIGHT=52 3/4"; NOZZLE_HEIGHT/7*2=13 3/16"; NOZZLE_SIZE=21"; NOZZLE_TOP_OD=30 3/4"; NOZZLE_TOP_RAD=15 3/8"; NOZZLE_WB/4=9 13/16"; NOZZLE_WB_OD=49"; NOZZLE_WB_RAD=24 1/2"; NOZZLE_WB_RAD-2"=22 1/2"; P=60"; R=30"; R*1.1=33"; R+((B/2)+1.5")=48 31/32"; R-((B/2)+1.5")=11 1/32"; RO/2=20 3/4"; RO2/2=113 1/8"; TRANSITION=20 11/32"; TRANSITION/2=10 5/32"; TRIP_Q=230 3/4"; TRIP_Q-4.5"=226 1/4"; Type Comments=Triple Vari-Plume Laboratory Exhaust Centrifugal Airfoil Class 1 Arr 10 With Mixing Box
- Triple_300_CAVP-21H_CLASS_2_With_Mixing_Box: ((M - (2 * (D - L - K - J))) / 2) + (TRANSITION / 2)=21 3/4"; (B/2)+1.5"=18 31/32"; (B/2)-.125"=17 11/32"; (D-J-K-L)*2=2"; (E/2)-((B/2)+1.5")=12 29/32"; (E/2)-((MB_P/2)+.125")=8 3/4"; (E/2)-(E/52*15)=13 1/2"; (F-((F-H)/2))/2=16 11/16"; (M - (2 * (D - L - K - J)))/2=11 19/32"; (MB_P/2)+.125"=23 1/8"; (MB_P/2-.125")+((F / 2) - 2")=-39 9/16"; (MB_P/2-.125")-((F / 2) - 2")=-6 3/16"; (MB_Q/2)+.125"=23 1/8"; (NOZZLE_HEIGHT - (NOZZLE_HEIGHT / 8 * 2)) / 2=19 25/32"; (NOZZLE_WB_OD - NOZZLE_TOP_OD) / 4=4 9/16"; -((MB_Q / 2) + 1/8")=-23 1/8"; -(F-((F-H)/2))/2=-16 11/16"; -MB_HEIGHT=-50 3/4"; -MB_P=-46"; -MB_P-.25=-46 1/4"; A=122 7/16"; A/2=61 7/32"; B=34 15/16"; B/2=17 15/32"; B/4=8 3/4"; C=74 15/16"; C/2=37 15/32"; CLASS=2"; D=61 3/16"; D-L-K-J=1"; D-M=36"; DUAL_Q=138 3/8"; DUAL_Q+.25"=138 5/8"; E=63 3/4"; E-(NOZZLE_RAD/3*2)=22 9/32"; E-N-N-H=2"; E/2=31 7/8"; E/2-H/2=14 3/16"; E/52*15=18 3/8"; E/52*30=36 25/32"; F=37 3/8"; F/2=18 11/16"; H=35 3/8"; H/2=17 11/16"; HEIGHT=57 27/32"; J=10"; J+K+L=60 3/16"; K=23"; L=27 3/16"; M=25 3/16"; M-(2*(D-L-K-J))=23 3/16"; MB_A=144"; MB_F=7 3/4"; MB_F-3"=4 3/4"; MB_HEIGHT=50 3/4"; MB_HEIGHT/2=25 3/8"; MB_N=14 3/16"; MB_N-(D-J-K-L)=13 3/16"; MB_P=46"; MB_P+.25"=46 1/4"; MB_P+MB_P+.5=92 1/2"; MB_P-4.5"=41 1/2"; MB_Q=46"; N=12 3/16"; N+(H/2)=29 7/8"; NOZZLE_BOTTOM_ID=28 3/4"; NOZZLE_BOTTOM_RAD=14 3/8"; NOZZLE_BOTTOM_RAD-3*2=8 3/8"; NOZZLE_HEIGHT=52 3/4"; NOZZLE_HEIGHT/7*2=13 3/16"; NOZZLE_SIZE=21"; NOZZLE_TOP_OD=30 3/4"; NOZZLE_TOP_RAD=15 3/8"; NOZZLE_WB/4=9 13/16"; NOZZLE_WB_OD=49"; NOZZLE_WB_RAD=24 1/2"; NOZZLE_WB_RAD-2"=22 1/2"; P=18 1/4"; R=30"; R*1.1=33"; R+((B/2)+1.5")=48 31/32"; R-((B/2)+1.5")=11 1/32"; RO/2=20 3/4"; RO2/2=113 1/8"; TRANSITION=20 11/32"; TRANSITION/2=10 5/32"; TRIP_Q=230 3/4"; TRIP_Q-4.5"=226 1/4"; Type Comments=Triple Vari-Plume Laboratory Exhaust Centrifugal Airfoil Class 2 Arr 10 With Mixing Box
- Triple_300_CAVP-21L_CLASS_2_With_Mixing_Box: ((M - (2 * (D - L - K - J))) / 2) + (TRANSITION / 2)=21 3/4"; (B/2)+1.5"=18 31/32"; (B/2)-.125"=17 11/32"; (D-J-K-L)*2=2"; (E/2)-((B/2)+1.5")=12 29/32"; (E/2)-((MB_P/2)+.125")=8 3/4"; (E/2)-(E/52*15)=13 1/2"; (F-((F-H)/2))/2=16 11/16"; (M - (2 * (D - L - K - J)))/2=11 19/32"; (MB_P/2)+.125"=23 1/8"; (MB_P/2-.125")+((F / 2) - 2")=-39 9/16"; (MB_P/2-.125")-((F / 2) - 2")=-6 3/16"; (MB_Q/2)+.125"=23 1/8"; (NOZZLE_HEIGHT - (NOZZLE_HEIGHT / 8 * 2)) / 2=19 25/32"; (NOZZLE_WB_OD - NOZZLE_TOP_OD) / 4=4 9/16"; -((MB_Q / 2) + 1/8")=-23 1/8"; -(F-((F-H)/2))/2=-16 11/16"; -MB_HEIGHT=-50 3/4"; -MB_P=-46"; -MB_P-.25=-46 1/4"; A=122 7/16"; A/2=61 7/32"; B=34 15/16"; B/2=17 15/32"; B/4=8 3/4"; C=74 15/16"; C/2=37 15/32"; CLASS=2"; D=61 3/16"; D-L-K-J=1"; D-M=36"; DUAL_Q=138 3/8"; DUAL_Q+.25"=138 5/8"; E=63 3/4"; E-(NOZZLE_RAD/3*2)=22 9/32"; E-N-N-H=2"; E/2=31 7/8"; E/2-H/2=14 3/16"; E/52*15=18 3/8"; E/52*30=36 25/32"; F=37 3/8"; F/2=18 11/16"; H=35 3/8"; H/2=17 11/16"; HEIGHT=57 27/32"; J=10"; J+K+L=60 3/16"; K=23"; L=27 3/16"; M=25 3/16"; M-(2*(D-L-K-J))=23 3/16"; MB_A=144"; MB_F=7 3/4"; MB_F-3"=4 3/4"; MB_HEIGHT=50 3/4"; MB_HEIGHT/2=25 3/8"; MB_N=14 3/16"; MB_N-(D-J-K-L)=13 3/16"; MB_P=46"; MB_P+.25"=46 1/4"; MB_P+MB_P+.5=92 1/2"; MB_P-4.5"=41 1/2"; MB_Q=46"; N=12 3/16"; N+(H/2)=29 7/8"; NOZZLE_BOTTOM_ID=28 3/4"; NOZZLE_BOTTOM_RAD=14 3/8"; NOZZLE_BOTTOM_RAD-3*2=8 3/8"; NOZZLE_HEIGHT=52 3/4"; NOZZLE_HEIGHT/7*2=13 3/16"; NOZZLE_SIZE=21"; NOZZLE_TOP_OD=30 3/4"; NOZZLE_TOP_RAD=15 3/8"; NOZZLE_WB/4=9 13/16"; NOZZLE_WB_OD=49"; NOZZLE_WB_RAD=24 1/2"; NOZZLE_WB_RAD-2"=22 1/2"; P=18 1/4"; R=30"; R*1.1=33"; R+((B/2)+1.5")=48 31/32"; R-((B/2)+1.5")=11 1/32"; RO/2=20 3/4"; RO2/2=113 1/8"; TRANSITION=20 11/32"; TRANSITION/2=10 5/32"; TRIP_Q=230 3/4"; TRIP_Q-4.5"=226 1/4"; Type Comments=Triple Vari-Plume Laboratory Exhaust Centrifugal Airfoil Class 2 Arr 10 With Mixing Box
- Triple_330_CAVP-21H_CLASS_1_With_Mixing_Box: ((M - (2 * (D - L - K - J))) / 2) + (TRANSITION / 2)=22 29/32"; (B/2)+1.5"=20 15/32"; (B/2)-.125"=18 27/32"; (D-J-K-L)*2=2"; (E/2)-((B/2)+1.5")=14 1/2"; (E/2)-((MB_P/2)+.125")=10 11/32"; (E/2)-(E/52*15)=14 25/32"; (F-((F-H)/2))/2=18 3/16"; (M - (2 * (D - L - K - J)))/2=12 3/4"; (MB_P/2)+.125"=24 5/8"; (MB_P/2-.125")+((F / 2) - 2")=-42 9/16"; (MB_P/2-.125")-((F / 2) - 2")=-6 3/16"; (MB_Q/2)+.125"=24 5/8"; (NOZZLE_HEIGHT - (NOZZLE_HEIGHT / 8 * 2)) / 2=19 25/32"; (NOZZLE_WB_OD - NOZZLE_TOP_OD) / 4=4 9/16"; -((MB_Q / 2) + 1/8")=-24 5/8"; -(F-((F-H)/2))/2=-18 3/16"; -MB_HEIGHT=-53 3/4"; -MB_P=-49"; -MB_P-.25=-49 1/4"; A=144 7/16"; A/2=72 7/32"; B=37 15/16"; B/2=18 31/32"; B/4=9 1/2"; C=82 13/16"; C/2=41 13/32"; CLASS=1"; D=60 1/4"; D-L-K-J=1"; D-M=32 3/4"; DUAL_Q=147 3/8"; DUAL_Q+.25"=147 5/8"; E=69 15/16"; E-(NOZZLE_RAD/3*2)=25 3/8"; E-N-N-H=2"; E/2=34 31/32"; E/2-H/2=15 25/32"; E/52*15=20 3/16"; E/52*30=40 11/32"; F=40 3/8"; F/2=20 3/16"; H=38 3/8"; H/2=19 3/16"; HEIGHT=63 17/32"; J=10 1/2"; J+K+L=59 1/4"; K=19 1/4"; L=29 1/2"; M=27 1/2"; M-(2*(D-L-K-J))=25 1/2"; MB_A=148 1/16"; MB_F=9 1/4"; MB_F-3"=6 1/4"; MB_HEIGHT=53 3/4"; MB_HEIGHT/2=26 7/8"; MB_N=14 3/16"; MB_N-(D-J-K-L)=13 3/16"; MB_P=49"; MB_P+.25"=49 1/4"; MB_P+MB_P+.5=98 1/2"; MB_P-4.5"=44 1/2"; MB_Q=49"; N=13 25/32"; N+(H/2)=32 31/32"; NOZZLE_BOTTOM_ID=28 3/4"; NOZZLE_BOTTOM_RAD=14 3/8"; NOZZLE_BOTTOM_RAD-3*2=8 3/8"; NOZZLE_HEIGHT=52 3/4"; NOZZLE_HEIGHT/7*2=13 3/16"; NOZZLE_SIZE=21"; NOZZLE_TOP_OD=30 3/4"; NOZZLE_TOP_RAD=15 3/8"; NOZZLE_WB/4=9 13/16"; NOZZLE_WB_OD=49"; NOZZLE_WB_RAD=24 1/2"; NOZZLE_WB_RAD-2"=22 1/2"; P=60"; R=33"; R*1.1=36 5/16"; R+((B/2)+1.5")=53 15/32"; R-((B/2)+1.5")=12 17/32"; RO/2=22 1/4"; RO2/2=120 5/8"; TRANSITION=20 11/32"; TRANSITION/2=10 5/32"; TRIP_Q=245 3/4"; TRIP_Q-4.5"=241 1/4"; Type Comments=Triple Vari-Plume Laboratory Exhaust Centrifugal Airfoil Class 1 Arr 10 With Mixing Box
- Triple_330_CAVP-21L_CLASS_1_With_Mixing_Box: ((M - (2 * (D - L - K - J))) / 2) + (TRANSITION / 2)=22 29/32"; (B/2)+1.5"=20 15/32"; (B/2)-.125"=18 27/32"; (D-J-K-L)*2=2"; (E/2)-((B/2)+1.5")=14 1/2"; (E/2)-((MB_P/2)+.125")=10 11/32"; (E/2)-(E/52*15)=14 25/32"; (F-((F-H)/2))/2=18 3/16"; (M - (2 * (D - L - K - J)))/2=12 3/4"; (MB_P/2)+.125"=24 5/8"; (MB_P/2-.125")+((F / 2) - 2")=-42 9/16"; (MB_P/2-.125")-((F / 2) - 2")=-6 3/16"; (MB_Q/2)+.125"=24 5/8"; (NOZZLE_HEIGHT - (NOZZLE_HEIGHT / 8 * 2)) / 2=19 25/32"; (NOZZLE_WB_OD - NOZZLE_TOP_OD) / 4=4 9/16"; -((MB_Q / 2) + 1/8")=-24 5/8"; -(F-((F-H)/2))/2=-18 3/16"; -MB_HEIGHT=-53 3/4"; -MB_P=-49"; -MB_P-.25=-49 1/4"; A=144 7/16"; A/2=72 7/32"; B=37 15/16"; B/2=18 31/32"; B/4=9 1/2"; C=82 13/16"; C/2=41 13/32"; CLASS=1"; D=60 1/4"; D-L-K-J=1"; D-M=32 3/4"; DUAL_Q=147 3/8"; DUAL_Q+.25"=147 5/8"; E=69 15/16"; E-(NOZZLE_RAD/3*2)=25 3/8"; E-N-N-H=2"; E/2=34 31/32"; E/2-H/2=15 25/32"; E/52*15=20 3/16"; E/52*30=40 11/32"; F=40 3/8"; F/2=20 3/16"; H=38 3/8"; H/2=19 3/16"; HEIGHT=63 17/32"; J=10 1/2"; J+K+L=59 1/4"; K=19 1/4"; L=29 1/2"; M=27 1/2"; M-(2*(D-L-K-J))=25 1/2"; MB_A=148 1/16"; MB_F=9 1/4"; MB_F-3"=6 1/4"; MB_HEIGHT=53 3/4"; MB_HEIGHT/2=26 7/8"; MB_N=14 3/16"; MB_N-(D-J-K-L)=13 3/16"; MB_P=49"; MB_P+.25"=49 1/4"; MB_P+MB_P+.5=98 1/2"; MB_P-4.5"=44 1/2"; MB_Q=49"; N=13 25/32"; N+(H/2)=32 31/32"; NOZZLE_BOTTOM_ID=28 3/4"; NOZZLE_BOTTOM_RAD=14 3/8"; NOZZLE_BOTTOM_RAD-3*2=8 3/8"; NOZZLE_HEIGHT=52 3/4"; NOZZLE_HEIGHT/7*2=13 3/16"; NOZZLE_SIZE=21"; NOZZLE_TOP_OD=30 3/4"; NOZZLE_TOP_RAD=15 3/8"; NOZZLE_WB/4=9 13/16"; NOZZLE_WB_OD=49"; NOZZLE_WB_RAD=24 1/2"; NOZZLE_WB_RAD-2"=22 1/2"; P=60"; R=33"; R*1.1=36 5/16"; R+((B/2)+1.5")=53 15/32"; R-((B/2)+1.5")=12 17/32"; RO/2=22 1/4"; RO2/2=120 5/8"; TRANSITION=20 11/32"; TRANSITION/2=10 5/32"; TRIP_Q=245 3/4"; TRIP_Q-4.5"=241 1/4"; Type Comments=Triple Vari-Plume Laboratory Exhaust Centrifugal Airfoil Class 1 Arr 10 With Mixing Box
- Triple_330_CAVP-21H_CLASS_2_With_Mixing_Box: ((M - (2 * (D - L - K - J))) / 2) + (TRANSITION / 2)=22 29/32"; (B/2)+1.5"=20 15/32"; (B/2)-.125"=18 27/32"; (D-J-K-L)*2=2"; (E/2)-((B/2)+1.5")=14 1/2"; (E/2)-((MB_P/2)+.125")=10 11/32"; (E/2)-(E/52*15)=14 25/32"; (F-((F-H)/2))/2=18 3/16"; (M - (2 * (D - L - K - J)))/2=12 3/4"; (MB_P/2)+.125"=24 5/8"; (MB_P/2-.125")+((F / 2) - 2")=-42 9/16"; (MB_P/2-.125")-((F / 2) - 2")=-6 3/16"; (MB_Q/2)+.125"=24 5/8"; (NOZZLE_HEIGHT - (NOZZLE_HEIGHT / 8 * 2)) / 2=19 25/32"; (NOZZLE_WB_OD - NOZZLE_TOP_OD) / 4=4 9/16"; -((MB_Q / 2) + 1/8")=-24 5/8"; -(F-((F-H)/2))/2=-18 3/16"; -MB_HEIGHT=-53 3/4"; -MB_P=-49"; -MB_P-.25=-49 1/4"; A=144 7/16"; A/2=72 7/32"; B=37 15/16"; B/2=18 31/32"; B/4=9 1/2"; C=82 13/16"; C/2=41 13/32"; CLASS=2"; D=64"; D-L-K-J=1"; D-M=36 1/2"; DUAL_Q=147 3/8"; DUAL_Q+.25"=147 5/8"; E=69 15/16"; E-(NOZZLE_RAD/3*2)=25 3/8"; E-N-N-H=2"; E/2=34 31/32"; E/2-H/2=15 25/32"; E/52*15=20 3/16"; E/52*30=40 11/32"; F=40 3/8"; F/2=20 3/16"; H=38 3/8"; H/2=19 3/16"; HEIGHT=63 17/32"; J=10 1/2"; J+K+L=63"; K=23"; L=29 1/2"; M=27 1/2"; M-(2*(D-L-K-J))=25 1/2"; MB_A=151 13/16"; MB_F=9 1/4"; MB_F-3"=6 1/4"; MB_HEIGHT=53 3/4"; MB_HEIGHT/2=26 7/8"; MB_N=14 3/16"; MB_N-(D-J-K-L)=13 3/16"; MB_P=49"; MB_P+.25"=49 1/4"; MB_P+MB_P+.5=98 1/2"; MB_P-4.5"=44 1/2"; MB_Q=49"; N=13 25/32"; N+(H/2)=32 31/32"; NOZZLE_BOTTOM_ID=28 3/4"; NOZZLE_BOTTOM_RAD=14 3/8"; NOZZLE_BOTTOM_RAD-3*2=8 3/8"; NOZZLE_HEIGHT=52 3/4"; NOZZLE_HEIGHT/7*2=13 3/16"; NOZZLE_SIZE=21"; NOZZLE_TOP_OD=30 3/4"; NOZZLE_TOP_RAD=15 3/8"; NOZZLE_WB/4=9 13/16"; NOZZLE_WB_OD=49"; NOZZLE_WB_RAD=24 1/2"; NOZZLE_WB_RAD-2"=22 1/2"; P=60"; R=33"; R*1.1=36 5/16"; R+((B/2)+1.5")=53 15/32"; R-((B/2)+1.5")=12 17/32"; RO/2=22 1/4"; RO2/2=120 5/8"; TRANSITION=20 11/32"; TRANSITION/2=10 5/32"; TRIP_Q=245 3/4"; TRIP_Q-4.5"=241 1/4"; Type Comments=Triple Vari-Plume Laboratory Exhaust Centrifugal Airfoil Class 2 Arr 10 With Mixing Box
- Triple_330_CAVP-21L_CLASS_2_With_Mixing_Box: ((M - (2 * (D - L - K - J))) / 2) + (TRANSITION / 2)=22 29/32"; (B/2)+1.5"=20 15/32"; (B/2)-.125"=18 27/32"; (D-J-K-L)*2=2"; (E/2)-((B/2)+1.5")=14 1/2"; (E/2)-((MB_P/2)+.125")=10 11/32"; (E/2)-(E/52*15)=14 25/32"; (F-((F-H)/2))/2=18 3/16"; (M - (2 * (D - L - K - J)))/2=12 3/4"; (MB_P/2)+.125"=24 5/8"; (MB_P/2-.125")+((F / 2) - 2")=-42 9/16"; (MB_P/2-.125")-((F / 2) - 2")=-6 3/16"; (MB_Q/2)+.125"=24 5/8"; (NOZZLE_HEIGHT - (NOZZLE_HEIGHT / 8 * 2)) / 2=19 25/32"; (NOZZLE_WB_OD - NOZZLE_TOP_OD) / 4=4 9/16"; -((MB_Q / 2) + 1/8")=-24 5/8"; -(F-((F-H)/2))/2=-18 3/16"; -MB_HEIGHT=-53 3/4"; -MB_P=-49"; -MB_P-.25=-49 1/4"; A=144 7/16"; A/2=72 7/32"; B=37 15/16"; B/2=18 31/32"; B/4=9 1/2"; C=82 13/16"; C/2=41 13/32"; CLASS=2"; D=64"; D-L-K-J=1"; D-M=36 1/2"; DUAL_Q=147 3/8"; DUAL_Q+.25"=147 5/8"; E=69 15/16"; E-(NOZZLE_RAD/3*2)=25 3/8"; E-N-N-H=2"; E/2=34 31/32"; E/2-H/2=15 25/32"; E/52*15=20 3/16"; E/52*30=40 11/32"; F=40 3/8"; F/2=20 3/16"; H=38 3/8"; H/2=19 3/16"; HEIGHT=63 17/32"; J=10 1/2"; J+K+L=63"; K=23"; L=29 1/2"; M=27 1/2"; M-(2*(D-L-K-J))=25 1/2"; MB_A=151 13/16"; MB_F=9 1/4"; MB_F-3"=6 1/4"; MB_HEIGHT=53 3/4"; MB_HEIGHT/2=26 7/8"; MB_N=14 3/16"; MB_N-(D-J-K-L)=13 3/16"; MB_P=49"; MB_P+.25"=49 1/4"; MB_P+MB_P+.5=98 1/2"; MB_P-4.5"=44 1/2"; MB_Q=49"; N=13 25/32"; N+(H/2)=32 31/32"; NOZZLE_BOTTOM_ID=28 3/4"; NOZZLE_BOTTOM_RAD=14 3/8"; NOZZLE_BOTTOM_RAD-3*2=8 3/8"; NOZZLE_HEIGHT=52 3/4"; NOZZLE_HEIGHT/7*2=13 3/16"; NOZZLE_SIZE=21"; NOZZLE_TOP_OD=30 3/4"; NOZZLE_TOP_RAD=15 3/8"; NOZZLE_WB/4=9 13/16"; NOZZLE_WB_OD=49"; NOZZLE_WB_RAD=24 1/2"; NOZZLE_WB_RAD-2"=22 1/2"; P=60"; R=33"; R*1.1=36 5/16"; R+((B/2)+1.5")=53 15/32"; R-((B/2)+1.5")=12 17/32"; RO/2=22 1/4"; RO2/2=120 5/8"; TRANSITION=20 11/32"; TRANSITION/2=10 5/32"; TRIP_Q=245 3/4"; TRIP_Q-4.5"=241 1/4"; Type Comments=Triple Vari-Plume Laboratory Exhaust Centrifugal Airfoil Class 2 Arr 10 With Mixing Box
- Triple_365_CAVP-21H_CLASS_1_With_Mixing_Box: ((M - (2 * (D - L - K - J))) / 2) + (TRANSITION / 2)=24 7/32"; (B/2)+1.5"=22 23/32"; (B/2)-.125"=21 3/32"; (D-J-K-L)*2=2"; (E/2)-((B/2)+1.5")=15 15/16"; (E/2)-((MB_P/2)+.125")=12 17/32"; (E/2)-(E/52*15)=16 11/32"; (F-((F-H)/2))/2=20 7/16"; (M - (2 * (D - L - K - J)))/2=14 1/16"; (MB_P/2)+.125"=26 1/8"; (MB_P/2-.125")+((F / 2) - 2")=-46 5/16"; (MB_P/2-.125")-((F / 2) - 2")=-5 7/16"; (MB_Q/2)+.125"=26 1/8"; (NOZZLE_HEIGHT - (NOZZLE_HEIGHT / 8 * 2)) / 2=19 25/32"; (NOZZLE_WB_OD - NOZZLE_TOP_OD) / 4=4 9/16"; -((MB_Q / 2) + 1/8")=-26 1/8"; -(F-((F-H)/2))/2=-20 7/16"; -MB_HEIGHT=-58 1/4"; -MB_P=-52"; -MB_P-.25=-52 1/4"; A=153 13/16"; A/2=76 29/32"; B=42 7/16"; B/2=21 7/32"; B/4=10 5/8"; C=92 3/16"; C/2=46 3/32"; CLASS=1"; D=66 7/8"; D-L-K-J=1"; D-M=36 3/4"; DUAL_Q=156 3/8"; DUAL_Q+.25"=156 5/8"; E=77 5/16"; E-(NOZZLE_RAD/3*2)=29 1/16"; E-N-N-H=2"; E/2=38 21/32"; E/2-H/2=17 7/32"; E/52*15=22 5/16"; E/52*30=44 19/32"; F=44 7/8"; F/2=22 7/16"; H=42 7/8"; H/2=21 7/16"; HEIGHT=69 3/4"; J=11"; J+K+L=65 7/8"; K=22 3/4"; L=32 1/8"; M=30 1/8"; M-(2*(D-L-K-J))=28 1/8"; MB_A=160 5/16"; MB_F=10 1/2"; MB_F-3"=7 1/2"; MB_HEIGHT=58 1/4"; MB_HEIGHT/2=29 1/8"; MB_N=14 3/16"; MB_N-(D-J-K-L)=13 3/16"; MB_P=52"; MB_P+.25"=52 1/4"; MB_P+MB_P+.5=104 1/2"; MB_P-4.5"=47 1/2"; MB_Q=52"; N=15 7/32"; N+(H/2)=36 21/32"; NOZZLE_BOTTOM_ID=28 3/4"; NOZZLE_BOTTOM_RAD=14 3/8"; NOZZLE_BOTTOM_RAD-3*2=8 3/8"; NOZZLE_HEIGHT=52 3/4"; NOZZLE_HEIGHT/7*2=13 3/16"; NOZZLE_SIZE=21"; NOZZLE_TOP_OD=30 3/4"; NOZZLE_TOP_RAD=15 3/8"; NOZZLE_WB/4=9 13/16"; NOZZLE_WB_OD=49"; NOZZLE_WB_RAD=24 1/2"; NOZZLE_WB_RAD-2"=22 1/2"; P=18 1/4"; R=36"; R*1.1=39 19/32"; R+((B/2)+1.5")=58 23/32"; R-((B/2)+1.5")=13 9/32"; RO/2=23 3/4"; RO2/2=128 1/8"; TRANSITION=20 11/32"; TRANSITION/2=10 5/32"; TRIP_Q=260 3/4"; TRIP_Q-4.5"=256 1/4"; Type Comments=Triple Vari-Plume Laboratory Exhaust Centrifugal Airfoil Class 1 Arr 10 With Mixing Box
- Triple_365_CAVP-21L_CLASS_1_With_Mixing_Box: ((M - (2 * (D - L - K - J))) / 2) + (TRANSITION / 2)=24 7/32"; (B/2)+1.5"=22 23/32"; (B/2)-.125"=21 3/32"; (D-J-K-L)*2=2"; (E/2)-((B/2)+1.5")=15 15/16"; (E/2)-((MB_P/2)+.125")=12 17/32"; (E/2)-(E/52*15)=16 11/32"; (F-((F-H)/2))/2=20 7/16"; (M - (2 * (D - L - K - J)))/2=14 1/16"; (MB_P/2)+.125"=26 1/8"; (MB_P/2-.125")+((F / 2) - 2")=-46 5/16"; (MB_P/2-.125")-((F / 2) - 2")=-5 7/16"; (MB_Q/2)+.125"=26 1/8"; (NOZZLE_HEIGHT - (NOZZLE_HEIGHT / 8 * 2)) / 2=19 25/32"; (NOZZLE_WB_OD - NOZZLE_TOP_OD) / 4=4 9/16"; -((MB_Q / 2) + 1/8")=-26 1/8"; -(F-((F-H)/2))/2=-20 7/16"; -MB_HEIGHT=-58 1/4"; -MB_P=-52"; -MB_P-.25=-52 1/4"; A=153 13/16"; A/2=76 29/32"; B=42 7/16"; B/2=21 7/32"; B/4=10 5/8"; C=92 3/16"; C/2=46 3/32"; CLASS=1"; D=66 7/8"; D-L-K-J=1"; D-M=36 3/4"; DUAL_Q=156 3/8"; DUAL_Q+.25"=156 5/8"; E=77 5/16"; E-(NOZZLE_RAD/3*2)=29 1/16"; E-N-N-H=2"; E/2=38 21/32"; E/2-H/2=17 7/32"; E/52*15=22 5/16"; E/52*30=44 19/32"; F=44 7/8"; F/2=22 7/16"; H=42 7/8"; H/2=21 7/16"; HEIGHT=69 3/4"; J=11"; J+K+L=65 7/8"; K=22 3/4"; L=32 1/8"; M=30 1/8"; M-(2*(D-L-K-J))=28 1/8"; MB_A=160 5/16"; MB_F=10 1/2"; MB_F-3"=7 1/2"; MB_HEIGHT=58 1/4"; MB_HEIGHT/2=29 1/8"; MB_N=14 3/16"; MB_N-(D-J-K-L)=13 3/16"; MB_P=52"; MB_P+.25"=52 1/4"; MB_P+MB_P+.5=104 1/2"; MB_P-4.5"=47 1/2"; MB_Q=52"; N=15 7/32"; N+(H/2)=36 21/32"; NOZZLE_BOTTOM_ID=28 3/4"; NOZZLE_BOTTOM_RAD=14 3/8"; NOZZLE_BOTTOM_RAD-3*2=8 3/8"; NOZZLE_HEIGHT=52 3/4"; NOZZLE_HEIGHT/7*2=13 3/16"; NOZZLE_SIZE=21"; NOZZLE_TOP_OD=30 3/4"; NOZZLE_TOP_RAD=15 3/8"; NOZZLE_WB/4=9 13/16"; NOZZLE_WB_OD=49"; NOZZLE_WB_RAD=24 1/2"; NOZZLE_WB_RAD-2"=22 1/2"; P=18 1/4"; R=36"; R*1.1=39 19/32"; R+((B/2)+1.5")=58 23/32"; R-((B/2)+1.5")=13 9/32"; RO/2=23 3/4"; RO2/2=128 1/8"; TRANSITION=20 11/32"; TRANSITION/2=10 5/32"; TRIP_Q=260 3/4"; TRIP_Q-4.5"=256 1/4"; Type Comments=Triple Vari-Plume Laboratory Exhaust Centrifugal Airfoil Class 1 Arr 10 With Mixing Box
- Triple_365_CAVP-21H_CLASS_2_With_Mixing_Box: ((M - (2 * (D - L - K - J))) / 2) + (TRANSITION / 2)=24 7/32"; (B/2)+1.5"=22 23/32"; (B/2)-.125"=21 3/32"; (D-J-K-L)*2=2"; (E/2)-((B/2)+1.5")=15 15/16"; (E/2)-((MB_P/2)+.125")=12 17/32"; (E/2)-(E/52*15)=16 11/32"; (F-((F-H)/2))/2=20 7/16"; (M - (2 * (D - L - K - J)))/2=14 1/16"; (MB_P/2)+.125"=26 1/8"; (MB_P/2-.125")+((F / 2) - 2")=-46 5/16"; (MB_P/2-.125")-((F / 2) - 2")=-5 7/16"; (MB_Q/2)+.125"=26 1/8"; (NOZZLE_HEIGHT - (NOZZLE_HEIGHT / 8 * 2)) / 2=19 25/32"; (NOZZLE_WB_OD - NOZZLE_TOP_OD) / 4=4 9/16"; -((MB_Q / 2) + 1/8")=-26 1/8"; -(F-((F-H)/2))/2=-20 7/16"; -MB_HEIGHT=-58 1/4"; -MB_P=-52"; -MB_P-.25=-52 1/4"; A=153 13/16"; A/2=76 29/32"; B=42 7/16"; B/2=21 7/32"; B/4=10 5/8"; C=92 3/16"; C/2=46 3/32"; CLASS=2"; D=67 1/8"; D-L-K-J=1"; D-M=37"; DUAL_Q=156 3/8"; DUAL_Q+.25"=156 5/8"; E=77 5/16"; E-(NOZZLE_RAD/3*2)=29 1/16"; E-N-N-H=2"; E/2=38 21/32"; E/2-H/2=17 7/32"; E/52*15=22 5/16"; E/52*30=44 19/32"; F=44 7/8"; F/2=22 7/16"; H=42 7/8"; H/2=21 7/16"; HEIGHT=69 3/4"; J=11"; J+K+L=66 1/8"; K=23"; L=32 1/8"; M=30 1/8"; M-(2*(D-L-K-J))=28 1/8"; MB_A=160 9/16"; MB_F=10 1/2"; MB_F-3"=7 1/2"; MB_HEIGHT=58 1/4"; MB_HEIGHT/2=29 1/8"; MB_N=14 3/16"; MB_N-(D-J-K-L)=13 3/16"; MB_P=52"; MB_P+.25"=52 1/4"; MB_P+MB_P+.5=104 1/2"; MB_P-4.5"=47 1/2"; MB_Q=52"; N=15 7/32"; N+(H/2)=36 21/32"; NOZZLE_BOTTOM_ID=28 3/4"; NOZZLE_BOTTOM_RAD=14 3/8"; NOZZLE_BOTTOM_RAD-3*2=8 3/8"; NOZZLE_HEIGHT=52 3/4"; NOZZLE_HEIGHT/7*2=13 3/16"; NOZZLE_SIZE=21"; NOZZLE_TOP_OD=30 3/4"; NOZZLE_TOP_RAD=15 3/8"; NOZZLE_WB/4=9 13/16"; NOZZLE_WB_OD=49"; NOZZLE_WB_RAD=24 1/2"; NOZZLE_WB_RAD-2"=22 1/2"; P=18 1/2"; R=36"; R*1.1=39 19/32"; R+((B/2)+1.5")=58 23/32"; R-((B/2)+1.5")=13 9/32"; RO/2=23 3/4"; RO2/2=128 1/8"; TRANSITION=20 11/32"; TRANSITION/2=10 5/32"; TRIP_Q=260 3/4"; TRIP_Q-4.5"=256 1/4"; Type Comments=Triple Vari-Plume Laboratory Exhaust Centrifugal Airfoil Class 2 Arr 10 With Mixing Box
- Triple_365_CAVP-21L_CLASS_2_With_Mixing_Box: ((M - (2 * (D - L - K - J))) / 2) + (TRANSITION / 2)=24 7/32"; (B/2)+1.5"=22 23/32"; (B/2)-.125"=21 3/32"; (D-J-K-L)*2=2"; (E/2)-((B/2)+1.5")=15 15/16"; (E/2)-((MB_P/2)+.125")=12 17/32"; (E/2)-(E/52*15)=16 11/32"; (F-((F-H)/2))/2=20 7/16"; (M - (2 * (D - L - K - J)))/2=14 1/16"; (MB_P/2)+.125"=26 1/8"; (MB_P/2-.125")+((F / 2) - 2")=-46 5/16"; (MB_P/2-.125")-((F / 2) - 2")=-5 7/16"; (MB_Q/2)+.125"=26 1/8"; (NOZZLE_HEIGHT - (NOZZLE_HEIGHT / 8 * 2)) / 2=19 25/32"; (NOZZLE_WB_OD - NOZZLE_TOP_OD) / 4=4 9/16"; -((MB_Q / 2) + 1/8")=-26 1/8"; -(F-((F-H)/2))/2=-20 7/16"; -MB_HEIGHT=-58 1/4"; -MB_P=-52"; -MB_P-.25=-52 1/4"; A=153 13/16"; A/2=76 29/32"; B=42 7/16"; B/2=21 7/32"; B/4=10 5/8"; C=92 3/16"; C/2=46 3/32"; CLASS=2"; D=67 1/8"; D-L-K-J=1"; D-M=37"; DUAL_Q=156 3/8"; DUAL_Q+.25"=156 5/8"; E=77 5/16"; E-(NOZZLE_RAD/3*2)=29 1/16"; E-N-N-H=2"; E/2=38 21/32"; E/2-H/2=17 7/32"; E/52*15=22 5/16"; E/52*30=44 19/32"; F=44 7/8"; F/2=22 7/16"; H=42 7/8"; H/2=21 7/16"; HEIGHT=69 3/4"; J=11"; J+K+L=66 1/8"; K=23"; L=32 1/8"; M=30 1/8"; M-(2*(D-L-K-J))=28 1/8"; MB_A=160 9/16"; MB_F=10 1/2"; MB_F-3"=7 1/2"; MB_HEIGHT=58 1/4"; MB_HEIGHT/2=29 1/8"; MB_N=14 3/16"; MB_N-(D-J-K-L)=13 3/16"; MB_P=52"; MB_P+.25"=52 1/4"; MB_P+MB_P+.5=104 1/2"; MB_P-4.5"=47 1/2"; MB_Q=52"; N=15 7/32"; N+(H/2)=36 21/32"; NOZZLE_BOTTOM_ID=28 3/4"; NOZZLE_BOTTOM_RAD=14 3/8"; NOZZLE_BOTTOM_RAD-3*2=8 3/8"; NOZZLE_HEIGHT=52 3/4"; NOZZLE_HEIGHT/7*2=13 3/16"; NOZZLE_SIZE=21"; NOZZLE_TOP_OD=30 3/4"; NOZZLE_TOP_RAD=15 3/8"; NOZZLE_WB/4=9 13/16"; NOZZLE_WB_OD=49"; NOZZLE_WB_RAD=24 1/2"; NOZZLE_WB_RAD-2"=22 1/2"; P=18 1/2"; R=36"; R*1.1=39 19/32"; R+((B/2)+1.5")=58 23/32"; R-((B/2)+1.5")=13 9/32"; RO/2=23 3/4"; RO2/2=128 1/8"; TRANSITION=20 11/32"; TRANSITION/2=10 5/32"; TRIP_Q=260 3/4"; TRIP_Q-4.5"=256 1/4"; Type Comments=Triple Vari-Plume Laboratory Exhaust Centrifugal Airfoil Class 2 Arr 10 With Mixing Box
- Triple_402_CAVP-21H_CLASS_1_With_Mixing_Box: ((M - (2 * (D - L - K - J))) / 2) + (TRANSITION / 2)=25 29/32"; (B/2)+1.5"=24 3/32"; (B/2)-.125"=22 15/32"; (D-J-K-L)*2=2 3/4"; (E/2)-((B/2)+1.5")=18 3/8"; (E/2)-((MB_P/2)+.125")=14 11/32"; (E/2)-(E/52*15)=17 31/32"; (F-((F-H)/2))/2=22 3/8"; (M - (2 * (D - L - K - J)))/2=15 3/4"; (MB_P/2)+.125"=28 1/8"; (MB_P/2-.125")+((F / 2) - 2")=-50 1/4"; (MB_P/2-.125")-((F / 2) - 2")=-5 1/2"; (MB_Q/2)+.125"=28 1/8"; (NOZZLE_HEIGHT - (NOZZLE_HEIGHT / 8 * 2)) / 2=19 25/32"; (NOZZLE_WB_OD - NOZZLE_TOP_OD) / 4=4 9/16"; -((MB_Q / 2) + 1/8")=-28 1/8"; -(F-((F-H)/2))/2=-22 3/8"; -MB_HEIGHT=-64 1/2"; -MB_P=-56"; -MB_P-.25=-56 1/4"; A=178 3/4"; A/2=89 3/8"; B=45 3/16"; B/2=22 19/32"; B/4=11 5/16"; C=100 3/4"; C/2=50 3/8"; CLASS=1"; D=72 1/4"; D-L-K-J=1 3/8"; D-M=38"; DUAL_Q=168 3/8"; DUAL_Q+.25"=168 5/8"; E=84 15/16"; E-(NOZZLE_RAD/3*2)=32 7/8"; E-N-N-H=2"; E/2=42 15/32"; E/2-H/2=19 3/32"; E/52*15=24 1/2"; E/52*30=49"; F=48 3/4"; F/2=24 3/8"; H=46 3/4"; H/2=23 3/8"; HEIGHT=77 3/32"; J=12 1/2"; J+K+L=70 7/8"; K=21 7/8"; L=36 1/2"; M=34 1/4"; M-(2*(D-L-K-J))=31 1/2"; MB_A=171 1/16"; MB_F=12 5/8"; MB_F-3"=9 5/8"; MB_HEIGHT=64 1/2"; MB_HEIGHT/2=32 1/4"; MB_N=13 9/16"; MB_N-(D-J-K-L)=12 3/16"; MB_P=56"; MB_P+.25"=56 1/4"; MB_P+MB_P+.5=112 1/2"; MB_P-4.5"=51 1/2"; MB_Q=56"; N=17 3/32"; N+(H/2)=40 15/32"; NOZZLE_BOTTOM_ID=28 3/4"; NOZZLE_BOTTOM_RAD=14 3/8"; NOZZLE_BOTTOM_RAD-3*2=8 3/8"; NOZZLE_HEIGHT=52 3/4"; NOZZLE_HEIGHT/7*2=13 3/16"; NOZZLE_SIZE=21"; NOZZLE_TOP_OD=30 3/4"; NOZZLE_TOP_RAD=15 3/8"; NOZZLE_WB/4=9 13/16"; NOZZLE_WB_OD=49"; NOZZLE_WB_RAD=24 1/2"; NOZZLE_WB_RAD-2"=22 1/2"; P=18 1/4"; R=40"; R*1.1=44"; R+((B/2)+1.5")=64 3/32"; R-((B/2)+1.5")=15 29/32"; RO/2=25 3/4"; RO2/2=138 1/8"; TRANSITION=20 11/32"; TRANSITION/2=10 5/32"; TRIP_Q=280 3/4"; TRIP_Q-4.5"=276 1/4"; Type Comments=Triple Vari-Plume Laboratory Exhaust Centrifugal Airfoil Class 1 Arr 10 With Mixing Box
- Triple_402_CAVP-21L_CLASS_1_With_Mixing_Box: ((M - (2 * (D - L - K - J))) / 2) + (TRANSITION / 2)=25 29/32"; (B/2)+1.5"=24 3/32"; (B/2)-.125"=22 15/32"; (D-J-K-L)*2=2 3/4"; (E/2)-((B/2)+1.5")=18 3/8"; (E/2)-((MB_P/2)+.125")=14 11/32"; (E/2)-(E/52*15)=17 31/32"; (F-((F-H)/2))/2=22 3/8"; (M - (2 * (D - L - K - J)))/2=15 3/4"; (MB_P/2)+.125"=28 1/8"; (MB_P/2-.125")+((F / 2) - 2")=-50 1/4"; (MB_P/2-.125")-((F / 2) - 2")=-5 1/2"; (MB_Q/2)+.125"=28 1/8"; (NOZZLE_HEIGHT - (NOZZLE_HEIGHT / 8 * 2)) / 2=19 25/32"; (NOZZLE_WB_OD - NOZZLE_TOP_OD) / 4=4 9/16"; -((MB_Q / 2) + 1/8")=-28 1/8"; -(F-((F-H)/2))/2=-22 3/8"; -MB_HEIGHT=-64 1/2"; -MB_P=-56"; -MB_P-.25=-56 1/4"; A=178 3/4"; A/2=89 3/8"; B=45 3/16"; B/2=22 19/32"; B/4=11 5/16"; C=100 3/4"; C/2=50 3/8"; CLASS=1"; D=72 1/4"; D-L-K-J=1 3/8"; D-M=38"; DUAL_Q=168 3/8"; DUAL_Q+.25"=168 5/8"; E=84 15/16"; E-(NOZZLE_RAD/3*2)=32 7/8"; E-N-N-H=2"; E/2=42 15/32"; E/2-H/2=19 3/32"; E/52*15=24 1/2"; E/52*30=49"; F=48 3/4"; F/2=24 3/8"; H=46 3/4"; H/2=23 3/8"; HEIGHT=77 3/32"; J=12 1/2"; J+K+L=70 7/8"; K=21 7/8"; L=36 1/2"; M=34 1/4"; M-(2*(D-L-K-J))=31 1/2"; MB_A=171 1/16"; MB_F=12 5/8"; MB_F-3"=9 5/8"; MB_HEIGHT=64 1/2"; MB_HEIGHT/2=32 1/4"; MB_N=13 9/16"; MB_N-(D-J-K-L)=12 3/16"; MB_P=56"; MB_P+.25"=56 1/4"; MB_P+MB_P+.5=112 1/2"; MB_P-4.5"=51 1/2"; MB_Q=56"; N=17 3/32"; N+(H/2)=40 15/32"; NOZZLE_BOTTOM_ID=28 3/4"; NOZZLE_BOTTOM_RAD=14 3/8"; NOZZLE_BOTTOM_RAD-3*2=8 3/8"; NOZZLE_HEIGHT=52 3/4"; NOZZLE_HEIGHT/7*2=13 3/16"; NOZZLE_SIZE=21"; NOZZLE_TOP_OD=30 3/4"; NOZZLE_TOP_RAD=15 3/8"; NOZZLE_WB/4=9 13/16"; NOZZLE_WB_OD=49"; NOZZLE_WB_RAD=24 1/2"; NOZZLE_WB_RAD-2"=22 1/2"; P=18 1/4"; R=40"; R*1.1=44"; R+((B/2)+1.5")=64 3/32"; R-((B/2)+1.5")=15 29/32"; RO/2=25 3/4"; RO2/2=138 1/8"; TRANSITION=20 11/32"; TRANSITION/2=10 5/32"; TRIP_Q=280 3/4"; TRIP_Q-4.5"=276 1/4"; Type Comments=Triple Vari-Plume Laboratory Exhaust Centrifugal Airfoil Class 1 Arr 10 With Mixing Box
- Triple_402_CAVP-21H_CLASS_2_With_Mixing_Box: ((M - (2 * (D - L - K - J))) / 2) + (TRANSITION / 2)=25 29/32"; (B/2)+1.5"=24 3/32"; (B/2)-.125"=22 15/32"; (D-J-K-L)*2=2 3/4"; (E/2)-((B/2)+1.5")=18 3/8"; (E/2)-((MB_P/2)+.125")=14 11/32"; (E/2)-(E/52*15)=17 31/32"; (F-((F-H)/2))/2=22 3/8"; (M - (2 * (D - L - K - J)))/2=15 3/4"; (MB_P/2)+.125"=28 1/8"; (MB_P/2-.125")+((F / 2) - 2")=-50 1/4"; (MB_P/2-.125")-((F / 2) - 2")=-5 1/2"; (MB_Q/2)+.125"=28 1/8"; (NOZZLE_HEIGHT - (NOZZLE_HEIGHT / 8 * 2)) / 2=19 25/32"; (NOZZLE_WB_OD - NOZZLE_TOP_OD) / 4=4 9/16"; -((MB_Q / 2) + 1/8")=-28 1/8"; -(F-((F-H)/2))/2=-22 3/8"; -MB_HEIGHT=-64 1/2"; -MB_P=-56"; -MB_P-.25=-56 1/4"; A=178 3/4"; A/2=89 3/8"; B=45 3/16"; B/2=22 19/32"; B/4=11 5/16"; C=100 3/4"; C/2=50 3/8"; CLASS=2"; D=72 1/4"; D-L-K-J=1 3/8"; D-M=38"; DUAL_Q=168 3/8"; DUAL_Q+.25"=168 5/8"; E=84 15/16"; E-(NOZZLE_RAD/3*2)=32 7/8"; E-N-N-H=2"; E/2=42 15/32"; E/2-H/2=19 3/32"; E/52*15=24 1/2"; E/52*30=49"; F=48 3/4"; F/2=24 3/8"; H=46 3/4"; H/2=23 3/8"; HEIGHT=77 3/32"; J=12 1/2"; J+K+L=70 7/8"; K=21 7/8"; L=36 1/2"; M=34 1/4"; M-(2*(D-L-K-J))=31 1/2"; MB_A=171 1/16"; MB_F=12 5/8"; MB_F-3"=9 5/8"; MB_HEIGHT=64 1/2"; MB_HEIGHT/2=32 1/4"; MB_N=13 9/16"; MB_N-(D-J-K-L)=12 3/16"; MB_P=56"; MB_P+.25"=56 1/4"; MB_P+MB_P+.5=112 1/2"; MB_P-4.5"=51 1/2"; MB_Q=56"; N=17 3/32"; N+(H/2)=40 15/32"; NOZZLE_BOTTOM_ID=28 3/4"; NOZZLE_BOTTOM_RAD=14 3/8"; NOZZLE_BOTTOM_RAD-3*2=8 3/8"; NOZZLE_HEIGHT=52 3/4"; NOZZLE_HEIGHT/7*2=13 3/16"; NOZZLE_SIZE=21"; NOZZLE_TOP_OD=30 3/4"; NOZZLE_TOP_RAD=15 3/8"; NOZZLE_WB/4=9 13/16"; NOZZLE_WB_OD=49"; NOZZLE_WB_RAD=24 1/2"; NOZZLE_WB_RAD-2"=22 1/2"; P=19 1/2"; R=40"; R*1.1=44"; R+((B/2)+1.5")=64 3/32"; R-((B/2)+1.5")=15 29/32"; RO/2=25 3/4"; RO2/2=138 1/8"; TRANSITION=20 11/32"; TRANSITION/2=10 5/32"; TRIP_Q=280 3/4"; TRIP_Q-4.5"=276 1/4"; Type Comments=Triple Vari-Plume Laboratory Exhaust Centrifugal Airfoil Class 2 Arr 10 With Mixing Box
- Triple_402_CAVP-21L_CLASS_2_With_Mixing_Box: ((M - (2 * (D - L - K - J))) / 2) + (TRANSITION / 2)=25 29/32"; (B/2)+1.5"=24 3/32"; (B/2)-.125"=22 15/32"; (D-J-K-L)*2=2 3/4"; (E/2)-((B/2)+1.5")=18 3/8"; (E/2)-((MB_P/2)+.125")=14 11/32"; (E/2)-(E/52*15)=17 31/32"; (F-((F-H)/2))/2=22 3/8"; (M - (2 * (D - L - K - J)))/2=15 3/4"; (MB_P/2)+.125"=28 1/8"; (MB_P/2-.125")+((F / 2) - 2")=-50 1/4"; (MB_P/2-.125")-((F / 2) - 2")=-5 1/2"; (MB_Q/2)+.125"=28 1/8"; (NOZZLE_HEIGHT - (NOZZLE_HEIGHT / 8 * 2)) / 2=19 25/32"; (NOZZLE_WB_OD - NOZZLE_TOP_OD) / 4=4 9/16"; -((MB_Q / 2) + 1/8")=-28 1/8"; -(F-((F-H)/2))/2=-22 3/8"; -MB_HEIGHT=-64 1/2"; -MB_P=-56"; -MB_P-.25=-56 1/4"; A=178 3/4"; A/2=89 3/8"; B=45 3/16"; B/2=22 19/32"; B/4=11 5/16"; C=100 3/4"; C/2=50 3/8"; CLASS=2"; D=72 1/4"; D-L-K-J=1 3/8"; D-M=38"; DUAL_Q=168 3/8"; DUAL_Q+.25"=168 5/8"; E=84 15/16"; E-(NOZZLE_RAD/3*2)=32 7/8"; E-N-N-H=2"; E/2=42 15/32"; E/2-H/2=19 3/32"; E/52*15=24 1/2"; E/52*30=49"; F=48 3/4"; F/2=24 3/8"; H=46 3/4"; H/2=23 3/8"; HEIGHT=77 3/32"; J=12 1/2"; J+K+L=70 7/8"; K=21 7/8"; L=36 1/2"; M=34 1/4"; M-(2*(D-L-K-J))=31 1/2"; MB_A=171 1/16"; MB_F=12 5/8"; MB_F-3"=9 5/8"; MB_HEIGHT=64 1/2"; MB_HEIGHT/2=32 1/4"; MB_N=13 9/16"; MB_N-(D-J-K-L)=12 3/16"; MB_P=56"; MB_P+.25"=56 1/4"; MB_P+MB_P+.5=112 1/2"; MB_P-4.5"=51 1/2"; MB_Q=56"; N=17 3/32"; N+(H/2)=40 15/32"; NOZZLE_BOTTOM_ID=28 3/4"; NOZZLE_BOTTOM_RAD=14 3/8"; NOZZLE_BOTTOM_RAD-3*2=8 3/8"; NOZZLE_HEIGHT=52 3/4"; NOZZLE_HEIGHT/7*2=13 3/16"; NOZZLE_SIZE=21"; NOZZLE_TOP_OD=30 3/4"; NOZZLE_TOP_RAD=15 3/8"; NOZZLE_WB/4=9 13/16"; NOZZLE_WB_OD=49"; NOZZLE_WB_RAD=24 1/2"; NOZZLE_WB_RAD-2"=22 1/2"; P=19 1/2"; R=40"; R*1.1=44"; R+((B/2)+1.5")=64 3/32"; R-((B/2)+1.5")=15 29/32"; RO/2=25 3/4"; RO2/2=138 1/8"; TRANSITION=20 11/32"; TRANSITION/2=10 5/32"; TRIP_Q=280 3/4"; TRIP_Q-4.5"=276 1/4"; Type Comments=Triple Vari-Plume Laboratory Exhaust Centrifugal Airfoil Class 2 Arr 10 With Mixing Box
- Triple_365_CAVP-27H_CLASS_1_With_Mixing_Box: ((M - (2 * (D - L - K - J))) / 2) + (TRANSITION / 2)=27 19/32"; (B/2)+1.5"=22 23/32"; (B/2)-.125"=21 3/32"; (D-J-K-L)*2=2"; (E/2)-((B/2)+1.5")=15 15/16"; (E/2)-((MB_P/2)+.125")=12 17/32"; (E/2)-(E/52*15)=16 11/32"; (F-((F-H)/2))/2=20 7/16"; (M - (2 * (D - L - K - J)))/2=14 1/16"; (MB_P/2)+.125"=26 1/8"; (MB_P/2-.125")+((F / 2) - 2")=-46 5/16"; (MB_P/2-.125")-((F / 2) - 2")=-5 7/16"; (MB_Q/2)+.125"=26 1/8"; (NOZZLE_HEIGHT - (NOZZLE_HEIGHT / 8 * 2)) / 2=22 3/4"; (NOZZLE_WB_OD - NOZZLE_TOP_OD) / 4=5 11/32"; -((MB_Q / 2) + 1/8")=-26 1/8"; -(F-((F-H)/2))/2=-20 7/16"; -MB_HEIGHT=-58 1/4"; -MB_P=-52"; -MB_P-.25=-52 1/4"; A=153 13/16"; A/2=76 29/32"; B=42 7/16"; B/2=21 7/32"; B/4=10 5/8"; C=92 3/16"; C/2=46 3/32"; CLASS=1"; D=66 7/8"; D-L-K-J=1"; D-M=36 3/4"; DUAL_Q=156 3/8"; DUAL_Q+.25"=156 5/8"; E=77 5/16"; E-(NOZZLE_RAD/3*2)=25 7/8"; E-N-N-H=2"; E/2=38 21/32"; E/2-H/2=17 7/32"; E/52*15=22 5/16"; E/52*30=44 19/32"; F=44 7/8"; F/2=22 7/16"; H=42 7/8"; H/2=21 7/16"; HEIGHT=69 3/4"; J=11"; J+K+L=65 7/8"; K=22 3/4"; L=32 1/8"; M=30 1/8"; M-(2*(D-L-K-J))=28 1/8"; MB_A=160 5/16"; MB_F=10 1/2"; MB_F-3"=7 1/2"; MB_HEIGHT=58 1/4"; MB_HEIGHT/2=29 1/8"; MB_N=14 3/16"; MB_N-(D-J-K-L)=13 3/16"; MB_P=52"; MB_P+.25"=52 1/4"; MB_P+MB_P+.5=104 1/2"; MB_P-4.5"=47 1/2"; MB_Q=52"; N=15 7/32"; N+(H/2)=36 21/32"; NOZZLE_BOTTOM_ID=38 5/16"; NOZZLE_BOTTOM_RAD=19 5/32"; NOZZLE_BOTTOM_RAD-3*2=13 5/32"; NOZZLE_HEIGHT=60 5/8"; NOZZLE_HEIGHT/7*2=15 5/32"; NOZZLE_SIZE=27"; NOZZLE_TOP_OD=39 11/16"; NOZZLE_TOP_RAD=19 27/32"; NOZZLE_WB/4=12 3/16"; NOZZLE_WB_OD=61"; NOZZLE_WB_RAD=30 1/2"; NOZZLE_WB_RAD-2"=28 1/2"; P=18 1/4"; R=36"; R*1.1=39 19/32"; R+((B/2)+1.5")=58 23/32"; R-((B/2)+1.5")=13 9/32"; RO/2=23 3/4"; RO2/2=128 1/8"; TRANSITION=27 3/32"; TRANSITION/2=13 17/32"; TRIP_Q=260 3/4"; TRIP_Q-4.5"=256 1/4"; Type Comments=Triple Vari-Plume Laboratory Exhaust Centrifugal Airfoil Class 1 Arr 10 With Mixing Box
- Triple_365_CAVP-27L_CLASS_1_With_Mixing_Box: ((M - (2 * (D - L - K - J))) / 2) + (TRANSITION / 2)=27 19/32"; (B/2)+1.5"=22 23/32"; (B/2)-.125"=21 3/32"; (D-J-K-L)*2=2"; (E/2)-((B/2)+1.5")=15 15/16"; (E/2)-((MB_P/2)+.125")=12 17/32"; (E/2)-(E/52*15)=16 11/32"; (F-((F-H)/2))/2=20 7/16"; (M - (2 * (D - L - K - J)))/2=14 1/16"; (MB_P/2)+.125"=26 1/8"; (MB_P/2-.125")+((F / 2) - 2")=-46 5/16"; (MB_P/2-.125")-((F / 2) - 2")=-5 7/16"; (MB_Q/2)+.125"=26 1/8"; (NOZZLE_HEIGHT - (NOZZLE_HEIGHT / 8 * 2)) / 2=22 3/4"; (NOZZLE_WB_OD - NOZZLE_TOP_OD) / 4=5 11/32"; -((MB_Q / 2) + 1/8")=-26 1/8"; -(F-((F-H)/2))/2=-20 7/16"; -MB_HEIGHT=-58 1/4"; -MB_P=-52"; -MB_P-.25=-52 1/4"; A=153 13/16"; A/2=76 29/32"; B=42 7/16"; B/2=21 7/32"; B/4=10 5/8"; C=92 3/16"; C/2=46 3/32"; CLASS=1"; D=66 7/8"; D-L-K-J=1"; D-M=36 3/4"; DUAL_Q=156 3/8"; DUAL_Q+.25"=156 5/8"; E=77 5/16"; E-(NOZZLE_RAD/3*2)=25 7/8"; E-N-N-H=2"; E/2=38 21/32"; E/2-H/2=17 7/32"; E/52*15=22 5/16"; E/52*30=44 19/32"; F=44 7/8"; F/2=22 7/16"; H=42 7/8"; H/2=21 7/16"; HEIGHT=69 3/4"; J=11"; J+K+L=65 7/8"; K=22 3/4"; L=32 1/8"; M=30 1/8"; M-(2*(D-L-K-J))=28 1/8"; MB_A=160 5/16"; MB_F=10 1/2"; MB_F-3"=7 1/2"; MB_HEIGHT=58 1/4"; MB_HEIGHT/2=29 1/8"; MB_N=14 3/16"; MB_N-(D-J-K-L)=13 3/16"; MB_P=52"; MB_P+.25"=52 1/4"; MB_P+MB_P+.5=104 1/2"; MB_P-4.5"=47 1/2"; MB_Q=52"; N=15 7/32"; N+(H/2)=36 21/32"; NOZZLE_BOTTOM_ID=38 5/16"; NOZZLE_BOTTOM_RAD=19 5/32"; NOZZLE_BOTTOM_RAD-3*2=13 5/32"; NOZZLE_HEIGHT=60 5/8"; NOZZLE_HEIGHT/7*2=15 5/32"; NOZZLE_SIZE=27"; NOZZLE_TOP_OD=39 11/16"; NOZZLE_TOP_RAD=19 27/32"; NOZZLE_WB/4=12 3/16"; NOZZLE_WB_OD=61"; NOZZLE_WB_RAD=30 1/2"; NOZZLE_WB_RAD-2"=28 1/2"; P=18 1/4"; R=36"; R*1.1=39 19/32"; R+((B/2)+1.5")=58 23/32"; R-((B/2)+1.5")=13 9/32"; RO/2=23 3/4"; RO2/2=128 1/8"; TRANSITION=27 3/32"; TRANSITION/2=13 17/32"; TRIP_Q=260 3/4"; TRIP_Q-4.5"=256 1/4"; Type Comments=Triple Vari-Plume Laboratory Exhaust Centrifugal Airfoil Class 1 Arr 10 With Mixing Box
- Triple_365_CAVP-27H_CLASS_2_With_Mixing_Box: ((M - (2 * (D - L - K - J))) / 2) + (TRANSITION / 2)=27 19/32"; (B/2)+1.5"=22 23/32"; (B/2)-.125"=21 3/32"; (D-J-K-L)*2=2"; (E/2)-((B/2)+1.5")=15 15/16"; (E/2)-((MB_P/2)+.125")=12 17/32"; (E/2)-(E/52*15)=16 11/32"; (F-((F-H)/2))/2=20 7/16"; (M - (2 * (D - L - K - J)))/2=14 1/16"; (MB_P/2)+.125"=26 1/8"; (MB_P/2-.125")+((F / 2) - 2")=-46 5/16"; (MB_P/2-.125")-((F / 2) - 2")=-5 7/16"; (MB_Q/2)+.125"=26 1/8"; (NOZZLE_HEIGHT - (NOZZLE_HEIGHT / 8 * 2)) / 2=22 3/4"; (NOZZLE_WB_OD - NOZZLE_TOP_OD) / 4=5 11/32"; -((MB_Q / 2) + 1/8")=-26 1/8"; -(F-((F-H)/2))/2=-20 7/16"; -MB_HEIGHT=-58 1/4"; -MB_P=-52"; -MB_P-.25=-52 1/4"; A=153 13/16"; A/2=76 29/32"; B=42 7/16"; B/2=21 7/32"; B/4=10 5/8"; C=92 3/16"; C/2=46 3/32"; CLASS=2"; D=67 1/8"; D-L-K-J=1"; D-M=37"; DUAL_Q=156 3/8"; DUAL_Q+.25"=156 5/8"; E=77 5/16"; E-(NOZZLE_RAD/3*2)=25 7/8"; E-N-N-H=2"; E/2=38 21/32"; E/2-H/2=17 7/32"; E/52*15=22 5/16"; E/52*30=44 19/32"; F=44 7/8"; F/2=22 7/16"; H=42 7/8"; H/2=21 7/16"; HEIGHT=69 3/4"; J=11"; J+K+L=66 1/8"; K=23"; L=32 1/8"; M=30 1/8"; M-(2*(D-L-K-J))=28 1/8"; MB_A=160 9/16"; MB_F=10 1/2"; MB_F-3"=7 1/2"; MB_HEIGHT=58 1/4"; MB_HEIGHT/2=29 1/8"; MB_N=14 3/16"; MB_N-(D-J-K-L)=13 3/16"; MB_P=52"; MB_P+.25"=52 1/4"; MB_P+MB_P+.5=104 1/2"; MB_P-4.5"=47 1/2"; MB_Q=52"; N=15 7/32"; N+(H/2)=36 21/32"; NOZZLE_BOTTOM_ID=38 5/16"; NOZZLE_BOTTOM_RAD=19 5/32"; NOZZLE_BOTTOM_RAD-3*2=13 5/32"; NOZZLE_HEIGHT=60 5/8"; NOZZLE_HEIGHT/7*2=15 5/32"; NOZZLE_SIZE=27"; NOZZLE_TOP_OD=39 11/16"; NOZZLE_TOP_RAD=19 27/32"; NOZZLE_WB/4=12 3/16"; NOZZLE_WB_OD=61"; NOZZLE_WB_RAD=30 1/2"; NOZZLE_WB_RAD-2"=28 1/2"; P=18 1/2"; R=36"; R*1.1=39 19/32"; R+((B/2)+1.5")=58 23/32"; R-((B/2)+1.5")=13 9/32"; RO/2=23 3/4"; RO2/2=128 1/8"; TRANSITION=27 3/32"; TRANSITION/2=13 17/32"; TRIP_Q=260 3/4"; TRIP_Q-4.5"=256 1/4"; Type Comments=Triple Vari-Plume Laboratory Exhaust Centrifugal Airfoil Class 2 Arr 10 With Mixing Box
- Triple_365_CAVP-27L_CLASS_2_With_Mixing_Box: ((M - (2 * (D - L - K - J))) / 2) + (TRANSITION / 2)=27 19/32"; (B/2)+1.5"=22 23/32"; (B/2)-.125"=21 3/32"; (D-J-K-L)*2=2"; (E/2)-((B/2)+1.5")=15 15/16"; (E/2)-((MB_P/2)+.125")=12 17/32"; (E/2)-(E/52*15)=16 11/32"; (F-((F-H)/2))/2=20 7/16"; (M - (2 * (D - L - K - J)))/2=14 1/16"; (MB_P/2)+.125"=26 1/8"; (MB_P/2-.125")+((F / 2) - 2")=-46 5/16"; (MB_P/2-.125")-((F / 2) - 2")=-5 7/16"; (MB_Q/2)+.125"=26 1/8"; (NOZZLE_HEIGHT - (NOZZLE_HEIGHT / 8 * 2)) / 2=22 3/4"; (NOZZLE_WB_OD - NOZZLE_TOP_OD) / 4=5 11/32"; -((MB_Q / 2) + 1/8")=-26 1/8"; -(F-((F-H)/2))/2=-20 7/16"; -MB_HEIGHT=-58 1/4"; -MB_P=-52"; -MB_P-.25=-52 1/4"; A=153 13/16"; A/2=76 29/32"; B=42 7/16"; B/2=21 7/32"; B/4=10 5/8"; C=92 3/16"; C/2=46 3/32"; CLASS=2"; D=67 1/8"; D-L-K-J=1"; D-M=37"; DUAL_Q=156 3/8"; DUAL_Q+.25"=156 5/8"; E=77 5/16"; E-(NOZZLE_RAD/3*2)=25 7/8"; E-N-N-H=2"; E/2=38 21/32"; E/2-H/2=17 7/32"; E/52*15=22 5/16"; E/52*30=44 19/32"; F=44 7/8"; F/2=22 7/16"; H=42 7/8"; H/2=21 7/16"; HEIGHT=69 3/4"; J=11"; J+K+L=66 1/8"; K=23"; L=32 1/8"; M=30 1/8"; M-(2*(D-L-K-J))=28 1/8"; MB_A=160 9/16"; MB_F=10 1/2"; MB_F-3"=7 1/2"; MB_HEIGHT=58 1/4"; MB_HEIGHT/2=29 1/8"; MB_N=14 3/16"; MB_N-(D-J-K-L)=13 3/16"; MB_P=52"; MB_P+.25"=52 1/4"; MB_P+MB_P+.5=104 1/2"; MB_P-4.5"=47 1/2"; MB_Q=52"; N=15 7/32"; N+(H/2)=36 21/32"; NOZZLE_BOTTOM_ID=38 5/16"; NOZZLE_BOTTOM_RAD=19 5/32"; NOZZLE_BOTTOM_RAD-3*2=13 5/32"; NOZZLE_HEIGHT=60 5/8"; NOZZLE_HEIGHT/7*2=15 5/32"; NOZZLE_SIZE=27"; NOZZLE_TOP_OD=39 11/16"; NOZZLE_TOP_RAD=19 27/32"; NOZZLE_WB/4=12 3/16"; NOZZLE_WB_OD=61"; NOZZLE_WB_RAD=30 1/2"; NOZZLE_WB_RAD-2"=28 1/2"; P=18 1/2"; R=36"; R*1.1=39 19/32"; R+((B/2)+1.5")=58 23/32"; R-((B/2)+1.5")=13 9/32"; RO/2=23 3/4"; RO2/2=128 1/8"; TRANSITION=27 3/32"; TRANSITION/2=13 17/32"; TRIP_Q=260 3/4"; TRIP_Q-4.5"=256 1/4"; Type Comments=Triple Vari-Plume Laboratory Exhaust Centrifugal Airfoil Class 2 Arr 10 With Mixing Box
- Triple_402_CAVP-27H_CLASS_1_With_Mixing_Box: ((M - (2 * (D - L - K - J))) / 2) + (TRANSITION / 2)=29 9/32"; (B/2)+1.5"=24 3/32"; (B/2)-.125"=22 15/32"; (D-J-K-L)*2=2 3/4"; (E/2)-((B/2)+1.5")=18 3/8"; (E/2)-((MB_P/2)+.125")=14 11/32"; (E/2)-(E/52*15)=17 31/32"; (F-((F-H)/2))/2=22 3/8"; (M - (2 * (D - L - K - J)))/2=15 3/4"; (MB_P/2)+.125"=28 1/8"; (MB_P/2-.125")+((F / 2) - 2")=-50 1/4"; (MB_P/2-.125")-((F / 2) - 2")=-5 1/2"; (MB_Q/2)+.125"=28 1/8"; (NOZZLE_HEIGHT - (NOZZLE_HEIGHT / 8 * 2)) / 2=22 3/4"; (NOZZLE_WB_OD - NOZZLE_TOP_OD) / 4=5 11/32"; -((MB_Q / 2) + 1/8")=-28 1/8"; -(F-((F-H)/2))/2=-22 3/8"; -MB_HEIGHT=-64 1/2"; -MB_P=-56"; -MB_P-.25=-56 1/4"; A=178 3/4"; A/2=89 3/8"; B=45 3/16"; B/2=22 19/32"; B/4=11 5/16"; C=100 3/4"; C/2=50 3/8"; CLASS=1"; D=72 1/4"; D-L-K-J=1 3/8"; D-M=38"; DUAL_Q=168 3/8"; DUAL_Q+.25"=168 5/8"; E=84 15/16"; E-(NOZZLE_RAD/3*2)=29 11/16"; E-N-N-H=2"; E/2=42 15/32"; E/2-H/2=19 3/32"; E/52*15=24 1/2"; E/52*30=49"; F=48 3/4"; F/2=24 3/8"; H=46 3/4"; H/2=23 3/8"; HEIGHT=77 3/32"; J=12 1/2"; J+K+L=70 7/8"; K=21 7/8"; L=36 1/2"; M=34 1/4"; M-(2*(D-L-K-J))=31 1/2"; MB_A=171 1/16"; MB_F=12 5/8"; MB_F-3"=9 5/8"; MB_HEIGHT=64 1/2"; MB_HEIGHT/2=32 1/4"; MB_N=13 9/16"; MB_N-(D-J-K-L)=12 3/16"; MB_P=56"; MB_P+.25"=56 1/4"; MB_P+MB_P+.5=112 1/2"; MB_P-4.5"=51 1/2"; MB_Q=56"; N=17 3/32"; N+(H/2)=40 15/32"; NOZZLE_BOTTOM_ID=38 5/16"; NOZZLE_BOTTOM_RAD=19 5/32"; NOZZLE_BOTTOM_RAD-3*2=13 5/32"; NOZZLE_HEIGHT=60 5/8"; NOZZLE_HEIGHT/7*2=15 5/32"; NOZZLE_SIZE=27"; NOZZLE_TOP_OD=39 11/16"; NOZZLE_TOP_RAD=19 27/32"; NOZZLE_WB/4=12 3/16"; NOZZLE_WB_OD=61"; NOZZLE_WB_RAD=30 1/2"; NOZZLE_WB_RAD-2"=28 1/2"; P=18 1/4"; R=40"; R*1.1=44"; R+((B/2)+1.5")=64 3/32"; R-((B/2)+1.5")=15 29/32"; RO/2=25 3/4"; RO2/2=138 1/8"; TRANSITION=27 3/32"; TRANSITION/2=13 17/32"; TRIP_Q=280 3/4"; TRIP_Q-4.5"=276 1/4"; Type Comments=Triple Vari-Plume Laboratory Exhaust Centrifugal Airfoil Class 1 Arr 10 With Mixing Box
- Triple_402_CAVP-27L_CLASS_1_With_Mixing_Box: ((M - (2 * (D - L - K - J))) / 2) + (TRANSITION / 2)=29 9/32"; (B/2)+1.5"=24 3/32"; (B/2)-.125"=22 15/32"; (D-J-K-L)*2=2 3/4"; (E/2)-((B/2)+1.5")=18 3/8"; (E/2)-((MB_P/2)+.125")=14 11/32"; (E/2)-(E/52*15)=17 31/32"; (F-((F-H)/2))/2=22 3/8"; (M - (2 * (D - L - K - J)))/2=15 3/4"; (MB_P/2)+.125"=28 1/8"; (MB_P/2-.125")+((F / 2) - 2")=-50 1/4"; (MB_P/2-.125")-((F / 2) - 2")=-5 1/2"; (MB_Q/2)+.125"=28 1/8"; (NOZZLE_HEIGHT - (NOZZLE_HEIGHT / 8 * 2)) / 2=22 3/4"; (NOZZLE_WB_OD - NOZZLE_TOP_OD) / 4=5 11/32"; -((MB_Q / 2) + 1/8")=-28 1/8"; -(F-((F-H)/2))/2=-22 3/8"; -MB_HEIGHT=-64 1/2"; -MB_P=-56"; -MB_P-.25=-56 1/4"; A=178 3/4"; A/2=89 3/8"; B=45 3/16"; B/2=22 19/32"; B/4=11 5/16"; C=100 3/4"; C/2=50 3/8"; CLASS=1"; D=72 1/4"; D-L-K-J=1 3/8"; D-M=38"; DUAL_Q=168 3/8"; DUAL_Q+.25"=168 5/8"; E=84 15/16"; E-(NOZZLE_RAD/3*2)=29 11/16"; E-N-N-H=2"; E/2=42 15/32"; E/2-H/2=19 3/32"; E/52*15=24 1/2"; E/52*30=49"; F=48 3/4"; F/2=24 3/8"; H=46 3/4"; H/2=23 3/8"; HEIGHT=77 3/32"; J=12 1/2"; J+K+L=70 7/8"; K=21 7/8"; L=36 1/2"; M=34 1/4"; M-(2*(D-L-K-J))=31 1/2"; MB_A=171 1/16"; MB_F=12 5/8"; MB_F-3"=9 5/8"; MB_HEIGHT=64 1/2"; MB_HEIGHT/2=32 1/4"; MB_N=13 9/16"; MB_N-(D-J-K-L)=12 3/16"; MB_P=56"; MB_P+.25"=56 1/4"; MB_P+MB_P+.5=112 1/2"; MB_P-4.5"=51 1/2"; MB_Q=56"; N=17 3/32"; N+(H/2)=40 15/32"; NOZZLE_BOTTOM_ID=38 5/16"; NOZZLE_BOTTOM_RAD=19 5/32"; NOZZLE_BOTTOM_RAD-3*2=13 5/32"; NOZZLE_HEIGHT=60 5/8"; NOZZLE_HEIGHT/7*2=15 5/32"; NOZZLE_SIZE=27"; NOZZLE_TOP_OD=39 11/16"; NOZZLE_TOP_RAD=19 27/32"; NOZZLE_WB/4=12 3/16"; NOZZLE_WB_OD=61"; NOZZLE_WB_RAD=30 1/2"; NOZZLE_WB_RAD-2"=28 1/2"; P=18 1/4"; R=40"; R*1.1=44"; R+((B/2)+1.5")=64 3/32"; R-((B/2)+1.5")=15 29/32"; RO/2=25 3/4"; RO2/2=138 1/8"; TRANSITION=27 3/32"; TRANSITION/2=13 17/32"; TRIP_Q=280 3/4"; TRIP_Q-4.5"=276 1/4"; Type Comments=Triple Vari-Plume Laboratory Exhaust Centrifugal Airfoil Class 1 Arr 10 With Mixing Box
- Triple_402_CAVP-27H_CLASS_2_With_Mixing_Box: ((M - (2 * (D - L - K - J))) / 2) + (TRANSITION / 2)=29 9/32"; (B/2)+1.5"=24 3/32"; (B/2)-.125"=22 15/32"; (D-J-K-L)*2=2 3/4"; (E/2)-((B/2)+1.5")=18 3/8"; (E/2)-((MB_P/2)+.125")=14 11/32"; (E/2)-(E/52*15)=17 31/32"; (F-((F-H)/2))/2=22 3/8"; (M - (2 * (D - L - K - J)))/2=15 3/4"; (MB_P/2)+.125"=28 1/8"; (MB_P/2-.125")+((F / 2) - 2")=-50 1/4"; (MB_P/2-.125")-((F / 2) - 2")=-5 1/2"; (MB_Q/2)+.125"=28 1/8"; (NOZZLE_HEIGHT - (NOZZLE_HEIGHT / 8 * 2)) / 2=22 3/4"; (NOZZLE_WB_OD - NOZZLE_TOP_OD) / 4=5 11/32"; -((MB_Q / 2) + 1/8")=-28 1/8"; -(F-((F-H)/2))/2=-22 3/8"; -MB_HEIGHT=-64 1/2"; -MB_P=-56"; -MB_P-.25=-56 1/4"; A=178 3/4"; A/2=89 3/8"; B=45 3/16"; B/2=22 19/32"; B/4=11 5/16"; C=100 3/4"; C/2=50 3/8"; CLASS=2"; D=72 1/4"; D-L-K-J=1 3/8"; D-M=38"; DUAL_Q=168 3/8"; DUAL_Q+.25"=168 5/8"; E=84 15/16"; E-(NOZZLE_RAD/3*2)=29 11/16"; E-N-N-H=2"; E/2=42 15/32"; E/2-H/2=19 3/32"; E/52*15=24 1/2"; E/52*30=49"; F=48 3/4"; F/2=24 3/8"; H=46 3/4"; H/2=23 3/8"; HEIGHT=77 3/32"; J=12 1/2"; J+K+L=70 7/8"; K=21 7/8"; L=36 1/2"; M=34 1/4"; M-(2*(D-L-K-J))=31 1/2"; MB_A=171 1/16"; MB_F=12 5/8"; MB_F-3"=9 5/8"; MB_HEIGHT=64 1/2"; MB_HEIGHT/2=32 1/4"; MB_N=13 9/16"; MB_N-(D-J-K-L)=12 3/16"; MB_P=56"; MB_P+.25"=56 1/4"; MB_P+MB_P+.5=112 1/2"; MB_P-4.5"=51 1/2"; MB_Q=56"; N=17 3/32"; N+(H/2)=40 15/32"; NOZZLE_BOTTOM_ID=38 5/16"; NOZZLE_BOTTOM_RAD=19 5/32"; NOZZLE_BOTTOM_RAD-3*2=13 5/32"; NOZZLE_HEIGHT=60 5/8"; NOZZLE_HEIGHT/7*2=15 5/32"; NOZZLE_SIZE=27"; NOZZLE_TOP_OD=39 11/16"; NOZZLE_TOP_RAD=19 27/32"; NOZZLE_WB/4=12 3/16"; NOZZLE_WB_OD=61"; NOZZLE_WB_RAD=30 1/2"; NOZZLE_WB_RAD-2"=28 1/2"; P=19 1/2"; R=40"; R*1.1=44"; R+((B/2)+1.5")=64 3/32"; R-((B/2)+1.5")=15 29/32"; RO/2=25 3/4"; RO2/2=138 1/8"; TRANSITION=27 3/32"; TRANSITION/2=13 17/32"; TRIP_Q=280 3/4"; TRIP_Q-4.5"=276 1/4"; Type Comments=Triple Vari-Plume Laboratory Exhaust Centrifugal Airfoil Class 2 Arr 10 With Mixing Box
- Triple_402_CAVP-27L_CLASS_2_With_Mixing_Box: ((M - (2 * (D - L - K - J))) / 2) + (TRANSITION / 2)=29 9/32"; (B/2)+1.5"=24 3/32"; (B/2)-.125"=22 15/32"; (D-J-K-L)*2=2 3/4"; (E/2)-((B/2)+1.5")=18 3/8"; (E/2)-((MB_P/2)+.125")=14 11/32"; (E/2)-(E/52*15)=17 31/32"; (F-((F-H)/2))/2=22 3/8"; (M - (2 * (D - L - K - J)))/2=15 3/4"; (MB_P/2)+.125"=28 1/8"; (MB_P/2-.125")+((F / 2) - 2")=-50 1/4"; (MB_P/2-.125")-((F / 2) - 2")=-5 1/2"; (MB_Q/2)+.125"=28 1/8"; (NOZZLE_HEIGHT - (NOZZLE_HEIGHT / 8 * 2)) / 2=22 3/4"; (NOZZLE_WB_OD - NOZZLE_TOP_OD) / 4=5 11/32"; -((MB_Q / 2) + 1/8")=-28 1/8"; -(F-((F-H)/2))/2=-22 3/8"; -MB_HEIGHT=-64 1/2"; -MB_P=-56"; -MB_P-.25=-56 1/4"; A=178 3/4"; A/2=89 3/8"; B=45 3/16"; B/2=22 19/32"; B/4=11 5/16"; C=100 3/4"; C/2=50 3/8"; CLASS=2"; D=72 1/4"; D-L-K-J=1 3/8"; D-M=38"; DUAL_Q=168 3/8"; DUAL_Q+.25"=168 5/8"; E=84 15/16"; E-(NOZZLE_RAD/3*2)=29 11/16"; E-N-N-H=2"; E/2=42 15/32"; E/2-H/2=19 3/32"; E/52*15=24 1/2"; E/52*30=49"; F=48 3/4"; F/2=24 3/8"; H=46 3/4"; H/2=23 3/8"; HEIGHT=77 3/32"; J=12 1/2"; J+K+L=70 7/8"; K=21 7/8"; L=36 1/2"; M=34 1/4"; M-(2*(D-L-K-J))=31 1/2"; MB_A=171 1/16"; MB_F=12 5/8"; MB_F-3"=9 5/8"; MB_HEIGHT=64 1/2"; MB_HEIGHT/2=32 1/4"; MB_N=13 9/16"; MB_N-(D-J-K-L)=12 3/16"; MB_P=56"; MB_P+.25"=56 1/4"; MB_P+MB_P+.5=112 1/2"; MB_P-4.5"=51 1/2"; MB_Q=56"; N=17 3/32"; N+(H/2)=40 15/32"; NOZZLE_BOTTOM_ID=38 5/16"; NOZZLE_BOTTOM_RAD=19 5/32"; NOZZLE_BOTTOM_RAD-3*2=13 5/32"; NOZZLE_HEIGHT=60 5/8"; NOZZLE_HEIGHT/7*2=15 5/32"; NOZZLE_SIZE=27"; NOZZLE_TOP_OD=39 11/16"; NOZZLE_TOP_RAD=19 27/32"; NOZZLE_WB/4=12 3/16"; NOZZLE_WB_OD=61"; NOZZLE_WB_RAD=30 1/2"; NOZZLE_WB_RAD-2"=28 1/2"; P=19 1/2"; R=40"; R*1.1=44"; R+((B/2)+1.5")=64 3/32"; R-((B/2)+1.5")=15 29/32"; RO/2=25 3/4"; RO2/2=138 1/8"; TRANSITION=27 3/32"; TRANSITION/2=13 17/32"; TRIP_Q=280 3/4"; TRIP_Q-4.5"=276 1/4"; Type Comments=Triple Vari-Plume Laboratory Exhaust Centrifugal Airfoil Class 2 Arr 10 With Mixing Box
- Triple_445_CAVP-27H_CLASS_1_With_Mixing_Box: ((M - (2 * (D - L - K - J))) / 2) + (TRANSITION / 2)=30 29/32"; (B/2)+1.5"=26 7/32"; (B/2)-.125"=24 19/32"; (D-J-K-L)*2=2 3/4"; (E/2)-((B/2)+1.5")=20 5/8"; (E/2)-((MB_P/2)+.125")=16 23/32"; (E/2)-(E/52*15)=19 13/16"; (F-((F-H)/2))/2=24 3/8"; (M - (2 * (D - L - K - J)))/2=17 3/8"; (MB_P/2)+.125"=30 1/8"; (MB_P/2-.125")+((F / 2) - 2")=-54 1/4"; (MB_P/2-.125")-((F / 2) - 2")=-5 1/2"; (MB_Q/2)+.125"=30 1/8"; (NOZZLE_HEIGHT - (NOZZLE_HEIGHT / 8 * 2)) / 2=22 3/4"; (NOZZLE_WB_OD - NOZZLE_TOP_OD) / 4=5 11/32"; -((MB_Q / 2) + 1/8")=-30 1/8"; -(F-((F-H)/2))/2=-24 3/8"; -MB_HEIGHT=-69 3/4"; -MB_P=-60"; -MB_P-.25=-60 1/4"; A=190 7/8"; A/2=95 7/16"; B=49 7/16"; B/2=24 23/32"; B/4=12 3/8"; C=112 7/8"; C/2=56 7/16"; CLASS=1"; D=80"; D-L-K-J=1 3/8"; D-M=42 1/2"; DUAL_Q=180 3/8"; DUAL_Q+.25"=180 5/8"; E=93 11/16"; E-(NOZZLE_RAD/3*2)=34 1/16"; E-N-N-H=2"; E/2=46 27/32"; E/2-H/2=21 15/32"; E/52*15=27 1/32"; E/52*30=54 1/16"; F=52 3/4"; F/2=26 3/8"; H=50 3/4"; H/2=25 3/8"; HEIGHT=84 29/32"; J=13"; J+K+L=78 5/8"; K=25 7/8"; L=39 3/4"; M=37 1/2"; M-(2*(D-L-K-J))=34 3/4"; MB_A=186 3/16"; MB_F=14 1/2"; MB_F-3"=11 1/2"; MB_HEIGHT=69 3/4"; MB_HEIGHT/2=34 7/8"; MB_N=13 9/16"; MB_N-(D-J-K-L)=12 3/16"; MB_P=60"; MB_P+.25"=60 1/4"; MB_P+MB_P+.5=120 1/2"; MB_P-4.5"=55 1/2"; MB_Q=60"; N=19 15/32"; N+(H/2)=44 27/32"; NOZZLE_BOTTOM_ID=38 5/16"; NOZZLE_BOTTOM_RAD=19 5/32"; NOZZLE_BOTTOM_RAD-3*2=13 5/32"; NOZZLE_HEIGHT=60 5/8"; NOZZLE_HEIGHT/7*2=15 5/32"; NOZZLE_SIZE=27"; NOZZLE_TOP_OD=39 11/16"; NOZZLE_TOP_RAD=19 27/32"; NOZZLE_WB/4=12 3/16"; NOZZLE_WB_OD=61"; NOZZLE_WB_RAD=30 1/2"; NOZZLE_WB_RAD-2"=28 1/2"; P=18 1/4"; R=44"; R*1.1=48 13/32"; R+((B/2)+1.5")=70 7/32"; R-((B/2)+1.5")=17 25/32"; RO/2=27 3/4"; RO2/2=148 1/8"; TRANSITION=27 3/32"; TRANSITION/2=13 17/32"; TRIP_Q=300 3/4"; TRIP_Q-4.5"=296 1/4"; Type Comments=Triple Vari-Plume Laboratory Exhaust Centrifugal Airfoil Class 1 Arr 10 With Mixing Box
- Triple_445_CAVP-27L_CLASS_1_With_Mixing_Box: ((M - (2 * (D - L - K - J))) / 2) + (TRANSITION / 2)=30 29/32"; (B/2)+1.5"=26 7/32"; (B/2)-.125"=24 19/32"; (D-J-K-L)*2=2 3/4"; (E/2)-((B/2)+1.5")=20 5/8"; (E/2)-((MB_P/2)+.125")=16 23/32"; (E/2)-(E/52*15)=19 13/16"; (F-((F-H)/2))/2=24 3/8"; (M - (2 * (D - L - K - J)))/2=17 3/8"; (MB_P/2)+.125"=30 1/8"; (MB_P/2-.125")+((F / 2) - 2")=-54 1/4"; (MB_P/2-.125")-((F / 2) - 2")=-5 1/2"; (MB_Q/2)+.125"=30 1/8"; (NOZZLE_HEIGHT - (NOZZLE_HEIGHT / 8 * 2)) / 2=22 3/4"; (NOZZLE_WB_OD - NOZZLE_TOP_OD) / 4=5 11/32"; -((MB_Q / 2) + 1/8")=-30 1/8"; -(F-((F-H)/2))/2=-24 3/8"; -MB_HEIGHT=-69 3/4"; -MB_P=-60"; -MB_P-.25=-60 1/4"; A=190 7/8"; A/2=95 7/16"; B=49 7/16"; B/2=24 23/32"; B/4=12 3/8"; C=112 7/8"; C/2=56 7/16"; CLASS=1"; D=80"; D-L-K-J=1 3/8"; D-M=42 1/2"; DUAL_Q=180 3/8"; DUAL_Q+.25"=180 5/8"; E=93 11/16"; E-(NOZZLE_RAD/3*2)=34 1/16"; E-N-N-H=2"; E/2=46 27/32"; E/2-H/2=21 15/32"; E/52*15=27 1/32"; E/52*30=54 1/16"; F=52 3/4"; F/2=26 3/8"; H=50 3/4"; H/2=25 3/8"; HEIGHT=84 29/32"; J=13"; J+K+L=78 5/8"; K=25 7/8"; L=39 3/4"; M=37 1/2"; M-(2*(D-L-K-J))=34 3/4"; MB_A=186 3/16"; MB_F=14 1/2"; MB_F-3"=11 1/2"; MB_HEIGHT=69 3/4"; MB_HEIGHT/2=34 7/8"; MB_N=13 9/16"; MB_N-(D-J-K-L)=12 3/16"; MB_P=60"; MB_P+.25"=60 1/4"; MB_P+MB_P+.5=120 1/2"; MB_P-4.5"=55 1/2"; MB_Q=60"; N=19 15/32"; N+(H/2)=44 27/32"; NOZZLE_BOTTOM_ID=38 5/16"; NOZZLE_BOTTOM_RAD=19 5/32"; NOZZLE_BOTTOM_RAD-3*2=13 5/32"; NOZZLE_HEIGHT=60 5/8"; NOZZLE_HEIGHT/7*2=15 5/32"; NOZZLE_SIZE=27"; NOZZLE_TOP_OD=39 11/16"; NOZZLE_TOP_RAD=19 27/32"; NOZZLE_WB/4=12 3/16"; NOZZLE_WB_OD=61"; NOZZLE_WB_RAD=30 1/2"; NOZZLE_WB_RAD-2"=28 1/2"; P=18 1/4"; R=44"; R*1.1=48 13/32"; R+((B/2)+1.5")=70 7/32"; R-((B/2)+1.5")=17 25/32"; RO/2=27 3/4"; RO2/2=148 1/8"; TRANSITION=27 3/32"; TRANSITION/2=13 17/32"; TRIP_Q=300 3/4"; TRIP_Q-4.5"=296 1/4"; Type Comments=Triple Vari-Plume Laboratory Exhaust Centrifugal Airfoil Class 1 Arr 10 With Mixing Box
- Triple_445_CAVP-27H_CLASS_2_With_Mixing_Box: ((M - (2 * (D - L - K - J))) / 2) + (TRANSITION / 2)=30 29/32"; (B/2)+1.5"=26 7/32"; (B/2)-.125"=24 19/32"; (D-J-K-L)*2=2 3/4"; (E/2)-((B/2)+1.5")=20 5/8"; (E/2)-((MB_P/2)+.125")=16 23/32"; (E/2)-(E/52*15)=19 13/16"; (F-((F-H)/2))/2=24 3/8"; (M - (2 * (D - L - K - J)))/2=17 3/8"; (MB_P/2)+.125"=30 1/8"; (MB_P/2-.125")+((F / 2) - 2")=-54 1/4"; (MB_P/2-.125")-((F / 2) - 2")=-5 1/2"; (MB_Q/2)+.125"=30 1/8"; (NOZZLE_HEIGHT - (NOZZLE_HEIGHT / 8 * 2)) / 2=22 3/4"; (NOZZLE_WB_OD - NOZZLE_TOP_OD) / 4=5 11/32"; -((MB_Q / 2) + 1/8")=-30 1/8"; -(F-((F-H)/2))/2=-24 3/8"; -MB_HEIGHT=-69 3/4"; -MB_P=-60"; -MB_P-.25=-60 1/4"; A=190 7/8"; A/2=95 7/16"; B=49 7/16"; B/2=24 23/32"; B/4=12 3/8"; C=112 7/8"; C/2=56 7/16"; CLASS=2"; D=80"; D-L-K-J=1 3/8"; D-M=42 1/2"; DUAL_Q=180 3/8"; DUAL_Q+.25"=180 5/8"; E=93 11/16"; E-(NOZZLE_RAD/3*2)=34 1/16"; E-N-N-H=2"; E/2=46 27/32"; E/2-H/2=21 15/32"; E/52*15=27 1/32"; E/52*30=54 1/16"; F=52 3/4"; F/2=26 3/8"; H=50 3/4"; H/2=25 3/8"; HEIGHT=84 29/32"; J=13"; J+K+L=78 5/8"; K=25 7/8"; L=39 3/4"; M=37 1/2"; M-(2*(D-L-K-J))=34 3/4"; MB_A=186 3/16"; MB_F=14 1/2"; MB_F-3"=11 1/2"; MB_HEIGHT=69 3/4"; MB_HEIGHT/2=34 7/8"; MB_N=13 9/16"; MB_N-(D-J-K-L)=12 3/16"; MB_P=60"; MB_P+.25"=60 1/4"; MB_P+MB_P+.5=120 1/2"; MB_P-4.5"=55 1/2"; MB_Q=60"; N=19 15/32"; N+(H/2)=44 27/32"; NOZZLE_BOTTOM_ID=38 5/16"; NOZZLE_BOTTOM_RAD=19 5/32"; NOZZLE_BOTTOM_RAD-3*2=13 5/32"; NOZZLE_HEIGHT=60 5/8"; NOZZLE_HEIGHT/7*2=15 5/32"; NOZZLE_SIZE=27"; NOZZLE_TOP_OD=39 11/16"; NOZZLE_TOP_RAD=19 27/32"; NOZZLE_WB/4=12 3/16"; NOZZLE_WB_OD=61"; NOZZLE_WB_RAD=30 1/2"; NOZZLE_WB_RAD-2"=28 1/2"; P=19 1/2"; R=44"; R*1.1=48 13/32"; R+((B/2)+1.5")=70 7/32"; R-((B/2)+1.5")=17 25/32"; RO/2=27 3/4"; RO2/2=148 1/8"; TRANSITION=27 3/32"; TRANSITION/2=13 17/32"; TRIP_Q=300 3/4"; TRIP_Q-4.5"=296 1/4"; Type Comments=Triple Vari-Plume Laboratory Exhaust Centrifugal Airfoil Class 2 Arr 10 With Mixing Box
- Triple_445_CAVP-27L_CLASS_2_With_Mixing_Box: ((M - (2 * (D - L - K - J))) / 2) + (TRANSITION / 2)=30 29/32"; (B/2)+1.5"=26 7/32"; (B/2)-.125"=24 19/32"; (D-J-K-L)*2=2 3/4"; (E/2)-((B/2)+1.5")=20 5/8"; (E/2)-((MB_P/2)+.125")=16 23/32"; (E/2)-(E/52*15)=19 13/16"; (F-((F-H)/2))/2=24 3/8"; (M - (2 * (D - L - K - J)))/2=17 3/8"; (MB_P/2)+.125"=30 1/8"; (MB_P/2-.125")+((F / 2) - 2")=-54 1/4"; (MB_P/2-.125")-((F / 2) - 2")=-5 1/2"; (MB_Q/2)+.125"=30 1/8"; (NOZZLE_HEIGHT - (NOZZLE_HEIGHT / 8 * 2)) / 2=22 3/4"; (NOZZLE_WB_OD - NOZZLE_TOP_OD) / 4=5 11/32"; -((MB_Q / 2) + 1/8")=-30 1/8"; -(F-((F-H)/2))/2=-24 3/8"; -MB_HEIGHT=-69 3/4"; -MB_P=-60"; -MB_P-.25=-60 1/4"; A=190 7/8"; A/2=95 7/16"; B=49 7/16"; B/2=24 23/32"; B/4=12 3/8"; C=112 7/8"; C/2=56 7/16"; CLASS=2"; D=80"; D-L-K-J=1 3/8"; D-M=42 1/2"; DUAL_Q=180 3/8"; DUAL_Q+.25"=180 5/8"; E=93 11/16"; E-(NOZZLE_RAD/3*2)=34 1/16"; E-N-N-H=2"; E/2=46 27/32"; E/2-H/2=21 15/32"; E/52*15=27 1/32"; E/52*30=54 1/16"; F=52 3/4"; F/2=26 3/8"; H=50 3/4"; H/2=25 3/8"; HEIGHT=84 29/32"; J=13"; J+K+L=78 5/8"; K=25 7/8"; L=39 3/4"; M=37 1/2"; M-(2*(D-L-K-J))=34 3/4"; MB_A=186 3/16"; MB_F=14 1/2"; MB_F-3"=11 1/2"; MB_HEIGHT=69 3/4"; MB_HEIGHT/2=34 7/8"; MB_N=13 9/16"; MB_N-(D-J-K-L)=12 3/16"; MB_P=60"; MB_P+.25"=60 1/4"; MB_P+MB_P+.5=120 1/2"; MB_P-4.5"=55 1/2"; MB_Q=60"; N=19 15/32"; N+(H/2)=44 27/32"; NOZZLE_BOTTOM_ID=38 5/16"; NOZZLE_BOTTOM_RAD=19 5/32"; NOZZLE_BOTTOM_RAD-3*2=13 5/32"; NOZZLE_HEIGHT=60 5/8"; NOZZLE_HEIGHT/7*2=15 5/32"; NOZZLE_SIZE=27"; NOZZLE_TOP_OD=39 11/16"; NOZZLE_TOP_RAD=19 27/32"; NOZZLE_WB/4=12 3/16"; NOZZLE_WB_OD=61"; NOZZLE_WB_RAD=30 1/2"; NOZZLE_WB_RAD-2"=28 1/2"; P=19 1/2"; R=44"; R*1.1=48 13/32"; R+((B/2)+1.5")=70 7/32"; R-((B/2)+1.5")=17 25/32"; RO/2=27 3/4"; RO2/2=148 1/8"; TRANSITION=27 3/32"; TRANSITION/2=13 17/32"; TRIP_Q=300 3/4"; TRIP_Q-4.5"=296 1/4"; Type Comments=Triple Vari-Plume Laboratory Exhaust Centrifugal Airfoil Class 2 Arr 10 With Mixing Box
- Triple_490_CAVP-27H_CLASS_1_With_Mixing_Box: ((M - (2 * (D - L - K - J))) / 2) + (TRANSITION / 2)=32 5/8"; (B/2)+1.5"=29"; (B/2)-.125"=27 3/8"; (D-J-K-L)*2=2 3/4"; (E/2)-((B/2)+1.5")=22 15/32"; (E/2)-((MB_P/2)+.125")=18 11/32"; (E/2)-(E/52*15)=21 25/32"; (F-((F-H)/2))/2=27 27/32"; (M - (2 * (D - L - K - J)))/2=19 3/32"; (MB_P/2)+.125"=33 1/8"; (MB_P/2-.125")+((F / 2) - 2")=-60 23/32"; (MB_P/2-.125")-((F / 2) - 2")=-5 1/32"; (MB_Q/2)+.125"=33 1/8"; (NOZZLE_HEIGHT - (NOZZLE_HEIGHT / 8 * 2)) / 2=22 3/4"; (NOZZLE_WB_OD - NOZZLE_TOP_OD) / 4=5 11/32"; -((MB_Q / 2) + 1/8")=-33 1/8"; -(F-((F-H)/2))/2=-27 27/32"; -MB_HEIGHT=-70 3/4"; -MB_P=-66"; -MB_P-.25=-66 1/4"; A=217 13/16"; A/2=108 29/32"; B=55"; B/2=27 1/2"; B/4=13 3/4"; C=123 1/16"; C/2=61 17/32"; CLASS=1"; D=79 15/16"; D-L-K-J=1 3/8"; D-M=39"; DUAL_Q=198 3/8"; DUAL_Q+.25"=198 5/8"; E=102 15/16"; E-(NOZZLE_RAD/3*2)=38 11/16"; E-N-N-H=2"; E/2=51 15/32"; E/2-H/2=22 5/8"; E/52*15=29 11/16"; E/52*30=59 3/8"; F=59 11/16"; F/2=29 27/32"; H=57 11/16"; H/2=28 27/32"; HEIGHT=92 15/16"; J=13 1/2"; J+K+L=78 9/16"; K=21 7/8"; L=43 3/16"; M=40 15/16"; M-(2*(D-L-K-J))=38 3/16"; MB_A=191 7/8"; MB_F=15 3/4"; MB_F-3"=12 3/4"; MB_HEIGHT=70 3/4"; MB_HEIGHT/2=35 3/8"; MB_N=13 9/16"; MB_N-(D-J-K-L)=12 3/16"; MB_P=66"; MB_P+.25"=66 1/4"; MB_P+MB_P+.5=132 1/2"; MB_P-4.5"=61 1/2"; MB_Q=66"; N=20 5/8"; N+(H/2)=49 15/32"; NOZZLE_BOTTOM_ID=38 5/16"; NOZZLE_BOTTOM_RAD=19 5/32"; NOZZLE_BOTTOM_RAD-3*2=13 5/32"; NOZZLE_HEIGHT=60 5/8"; NOZZLE_HEIGHT/7*2=15 5/32"; NOZZLE_SIZE=27"; NOZZLE_TOP_OD=39 11/16"; NOZZLE_TOP_RAD=19 27/32"; NOZZLE_WB/4=12 3/16"; NOZZLE_WB_OD=61"; NOZZLE_WB_RAD=30 1/2"; NOZZLE_WB_RAD-2"=28 1/2"; P=18 1/2"; R=48"; R*1.1=52 13/16"; R+((B/2)+1.5")=77"; R-((B/2)+1.5")=19"; RO/2=30 3/4"; RO2/2=163 1/8"; TRANSITION=27 3/32"; TRANSITION/2=13 17/32"; TRIP_Q=330 3/4"; TRIP_Q-4.5"=326 1/4"; Type Comments=Triple Vari-Plume Laboratory Exhaust Centrifugal Airfoil Class 1 Arr 10 With Mixing Box
- Triple_490_CAVP-27L_CLASS_1_With_Mixing_Box: ((M - (2 * (D - L - K - J))) / 2) + (TRANSITION / 2)=32 5/8"; (B/2)+1.5"=29"; (B/2)-.125"=27 3/8"; (D-J-K-L)*2=2 3/4"; (E/2)-((B/2)+1.5")=22 15/32"; (E/2)-((MB_P/2)+.125")=18 11/32"; (E/2)-(E/52*15)=21 25/32"; (F-((F-H)/2))/2=27 27/32"; (M - (2 * (D - L - K - J)))/2=19 3/32"; (MB_P/2)+.125"=33 1/8"; (MB_P/2-.125")+((F / 2) - 2")=-60 23/32"; (MB_P/2-.125")-((F / 2) - 2")=-5 1/32"; (MB_Q/2)+.125"=33 1/8"; (NOZZLE_HEIGHT - (NOZZLE_HEIGHT / 8 * 2)) / 2=22 3/4"; (NOZZLE_WB_OD - NOZZLE_TOP_OD) / 4=5 11/32"; -((MB_Q / 2) + 1/8")=-33 1/8"; -(F-((F-H)/2))/2=-27 27/32"; -MB_HEIGHT=-70 3/4"; -MB_P=-66"; -MB_P-.25=-66 1/4"; A=217 13/16"; A/2=108 29/32"; B=55"; B/2=27 1/2"; B/4=13 3/4"; C=123 1/16"; C/2=61 17/32"; CLASS=1"; D=79 15/16"; D-L-K-J=1 3/8"; D-M=39"; DUAL_Q=198 3/8"; DUAL_Q+.25"=198 5/8"; E=102 15/16"; E-(NOZZLE_RAD/3*2)=38 11/16"; E-N-N-H=2"; E/2=51 15/32"; E/2-H/2=22 5/8"; E/52*15=29 11/16"; E/52*30=59 3/8"; F=59 11/16"; F/2=29 27/32"; H=57 11/16"; H/2=28 27/32"; HEIGHT=92 15/16"; J=13 1/2"; J+K+L=78 9/16"; K=21 7/8"; L=43 3/16"; M=40 15/16"; M-(2*(D-L-K-J))=38 3/16"; MB_A=191 7/8"; MB_F=15 3/4"; MB_F-3"=12 3/4"; MB_HEIGHT=70 3/4"; MB_HEIGHT/2=35 3/8"; MB_N=13 9/16"; MB_N-(D-J-K-L)=12 3/16"; MB_P=66"; MB_P+.25"=66 1/4"; MB_P+MB_P+.5=132 1/2"; MB_P-4.5"=61 1/2"; MB_Q=66"; N=20 5/8"; N+(H/2)=49 15/32"; NOZZLE_BOTTOM_ID=38 5/16"; NOZZLE_BOTTOM_RAD=19 5/32"; NOZZLE_BOTTOM_RAD-3*2=13 5/32"; NOZZLE_HEIGHT=60 5/8"; NOZZLE_HEIGHT/7*2=15 5/32"; NOZZLE_SIZE=27"; NOZZLE_TOP_OD=39 11/16"; NOZZLE_TOP_RAD=19 27/32"; NOZZLE_WB/4=12 3/16"; NOZZLE_WB_OD=61"; NOZZLE_WB_RAD=30 1/2"; NOZZLE_WB_RAD-2"=28 1/2"; P=18 1/2"; R=48"; R*1.1=52 13/16"; R+((B/2)+1.5")=77"; R-((B/2)+1.5")=19"; RO/2=30 3/4"; RO2/2=163 1/8"; TRANSITION=27 3/32"; TRANSITION/2=13 17/32"; TRIP_Q=330 3/4"; TRIP_Q-4.5"=326 1/4"; Type Comments=Triple Vari-Plume Laboratory Exhaust Centrifugal Airfoil Class 1 Arr 10 With Mixing Box
- Triple_490_CAVP-27H_CLASS_2_With_Mixing_Box: ((M - (2 * (D - L - K - J))) / 2) + (TRANSITION / 2)=32 5/8"; (B/2)+1.5"=29"; (B/2)-.125"=27 3/8"; (D-J-K-L)*2=2 3/4"; (E/2)-((B/2)+1.5")=22 15/32"; (E/2)-((MB_P/2)+.125")=18 11/32"; (E/2)-(E/52*15)=21 25/32"; (F-((F-H)/2))/2=27 27/32"; (M - (2 * (D - L - K - J)))/2=19 3/32"; (MB_P/2)+.125"=33 1/8"; (MB_P/2-.125")+((F / 2) - 2")=-60 23/32"; (MB_P/2-.125")-((F / 2) - 2")=-5 1/32"; (MB_Q/2)+.125"=33 1/8"; (NOZZLE_HEIGHT - (NOZZLE_HEIGHT / 8 * 2)) / 2=22 3/4"; (NOZZLE_WB_OD - NOZZLE_TOP_OD) / 4=5 11/32"; -((MB_Q / 2) + 1/8")=-33 1/8"; -(F-((F-H)/2))/2=-27 27/32"; -MB_HEIGHT=-70 3/4"; -MB_P=-66"; -MB_P-.25=-66 1/4"; A=217 13/16"; A/2=108 29/32"; B=55"; B/2=27 1/2"; B/4=13 3/4"; C=123 1/16"; C/2=61 17/32"; CLASS=2"; D=83 15/16"; D-L-K-J=1 3/8"; D-M=43"; DUAL_Q=198 3/8"; DUAL_Q+.25"=198 5/8"; E=102 15/16"; E-(NOZZLE_RAD/3*2)=38 11/16"; E-N-N-H=2"; E/2=51 15/32"; E/2-H/2=22 5/8"; E/52*15=29 11/16"; E/52*30=59 3/8"; F=59 11/16"; F/2=29 27/32"; H=57 11/16"; H/2=28 27/32"; HEIGHT=92 15/16"; J=13 1/2"; J+K+L=82 9/16"; K=25 7/8"; L=43 3/16"; M=40 15/16"; M-(2*(D-L-K-J))=38 3/16"; MB_A=195 7/8"; MB_F=15 3/4"; MB_F-3"=12 3/4"; MB_HEIGHT=70 3/4"; MB_HEIGHT/2=35 3/8"; MB_N=13 9/16"; MB_N-(D-J-K-L)=12 3/16"; MB_P=66"; MB_P+.25"=66 1/4"; MB_P+MB_P+.5=132 1/2"; MB_P-4.5"=61 1/2"; MB_Q=66"; N=20 5/8"; N+(H/2)=49 15/32"; NOZZLE_BOTTOM_ID=38 5/16"; NOZZLE_BOTTOM_RAD=19 5/32"; NOZZLE_BOTTOM_RAD-3*2=13 5/32"; NOZZLE_HEIGHT=60 5/8"; NOZZLE_HEIGHT/7*2=15 5/32"; NOZZLE_SIZE=27"; NOZZLE_TOP_OD=39 11/16"; NOZZLE_TOP_RAD=19 27/32"; NOZZLE_WB/4=12 3/16"; NOZZLE_WB_OD=61"; NOZZLE_WB_RAD=30 1/2"; NOZZLE_WB_RAD-2"=28 1/2"; P=21 7/8"; R=48"; R*1.1=52 13/16"; R+((B/2)+1.5")=77"; R-((B/2)+1.5")=19"; RO/2=30 3/4"; RO2/2=163 1/8"; TRANSITION=27 3/32"; TRANSITION/2=13 17/32"; TRIP_Q=330 3/4"; TRIP_Q-4.5"=326 1/4"; Type Comments=Triple Vari-Plume Laboratory Exhaust Centrifugal Airfoil Class 2 Arr 10 With Mixing Box
- Triple_490_CAVP-27L_CLASS_2_With_Mixing_Box: ((M - (2 * (D - L - K - J))) / 2) + (TRANSITION / 2)=32 5/8"; (B/2)+1.5"=29"; (B/2)-.125"=27 3/8"; (D-J-K-L)*2=2 3/4"; (E/2)-((B/2)+1.5")=22 15/32"; (E/2)-((MB_P/2)+.125")=18 11/32"; (E/2)-(E/52*15)=21 25/32"; (F-((F-H)/2))/2=27 27/32"; (M - (2 * (D - L - K - J)))/2=19 3/32"; (MB_P/2)+.125"=33 1/8"; (MB_P/2-.125")+((F / 2) - 2")=-60 23/32"; (MB_P/2-.125")-((F / 2) - 2")=-5 1/32"; (MB_Q/2)+.125"=33 1/8"; (NOZZLE_HEIGHT - (NOZZLE_HEIGHT / 8 * 2)) / 2=22 3/4"; (NOZZLE_WB_OD - NOZZLE_TOP_OD) / 4=5 11/32"; -((MB_Q / 2) + 1/8")=-33 1/8"; -(F-((F-H)/2))/2=-27 27/32"; -MB_HEIGHT=-70 3/4"; -MB_P=-66"; -MB_P-.25=-66 1/4"; A=217 13/16"; A/2=108 29/32"; B=55"; B/2=27 1/2"; B/4=13 3/4"; C=123 1/16"; C/2=61 17/32"; CLASS=2"; D=83 15/16"; D-L-K-J=1 3/8"; D-M=43"; DUAL_Q=198 3/8"; DUAL_Q+.25"=198 5/8"; E=102 15/16"; E-(NOZZLE_RAD/3*2)=38 11/16"; E-N-N-H=2"; E/2=51 15/32"; E/2-H/2=22 5/8"; E/52*15=29 11/16"; E/52*30=59 3/8"; F=59 11/16"; F/2=29 27/32"; H=57 11/16"; H/2=28 27/32"; HEIGHT=92 15/16"; J=13 1/2"; J+K+L=82 9/16"; K=25 7/8"; L=43 3/16"; M=40 15/16"; M-(2*(D-L-K-J))=38 3/16"; MB_A=195 7/8"; MB_F=15 3/4"; MB_F-3"=12 3/4"; MB_HEIGHT=70 3/4"; MB_HEIGHT/2=35 3/8"; MB_N=13 9/16"; MB_N-(D-J-K-L)=12 3/16"; MB_P=66"; MB_P+.25"=66 1/4"; MB_P+MB_P+.5=132 1/2"; MB_P-4.5"=61 1/2"; MB_Q=66"; N=20 5/8"; N+(H/2)=49 15/32"; NOZZLE_BOTTOM_ID=38 5/16"; NOZZLE_BOTTOM_RAD=19 5/32"; NOZZLE_BOTTOM_RAD-3*2=13 5/32"; NOZZLE_HEIGHT=60 5/8"; NOZZLE_HEIGHT/7*2=15 5/32"; NOZZLE_SIZE=27"; NOZZLE_TOP_OD=39 11/16"; NOZZLE_TOP_RAD=19 27/32"; NOZZLE_WB/4=12 3/16"; NOZZLE_WB_OD=61"; NOZZLE_WB_RAD=30 1/2"; NOZZLE_WB_RAD-2"=28 1/2"; P=21 7/8"; R=48"; R*1.1=52 13/16"; R+((B/2)+1.5")=77"; R-((B/2)+1.5")=19"; RO/2=30 3/4"; RO2/2=163 1/8"; TRANSITION=27 3/32"; TRANSITION/2=13 17/32"; TRIP_Q=330 3/4"; TRIP_Q-4.5"=326 1/4"; Type Comments=Triple Vari-Plume Laboratory Exhaust Centrifugal Airfoil Class 2 Arr 10 With Mixing Box

## geometry (parser evidence)
native form markers: Sweep x3
no freeform markers — native parametric forms only
